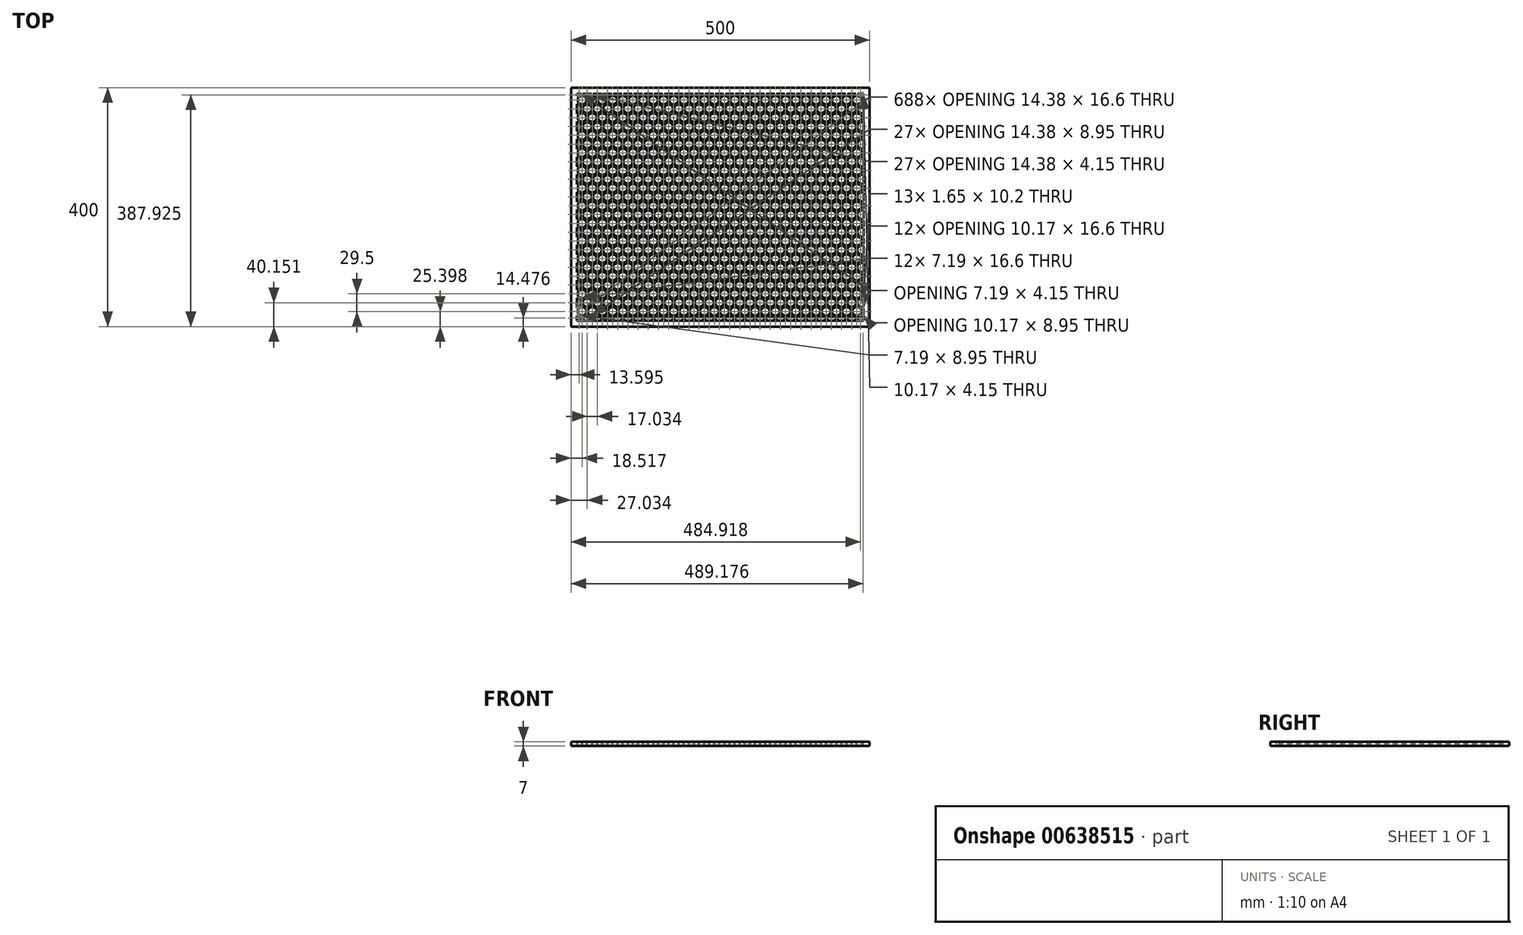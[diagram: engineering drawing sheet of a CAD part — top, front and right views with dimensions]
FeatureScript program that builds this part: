
annotation { "Feature Type Name" : "Feature", "Feature Type Description" : "" }
export const myFeature = defineFeature(function(context is Context, id is Id, definition is map)
    precondition{}
    {
        {
            var Q0;
            Q0=qCreatedBy(makeId("Top.planeOp"),FACE);
            var sketch = newSketch(context, id + "F0", { "sketchPlane" : qUnion([Q0])});
            skLineSegment(sketch, "E0.bottom", {"start": v(0, 0) * mm, "end": v(500, 0) * mm});
            skLineSegment(sketch, "E0.top", {"start": v(0, 400) * mm, "end": v(500, 400) * mm});
            skLineSegment(sketch, "E0.left", {"start": v(0, 0) * mm, "end": v(0, 400) * mm});
            skLineSegment(sketch, "E0.right", {"start": v(500, 0) * mm, "end": v(500, 400) * mm});
            skSolve(sketch);
        }
        {
            var Q0;
            Q0=makeQuery(id+"F0.imprint","IMPRINT",FACE,{"disambiguationData":[TD([[makeQuery(id+"F0.imprint","IMPRINT",EDGE,{"derivedFrom":sQuery(id+"F0.wireOp",EDGE,"E0.bottom")}),1.0]])]});
            extrude(context, id + "F1", {"entities" : qUnion([Q0]), "depth" : 7 * mm, "offsetDistance" : 25 * mm});
        }
        {
            var Q0;
            Q0=makeQuery(id+"F1.opExtrude","CAP_FACE",FACE,{"disambiguationData":[OSD([sQuery(id+"F0.wireOp",EDGE,"E0.bottom"),sQuery(id+"F0.wireOp",EDGE,"E0.top"),sQuery(id+"F0.wireOp",EDGE,"E0.left"),sQuery(id+"F0.wireOp",EDGE,"E0.right")])],"isStart":false});
            var sketch = newSketch(context, id + "F2", { "sketchPlane" : qUnion([Q0])});
            skLineSegment(sketch, "E1.0.5.0", {"start": v(28.36, 375.25) * mm, "end": v(28.36, 383.55) * mm});
            skLineSegment(sketch, "E1.0.5.1", {"start": v(52.58, 387.7) * mm, "end": v(59.77, 383.55) * mm});
            skLineSegment(sketch, "E1.0.5.3", {"start": v(25.7, 383.55) * mm, "end": v(25.7, 375.25) * mm});
            skLineSegment(sketch, "E1.0.5.4", {"start": v(52.58, 371.1) * mm, "end": v(45.4, 375.25) * mm});
            skLineSegment(sketch, "E1.0.5.5", {"start": v(18.52, 371.1) * mm, "end": v(11.33, 375.25) * mm});
            skLineSegment(sketch, "E1.0.5.6", {"start": v(35.55, 387.7) * mm, "end": v(42.74, 383.55) * mm});
            skLineSegment(sketch, "E1.0.5.7", {"start": v(11.33, 375.25) * mm, "end": v(11.33, 383.55) * mm});
            skLineSegment(sketch, "E1.0.5.8", {"start": v(59.77, 383.55) * mm, "end": v(59.77, 375.25) * mm});
            skLineSegment(sketch, "E1.0.5.9", {"start": v(42.74, 375.25) * mm, "end": v(35.55, 371.1) * mm});
            skLineSegment(sketch, "E1.0.5.10", {"start": v(45.4, 375.25) * mm, "end": v(45.4, 383.55) * mm});
            skLineSegment(sketch, "E1.0.5.12", {"start": v(28.36, 383.55) * mm, "end": v(35.55, 387.7) * mm});
            skLineSegment(sketch, "E1.0.5.19", {"start": v(11.33, 383.55) * mm, "end": v(18.52, 387.7) * mm});
            skLineSegment(sketch, "E1.0.5.24", {"start": v(25.7, 375.25) * mm, "end": v(18.52, 371.1) * mm});
            skLineSegment(sketch, "E1.0.5.25", {"start": v(45.4, 383.55) * mm, "end": v(52.58, 387.7) * mm});
            skLineSegment(sketch, "E1.0.5.26", {"start": v(18.52, 387.7) * mm, "end": v(25.7, 383.55) * mm});
            skLineSegment(sketch, "E1.0.5.27", {"start": v(59.77, 375.25) * mm, "end": v(52.58, 371.1) * mm});
            skLineSegment(sketch, "E1.0.5.28", {"start": v(35.55, 371.1) * mm, "end": v(28.36, 375.25) * mm});
            skLineSegment(sketch, "E1.0.5.29", {"start": v(42.74, 383.55) * mm, "end": v(42.74, 375.25) * mm});
            skLineSegment(sketch, "E2", {"start": v(10, 390) * mm, "end": v(10, 10) * mm});
            skLineSegment(sketch, "E3", {"start": v(490, 10) * mm, "end": v(10, 10) * mm});
            skLineSegment(sketch, "E4", {"start": v(490, 390) * mm, "end": v(490, 10) * mm});
            skLineSegment(sketch, "E5.MirrorCS", {"start": v(19.84, 390) * mm, "end": v(27.03, 385.85) * mm});
            skLineSegment(sketch, "E6.MirrorCS", {"start": v(27.03, 385.85) * mm, "end": v(34.22, 390) * mm});
            skLineSegment(sketch, "E7.MirrorCS", {"start": v(19.84, 398.3) * mm, "end": v(19.84, 390) * mm});
            skLineSegment(sketch, "E8.MirrorCS", {"start": v(27.03, 402.45) * mm, "end": v(19.84, 398.3) * mm});
            skLineSegment(sketch, "E9.MirrorCS", {"start": v(34.22, 398.3) * mm, "end": v(27.03, 402.45) * mm});
            skLineSegment(sketch, "E10.MirrorCS", {"start": v(34.22, 390) * mm, "end": v(34.22, 398.3) * mm});
            skLineSegment(sketch, "E11.MirrorCS", {"start": v(17.19, 390) * mm, "end": v(10, 385.85) * mm});
            skLineSegment(sketch, "E12.MirrorCS", {"start": v(17.19, 398.3) * mm, "end": v(17.19, 390) * mm});
            skLineSegment(sketch, "E13.MirrorCS", {"start": v(10, 402.45) * mm, "end": v(17.19, 398.3) * mm});
            skLineSegment(sketch, "E14.MirrorCS", {"start": v(2.81, 398.3) * mm, "end": v(10, 402.45) * mm});
            skLineSegment(sketch, "E15.MirrorCS", {"start": v(2.81, 390) * mm, "end": v(2.81, 398.3) * mm});
            skLineSegment(sketch, "E16.MirrorCS", {"start": v(10, 385.85) * mm, "end": v(2.81, 390) * mm});
            skLineSegment(sketch, "E17.MirrorCS", {"start": v(36.88, 390) * mm, "end": v(44.07, 385.85) * mm});
            skLineSegment(sketch, "E18.MirrorCS", {"start": v(44.07, 385.85) * mm, "end": v(51.26, 390) * mm});
            skLineSegment(sketch, "E19.MirrorCS", {"start": v(51.26, 390) * mm, "end": v(51.26, 398.3) * mm});
            skLineSegment(sketch, "E20.MirrorCS", {"start": v(51.26, 398.3) * mm, "end": v(44.07, 402.45) * mm});
            skLineSegment(sketch, "E21.MirrorCS", {"start": v(44.07, 402.45) * mm, "end": v(36.88, 398.3) * mm});
            skLineSegment(sketch, "E22.MirrorCS", {"start": v(36.88, 398.3) * mm, "end": v(36.88, 390) * mm});
            skLineSegment(sketch, "E23", {"start": v(10, 390) * mm, "end": v(490, 390) * mm});
            skLineSegment(sketch, "E24.1.0.0", {"start": v(61.1, 385.85) * mm, "end": v(53.92, 390) * mm});
            skLineSegment(sketch, "E24.1.0.2", {"start": v(95.18, 385.85) * mm, "end": v(102.37, 390) * mm});
            skLineSegment(sketch, "E24.1.0.3", {"start": v(95.18, 402.45) * mm, "end": v(87.99, 398.3) * mm});
            skLineSegment(sketch, "E24.1.0.4", {"start": v(79.47, 375.25) * mm, "end": v(79.47, 383.55) * mm});
            skLineSegment(sketch, "E24.1.0.5", {"start": v(103.7, 387.7) * mm, "end": v(110.88, 383.55) * mm});
            skLineSegment(sketch, "E24.1.0.8", {"start": v(78.14, 385.85) * mm, "end": v(85.33, 390) * mm});
            skLineSegment(sketch, "E24.1.0.9", {"start": v(61.1, 402.45) * mm, "end": v(68.3, 398.3) * mm});
            skLineSegment(sketch, "E24.1.0.10", {"start": v(79.47, 383.55) * mm, "end": v(86.66, 387.7) * mm});
            skLineSegment(sketch, "E24.1.0.11", {"start": v(110.88, 383.55) * mm, "end": v(110.88, 375.25) * mm});
            skLineSegment(sketch, "E24.1.0.13", {"start": v(87.99, 398.3) * mm, "end": v(87.99, 390) * mm});
            skLineSegment(sketch, "E24.1.0.14", {"start": v(76.82, 375.25) * mm, "end": v(69.63, 371.1) * mm});
            skLineSegment(sketch, "E24.1.0.16", {"start": v(85.33, 398.3) * mm, "end": v(78.14, 402.45) * mm});
            skLineSegment(sketch, "E24.1.0.18", {"start": v(93.85, 375.25) * mm, "end": v(86.66, 371.1) * mm});
            skLineSegment(sketch, "E24.1.0.19", {"start": v(96.5, 375.25) * mm, "end": v(96.5, 383.55) * mm});
            skLineSegment(sketch, "E24.1.0.21", {"start": v(93.85, 383.55) * mm, "end": v(93.85, 375.25) * mm});
            skLineSegment(sketch, "E24.1.0.22", {"start": v(68.3, 398.3) * mm, "end": v(68.3, 390) * mm});
            skLineSegment(sketch, "E24.1.0.25", {"start": v(102.37, 398.3) * mm, "end": v(95.18, 402.45) * mm});
            skLineSegment(sketch, "E24.1.0.26", {"start": v(76.82, 383.55) * mm, "end": v(76.82, 375.25) * mm});
            skLineSegment(sketch, "E24.1.0.27", {"start": v(103.7, 371.1) * mm, "end": v(96.5, 375.25) * mm});
            skLineSegment(sketch, "E24.1.0.28", {"start": v(102.37, 390) * mm, "end": v(102.37, 398.3) * mm});
            skLineSegment(sketch, "E24.1.0.31", {"start": v(86.66, 371.1) * mm, "end": v(79.47, 375.25) * mm});
            skLineSegment(sketch, "E24.1.0.32", {"start": v(62.44, 375.25) * mm, "end": v(62.44, 383.55) * mm});
            skLineSegment(sketch, "E24.1.0.33", {"start": v(69.63, 387.7) * mm, "end": v(76.82, 383.55) * mm});
            skLineSegment(sketch, "E24.1.0.34", {"start": v(78.14, 402.45) * mm, "end": v(70.95, 398.3) * mm});
            skLineSegment(sketch, "E24.1.0.35", {"start": v(85.33, 390) * mm, "end": v(85.33, 398.3) * mm});
            skLineSegment(sketch, "E24.1.0.36", {"start": v(110.88, 375.25) * mm, "end": v(103.7, 371.1) * mm});
            skLineSegment(sketch, "E24.1.0.37", {"start": v(87.99, 390) * mm, "end": v(95.18, 385.85) * mm});
            skLineSegment(sketch, "E24.1.0.41", {"start": v(68.3, 390) * mm, "end": v(61.1, 385.85) * mm});
            skLineSegment(sketch, "E24.1.0.42", {"start": v(53.92, 398.3) * mm, "end": v(61.1, 402.45) * mm});
            skLineSegment(sketch, "E24.1.0.43", {"start": v(70.95, 390) * mm, "end": v(78.14, 385.85) * mm});
            skLineSegment(sketch, "E24.1.0.44", {"start": v(53.92, 390) * mm, "end": v(53.92, 398.3) * mm});
            skLineSegment(sketch, "E24.1.0.46", {"start": v(70.95, 398.3) * mm, "end": v(70.95, 390) * mm});
            skLineSegment(sketch, "E24.1.0.47", {"start": v(96.5, 383.55) * mm, "end": v(103.7, 387.7) * mm});
            skLineSegment(sketch, "E24.1.0.49", {"start": v(69.63, 371.1) * mm, "end": v(62.44, 375.25) * mm});
            skLineSegment(sketch, "E24.1.0.51", {"start": v(86.66, 387.7) * mm, "end": v(93.85, 383.55) * mm});
            skLineSegment(sketch, "E24.1.0.52", {"start": v(62.44, 383.55) * mm, "end": v(69.63, 387.7) * mm});
            skLineSegment(sketch, "E24.2.0.0", {"start": v(112.22, 385.85) * mm, "end": v(105.03, 390) * mm});
            skLineSegment(sketch, "E24.2.0.2", {"start": v(146.29, 385.85) * mm, "end": v(153.48, 390) * mm});
            skLineSegment(sketch, "E24.2.0.3", {"start": v(146.29, 402.45) * mm, "end": v(139.1, 398.3) * mm});
            skLineSegment(sketch, "E24.2.0.4", {"start": v(130.58, 375.25) * mm, "end": v(130.58, 383.55) * mm});
            skLineSegment(sketch, "E24.2.0.5", {"start": v(154.8, 387.7) * mm, "end": v(162, 383.55) * mm});
            skLineSegment(sketch, "E24.2.0.8", {"start": v(129.25, 385.85) * mm, "end": v(136.44, 390) * mm});
            skLineSegment(sketch, "E24.2.0.9", {"start": v(112.22, 402.45) * mm, "end": v(119.4, 398.3) * mm});
            skLineSegment(sketch, "E24.2.0.10", {"start": v(130.58, 383.55) * mm, "end": v(137.77, 387.7) * mm});
            skLineSegment(sketch, "E24.2.0.11", {"start": v(162, 383.55) * mm, "end": v(162, 375.25) * mm});
            skLineSegment(sketch, "E24.2.0.13", {"start": v(139.1, 398.3) * mm, "end": v(139.1, 390) * mm});
            skLineSegment(sketch, "E24.2.0.14", {"start": v(127.93, 375.25) * mm, "end": v(120.74, 371.1) * mm});
            skLineSegment(sketch, "E24.2.0.16", {"start": v(136.44, 398.3) * mm, "end": v(129.25, 402.45) * mm});
            skLineSegment(sketch, "E24.2.0.18", {"start": v(144.96, 375.25) * mm, "end": v(137.77, 371.1) * mm});
            skLineSegment(sketch, "E24.2.0.19", {"start": v(147.62, 375.25) * mm, "end": v(147.62, 383.55) * mm});
            skLineSegment(sketch, "E24.2.0.21", {"start": v(144.96, 383.55) * mm, "end": v(144.96, 375.25) * mm});
            skLineSegment(sketch, "E24.2.0.22", {"start": v(119.4, 398.3) * mm, "end": v(119.4, 390) * mm});
            skLineSegment(sketch, "E24.2.0.25", {"start": v(153.48, 398.3) * mm, "end": v(146.29, 402.45) * mm});
            skLineSegment(sketch, "E24.2.0.26", {"start": v(127.93, 383.55) * mm, "end": v(127.93, 375.25) * mm});
            skLineSegment(sketch, "E24.2.0.27", {"start": v(154.8, 371.1) * mm, "end": v(147.62, 375.25) * mm});
            skLineSegment(sketch, "E24.2.0.28", {"start": v(153.48, 390) * mm, "end": v(153.48, 398.3) * mm});
            skLineSegment(sketch, "E24.2.0.31", {"start": v(137.77, 371.1) * mm, "end": v(130.58, 375.25) * mm});
            skLineSegment(sketch, "E24.2.0.32", {"start": v(113.55, 375.25) * mm, "end": v(113.55, 383.55) * mm});
            skLineSegment(sketch, "E24.2.0.33", {"start": v(120.74, 387.7) * mm, "end": v(127.93, 383.55) * mm});
            skLineSegment(sketch, "E24.2.0.34", {"start": v(129.25, 402.45) * mm, "end": v(122.06, 398.3) * mm});
            skLineSegment(sketch, "E24.2.0.35", {"start": v(136.44, 390) * mm, "end": v(136.44, 398.3) * mm});
            skLineSegment(sketch, "E24.2.0.36", {"start": v(162, 375.25) * mm, "end": v(154.8, 371.1) * mm});
            skLineSegment(sketch, "E24.2.0.37", {"start": v(139.1, 390) * mm, "end": v(146.29, 385.85) * mm});
            skLineSegment(sketch, "E24.2.0.41", {"start": v(119.4, 390) * mm, "end": v(112.22, 385.85) * mm});
            skLineSegment(sketch, "E24.2.0.42", {"start": v(105.03, 398.3) * mm, "end": v(112.22, 402.45) * mm});
            skLineSegment(sketch, "E24.2.0.43", {"start": v(122.06, 390) * mm, "end": v(129.25, 385.85) * mm});
            skLineSegment(sketch, "E24.2.0.44", {"start": v(105.03, 390) * mm, "end": v(105.03, 398.3) * mm});
            skLineSegment(sketch, "E24.2.0.46", {"start": v(122.06, 398.3) * mm, "end": v(122.06, 390) * mm});
            skLineSegment(sketch, "E24.2.0.47", {"start": v(147.62, 383.55) * mm, "end": v(154.8, 387.7) * mm});
            skLineSegment(sketch, "E24.2.0.49", {"start": v(120.74, 371.1) * mm, "end": v(113.55, 375.25) * mm});
            skLineSegment(sketch, "E24.2.0.51", {"start": v(137.77, 387.7) * mm, "end": v(144.96, 383.55) * mm});
            skLineSegment(sketch, "E24.2.0.52", {"start": v(113.55, 383.55) * mm, "end": v(120.74, 387.7) * mm});
            skLineSegment(sketch, "E24.3.0.0", {"start": v(163.33, 385.85) * mm, "end": v(156.14, 390) * mm});
            skLineSegment(sketch, "E24.3.0.2", {"start": v(197.4, 385.85) * mm, "end": v(204.59, 390) * mm});
            skLineSegment(sketch, "E24.3.0.3", {"start": v(197.4, 402.45) * mm, "end": v(190.2, 398.3) * mm});
            skLineSegment(sketch, "E24.3.0.4", {"start": v(181.7, 375.25) * mm, "end": v(181.7, 383.55) * mm});
            skLineSegment(sketch, "E24.3.0.5", {"start": v(205.91, 387.7) * mm, "end": v(213.1, 383.55) * mm});
            skLineSegment(sketch, "E24.3.0.8", {"start": v(180.36, 385.85) * mm, "end": v(187.55, 390) * mm});
            skLineSegment(sketch, "E24.3.0.9", {"start": v(163.33, 402.45) * mm, "end": v(170.52, 398.3) * mm});
            skLineSegment(sketch, "E24.3.0.10", {"start": v(181.7, 383.55) * mm, "end": v(188.88, 387.7) * mm});
            skLineSegment(sketch, "E24.3.0.11", {"start": v(213.1, 383.55) * mm, "end": v(213.1, 375.25) * mm});
            skLineSegment(sketch, "E24.3.0.13", {"start": v(190.2, 398.3) * mm, "end": v(190.2, 390) * mm});
            skLineSegment(sketch, "E24.3.0.14", {"start": v(179.04, 375.25) * mm, "end": v(171.85, 371.1) * mm});
            skLineSegment(sketch, "E24.3.0.16", {"start": v(187.55, 398.3) * mm, "end": v(180.36, 402.45) * mm});
            skLineSegment(sketch, "E24.3.0.18", {"start": v(196.07, 375.25) * mm, "end": v(188.88, 371.1) * mm});
            skLineSegment(sketch, "E24.3.0.19", {"start": v(198.73, 375.25) * mm, "end": v(198.73, 383.55) * mm});
            skLineSegment(sketch, "E24.3.0.21", {"start": v(196.07, 383.55) * mm, "end": v(196.07, 375.25) * mm});
            skLineSegment(sketch, "E24.3.0.22", {"start": v(170.52, 398.3) * mm, "end": v(170.52, 390) * mm});
            skLineSegment(sketch, "E24.3.0.25", {"start": v(204.59, 398.3) * mm, "end": v(197.4, 402.45) * mm});
            skLineSegment(sketch, "E24.3.0.26", {"start": v(179.04, 383.55) * mm, "end": v(179.04, 375.25) * mm});
            skLineSegment(sketch, "E24.3.0.27", {"start": v(205.91, 371.1) * mm, "end": v(198.73, 375.25) * mm});
            skLineSegment(sketch, "E24.3.0.28", {"start": v(204.59, 390) * mm, "end": v(204.59, 398.3) * mm});
            skLineSegment(sketch, "E24.3.0.31", {"start": v(188.88, 371.1) * mm, "end": v(181.7, 375.25) * mm});
            skLineSegment(sketch, "E24.3.0.32", {"start": v(164.66, 375.25) * mm, "end": v(164.66, 383.55) * mm});
            skLineSegment(sketch, "E24.3.0.33", {"start": v(171.85, 387.7) * mm, "end": v(179.04, 383.55) * mm});
            skLineSegment(sketch, "E24.3.0.34", {"start": v(180.36, 402.45) * mm, "end": v(173.17, 398.3) * mm});
            skLineSegment(sketch, "E24.3.0.35", {"start": v(187.55, 390) * mm, "end": v(187.55, 398.3) * mm});
            skLineSegment(sketch, "E24.3.0.36", {"start": v(213.1, 375.25) * mm, "end": v(205.91, 371.1) * mm});
            skLineSegment(sketch, "E24.3.0.37", {"start": v(190.2, 390) * mm, "end": v(197.4, 385.85) * mm});
            skLineSegment(sketch, "E24.3.0.41", {"start": v(170.52, 390) * mm, "end": v(163.33, 385.85) * mm});
            skLineSegment(sketch, "E24.3.0.42", {"start": v(156.14, 398.3) * mm, "end": v(163.33, 402.45) * mm});
            skLineSegment(sketch, "E24.3.0.43", {"start": v(173.17, 390) * mm, "end": v(180.36, 385.85) * mm});
            skLineSegment(sketch, "E24.3.0.44", {"start": v(156.14, 390) * mm, "end": v(156.14, 398.3) * mm});
            skLineSegment(sketch, "E24.3.0.46", {"start": v(173.17, 398.3) * mm, "end": v(173.17, 390) * mm});
            skLineSegment(sketch, "E24.3.0.47", {"start": v(198.73, 383.55) * mm, "end": v(205.91, 387.7) * mm});
            skLineSegment(sketch, "E24.3.0.49", {"start": v(171.85, 371.1) * mm, "end": v(164.66, 375.25) * mm});
            skLineSegment(sketch, "E24.3.0.51", {"start": v(188.88, 387.7) * mm, "end": v(196.07, 383.55) * mm});
            skLineSegment(sketch, "E24.3.0.52", {"start": v(164.66, 383.55) * mm, "end": v(171.85, 387.7) * mm});
            skLineSegment(sketch, "E24.4.0.0", {"start": v(214.44, 385.85) * mm, "end": v(207.25, 390) * mm});
            skLineSegment(sketch, "E24.4.0.2", {"start": v(248.5, 385.85) * mm, "end": v(255.7, 390) * mm});
            skLineSegment(sketch, "E24.4.0.3", {"start": v(248.5, 402.45) * mm, "end": v(241.32, 398.3) * mm});
            skLineSegment(sketch, "E24.4.0.4", {"start": v(232.8, 375.25) * mm, "end": v(232.8, 383.55) * mm});
            skLineSegment(sketch, "E24.4.0.5", {"start": v(257.02, 387.7) * mm, "end": v(264.21, 383.55) * mm});
            skLineSegment(sketch, "E24.4.0.8", {"start": v(231.47, 385.85) * mm, "end": v(238.66, 390) * mm});
            skLineSegment(sketch, "E24.4.0.9", {"start": v(214.44, 402.45) * mm, "end": v(221.63, 398.3) * mm});
            skLineSegment(sketch, "E24.4.0.10", {"start": v(232.8, 383.55) * mm, "end": v(240, 387.7) * mm});
            skLineSegment(sketch, "E24.4.0.11", {"start": v(264.21, 383.55) * mm, "end": v(264.21, 375.25) * mm});
            skLineSegment(sketch, "E24.4.0.13", {"start": v(241.32, 398.3) * mm, "end": v(241.32, 390) * mm});
            skLineSegment(sketch, "E24.4.0.14", {"start": v(230.15, 375.25) * mm, "end": v(222.96, 371.1) * mm});
            skLineSegment(sketch, "E24.4.0.16", {"start": v(238.66, 398.3) * mm, "end": v(231.47, 402.45) * mm});
            skLineSegment(sketch, "E24.4.0.18", {"start": v(247.18, 375.25) * mm, "end": v(240, 371.1) * mm});
            skLineSegment(sketch, "E24.4.0.19", {"start": v(249.84, 375.25) * mm, "end": v(249.84, 383.55) * mm});
            skLineSegment(sketch, "E24.4.0.21", {"start": v(247.18, 383.55) * mm, "end": v(247.18, 375.25) * mm});
            skLineSegment(sketch, "E24.4.0.22", {"start": v(221.63, 398.3) * mm, "end": v(221.63, 390) * mm});
            skLineSegment(sketch, "E24.4.0.25", {"start": v(255.7, 398.3) * mm, "end": v(248.5, 402.45) * mm});
            skLineSegment(sketch, "E24.4.0.26", {"start": v(230.15, 383.55) * mm, "end": v(230.15, 375.25) * mm});
            skLineSegment(sketch, "E24.4.0.27", {"start": v(257.02, 371.1) * mm, "end": v(249.84, 375.25) * mm});
            skLineSegment(sketch, "E24.4.0.28", {"start": v(255.7, 390) * mm, "end": v(255.7, 398.3) * mm});
            skLineSegment(sketch, "E24.4.0.31", {"start": v(240, 371.1) * mm, "end": v(232.8, 375.25) * mm});
            skLineSegment(sketch, "E24.4.0.32", {"start": v(215.77, 375.25) * mm, "end": v(215.77, 383.55) * mm});
            skLineSegment(sketch, "E24.4.0.33", {"start": v(222.96, 387.7) * mm, "end": v(230.15, 383.55) * mm});
            skLineSegment(sketch, "E24.4.0.34", {"start": v(231.47, 402.45) * mm, "end": v(224.28, 398.3) * mm});
            skLineSegment(sketch, "E24.4.0.35", {"start": v(238.66, 390) * mm, "end": v(238.66, 398.3) * mm});
            skLineSegment(sketch, "E24.4.0.36", {"start": v(264.21, 375.25) * mm, "end": v(257.02, 371.1) * mm});
            skLineSegment(sketch, "E24.4.0.37", {"start": v(241.32, 390) * mm, "end": v(248.5, 385.85) * mm});
            skLineSegment(sketch, "E24.4.0.41", {"start": v(221.63, 390) * mm, "end": v(214.44, 385.85) * mm});
            skLineSegment(sketch, "E24.4.0.42", {"start": v(207.25, 398.3) * mm, "end": v(214.44, 402.45) * mm});
            skLineSegment(sketch, "E24.4.0.43", {"start": v(224.28, 390) * mm, "end": v(231.47, 385.85) * mm});
            skLineSegment(sketch, "E24.4.0.44", {"start": v(207.25, 390) * mm, "end": v(207.25, 398.3) * mm});
            skLineSegment(sketch, "E24.4.0.46", {"start": v(224.28, 398.3) * mm, "end": v(224.28, 390) * mm});
            skLineSegment(sketch, "E24.4.0.47", {"start": v(249.84, 383.55) * mm, "end": v(257.02, 387.7) * mm});
            skLineSegment(sketch, "E24.4.0.49", {"start": v(222.96, 371.1) * mm, "end": v(215.77, 375.25) * mm});
            skLineSegment(sketch, "E24.4.0.51", {"start": v(240, 387.7) * mm, "end": v(247.18, 383.55) * mm});
            skLineSegment(sketch, "E24.4.0.52", {"start": v(215.77, 383.55) * mm, "end": v(222.96, 387.7) * mm});
            skLineSegment(sketch, "E24.5.0.0", {"start": v(265.55, 385.85) * mm, "end": v(258.36, 390) * mm});
            skLineSegment(sketch, "E24.5.0.2", {"start": v(299.62, 385.85) * mm, "end": v(306.8, 390) * mm});
            skLineSegment(sketch, "E24.5.0.3", {"start": v(299.62, 402.45) * mm, "end": v(292.43, 398.3) * mm});
            skLineSegment(sketch, "E24.5.0.4", {"start": v(283.91, 375.25) * mm, "end": v(283.91, 383.55) * mm});
            skLineSegment(sketch, "E24.5.0.5", {"start": v(308.13, 387.7) * mm, "end": v(315.32, 383.55) * mm});
            skLineSegment(sketch, "E24.5.0.8", {"start": v(282.58, 385.85) * mm, "end": v(289.77, 390) * mm});
            skLineSegment(sketch, "E24.5.0.9", {"start": v(265.55, 402.45) * mm, "end": v(272.74, 398.3) * mm});
            skLineSegment(sketch, "E24.5.0.10", {"start": v(283.91, 383.55) * mm, "end": v(291.1, 387.7) * mm});
            skLineSegment(sketch, "E24.5.0.11", {"start": v(315.32, 383.55) * mm, "end": v(315.32, 375.25) * mm});
            skLineSegment(sketch, "E24.5.0.13", {"start": v(292.43, 398.3) * mm, "end": v(292.43, 390) * mm});
            skLineSegment(sketch, "E24.5.0.14", {"start": v(281.26, 375.25) * mm, "end": v(274.07, 371.1) * mm});
            skLineSegment(sketch, "E24.5.0.16", {"start": v(289.77, 398.3) * mm, "end": v(282.58, 402.45) * mm});
            skLineSegment(sketch, "E24.5.0.18", {"start": v(298.29, 375.25) * mm, "end": v(291.1, 371.1) * mm});
            skLineSegment(sketch, "E24.5.0.19", {"start": v(300.95, 375.25) * mm, "end": v(300.95, 383.55) * mm});
            skLineSegment(sketch, "E24.5.0.21", {"start": v(298.29, 383.55) * mm, "end": v(298.29, 375.25) * mm});
            skLineSegment(sketch, "E24.5.0.22", {"start": v(272.74, 398.3) * mm, "end": v(272.74, 390) * mm});
            skLineSegment(sketch, "E24.5.0.25", {"start": v(306.8, 398.3) * mm, "end": v(299.62, 402.45) * mm});
            skLineSegment(sketch, "E24.5.0.26", {"start": v(281.26, 383.55) * mm, "end": v(281.26, 375.25) * mm});
            skLineSegment(sketch, "E24.5.0.27", {"start": v(308.13, 371.1) * mm, "end": v(300.95, 375.25) * mm});
            skLineSegment(sketch, "E24.5.0.28", {"start": v(306.8, 390) * mm, "end": v(306.8, 398.3) * mm});
            skLineSegment(sketch, "E24.5.0.31", {"start": v(291.1, 371.1) * mm, "end": v(283.91, 375.25) * mm});
            skLineSegment(sketch, "E24.5.0.32", {"start": v(266.88, 375.25) * mm, "end": v(266.88, 383.55) * mm});
            skLineSegment(sketch, "E24.5.0.33", {"start": v(274.07, 387.7) * mm, "end": v(281.26, 383.55) * mm});
            skLineSegment(sketch, "E24.5.0.34", {"start": v(282.58, 402.45) * mm, "end": v(275.4, 398.3) * mm});
            skLineSegment(sketch, "E24.5.0.35", {"start": v(289.77, 390) * mm, "end": v(289.77, 398.3) * mm});
            skLineSegment(sketch, "E24.5.0.36", {"start": v(315.32, 375.25) * mm, "end": v(308.13, 371.1) * mm});
            skLineSegment(sketch, "E24.5.0.37", {"start": v(292.43, 390) * mm, "end": v(299.62, 385.85) * mm});
            skLineSegment(sketch, "E24.5.0.41", {"start": v(272.74, 390) * mm, "end": v(265.55, 385.85) * mm});
            skLineSegment(sketch, "E24.5.0.42", {"start": v(258.36, 398.3) * mm, "end": v(265.55, 402.45) * mm});
            skLineSegment(sketch, "E24.5.0.43", {"start": v(275.4, 390) * mm, "end": v(282.58, 385.85) * mm});
            skLineSegment(sketch, "E24.5.0.44", {"start": v(258.36, 390) * mm, "end": v(258.36, 398.3) * mm});
            skLineSegment(sketch, "E24.5.0.46", {"start": v(275.4, 398.3) * mm, "end": v(275.4, 390) * mm});
            skLineSegment(sketch, "E24.5.0.47", {"start": v(300.95, 383.55) * mm, "end": v(308.13, 387.7) * mm});
            skLineSegment(sketch, "E24.5.0.49", {"start": v(274.07, 371.1) * mm, "end": v(266.88, 375.25) * mm});
            skLineSegment(sketch, "E24.5.0.51", {"start": v(291.1, 387.7) * mm, "end": v(298.29, 383.55) * mm});
            skLineSegment(sketch, "E24.5.0.52", {"start": v(266.88, 383.55) * mm, "end": v(274.07, 387.7) * mm});
            skLineSegment(sketch, "E24.6.0.0", {"start": v(316.66, 385.85) * mm, "end": v(309.47, 390) * mm});
            skLineSegment(sketch, "E24.6.0.2", {"start": v(350.73, 385.85) * mm, "end": v(357.92, 390) * mm});
            skLineSegment(sketch, "E24.6.0.3", {"start": v(350.73, 402.45) * mm, "end": v(343.54, 398.3) * mm});
            skLineSegment(sketch, "E24.6.0.4", {"start": v(335.02, 375.25) * mm, "end": v(335.02, 383.55) * mm});
            skLineSegment(sketch, "E24.6.0.5", {"start": v(359.24, 387.7) * mm, "end": v(366.43, 383.55) * mm});
            skLineSegment(sketch, "E24.6.0.8", {"start": v(333.7, 385.85) * mm, "end": v(340.88, 390) * mm});
            skLineSegment(sketch, "E24.6.0.9", {"start": v(316.66, 402.45) * mm, "end": v(323.85, 398.3) * mm});
            skLineSegment(sketch, "E24.6.0.10", {"start": v(335.02, 383.55) * mm, "end": v(342.21, 387.7) * mm});
            skLineSegment(sketch, "E24.6.0.11", {"start": v(366.43, 383.55) * mm, "end": v(366.43, 375.25) * mm});
            skLineSegment(sketch, "E24.6.0.13", {"start": v(343.54, 398.3) * mm, "end": v(343.54, 390) * mm});
            skLineSegment(sketch, "E24.6.0.14", {"start": v(332.37, 375.25) * mm, "end": v(325.18, 371.1) * mm});
            skLineSegment(sketch, "E24.6.0.16", {"start": v(340.88, 398.3) * mm, "end": v(333.7, 402.45) * mm});
            skLineSegment(sketch, "E24.6.0.18", {"start": v(349.4, 375.25) * mm, "end": v(342.21, 371.1) * mm});
            skLineSegment(sketch, "E24.6.0.19", {"start": v(352.06, 375.25) * mm, "end": v(352.06, 383.55) * mm});
            skLineSegment(sketch, "E24.6.0.21", {"start": v(349.4, 383.55) * mm, "end": v(349.4, 375.25) * mm});
            skLineSegment(sketch, "E24.6.0.22", {"start": v(323.85, 398.3) * mm, "end": v(323.85, 390) * mm});
            skLineSegment(sketch, "E24.6.0.25", {"start": v(357.92, 398.3) * mm, "end": v(350.73, 402.45) * mm});
            skLineSegment(sketch, "E24.6.0.26", {"start": v(332.37, 383.55) * mm, "end": v(332.37, 375.25) * mm});
            skLineSegment(sketch, "E24.6.0.27", {"start": v(359.24, 371.1) * mm, "end": v(352.06, 375.25) * mm});
            skLineSegment(sketch, "E24.6.0.28", {"start": v(357.92, 390) * mm, "end": v(357.92, 398.3) * mm});
            skLineSegment(sketch, "E24.6.0.31", {"start": v(342.21, 371.1) * mm, "end": v(335.02, 375.25) * mm});
            skLineSegment(sketch, "E24.6.0.32", {"start": v(317.99, 375.25) * mm, "end": v(317.99, 383.55) * mm});
            skLineSegment(sketch, "E24.6.0.33", {"start": v(325.18, 387.7) * mm, "end": v(332.37, 383.55) * mm});
            skLineSegment(sketch, "E24.6.0.34", {"start": v(333.7, 402.45) * mm, "end": v(326.5, 398.3) * mm});
            skLineSegment(sketch, "E24.6.0.35", {"start": v(340.88, 390) * mm, "end": v(340.88, 398.3) * mm});
            skLineSegment(sketch, "E24.6.0.36", {"start": v(366.43, 375.25) * mm, "end": v(359.24, 371.1) * mm});
            skLineSegment(sketch, "E24.6.0.37", {"start": v(343.54, 390) * mm, "end": v(350.73, 385.85) * mm});
            skLineSegment(sketch, "E24.6.0.41", {"start": v(323.85, 390) * mm, "end": v(316.66, 385.85) * mm});
            skLineSegment(sketch, "E24.6.0.42", {"start": v(309.47, 398.3) * mm, "end": v(316.66, 402.45) * mm});
            skLineSegment(sketch, "E24.6.0.43", {"start": v(326.5, 390) * mm, "end": v(333.7, 385.85) * mm});
            skLineSegment(sketch, "E24.6.0.44", {"start": v(309.47, 390) * mm, "end": v(309.47, 398.3) * mm});
            skLineSegment(sketch, "E24.6.0.46", {"start": v(326.5, 398.3) * mm, "end": v(326.5, 390) * mm});
            skLineSegment(sketch, "E24.6.0.47", {"start": v(352.06, 383.55) * mm, "end": v(359.24, 387.7) * mm});
            skLineSegment(sketch, "E24.6.0.49", {"start": v(325.18, 371.1) * mm, "end": v(317.99, 375.25) * mm});
            skLineSegment(sketch, "E24.6.0.51", {"start": v(342.21, 387.7) * mm, "end": v(349.4, 383.55) * mm});
            skLineSegment(sketch, "E24.6.0.52", {"start": v(317.99, 383.55) * mm, "end": v(325.18, 387.7) * mm});
            skLineSegment(sketch, "E24.7.0.0", {"start": v(367.77, 385.85) * mm, "end": v(360.58, 390) * mm});
            skLineSegment(sketch, "E24.7.0.2", {"start": v(401.84, 385.85) * mm, "end": v(409.03, 390) * mm});
            skLineSegment(sketch, "E24.7.0.3", {"start": v(401.84, 402.45) * mm, "end": v(394.65, 398.3) * mm});
            skLineSegment(sketch, "E24.7.0.4", {"start": v(386.13, 375.25) * mm, "end": v(386.13, 383.55) * mm});
            skLineSegment(sketch, "E24.7.0.5", {"start": v(410.35, 387.7) * mm, "end": v(417.54, 383.55) * mm});
            skLineSegment(sketch, "E24.7.0.8", {"start": v(384.8, 385.85) * mm, "end": v(392, 390) * mm});
            skLineSegment(sketch, "E24.7.0.9", {"start": v(367.77, 402.45) * mm, "end": v(374.96, 398.3) * mm});
            skLineSegment(sketch, "E24.7.0.10", {"start": v(386.13, 383.55) * mm, "end": v(393.32, 387.7) * mm});
            skLineSegment(sketch, "E24.7.0.11", {"start": v(417.54, 383.55) * mm, "end": v(417.54, 375.25) * mm});
            skLineSegment(sketch, "E24.7.0.13", {"start": v(394.65, 398.3) * mm, "end": v(394.65, 390) * mm});
            skLineSegment(sketch, "E24.7.0.14", {"start": v(383.48, 375.25) * mm, "end": v(376.29, 371.1) * mm});
            skLineSegment(sketch, "E24.7.0.16", {"start": v(392, 398.3) * mm, "end": v(384.8, 402.45) * mm});
            skLineSegment(sketch, "E24.7.0.18", {"start": v(400.5, 375.25) * mm, "end": v(393.32, 371.1) * mm});
            skLineSegment(sketch, "E24.7.0.19", {"start": v(403.17, 375.25) * mm, "end": v(403.17, 383.55) * mm});
            skLineSegment(sketch, "E24.7.0.21", {"start": v(400.5, 383.55) * mm, "end": v(400.5, 375.25) * mm});
            skLineSegment(sketch, "E24.7.0.22", {"start": v(374.96, 398.3) * mm, "end": v(374.96, 390) * mm});
            skLineSegment(sketch, "E24.7.0.25", {"start": v(409.03, 398.3) * mm, "end": v(401.84, 402.45) * mm});
            skLineSegment(sketch, "E24.7.0.26", {"start": v(383.48, 383.55) * mm, "end": v(383.48, 375.25) * mm});
            skLineSegment(sketch, "E24.7.0.27", {"start": v(410.35, 371.1) * mm, "end": v(403.17, 375.25) * mm});
            skLineSegment(sketch, "E24.7.0.28", {"start": v(409.03, 390) * mm, "end": v(409.03, 398.3) * mm});
            skLineSegment(sketch, "E24.7.0.31", {"start": v(393.32, 371.1) * mm, "end": v(386.13, 375.25) * mm});
            skLineSegment(sketch, "E24.7.0.32", {"start": v(369.1, 375.25) * mm, "end": v(369.1, 383.55) * mm});
            skLineSegment(sketch, "E24.7.0.33", {"start": v(376.29, 387.7) * mm, "end": v(383.48, 383.55) * mm});
            skLineSegment(sketch, "E24.7.0.34", {"start": v(384.8, 402.45) * mm, "end": v(377.61, 398.3) * mm});
            skLineSegment(sketch, "E24.7.0.35", {"start": v(392, 390) * mm, "end": v(392, 398.3) * mm});
            skLineSegment(sketch, "E24.7.0.36", {"start": v(417.54, 375.25) * mm, "end": v(410.35, 371.1) * mm});
            skLineSegment(sketch, "E24.7.0.37", {"start": v(394.65, 390) * mm, "end": v(401.84, 385.85) * mm});
            skLineSegment(sketch, "E24.7.0.41", {"start": v(374.96, 390) * mm, "end": v(367.77, 385.85) * mm});
            skLineSegment(sketch, "E24.7.0.42", {"start": v(360.58, 398.3) * mm, "end": v(367.77, 402.45) * mm});
            skLineSegment(sketch, "E24.7.0.43", {"start": v(377.61, 390) * mm, "end": v(384.8, 385.85) * mm});
            skLineSegment(sketch, "E24.7.0.44", {"start": v(360.58, 390) * mm, "end": v(360.58, 398.3) * mm});
            skLineSegment(sketch, "E24.7.0.46", {"start": v(377.61, 398.3) * mm, "end": v(377.61, 390) * mm});
            skLineSegment(sketch, "E24.7.0.47", {"start": v(403.17, 383.55) * mm, "end": v(410.35, 387.7) * mm});
            skLineSegment(sketch, "E24.7.0.49", {"start": v(376.29, 371.1) * mm, "end": v(369.1, 375.25) * mm});
            skLineSegment(sketch, "E24.7.0.51", {"start": v(393.32, 387.7) * mm, "end": v(400.5, 383.55) * mm});
            skLineSegment(sketch, "E24.7.0.52", {"start": v(369.1, 383.55) * mm, "end": v(376.29, 387.7) * mm});
            skLineSegment(sketch, "E24.8.0.0", {"start": v(418.88, 385.85) * mm, "end": v(411.7, 390) * mm});
            skLineSegment(sketch, "E24.8.0.2", {"start": v(452.95, 385.85) * mm, "end": v(460.14, 390) * mm});
            skLineSegment(sketch, "E24.8.0.3", {"start": v(452.95, 402.45) * mm, "end": v(445.76, 398.3) * mm});
            skLineSegment(sketch, "E24.8.0.4", {"start": v(437.24, 375.25) * mm, "end": v(437.24, 383.55) * mm});
            skLineSegment(sketch, "E24.8.0.5", {"start": v(461.46, 387.7) * mm, "end": v(468.65, 383.55) * mm});
            skLineSegment(sketch, "E24.8.0.8", {"start": v(435.91, 385.85) * mm, "end": v(443.1, 390) * mm});
            skLineSegment(sketch, "E24.8.0.9", {"start": v(418.88, 402.45) * mm, "end": v(426.07, 398.3) * mm});
            skLineSegment(sketch, "E24.8.0.10", {"start": v(437.24, 383.55) * mm, "end": v(444.43, 387.7) * mm});
            skLineSegment(sketch, "E24.8.0.11", {"start": v(468.65, 383.55) * mm, "end": v(468.65, 375.25) * mm});
            skLineSegment(sketch, "E24.8.0.13", {"start": v(445.76, 398.3) * mm, "end": v(445.76, 390) * mm});
            skLineSegment(sketch, "E24.8.0.14", {"start": v(434.59, 375.25) * mm, "end": v(427.4, 371.1) * mm});
            skLineSegment(sketch, "E24.8.0.16", {"start": v(443.1, 398.3) * mm, "end": v(435.91, 402.45) * mm});
            skLineSegment(sketch, "E24.8.0.18", {"start": v(451.62, 375.25) * mm, "end": v(444.43, 371.1) * mm});
            skLineSegment(sketch, "E24.8.0.19", {"start": v(454.28, 375.25) * mm, "end": v(454.28, 383.55) * mm});
            skLineSegment(sketch, "E24.8.0.21", {"start": v(451.62, 383.55) * mm, "end": v(451.62, 375.25) * mm});
            skLineSegment(sketch, "E24.8.0.22", {"start": v(426.07, 398.3) * mm, "end": v(426.07, 390) * mm});
            skLineSegment(sketch, "E24.8.0.25", {"start": v(460.14, 398.3) * mm, "end": v(452.95, 402.45) * mm});
            skLineSegment(sketch, "E24.8.0.26", {"start": v(434.59, 383.55) * mm, "end": v(434.59, 375.25) * mm});
            skLineSegment(sketch, "E24.8.0.27", {"start": v(461.46, 371.1) * mm, "end": v(454.28, 375.25) * mm});
            skLineSegment(sketch, "E24.8.0.28", {"start": v(460.14, 390) * mm, "end": v(460.14, 398.3) * mm});
            skLineSegment(sketch, "E24.8.0.31", {"start": v(444.43, 371.1) * mm, "end": v(437.24, 375.25) * mm});
            skLineSegment(sketch, "E24.8.0.32", {"start": v(420.2, 375.25) * mm, "end": v(420.2, 383.55) * mm});
            skLineSegment(sketch, "E24.8.0.33", {"start": v(427.4, 387.7) * mm, "end": v(434.59, 383.55) * mm});
            skLineSegment(sketch, "E24.8.0.34", {"start": v(435.91, 402.45) * mm, "end": v(428.72, 398.3) * mm});
            skLineSegment(sketch, "E24.8.0.35", {"start": v(443.1, 390) * mm, "end": v(443.1, 398.3) * mm});
            skLineSegment(sketch, "E24.8.0.36", {"start": v(468.65, 375.25) * mm, "end": v(461.46, 371.1) * mm});
            skLineSegment(sketch, "E24.8.0.37", {"start": v(445.76, 390) * mm, "end": v(452.95, 385.85) * mm});
            skLineSegment(sketch, "E24.8.0.41", {"start": v(426.07, 390) * mm, "end": v(418.88, 385.85) * mm});
            skLineSegment(sketch, "E24.8.0.42", {"start": v(411.7, 398.3) * mm, "end": v(418.88, 402.45) * mm});
            skLineSegment(sketch, "E24.8.0.43", {"start": v(428.72, 390) * mm, "end": v(435.91, 385.85) * mm});
            skLineSegment(sketch, "E24.8.0.44", {"start": v(411.7, 390) * mm, "end": v(411.7, 398.3) * mm});
            skLineSegment(sketch, "E24.8.0.46", {"start": v(428.72, 398.3) * mm, "end": v(428.72, 390) * mm});
            skLineSegment(sketch, "E24.8.0.47", {"start": v(454.28, 383.55) * mm, "end": v(461.46, 387.7) * mm});
            skLineSegment(sketch, "E24.8.0.49", {"start": v(427.4, 371.1) * mm, "end": v(420.2, 375.25) * mm});
            skLineSegment(sketch, "E24.8.0.51", {"start": v(444.43, 387.7) * mm, "end": v(451.62, 383.55) * mm});
            skLineSegment(sketch, "E24.8.0.52", {"start": v(420.2, 383.55) * mm, "end": v(427.4, 387.7) * mm});
            skLineSegment(sketch, "E24.9.0.0", {"start": v(469.99, 385.85) * mm, "end": v(462.8, 390) * mm});
            skLineSegment(sketch, "E24.9.0.2", {"start": v(504.06, 385.85) * mm, "end": v(511.25, 390) * mm});
            skLineSegment(sketch, "E24.9.0.3", {"start": v(504.06, 402.45) * mm, "end": v(496.87, 398.3) * mm});
            skLineSegment(sketch, "E24.9.0.4", {"start": v(488.35, 375.25) * mm, "end": v(488.35, 383.55) * mm});
            skLineSegment(sketch, "E24.9.0.5", {"start": v(512.57, 387.7) * mm, "end": v(519.76, 383.55) * mm});
            skLineSegment(sketch, "E24.9.0.8", {"start": v(487.02, 385.85) * mm, "end": v(494.21, 390) * mm});
            skLineSegment(sketch, "E24.9.0.9", {"start": v(469.99, 402.45) * mm, "end": v(477.18, 398.3) * mm});
            skLineSegment(sketch, "E24.9.0.10", {"start": v(488.35, 383.55) * mm, "end": v(495.54, 387.7) * mm});
            skLineSegment(sketch, "E24.9.0.11", {"start": v(519.76, 383.55) * mm, "end": v(519.76, 375.25) * mm});
            skLineSegment(sketch, "E24.9.0.13", {"start": v(496.87, 398.3) * mm, "end": v(496.87, 390) * mm});
            skLineSegment(sketch, "E24.9.0.14", {"start": v(485.7, 375.25) * mm, "end": v(478.5, 371.1) * mm});
            skLineSegment(sketch, "E24.9.0.16", {"start": v(494.21, 398.3) * mm, "end": v(487.02, 402.45) * mm});
            skLineSegment(sketch, "E24.9.0.18", {"start": v(502.73, 375.25) * mm, "end": v(495.54, 371.1) * mm});
            skLineSegment(sketch, "E24.9.0.19", {"start": v(505.39, 375.25) * mm, "end": v(505.39, 383.55) * mm});
            skLineSegment(sketch, "E24.9.0.21", {"start": v(502.73, 383.55) * mm, "end": v(502.73, 375.25) * mm});
            skLineSegment(sketch, "E24.9.0.22", {"start": v(477.18, 398.3) * mm, "end": v(477.18, 390) * mm});
            skLineSegment(sketch, "E24.9.0.25", {"start": v(511.25, 398.3) * mm, "end": v(504.06, 402.45) * mm});
            skLineSegment(sketch, "E24.9.0.26", {"start": v(485.7, 383.55) * mm, "end": v(485.7, 375.25) * mm});
            skLineSegment(sketch, "E24.9.0.27", {"start": v(512.57, 371.1) * mm, "end": v(505.39, 375.25) * mm});
            skLineSegment(sketch, "E24.9.0.28", {"start": v(511.25, 390) * mm, "end": v(511.25, 398.3) * mm});
            skLineSegment(sketch, "E24.9.0.31", {"start": v(495.54, 371.1) * mm, "end": v(488.35, 375.25) * mm});
            skLineSegment(sketch, "E24.9.0.32", {"start": v(471.32, 375.25) * mm, "end": v(471.32, 383.55) * mm});
            skLineSegment(sketch, "E24.9.0.33", {"start": v(478.5, 387.7) * mm, "end": v(485.7, 383.55) * mm});
            skLineSegment(sketch, "E24.9.0.34", {"start": v(487.02, 402.45) * mm, "end": v(479.83, 398.3) * mm});
            skLineSegment(sketch, "E24.9.0.35", {"start": v(494.21, 390) * mm, "end": v(494.21, 398.3) * mm});
            skLineSegment(sketch, "E24.9.0.36", {"start": v(519.76, 375.25) * mm, "end": v(512.57, 371.1) * mm});
            skLineSegment(sketch, "E24.9.0.37", {"start": v(496.87, 390) * mm, "end": v(504.06, 385.85) * mm});
            skLineSegment(sketch, "E24.9.0.41", {"start": v(477.18, 390) * mm, "end": v(469.99, 385.85) * mm});
            skLineSegment(sketch, "E24.9.0.42", {"start": v(462.8, 398.3) * mm, "end": v(469.99, 402.45) * mm});
            skLineSegment(sketch, "E24.9.0.43", {"start": v(479.83, 390) * mm, "end": v(487.02, 385.85) * mm});
            skLineSegment(sketch, "E24.9.0.44", {"start": v(462.8, 390) * mm, "end": v(462.8, 398.3) * mm});
            skLineSegment(sketch, "E24.9.0.46", {"start": v(479.83, 398.3) * mm, "end": v(479.83, 390) * mm});
            skLineSegment(sketch, "E24.9.0.47", {"start": v(505.39, 383.55) * mm, "end": v(512.57, 387.7) * mm});
            skLineSegment(sketch, "E24.9.0.49", {"start": v(478.5, 371.1) * mm, "end": v(471.32, 375.25) * mm});
            skLineSegment(sketch, "E24.9.0.51", {"start": v(495.54, 387.7) * mm, "end": v(502.73, 383.55) * mm});
            skLineSegment(sketch, "E24.9.0.52", {"start": v(471.32, 383.55) * mm, "end": v(478.5, 387.7) * mm});
            skLineSegment(sketch, "E25.0.1.0", {"start": v(332.37, 345.75) * mm, "end": v(325.18, 341.6) * mm});
            skLineSegment(sketch, "E25.0.1.1", {"start": v(511.25, 368.8) * mm, "end": v(504.06, 372.95) * mm});
            skLineSegment(sketch, "E25.0.1.2", {"start": v(2.81, 368.8) * mm, "end": v(10, 372.95) * mm});
            skLineSegment(sketch, "E25.0.1.3", {"start": v(127.93, 345.75) * mm, "end": v(120.74, 341.6) * mm});
            skLineSegment(sketch, "E25.0.1.4", {"start": v(512.57, 341.6) * mm, "end": v(505.39, 345.75) * mm});
            skLineSegment(sketch, "E25.0.1.5", {"start": v(519.76, 345.75) * mm, "end": v(512.57, 341.6) * mm});
            skLineSegment(sketch, "E25.0.1.6", {"start": v(25.7, 345.75) * mm, "end": v(18.52, 341.6) * mm});
            skLineSegment(sketch, "E25.0.1.7", {"start": v(11.33, 345.75) * mm, "end": v(11.33, 354.05) * mm});
            skLineSegment(sketch, "E25.0.1.8", {"start": v(18.52, 341.6) * mm, "end": v(11.33, 345.75) * mm});
            skLineSegment(sketch, "E25.0.1.9", {"start": v(519.76, 354.05) * mm, "end": v(519.76, 345.75) * mm});
            skLineSegment(sketch, "E25.0.1.10", {"start": v(76.82, 345.75) * mm, "end": v(69.63, 341.6) * mm});
            skLineSegment(sketch, "E25.0.1.11", {"start": v(112.22, 372.95) * mm, "end": v(119.4, 368.8) * mm});
            skLineSegment(sketch, "E25.0.1.12", {"start": v(205.91, 341.6) * mm, "end": v(198.73, 345.75) * mm});
            skLineSegment(sketch, "E25.0.1.13", {"start": v(197.4, 372.95) * mm, "end": v(190.2, 368.8) * mm});
            skLineSegment(sketch, "E25.0.1.14", {"start": v(93.85, 345.75) * mm, "end": v(86.66, 341.6) * mm});
            skLineSegment(sketch, "E25.0.1.15", {"start": v(129.25, 372.95) * mm, "end": v(122.06, 368.8) * mm});
            skLineSegment(sketch, "E25.0.1.16", {"start": v(298.29, 345.75) * mm, "end": v(291.1, 341.6) * mm});
            skLineSegment(sketch, "E25.0.1.17", {"start": v(502.73, 345.75) * mm, "end": v(495.54, 341.6) * mm});
            skLineSegment(sketch, "E25.0.1.18", {"start": v(289.77, 368.8) * mm, "end": v(282.58, 372.95) * mm});
            skLineSegment(sketch, "E25.0.1.19", {"start": v(85.33, 368.8) * mm, "end": v(78.14, 372.95) * mm});
            skLineSegment(sketch, "E25.0.1.20", {"start": v(494.21, 368.8) * mm, "end": v(487.02, 372.95) * mm});
            skLineSegment(sketch, "E25.0.1.21", {"start": v(333.7, 372.95) * mm, "end": v(326.5, 368.8) * mm});
            skLineSegment(sketch, "E25.0.1.22", {"start": v(95.18, 372.95) * mm, "end": v(87.99, 368.8) * mm});
            skLineSegment(sketch, "E25.0.1.23", {"start": v(478.5, 341.6) * mm, "end": v(471.32, 345.75) * mm});
            skLineSegment(sketch, "E25.0.1.24", {"start": v(274.07, 341.6) * mm, "end": v(266.88, 345.75) * mm});
            skLineSegment(sketch, "E25.0.1.25", {"start": v(444.43, 341.6) * mm, "end": v(437.24, 345.75) * mm});
            skLineSegment(sketch, "E25.0.1.26", {"start": v(401.84, 372.95) * mm, "end": v(394.65, 368.8) * mm});
            skLineSegment(sketch, "E25.0.1.27", {"start": v(410.35, 341.6) * mm, "end": v(403.17, 345.75) * mm});
            skLineSegment(sketch, "E25.0.1.28", {"start": v(468.65, 345.75) * mm, "end": v(461.46, 341.6) * mm});
            skLineSegment(sketch, "E25.0.1.29", {"start": v(427.4, 341.6) * mm, "end": v(420.2, 345.75) * mm});
            skLineSegment(sketch, "E25.0.1.30", {"start": v(59.77, 345.75) * mm, "end": v(52.58, 341.6) * mm});
            skLineSegment(sketch, "E25.0.1.31", {"start": v(512.57, 358.2) * mm, "end": v(519.76, 354.05) * mm});
            skLineSegment(sketch, "E25.0.1.32", {"start": v(196.07, 345.75) * mm, "end": v(188.88, 341.6) * mm});
            skLineSegment(sketch, "E25.0.1.33", {"start": v(86.66, 341.6) * mm, "end": v(79.47, 345.75) * mm});
            skLineSegment(sketch, "E25.0.1.34", {"start": v(400.5, 345.75) * mm, "end": v(393.32, 341.6) * mm});
            skLineSegment(sketch, "E25.0.1.35", {"start": v(103.7, 341.6) * mm, "end": v(96.5, 345.75) * mm});
            skLineSegment(sketch, "E25.0.1.36", {"start": v(299.62, 372.95) * mm, "end": v(292.43, 368.8) * mm});
            skLineSegment(sketch, "E25.0.1.37", {"start": v(504.06, 372.95) * mm, "end": v(496.87, 368.8) * mm});
            skLineSegment(sketch, "E25.0.1.38", {"start": v(2.81, 360.5) * mm, "end": v(2.81, 368.8) * mm});
            skLineSegment(sketch, "E25.0.1.39", {"start": v(308.13, 341.6) * mm, "end": v(300.95, 345.75) * mm});
            skLineSegment(sketch, "E25.0.1.40", {"start": v(417.54, 345.75) * mm, "end": v(410.35, 341.6) * mm});
            skLineSegment(sketch, "E25.0.1.41", {"start": v(434.59, 345.75) * mm, "end": v(427.4, 341.6) * mm});
            skLineSegment(sketch, "E25.0.1.42", {"start": v(62.44, 345.75) * mm, "end": v(62.44, 354.05) * mm});
            skLineSegment(sketch, "E25.0.1.43", {"start": v(69.63, 341.6) * mm, "end": v(62.44, 345.75) * mm});
            skLineSegment(sketch, "E25.0.1.44", {"start": v(325.18, 341.6) * mm, "end": v(317.99, 345.75) * mm});
            skLineSegment(sketch, "E25.0.1.45", {"start": v(264.21, 345.75) * mm, "end": v(257.02, 341.6) * mm});
            skLineSegment(sketch, "E25.0.1.46", {"start": v(120.74, 341.6) * mm, "end": v(113.55, 345.75) * mm});
            skLineSegment(sketch, "E25.0.1.47", {"start": v(502.73, 354.05) * mm, "end": v(502.73, 345.75) * mm});
            skLineSegment(sketch, "E25.0.1.48", {"start": v(316.66, 372.95) * mm, "end": v(323.85, 368.8) * mm});
            skLineSegment(sketch, "E25.0.1.49", {"start": v(505.39, 345.75) * mm, "end": v(505.39, 354.05) * mm});
            skLineSegment(sketch, "E25.0.1.50", {"start": v(10, 356.35) * mm, "end": v(2.81, 360.5) * mm});
            skLineSegment(sketch, "E25.0.1.51", {"start": v(59.77, 354.05) * mm, "end": v(59.77, 345.75) * mm});
            skLineSegment(sketch, "E25.0.1.52", {"start": v(291.1, 341.6) * mm, "end": v(283.91, 345.75) * mm});
            skLineSegment(sketch, "E25.0.1.53", {"start": v(511.25, 360.5) * mm, "end": v(511.25, 368.8) * mm});
            skLineSegment(sketch, "E25.0.1.54", {"start": v(392, 368.8) * mm, "end": v(384.8, 372.95) * mm});
            skLineSegment(sketch, "E25.0.1.55", {"start": v(187.55, 368.8) * mm, "end": v(180.36, 372.95) * mm});
            skLineSegment(sketch, "E25.0.1.56", {"start": v(247.18, 354.05) * mm, "end": v(247.18, 345.75) * mm});
            skLineSegment(sketch, "E25.0.1.57", {"start": v(188.88, 358.2) * mm, "end": v(196.07, 354.05) * mm});
            skLineSegment(sketch, "E25.0.1.58", {"start": v(369.1, 354.05) * mm, "end": v(376.29, 358.2) * mm});
            skLineSegment(sketch, "E25.0.1.59", {"start": v(409.03, 360.5) * mm, "end": v(409.03, 368.8) * mm});
            skLineSegment(sketch, "E25.0.1.60", {"start": v(188.88, 341.6) * mm, "end": v(181.7, 345.75) * mm});
            skLineSegment(sketch, "E25.0.1.61", {"start": v(204.59, 360.5) * mm, "end": v(204.59, 368.8) * mm});
            skLineSegment(sketch, "E25.0.1.62", {"start": v(164.66, 354.05) * mm, "end": v(171.85, 358.2) * mm});
            skLineSegment(sketch, "E25.0.1.63", {"start": v(230.15, 354.05) * mm, "end": v(230.15, 345.75) * mm});
            skLineSegment(sketch, "E25.0.1.64", {"start": v(343.54, 368.8) * mm, "end": v(343.54, 360.5) * mm});
            skLineSegment(sketch, "E25.0.1.65", {"start": v(139.1, 368.8) * mm, "end": v(139.1, 360.5) * mm});
            skLineSegment(sketch, "E25.0.1.66", {"start": v(70.95, 360.5) * mm, "end": v(78.14, 356.35) * mm});
            skLineSegment(sketch, "E25.0.1.67", {"start": v(96.5, 345.75) * mm, "end": v(96.5, 354.05) * mm});
            skLineSegment(sketch, "E25.0.1.68", {"start": v(44.07, 372.95) * mm, "end": v(36.88, 368.8) * mm});
            skLineSegment(sketch, "E25.0.1.69", {"start": v(162, 345.75) * mm, "end": v(154.8, 341.6) * mm});
            skLineSegment(sketch, "E25.0.1.70", {"start": v(300.95, 345.75) * mm, "end": v(300.95, 354.05) * mm});
            skLineSegment(sketch, "E25.0.1.71", {"start": v(222.96, 341.6) * mm, "end": v(215.77, 345.75) * mm});
            skLineSegment(sketch, "E25.0.1.72", {"start": v(452.95, 356.35) * mm, "end": v(460.14, 360.5) * mm});
            skLineSegment(sketch, "E25.0.1.73", {"start": v(369.1, 345.75) * mm, "end": v(369.1, 354.05) * mm});
            skLineSegment(sketch, "E25.0.1.74", {"start": v(366.43, 345.75) * mm, "end": v(359.24, 341.6) * mm});
            skLineSegment(sketch, "E25.0.1.75", {"start": v(164.66, 345.75) * mm, "end": v(164.66, 354.05) * mm});
            skLineSegment(sketch, "E25.0.1.76", {"start": v(248.5, 356.35) * mm, "end": v(255.7, 360.5) * mm});
            skLineSegment(sketch, "E25.0.1.77", {"start": v(249.84, 354.05) * mm, "end": v(257.02, 358.2) * mm});
            skLineSegment(sketch, "E25.0.1.78", {"start": v(393.32, 341.6) * mm, "end": v(386.13, 345.75) * mm});
            skLineSegment(sketch, "E25.0.1.79", {"start": v(62.44, 354.05) * mm, "end": v(69.63, 358.2) * mm});
            skLineSegment(sketch, "E25.0.1.80", {"start": v(136.44, 360.5) * mm, "end": v(136.44, 368.8) * mm});
            skLineSegment(sketch, "E25.0.1.81", {"start": v(102.37, 360.5) * mm, "end": v(102.37, 368.8) * mm});
            skLineSegment(sketch, "E25.0.1.82", {"start": v(418.88, 372.95) * mm, "end": v(426.07, 368.8) * mm});
            skLineSegment(sketch, "E25.0.1.83", {"start": v(454.28, 354.05) * mm, "end": v(461.46, 358.2) * mm});
            skLineSegment(sketch, "E25.0.1.84", {"start": v(78.14, 372.95) * mm, "end": v(70.95, 368.8) * mm});
            skLineSegment(sketch, "E25.0.1.85", {"start": v(105.03, 360.5) * mm, "end": v(105.03, 368.8) * mm});
            skLineSegment(sketch, "E25.0.1.86", {"start": v(190.2, 360.5) * mm, "end": v(197.4, 356.35) * mm});
            skLineSegment(sketch, "E25.0.1.87", {"start": v(352.06, 345.75) * mm, "end": v(352.06, 354.05) * mm});
            skLineSegment(sketch, "E25.0.1.88", {"start": v(400.5, 354.05) * mm, "end": v(400.5, 345.75) * mm});
            skLineSegment(sketch, "E25.0.1.89", {"start": v(299.62, 356.35) * mm, "end": v(306.8, 360.5) * mm});
            skLineSegment(sketch, "E25.0.1.90", {"start": v(190.2, 368.8) * mm, "end": v(190.2, 360.5) * mm});
            skLineSegment(sketch, "E25.0.1.91", {"start": v(76.82, 354.05) * mm, "end": v(76.82, 345.75) * mm});
            skLineSegment(sketch, "E25.0.1.92", {"start": v(392, 360.5) * mm, "end": v(392, 368.8) * mm});
            skLineSegment(sketch, "E25.0.1.93", {"start": v(309.47, 368.8) * mm, "end": v(316.66, 372.95) * mm});
            skLineSegment(sketch, "E25.0.1.94", {"start": v(349.4, 345.75) * mm, "end": v(342.21, 341.6) * mm});
            skLineSegment(sketch, "E25.0.1.95", {"start": v(257.02, 358.2) * mm, "end": v(264.21, 354.05) * mm});
            skLineSegment(sketch, "E25.0.1.96", {"start": v(61.1, 372.95) * mm, "end": v(68.3, 368.8) * mm});
            skLineSegment(sketch, "E25.0.1.97", {"start": v(146.29, 372.95) * mm, "end": v(139.1, 368.8) * mm});
            skLineSegment(sketch, "E25.0.1.98", {"start": v(154.8, 341.6) * mm, "end": v(147.62, 345.75) * mm});
            skLineSegment(sketch, "E25.0.1.99", {"start": v(306.8, 368.8) * mm, "end": v(299.62, 372.95) * mm});
            skLineSegment(sketch, "E25.0.1.100", {"start": v(87.99, 360.5) * mm, "end": v(95.18, 356.35) * mm});
            skLineSegment(sketch, "E25.0.1.101", {"start": v(105.03, 368.8) * mm, "end": v(112.22, 372.95) * mm});
            skLineSegment(sketch, "E25.0.1.102", {"start": v(102.37, 368.8) * mm, "end": v(95.18, 372.95) * mm});
            skLineSegment(sketch, "E25.0.1.103", {"start": v(187.55, 360.5) * mm, "end": v(187.55, 368.8) * mm});
            skLineSegment(sketch, "E25.0.1.104", {"start": v(61.1, 356.35) * mm, "end": v(53.92, 360.5) * mm});
            skLineSegment(sketch, "E25.0.1.105", {"start": v(437.24, 345.75) * mm, "end": v(437.24, 354.05) * mm});
            skLineSegment(sketch, "E25.0.1.106", {"start": v(393.32, 358.2) * mm, "end": v(400.5, 354.05) * mm});
            skLineSegment(sketch, "E25.0.1.107", {"start": v(232.8, 345.75) * mm, "end": v(232.8, 354.05) * mm});
            skLineSegment(sketch, "E25.0.1.108", {"start": v(87.99, 368.8) * mm, "end": v(87.99, 360.5) * mm});
            skLineSegment(sketch, "E25.0.1.109", {"start": v(113.55, 345.75) * mm, "end": v(113.55, 354.05) * mm});
            skLineSegment(sketch, "E25.0.1.110", {"start": v(332.37, 354.05) * mm, "end": v(332.37, 345.75) * mm});
            skLineSegment(sketch, "E25.0.1.111", {"start": v(266.88, 345.75) * mm, "end": v(266.88, 354.05) * mm});
            skLineSegment(sketch, "E25.0.1.112", {"start": v(180.36, 372.95) * mm, "end": v(173.17, 368.8) * mm});
            skLineSegment(sketch, "E25.0.1.113", {"start": v(181.7, 354.05) * mm, "end": v(188.88, 358.2) * mm});
            skLineSegment(sketch, "E25.0.1.114", {"start": v(68.3, 368.8) * mm, "end": v(68.3, 360.5) * mm});
            skLineSegment(sketch, "E25.0.1.115", {"start": v(317.99, 345.75) * mm, "end": v(317.99, 354.05) * mm});
            skLineSegment(sketch, "E25.0.1.116", {"start": v(485.7, 345.75) * mm, "end": v(478.5, 341.6) * mm});
            skLineSegment(sketch, "E25.0.1.117", {"start": v(10, 372.95) * mm, "end": v(17.19, 368.8) * mm});
            skLineSegment(sketch, "E25.0.1.118", {"start": v(376.29, 341.6) * mm, "end": v(369.1, 345.75) * mm});
            skLineSegment(sketch, "E25.0.1.119", {"start": v(452.95, 372.95) * mm, "end": v(445.76, 368.8) * mm});
            skLineSegment(sketch, "E25.0.1.120", {"start": v(315.32, 345.75) * mm, "end": v(308.13, 341.6) * mm});
            skLineSegment(sketch, "E25.0.1.121", {"start": v(93.85, 354.05) * mm, "end": v(93.85, 345.75) * mm});
            skLineSegment(sketch, "E25.0.1.122", {"start": v(35.55, 341.6) * mm, "end": v(28.36, 345.75) * mm});
            skLineSegment(sketch, "E25.0.1.123", {"start": v(45.4, 345.75) * mm, "end": v(45.4, 354.05) * mm});
            skLineSegment(sketch, "E25.0.1.124", {"start": v(42.74, 345.75) * mm, "end": v(35.55, 341.6) * mm});
            skLineSegment(sketch, "E25.0.1.125", {"start": v(434.59, 354.05) * mm, "end": v(434.59, 345.75) * mm});
            skLineSegment(sketch, "E25.0.1.126", {"start": v(340.88, 360.5) * mm, "end": v(340.88, 368.8) * mm});
            skLineSegment(sketch, "E25.0.1.127", {"start": v(394.65, 360.5) * mm, "end": v(401.84, 356.35) * mm});
            skLineSegment(sketch, "E25.0.1.128", {"start": v(153.48, 368.8) * mm, "end": v(146.29, 372.95) * mm});
            skLineSegment(sketch, "E25.0.1.129", {"start": v(52.58, 341.6) * mm, "end": v(45.4, 345.75) * mm});
            skLineSegment(sketch, "E25.0.1.130", {"start": v(25.7, 354.05) * mm, "end": v(25.7, 345.75) * mm});
            skLineSegment(sketch, "E25.0.1.131", {"start": v(28.36, 345.75) * mm, "end": v(28.36, 354.05) * mm});
            skLineSegment(sketch, "E25.0.1.132", {"start": v(45.4, 354.05) * mm, "end": v(52.58, 358.2) * mm});
            skLineSegment(sketch, "E25.0.1.133", {"start": v(451.62, 345.75) * mm, "end": v(444.43, 341.6) * mm});
            skLineSegment(sketch, "E25.0.1.134", {"start": v(411.7, 360.5) * mm, "end": v(411.7, 368.8) * mm});
            skLineSegment(sketch, "E25.0.1.135", {"start": v(342.21, 341.6) * mm, "end": v(335.02, 345.75) * mm});
            skLineSegment(sketch, "E25.0.1.136", {"start": v(443.1, 360.5) * mm, "end": v(443.1, 368.8) * mm});
            skLineSegment(sketch, "E25.0.1.137", {"start": v(357.92, 368.8) * mm, "end": v(350.73, 372.95) * mm});
            skLineSegment(sketch, "E25.0.1.138", {"start": v(289.77, 360.5) * mm, "end": v(289.77, 368.8) * mm});
            skLineSegment(sketch, "E25.0.1.139", {"start": v(204.59, 368.8) * mm, "end": v(197.4, 372.95) * mm});
            skLineSegment(sketch, "E25.0.1.140", {"start": v(198.73, 354.05) * mm, "end": v(205.91, 358.2) * mm});
            skLineSegment(sketch, "E25.0.1.141", {"start": v(454.28, 345.75) * mm, "end": v(454.28, 354.05) * mm});
            skLineSegment(sketch, "E25.0.1.142", {"start": v(86.66, 358.2) * mm, "end": v(93.85, 354.05) * mm});
            skLineSegment(sketch, "E25.0.1.143", {"start": v(443.1, 368.8) * mm, "end": v(435.91, 372.95) * mm});
            skLineSegment(sketch, "E25.0.1.144", {"start": v(435.91, 372.95) * mm, "end": v(428.72, 368.8) * mm});
            skLineSegment(sketch, "E25.0.1.145", {"start": v(437.24, 354.05) * mm, "end": v(444.43, 358.2) * mm});
            skLineSegment(sketch, "E25.0.1.146", {"start": v(231.47, 372.95) * mm, "end": v(224.28, 368.8) * mm});
            skLineSegment(sketch, "E25.0.1.147", {"start": v(79.47, 345.75) * mm, "end": v(79.47, 354.05) * mm});
            skLineSegment(sketch, "E25.0.1.148", {"start": v(309.47, 360.5) * mm, "end": v(309.47, 368.8) * mm});
            skLineSegment(sketch, "E25.0.1.149", {"start": v(214.44, 372.95) * mm, "end": v(221.63, 368.8) * mm});
            skLineSegment(sketch, "E25.0.1.150", {"start": v(238.66, 368.8) * mm, "end": v(231.47, 372.95) * mm});
            skLineSegment(sketch, "E25.0.1.151", {"start": v(394.65, 368.8) * mm, "end": v(394.65, 360.5) * mm});
            skLineSegment(sketch, "E25.0.1.152", {"start": v(445.76, 360.5) * mm, "end": v(452.95, 356.35) * mm});
            skLineSegment(sketch, "E25.0.1.153", {"start": v(241.32, 360.5) * mm, "end": v(248.5, 356.35) * mm});
            skLineSegment(sketch, "E25.0.1.154", {"start": v(231.47, 356.35) * mm, "end": v(238.66, 360.5) * mm});
            skLineSegment(sketch, "E25.0.1.155", {"start": v(79.47, 354.05) * mm, "end": v(86.66, 358.2) * mm});
            skLineSegment(sketch, "E25.0.1.156", {"start": v(350.73, 372.95) * mm, "end": v(343.54, 368.8) * mm});
            skLineSegment(sketch, "E25.0.1.157", {"start": v(196.07, 354.05) * mm, "end": v(196.07, 345.75) * mm});
            skLineSegment(sketch, "E25.0.1.158", {"start": v(240, 341.6) * mm, "end": v(232.8, 345.75) * mm});
            skLineSegment(sketch, "E25.0.1.159", {"start": v(69.63, 358.2) * mm, "end": v(76.82, 354.05) * mm});
            skLineSegment(sketch, "E25.0.1.160", {"start": v(349.4, 354.05) * mm, "end": v(349.4, 345.75) * mm});
            skLineSegment(sketch, "E25.0.1.161", {"start": v(383.48, 345.75) * mm, "end": v(376.29, 341.6) * mm});
            skLineSegment(sketch, "E25.0.1.162", {"start": v(144.96, 354.05) * mm, "end": v(144.96, 345.75) * mm});
            skLineSegment(sketch, "E25.0.1.163", {"start": v(179.04, 345.75) * mm, "end": v(171.85, 341.6) * mm});
            skLineSegment(sketch, "E25.0.1.164", {"start": v(386.13, 354.05) * mm, "end": v(393.32, 358.2) * mm});
            skLineSegment(sketch, "E25.0.1.165", {"start": v(435.91, 356.35) * mm, "end": v(443.1, 360.5) * mm});
            skLineSegment(sketch, "E25.0.1.166", {"start": v(504.06, 356.35) * mm, "end": v(511.25, 360.5) * mm});
            skLineSegment(sketch, "E25.0.1.167", {"start": v(403.17, 345.75) * mm, "end": v(403.17, 354.05) * mm});
            skLineSegment(sketch, "E25.0.1.168", {"start": v(241.32, 368.8) * mm, "end": v(241.32, 360.5) * mm});
            skLineSegment(sketch, "E25.0.1.169", {"start": v(359.24, 341.6) * mm, "end": v(352.06, 345.75) * mm});
            skLineSegment(sketch, "E25.0.1.170", {"start": v(213.1, 345.75) * mm, "end": v(205.91, 341.6) * mm});
            skLineSegment(sketch, "E25.0.1.171", {"start": v(34.22, 368.8) * mm, "end": v(27.03, 372.95) * mm});
            skLineSegment(sketch, "E25.0.1.172", {"start": v(461.46, 358.2) * mm, "end": v(468.65, 354.05) * mm});
            skLineSegment(sketch, "E25.0.1.173", {"start": v(505.39, 354.05) * mm, "end": v(512.57, 358.2) * mm});
            skLineSegment(sketch, "E25.0.1.174", {"start": v(300.95, 354.05) * mm, "end": v(308.13, 358.2) * mm});
            skLineSegment(sketch, "E25.0.1.175", {"start": v(230.15, 345.75) * mm, "end": v(222.96, 341.6) * mm});
            skLineSegment(sketch, "E25.0.1.176", {"start": v(265.55, 356.35) * mm, "end": v(258.36, 360.5) * mm});
            skLineSegment(sketch, "E25.0.1.177", {"start": v(144.96, 345.75) * mm, "end": v(137.77, 341.6) * mm});
            skLineSegment(sketch, "E25.0.1.178", {"start": v(27.03, 372.95) * mm, "end": v(19.84, 368.8) * mm});
            skLineSegment(sketch, "E25.0.1.179", {"start": v(384.8, 372.95) * mm, "end": v(377.61, 368.8) * mm});
            skLineSegment(sketch, "E25.0.1.180", {"start": v(340.88, 368.8) * mm, "end": v(333.7, 372.95) * mm});
            skLineSegment(sketch, "E25.0.1.181", {"start": v(136.44, 368.8) * mm, "end": v(129.25, 372.95) * mm});
            skLineSegment(sketch, "E25.0.1.182", {"start": v(198.73, 345.75) * mm, "end": v(198.73, 354.05) * mm});
            skLineSegment(sketch, "E25.0.1.183", {"start": v(70.95, 368.8) * mm, "end": v(70.95, 360.5) * mm});
            skLineSegment(sketch, "E25.0.1.184", {"start": v(127.93, 354.05) * mm, "end": v(127.93, 345.75) * mm});
            skLineSegment(sketch, "E25.0.1.185", {"start": v(461.46, 341.6) * mm, "end": v(454.28, 345.75) * mm});
            skLineSegment(sketch, "E25.0.1.186", {"start": v(444.43, 358.2) * mm, "end": v(451.62, 354.05) * mm});
            skLineSegment(sketch, "E25.0.1.187", {"start": v(445.76, 368.8) * mm, "end": v(445.76, 360.5) * mm});
            skLineSegment(sketch, "E25.0.1.188", {"start": v(240, 358.2) * mm, "end": v(247.18, 354.05) * mm});
            skLineSegment(sketch, "E25.0.1.189", {"start": v(298.29, 354.05) * mm, "end": v(298.29, 345.75) * mm});
            skLineSegment(sketch, "E25.0.1.190", {"start": v(471.32, 345.75) * mm, "end": v(471.32, 354.05) * mm});
            skLineSegment(sketch, "E25.0.1.191", {"start": v(207.25, 360.5) * mm, "end": v(207.25, 368.8) * mm});
            skLineSegment(sketch, "E25.0.1.192", {"start": v(281.26, 345.75) * mm, "end": v(274.07, 341.6) * mm});
            skLineSegment(sketch, "E25.0.1.193", {"start": v(257.02, 341.6) * mm, "end": v(249.84, 345.75) * mm});
            skLineSegment(sketch, "E25.0.1.194", {"start": v(248.5, 372.95) * mm, "end": v(241.32, 368.8) * mm});
            skLineSegment(sketch, "E25.0.1.195", {"start": v(451.62, 354.05) * mm, "end": v(451.62, 345.75) * mm});
            skLineSegment(sketch, "E25.0.1.196", {"start": v(110.88, 345.75) * mm, "end": v(103.7, 341.6) * mm});
            skLineSegment(sketch, "E25.0.1.197", {"start": v(401.84, 356.35) * mm, "end": v(409.03, 360.5) * mm});
            skLineSegment(sketch, "E25.0.1.198", {"start": v(292.43, 368.8) * mm, "end": v(292.43, 360.5) * mm});
            skLineSegment(sketch, "E25.0.1.199", {"start": v(171.85, 341.6) * mm, "end": v(164.66, 345.75) * mm});
            skLineSegment(sketch, "E25.0.1.200", {"start": v(197.4, 356.35) * mm, "end": v(204.59, 360.5) * mm});
            skLineSegment(sketch, "E25.0.1.201", {"start": v(52.58, 358.2) * mm, "end": v(59.77, 354.05) * mm});
            skLineSegment(sketch, "E25.0.1.202", {"start": v(411.7, 368.8) * mm, "end": v(418.88, 372.95) * mm});
            skLineSegment(sketch, "E25.0.1.203", {"start": v(409.03, 368.8) * mm, "end": v(401.84, 372.95) * mm});
            skLineSegment(sketch, "E25.0.1.204", {"start": v(207.25, 368.8) * mm, "end": v(214.44, 372.95) * mm});
            skLineSegment(sketch, "E25.0.1.205", {"start": v(403.17, 354.05) * mm, "end": v(410.35, 358.2) * mm});
            skLineSegment(sketch, "E25.0.1.206", {"start": v(495.54, 341.6) * mm, "end": v(488.35, 345.75) * mm});
            skLineSegment(sketch, "E25.0.1.207", {"start": v(468.65, 354.05) * mm, "end": v(468.65, 345.75) * mm});
            skLineSegment(sketch, "E25.0.1.208", {"start": v(264.21, 354.05) * mm, "end": v(264.21, 345.75) * mm});
            skLineSegment(sketch, "E25.0.1.209", {"start": v(238.66, 360.5) * mm, "end": v(238.66, 368.8) * mm});
            skLineSegment(sketch, "E25.0.1.210", {"start": v(247.18, 345.75) * mm, "end": v(240, 341.6) * mm});
            skLineSegment(sketch, "E25.0.1.211", {"start": v(85.33, 360.5) * mm, "end": v(85.33, 368.8) * mm});
            skLineSegment(sketch, "E25.0.1.212", {"start": v(137.77, 341.6) * mm, "end": v(130.58, 345.75) * mm});
            skLineSegment(sketch, "E25.0.1.213", {"start": v(374.96, 360.5) * mm, "end": v(367.77, 356.35) * mm});
            skLineSegment(sketch, "E25.0.1.214", {"start": v(323.85, 368.8) * mm, "end": v(323.85, 360.5) * mm});
            skLineSegment(sketch, "E25.0.1.215", {"start": v(266.88, 354.05) * mm, "end": v(274.07, 358.2) * mm});
            skLineSegment(sketch, "E25.0.1.216", {"start": v(326.5, 368.8) * mm, "end": v(326.5, 360.5) * mm});
            skLineSegment(sketch, "E25.0.1.217", {"start": v(232.8, 354.05) * mm, "end": v(240, 358.2) * mm});
            skLineSegment(sketch, "E25.0.1.218", {"start": v(306.8, 360.5) * mm, "end": v(306.8, 368.8) * mm});
            skLineSegment(sketch, "E25.0.1.219", {"start": v(119.4, 368.8) * mm, "end": v(119.4, 360.5) * mm});
            skLineSegment(sketch, "E25.0.1.220", {"start": v(122.06, 368.8) * mm, "end": v(122.06, 360.5) * mm});
            skLineSegment(sketch, "E25.0.1.221", {"start": v(170.52, 360.5) * mm, "end": v(163.33, 356.35) * mm});
            skLineSegment(sketch, "E25.0.1.222", {"start": v(428.72, 368.8) * mm, "end": v(428.72, 360.5) * mm});
            skLineSegment(sketch, "E25.0.1.223", {"start": v(51.26, 360.5) * mm, "end": v(51.26, 368.8) * mm});
            skLineSegment(sketch, "E25.0.1.224", {"start": v(386.13, 345.75) * mm, "end": v(386.13, 354.05) * mm});
            skLineSegment(sketch, "E25.0.1.225", {"start": v(44.07, 356.35) * mm, "end": v(51.26, 360.5) * mm});
            skLineSegment(sketch, "E25.0.1.226", {"start": v(462.8, 368.8) * mm, "end": v(469.99, 372.95) * mm});
            skLineSegment(sketch, "E25.0.1.227", {"start": v(214.44, 356.35) * mm, "end": v(207.25, 360.5) * mm});
            skLineSegment(sketch, "E25.0.1.228", {"start": v(205.91, 358.2) * mm, "end": v(213.1, 354.05) * mm});
            skLineSegment(sketch, "E25.0.1.229", {"start": v(366.43, 354.05) * mm, "end": v(366.43, 345.75) * mm});
            skLineSegment(sketch, "E25.0.1.230", {"start": v(130.58, 354.05) * mm, "end": v(137.77, 358.2) * mm});
            skLineSegment(sketch, "E25.0.1.231", {"start": v(224.28, 368.8) * mm, "end": v(224.28, 360.5) * mm});
            skLineSegment(sketch, "E25.0.1.232", {"start": v(384.8, 356.35) * mm, "end": v(392, 360.5) * mm});
            skLineSegment(sketch, "E25.0.1.233", {"start": v(275.4, 360.5) * mm, "end": v(282.58, 356.35) * mm});
            skLineSegment(sketch, "E25.0.1.234", {"start": v(19.84, 360.5) * mm, "end": v(27.03, 356.35) * mm});
            skLineSegment(sketch, "E25.0.1.235", {"start": v(180.36, 356.35) * mm, "end": v(187.55, 360.5) * mm});
            skLineSegment(sketch, "E25.0.1.236", {"start": v(410.35, 358.2) * mm, "end": v(417.54, 354.05) * mm});
            skLineSegment(sketch, "E25.0.1.237", {"start": v(255.7, 368.8) * mm, "end": v(248.5, 372.95) * mm});
            skLineSegment(sketch, "E25.0.1.238", {"start": v(53.92, 368.8) * mm, "end": v(61.1, 372.95) * mm});
            skLineSegment(sketch, "E25.0.1.239", {"start": v(162, 354.05) * mm, "end": v(162, 345.75) * mm});
            skLineSegment(sketch, "E25.0.1.240", {"start": v(51.26, 368.8) * mm, "end": v(44.07, 372.95) * mm});
            skLineSegment(sketch, "E25.0.1.241", {"start": v(427.4, 358.2) * mm, "end": v(434.59, 354.05) * mm});
            skLineSegment(sketch, "E25.0.1.242", {"start": v(460.14, 368.8) * mm, "end": v(452.95, 372.95) * mm});
            skLineSegment(sketch, "E25.0.1.243", {"start": v(272.74, 360.5) * mm, "end": v(265.55, 356.35) * mm});
            skLineSegment(sketch, "E25.0.1.244", {"start": v(181.7, 345.75) * mm, "end": v(181.7, 354.05) * mm});
            skLineSegment(sketch, "E25.0.1.245", {"start": v(335.02, 354.05) * mm, "end": v(342.21, 358.2) * mm});
            skLineSegment(sketch, "E25.0.1.246", {"start": v(221.63, 368.8) * mm, "end": v(221.63, 360.5) * mm});
            skLineSegment(sketch, "E25.0.1.247", {"start": v(68.3, 360.5) * mm, "end": v(61.1, 356.35) * mm});
            skLineSegment(sketch, "E25.0.1.248", {"start": v(130.58, 345.75) * mm, "end": v(130.58, 354.05) * mm});
            skLineSegment(sketch, "E25.0.1.249", {"start": v(477.18, 360.5) * mm, "end": v(469.99, 356.35) * mm});
            skLineSegment(sketch, "E25.0.1.250", {"start": v(469.99, 372.95) * mm, "end": v(477.18, 368.8) * mm});
            skLineSegment(sketch, "E25.0.1.251", {"start": v(360.58, 360.5) * mm, "end": v(360.58, 368.8) * mm});
            skLineSegment(sketch, "E25.0.1.252", {"start": v(122.06, 360.5) * mm, "end": v(129.25, 356.35) * mm});
            skLineSegment(sketch, "E25.0.1.253", {"start": v(95.18, 356.35) * mm, "end": v(102.37, 360.5) * mm});
            skLineSegment(sketch, "E25.0.1.254", {"start": v(137.77, 358.2) * mm, "end": v(144.96, 354.05) * mm});
            skLineSegment(sketch, "E25.0.1.255", {"start": v(469.99, 356.35) * mm, "end": v(462.8, 360.5) * mm});
            skLineSegment(sketch, "E25.0.1.256", {"start": v(417.54, 354.05) * mm, "end": v(417.54, 345.75) * mm});
            skLineSegment(sketch, "E25.0.1.257", {"start": v(120.74, 358.2) * mm, "end": v(127.93, 354.05) * mm});
            skLineSegment(sketch, "E25.0.1.258", {"start": v(477.18, 368.8) * mm, "end": v(477.18, 360.5) * mm});
            skLineSegment(sketch, "E25.0.1.259", {"start": v(420.2, 354.05) * mm, "end": v(427.4, 358.2) * mm});
            skLineSegment(sketch, "E25.0.1.260", {"start": v(275.4, 368.8) * mm, "end": v(275.4, 360.5) * mm});
            skLineSegment(sketch, "E25.0.1.261", {"start": v(255.7, 360.5) * mm, "end": v(255.7, 368.8) * mm});
            skLineSegment(sketch, "E25.0.1.262", {"start": v(215.77, 354.05) * mm, "end": v(222.96, 358.2) * mm});
            skLineSegment(sketch, "E25.0.1.263", {"start": v(42.74, 354.05) * mm, "end": v(42.74, 345.75) * mm});
            skLineSegment(sketch, "E25.0.1.264", {"start": v(350.73, 356.35) * mm, "end": v(357.92, 360.5) * mm});
            skLineSegment(sketch, "E25.0.1.265", {"start": v(78.14, 356.35) * mm, "end": v(85.33, 360.5) * mm});
            skLineSegment(sketch, "E25.0.1.266", {"start": v(119.4, 360.5) * mm, "end": v(112.22, 356.35) * mm});
            skLineSegment(sketch, "E25.0.1.267", {"start": v(19.84, 368.8) * mm, "end": v(19.84, 360.5) * mm});
            skLineSegment(sketch, "E25.0.1.268", {"start": v(496.87, 360.5) * mm, "end": v(504.06, 356.35) * mm});
            skLineSegment(sketch, "E25.0.1.269", {"start": v(325.18, 358.2) * mm, "end": v(332.37, 354.05) * mm});
            skLineSegment(sketch, "E25.0.1.270", {"start": v(367.77, 372.95) * mm, "end": v(374.96, 368.8) * mm});
            skLineSegment(sketch, "E25.0.1.271", {"start": v(258.36, 360.5) * mm, "end": v(258.36, 368.8) * mm});
            skLineSegment(sketch, "E25.0.1.272", {"start": v(163.33, 372.95) * mm, "end": v(170.52, 368.8) * mm});
            skLineSegment(sketch, "E25.0.1.273", {"start": v(179.04, 354.05) * mm, "end": v(179.04, 345.75) * mm});
            skLineSegment(sketch, "E25.0.1.274", {"start": v(249.84, 345.75) * mm, "end": v(249.84, 354.05) * mm});
            skLineSegment(sketch, "E25.0.1.275", {"start": v(139.1, 360.5) * mm, "end": v(146.29, 356.35) * mm});
            skLineSegment(sketch, "E25.0.1.276", {"start": v(418.88, 356.35) * mm, "end": v(411.7, 360.5) * mm});
            skLineSegment(sketch, "E25.0.1.277", {"start": v(426.07, 368.8) * mm, "end": v(426.07, 360.5) * mm});
            skLineSegment(sketch, "E25.0.1.278", {"start": v(367.77, 356.35) * mm, "end": v(360.58, 360.5) * mm});
            skLineSegment(sketch, "E25.0.1.279", {"start": v(352.06, 354.05) * mm, "end": v(359.24, 358.2) * mm});
            skLineSegment(sketch, "E25.0.1.280", {"start": v(163.33, 356.35) * mm, "end": v(156.14, 360.5) * mm});
            skLineSegment(sketch, "E25.0.1.281", {"start": v(112.22, 356.35) * mm, "end": v(105.03, 360.5) * mm});
            skLineSegment(sketch, "E25.0.1.282", {"start": v(487.02, 372.95) * mm, "end": v(479.83, 368.8) * mm});
            skLineSegment(sketch, "E25.0.1.283", {"start": v(374.96, 368.8) * mm, "end": v(374.96, 360.5) * mm});
            skLineSegment(sketch, "E25.0.1.284", {"start": v(17.19, 360.5) * mm, "end": v(10, 356.35) * mm});
            skLineSegment(sketch, "E25.0.1.285", {"start": v(221.63, 360.5) * mm, "end": v(214.44, 356.35) * mm});
            skLineSegment(sketch, "E25.0.1.286", {"start": v(282.58, 372.95) * mm, "end": v(275.4, 368.8) * mm});
            skLineSegment(sketch, "E25.0.1.287", {"start": v(335.02, 345.75) * mm, "end": v(335.02, 354.05) * mm});
            skLineSegment(sketch, "E25.0.1.288", {"start": v(170.52, 368.8) * mm, "end": v(170.52, 360.5) * mm});
            skLineSegment(sketch, "E25.0.1.289", {"start": v(291.1, 358.2) * mm, "end": v(298.29, 354.05) * mm});
            skLineSegment(sketch, "E25.0.1.290", {"start": v(173.17, 368.8) * mm, "end": v(173.17, 360.5) * mm});
            skLineSegment(sketch, "E25.0.1.291", {"start": v(495.54, 358.2) * mm, "end": v(502.73, 354.05) * mm});
            skLineSegment(sketch, "E25.0.1.292", {"start": v(147.62, 345.75) * mm, "end": v(147.62, 354.05) * mm});
            skLineSegment(sketch, "E25.0.1.293", {"start": v(153.48, 360.5) * mm, "end": v(153.48, 368.8) * mm});
            skLineSegment(sketch, "E25.0.1.294", {"start": v(222.96, 358.2) * mm, "end": v(230.15, 354.05) * mm});
            skLineSegment(sketch, "E25.0.1.295", {"start": v(479.83, 368.8) * mm, "end": v(479.83, 360.5) * mm});
            skLineSegment(sketch, "E25.0.1.296", {"start": v(420.2, 345.75) * mm, "end": v(420.2, 354.05) * mm});
            skLineSegment(sketch, "E25.0.1.297", {"start": v(326.5, 360.5) * mm, "end": v(333.7, 356.35) * mm});
            skLineSegment(sketch, "E25.0.1.298", {"start": v(173.17, 360.5) * mm, "end": v(180.36, 356.35) * mm});
            skLineSegment(sketch, "E25.0.1.299", {"start": v(342.21, 358.2) * mm, "end": v(349.4, 354.05) * mm});
            skLineSegment(sketch, "E25.0.1.300", {"start": v(265.55, 372.95) * mm, "end": v(272.74, 368.8) * mm});
            skLineSegment(sketch, "E25.0.1.301", {"start": v(274.07, 358.2) * mm, "end": v(281.26, 354.05) * mm});
            skLineSegment(sketch, "E25.0.1.302", {"start": v(215.77, 345.75) * mm, "end": v(215.77, 354.05) * mm});
            skLineSegment(sketch, "E25.0.1.303", {"start": v(462.8, 360.5) * mm, "end": v(462.8, 368.8) * mm});
            skLineSegment(sketch, "E25.0.1.304", {"start": v(281.26, 354.05) * mm, "end": v(281.26, 345.75) * mm});
            skLineSegment(sketch, "E25.0.1.305", {"start": v(156.14, 360.5) * mm, "end": v(156.14, 368.8) * mm});
            skLineSegment(sketch, "E25.0.1.306", {"start": v(213.1, 354.05) * mm, "end": v(213.1, 345.75) * mm});
            skLineSegment(sketch, "E25.0.1.307", {"start": v(96.5, 354.05) * mm, "end": v(103.7, 358.2) * mm});
            skLineSegment(sketch, "E25.0.1.308", {"start": v(460.14, 360.5) * mm, "end": v(460.14, 368.8) * mm});
            skLineSegment(sketch, "E25.0.1.309", {"start": v(323.85, 360.5) * mm, "end": v(316.66, 356.35) * mm});
            skLineSegment(sketch, "E25.0.1.310", {"start": v(272.74, 368.8) * mm, "end": v(272.74, 360.5) * mm});
            skLineSegment(sketch, "E25.0.1.311", {"start": v(377.61, 360.5) * mm, "end": v(384.8, 356.35) * mm});
            skLineSegment(sketch, "E25.0.1.312", {"start": v(282.58, 356.35) * mm, "end": v(289.77, 360.5) * mm});
            skLineSegment(sketch, "E25.0.1.313", {"start": v(146.29, 356.35) * mm, "end": v(153.48, 360.5) * mm});
            skLineSegment(sketch, "E25.0.1.314", {"start": v(343.54, 360.5) * mm, "end": v(350.73, 356.35) * mm});
            skLineSegment(sketch, "E25.0.1.315", {"start": v(376.29, 358.2) * mm, "end": v(383.48, 354.05) * mm});
            skLineSegment(sketch, "E25.0.1.316", {"start": v(171.85, 358.2) * mm, "end": v(179.04, 354.05) * mm});
            skLineSegment(sketch, "E25.0.1.317", {"start": v(53.92, 360.5) * mm, "end": v(53.92, 368.8) * mm});
            skLineSegment(sketch, "E25.0.1.318", {"start": v(292.43, 360.5) * mm, "end": v(299.62, 356.35) * mm});
            skLineSegment(sketch, "E25.0.1.319", {"start": v(377.61, 368.8) * mm, "end": v(377.61, 360.5) * mm});
            skLineSegment(sketch, "E25.0.1.320", {"start": v(383.48, 354.05) * mm, "end": v(383.48, 345.75) * mm});
            skLineSegment(sketch, "E25.0.1.321", {"start": v(129.25, 356.35) * mm, "end": v(136.44, 360.5) * mm});
            skLineSegment(sketch, "E25.0.1.322", {"start": v(428.72, 360.5) * mm, "end": v(435.91, 356.35) * mm});
            skLineSegment(sketch, "E25.0.1.323", {"start": v(496.87, 368.8) * mm, "end": v(496.87, 360.5) * mm});
            skLineSegment(sketch, "E25.0.1.324", {"start": v(224.28, 360.5) * mm, "end": v(231.47, 356.35) * mm});
            skLineSegment(sketch, "E25.0.1.325", {"start": v(333.7, 356.35) * mm, "end": v(340.88, 360.5) * mm});
            skLineSegment(sketch, "E25.0.1.326", {"start": v(11.33, 354.05) * mm, "end": v(18.52, 358.2) * mm});
            skLineSegment(sketch, "E25.0.1.327", {"start": v(18.52, 358.2) * mm, "end": v(25.7, 354.05) * mm});
            skLineSegment(sketch, "E25.0.1.328", {"start": v(494.21, 360.5) * mm, "end": v(494.21, 368.8) * mm});
            skLineSegment(sketch, "E25.0.1.329", {"start": v(315.32, 354.05) * mm, "end": v(315.32, 345.75) * mm});
            skLineSegment(sketch, "E25.0.1.330", {"start": v(360.58, 368.8) * mm, "end": v(367.77, 372.95) * mm});
            skLineSegment(sketch, "E25.0.1.331", {"start": v(316.66, 356.35) * mm, "end": v(309.47, 360.5) * mm});
            skLineSegment(sketch, "E25.0.1.332", {"start": v(308.13, 358.2) * mm, "end": v(315.32, 354.05) * mm});
            skLineSegment(sketch, "E25.0.1.333", {"start": v(147.62, 354.05) * mm, "end": v(154.8, 358.2) * mm});
            skLineSegment(sketch, "E25.0.1.334", {"start": v(359.24, 358.2) * mm, "end": v(366.43, 354.05) * mm});
            skLineSegment(sketch, "E25.0.1.335", {"start": v(110.88, 354.05) * mm, "end": v(110.88, 345.75) * mm});
            skLineSegment(sketch, "E25.0.1.336", {"start": v(154.8, 358.2) * mm, "end": v(162, 354.05) * mm});
            skLineSegment(sketch, "E25.0.1.337", {"start": v(17.19, 368.8) * mm, "end": v(17.19, 360.5) * mm});
            skLineSegment(sketch, "E25.0.1.338", {"start": v(156.14, 368.8) * mm, "end": v(163.33, 372.95) * mm});
            skLineSegment(sketch, "E25.0.1.339", {"start": v(103.7, 358.2) * mm, "end": v(110.88, 354.05) * mm});
            skLineSegment(sketch, "E25.0.1.340", {"start": v(471.32, 354.05) * mm, "end": v(478.5, 358.2) * mm});
            skLineSegment(sketch, "E25.0.1.341", {"start": v(426.07, 360.5) * mm, "end": v(418.88, 356.35) * mm});
            skLineSegment(sketch, "E25.0.1.342", {"start": v(357.92, 360.5) * mm, "end": v(357.92, 368.8) * mm});
            skLineSegment(sketch, "E25.0.1.343", {"start": v(317.99, 354.05) * mm, "end": v(325.18, 358.2) * mm});
            skLineSegment(sketch, "E25.0.1.344", {"start": v(258.36, 368.8) * mm, "end": v(265.55, 372.95) * mm});
            skLineSegment(sketch, "E25.0.1.345", {"start": v(283.91, 345.75) * mm, "end": v(283.91, 354.05) * mm});
            skLineSegment(sketch, "E25.0.1.346", {"start": v(283.91, 354.05) * mm, "end": v(291.1, 358.2) * mm});
            skLineSegment(sketch, "E25.0.1.347", {"start": v(113.55, 354.05) * mm, "end": v(120.74, 358.2) * mm});
            skLineSegment(sketch, "E25.0.1.348", {"start": v(36.88, 360.5) * mm, "end": v(44.07, 356.35) * mm});
            skLineSegment(sketch, "E25.0.1.349", {"start": v(36.88, 368.8) * mm, "end": v(36.88, 360.5) * mm});
            skLineSegment(sketch, "E25.0.1.350", {"start": v(34.22, 360.5) * mm, "end": v(34.22, 368.8) * mm});
            skLineSegment(sketch, "E25.0.1.351", {"start": v(485.7, 354.05) * mm, "end": v(485.7, 345.75) * mm});
            skLineSegment(sketch, "E25.0.1.352", {"start": v(478.5, 358.2) * mm, "end": v(485.7, 354.05) * mm});
            skLineSegment(sketch, "E25.0.1.353", {"start": v(487.02, 356.35) * mm, "end": v(494.21, 360.5) * mm});
            skLineSegment(sketch, "E25.0.1.354", {"start": v(27.03, 356.35) * mm, "end": v(34.22, 360.5) * mm});
            skLineSegment(sketch, "E25.0.1.355", {"start": v(479.83, 360.5) * mm, "end": v(487.02, 356.35) * mm});
            skLineSegment(sketch, "E25.0.1.356", {"start": v(28.36, 354.05) * mm, "end": v(35.55, 358.2) * mm});
            skLineSegment(sketch, "E25.0.1.357", {"start": v(35.55, 358.2) * mm, "end": v(42.74, 354.05) * mm});
            skLineSegment(sketch, "E25.0.1.358", {"start": v(488.35, 354.05) * mm, "end": v(495.54, 358.2) * mm});
            skLineSegment(sketch, "E25.0.1.359", {"start": v(488.35, 345.75) * mm, "end": v(488.35, 354.05) * mm});
            skLineSegment(sketch, "E25.0.2.0", {"start": v(332.37, 316.25) * mm, "end": v(325.18, 312.1) * mm});
            skLineSegment(sketch, "E25.0.2.1", {"start": v(511.25, 339.3) * mm, "end": v(504.06, 343.45) * mm});
            skLineSegment(sketch, "E25.0.2.2", {"start": v(2.81, 339.3) * mm, "end": v(10, 343.45) * mm});
            skLineSegment(sketch, "E25.0.2.3", {"start": v(127.93, 316.25) * mm, "end": v(120.74, 312.1) * mm});
            skLineSegment(sketch, "E25.0.2.4", {"start": v(512.57, 312.1) * mm, "end": v(505.39, 316.25) * mm});
            skLineSegment(sketch, "E25.0.2.5", {"start": v(519.76, 316.25) * mm, "end": v(512.57, 312.1) * mm});
            skLineSegment(sketch, "E25.0.2.6", {"start": v(25.7, 316.25) * mm, "end": v(18.52, 312.1) * mm});
            skLineSegment(sketch, "E25.0.2.7", {"start": v(11.33, 316.25) * mm, "end": v(11.33, 324.55) * mm});
            skLineSegment(sketch, "E25.0.2.8", {"start": v(18.52, 312.1) * mm, "end": v(11.33, 316.25) * mm});
            skLineSegment(sketch, "E25.0.2.9", {"start": v(519.76, 324.55) * mm, "end": v(519.76, 316.25) * mm});
            skLineSegment(sketch, "E25.0.2.10", {"start": v(76.82, 316.25) * mm, "end": v(69.63, 312.1) * mm});
            skLineSegment(sketch, "E25.0.2.11", {"start": v(112.22, 343.45) * mm, "end": v(119.4, 339.3) * mm});
            skLineSegment(sketch, "E25.0.2.12", {"start": v(205.91, 312.1) * mm, "end": v(198.73, 316.25) * mm});
            skLineSegment(sketch, "E25.0.2.13", {"start": v(197.4, 343.45) * mm, "end": v(190.2, 339.3) * mm});
            skLineSegment(sketch, "E25.0.2.14", {"start": v(93.85, 316.25) * mm, "end": v(86.66, 312.1) * mm});
            skLineSegment(sketch, "E25.0.2.15", {"start": v(129.25, 343.45) * mm, "end": v(122.06, 339.3) * mm});
            skLineSegment(sketch, "E25.0.2.16", {"start": v(298.29, 316.25) * mm, "end": v(291.1, 312.1) * mm});
            skLineSegment(sketch, "E25.0.2.17", {"start": v(502.73, 316.25) * mm, "end": v(495.54, 312.1) * mm});
            skLineSegment(sketch, "E25.0.2.18", {"start": v(289.77, 339.3) * mm, "end": v(282.58, 343.45) * mm});
            skLineSegment(sketch, "E25.0.2.19", {"start": v(85.33, 339.3) * mm, "end": v(78.14, 343.45) * mm});
            skLineSegment(sketch, "E25.0.2.20", {"start": v(494.21, 339.3) * mm, "end": v(487.02, 343.45) * mm});
            skLineSegment(sketch, "E25.0.2.21", {"start": v(333.7, 343.45) * mm, "end": v(326.5, 339.3) * mm});
            skLineSegment(sketch, "E25.0.2.22", {"start": v(95.18, 343.45) * mm, "end": v(87.99, 339.3) * mm});
            skLineSegment(sketch, "E25.0.2.23", {"start": v(478.5, 312.1) * mm, "end": v(471.32, 316.25) * mm});
            skLineSegment(sketch, "E25.0.2.24", {"start": v(274.07, 312.1) * mm, "end": v(266.88, 316.25) * mm});
            skLineSegment(sketch, "E25.0.2.25", {"start": v(444.43, 312.1) * mm, "end": v(437.24, 316.25) * mm});
            skLineSegment(sketch, "E25.0.2.26", {"start": v(401.84, 343.45) * mm, "end": v(394.65, 339.3) * mm});
            skLineSegment(sketch, "E25.0.2.27", {"start": v(410.35, 312.1) * mm, "end": v(403.17, 316.25) * mm});
            skLineSegment(sketch, "E25.0.2.28", {"start": v(468.65, 316.25) * mm, "end": v(461.46, 312.1) * mm});
            skLineSegment(sketch, "E25.0.2.29", {"start": v(427.4, 312.1) * mm, "end": v(420.2, 316.25) * mm});
            skLineSegment(sketch, "E25.0.2.30", {"start": v(59.77, 316.25) * mm, "end": v(52.58, 312.1) * mm});
            skLineSegment(sketch, "E25.0.2.31", {"start": v(512.57, 328.7) * mm, "end": v(519.76, 324.55) * mm});
            skLineSegment(sketch, "E25.0.2.32", {"start": v(196.07, 316.25) * mm, "end": v(188.88, 312.1) * mm});
            skLineSegment(sketch, "E25.0.2.33", {"start": v(86.66, 312.1) * mm, "end": v(79.47, 316.25) * mm});
            skLineSegment(sketch, "E25.0.2.34", {"start": v(400.5, 316.25) * mm, "end": v(393.32, 312.1) * mm});
            skLineSegment(sketch, "E25.0.2.35", {"start": v(103.7, 312.1) * mm, "end": v(96.5, 316.25) * mm});
            skLineSegment(sketch, "E25.0.2.36", {"start": v(299.62, 343.45) * mm, "end": v(292.43, 339.3) * mm});
            skLineSegment(sketch, "E25.0.2.37", {"start": v(504.06, 343.45) * mm, "end": v(496.87, 339.3) * mm});
            skLineSegment(sketch, "E25.0.2.38", {"start": v(2.81, 331) * mm, "end": v(2.81, 339.3) * mm});
            skLineSegment(sketch, "E25.0.2.39", {"start": v(308.13, 312.1) * mm, "end": v(300.95, 316.25) * mm});
            skLineSegment(sketch, "E25.0.2.40", {"start": v(417.54, 316.25) * mm, "end": v(410.35, 312.1) * mm});
            skLineSegment(sketch, "E25.0.2.41", {"start": v(434.59, 316.25) * mm, "end": v(427.4, 312.1) * mm});
            skLineSegment(sketch, "E25.0.2.42", {"start": v(62.44, 316.25) * mm, "end": v(62.44, 324.55) * mm});
            skLineSegment(sketch, "E25.0.2.43", {"start": v(69.63, 312.1) * mm, "end": v(62.44, 316.25) * mm});
            skLineSegment(sketch, "E25.0.2.44", {"start": v(325.18, 312.1) * mm, "end": v(317.99, 316.25) * mm});
            skLineSegment(sketch, "E25.0.2.45", {"start": v(264.21, 316.25) * mm, "end": v(257.02, 312.1) * mm});
            skLineSegment(sketch, "E25.0.2.46", {"start": v(120.74, 312.1) * mm, "end": v(113.55, 316.25) * mm});
            skLineSegment(sketch, "E25.0.2.47", {"start": v(502.73, 324.55) * mm, "end": v(502.73, 316.25) * mm});
            skLineSegment(sketch, "E25.0.2.48", {"start": v(316.66, 343.45) * mm, "end": v(323.85, 339.3) * mm});
            skLineSegment(sketch, "E25.0.2.49", {"start": v(505.39, 316.25) * mm, "end": v(505.39, 324.55) * mm});
            skLineSegment(sketch, "E25.0.2.50", {"start": v(10, 326.85) * mm, "end": v(2.81, 331) * mm});
            skLineSegment(sketch, "E25.0.2.51", {"start": v(59.77, 324.55) * mm, "end": v(59.77, 316.25) * mm});
            skLineSegment(sketch, "E25.0.2.52", {"start": v(291.1, 312.1) * mm, "end": v(283.91, 316.25) * mm});
            skLineSegment(sketch, "E25.0.2.53", {"start": v(511.25, 331) * mm, "end": v(511.25, 339.3) * mm});
            skLineSegment(sketch, "E25.0.2.54", {"start": v(392, 339.3) * mm, "end": v(384.8, 343.45) * mm});
            skLineSegment(sketch, "E25.0.2.55", {"start": v(187.55, 339.3) * mm, "end": v(180.36, 343.45) * mm});
            skLineSegment(sketch, "E25.0.2.56", {"start": v(247.18, 324.55) * mm, "end": v(247.18, 316.25) * mm});
            skLineSegment(sketch, "E25.0.2.57", {"start": v(188.88, 328.7) * mm, "end": v(196.07, 324.55) * mm});
            skLineSegment(sketch, "E25.0.2.58", {"start": v(369.1, 324.55) * mm, "end": v(376.29, 328.7) * mm});
            skLineSegment(sketch, "E25.0.2.59", {"start": v(409.03, 331) * mm, "end": v(409.03, 339.3) * mm});
            skLineSegment(sketch, "E25.0.2.60", {"start": v(188.88, 312.1) * mm, "end": v(181.7, 316.25) * mm});
            skLineSegment(sketch, "E25.0.2.61", {"start": v(204.59, 331) * mm, "end": v(204.59, 339.3) * mm});
            skLineSegment(sketch, "E25.0.2.62", {"start": v(164.66, 324.55) * mm, "end": v(171.85, 328.7) * mm});
            skLineSegment(sketch, "E25.0.2.63", {"start": v(230.15, 324.55) * mm, "end": v(230.15, 316.25) * mm});
            skLineSegment(sketch, "E25.0.2.64", {"start": v(343.54, 339.3) * mm, "end": v(343.54, 331) * mm});
            skLineSegment(sketch, "E25.0.2.65", {"start": v(139.1, 339.3) * mm, "end": v(139.1, 331) * mm});
            skLineSegment(sketch, "E25.0.2.66", {"start": v(70.95, 331) * mm, "end": v(78.14, 326.85) * mm});
            skLineSegment(sketch, "E25.0.2.67", {"start": v(96.5, 316.25) * mm, "end": v(96.5, 324.55) * mm});
            skLineSegment(sketch, "E25.0.2.68", {"start": v(44.07, 343.45) * mm, "end": v(36.88, 339.3) * mm});
            skLineSegment(sketch, "E25.0.2.69", {"start": v(162, 316.25) * mm, "end": v(154.8, 312.1) * mm});
            skLineSegment(sketch, "E25.0.2.70", {"start": v(300.95, 316.25) * mm, "end": v(300.95, 324.55) * mm});
            skLineSegment(sketch, "E25.0.2.71", {"start": v(222.96, 312.1) * mm, "end": v(215.77, 316.25) * mm});
            skLineSegment(sketch, "E25.0.2.72", {"start": v(452.95, 326.85) * mm, "end": v(460.14, 331) * mm});
            skLineSegment(sketch, "E25.0.2.73", {"start": v(369.1, 316.25) * mm, "end": v(369.1, 324.55) * mm});
            skLineSegment(sketch, "E25.0.2.74", {"start": v(366.43, 316.25) * mm, "end": v(359.24, 312.1) * mm});
            skLineSegment(sketch, "E25.0.2.75", {"start": v(164.66, 316.25) * mm, "end": v(164.66, 324.55) * mm});
            skLineSegment(sketch, "E25.0.2.76", {"start": v(248.5, 326.85) * mm, "end": v(255.7, 331) * mm});
            skLineSegment(sketch, "E25.0.2.77", {"start": v(249.84, 324.55) * mm, "end": v(257.02, 328.7) * mm});
            skLineSegment(sketch, "E25.0.2.78", {"start": v(393.32, 312.1) * mm, "end": v(386.13, 316.25) * mm});
            skLineSegment(sketch, "E25.0.2.79", {"start": v(62.44, 324.55) * mm, "end": v(69.63, 328.7) * mm});
            skLineSegment(sketch, "E25.0.2.80", {"start": v(136.44, 331) * mm, "end": v(136.44, 339.3) * mm});
            skLineSegment(sketch, "E25.0.2.81", {"start": v(102.37, 331) * mm, "end": v(102.37, 339.3) * mm});
            skLineSegment(sketch, "E25.0.2.82", {"start": v(418.88, 343.45) * mm, "end": v(426.07, 339.3) * mm});
            skLineSegment(sketch, "E25.0.2.83", {"start": v(454.28, 324.55) * mm, "end": v(461.46, 328.7) * mm});
            skLineSegment(sketch, "E25.0.2.84", {"start": v(78.14, 343.45) * mm, "end": v(70.95, 339.3) * mm});
            skLineSegment(sketch, "E25.0.2.85", {"start": v(105.03, 331) * mm, "end": v(105.03, 339.3) * mm});
            skLineSegment(sketch, "E25.0.2.86", {"start": v(190.2, 331) * mm, "end": v(197.4, 326.85) * mm});
            skLineSegment(sketch, "E25.0.2.87", {"start": v(352.06, 316.25) * mm, "end": v(352.06, 324.55) * mm});
            skLineSegment(sketch, "E25.0.2.88", {"start": v(400.5, 324.55) * mm, "end": v(400.5, 316.25) * mm});
            skLineSegment(sketch, "E25.0.2.89", {"start": v(299.62, 326.85) * mm, "end": v(306.8, 331) * mm});
            skLineSegment(sketch, "E25.0.2.90", {"start": v(190.2, 339.3) * mm, "end": v(190.2, 331) * mm});
            skLineSegment(sketch, "E25.0.2.91", {"start": v(76.82, 324.55) * mm, "end": v(76.82, 316.25) * mm});
            skLineSegment(sketch, "E25.0.2.92", {"start": v(392, 331) * mm, "end": v(392, 339.3) * mm});
            skLineSegment(sketch, "E25.0.2.93", {"start": v(309.47, 339.3) * mm, "end": v(316.66, 343.45) * mm});
            skLineSegment(sketch, "E25.0.2.94", {"start": v(349.4, 316.25) * mm, "end": v(342.21, 312.1) * mm});
            skLineSegment(sketch, "E25.0.2.95", {"start": v(257.02, 328.7) * mm, "end": v(264.21, 324.55) * mm});
            skLineSegment(sketch, "E25.0.2.96", {"start": v(61.1, 343.45) * mm, "end": v(68.3, 339.3) * mm});
            skLineSegment(sketch, "E25.0.2.97", {"start": v(146.29, 343.45) * mm, "end": v(139.1, 339.3) * mm});
            skLineSegment(sketch, "E25.0.2.98", {"start": v(154.8, 312.1) * mm, "end": v(147.62, 316.25) * mm});
            skLineSegment(sketch, "E25.0.2.99", {"start": v(306.8, 339.3) * mm, "end": v(299.62, 343.45) * mm});
            skLineSegment(sketch, "E25.0.2.100", {"start": v(87.99, 331) * mm, "end": v(95.18, 326.85) * mm});
            skLineSegment(sketch, "E25.0.2.101", {"start": v(105.03, 339.3) * mm, "end": v(112.22, 343.45) * mm});
            skLineSegment(sketch, "E25.0.2.102", {"start": v(102.37, 339.3) * mm, "end": v(95.18, 343.45) * mm});
            skLineSegment(sketch, "E25.0.2.103", {"start": v(187.55, 331) * mm, "end": v(187.55, 339.3) * mm});
            skLineSegment(sketch, "E25.0.2.104", {"start": v(61.1, 326.85) * mm, "end": v(53.92, 331) * mm});
            skLineSegment(sketch, "E25.0.2.105", {"start": v(437.24, 316.25) * mm, "end": v(437.24, 324.55) * mm});
            skLineSegment(sketch, "E25.0.2.106", {"start": v(393.32, 328.7) * mm, "end": v(400.5, 324.55) * mm});
            skLineSegment(sketch, "E25.0.2.107", {"start": v(232.8, 316.25) * mm, "end": v(232.8, 324.55) * mm});
            skLineSegment(sketch, "E25.0.2.108", {"start": v(87.99, 339.3) * mm, "end": v(87.99, 331) * mm});
            skLineSegment(sketch, "E25.0.2.109", {"start": v(113.55, 316.25) * mm, "end": v(113.55, 324.55) * mm});
            skLineSegment(sketch, "E25.0.2.110", {"start": v(332.37, 324.55) * mm, "end": v(332.37, 316.25) * mm});
            skLineSegment(sketch, "E25.0.2.111", {"start": v(266.88, 316.25) * mm, "end": v(266.88, 324.55) * mm});
            skLineSegment(sketch, "E25.0.2.112", {"start": v(180.36, 343.45) * mm, "end": v(173.17, 339.3) * mm});
            skLineSegment(sketch, "E25.0.2.113", {"start": v(181.7, 324.55) * mm, "end": v(188.88, 328.7) * mm});
            skLineSegment(sketch, "E25.0.2.114", {"start": v(68.3, 339.3) * mm, "end": v(68.3, 331) * mm});
            skLineSegment(sketch, "E25.0.2.115", {"start": v(317.99, 316.25) * mm, "end": v(317.99, 324.55) * mm});
            skLineSegment(sketch, "E25.0.2.116", {"start": v(485.7, 316.25) * mm, "end": v(478.5, 312.1) * mm});
            skLineSegment(sketch, "E25.0.2.117", {"start": v(10, 343.45) * mm, "end": v(17.19, 339.3) * mm});
            skLineSegment(sketch, "E25.0.2.118", {"start": v(376.29, 312.1) * mm, "end": v(369.1, 316.25) * mm});
            skLineSegment(sketch, "E25.0.2.119", {"start": v(452.95, 343.45) * mm, "end": v(445.76, 339.3) * mm});
            skLineSegment(sketch, "E25.0.2.120", {"start": v(315.32, 316.25) * mm, "end": v(308.13, 312.1) * mm});
            skLineSegment(sketch, "E25.0.2.121", {"start": v(93.85, 324.55) * mm, "end": v(93.85, 316.25) * mm});
            skLineSegment(sketch, "E25.0.2.122", {"start": v(35.55, 312.1) * mm, "end": v(28.36, 316.25) * mm});
            skLineSegment(sketch, "E25.0.2.123", {"start": v(45.4, 316.25) * mm, "end": v(45.4, 324.55) * mm});
            skLineSegment(sketch, "E25.0.2.124", {"start": v(42.74, 316.25) * mm, "end": v(35.55, 312.1) * mm});
            skLineSegment(sketch, "E25.0.2.125", {"start": v(434.59, 324.55) * mm, "end": v(434.59, 316.25) * mm});
            skLineSegment(sketch, "E25.0.2.126", {"start": v(340.88, 331) * mm, "end": v(340.88, 339.3) * mm});
            skLineSegment(sketch, "E25.0.2.127", {"start": v(394.65, 331) * mm, "end": v(401.84, 326.85) * mm});
            skLineSegment(sketch, "E25.0.2.128", {"start": v(153.48, 339.3) * mm, "end": v(146.29, 343.45) * mm});
            skLineSegment(sketch, "E25.0.2.129", {"start": v(52.58, 312.1) * mm, "end": v(45.4, 316.25) * mm});
            skLineSegment(sketch, "E25.0.2.130", {"start": v(25.7, 324.55) * mm, "end": v(25.7, 316.25) * mm});
            skLineSegment(sketch, "E25.0.2.131", {"start": v(28.36, 316.25) * mm, "end": v(28.36, 324.55) * mm});
            skLineSegment(sketch, "E25.0.2.132", {"start": v(45.4, 324.55) * mm, "end": v(52.58, 328.7) * mm});
            skLineSegment(sketch, "E25.0.2.133", {"start": v(451.62, 316.25) * mm, "end": v(444.43, 312.1) * mm});
            skLineSegment(sketch, "E25.0.2.134", {"start": v(411.7, 331) * mm, "end": v(411.7, 339.3) * mm});
            skLineSegment(sketch, "E25.0.2.135", {"start": v(342.21, 312.1) * mm, "end": v(335.02, 316.25) * mm});
            skLineSegment(sketch, "E25.0.2.136", {"start": v(443.1, 331) * mm, "end": v(443.1, 339.3) * mm});
            skLineSegment(sketch, "E25.0.2.137", {"start": v(357.92, 339.3) * mm, "end": v(350.73, 343.45) * mm});
            skLineSegment(sketch, "E25.0.2.138", {"start": v(289.77, 331) * mm, "end": v(289.77, 339.3) * mm});
            skLineSegment(sketch, "E25.0.2.139", {"start": v(204.59, 339.3) * mm, "end": v(197.4, 343.45) * mm});
            skLineSegment(sketch, "E25.0.2.140", {"start": v(198.73, 324.55) * mm, "end": v(205.91, 328.7) * mm});
            skLineSegment(sketch, "E25.0.2.141", {"start": v(454.28, 316.25) * mm, "end": v(454.28, 324.55) * mm});
            skLineSegment(sketch, "E25.0.2.142", {"start": v(86.66, 328.7) * mm, "end": v(93.85, 324.55) * mm});
            skLineSegment(sketch, "E25.0.2.143", {"start": v(443.1, 339.3) * mm, "end": v(435.91, 343.45) * mm});
            skLineSegment(sketch, "E25.0.2.144", {"start": v(435.91, 343.45) * mm, "end": v(428.72, 339.3) * mm});
            skLineSegment(sketch, "E25.0.2.145", {"start": v(437.24, 324.55) * mm, "end": v(444.43, 328.7) * mm});
            skLineSegment(sketch, "E25.0.2.146", {"start": v(231.47, 343.45) * mm, "end": v(224.28, 339.3) * mm});
            skLineSegment(sketch, "E25.0.2.147", {"start": v(79.47, 316.25) * mm, "end": v(79.47, 324.55) * mm});
            skLineSegment(sketch, "E25.0.2.148", {"start": v(309.47, 331) * mm, "end": v(309.47, 339.3) * mm});
            skLineSegment(sketch, "E25.0.2.149", {"start": v(214.44, 343.45) * mm, "end": v(221.63, 339.3) * mm});
            skLineSegment(sketch, "E25.0.2.150", {"start": v(238.66, 339.3) * mm, "end": v(231.47, 343.45) * mm});
            skLineSegment(sketch, "E25.0.2.151", {"start": v(394.65, 339.3) * mm, "end": v(394.65, 331) * mm});
            skLineSegment(sketch, "E25.0.2.152", {"start": v(445.76, 331) * mm, "end": v(452.95, 326.85) * mm});
            skLineSegment(sketch, "E25.0.2.153", {"start": v(241.32, 331) * mm, "end": v(248.5, 326.85) * mm});
            skLineSegment(sketch, "E25.0.2.154", {"start": v(231.47, 326.85) * mm, "end": v(238.66, 331) * mm});
            skLineSegment(sketch, "E25.0.2.155", {"start": v(79.47, 324.55) * mm, "end": v(86.66, 328.7) * mm});
            skLineSegment(sketch, "E25.0.2.156", {"start": v(350.73, 343.45) * mm, "end": v(343.54, 339.3) * mm});
            skLineSegment(sketch, "E25.0.2.157", {"start": v(196.07, 324.55) * mm, "end": v(196.07, 316.25) * mm});
            skLineSegment(sketch, "E25.0.2.158", {"start": v(240, 312.1) * mm, "end": v(232.8, 316.25) * mm});
            skLineSegment(sketch, "E25.0.2.159", {"start": v(69.63, 328.7) * mm, "end": v(76.82, 324.55) * mm});
            skLineSegment(sketch, "E25.0.2.160", {"start": v(349.4, 324.55) * mm, "end": v(349.4, 316.25) * mm});
            skLineSegment(sketch, "E25.0.2.161", {"start": v(383.48, 316.25) * mm, "end": v(376.29, 312.1) * mm});
            skLineSegment(sketch, "E25.0.2.162", {"start": v(144.96, 324.55) * mm, "end": v(144.96, 316.25) * mm});
            skLineSegment(sketch, "E25.0.2.163", {"start": v(179.04, 316.25) * mm, "end": v(171.85, 312.1) * mm});
            skLineSegment(sketch, "E25.0.2.164", {"start": v(386.13, 324.55) * mm, "end": v(393.32, 328.7) * mm});
            skLineSegment(sketch, "E25.0.2.165", {"start": v(435.91, 326.85) * mm, "end": v(443.1, 331) * mm});
            skLineSegment(sketch, "E25.0.2.166", {"start": v(504.06, 326.85) * mm, "end": v(511.25, 331) * mm});
            skLineSegment(sketch, "E25.0.2.167", {"start": v(403.17, 316.25) * mm, "end": v(403.17, 324.55) * mm});
            skLineSegment(sketch, "E25.0.2.168", {"start": v(241.32, 339.3) * mm, "end": v(241.32, 331) * mm});
            skLineSegment(sketch, "E25.0.2.169", {"start": v(359.24, 312.1) * mm, "end": v(352.06, 316.25) * mm});
            skLineSegment(sketch, "E25.0.2.170", {"start": v(213.1, 316.25) * mm, "end": v(205.91, 312.1) * mm});
            skLineSegment(sketch, "E25.0.2.171", {"start": v(34.22, 339.3) * mm, "end": v(27.03, 343.45) * mm});
            skLineSegment(sketch, "E25.0.2.172", {"start": v(461.46, 328.7) * mm, "end": v(468.65, 324.55) * mm});
            skLineSegment(sketch, "E25.0.2.173", {"start": v(505.39, 324.55) * mm, "end": v(512.57, 328.7) * mm});
            skLineSegment(sketch, "E25.0.2.174", {"start": v(300.95, 324.55) * mm, "end": v(308.13, 328.7) * mm});
            skLineSegment(sketch, "E25.0.2.175", {"start": v(230.15, 316.25) * mm, "end": v(222.96, 312.1) * mm});
            skLineSegment(sketch, "E25.0.2.176", {"start": v(265.55, 326.85) * mm, "end": v(258.36, 331) * mm});
            skLineSegment(sketch, "E25.0.2.177", {"start": v(144.96, 316.25) * mm, "end": v(137.77, 312.1) * mm});
            skLineSegment(sketch, "E25.0.2.178", {"start": v(27.03, 343.45) * mm, "end": v(19.84, 339.3) * mm});
            skLineSegment(sketch, "E25.0.2.179", {"start": v(384.8, 343.45) * mm, "end": v(377.61, 339.3) * mm});
            skLineSegment(sketch, "E25.0.2.180", {"start": v(340.88, 339.3) * mm, "end": v(333.7, 343.45) * mm});
            skLineSegment(sketch, "E25.0.2.181", {"start": v(136.44, 339.3) * mm, "end": v(129.25, 343.45) * mm});
            skLineSegment(sketch, "E25.0.2.182", {"start": v(198.73, 316.25) * mm, "end": v(198.73, 324.55) * mm});
            skLineSegment(sketch, "E25.0.2.183", {"start": v(70.95, 339.3) * mm, "end": v(70.95, 331) * mm});
            skLineSegment(sketch, "E25.0.2.184", {"start": v(127.93, 324.55) * mm, "end": v(127.93, 316.25) * mm});
            skLineSegment(sketch, "E25.0.2.185", {"start": v(461.46, 312.1) * mm, "end": v(454.28, 316.25) * mm});
            skLineSegment(sketch, "E25.0.2.186", {"start": v(444.43, 328.7) * mm, "end": v(451.62, 324.55) * mm});
            skLineSegment(sketch, "E25.0.2.187", {"start": v(445.76, 339.3) * mm, "end": v(445.76, 331) * mm});
            skLineSegment(sketch, "E25.0.2.188", {"start": v(240, 328.7) * mm, "end": v(247.18, 324.55) * mm});
            skLineSegment(sketch, "E25.0.2.189", {"start": v(298.29, 324.55) * mm, "end": v(298.29, 316.25) * mm});
            skLineSegment(sketch, "E25.0.2.190", {"start": v(471.32, 316.25) * mm, "end": v(471.32, 324.55) * mm});
            skLineSegment(sketch, "E25.0.2.191", {"start": v(207.25, 331) * mm, "end": v(207.25, 339.3) * mm});
            skLineSegment(sketch, "E25.0.2.192", {"start": v(281.26, 316.25) * mm, "end": v(274.07, 312.1) * mm});
            skLineSegment(sketch, "E25.0.2.193", {"start": v(257.02, 312.1) * mm, "end": v(249.84, 316.25) * mm});
            skLineSegment(sketch, "E25.0.2.194", {"start": v(248.5, 343.45) * mm, "end": v(241.32, 339.3) * mm});
            skLineSegment(sketch, "E25.0.2.195", {"start": v(451.62, 324.55) * mm, "end": v(451.62, 316.25) * mm});
            skLineSegment(sketch, "E25.0.2.196", {"start": v(110.88, 316.25) * mm, "end": v(103.7, 312.1) * mm});
            skLineSegment(sketch, "E25.0.2.197", {"start": v(401.84, 326.85) * mm, "end": v(409.03, 331) * mm});
            skLineSegment(sketch, "E25.0.2.198", {"start": v(292.43, 339.3) * mm, "end": v(292.43, 331) * mm});
            skLineSegment(sketch, "E25.0.2.199", {"start": v(171.85, 312.1) * mm, "end": v(164.66, 316.25) * mm});
            skLineSegment(sketch, "E25.0.2.200", {"start": v(197.4, 326.85) * mm, "end": v(204.59, 331) * mm});
            skLineSegment(sketch, "E25.0.2.201", {"start": v(52.58, 328.7) * mm, "end": v(59.77, 324.55) * mm});
            skLineSegment(sketch, "E25.0.2.202", {"start": v(411.7, 339.3) * mm, "end": v(418.88, 343.45) * mm});
            skLineSegment(sketch, "E25.0.2.203", {"start": v(409.03, 339.3) * mm, "end": v(401.84, 343.45) * mm});
            skLineSegment(sketch, "E25.0.2.204", {"start": v(207.25, 339.3) * mm, "end": v(214.44, 343.45) * mm});
            skLineSegment(sketch, "E25.0.2.205", {"start": v(403.17, 324.55) * mm, "end": v(410.35, 328.7) * mm});
            skLineSegment(sketch, "E25.0.2.206", {"start": v(495.54, 312.1) * mm, "end": v(488.35, 316.25) * mm});
            skLineSegment(sketch, "E25.0.2.207", {"start": v(468.65, 324.55) * mm, "end": v(468.65, 316.25) * mm});
            skLineSegment(sketch, "E25.0.2.208", {"start": v(264.21, 324.55) * mm, "end": v(264.21, 316.25) * mm});
            skLineSegment(sketch, "E25.0.2.209", {"start": v(238.66, 331) * mm, "end": v(238.66, 339.3) * mm});
            skLineSegment(sketch, "E25.0.2.210", {"start": v(247.18, 316.25) * mm, "end": v(240, 312.1) * mm});
            skLineSegment(sketch, "E25.0.2.211", {"start": v(85.33, 331) * mm, "end": v(85.33, 339.3) * mm});
            skLineSegment(sketch, "E25.0.2.212", {"start": v(137.77, 312.1) * mm, "end": v(130.58, 316.25) * mm});
            skLineSegment(sketch, "E25.0.2.213", {"start": v(374.96, 331) * mm, "end": v(367.77, 326.85) * mm});
            skLineSegment(sketch, "E25.0.2.214", {"start": v(323.85, 339.3) * mm, "end": v(323.85, 331) * mm});
            skLineSegment(sketch, "E25.0.2.215", {"start": v(266.88, 324.55) * mm, "end": v(274.07, 328.7) * mm});
            skLineSegment(sketch, "E25.0.2.216", {"start": v(326.5, 339.3) * mm, "end": v(326.5, 331) * mm});
            skLineSegment(sketch, "E25.0.2.217", {"start": v(232.8, 324.55) * mm, "end": v(240, 328.7) * mm});
            skLineSegment(sketch, "E25.0.2.218", {"start": v(306.8, 331) * mm, "end": v(306.8, 339.3) * mm});
            skLineSegment(sketch, "E25.0.2.219", {"start": v(119.4, 339.3) * mm, "end": v(119.4, 331) * mm});
            skLineSegment(sketch, "E25.0.2.220", {"start": v(122.06, 339.3) * mm, "end": v(122.06, 331) * mm});
            skLineSegment(sketch, "E25.0.2.221", {"start": v(170.52, 331) * mm, "end": v(163.33, 326.85) * mm});
            skLineSegment(sketch, "E25.0.2.222", {"start": v(428.72, 339.3) * mm, "end": v(428.72, 331) * mm});
            skLineSegment(sketch, "E25.0.2.223", {"start": v(51.26, 331) * mm, "end": v(51.26, 339.3) * mm});
            skLineSegment(sketch, "E25.0.2.224", {"start": v(386.13, 316.25) * mm, "end": v(386.13, 324.55) * mm});
            skLineSegment(sketch, "E25.0.2.225", {"start": v(44.07, 326.85) * mm, "end": v(51.26, 331) * mm});
            skLineSegment(sketch, "E25.0.2.226", {"start": v(462.8, 339.3) * mm, "end": v(469.99, 343.45) * mm});
            skLineSegment(sketch, "E25.0.2.227", {"start": v(214.44, 326.85) * mm, "end": v(207.25, 331) * mm});
            skLineSegment(sketch, "E25.0.2.228", {"start": v(205.91, 328.7) * mm, "end": v(213.1, 324.55) * mm});
            skLineSegment(sketch, "E25.0.2.229", {"start": v(366.43, 324.55) * mm, "end": v(366.43, 316.25) * mm});
            skLineSegment(sketch, "E25.0.2.230", {"start": v(130.58, 324.55) * mm, "end": v(137.77, 328.7) * mm});
            skLineSegment(sketch, "E25.0.2.231", {"start": v(224.28, 339.3) * mm, "end": v(224.28, 331) * mm});
            skLineSegment(sketch, "E25.0.2.232", {"start": v(384.8, 326.85) * mm, "end": v(392, 331) * mm});
            skLineSegment(sketch, "E25.0.2.233", {"start": v(275.4, 331) * mm, "end": v(282.58, 326.85) * mm});
            skLineSegment(sketch, "E25.0.2.234", {"start": v(19.84, 331) * mm, "end": v(27.03, 326.85) * mm});
            skLineSegment(sketch, "E25.0.2.235", {"start": v(180.36, 326.85) * mm, "end": v(187.55, 331) * mm});
            skLineSegment(sketch, "E25.0.2.236", {"start": v(410.35, 328.7) * mm, "end": v(417.54, 324.55) * mm});
            skLineSegment(sketch, "E25.0.2.237", {"start": v(255.7, 339.3) * mm, "end": v(248.5, 343.45) * mm});
            skLineSegment(sketch, "E25.0.2.238", {"start": v(53.92, 339.3) * mm, "end": v(61.1, 343.45) * mm});
            skLineSegment(sketch, "E25.0.2.239", {"start": v(162, 324.55) * mm, "end": v(162, 316.25) * mm});
            skLineSegment(sketch, "E25.0.2.240", {"start": v(51.26, 339.3) * mm, "end": v(44.07, 343.45) * mm});
            skLineSegment(sketch, "E25.0.2.241", {"start": v(427.4, 328.7) * mm, "end": v(434.59, 324.55) * mm});
            skLineSegment(sketch, "E25.0.2.242", {"start": v(460.14, 339.3) * mm, "end": v(452.95, 343.45) * mm});
            skLineSegment(sketch, "E25.0.2.243", {"start": v(272.74, 331) * mm, "end": v(265.55, 326.85) * mm});
            skLineSegment(sketch, "E25.0.2.244", {"start": v(181.7, 316.25) * mm, "end": v(181.7, 324.55) * mm});
            skLineSegment(sketch, "E25.0.2.245", {"start": v(335.02, 324.55) * mm, "end": v(342.21, 328.7) * mm});
            skLineSegment(sketch, "E25.0.2.246", {"start": v(221.63, 339.3) * mm, "end": v(221.63, 331) * mm});
            skLineSegment(sketch, "E25.0.2.247", {"start": v(68.3, 331) * mm, "end": v(61.1, 326.85) * mm});
            skLineSegment(sketch, "E25.0.2.248", {"start": v(130.58, 316.25) * mm, "end": v(130.58, 324.55) * mm});
            skLineSegment(sketch, "E25.0.2.249", {"start": v(477.18, 331) * mm, "end": v(469.99, 326.85) * mm});
            skLineSegment(sketch, "E25.0.2.250", {"start": v(469.99, 343.45) * mm, "end": v(477.18, 339.3) * mm});
            skLineSegment(sketch, "E25.0.2.251", {"start": v(360.58, 331) * mm, "end": v(360.58, 339.3) * mm});
            skLineSegment(sketch, "E25.0.2.252", {"start": v(122.06, 331) * mm, "end": v(129.25, 326.85) * mm});
            skLineSegment(sketch, "E25.0.2.253", {"start": v(95.18, 326.85) * mm, "end": v(102.37, 331) * mm});
            skLineSegment(sketch, "E25.0.2.254", {"start": v(137.77, 328.7) * mm, "end": v(144.96, 324.55) * mm});
            skLineSegment(sketch, "E25.0.2.255", {"start": v(469.99, 326.85) * mm, "end": v(462.8, 331) * mm});
            skLineSegment(sketch, "E25.0.2.256", {"start": v(417.54, 324.55) * mm, "end": v(417.54, 316.25) * mm});
            skLineSegment(sketch, "E25.0.2.257", {"start": v(120.74, 328.7) * mm, "end": v(127.93, 324.55) * mm});
            skLineSegment(sketch, "E25.0.2.258", {"start": v(477.18, 339.3) * mm, "end": v(477.18, 331) * mm});
            skLineSegment(sketch, "E25.0.2.259", {"start": v(420.2, 324.55) * mm, "end": v(427.4, 328.7) * mm});
            skLineSegment(sketch, "E25.0.2.260", {"start": v(275.4, 339.3) * mm, "end": v(275.4, 331) * mm});
            skLineSegment(sketch, "E25.0.2.261", {"start": v(255.7, 331) * mm, "end": v(255.7, 339.3) * mm});
            skLineSegment(sketch, "E25.0.2.262", {"start": v(215.77, 324.55) * mm, "end": v(222.96, 328.7) * mm});
            skLineSegment(sketch, "E25.0.2.263", {"start": v(42.74, 324.55) * mm, "end": v(42.74, 316.25) * mm});
            skLineSegment(sketch, "E25.0.2.264", {"start": v(350.73, 326.85) * mm, "end": v(357.92, 331) * mm});
            skLineSegment(sketch, "E25.0.2.265", {"start": v(78.14, 326.85) * mm, "end": v(85.33, 331) * mm});
            skLineSegment(sketch, "E25.0.2.266", {"start": v(119.4, 331) * mm, "end": v(112.22, 326.85) * mm});
            skLineSegment(sketch, "E25.0.2.267", {"start": v(19.84, 339.3) * mm, "end": v(19.84, 331) * mm});
            skLineSegment(sketch, "E25.0.2.268", {"start": v(496.87, 331) * mm, "end": v(504.06, 326.85) * mm});
            skLineSegment(sketch, "E25.0.2.269", {"start": v(325.18, 328.7) * mm, "end": v(332.37, 324.55) * mm});
            skLineSegment(sketch, "E25.0.2.270", {"start": v(367.77, 343.45) * mm, "end": v(374.96, 339.3) * mm});
            skLineSegment(sketch, "E25.0.2.271", {"start": v(258.36, 331) * mm, "end": v(258.36, 339.3) * mm});
            skLineSegment(sketch, "E25.0.2.272", {"start": v(163.33, 343.45) * mm, "end": v(170.52, 339.3) * mm});
            skLineSegment(sketch, "E25.0.2.273", {"start": v(179.04, 324.55) * mm, "end": v(179.04, 316.25) * mm});
            skLineSegment(sketch, "E25.0.2.274", {"start": v(249.84, 316.25) * mm, "end": v(249.84, 324.55) * mm});
            skLineSegment(sketch, "E25.0.2.275", {"start": v(139.1, 331) * mm, "end": v(146.29, 326.85) * mm});
            skLineSegment(sketch, "E25.0.2.276", {"start": v(418.88, 326.85) * mm, "end": v(411.7, 331) * mm});
            skLineSegment(sketch, "E25.0.2.277", {"start": v(426.07, 339.3) * mm, "end": v(426.07, 331) * mm});
            skLineSegment(sketch, "E25.0.2.278", {"start": v(367.77, 326.85) * mm, "end": v(360.58, 331) * mm});
            skLineSegment(sketch, "E25.0.2.279", {"start": v(352.06, 324.55) * mm, "end": v(359.24, 328.7) * mm});
            skLineSegment(sketch, "E25.0.2.280", {"start": v(163.33, 326.85) * mm, "end": v(156.14, 331) * mm});
            skLineSegment(sketch, "E25.0.2.281", {"start": v(112.22, 326.85) * mm, "end": v(105.03, 331) * mm});
            skLineSegment(sketch, "E25.0.2.282", {"start": v(487.02, 343.45) * mm, "end": v(479.83, 339.3) * mm});
            skLineSegment(sketch, "E25.0.2.283", {"start": v(374.96, 339.3) * mm, "end": v(374.96, 331) * mm});
            skLineSegment(sketch, "E25.0.2.284", {"start": v(17.19, 331) * mm, "end": v(10, 326.85) * mm});
            skLineSegment(sketch, "E25.0.2.285", {"start": v(221.63, 331) * mm, "end": v(214.44, 326.85) * mm});
            skLineSegment(sketch, "E25.0.2.286", {"start": v(282.58, 343.45) * mm, "end": v(275.4, 339.3) * mm});
            skLineSegment(sketch, "E25.0.2.287", {"start": v(335.02, 316.25) * mm, "end": v(335.02, 324.55) * mm});
            skLineSegment(sketch, "E25.0.2.288", {"start": v(170.52, 339.3) * mm, "end": v(170.52, 331) * mm});
            skLineSegment(sketch, "E25.0.2.289", {"start": v(291.1, 328.7) * mm, "end": v(298.29, 324.55) * mm});
            skLineSegment(sketch, "E25.0.2.290", {"start": v(173.17, 339.3) * mm, "end": v(173.17, 331) * mm});
            skLineSegment(sketch, "E25.0.2.291", {"start": v(495.54, 328.7) * mm, "end": v(502.73, 324.55) * mm});
            skLineSegment(sketch, "E25.0.2.292", {"start": v(147.62, 316.25) * mm, "end": v(147.62, 324.55) * mm});
            skLineSegment(sketch, "E25.0.2.293", {"start": v(153.48, 331) * mm, "end": v(153.48, 339.3) * mm});
            skLineSegment(sketch, "E25.0.2.294", {"start": v(222.96, 328.7) * mm, "end": v(230.15, 324.55) * mm});
            skLineSegment(sketch, "E25.0.2.295", {"start": v(479.83, 339.3) * mm, "end": v(479.83, 331) * mm});
            skLineSegment(sketch, "E25.0.2.296", {"start": v(420.2, 316.25) * mm, "end": v(420.2, 324.55) * mm});
            skLineSegment(sketch, "E25.0.2.297", {"start": v(326.5, 331) * mm, "end": v(333.7, 326.85) * mm});
            skLineSegment(sketch, "E25.0.2.298", {"start": v(173.17, 331) * mm, "end": v(180.36, 326.85) * mm});
            skLineSegment(sketch, "E25.0.2.299", {"start": v(342.21, 328.7) * mm, "end": v(349.4, 324.55) * mm});
            skLineSegment(sketch, "E25.0.2.300", {"start": v(265.55, 343.45) * mm, "end": v(272.74, 339.3) * mm});
            skLineSegment(sketch, "E25.0.2.301", {"start": v(274.07, 328.7) * mm, "end": v(281.26, 324.55) * mm});
            skLineSegment(sketch, "E25.0.2.302", {"start": v(215.77, 316.25) * mm, "end": v(215.77, 324.55) * mm});
            skLineSegment(sketch, "E25.0.2.303", {"start": v(462.8, 331) * mm, "end": v(462.8, 339.3) * mm});
            skLineSegment(sketch, "E25.0.2.304", {"start": v(281.26, 324.55) * mm, "end": v(281.26, 316.25) * mm});
            skLineSegment(sketch, "E25.0.2.305", {"start": v(156.14, 331) * mm, "end": v(156.14, 339.3) * mm});
            skLineSegment(sketch, "E25.0.2.306", {"start": v(213.1, 324.55) * mm, "end": v(213.1, 316.25) * mm});
            skLineSegment(sketch, "E25.0.2.307", {"start": v(96.5, 324.55) * mm, "end": v(103.7, 328.7) * mm});
            skLineSegment(sketch, "E25.0.2.308", {"start": v(460.14, 331) * mm, "end": v(460.14, 339.3) * mm});
            skLineSegment(sketch, "E25.0.2.309", {"start": v(323.85, 331) * mm, "end": v(316.66, 326.85) * mm});
            skLineSegment(sketch, "E25.0.2.310", {"start": v(272.74, 339.3) * mm, "end": v(272.74, 331) * mm});
            skLineSegment(sketch, "E25.0.2.311", {"start": v(377.61, 331) * mm, "end": v(384.8, 326.85) * mm});
            skLineSegment(sketch, "E25.0.2.312", {"start": v(282.58, 326.85) * mm, "end": v(289.77, 331) * mm});
            skLineSegment(sketch, "E25.0.2.313", {"start": v(146.29, 326.85) * mm, "end": v(153.48, 331) * mm});
            skLineSegment(sketch, "E25.0.2.314", {"start": v(343.54, 331) * mm, "end": v(350.73, 326.85) * mm});
            skLineSegment(sketch, "E25.0.2.315", {"start": v(376.29, 328.7) * mm, "end": v(383.48, 324.55) * mm});
            skLineSegment(sketch, "E25.0.2.316", {"start": v(171.85, 328.7) * mm, "end": v(179.04, 324.55) * mm});
            skLineSegment(sketch, "E25.0.2.317", {"start": v(53.92, 331) * mm, "end": v(53.92, 339.3) * mm});
            skLineSegment(sketch, "E25.0.2.318", {"start": v(292.43, 331) * mm, "end": v(299.62, 326.85) * mm});
            skLineSegment(sketch, "E25.0.2.319", {"start": v(377.61, 339.3) * mm, "end": v(377.61, 331) * mm});
            skLineSegment(sketch, "E25.0.2.320", {"start": v(383.48, 324.55) * mm, "end": v(383.48, 316.25) * mm});
            skLineSegment(sketch, "E25.0.2.321", {"start": v(129.25, 326.85) * mm, "end": v(136.44, 331) * mm});
            skLineSegment(sketch, "E25.0.2.322", {"start": v(428.72, 331) * mm, "end": v(435.91, 326.85) * mm});
            skLineSegment(sketch, "E25.0.2.323", {"start": v(496.87, 339.3) * mm, "end": v(496.87, 331) * mm});
            skLineSegment(sketch, "E25.0.2.324", {"start": v(224.28, 331) * mm, "end": v(231.47, 326.85) * mm});
            skLineSegment(sketch, "E25.0.2.325", {"start": v(333.7, 326.85) * mm, "end": v(340.88, 331) * mm});
            skLineSegment(sketch, "E25.0.2.326", {"start": v(11.33, 324.55) * mm, "end": v(18.52, 328.7) * mm});
            skLineSegment(sketch, "E25.0.2.327", {"start": v(18.52, 328.7) * mm, "end": v(25.7, 324.55) * mm});
            skLineSegment(sketch, "E25.0.2.328", {"start": v(494.21, 331) * mm, "end": v(494.21, 339.3) * mm});
            skLineSegment(sketch, "E25.0.2.329", {"start": v(315.32, 324.55) * mm, "end": v(315.32, 316.25) * mm});
            skLineSegment(sketch, "E25.0.2.330", {"start": v(360.58, 339.3) * mm, "end": v(367.77, 343.45) * mm});
            skLineSegment(sketch, "E25.0.2.331", {"start": v(316.66, 326.85) * mm, "end": v(309.47, 331) * mm});
            skLineSegment(sketch, "E25.0.2.332", {"start": v(308.13, 328.7) * mm, "end": v(315.32, 324.55) * mm});
            skLineSegment(sketch, "E25.0.2.333", {"start": v(147.62, 324.55) * mm, "end": v(154.8, 328.7) * mm});
            skLineSegment(sketch, "E25.0.2.334", {"start": v(359.24, 328.7) * mm, "end": v(366.43, 324.55) * mm});
            skLineSegment(sketch, "E25.0.2.335", {"start": v(110.88, 324.55) * mm, "end": v(110.88, 316.25) * mm});
            skLineSegment(sketch, "E25.0.2.336", {"start": v(154.8, 328.7) * mm, "end": v(162, 324.55) * mm});
            skLineSegment(sketch, "E25.0.2.337", {"start": v(17.19, 339.3) * mm, "end": v(17.19, 331) * mm});
            skLineSegment(sketch, "E25.0.2.338", {"start": v(156.14, 339.3) * mm, "end": v(163.33, 343.45) * mm});
            skLineSegment(sketch, "E25.0.2.339", {"start": v(103.7, 328.7) * mm, "end": v(110.88, 324.55) * mm});
            skLineSegment(sketch, "E25.0.2.340", {"start": v(471.32, 324.55) * mm, "end": v(478.5, 328.7) * mm});
            skLineSegment(sketch, "E25.0.2.341", {"start": v(426.07, 331) * mm, "end": v(418.88, 326.85) * mm});
            skLineSegment(sketch, "E25.0.2.342", {"start": v(357.92, 331) * mm, "end": v(357.92, 339.3) * mm});
            skLineSegment(sketch, "E25.0.2.343", {"start": v(317.99, 324.55) * mm, "end": v(325.18, 328.7) * mm});
            skLineSegment(sketch, "E25.0.2.344", {"start": v(258.36, 339.3) * mm, "end": v(265.55, 343.45) * mm});
            skLineSegment(sketch, "E25.0.2.345", {"start": v(283.91, 316.25) * mm, "end": v(283.91, 324.55) * mm});
            skLineSegment(sketch, "E25.0.2.346", {"start": v(283.91, 324.55) * mm, "end": v(291.1, 328.7) * mm});
            skLineSegment(sketch, "E25.0.2.347", {"start": v(113.55, 324.55) * mm, "end": v(120.74, 328.7) * mm});
            skLineSegment(sketch, "E25.0.2.348", {"start": v(36.88, 331) * mm, "end": v(44.07, 326.85) * mm});
            skLineSegment(sketch, "E25.0.2.349", {"start": v(36.88, 339.3) * mm, "end": v(36.88, 331) * mm});
            skLineSegment(sketch, "E25.0.2.350", {"start": v(34.22, 331) * mm, "end": v(34.22, 339.3) * mm});
            skLineSegment(sketch, "E25.0.2.351", {"start": v(485.7, 324.55) * mm, "end": v(485.7, 316.25) * mm});
            skLineSegment(sketch, "E25.0.2.352", {"start": v(478.5, 328.7) * mm, "end": v(485.7, 324.55) * mm});
            skLineSegment(sketch, "E25.0.2.353", {"start": v(487.02, 326.85) * mm, "end": v(494.21, 331) * mm});
            skLineSegment(sketch, "E25.0.2.354", {"start": v(27.03, 326.85) * mm, "end": v(34.22, 331) * mm});
            skLineSegment(sketch, "E25.0.2.355", {"start": v(479.83, 331) * mm, "end": v(487.02, 326.85) * mm});
            skLineSegment(sketch, "E25.0.2.356", {"start": v(28.36, 324.55) * mm, "end": v(35.55, 328.7) * mm});
            skLineSegment(sketch, "E25.0.2.357", {"start": v(35.55, 328.7) * mm, "end": v(42.74, 324.55) * mm});
            skLineSegment(sketch, "E25.0.2.358", {"start": v(488.35, 324.55) * mm, "end": v(495.54, 328.7) * mm});
            skLineSegment(sketch, "E25.0.2.359", {"start": v(488.35, 316.25) * mm, "end": v(488.35, 324.55) * mm});
            skLineSegment(sketch, "E25.0.3.0", {"start": v(332.37, 286.75) * mm, "end": v(325.18, 282.6) * mm});
            skLineSegment(sketch, "E25.0.3.1", {"start": v(511.25, 309.8) * mm, "end": v(504.06, 313.95) * mm});
            skLineSegment(sketch, "E25.0.3.2", {"start": v(2.81, 309.8) * mm, "end": v(10, 313.95) * mm});
            skLineSegment(sketch, "E25.0.3.3", {"start": v(127.93, 286.75) * mm, "end": v(120.74, 282.6) * mm});
            skLineSegment(sketch, "E25.0.3.4", {"start": v(512.57, 282.6) * mm, "end": v(505.39, 286.75) * mm});
            skLineSegment(sketch, "E25.0.3.5", {"start": v(519.76, 286.75) * mm, "end": v(512.57, 282.6) * mm});
            skLineSegment(sketch, "E25.0.3.6", {"start": v(25.7, 286.75) * mm, "end": v(18.52, 282.6) * mm});
            skLineSegment(sketch, "E25.0.3.7", {"start": v(11.33, 286.75) * mm, "end": v(11.33, 295.05) * mm});
            skLineSegment(sketch, "E25.0.3.8", {"start": v(18.52, 282.6) * mm, "end": v(11.33, 286.75) * mm});
            skLineSegment(sketch, "E25.0.3.9", {"start": v(519.76, 295.05) * mm, "end": v(519.76, 286.75) * mm});
            skLineSegment(sketch, "E25.0.3.10", {"start": v(76.82, 286.75) * mm, "end": v(69.63, 282.6) * mm});
            skLineSegment(sketch, "E25.0.3.11", {"start": v(112.22, 313.95) * mm, "end": v(119.4, 309.8) * mm});
            skLineSegment(sketch, "E25.0.3.12", {"start": v(205.91, 282.6) * mm, "end": v(198.73, 286.75) * mm});
            skLineSegment(sketch, "E25.0.3.13", {"start": v(197.4, 313.95) * mm, "end": v(190.2, 309.8) * mm});
            skLineSegment(sketch, "E25.0.3.14", {"start": v(93.85, 286.75) * mm, "end": v(86.66, 282.6) * mm});
            skLineSegment(sketch, "E25.0.3.15", {"start": v(129.25, 313.95) * mm, "end": v(122.06, 309.8) * mm});
            skLineSegment(sketch, "E25.0.3.16", {"start": v(298.29, 286.75) * mm, "end": v(291.1, 282.6) * mm});
            skLineSegment(sketch, "E25.0.3.17", {"start": v(502.73, 286.75) * mm, "end": v(495.54, 282.6) * mm});
            skLineSegment(sketch, "E25.0.3.18", {"start": v(289.77, 309.8) * mm, "end": v(282.58, 313.95) * mm});
            skLineSegment(sketch, "E25.0.3.19", {"start": v(85.33, 309.8) * mm, "end": v(78.14, 313.95) * mm});
            skLineSegment(sketch, "E25.0.3.20", {"start": v(494.21, 309.8) * mm, "end": v(487.02, 313.95) * mm});
            skLineSegment(sketch, "E25.0.3.21", {"start": v(333.7, 313.95) * mm, "end": v(326.5, 309.8) * mm});
            skLineSegment(sketch, "E25.0.3.22", {"start": v(95.18, 313.95) * mm, "end": v(87.99, 309.8) * mm});
            skLineSegment(sketch, "E25.0.3.23", {"start": v(478.5, 282.6) * mm, "end": v(471.32, 286.75) * mm});
            skLineSegment(sketch, "E25.0.3.24", {"start": v(274.07, 282.6) * mm, "end": v(266.88, 286.75) * mm});
            skLineSegment(sketch, "E25.0.3.25", {"start": v(444.43, 282.6) * mm, "end": v(437.24, 286.75) * mm});
            skLineSegment(sketch, "E25.0.3.26", {"start": v(401.84, 313.95) * mm, "end": v(394.65, 309.8) * mm});
            skLineSegment(sketch, "E25.0.3.27", {"start": v(410.35, 282.6) * mm, "end": v(403.17, 286.75) * mm});
            skLineSegment(sketch, "E25.0.3.28", {"start": v(468.65, 286.75) * mm, "end": v(461.46, 282.6) * mm});
            skLineSegment(sketch, "E25.0.3.29", {"start": v(427.4, 282.6) * mm, "end": v(420.2, 286.75) * mm});
            skLineSegment(sketch, "E25.0.3.30", {"start": v(59.77, 286.75) * mm, "end": v(52.58, 282.6) * mm});
            skLineSegment(sketch, "E25.0.3.31", {"start": v(512.57, 299.2) * mm, "end": v(519.76, 295.05) * mm});
            skLineSegment(sketch, "E25.0.3.32", {"start": v(196.07, 286.75) * mm, "end": v(188.88, 282.6) * mm});
            skLineSegment(sketch, "E25.0.3.33", {"start": v(86.66, 282.6) * mm, "end": v(79.47, 286.75) * mm});
            skLineSegment(sketch, "E25.0.3.34", {"start": v(400.5, 286.75) * mm, "end": v(393.32, 282.6) * mm});
            skLineSegment(sketch, "E25.0.3.35", {"start": v(103.7, 282.6) * mm, "end": v(96.5, 286.75) * mm});
            skLineSegment(sketch, "E25.0.3.36", {"start": v(299.62, 313.95) * mm, "end": v(292.43, 309.8) * mm});
            skLineSegment(sketch, "E25.0.3.37", {"start": v(504.06, 313.95) * mm, "end": v(496.87, 309.8) * mm});
            skLineSegment(sketch, "E25.0.3.38", {"start": v(2.81, 301.5) * mm, "end": v(2.81, 309.8) * mm});
            skLineSegment(sketch, "E25.0.3.39", {"start": v(308.13, 282.6) * mm, "end": v(300.95, 286.75) * mm});
            skLineSegment(sketch, "E25.0.3.40", {"start": v(417.54, 286.75) * mm, "end": v(410.35, 282.6) * mm});
            skLineSegment(sketch, "E25.0.3.41", {"start": v(434.59, 286.75) * mm, "end": v(427.4, 282.6) * mm});
            skLineSegment(sketch, "E25.0.3.42", {"start": v(62.44, 286.75) * mm, "end": v(62.44, 295.05) * mm});
            skLineSegment(sketch, "E25.0.3.43", {"start": v(69.63, 282.6) * mm, "end": v(62.44, 286.75) * mm});
            skLineSegment(sketch, "E25.0.3.44", {"start": v(325.18, 282.6) * mm, "end": v(317.99, 286.75) * mm});
            skLineSegment(sketch, "E25.0.3.45", {"start": v(264.21, 286.75) * mm, "end": v(257.02, 282.6) * mm});
            skLineSegment(sketch, "E25.0.3.46", {"start": v(120.74, 282.6) * mm, "end": v(113.55, 286.75) * mm});
            skLineSegment(sketch, "E25.0.3.47", {"start": v(502.73, 295.05) * mm, "end": v(502.73, 286.75) * mm});
            skLineSegment(sketch, "E25.0.3.48", {"start": v(316.66, 313.95) * mm, "end": v(323.85, 309.8) * mm});
            skLineSegment(sketch, "E25.0.3.49", {"start": v(505.39, 286.75) * mm, "end": v(505.39, 295.05) * mm});
            skLineSegment(sketch, "E25.0.3.50", {"start": v(10, 297.35) * mm, "end": v(2.81, 301.5) * mm});
            skLineSegment(sketch, "E25.0.3.51", {"start": v(59.77, 295.05) * mm, "end": v(59.77, 286.75) * mm});
            skLineSegment(sketch, "E25.0.3.52", {"start": v(291.1, 282.6) * mm, "end": v(283.91, 286.75) * mm});
            skLineSegment(sketch, "E25.0.3.53", {"start": v(511.25, 301.5) * mm, "end": v(511.25, 309.8) * mm});
            skLineSegment(sketch, "E25.0.3.54", {"start": v(392, 309.8) * mm, "end": v(384.8, 313.95) * mm});
            skLineSegment(sketch, "E25.0.3.55", {"start": v(187.55, 309.8) * mm, "end": v(180.36, 313.95) * mm});
            skLineSegment(sketch, "E25.0.3.56", {"start": v(247.18, 295.05) * mm, "end": v(247.18, 286.75) * mm});
            skLineSegment(sketch, "E25.0.3.57", {"start": v(188.88, 299.2) * mm, "end": v(196.07, 295.05) * mm});
            skLineSegment(sketch, "E25.0.3.58", {"start": v(369.1, 295.05) * mm, "end": v(376.29, 299.2) * mm});
            skLineSegment(sketch, "E25.0.3.59", {"start": v(409.03, 301.5) * mm, "end": v(409.03, 309.8) * mm});
            skLineSegment(sketch, "E25.0.3.60", {"start": v(188.88, 282.6) * mm, "end": v(181.7, 286.75) * mm});
            skLineSegment(sketch, "E25.0.3.61", {"start": v(204.59, 301.5) * mm, "end": v(204.59, 309.8) * mm});
            skLineSegment(sketch, "E25.0.3.62", {"start": v(164.66, 295.05) * mm, "end": v(171.85, 299.2) * mm});
            skLineSegment(sketch, "E25.0.3.63", {"start": v(230.15, 295.05) * mm, "end": v(230.15, 286.75) * mm});
            skLineSegment(sketch, "E25.0.3.64", {"start": v(343.54, 309.8) * mm, "end": v(343.54, 301.5) * mm});
            skLineSegment(sketch, "E25.0.3.65", {"start": v(139.1, 309.8) * mm, "end": v(139.1, 301.5) * mm});
            skLineSegment(sketch, "E25.0.3.66", {"start": v(70.95, 301.5) * mm, "end": v(78.14, 297.35) * mm});
            skLineSegment(sketch, "E25.0.3.67", {"start": v(96.5, 286.75) * mm, "end": v(96.5, 295.05) * mm});
            skLineSegment(sketch, "E25.0.3.68", {"start": v(44.07, 313.95) * mm, "end": v(36.88, 309.8) * mm});
            skLineSegment(sketch, "E25.0.3.69", {"start": v(162, 286.75) * mm, "end": v(154.8, 282.6) * mm});
            skLineSegment(sketch, "E25.0.3.70", {"start": v(300.95, 286.75) * mm, "end": v(300.95, 295.05) * mm});
            skLineSegment(sketch, "E25.0.3.71", {"start": v(222.96, 282.6) * mm, "end": v(215.77, 286.75) * mm});
            skLineSegment(sketch, "E25.0.3.72", {"start": v(452.95, 297.35) * mm, "end": v(460.14, 301.5) * mm});
            skLineSegment(sketch, "E25.0.3.73", {"start": v(369.1, 286.75) * mm, "end": v(369.1, 295.05) * mm});
            skLineSegment(sketch, "E25.0.3.74", {"start": v(366.43, 286.75) * mm, "end": v(359.24, 282.6) * mm});
            skLineSegment(sketch, "E25.0.3.75", {"start": v(164.66, 286.75) * mm, "end": v(164.66, 295.05) * mm});
            skLineSegment(sketch, "E25.0.3.76", {"start": v(248.5, 297.35) * mm, "end": v(255.7, 301.5) * mm});
            skLineSegment(sketch, "E25.0.3.77", {"start": v(249.84, 295.05) * mm, "end": v(257.02, 299.2) * mm});
            skLineSegment(sketch, "E25.0.3.78", {"start": v(393.32, 282.6) * mm, "end": v(386.13, 286.75) * mm});
            skLineSegment(sketch, "E25.0.3.79", {"start": v(62.44, 295.05) * mm, "end": v(69.63, 299.2) * mm});
            skLineSegment(sketch, "E25.0.3.80", {"start": v(136.44, 301.5) * mm, "end": v(136.44, 309.8) * mm});
            skLineSegment(sketch, "E25.0.3.81", {"start": v(102.37, 301.5) * mm, "end": v(102.37, 309.8) * mm});
            skLineSegment(sketch, "E25.0.3.82", {"start": v(418.88, 313.95) * mm, "end": v(426.07, 309.8) * mm});
            skLineSegment(sketch, "E25.0.3.83", {"start": v(454.28, 295.05) * mm, "end": v(461.46, 299.2) * mm});
            skLineSegment(sketch, "E25.0.3.84", {"start": v(78.14, 313.95) * mm, "end": v(70.95, 309.8) * mm});
            skLineSegment(sketch, "E25.0.3.85", {"start": v(105.03, 301.5) * mm, "end": v(105.03, 309.8) * mm});
            skLineSegment(sketch, "E25.0.3.86", {"start": v(190.2, 301.5) * mm, "end": v(197.4, 297.35) * mm});
            skLineSegment(sketch, "E25.0.3.87", {"start": v(352.06, 286.75) * mm, "end": v(352.06, 295.05) * mm});
            skLineSegment(sketch, "E25.0.3.88", {"start": v(400.5, 295.05) * mm, "end": v(400.5, 286.75) * mm});
            skLineSegment(sketch, "E25.0.3.89", {"start": v(299.62, 297.35) * mm, "end": v(306.8, 301.5) * mm});
            skLineSegment(sketch, "E25.0.3.90", {"start": v(190.2, 309.8) * mm, "end": v(190.2, 301.5) * mm});
            skLineSegment(sketch, "E25.0.3.91", {"start": v(76.82, 295.05) * mm, "end": v(76.82, 286.75) * mm});
            skLineSegment(sketch, "E25.0.3.92", {"start": v(392, 301.5) * mm, "end": v(392, 309.8) * mm});
            skLineSegment(sketch, "E25.0.3.93", {"start": v(309.47, 309.8) * mm, "end": v(316.66, 313.95) * mm});
            skLineSegment(sketch, "E25.0.3.94", {"start": v(349.4, 286.75) * mm, "end": v(342.21, 282.6) * mm});
            skLineSegment(sketch, "E25.0.3.95", {"start": v(257.02, 299.2) * mm, "end": v(264.21, 295.05) * mm});
            skLineSegment(sketch, "E25.0.3.96", {"start": v(61.1, 313.95) * mm, "end": v(68.3, 309.8) * mm});
            skLineSegment(sketch, "E25.0.3.97", {"start": v(146.29, 313.95) * mm, "end": v(139.1, 309.8) * mm});
            skLineSegment(sketch, "E25.0.3.98", {"start": v(154.8, 282.6) * mm, "end": v(147.62, 286.75) * mm});
            skLineSegment(sketch, "E25.0.3.99", {"start": v(306.8, 309.8) * mm, "end": v(299.62, 313.95) * mm});
            skLineSegment(sketch, "E25.0.3.100", {"start": v(87.99, 301.5) * mm, "end": v(95.18, 297.35) * mm});
            skLineSegment(sketch, "E25.0.3.101", {"start": v(105.03, 309.8) * mm, "end": v(112.22, 313.95) * mm});
            skLineSegment(sketch, "E25.0.3.102", {"start": v(102.37, 309.8) * mm, "end": v(95.18, 313.95) * mm});
            skLineSegment(sketch, "E25.0.3.103", {"start": v(187.55, 301.5) * mm, "end": v(187.55, 309.8) * mm});
            skLineSegment(sketch, "E25.0.3.104", {"start": v(61.1, 297.35) * mm, "end": v(53.92, 301.5) * mm});
            skLineSegment(sketch, "E25.0.3.105", {"start": v(437.24, 286.75) * mm, "end": v(437.24, 295.05) * mm});
            skLineSegment(sketch, "E25.0.3.106", {"start": v(393.32, 299.2) * mm, "end": v(400.5, 295.05) * mm});
            skLineSegment(sketch, "E25.0.3.107", {"start": v(232.8, 286.75) * mm, "end": v(232.8, 295.05) * mm});
            skLineSegment(sketch, "E25.0.3.108", {"start": v(87.99, 309.8) * mm, "end": v(87.99, 301.5) * mm});
            skLineSegment(sketch, "E25.0.3.109", {"start": v(113.55, 286.75) * mm, "end": v(113.55, 295.05) * mm});
            skLineSegment(sketch, "E25.0.3.110", {"start": v(332.37, 295.05) * mm, "end": v(332.37, 286.75) * mm});
            skLineSegment(sketch, "E25.0.3.111", {"start": v(266.88, 286.75) * mm, "end": v(266.88, 295.05) * mm});
            skLineSegment(sketch, "E25.0.3.112", {"start": v(180.36, 313.95) * mm, "end": v(173.17, 309.8) * mm});
            skLineSegment(sketch, "E25.0.3.113", {"start": v(181.7, 295.05) * mm, "end": v(188.88, 299.2) * mm});
            skLineSegment(sketch, "E25.0.3.114", {"start": v(68.3, 309.8) * mm, "end": v(68.3, 301.5) * mm});
            skLineSegment(sketch, "E25.0.3.115", {"start": v(317.99, 286.75) * mm, "end": v(317.99, 295.05) * mm});
            skLineSegment(sketch, "E25.0.3.116", {"start": v(485.7, 286.75) * mm, "end": v(478.5, 282.6) * mm});
            skLineSegment(sketch, "E25.0.3.117", {"start": v(10, 313.95) * mm, "end": v(17.19, 309.8) * mm});
            skLineSegment(sketch, "E25.0.3.118", {"start": v(376.29, 282.6) * mm, "end": v(369.1, 286.75) * mm});
            skLineSegment(sketch, "E25.0.3.119", {"start": v(452.95, 313.95) * mm, "end": v(445.76, 309.8) * mm});
            skLineSegment(sketch, "E25.0.3.120", {"start": v(315.32, 286.75) * mm, "end": v(308.13, 282.6) * mm});
            skLineSegment(sketch, "E25.0.3.121", {"start": v(93.85, 295.05) * mm, "end": v(93.85, 286.75) * mm});
            skLineSegment(sketch, "E25.0.3.122", {"start": v(35.55, 282.6) * mm, "end": v(28.36, 286.75) * mm});
            skLineSegment(sketch, "E25.0.3.123", {"start": v(45.4, 286.75) * mm, "end": v(45.4, 295.05) * mm});
            skLineSegment(sketch, "E25.0.3.124", {"start": v(42.74, 286.75) * mm, "end": v(35.55, 282.6) * mm});
            skLineSegment(sketch, "E25.0.3.125", {"start": v(434.59, 295.05) * mm, "end": v(434.59, 286.75) * mm});
            skLineSegment(sketch, "E25.0.3.126", {"start": v(340.88, 301.5) * mm, "end": v(340.88, 309.8) * mm});
            skLineSegment(sketch, "E25.0.3.127", {"start": v(394.65, 301.5) * mm, "end": v(401.84, 297.35) * mm});
            skLineSegment(sketch, "E25.0.3.128", {"start": v(153.48, 309.8) * mm, "end": v(146.29, 313.95) * mm});
            skLineSegment(sketch, "E25.0.3.129", {"start": v(52.58, 282.6) * mm, "end": v(45.4, 286.75) * mm});
            skLineSegment(sketch, "E25.0.3.130", {"start": v(25.7, 295.05) * mm, "end": v(25.7, 286.75) * mm});
            skLineSegment(sketch, "E25.0.3.131", {"start": v(28.36, 286.75) * mm, "end": v(28.36, 295.05) * mm});
            skLineSegment(sketch, "E25.0.3.132", {"start": v(45.4, 295.05) * mm, "end": v(52.58, 299.2) * mm});
            skLineSegment(sketch, "E25.0.3.133", {"start": v(451.62, 286.75) * mm, "end": v(444.43, 282.6) * mm});
            skLineSegment(sketch, "E25.0.3.134", {"start": v(411.7, 301.5) * mm, "end": v(411.7, 309.8) * mm});
            skLineSegment(sketch, "E25.0.3.135", {"start": v(342.21, 282.6) * mm, "end": v(335.02, 286.75) * mm});
            skLineSegment(sketch, "E25.0.3.136", {"start": v(443.1, 301.5) * mm, "end": v(443.1, 309.8) * mm});
            skLineSegment(sketch, "E25.0.3.137", {"start": v(357.92, 309.8) * mm, "end": v(350.73, 313.95) * mm});
            skLineSegment(sketch, "E25.0.3.138", {"start": v(289.77, 301.5) * mm, "end": v(289.77, 309.8) * mm});
            skLineSegment(sketch, "E25.0.3.139", {"start": v(204.59, 309.8) * mm, "end": v(197.4, 313.95) * mm});
            skLineSegment(sketch, "E25.0.3.140", {"start": v(198.73, 295.05) * mm, "end": v(205.91, 299.2) * mm});
            skLineSegment(sketch, "E25.0.3.141", {"start": v(454.28, 286.75) * mm, "end": v(454.28, 295.05) * mm});
            skLineSegment(sketch, "E25.0.3.142", {"start": v(86.66, 299.2) * mm, "end": v(93.85, 295.05) * mm});
            skLineSegment(sketch, "E25.0.3.143", {"start": v(443.1, 309.8) * mm, "end": v(435.91, 313.95) * mm});
            skLineSegment(sketch, "E25.0.3.144", {"start": v(435.91, 313.95) * mm, "end": v(428.72, 309.8) * mm});
            skLineSegment(sketch, "E25.0.3.145", {"start": v(437.24, 295.05) * mm, "end": v(444.43, 299.2) * mm});
            skLineSegment(sketch, "E25.0.3.146", {"start": v(231.47, 313.95) * mm, "end": v(224.28, 309.8) * mm});
            skLineSegment(sketch, "E25.0.3.147", {"start": v(79.47, 286.75) * mm, "end": v(79.47, 295.05) * mm});
            skLineSegment(sketch, "E25.0.3.148", {"start": v(309.47, 301.5) * mm, "end": v(309.47, 309.8) * mm});
            skLineSegment(sketch, "E25.0.3.149", {"start": v(214.44, 313.95) * mm, "end": v(221.63, 309.8) * mm});
            skLineSegment(sketch, "E25.0.3.150", {"start": v(238.66, 309.8) * mm, "end": v(231.47, 313.95) * mm});
            skLineSegment(sketch, "E25.0.3.151", {"start": v(394.65, 309.8) * mm, "end": v(394.65, 301.5) * mm});
            skLineSegment(sketch, "E25.0.3.152", {"start": v(445.76, 301.5) * mm, "end": v(452.95, 297.35) * mm});
            skLineSegment(sketch, "E25.0.3.153", {"start": v(241.32, 301.5) * mm, "end": v(248.5, 297.35) * mm});
            skLineSegment(sketch, "E25.0.3.154", {"start": v(231.47, 297.35) * mm, "end": v(238.66, 301.5) * mm});
            skLineSegment(sketch, "E25.0.3.155", {"start": v(79.47, 295.05) * mm, "end": v(86.66, 299.2) * mm});
            skLineSegment(sketch, "E25.0.3.156", {"start": v(350.73, 313.95) * mm, "end": v(343.54, 309.8) * mm});
            skLineSegment(sketch, "E25.0.3.157", {"start": v(196.07, 295.05) * mm, "end": v(196.07, 286.75) * mm});
            skLineSegment(sketch, "E25.0.3.158", {"start": v(240, 282.6) * mm, "end": v(232.8, 286.75) * mm});
            skLineSegment(sketch, "E25.0.3.159", {"start": v(69.63, 299.2) * mm, "end": v(76.82, 295.05) * mm});
            skLineSegment(sketch, "E25.0.3.160", {"start": v(349.4, 295.05) * mm, "end": v(349.4, 286.75) * mm});
            skLineSegment(sketch, "E25.0.3.161", {"start": v(383.48, 286.75) * mm, "end": v(376.29, 282.6) * mm});
            skLineSegment(sketch, "E25.0.3.162", {"start": v(144.96, 295.05) * mm, "end": v(144.96, 286.75) * mm});
            skLineSegment(sketch, "E25.0.3.163", {"start": v(179.04, 286.75) * mm, "end": v(171.85, 282.6) * mm});
            skLineSegment(sketch, "E25.0.3.164", {"start": v(386.13, 295.05) * mm, "end": v(393.32, 299.2) * mm});
            skLineSegment(sketch, "E25.0.3.165", {"start": v(435.91, 297.35) * mm, "end": v(443.1, 301.5) * mm});
            skLineSegment(sketch, "E25.0.3.166", {"start": v(504.06, 297.35) * mm, "end": v(511.25, 301.5) * mm});
            skLineSegment(sketch, "E25.0.3.167", {"start": v(403.17, 286.75) * mm, "end": v(403.17, 295.05) * mm});
            skLineSegment(sketch, "E25.0.3.168", {"start": v(241.32, 309.8) * mm, "end": v(241.32, 301.5) * mm});
            skLineSegment(sketch, "E25.0.3.169", {"start": v(359.24, 282.6) * mm, "end": v(352.06, 286.75) * mm});
            skLineSegment(sketch, "E25.0.3.170", {"start": v(213.1, 286.75) * mm, "end": v(205.91, 282.6) * mm});
            skLineSegment(sketch, "E25.0.3.171", {"start": v(34.22, 309.8) * mm, "end": v(27.03, 313.95) * mm});
            skLineSegment(sketch, "E25.0.3.172", {"start": v(461.46, 299.2) * mm, "end": v(468.65, 295.05) * mm});
            skLineSegment(sketch, "E25.0.3.173", {"start": v(505.39, 295.05) * mm, "end": v(512.57, 299.2) * mm});
            skLineSegment(sketch, "E25.0.3.174", {"start": v(300.95, 295.05) * mm, "end": v(308.13, 299.2) * mm});
            skLineSegment(sketch, "E25.0.3.175", {"start": v(230.15, 286.75) * mm, "end": v(222.96, 282.6) * mm});
            skLineSegment(sketch, "E25.0.3.176", {"start": v(265.55, 297.35) * mm, "end": v(258.36, 301.5) * mm});
            skLineSegment(sketch, "E25.0.3.177", {"start": v(144.96, 286.75) * mm, "end": v(137.77, 282.6) * mm});
            skLineSegment(sketch, "E25.0.3.178", {"start": v(27.03, 313.95) * mm, "end": v(19.84, 309.8) * mm});
            skLineSegment(sketch, "E25.0.3.179", {"start": v(384.8, 313.95) * mm, "end": v(377.61, 309.8) * mm});
            skLineSegment(sketch, "E25.0.3.180", {"start": v(340.88, 309.8) * mm, "end": v(333.7, 313.95) * mm});
            skLineSegment(sketch, "E25.0.3.181", {"start": v(136.44, 309.8) * mm, "end": v(129.25, 313.95) * mm});
            skLineSegment(sketch, "E25.0.3.182", {"start": v(198.73, 286.75) * mm, "end": v(198.73, 295.05) * mm});
            skLineSegment(sketch, "E25.0.3.183", {"start": v(70.95, 309.8) * mm, "end": v(70.95, 301.5) * mm});
            skLineSegment(sketch, "E25.0.3.184", {"start": v(127.93, 295.05) * mm, "end": v(127.93, 286.75) * mm});
            skLineSegment(sketch, "E25.0.3.185", {"start": v(461.46, 282.6) * mm, "end": v(454.28, 286.75) * mm});
            skLineSegment(sketch, "E25.0.3.186", {"start": v(444.43, 299.2) * mm, "end": v(451.62, 295.05) * mm});
            skLineSegment(sketch, "E25.0.3.187", {"start": v(445.76, 309.8) * mm, "end": v(445.76, 301.5) * mm});
            skLineSegment(sketch, "E25.0.3.188", {"start": v(240, 299.2) * mm, "end": v(247.18, 295.05) * mm});
            skLineSegment(sketch, "E25.0.3.189", {"start": v(298.29, 295.05) * mm, "end": v(298.29, 286.75) * mm});
            skLineSegment(sketch, "E25.0.3.190", {"start": v(471.32, 286.75) * mm, "end": v(471.32, 295.05) * mm});
            skLineSegment(sketch, "E25.0.3.191", {"start": v(207.25, 301.5) * mm, "end": v(207.25, 309.8) * mm});
            skLineSegment(sketch, "E25.0.3.192", {"start": v(281.26, 286.75) * mm, "end": v(274.07, 282.6) * mm});
            skLineSegment(sketch, "E25.0.3.193", {"start": v(257.02, 282.6) * mm, "end": v(249.84, 286.75) * mm});
            skLineSegment(sketch, "E25.0.3.194", {"start": v(248.5, 313.95) * mm, "end": v(241.32, 309.8) * mm});
            skLineSegment(sketch, "E25.0.3.195", {"start": v(451.62, 295.05) * mm, "end": v(451.62, 286.75) * mm});
            skLineSegment(sketch, "E25.0.3.196", {"start": v(110.88, 286.75) * mm, "end": v(103.7, 282.6) * mm});
            skLineSegment(sketch, "E25.0.3.197", {"start": v(401.84, 297.35) * mm, "end": v(409.03, 301.5) * mm});
            skLineSegment(sketch, "E25.0.3.198", {"start": v(292.43, 309.8) * mm, "end": v(292.43, 301.5) * mm});
            skLineSegment(sketch, "E25.0.3.199", {"start": v(171.85, 282.6) * mm, "end": v(164.66, 286.75) * mm});
            skLineSegment(sketch, "E25.0.3.200", {"start": v(197.4, 297.35) * mm, "end": v(204.59, 301.5) * mm});
            skLineSegment(sketch, "E25.0.3.201", {"start": v(52.58, 299.2) * mm, "end": v(59.77, 295.05) * mm});
            skLineSegment(sketch, "E25.0.3.202", {"start": v(411.7, 309.8) * mm, "end": v(418.88, 313.95) * mm});
            skLineSegment(sketch, "E25.0.3.203", {"start": v(409.03, 309.8) * mm, "end": v(401.84, 313.95) * mm});
            skLineSegment(sketch, "E25.0.3.204", {"start": v(207.25, 309.8) * mm, "end": v(214.44, 313.95) * mm});
            skLineSegment(sketch, "E25.0.3.205", {"start": v(403.17, 295.05) * mm, "end": v(410.35, 299.2) * mm});
            skLineSegment(sketch, "E25.0.3.206", {"start": v(495.54, 282.6) * mm, "end": v(488.35, 286.75) * mm});
            skLineSegment(sketch, "E25.0.3.207", {"start": v(468.65, 295.05) * mm, "end": v(468.65, 286.75) * mm});
            skLineSegment(sketch, "E25.0.3.208", {"start": v(264.21, 295.05) * mm, "end": v(264.21, 286.75) * mm});
            skLineSegment(sketch, "E25.0.3.209", {"start": v(238.66, 301.5) * mm, "end": v(238.66, 309.8) * mm});
            skLineSegment(sketch, "E25.0.3.210", {"start": v(247.18, 286.75) * mm, "end": v(240, 282.6) * mm});
            skLineSegment(sketch, "E25.0.3.211", {"start": v(85.33, 301.5) * mm, "end": v(85.33, 309.8) * mm});
            skLineSegment(sketch, "E25.0.3.212", {"start": v(137.77, 282.6) * mm, "end": v(130.58, 286.75) * mm});
            skLineSegment(sketch, "E25.0.3.213", {"start": v(374.96, 301.5) * mm, "end": v(367.77, 297.35) * mm});
            skLineSegment(sketch, "E25.0.3.214", {"start": v(323.85, 309.8) * mm, "end": v(323.85, 301.5) * mm});
            skLineSegment(sketch, "E25.0.3.215", {"start": v(266.88, 295.05) * mm, "end": v(274.07, 299.2) * mm});
            skLineSegment(sketch, "E25.0.3.216", {"start": v(326.5, 309.8) * mm, "end": v(326.5, 301.5) * mm});
            skLineSegment(sketch, "E25.0.3.217", {"start": v(232.8, 295.05) * mm, "end": v(240, 299.2) * mm});
            skLineSegment(sketch, "E25.0.3.218", {"start": v(306.8, 301.5) * mm, "end": v(306.8, 309.8) * mm});
            skLineSegment(sketch, "E25.0.3.219", {"start": v(119.4, 309.8) * mm, "end": v(119.4, 301.5) * mm});
            skLineSegment(sketch, "E25.0.3.220", {"start": v(122.06, 309.8) * mm, "end": v(122.06, 301.5) * mm});
            skLineSegment(sketch, "E25.0.3.221", {"start": v(170.52, 301.5) * mm, "end": v(163.33, 297.35) * mm});
            skLineSegment(sketch, "E25.0.3.222", {"start": v(428.72, 309.8) * mm, "end": v(428.72, 301.5) * mm});
            skLineSegment(sketch, "E25.0.3.223", {"start": v(51.26, 301.5) * mm, "end": v(51.26, 309.8) * mm});
            skLineSegment(sketch, "E25.0.3.224", {"start": v(386.13, 286.75) * mm, "end": v(386.13, 295.05) * mm});
            skLineSegment(sketch, "E25.0.3.225", {"start": v(44.07, 297.35) * mm, "end": v(51.26, 301.5) * mm});
            skLineSegment(sketch, "E25.0.3.226", {"start": v(462.8, 309.8) * mm, "end": v(469.99, 313.95) * mm});
            skLineSegment(sketch, "E25.0.3.227", {"start": v(214.44, 297.35) * mm, "end": v(207.25, 301.5) * mm});
            skLineSegment(sketch, "E25.0.3.228", {"start": v(205.91, 299.2) * mm, "end": v(213.1, 295.05) * mm});
            skLineSegment(sketch, "E25.0.3.229", {"start": v(366.43, 295.05) * mm, "end": v(366.43, 286.75) * mm});
            skLineSegment(sketch, "E25.0.3.230", {"start": v(130.58, 295.05) * mm, "end": v(137.77, 299.2) * mm});
            skLineSegment(sketch, "E25.0.3.231", {"start": v(224.28, 309.8) * mm, "end": v(224.28, 301.5) * mm});
            skLineSegment(sketch, "E25.0.3.232", {"start": v(384.8, 297.35) * mm, "end": v(392, 301.5) * mm});
            skLineSegment(sketch, "E25.0.3.233", {"start": v(275.4, 301.5) * mm, "end": v(282.58, 297.35) * mm});
            skLineSegment(sketch, "E25.0.3.234", {"start": v(19.84, 301.5) * mm, "end": v(27.03, 297.35) * mm});
            skLineSegment(sketch, "E25.0.3.235", {"start": v(180.36, 297.35) * mm, "end": v(187.55, 301.5) * mm});
            skLineSegment(sketch, "E25.0.3.236", {"start": v(410.35, 299.2) * mm, "end": v(417.54, 295.05) * mm});
            skLineSegment(sketch, "E25.0.3.237", {"start": v(255.7, 309.8) * mm, "end": v(248.5, 313.95) * mm});
            skLineSegment(sketch, "E25.0.3.238", {"start": v(53.92, 309.8) * mm, "end": v(61.1, 313.95) * mm});
            skLineSegment(sketch, "E25.0.3.239", {"start": v(162, 295.05) * mm, "end": v(162, 286.75) * mm});
            skLineSegment(sketch, "E25.0.3.240", {"start": v(51.26, 309.8) * mm, "end": v(44.07, 313.95) * mm});
            skLineSegment(sketch, "E25.0.3.241", {"start": v(427.4, 299.2) * mm, "end": v(434.59, 295.05) * mm});
            skLineSegment(sketch, "E25.0.3.242", {"start": v(460.14, 309.8) * mm, "end": v(452.95, 313.95) * mm});
            skLineSegment(sketch, "E25.0.3.243", {"start": v(272.74, 301.5) * mm, "end": v(265.55, 297.35) * mm});
            skLineSegment(sketch, "E25.0.3.244", {"start": v(181.7, 286.75) * mm, "end": v(181.7, 295.05) * mm});
            skLineSegment(sketch, "E25.0.3.245", {"start": v(335.02, 295.05) * mm, "end": v(342.21, 299.2) * mm});
            skLineSegment(sketch, "E25.0.3.246", {"start": v(221.63, 309.8) * mm, "end": v(221.63, 301.5) * mm});
            skLineSegment(sketch, "E25.0.3.247", {"start": v(68.3, 301.5) * mm, "end": v(61.1, 297.35) * mm});
            skLineSegment(sketch, "E25.0.3.248", {"start": v(130.58, 286.75) * mm, "end": v(130.58, 295.05) * mm});
            skLineSegment(sketch, "E25.0.3.249", {"start": v(477.18, 301.5) * mm, "end": v(469.99, 297.35) * mm});
            skLineSegment(sketch, "E25.0.3.250", {"start": v(469.99, 313.95) * mm, "end": v(477.18, 309.8) * mm});
            skLineSegment(sketch, "E25.0.3.251", {"start": v(360.58, 301.5) * mm, "end": v(360.58, 309.8) * mm});
            skLineSegment(sketch, "E25.0.3.252", {"start": v(122.06, 301.5) * mm, "end": v(129.25, 297.35) * mm});
            skLineSegment(sketch, "E25.0.3.253", {"start": v(95.18, 297.35) * mm, "end": v(102.37, 301.5) * mm});
            skLineSegment(sketch, "E25.0.3.254", {"start": v(137.77, 299.2) * mm, "end": v(144.96, 295.05) * mm});
            skLineSegment(sketch, "E25.0.3.255", {"start": v(469.99, 297.35) * mm, "end": v(462.8, 301.5) * mm});
            skLineSegment(sketch, "E25.0.3.256", {"start": v(417.54, 295.05) * mm, "end": v(417.54, 286.75) * mm});
            skLineSegment(sketch, "E25.0.3.257", {"start": v(120.74, 299.2) * mm, "end": v(127.93, 295.05) * mm});
            skLineSegment(sketch, "E25.0.3.258", {"start": v(477.18, 309.8) * mm, "end": v(477.18, 301.5) * mm});
            skLineSegment(sketch, "E25.0.3.259", {"start": v(420.2, 295.05) * mm, "end": v(427.4, 299.2) * mm});
            skLineSegment(sketch, "E25.0.3.260", {"start": v(275.4, 309.8) * mm, "end": v(275.4, 301.5) * mm});
            skLineSegment(sketch, "E25.0.3.261", {"start": v(255.7, 301.5) * mm, "end": v(255.7, 309.8) * mm});
            skLineSegment(sketch, "E25.0.3.262", {"start": v(215.77, 295.05) * mm, "end": v(222.96, 299.2) * mm});
            skLineSegment(sketch, "E25.0.3.263", {"start": v(42.74, 295.05) * mm, "end": v(42.74, 286.75) * mm});
            skLineSegment(sketch, "E25.0.3.264", {"start": v(350.73, 297.35) * mm, "end": v(357.92, 301.5) * mm});
            skLineSegment(sketch, "E25.0.3.265", {"start": v(78.14, 297.35) * mm, "end": v(85.33, 301.5) * mm});
            skLineSegment(sketch, "E25.0.3.266", {"start": v(119.4, 301.5) * mm, "end": v(112.22, 297.35) * mm});
            skLineSegment(sketch, "E25.0.3.267", {"start": v(19.84, 309.8) * mm, "end": v(19.84, 301.5) * mm});
            skLineSegment(sketch, "E25.0.3.268", {"start": v(496.87, 301.5) * mm, "end": v(504.06, 297.35) * mm});
            skLineSegment(sketch, "E25.0.3.269", {"start": v(325.18, 299.2) * mm, "end": v(332.37, 295.05) * mm});
            skLineSegment(sketch, "E25.0.3.270", {"start": v(367.77, 313.95) * mm, "end": v(374.96, 309.8) * mm});
            skLineSegment(sketch, "E25.0.3.271", {"start": v(258.36, 301.5) * mm, "end": v(258.36, 309.8) * mm});
            skLineSegment(sketch, "E25.0.3.272", {"start": v(163.33, 313.95) * mm, "end": v(170.52, 309.8) * mm});
            skLineSegment(sketch, "E25.0.3.273", {"start": v(179.04, 295.05) * mm, "end": v(179.04, 286.75) * mm});
            skLineSegment(sketch, "E25.0.3.274", {"start": v(249.84, 286.75) * mm, "end": v(249.84, 295.05) * mm});
            skLineSegment(sketch, "E25.0.3.275", {"start": v(139.1, 301.5) * mm, "end": v(146.29, 297.35) * mm});
            skLineSegment(sketch, "E25.0.3.276", {"start": v(418.88, 297.35) * mm, "end": v(411.7, 301.5) * mm});
            skLineSegment(sketch, "E25.0.3.277", {"start": v(426.07, 309.8) * mm, "end": v(426.07, 301.5) * mm});
            skLineSegment(sketch, "E25.0.3.278", {"start": v(367.77, 297.35) * mm, "end": v(360.58, 301.5) * mm});
            skLineSegment(sketch, "E25.0.3.279", {"start": v(352.06, 295.05) * mm, "end": v(359.24, 299.2) * mm});
            skLineSegment(sketch, "E25.0.3.280", {"start": v(163.33, 297.35) * mm, "end": v(156.14, 301.5) * mm});
            skLineSegment(sketch, "E25.0.3.281", {"start": v(112.22, 297.35) * mm, "end": v(105.03, 301.5) * mm});
            skLineSegment(sketch, "E25.0.3.282", {"start": v(487.02, 313.95) * mm, "end": v(479.83, 309.8) * mm});
            skLineSegment(sketch, "E25.0.3.283", {"start": v(374.96, 309.8) * mm, "end": v(374.96, 301.5) * mm});
            skLineSegment(sketch, "E25.0.3.284", {"start": v(17.19, 301.5) * mm, "end": v(10, 297.35) * mm});
            skLineSegment(sketch, "E25.0.3.285", {"start": v(221.63, 301.5) * mm, "end": v(214.44, 297.35) * mm});
            skLineSegment(sketch, "E25.0.3.286", {"start": v(282.58, 313.95) * mm, "end": v(275.4, 309.8) * mm});
            skLineSegment(sketch, "E25.0.3.287", {"start": v(335.02, 286.75) * mm, "end": v(335.02, 295.05) * mm});
            skLineSegment(sketch, "E25.0.3.288", {"start": v(170.52, 309.8) * mm, "end": v(170.52, 301.5) * mm});
            skLineSegment(sketch, "E25.0.3.289", {"start": v(291.1, 299.2) * mm, "end": v(298.29, 295.05) * mm});
            skLineSegment(sketch, "E25.0.3.290", {"start": v(173.17, 309.8) * mm, "end": v(173.17, 301.5) * mm});
            skLineSegment(sketch, "E25.0.3.291", {"start": v(495.54, 299.2) * mm, "end": v(502.73, 295.05) * mm});
            skLineSegment(sketch, "E25.0.3.292", {"start": v(147.62, 286.75) * mm, "end": v(147.62, 295.05) * mm});
            skLineSegment(sketch, "E25.0.3.293", {"start": v(153.48, 301.5) * mm, "end": v(153.48, 309.8) * mm});
            skLineSegment(sketch, "E25.0.3.294", {"start": v(222.96, 299.2) * mm, "end": v(230.15, 295.05) * mm});
            skLineSegment(sketch, "E25.0.3.295", {"start": v(479.83, 309.8) * mm, "end": v(479.83, 301.5) * mm});
            skLineSegment(sketch, "E25.0.3.296", {"start": v(420.2, 286.75) * mm, "end": v(420.2, 295.05) * mm});
            skLineSegment(sketch, "E25.0.3.297", {"start": v(326.5, 301.5) * mm, "end": v(333.7, 297.35) * mm});
            skLineSegment(sketch, "E25.0.3.298", {"start": v(173.17, 301.5) * mm, "end": v(180.36, 297.35) * mm});
            skLineSegment(sketch, "E25.0.3.299", {"start": v(342.21, 299.2) * mm, "end": v(349.4, 295.05) * mm});
            skLineSegment(sketch, "E25.0.3.300", {"start": v(265.55, 313.95) * mm, "end": v(272.74, 309.8) * mm});
            skLineSegment(sketch, "E25.0.3.301", {"start": v(274.07, 299.2) * mm, "end": v(281.26, 295.05) * mm});
            skLineSegment(sketch, "E25.0.3.302", {"start": v(215.77, 286.75) * mm, "end": v(215.77, 295.05) * mm});
            skLineSegment(sketch, "E25.0.3.303", {"start": v(462.8, 301.5) * mm, "end": v(462.8, 309.8) * mm});
            skLineSegment(sketch, "E25.0.3.304", {"start": v(281.26, 295.05) * mm, "end": v(281.26, 286.75) * mm});
            skLineSegment(sketch, "E25.0.3.305", {"start": v(156.14, 301.5) * mm, "end": v(156.14, 309.8) * mm});
            skLineSegment(sketch, "E25.0.3.306", {"start": v(213.1, 295.05) * mm, "end": v(213.1, 286.75) * mm});
            skLineSegment(sketch, "E25.0.3.307", {"start": v(96.5, 295.05) * mm, "end": v(103.7, 299.2) * mm});
            skLineSegment(sketch, "E25.0.3.308", {"start": v(460.14, 301.5) * mm, "end": v(460.14, 309.8) * mm});
            skLineSegment(sketch, "E25.0.3.309", {"start": v(323.85, 301.5) * mm, "end": v(316.66, 297.35) * mm});
            skLineSegment(sketch, "E25.0.3.310", {"start": v(272.74, 309.8) * mm, "end": v(272.74, 301.5) * mm});
            skLineSegment(sketch, "E25.0.3.311", {"start": v(377.61, 301.5) * mm, "end": v(384.8, 297.35) * mm});
            skLineSegment(sketch, "E25.0.3.312", {"start": v(282.58, 297.35) * mm, "end": v(289.77, 301.5) * mm});
            skLineSegment(sketch, "E25.0.3.313", {"start": v(146.29, 297.35) * mm, "end": v(153.48, 301.5) * mm});
            skLineSegment(sketch, "E25.0.3.314", {"start": v(343.54, 301.5) * mm, "end": v(350.73, 297.35) * mm});
            skLineSegment(sketch, "E25.0.3.315", {"start": v(376.29, 299.2) * mm, "end": v(383.48, 295.05) * mm});
            skLineSegment(sketch, "E25.0.3.316", {"start": v(171.85, 299.2) * mm, "end": v(179.04, 295.05) * mm});
            skLineSegment(sketch, "E25.0.3.317", {"start": v(53.92, 301.5) * mm, "end": v(53.92, 309.8) * mm});
            skLineSegment(sketch, "E25.0.3.318", {"start": v(292.43, 301.5) * mm, "end": v(299.62, 297.35) * mm});
            skLineSegment(sketch, "E25.0.3.319", {"start": v(377.61, 309.8) * mm, "end": v(377.61, 301.5) * mm});
            skLineSegment(sketch, "E25.0.3.320", {"start": v(383.48, 295.05) * mm, "end": v(383.48, 286.75) * mm});
            skLineSegment(sketch, "E25.0.3.321", {"start": v(129.25, 297.35) * mm, "end": v(136.44, 301.5) * mm});
            skLineSegment(sketch, "E25.0.3.322", {"start": v(428.72, 301.5) * mm, "end": v(435.91, 297.35) * mm});
            skLineSegment(sketch, "E25.0.3.323", {"start": v(496.87, 309.8) * mm, "end": v(496.87, 301.5) * mm});
            skLineSegment(sketch, "E25.0.3.324", {"start": v(224.28, 301.5) * mm, "end": v(231.47, 297.35) * mm});
            skLineSegment(sketch, "E25.0.3.325", {"start": v(333.7, 297.35) * mm, "end": v(340.88, 301.5) * mm});
            skLineSegment(sketch, "E25.0.3.326", {"start": v(11.33, 295.05) * mm, "end": v(18.52, 299.2) * mm});
            skLineSegment(sketch, "E25.0.3.327", {"start": v(18.52, 299.2) * mm, "end": v(25.7, 295.05) * mm});
            skLineSegment(sketch, "E25.0.3.328", {"start": v(494.21, 301.5) * mm, "end": v(494.21, 309.8) * mm});
            skLineSegment(sketch, "E25.0.3.329", {"start": v(315.32, 295.05) * mm, "end": v(315.32, 286.75) * mm});
            skLineSegment(sketch, "E25.0.3.330", {"start": v(360.58, 309.8) * mm, "end": v(367.77, 313.95) * mm});
            skLineSegment(sketch, "E25.0.3.331", {"start": v(316.66, 297.35) * mm, "end": v(309.47, 301.5) * mm});
            skLineSegment(sketch, "E25.0.3.332", {"start": v(308.13, 299.2) * mm, "end": v(315.32, 295.05) * mm});
            skLineSegment(sketch, "E25.0.3.333", {"start": v(147.62, 295.05) * mm, "end": v(154.8, 299.2) * mm});
            skLineSegment(sketch, "E25.0.3.334", {"start": v(359.24, 299.2) * mm, "end": v(366.43, 295.05) * mm});
            skLineSegment(sketch, "E25.0.3.335", {"start": v(110.88, 295.05) * mm, "end": v(110.88, 286.75) * mm});
            skLineSegment(sketch, "E25.0.3.336", {"start": v(154.8, 299.2) * mm, "end": v(162, 295.05) * mm});
            skLineSegment(sketch, "E25.0.3.337", {"start": v(17.19, 309.8) * mm, "end": v(17.19, 301.5) * mm});
            skLineSegment(sketch, "E25.0.3.338", {"start": v(156.14, 309.8) * mm, "end": v(163.33, 313.95) * mm});
            skLineSegment(sketch, "E25.0.3.339", {"start": v(103.7, 299.2) * mm, "end": v(110.88, 295.05) * mm});
            skLineSegment(sketch, "E25.0.3.340", {"start": v(471.32, 295.05) * mm, "end": v(478.5, 299.2) * mm});
            skLineSegment(sketch, "E25.0.3.341", {"start": v(426.07, 301.5) * mm, "end": v(418.88, 297.35) * mm});
            skLineSegment(sketch, "E25.0.3.342", {"start": v(357.92, 301.5) * mm, "end": v(357.92, 309.8) * mm});
            skLineSegment(sketch, "E25.0.3.343", {"start": v(317.99, 295.05) * mm, "end": v(325.18, 299.2) * mm});
            skLineSegment(sketch, "E25.0.3.344", {"start": v(258.36, 309.8) * mm, "end": v(265.55, 313.95) * mm});
            skLineSegment(sketch, "E25.0.3.345", {"start": v(283.91, 286.75) * mm, "end": v(283.91, 295.05) * mm});
            skLineSegment(sketch, "E25.0.3.346", {"start": v(283.91, 295.05) * mm, "end": v(291.1, 299.2) * mm});
            skLineSegment(sketch, "E25.0.3.347", {"start": v(113.55, 295.05) * mm, "end": v(120.74, 299.2) * mm});
            skLineSegment(sketch, "E25.0.3.348", {"start": v(36.88, 301.5) * mm, "end": v(44.07, 297.35) * mm});
            skLineSegment(sketch, "E25.0.3.349", {"start": v(36.88, 309.8) * mm, "end": v(36.88, 301.5) * mm});
            skLineSegment(sketch, "E25.0.3.350", {"start": v(34.22, 301.5) * mm, "end": v(34.22, 309.8) * mm});
            skLineSegment(sketch, "E25.0.3.351", {"start": v(485.7, 295.05) * mm, "end": v(485.7, 286.75) * mm});
            skLineSegment(sketch, "E25.0.3.352", {"start": v(478.5, 299.2) * mm, "end": v(485.7, 295.05) * mm});
            skLineSegment(sketch, "E25.0.3.353", {"start": v(487.02, 297.35) * mm, "end": v(494.21, 301.5) * mm});
            skLineSegment(sketch, "E25.0.3.354", {"start": v(27.03, 297.35) * mm, "end": v(34.22, 301.5) * mm});
            skLineSegment(sketch, "E25.0.3.355", {"start": v(479.83, 301.5) * mm, "end": v(487.02, 297.35) * mm});
            skLineSegment(sketch, "E25.0.3.356", {"start": v(28.36, 295.05) * mm, "end": v(35.55, 299.2) * mm});
            skLineSegment(sketch, "E25.0.3.357", {"start": v(35.55, 299.2) * mm, "end": v(42.74, 295.05) * mm});
            skLineSegment(sketch, "E25.0.3.358", {"start": v(488.35, 295.05) * mm, "end": v(495.54, 299.2) * mm});
            skLineSegment(sketch, "E25.0.3.359", {"start": v(488.35, 286.75) * mm, "end": v(488.35, 295.05) * mm});
            skLineSegment(sketch, "E25.0.4.0", {"start": v(332.37, 257.25) * mm, "end": v(325.18, 253.1) * mm});
            skLineSegment(sketch, "E25.0.4.1", {"start": v(511.25, 280.3) * mm, "end": v(504.06, 284.45) * mm});
            skLineSegment(sketch, "E25.0.4.2", {"start": v(2.81, 280.3) * mm, "end": v(10, 284.45) * mm});
            skLineSegment(sketch, "E25.0.4.3", {"start": v(127.93, 257.25) * mm, "end": v(120.74, 253.1) * mm});
            skLineSegment(sketch, "E25.0.4.4", {"start": v(512.57, 253.1) * mm, "end": v(505.39, 257.25) * mm});
            skLineSegment(sketch, "E25.0.4.5", {"start": v(519.76, 257.25) * mm, "end": v(512.57, 253.1) * mm});
            skLineSegment(sketch, "E25.0.4.6", {"start": v(25.7, 257.25) * mm, "end": v(18.52, 253.1) * mm});
            skLineSegment(sketch, "E25.0.4.7", {"start": v(11.33, 257.25) * mm, "end": v(11.33, 265.55) * mm});
            skLineSegment(sketch, "E25.0.4.8", {"start": v(18.52, 253.1) * mm, "end": v(11.33, 257.25) * mm});
            skLineSegment(sketch, "E25.0.4.9", {"start": v(519.76, 265.55) * mm, "end": v(519.76, 257.25) * mm});
            skLineSegment(sketch, "E25.0.4.10", {"start": v(76.82, 257.25) * mm, "end": v(69.63, 253.1) * mm});
            skLineSegment(sketch, "E25.0.4.11", {"start": v(112.22, 284.45) * mm, "end": v(119.4, 280.3) * mm});
            skLineSegment(sketch, "E25.0.4.12", {"start": v(205.91, 253.1) * mm, "end": v(198.73, 257.25) * mm});
            skLineSegment(sketch, "E25.0.4.13", {"start": v(197.4, 284.45) * mm, "end": v(190.2, 280.3) * mm});
            skLineSegment(sketch, "E25.0.4.14", {"start": v(93.85, 257.25) * mm, "end": v(86.66, 253.1) * mm});
            skLineSegment(sketch, "E25.0.4.15", {"start": v(129.25, 284.45) * mm, "end": v(122.06, 280.3) * mm});
            skLineSegment(sketch, "E25.0.4.16", {"start": v(298.29, 257.25) * mm, "end": v(291.1, 253.1) * mm});
            skLineSegment(sketch, "E25.0.4.17", {"start": v(502.73, 257.25) * mm, "end": v(495.54, 253.1) * mm});
            skLineSegment(sketch, "E25.0.4.18", {"start": v(289.77, 280.3) * mm, "end": v(282.58, 284.45) * mm});
            skLineSegment(sketch, "E25.0.4.19", {"start": v(85.33, 280.3) * mm, "end": v(78.14, 284.45) * mm});
            skLineSegment(sketch, "E25.0.4.20", {"start": v(494.21, 280.3) * mm, "end": v(487.02, 284.45) * mm});
            skLineSegment(sketch, "E25.0.4.21", {"start": v(333.7, 284.45) * mm, "end": v(326.5, 280.3) * mm});
            skLineSegment(sketch, "E25.0.4.22", {"start": v(95.18, 284.45) * mm, "end": v(87.99, 280.3) * mm});
            skLineSegment(sketch, "E25.0.4.23", {"start": v(478.5, 253.1) * mm, "end": v(471.32, 257.25) * mm});
            skLineSegment(sketch, "E25.0.4.24", {"start": v(274.07, 253.1) * mm, "end": v(266.88, 257.25) * mm});
            skLineSegment(sketch, "E25.0.4.25", {"start": v(444.43, 253.1) * mm, "end": v(437.24, 257.25) * mm});
            skLineSegment(sketch, "E25.0.4.26", {"start": v(401.84, 284.45) * mm, "end": v(394.65, 280.3) * mm});
            skLineSegment(sketch, "E25.0.4.27", {"start": v(410.35, 253.1) * mm, "end": v(403.17, 257.25) * mm});
            skLineSegment(sketch, "E25.0.4.28", {"start": v(468.65, 257.25) * mm, "end": v(461.46, 253.1) * mm});
            skLineSegment(sketch, "E25.0.4.29", {"start": v(427.4, 253.1) * mm, "end": v(420.2, 257.25) * mm});
            skLineSegment(sketch, "E25.0.4.30", {"start": v(59.77, 257.25) * mm, "end": v(52.58, 253.1) * mm});
            skLineSegment(sketch, "E25.0.4.31", {"start": v(512.57, 269.7) * mm, "end": v(519.76, 265.55) * mm});
            skLineSegment(sketch, "E25.0.4.32", {"start": v(196.07, 257.25) * mm, "end": v(188.88, 253.1) * mm});
            skLineSegment(sketch, "E25.0.4.33", {"start": v(86.66, 253.1) * mm, "end": v(79.47, 257.25) * mm});
            skLineSegment(sketch, "E25.0.4.34", {"start": v(400.5, 257.25) * mm, "end": v(393.32, 253.1) * mm});
            skLineSegment(sketch, "E25.0.4.35", {"start": v(103.7, 253.1) * mm, "end": v(96.5, 257.25) * mm});
            skLineSegment(sketch, "E25.0.4.36", {"start": v(299.62, 284.45) * mm, "end": v(292.43, 280.3) * mm});
            skLineSegment(sketch, "E25.0.4.37", {"start": v(504.06, 284.45) * mm, "end": v(496.87, 280.3) * mm});
            skLineSegment(sketch, "E25.0.4.38", {"start": v(2.81, 272) * mm, "end": v(2.81, 280.3) * mm});
            skLineSegment(sketch, "E25.0.4.39", {"start": v(308.13, 253.1) * mm, "end": v(300.95, 257.25) * mm});
            skLineSegment(sketch, "E25.0.4.40", {"start": v(417.54, 257.25) * mm, "end": v(410.35, 253.1) * mm});
            skLineSegment(sketch, "E25.0.4.41", {"start": v(434.59, 257.25) * mm, "end": v(427.4, 253.1) * mm});
            skLineSegment(sketch, "E25.0.4.42", {"start": v(62.44, 257.25) * mm, "end": v(62.44, 265.55) * mm});
            skLineSegment(sketch, "E25.0.4.43", {"start": v(69.63, 253.1) * mm, "end": v(62.44, 257.25) * mm});
            skLineSegment(sketch, "E25.0.4.44", {"start": v(325.18, 253.1) * mm, "end": v(317.99, 257.25) * mm});
            skLineSegment(sketch, "E25.0.4.45", {"start": v(264.21, 257.25) * mm, "end": v(257.02, 253.1) * mm});
            skLineSegment(sketch, "E25.0.4.46", {"start": v(120.74, 253.1) * mm, "end": v(113.55, 257.25) * mm});
            skLineSegment(sketch, "E25.0.4.47", {"start": v(502.73, 265.55) * mm, "end": v(502.73, 257.25) * mm});
            skLineSegment(sketch, "E25.0.4.48", {"start": v(316.66, 284.45) * mm, "end": v(323.85, 280.3) * mm});
            skLineSegment(sketch, "E25.0.4.49", {"start": v(505.39, 257.25) * mm, "end": v(505.39, 265.55) * mm});
            skLineSegment(sketch, "E25.0.4.50", {"start": v(10, 267.85) * mm, "end": v(2.81, 272) * mm});
            skLineSegment(sketch, "E25.0.4.51", {"start": v(59.77, 265.55) * mm, "end": v(59.77, 257.25) * mm});
            skLineSegment(sketch, "E25.0.4.52", {"start": v(291.1, 253.1) * mm, "end": v(283.91, 257.25) * mm});
            skLineSegment(sketch, "E25.0.4.53", {"start": v(511.25, 272) * mm, "end": v(511.25, 280.3) * mm});
            skLineSegment(sketch, "E25.0.4.54", {"start": v(392, 280.3) * mm, "end": v(384.8, 284.45) * mm});
            skLineSegment(sketch, "E25.0.4.55", {"start": v(187.55, 280.3) * mm, "end": v(180.36, 284.45) * mm});
            skLineSegment(sketch, "E25.0.4.56", {"start": v(247.18, 265.55) * mm, "end": v(247.18, 257.25) * mm});
            skLineSegment(sketch, "E25.0.4.57", {"start": v(188.88, 269.7) * mm, "end": v(196.07, 265.55) * mm});
            skLineSegment(sketch, "E25.0.4.58", {"start": v(369.1, 265.55) * mm, "end": v(376.29, 269.7) * mm});
            skLineSegment(sketch, "E25.0.4.59", {"start": v(409.03, 272) * mm, "end": v(409.03, 280.3) * mm});
            skLineSegment(sketch, "E25.0.4.60", {"start": v(188.88, 253.1) * mm, "end": v(181.7, 257.25) * mm});
            skLineSegment(sketch, "E25.0.4.61", {"start": v(204.59, 272) * mm, "end": v(204.59, 280.3) * mm});
            skLineSegment(sketch, "E25.0.4.62", {"start": v(164.66, 265.55) * mm, "end": v(171.85, 269.7) * mm});
            skLineSegment(sketch, "E25.0.4.63", {"start": v(230.15, 265.55) * mm, "end": v(230.15, 257.25) * mm});
            skLineSegment(sketch, "E25.0.4.64", {"start": v(343.54, 280.3) * mm, "end": v(343.54, 272) * mm});
            skLineSegment(sketch, "E25.0.4.65", {"start": v(139.1, 280.3) * mm, "end": v(139.1, 272) * mm});
            skLineSegment(sketch, "E25.0.4.66", {"start": v(70.95, 272) * mm, "end": v(78.14, 267.85) * mm});
            skLineSegment(sketch, "E25.0.4.67", {"start": v(96.5, 257.25) * mm, "end": v(96.5, 265.55) * mm});
            skLineSegment(sketch, "E25.0.4.68", {"start": v(44.07, 284.45) * mm, "end": v(36.88, 280.3) * mm});
            skLineSegment(sketch, "E25.0.4.69", {"start": v(162, 257.25) * mm, "end": v(154.8, 253.1) * mm});
            skLineSegment(sketch, "E25.0.4.70", {"start": v(300.95, 257.25) * mm, "end": v(300.95, 265.55) * mm});
            skLineSegment(sketch, "E25.0.4.71", {"start": v(222.96, 253.1) * mm, "end": v(215.77, 257.25) * mm});
            skLineSegment(sketch, "E25.0.4.72", {"start": v(452.95, 267.85) * mm, "end": v(460.14, 272) * mm});
            skLineSegment(sketch, "E25.0.4.73", {"start": v(369.1, 257.25) * mm, "end": v(369.1, 265.55) * mm});
            skLineSegment(sketch, "E25.0.4.74", {"start": v(366.43, 257.25) * mm, "end": v(359.24, 253.1) * mm});
            skLineSegment(sketch, "E25.0.4.75", {"start": v(164.66, 257.25) * mm, "end": v(164.66, 265.55) * mm});
            skLineSegment(sketch, "E25.0.4.76", {"start": v(248.5, 267.85) * mm, "end": v(255.7, 272) * mm});
            skLineSegment(sketch, "E25.0.4.77", {"start": v(249.84, 265.55) * mm, "end": v(257.02, 269.7) * mm});
            skLineSegment(sketch, "E25.0.4.78", {"start": v(393.32, 253.1) * mm, "end": v(386.13, 257.25) * mm});
            skLineSegment(sketch, "E25.0.4.79", {"start": v(62.44, 265.55) * mm, "end": v(69.63, 269.7) * mm});
            skLineSegment(sketch, "E25.0.4.80", {"start": v(136.44, 272) * mm, "end": v(136.44, 280.3) * mm});
            skLineSegment(sketch, "E25.0.4.81", {"start": v(102.37, 272) * mm, "end": v(102.37, 280.3) * mm});
            skLineSegment(sketch, "E25.0.4.82", {"start": v(418.88, 284.45) * mm, "end": v(426.07, 280.3) * mm});
            skLineSegment(sketch, "E25.0.4.83", {"start": v(454.28, 265.55) * mm, "end": v(461.46, 269.7) * mm});
            skLineSegment(sketch, "E25.0.4.84", {"start": v(78.14, 284.45) * mm, "end": v(70.95, 280.3) * mm});
            skLineSegment(sketch, "E25.0.4.85", {"start": v(105.03, 272) * mm, "end": v(105.03, 280.3) * mm});
            skLineSegment(sketch, "E25.0.4.86", {"start": v(190.2, 272) * mm, "end": v(197.4, 267.85) * mm});
            skLineSegment(sketch, "E25.0.4.87", {"start": v(352.06, 257.25) * mm, "end": v(352.06, 265.55) * mm});
            skLineSegment(sketch, "E25.0.4.88", {"start": v(400.5, 265.55) * mm, "end": v(400.5, 257.25) * mm});
            skLineSegment(sketch, "E25.0.4.89", {"start": v(299.62, 267.85) * mm, "end": v(306.8, 272) * mm});
            skLineSegment(sketch, "E25.0.4.90", {"start": v(190.2, 280.3) * mm, "end": v(190.2, 272) * mm});
            skLineSegment(sketch, "E25.0.4.91", {"start": v(76.82, 265.55) * mm, "end": v(76.82, 257.25) * mm});
            skLineSegment(sketch, "E25.0.4.92", {"start": v(392, 272) * mm, "end": v(392, 280.3) * mm});
            skLineSegment(sketch, "E25.0.4.93", {"start": v(309.47, 280.3) * mm, "end": v(316.66, 284.45) * mm});
            skLineSegment(sketch, "E25.0.4.94", {"start": v(349.4, 257.25) * mm, "end": v(342.21, 253.1) * mm});
            skLineSegment(sketch, "E25.0.4.95", {"start": v(257.02, 269.7) * mm, "end": v(264.21, 265.55) * mm});
            skLineSegment(sketch, "E25.0.4.96", {"start": v(61.1, 284.45) * mm, "end": v(68.3, 280.3) * mm});
            skLineSegment(sketch, "E25.0.4.97", {"start": v(146.29, 284.45) * mm, "end": v(139.1, 280.3) * mm});
            skLineSegment(sketch, "E25.0.4.98", {"start": v(154.8, 253.1) * mm, "end": v(147.62, 257.25) * mm});
            skLineSegment(sketch, "E25.0.4.99", {"start": v(306.8, 280.3) * mm, "end": v(299.62, 284.45) * mm});
            skLineSegment(sketch, "E25.0.4.100", {"start": v(87.99, 272) * mm, "end": v(95.18, 267.85) * mm});
            skLineSegment(sketch, "E25.0.4.101", {"start": v(105.03, 280.3) * mm, "end": v(112.22, 284.45) * mm});
            skLineSegment(sketch, "E25.0.4.102", {"start": v(102.37, 280.3) * mm, "end": v(95.18, 284.45) * mm});
            skLineSegment(sketch, "E25.0.4.103", {"start": v(187.55, 272) * mm, "end": v(187.55, 280.3) * mm});
            skLineSegment(sketch, "E25.0.4.104", {"start": v(61.1, 267.85) * mm, "end": v(53.92, 272) * mm});
            skLineSegment(sketch, "E25.0.4.105", {"start": v(437.24, 257.25) * mm, "end": v(437.24, 265.55) * mm});
            skLineSegment(sketch, "E25.0.4.106", {"start": v(393.32, 269.7) * mm, "end": v(400.5, 265.55) * mm});
            skLineSegment(sketch, "E25.0.4.107", {"start": v(232.8, 257.25) * mm, "end": v(232.8, 265.55) * mm});
            skLineSegment(sketch, "E25.0.4.108", {"start": v(87.99, 280.3) * mm, "end": v(87.99, 272) * mm});
            skLineSegment(sketch, "E25.0.4.109", {"start": v(113.55, 257.25) * mm, "end": v(113.55, 265.55) * mm});
            skLineSegment(sketch, "E25.0.4.110", {"start": v(332.37, 265.55) * mm, "end": v(332.37, 257.25) * mm});
            skLineSegment(sketch, "E25.0.4.111", {"start": v(266.88, 257.25) * mm, "end": v(266.88, 265.55) * mm});
            skLineSegment(sketch, "E25.0.4.112", {"start": v(180.36, 284.45) * mm, "end": v(173.17, 280.3) * mm});
            skLineSegment(sketch, "E25.0.4.113", {"start": v(181.7, 265.55) * mm, "end": v(188.88, 269.7) * mm});
            skLineSegment(sketch, "E25.0.4.114", {"start": v(68.3, 280.3) * mm, "end": v(68.3, 272) * mm});
            skLineSegment(sketch, "E25.0.4.115", {"start": v(317.99, 257.25) * mm, "end": v(317.99, 265.55) * mm});
            skLineSegment(sketch, "E25.0.4.116", {"start": v(485.7, 257.25) * mm, "end": v(478.5, 253.1) * mm});
            skLineSegment(sketch, "E25.0.4.117", {"start": v(10, 284.45) * mm, "end": v(17.19, 280.3) * mm});
            skLineSegment(sketch, "E25.0.4.118", {"start": v(376.29, 253.1) * mm, "end": v(369.1, 257.25) * mm});
            skLineSegment(sketch, "E25.0.4.119", {"start": v(452.95, 284.45) * mm, "end": v(445.76, 280.3) * mm});
            skLineSegment(sketch, "E25.0.4.120", {"start": v(315.32, 257.25) * mm, "end": v(308.13, 253.1) * mm});
            skLineSegment(sketch, "E25.0.4.121", {"start": v(93.85, 265.55) * mm, "end": v(93.85, 257.25) * mm});
            skLineSegment(sketch, "E25.0.4.122", {"start": v(35.55, 253.1) * mm, "end": v(28.36, 257.25) * mm});
            skLineSegment(sketch, "E25.0.4.123", {"start": v(45.4, 257.25) * mm, "end": v(45.4, 265.55) * mm});
            skLineSegment(sketch, "E25.0.4.124", {"start": v(42.74, 257.25) * mm, "end": v(35.55, 253.1) * mm});
            skLineSegment(sketch, "E25.0.4.125", {"start": v(434.59, 265.55) * mm, "end": v(434.59, 257.25) * mm});
            skLineSegment(sketch, "E25.0.4.126", {"start": v(340.88, 272) * mm, "end": v(340.88, 280.3) * mm});
            skLineSegment(sketch, "E25.0.4.127", {"start": v(394.65, 272) * mm, "end": v(401.84, 267.85) * mm});
            skLineSegment(sketch, "E25.0.4.128", {"start": v(153.48, 280.3) * mm, "end": v(146.29, 284.45) * mm});
            skLineSegment(sketch, "E25.0.4.129", {"start": v(52.58, 253.1) * mm, "end": v(45.4, 257.25) * mm});
            skLineSegment(sketch, "E25.0.4.130", {"start": v(25.7, 265.55) * mm, "end": v(25.7, 257.25) * mm});
            skLineSegment(sketch, "E25.0.4.131", {"start": v(28.36, 257.25) * mm, "end": v(28.36, 265.55) * mm});
            skLineSegment(sketch, "E25.0.4.132", {"start": v(45.4, 265.55) * mm, "end": v(52.58, 269.7) * mm});
            skLineSegment(sketch, "E25.0.4.133", {"start": v(451.62, 257.25) * mm, "end": v(444.43, 253.1) * mm});
            skLineSegment(sketch, "E25.0.4.134", {"start": v(411.7, 272) * mm, "end": v(411.7, 280.3) * mm});
            skLineSegment(sketch, "E25.0.4.135", {"start": v(342.21, 253.1) * mm, "end": v(335.02, 257.25) * mm});
            skLineSegment(sketch, "E25.0.4.136", {"start": v(443.1, 272) * mm, "end": v(443.1, 280.3) * mm});
            skLineSegment(sketch, "E25.0.4.137", {"start": v(357.92, 280.3) * mm, "end": v(350.73, 284.45) * mm});
            skLineSegment(sketch, "E25.0.4.138", {"start": v(289.77, 272) * mm, "end": v(289.77, 280.3) * mm});
            skLineSegment(sketch, "E25.0.4.139", {"start": v(204.59, 280.3) * mm, "end": v(197.4, 284.45) * mm});
            skLineSegment(sketch, "E25.0.4.140", {"start": v(198.73, 265.55) * mm, "end": v(205.91, 269.7) * mm});
            skLineSegment(sketch, "E25.0.4.141", {"start": v(454.28, 257.25) * mm, "end": v(454.28, 265.55) * mm});
            skLineSegment(sketch, "E25.0.4.142", {"start": v(86.66, 269.7) * mm, "end": v(93.85, 265.55) * mm});
            skLineSegment(sketch, "E25.0.4.143", {"start": v(443.1, 280.3) * mm, "end": v(435.91, 284.45) * mm});
            skLineSegment(sketch, "E25.0.4.144", {"start": v(435.91, 284.45) * mm, "end": v(428.72, 280.3) * mm});
            skLineSegment(sketch, "E25.0.4.145", {"start": v(437.24, 265.55) * mm, "end": v(444.43, 269.7) * mm});
            skLineSegment(sketch, "E25.0.4.146", {"start": v(231.47, 284.45) * mm, "end": v(224.28, 280.3) * mm});
            skLineSegment(sketch, "E25.0.4.147", {"start": v(79.47, 257.25) * mm, "end": v(79.47, 265.55) * mm});
            skLineSegment(sketch, "E25.0.4.148", {"start": v(309.47, 272) * mm, "end": v(309.47, 280.3) * mm});
            skLineSegment(sketch, "E25.0.4.149", {"start": v(214.44, 284.45) * mm, "end": v(221.63, 280.3) * mm});
            skLineSegment(sketch, "E25.0.4.150", {"start": v(238.66, 280.3) * mm, "end": v(231.47, 284.45) * mm});
            skLineSegment(sketch, "E25.0.4.151", {"start": v(394.65, 280.3) * mm, "end": v(394.65, 272) * mm});
            skLineSegment(sketch, "E25.0.4.152", {"start": v(445.76, 272) * mm, "end": v(452.95, 267.85) * mm});
            skLineSegment(sketch, "E25.0.4.153", {"start": v(241.32, 272) * mm, "end": v(248.5, 267.85) * mm});
            skLineSegment(sketch, "E25.0.4.154", {"start": v(231.47, 267.85) * mm, "end": v(238.66, 272) * mm});
            skLineSegment(sketch, "E25.0.4.155", {"start": v(79.47, 265.55) * mm, "end": v(86.66, 269.7) * mm});
            skLineSegment(sketch, "E25.0.4.156", {"start": v(350.73, 284.45) * mm, "end": v(343.54, 280.3) * mm});
            skLineSegment(sketch, "E25.0.4.157", {"start": v(196.07, 265.55) * mm, "end": v(196.07, 257.25) * mm});
            skLineSegment(sketch, "E25.0.4.158", {"start": v(240, 253.1) * mm, "end": v(232.8, 257.25) * mm});
            skLineSegment(sketch, "E25.0.4.159", {"start": v(69.63, 269.7) * mm, "end": v(76.82, 265.55) * mm});
            skLineSegment(sketch, "E25.0.4.160", {"start": v(349.4, 265.55) * mm, "end": v(349.4, 257.25) * mm});
            skLineSegment(sketch, "E25.0.4.161", {"start": v(383.48, 257.25) * mm, "end": v(376.29, 253.1) * mm});
            skLineSegment(sketch, "E25.0.4.162", {"start": v(144.96, 265.55) * mm, "end": v(144.96, 257.25) * mm});
            skLineSegment(sketch, "E25.0.4.163", {"start": v(179.04, 257.25) * mm, "end": v(171.85, 253.1) * mm});
            skLineSegment(sketch, "E25.0.4.164", {"start": v(386.13, 265.55) * mm, "end": v(393.32, 269.7) * mm});
            skLineSegment(sketch, "E25.0.4.165", {"start": v(435.91, 267.85) * mm, "end": v(443.1, 272) * mm});
            skLineSegment(sketch, "E25.0.4.166", {"start": v(504.06, 267.85) * mm, "end": v(511.25, 272) * mm});
            skLineSegment(sketch, "E25.0.4.167", {"start": v(403.17, 257.25) * mm, "end": v(403.17, 265.55) * mm});
            skLineSegment(sketch, "E25.0.4.168", {"start": v(241.32, 280.3) * mm, "end": v(241.32, 272) * mm});
            skLineSegment(sketch, "E25.0.4.169", {"start": v(359.24, 253.1) * mm, "end": v(352.06, 257.25) * mm});
            skLineSegment(sketch, "E25.0.4.170", {"start": v(213.1, 257.25) * mm, "end": v(205.91, 253.1) * mm});
            skLineSegment(sketch, "E25.0.4.171", {"start": v(34.22, 280.3) * mm, "end": v(27.03, 284.45) * mm});
            skLineSegment(sketch, "E25.0.4.172", {"start": v(461.46, 269.7) * mm, "end": v(468.65, 265.55) * mm});
            skLineSegment(sketch, "E25.0.4.173", {"start": v(505.39, 265.55) * mm, "end": v(512.57, 269.7) * mm});
            skLineSegment(sketch, "E25.0.4.174", {"start": v(300.95, 265.55) * mm, "end": v(308.13, 269.7) * mm});
            skLineSegment(sketch, "E25.0.4.175", {"start": v(230.15, 257.25) * mm, "end": v(222.96, 253.1) * mm});
            skLineSegment(sketch, "E25.0.4.176", {"start": v(265.55, 267.85) * mm, "end": v(258.36, 272) * mm});
            skLineSegment(sketch, "E25.0.4.177", {"start": v(144.96, 257.25) * mm, "end": v(137.77, 253.1) * mm});
            skLineSegment(sketch, "E25.0.4.178", {"start": v(27.03, 284.45) * mm, "end": v(19.84, 280.3) * mm});
            skLineSegment(sketch, "E25.0.4.179", {"start": v(384.8, 284.45) * mm, "end": v(377.61, 280.3) * mm});
            skLineSegment(sketch, "E25.0.4.180", {"start": v(340.88, 280.3) * mm, "end": v(333.7, 284.45) * mm});
            skLineSegment(sketch, "E25.0.4.181", {"start": v(136.44, 280.3) * mm, "end": v(129.25, 284.45) * mm});
            skLineSegment(sketch, "E25.0.4.182", {"start": v(198.73, 257.25) * mm, "end": v(198.73, 265.55) * mm});
            skLineSegment(sketch, "E25.0.4.183", {"start": v(70.95, 280.3) * mm, "end": v(70.95, 272) * mm});
            skLineSegment(sketch, "E25.0.4.184", {"start": v(127.93, 265.55) * mm, "end": v(127.93, 257.25) * mm});
            skLineSegment(sketch, "E25.0.4.185", {"start": v(461.46, 253.1) * mm, "end": v(454.28, 257.25) * mm});
            skLineSegment(sketch, "E25.0.4.186", {"start": v(444.43, 269.7) * mm, "end": v(451.62, 265.55) * mm});
            skLineSegment(sketch, "E25.0.4.187", {"start": v(445.76, 280.3) * mm, "end": v(445.76, 272) * mm});
            skLineSegment(sketch, "E25.0.4.188", {"start": v(240, 269.7) * mm, "end": v(247.18, 265.55) * mm});
            skLineSegment(sketch, "E25.0.4.189", {"start": v(298.29, 265.55) * mm, "end": v(298.29, 257.25) * mm});
            skLineSegment(sketch, "E25.0.4.190", {"start": v(471.32, 257.25) * mm, "end": v(471.32, 265.55) * mm});
            skLineSegment(sketch, "E25.0.4.191", {"start": v(207.25, 272) * mm, "end": v(207.25, 280.3) * mm});
            skLineSegment(sketch, "E25.0.4.192", {"start": v(281.26, 257.25) * mm, "end": v(274.07, 253.1) * mm});
            skLineSegment(sketch, "E25.0.4.193", {"start": v(257.02, 253.1) * mm, "end": v(249.84, 257.25) * mm});
            skLineSegment(sketch, "E25.0.4.194", {"start": v(248.5, 284.45) * mm, "end": v(241.32, 280.3) * mm});
            skLineSegment(sketch, "E25.0.4.195", {"start": v(451.62, 265.55) * mm, "end": v(451.62, 257.25) * mm});
            skLineSegment(sketch, "E25.0.4.196", {"start": v(110.88, 257.25) * mm, "end": v(103.7, 253.1) * mm});
            skLineSegment(sketch, "E25.0.4.197", {"start": v(401.84, 267.85) * mm, "end": v(409.03, 272) * mm});
            skLineSegment(sketch, "E25.0.4.198", {"start": v(292.43, 280.3) * mm, "end": v(292.43, 272) * mm});
            skLineSegment(sketch, "E25.0.4.199", {"start": v(171.85, 253.1) * mm, "end": v(164.66, 257.25) * mm});
            skLineSegment(sketch, "E25.0.4.200", {"start": v(197.4, 267.85) * mm, "end": v(204.59, 272) * mm});
            skLineSegment(sketch, "E25.0.4.201", {"start": v(52.58, 269.7) * mm, "end": v(59.77, 265.55) * mm});
            skLineSegment(sketch, "E25.0.4.202", {"start": v(411.7, 280.3) * mm, "end": v(418.88, 284.45) * mm});
            skLineSegment(sketch, "E25.0.4.203", {"start": v(409.03, 280.3) * mm, "end": v(401.84, 284.45) * mm});
            skLineSegment(sketch, "E25.0.4.204", {"start": v(207.25, 280.3) * mm, "end": v(214.44, 284.45) * mm});
            skLineSegment(sketch, "E25.0.4.205", {"start": v(403.17, 265.55) * mm, "end": v(410.35, 269.7) * mm});
            skLineSegment(sketch, "E25.0.4.206", {"start": v(495.54, 253.1) * mm, "end": v(488.35, 257.25) * mm});
            skLineSegment(sketch, "E25.0.4.207", {"start": v(468.65, 265.55) * mm, "end": v(468.65, 257.25) * mm});
            skLineSegment(sketch, "E25.0.4.208", {"start": v(264.21, 265.55) * mm, "end": v(264.21, 257.25) * mm});
            skLineSegment(sketch, "E25.0.4.209", {"start": v(238.66, 272) * mm, "end": v(238.66, 280.3) * mm});
            skLineSegment(sketch, "E25.0.4.210", {"start": v(247.18, 257.25) * mm, "end": v(240, 253.1) * mm});
            skLineSegment(sketch, "E25.0.4.211", {"start": v(85.33, 272) * mm, "end": v(85.33, 280.3) * mm});
            skLineSegment(sketch, "E25.0.4.212", {"start": v(137.77, 253.1) * mm, "end": v(130.58, 257.25) * mm});
            skLineSegment(sketch, "E25.0.4.213", {"start": v(374.96, 272) * mm, "end": v(367.77, 267.85) * mm});
            skLineSegment(sketch, "E25.0.4.214", {"start": v(323.85, 280.3) * mm, "end": v(323.85, 272) * mm});
            skLineSegment(sketch, "E25.0.4.215", {"start": v(266.88, 265.55) * mm, "end": v(274.07, 269.7) * mm});
            skLineSegment(sketch, "E25.0.4.216", {"start": v(326.5, 280.3) * mm, "end": v(326.5, 272) * mm});
            skLineSegment(sketch, "E25.0.4.217", {"start": v(232.8, 265.55) * mm, "end": v(240, 269.7) * mm});
            skLineSegment(sketch, "E25.0.4.218", {"start": v(306.8, 272) * mm, "end": v(306.8, 280.3) * mm});
            skLineSegment(sketch, "E25.0.4.219", {"start": v(119.4, 280.3) * mm, "end": v(119.4, 272) * mm});
            skLineSegment(sketch, "E25.0.4.220", {"start": v(122.06, 280.3) * mm, "end": v(122.06, 272) * mm});
            skLineSegment(sketch, "E25.0.4.221", {"start": v(170.52, 272) * mm, "end": v(163.33, 267.85) * mm});
            skLineSegment(sketch, "E25.0.4.222", {"start": v(428.72, 280.3) * mm, "end": v(428.72, 272) * mm});
            skLineSegment(sketch, "E25.0.4.223", {"start": v(51.26, 272) * mm, "end": v(51.26, 280.3) * mm});
            skLineSegment(sketch, "E25.0.4.224", {"start": v(386.13, 257.25) * mm, "end": v(386.13, 265.55) * mm});
            skLineSegment(sketch, "E25.0.4.225", {"start": v(44.07, 267.85) * mm, "end": v(51.26, 272) * mm});
            skLineSegment(sketch, "E25.0.4.226", {"start": v(462.8, 280.3) * mm, "end": v(469.99, 284.45) * mm});
            skLineSegment(sketch, "E25.0.4.227", {"start": v(214.44, 267.85) * mm, "end": v(207.25, 272) * mm});
            skLineSegment(sketch, "E25.0.4.228", {"start": v(205.91, 269.7) * mm, "end": v(213.1, 265.55) * mm});
            skLineSegment(sketch, "E25.0.4.229", {"start": v(366.43, 265.55) * mm, "end": v(366.43, 257.25) * mm});
            skLineSegment(sketch, "E25.0.4.230", {"start": v(130.58, 265.55) * mm, "end": v(137.77, 269.7) * mm});
            skLineSegment(sketch, "E25.0.4.231", {"start": v(224.28, 280.3) * mm, "end": v(224.28, 272) * mm});
            skLineSegment(sketch, "E25.0.4.232", {"start": v(384.8, 267.85) * mm, "end": v(392, 272) * mm});
            skLineSegment(sketch, "E25.0.4.233", {"start": v(275.4, 272) * mm, "end": v(282.58, 267.85) * mm});
            skLineSegment(sketch, "E25.0.4.234", {"start": v(19.84, 272) * mm, "end": v(27.03, 267.85) * mm});
            skLineSegment(sketch, "E25.0.4.235", {"start": v(180.36, 267.85) * mm, "end": v(187.55, 272) * mm});
            skLineSegment(sketch, "E25.0.4.236", {"start": v(410.35, 269.7) * mm, "end": v(417.54, 265.55) * mm});
            skLineSegment(sketch, "E25.0.4.237", {"start": v(255.7, 280.3) * mm, "end": v(248.5, 284.45) * mm});
            skLineSegment(sketch, "E25.0.4.238", {"start": v(53.92, 280.3) * mm, "end": v(61.1, 284.45) * mm});
            skLineSegment(sketch, "E25.0.4.239", {"start": v(162, 265.55) * mm, "end": v(162, 257.25) * mm});
            skLineSegment(sketch, "E25.0.4.240", {"start": v(51.26, 280.3) * mm, "end": v(44.07, 284.45) * mm});
            skLineSegment(sketch, "E25.0.4.241", {"start": v(427.4, 269.7) * mm, "end": v(434.59, 265.55) * mm});
            skLineSegment(sketch, "E25.0.4.242", {"start": v(460.14, 280.3) * mm, "end": v(452.95, 284.45) * mm});
            skLineSegment(sketch, "E25.0.4.243", {"start": v(272.74, 272) * mm, "end": v(265.55, 267.85) * mm});
            skLineSegment(sketch, "E25.0.4.244", {"start": v(181.7, 257.25) * mm, "end": v(181.7, 265.55) * mm});
            skLineSegment(sketch, "E25.0.4.245", {"start": v(335.02, 265.55) * mm, "end": v(342.21, 269.7) * mm});
            skLineSegment(sketch, "E25.0.4.246", {"start": v(221.63, 280.3) * mm, "end": v(221.63, 272) * mm});
            skLineSegment(sketch, "E25.0.4.247", {"start": v(68.3, 272) * mm, "end": v(61.1, 267.85) * mm});
            skLineSegment(sketch, "E25.0.4.248", {"start": v(130.58, 257.25) * mm, "end": v(130.58, 265.55) * mm});
            skLineSegment(sketch, "E25.0.4.249", {"start": v(477.18, 272) * mm, "end": v(469.99, 267.85) * mm});
            skLineSegment(sketch, "E25.0.4.250", {"start": v(469.99, 284.45) * mm, "end": v(477.18, 280.3) * mm});
            skLineSegment(sketch, "E25.0.4.251", {"start": v(360.58, 272) * mm, "end": v(360.58, 280.3) * mm});
            skLineSegment(sketch, "E25.0.4.252", {"start": v(122.06, 272) * mm, "end": v(129.25, 267.85) * mm});
            skLineSegment(sketch, "E25.0.4.253", {"start": v(95.18, 267.85) * mm, "end": v(102.37, 272) * mm});
            skLineSegment(sketch, "E25.0.4.254", {"start": v(137.77, 269.7) * mm, "end": v(144.96, 265.55) * mm});
            skLineSegment(sketch, "E25.0.4.255", {"start": v(469.99, 267.85) * mm, "end": v(462.8, 272) * mm});
            skLineSegment(sketch, "E25.0.4.256", {"start": v(417.54, 265.55) * mm, "end": v(417.54, 257.25) * mm});
            skLineSegment(sketch, "E25.0.4.257", {"start": v(120.74, 269.7) * mm, "end": v(127.93, 265.55) * mm});
            skLineSegment(sketch, "E25.0.4.258", {"start": v(477.18, 280.3) * mm, "end": v(477.18, 272) * mm});
            skLineSegment(sketch, "E25.0.4.259", {"start": v(420.2, 265.55) * mm, "end": v(427.4, 269.7) * mm});
            skLineSegment(sketch, "E25.0.4.260", {"start": v(275.4, 280.3) * mm, "end": v(275.4, 272) * mm});
            skLineSegment(sketch, "E25.0.4.261", {"start": v(255.7, 272) * mm, "end": v(255.7, 280.3) * mm});
            skLineSegment(sketch, "E25.0.4.262", {"start": v(215.77, 265.55) * mm, "end": v(222.96, 269.7) * mm});
            skLineSegment(sketch, "E25.0.4.263", {"start": v(42.74, 265.55) * mm, "end": v(42.74, 257.25) * mm});
            skLineSegment(sketch, "E25.0.4.264", {"start": v(350.73, 267.85) * mm, "end": v(357.92, 272) * mm});
            skLineSegment(sketch, "E25.0.4.265", {"start": v(78.14, 267.85) * mm, "end": v(85.33, 272) * mm});
            skLineSegment(sketch, "E25.0.4.266", {"start": v(119.4, 272) * mm, "end": v(112.22, 267.85) * mm});
            skLineSegment(sketch, "E25.0.4.267", {"start": v(19.84, 280.3) * mm, "end": v(19.84, 272) * mm});
            skLineSegment(sketch, "E25.0.4.268", {"start": v(496.87, 272) * mm, "end": v(504.06, 267.85) * mm});
            skLineSegment(sketch, "E25.0.4.269", {"start": v(325.18, 269.7) * mm, "end": v(332.37, 265.55) * mm});
            skLineSegment(sketch, "E25.0.4.270", {"start": v(367.77, 284.45) * mm, "end": v(374.96, 280.3) * mm});
            skLineSegment(sketch, "E25.0.4.271", {"start": v(258.36, 272) * mm, "end": v(258.36, 280.3) * mm});
            skLineSegment(sketch, "E25.0.4.272", {"start": v(163.33, 284.45) * mm, "end": v(170.52, 280.3) * mm});
            skLineSegment(sketch, "E25.0.4.273", {"start": v(179.04, 265.55) * mm, "end": v(179.04, 257.25) * mm});
            skLineSegment(sketch, "E25.0.4.274", {"start": v(249.84, 257.25) * mm, "end": v(249.84, 265.55) * mm});
            skLineSegment(sketch, "E25.0.4.275", {"start": v(139.1, 272) * mm, "end": v(146.29, 267.85) * mm});
            skLineSegment(sketch, "E25.0.4.276", {"start": v(418.88, 267.85) * mm, "end": v(411.7, 272) * mm});
            skLineSegment(sketch, "E25.0.4.277", {"start": v(426.07, 280.3) * mm, "end": v(426.07, 272) * mm});
            skLineSegment(sketch, "E25.0.4.278", {"start": v(367.77, 267.85) * mm, "end": v(360.58, 272) * mm});
            skLineSegment(sketch, "E25.0.4.279", {"start": v(352.06, 265.55) * mm, "end": v(359.24, 269.7) * mm});
            skLineSegment(sketch, "E25.0.4.280", {"start": v(163.33, 267.85) * mm, "end": v(156.14, 272) * mm});
            skLineSegment(sketch, "E25.0.4.281", {"start": v(112.22, 267.85) * mm, "end": v(105.03, 272) * mm});
            skLineSegment(sketch, "E25.0.4.282", {"start": v(487.02, 284.45) * mm, "end": v(479.83, 280.3) * mm});
            skLineSegment(sketch, "E25.0.4.283", {"start": v(374.96, 280.3) * mm, "end": v(374.96, 272) * mm});
            skLineSegment(sketch, "E25.0.4.284", {"start": v(17.19, 272) * mm, "end": v(10, 267.85) * mm});
            skLineSegment(sketch, "E25.0.4.285", {"start": v(221.63, 272) * mm, "end": v(214.44, 267.85) * mm});
            skLineSegment(sketch, "E25.0.4.286", {"start": v(282.58, 284.45) * mm, "end": v(275.4, 280.3) * mm});
            skLineSegment(sketch, "E25.0.4.287", {"start": v(335.02, 257.25) * mm, "end": v(335.02, 265.55) * mm});
            skLineSegment(sketch, "E25.0.4.288", {"start": v(170.52, 280.3) * mm, "end": v(170.52, 272) * mm});
            skLineSegment(sketch, "E25.0.4.289", {"start": v(291.1, 269.7) * mm, "end": v(298.29, 265.55) * mm});
            skLineSegment(sketch, "E25.0.4.290", {"start": v(173.17, 280.3) * mm, "end": v(173.17, 272) * mm});
            skLineSegment(sketch, "E25.0.4.291", {"start": v(495.54, 269.7) * mm, "end": v(502.73, 265.55) * mm});
            skLineSegment(sketch, "E25.0.4.292", {"start": v(147.62, 257.25) * mm, "end": v(147.62, 265.55) * mm});
            skLineSegment(sketch, "E25.0.4.293", {"start": v(153.48, 272) * mm, "end": v(153.48, 280.3) * mm});
            skLineSegment(sketch, "E25.0.4.294", {"start": v(222.96, 269.7) * mm, "end": v(230.15, 265.55) * mm});
            skLineSegment(sketch, "E25.0.4.295", {"start": v(479.83, 280.3) * mm, "end": v(479.83, 272) * mm});
            skLineSegment(sketch, "E25.0.4.296", {"start": v(420.2, 257.25) * mm, "end": v(420.2, 265.55) * mm});
            skLineSegment(sketch, "E25.0.4.297", {"start": v(326.5, 272) * mm, "end": v(333.7, 267.85) * mm});
            skLineSegment(sketch, "E25.0.4.298", {"start": v(173.17, 272) * mm, "end": v(180.36, 267.85) * mm});
            skLineSegment(sketch, "E25.0.4.299", {"start": v(342.21, 269.7) * mm, "end": v(349.4, 265.55) * mm});
            skLineSegment(sketch, "E25.0.4.300", {"start": v(265.55, 284.45) * mm, "end": v(272.74, 280.3) * mm});
            skLineSegment(sketch, "E25.0.4.301", {"start": v(274.07, 269.7) * mm, "end": v(281.26, 265.55) * mm});
            skLineSegment(sketch, "E25.0.4.302", {"start": v(215.77, 257.25) * mm, "end": v(215.77, 265.55) * mm});
            skLineSegment(sketch, "E25.0.4.303", {"start": v(462.8, 272) * mm, "end": v(462.8, 280.3) * mm});
            skLineSegment(sketch, "E25.0.4.304", {"start": v(281.26, 265.55) * mm, "end": v(281.26, 257.25) * mm});
            skLineSegment(sketch, "E25.0.4.305", {"start": v(156.14, 272) * mm, "end": v(156.14, 280.3) * mm});
            skLineSegment(sketch, "E25.0.4.306", {"start": v(213.1, 265.55) * mm, "end": v(213.1, 257.25) * mm});
            skLineSegment(sketch, "E25.0.4.307", {"start": v(96.5, 265.55) * mm, "end": v(103.7, 269.7) * mm});
            skLineSegment(sketch, "E25.0.4.308", {"start": v(460.14, 272) * mm, "end": v(460.14, 280.3) * mm});
            skLineSegment(sketch, "E25.0.4.309", {"start": v(323.85, 272) * mm, "end": v(316.66, 267.85) * mm});
            skLineSegment(sketch, "E25.0.4.310", {"start": v(272.74, 280.3) * mm, "end": v(272.74, 272) * mm});
            skLineSegment(sketch, "E25.0.4.311", {"start": v(377.61, 272) * mm, "end": v(384.8, 267.85) * mm});
            skLineSegment(sketch, "E25.0.4.312", {"start": v(282.58, 267.85) * mm, "end": v(289.77, 272) * mm});
            skLineSegment(sketch, "E25.0.4.313", {"start": v(146.29, 267.85) * mm, "end": v(153.48, 272) * mm});
            skLineSegment(sketch, "E25.0.4.314", {"start": v(343.54, 272) * mm, "end": v(350.73, 267.85) * mm});
            skLineSegment(sketch, "E25.0.4.315", {"start": v(376.29, 269.7) * mm, "end": v(383.48, 265.55) * mm});
            skLineSegment(sketch, "E25.0.4.316", {"start": v(171.85, 269.7) * mm, "end": v(179.04, 265.55) * mm});
            skLineSegment(sketch, "E25.0.4.317", {"start": v(53.92, 272) * mm, "end": v(53.92, 280.3) * mm});
            skLineSegment(sketch, "E25.0.4.318", {"start": v(292.43, 272) * mm, "end": v(299.62, 267.85) * mm});
            skLineSegment(sketch, "E25.0.4.319", {"start": v(377.61, 280.3) * mm, "end": v(377.61, 272) * mm});
            skLineSegment(sketch, "E25.0.4.320", {"start": v(383.48, 265.55) * mm, "end": v(383.48, 257.25) * mm});
            skLineSegment(sketch, "E25.0.4.321", {"start": v(129.25, 267.85) * mm, "end": v(136.44, 272) * mm});
            skLineSegment(sketch, "E25.0.4.322", {"start": v(428.72, 272) * mm, "end": v(435.91, 267.85) * mm});
            skLineSegment(sketch, "E25.0.4.323", {"start": v(496.87, 280.3) * mm, "end": v(496.87, 272) * mm});
            skLineSegment(sketch, "E25.0.4.324", {"start": v(224.28, 272) * mm, "end": v(231.47, 267.85) * mm});
            skLineSegment(sketch, "E25.0.4.325", {"start": v(333.7, 267.85) * mm, "end": v(340.88, 272) * mm});
            skLineSegment(sketch, "E25.0.4.326", {"start": v(11.33, 265.55) * mm, "end": v(18.52, 269.7) * mm});
            skLineSegment(sketch, "E25.0.4.327", {"start": v(18.52, 269.7) * mm, "end": v(25.7, 265.55) * mm});
            skLineSegment(sketch, "E25.0.4.328", {"start": v(494.21, 272) * mm, "end": v(494.21, 280.3) * mm});
            skLineSegment(sketch, "E25.0.4.329", {"start": v(315.32, 265.55) * mm, "end": v(315.32, 257.25) * mm});
            skLineSegment(sketch, "E25.0.4.330", {"start": v(360.58, 280.3) * mm, "end": v(367.77, 284.45) * mm});
            skLineSegment(sketch, "E25.0.4.331", {"start": v(316.66, 267.85) * mm, "end": v(309.47, 272) * mm});
            skLineSegment(sketch, "E25.0.4.332", {"start": v(308.13, 269.7) * mm, "end": v(315.32, 265.55) * mm});
            skLineSegment(sketch, "E25.0.4.333", {"start": v(147.62, 265.55) * mm, "end": v(154.8, 269.7) * mm});
            skLineSegment(sketch, "E25.0.4.334", {"start": v(359.24, 269.7) * mm, "end": v(366.43, 265.55) * mm});
            skLineSegment(sketch, "E25.0.4.335", {"start": v(110.88, 265.55) * mm, "end": v(110.88, 257.25) * mm});
            skLineSegment(sketch, "E25.0.4.336", {"start": v(154.8, 269.7) * mm, "end": v(162, 265.55) * mm});
            skLineSegment(sketch, "E25.0.4.337", {"start": v(17.19, 280.3) * mm, "end": v(17.19, 272) * mm});
            skLineSegment(sketch, "E25.0.4.338", {"start": v(156.14, 280.3) * mm, "end": v(163.33, 284.45) * mm});
            skLineSegment(sketch, "E25.0.4.339", {"start": v(103.7, 269.7) * mm, "end": v(110.88, 265.55) * mm});
            skLineSegment(sketch, "E25.0.4.340", {"start": v(471.32, 265.55) * mm, "end": v(478.5, 269.7) * mm});
            skLineSegment(sketch, "E25.0.4.341", {"start": v(426.07, 272) * mm, "end": v(418.88, 267.85) * mm});
            skLineSegment(sketch, "E25.0.4.342", {"start": v(357.92, 272) * mm, "end": v(357.92, 280.3) * mm});
            skLineSegment(sketch, "E25.0.4.343", {"start": v(317.99, 265.55) * mm, "end": v(325.18, 269.7) * mm});
            skLineSegment(sketch, "E25.0.4.344", {"start": v(258.36, 280.3) * mm, "end": v(265.55, 284.45) * mm});
            skLineSegment(sketch, "E25.0.4.345", {"start": v(283.91, 257.25) * mm, "end": v(283.91, 265.55) * mm});
            skLineSegment(sketch, "E25.0.4.346", {"start": v(283.91, 265.55) * mm, "end": v(291.1, 269.7) * mm});
            skLineSegment(sketch, "E25.0.4.347", {"start": v(113.55, 265.55) * mm, "end": v(120.74, 269.7) * mm});
            skLineSegment(sketch, "E25.0.4.348", {"start": v(36.88, 272) * mm, "end": v(44.07, 267.85) * mm});
            skLineSegment(sketch, "E25.0.4.349", {"start": v(36.88, 280.3) * mm, "end": v(36.88, 272) * mm});
            skLineSegment(sketch, "E25.0.4.350", {"start": v(34.22, 272) * mm, "end": v(34.22, 280.3) * mm});
            skLineSegment(sketch, "E25.0.4.351", {"start": v(485.7, 265.55) * mm, "end": v(485.7, 257.25) * mm});
            skLineSegment(sketch, "E25.0.4.352", {"start": v(478.5, 269.7) * mm, "end": v(485.7, 265.55) * mm});
            skLineSegment(sketch, "E25.0.4.353", {"start": v(487.02, 267.85) * mm, "end": v(494.21, 272) * mm});
            skLineSegment(sketch, "E25.0.4.354", {"start": v(27.03, 267.85) * mm, "end": v(34.22, 272) * mm});
            skLineSegment(sketch, "E25.0.4.355", {"start": v(479.83, 272) * mm, "end": v(487.02, 267.85) * mm});
            skLineSegment(sketch, "E25.0.4.356", {"start": v(28.36, 265.55) * mm, "end": v(35.55, 269.7) * mm});
            skLineSegment(sketch, "E25.0.4.357", {"start": v(35.55, 269.7) * mm, "end": v(42.74, 265.55) * mm});
            skLineSegment(sketch, "E25.0.4.358", {"start": v(488.35, 265.55) * mm, "end": v(495.54, 269.7) * mm});
            skLineSegment(sketch, "E25.0.4.359", {"start": v(488.35, 257.25) * mm, "end": v(488.35, 265.55) * mm});
            skLineSegment(sketch, "E25.0.5.0", {"start": v(332.37, 227.75) * mm, "end": v(325.18, 223.6) * mm});
            skLineSegment(sketch, "E25.0.5.1", {"start": v(511.25, 250.8) * mm, "end": v(504.06, 254.95) * mm});
            skLineSegment(sketch, "E25.0.5.2", {"start": v(2.81, 250.8) * mm, "end": v(10, 254.95) * mm});
            skLineSegment(sketch, "E25.0.5.3", {"start": v(127.93, 227.75) * mm, "end": v(120.74, 223.6) * mm});
            skLineSegment(sketch, "E25.0.5.4", {"start": v(512.57, 223.6) * mm, "end": v(505.39, 227.75) * mm});
            skLineSegment(sketch, "E25.0.5.5", {"start": v(519.76, 227.75) * mm, "end": v(512.57, 223.6) * mm});
            skLineSegment(sketch, "E25.0.5.6", {"start": v(25.7, 227.75) * mm, "end": v(18.52, 223.6) * mm});
            skLineSegment(sketch, "E25.0.5.7", {"start": v(11.33, 227.75) * mm, "end": v(11.33, 236.05) * mm});
            skLineSegment(sketch, "E25.0.5.8", {"start": v(18.52, 223.6) * mm, "end": v(11.33, 227.75) * mm});
            skLineSegment(sketch, "E25.0.5.9", {"start": v(519.76, 236.05) * mm, "end": v(519.76, 227.75) * mm});
            skLineSegment(sketch, "E25.0.5.10", {"start": v(76.82, 227.75) * mm, "end": v(69.63, 223.6) * mm});
            skLineSegment(sketch, "E25.0.5.11", {"start": v(112.22, 254.95) * mm, "end": v(119.4, 250.8) * mm});
            skLineSegment(sketch, "E25.0.5.12", {"start": v(205.91, 223.6) * mm, "end": v(198.73, 227.75) * mm});
            skLineSegment(sketch, "E25.0.5.13", {"start": v(197.4, 254.95) * mm, "end": v(190.2, 250.8) * mm});
            skLineSegment(sketch, "E25.0.5.14", {"start": v(93.85, 227.75) * mm, "end": v(86.66, 223.6) * mm});
            skLineSegment(sketch, "E25.0.5.15", {"start": v(129.25, 254.95) * mm, "end": v(122.06, 250.8) * mm});
            skLineSegment(sketch, "E25.0.5.16", {"start": v(298.29, 227.75) * mm, "end": v(291.1, 223.6) * mm});
            skLineSegment(sketch, "E25.0.5.17", {"start": v(502.73, 227.75) * mm, "end": v(495.54, 223.6) * mm});
            skLineSegment(sketch, "E25.0.5.18", {"start": v(289.77, 250.8) * mm, "end": v(282.58, 254.95) * mm});
            skLineSegment(sketch, "E25.0.5.19", {"start": v(85.33, 250.8) * mm, "end": v(78.14, 254.95) * mm});
            skLineSegment(sketch, "E25.0.5.20", {"start": v(494.21, 250.8) * mm, "end": v(487.02, 254.95) * mm});
            skLineSegment(sketch, "E25.0.5.21", {"start": v(333.7, 254.95) * mm, "end": v(326.5, 250.8) * mm});
            skLineSegment(sketch, "E25.0.5.22", {"start": v(95.18, 254.95) * mm, "end": v(87.99, 250.8) * mm});
            skLineSegment(sketch, "E25.0.5.23", {"start": v(478.5, 223.6) * mm, "end": v(471.32, 227.75) * mm});
            skLineSegment(sketch, "E25.0.5.24", {"start": v(274.07, 223.6) * mm, "end": v(266.88, 227.75) * mm});
            skLineSegment(sketch, "E25.0.5.25", {"start": v(444.43, 223.6) * mm, "end": v(437.24, 227.75) * mm});
            skLineSegment(sketch, "E25.0.5.26", {"start": v(401.84, 254.95) * mm, "end": v(394.65, 250.8) * mm});
            skLineSegment(sketch, "E25.0.5.27", {"start": v(410.35, 223.6) * mm, "end": v(403.17, 227.75) * mm});
            skLineSegment(sketch, "E25.0.5.28", {"start": v(468.65, 227.75) * mm, "end": v(461.46, 223.6) * mm});
            skLineSegment(sketch, "E25.0.5.29", {"start": v(427.4, 223.6) * mm, "end": v(420.2, 227.75) * mm});
            skLineSegment(sketch, "E25.0.5.30", {"start": v(59.77, 227.75) * mm, "end": v(52.58, 223.6) * mm});
            skLineSegment(sketch, "E25.0.5.31", {"start": v(512.57, 240.2) * mm, "end": v(519.76, 236.05) * mm});
            skLineSegment(sketch, "E25.0.5.32", {"start": v(196.07, 227.75) * mm, "end": v(188.88, 223.6) * mm});
            skLineSegment(sketch, "E25.0.5.33", {"start": v(86.66, 223.6) * mm, "end": v(79.47, 227.75) * mm});
            skLineSegment(sketch, "E25.0.5.34", {"start": v(400.5, 227.75) * mm, "end": v(393.32, 223.6) * mm});
            skLineSegment(sketch, "E25.0.5.35", {"start": v(103.7, 223.6) * mm, "end": v(96.5, 227.75) * mm});
            skLineSegment(sketch, "E25.0.5.36", {"start": v(299.62, 254.95) * mm, "end": v(292.43, 250.8) * mm});
            skLineSegment(sketch, "E25.0.5.37", {"start": v(504.06, 254.95) * mm, "end": v(496.87, 250.8) * mm});
            skLineSegment(sketch, "E25.0.5.38", {"start": v(2.81, 242.5) * mm, "end": v(2.81, 250.8) * mm});
            skLineSegment(sketch, "E25.0.5.39", {"start": v(308.13, 223.6) * mm, "end": v(300.95, 227.75) * mm});
            skLineSegment(sketch, "E25.0.5.40", {"start": v(417.54, 227.75) * mm, "end": v(410.35, 223.6) * mm});
            skLineSegment(sketch, "E25.0.5.41", {"start": v(434.59, 227.75) * mm, "end": v(427.4, 223.6) * mm});
            skLineSegment(sketch, "E25.0.5.42", {"start": v(62.44, 227.75) * mm, "end": v(62.44, 236.05) * mm});
            skLineSegment(sketch, "E25.0.5.43", {"start": v(69.63, 223.6) * mm, "end": v(62.44, 227.75) * mm});
            skLineSegment(sketch, "E25.0.5.44", {"start": v(325.18, 223.6) * mm, "end": v(317.99, 227.75) * mm});
            skLineSegment(sketch, "E25.0.5.45", {"start": v(264.21, 227.75) * mm, "end": v(257.02, 223.6) * mm});
            skLineSegment(sketch, "E25.0.5.46", {"start": v(120.74, 223.6) * mm, "end": v(113.55, 227.75) * mm});
            skLineSegment(sketch, "E25.0.5.47", {"start": v(502.73, 236.05) * mm, "end": v(502.73, 227.75) * mm});
            skLineSegment(sketch, "E25.0.5.48", {"start": v(316.66, 254.95) * mm, "end": v(323.85, 250.8) * mm});
            skLineSegment(sketch, "E25.0.5.49", {"start": v(505.39, 227.75) * mm, "end": v(505.39, 236.05) * mm});
            skLineSegment(sketch, "E25.0.5.50", {"start": v(10, 238.35) * mm, "end": v(2.81, 242.5) * mm});
            skLineSegment(sketch, "E25.0.5.51", {"start": v(59.77, 236.05) * mm, "end": v(59.77, 227.75) * mm});
            skLineSegment(sketch, "E25.0.5.52", {"start": v(291.1, 223.6) * mm, "end": v(283.91, 227.75) * mm});
            skLineSegment(sketch, "E25.0.5.53", {"start": v(511.25, 242.5) * mm, "end": v(511.25, 250.8) * mm});
            skLineSegment(sketch, "E25.0.5.54", {"start": v(392, 250.8) * mm, "end": v(384.8, 254.95) * mm});
            skLineSegment(sketch, "E25.0.5.55", {"start": v(187.55, 250.8) * mm, "end": v(180.36, 254.95) * mm});
            skLineSegment(sketch, "E25.0.5.56", {"start": v(247.18, 236.05) * mm, "end": v(247.18, 227.75) * mm});
            skLineSegment(sketch, "E25.0.5.57", {"start": v(188.88, 240.2) * mm, "end": v(196.07, 236.05) * mm});
            skLineSegment(sketch, "E25.0.5.58", {"start": v(369.1, 236.05) * mm, "end": v(376.29, 240.2) * mm});
            skLineSegment(sketch, "E25.0.5.59", {"start": v(409.03, 242.5) * mm, "end": v(409.03, 250.8) * mm});
            skLineSegment(sketch, "E25.0.5.60", {"start": v(188.88, 223.6) * mm, "end": v(181.7, 227.75) * mm});
            skLineSegment(sketch, "E25.0.5.61", {"start": v(204.59, 242.5) * mm, "end": v(204.59, 250.8) * mm});
            skLineSegment(sketch, "E25.0.5.62", {"start": v(164.66, 236.05) * mm, "end": v(171.85, 240.2) * mm});
            skLineSegment(sketch, "E25.0.5.63", {"start": v(230.15, 236.05) * mm, "end": v(230.15, 227.75) * mm});
            skLineSegment(sketch, "E25.0.5.64", {"start": v(343.54, 250.8) * mm, "end": v(343.54, 242.5) * mm});
            skLineSegment(sketch, "E25.0.5.65", {"start": v(139.1, 250.8) * mm, "end": v(139.1, 242.5) * mm});
            skLineSegment(sketch, "E25.0.5.66", {"start": v(70.95, 242.5) * mm, "end": v(78.14, 238.35) * mm});
            skLineSegment(sketch, "E25.0.5.67", {"start": v(96.5, 227.75) * mm, "end": v(96.5, 236.05) * mm});
            skLineSegment(sketch, "E25.0.5.68", {"start": v(44.07, 254.95) * mm, "end": v(36.88, 250.8) * mm});
            skLineSegment(sketch, "E25.0.5.69", {"start": v(162, 227.75) * mm, "end": v(154.8, 223.6) * mm});
            skLineSegment(sketch, "E25.0.5.70", {"start": v(300.95, 227.75) * mm, "end": v(300.95, 236.05) * mm});
            skLineSegment(sketch, "E25.0.5.71", {"start": v(222.96, 223.6) * mm, "end": v(215.77, 227.75) * mm});
            skLineSegment(sketch, "E25.0.5.72", {"start": v(452.95, 238.35) * mm, "end": v(460.14, 242.5) * mm});
            skLineSegment(sketch, "E25.0.5.73", {"start": v(369.1, 227.75) * mm, "end": v(369.1, 236.05) * mm});
            skLineSegment(sketch, "E25.0.5.74", {"start": v(366.43, 227.75) * mm, "end": v(359.24, 223.6) * mm});
            skLineSegment(sketch, "E25.0.5.75", {"start": v(164.66, 227.75) * mm, "end": v(164.66, 236.05) * mm});
            skLineSegment(sketch, "E25.0.5.76", {"start": v(248.5, 238.35) * mm, "end": v(255.7, 242.5) * mm});
            skLineSegment(sketch, "E25.0.5.77", {"start": v(249.84, 236.05) * mm, "end": v(257.02, 240.2) * mm});
            skLineSegment(sketch, "E25.0.5.78", {"start": v(393.32, 223.6) * mm, "end": v(386.13, 227.75) * mm});
            skLineSegment(sketch, "E25.0.5.79", {"start": v(62.44, 236.05) * mm, "end": v(69.63, 240.2) * mm});
            skLineSegment(sketch, "E25.0.5.80", {"start": v(136.44, 242.5) * mm, "end": v(136.44, 250.8) * mm});
            skLineSegment(sketch, "E25.0.5.81", {"start": v(102.37, 242.5) * mm, "end": v(102.37, 250.8) * mm});
            skLineSegment(sketch, "E25.0.5.82", {"start": v(418.88, 254.95) * mm, "end": v(426.07, 250.8) * mm});
            skLineSegment(sketch, "E25.0.5.83", {"start": v(454.28, 236.05) * mm, "end": v(461.46, 240.2) * mm});
            skLineSegment(sketch, "E25.0.5.84", {"start": v(78.14, 254.95) * mm, "end": v(70.95, 250.8) * mm});
            skLineSegment(sketch, "E25.0.5.85", {"start": v(105.03, 242.5) * mm, "end": v(105.03, 250.8) * mm});
            skLineSegment(sketch, "E25.0.5.86", {"start": v(190.2, 242.5) * mm, "end": v(197.4, 238.35) * mm});
            skLineSegment(sketch, "E25.0.5.87", {"start": v(352.06, 227.75) * mm, "end": v(352.06, 236.05) * mm});
            skLineSegment(sketch, "E25.0.5.88", {"start": v(400.5, 236.05) * mm, "end": v(400.5, 227.75) * mm});
            skLineSegment(sketch, "E25.0.5.89", {"start": v(299.62, 238.35) * mm, "end": v(306.8, 242.5) * mm});
            skLineSegment(sketch, "E25.0.5.90", {"start": v(190.2, 250.8) * mm, "end": v(190.2, 242.5) * mm});
            skLineSegment(sketch, "E25.0.5.91", {"start": v(76.82, 236.05) * mm, "end": v(76.82, 227.75) * mm});
            skLineSegment(sketch, "E25.0.5.92", {"start": v(392, 242.5) * mm, "end": v(392, 250.8) * mm});
            skLineSegment(sketch, "E25.0.5.93", {"start": v(309.47, 250.8) * mm, "end": v(316.66, 254.95) * mm});
            skLineSegment(sketch, "E25.0.5.94", {"start": v(349.4, 227.75) * mm, "end": v(342.21, 223.6) * mm});
            skLineSegment(sketch, "E25.0.5.95", {"start": v(257.02, 240.2) * mm, "end": v(264.21, 236.05) * mm});
            skLineSegment(sketch, "E25.0.5.96", {"start": v(61.1, 254.95) * mm, "end": v(68.3, 250.8) * mm});
            skLineSegment(sketch, "E25.0.5.97", {"start": v(146.29, 254.95) * mm, "end": v(139.1, 250.8) * mm});
            skLineSegment(sketch, "E25.0.5.98", {"start": v(154.8, 223.6) * mm, "end": v(147.62, 227.75) * mm});
            skLineSegment(sketch, "E25.0.5.99", {"start": v(306.8, 250.8) * mm, "end": v(299.62, 254.95) * mm});
            skLineSegment(sketch, "E25.0.5.100", {"start": v(87.99, 242.5) * mm, "end": v(95.18, 238.35) * mm});
            skLineSegment(sketch, "E25.0.5.101", {"start": v(105.03, 250.8) * mm, "end": v(112.22, 254.95) * mm});
            skLineSegment(sketch, "E25.0.5.102", {"start": v(102.37, 250.8) * mm, "end": v(95.18, 254.95) * mm});
            skLineSegment(sketch, "E25.0.5.103", {"start": v(187.55, 242.5) * mm, "end": v(187.55, 250.8) * mm});
            skLineSegment(sketch, "E25.0.5.104", {"start": v(61.1, 238.35) * mm, "end": v(53.92, 242.5) * mm});
            skLineSegment(sketch, "E25.0.5.105", {"start": v(437.24, 227.75) * mm, "end": v(437.24, 236.05) * mm});
            skLineSegment(sketch, "E25.0.5.106", {"start": v(393.32, 240.2) * mm, "end": v(400.5, 236.05) * mm});
            skLineSegment(sketch, "E25.0.5.107", {"start": v(232.8, 227.75) * mm, "end": v(232.8, 236.05) * mm});
            skLineSegment(sketch, "E25.0.5.108", {"start": v(87.99, 250.8) * mm, "end": v(87.99, 242.5) * mm});
            skLineSegment(sketch, "E25.0.5.109", {"start": v(113.55, 227.75) * mm, "end": v(113.55, 236.05) * mm});
            skLineSegment(sketch, "E25.0.5.110", {"start": v(332.37, 236.05) * mm, "end": v(332.37, 227.75) * mm});
            skLineSegment(sketch, "E25.0.5.111", {"start": v(266.88, 227.75) * mm, "end": v(266.88, 236.05) * mm});
            skLineSegment(sketch, "E25.0.5.112", {"start": v(180.36, 254.95) * mm, "end": v(173.17, 250.8) * mm});
            skLineSegment(sketch, "E25.0.5.113", {"start": v(181.7, 236.05) * mm, "end": v(188.88, 240.2) * mm});
            skLineSegment(sketch, "E25.0.5.114", {"start": v(68.3, 250.8) * mm, "end": v(68.3, 242.5) * mm});
            skLineSegment(sketch, "E25.0.5.115", {"start": v(317.99, 227.75) * mm, "end": v(317.99, 236.05) * mm});
            skLineSegment(sketch, "E25.0.5.116", {"start": v(485.7, 227.75) * mm, "end": v(478.5, 223.6) * mm});
            skLineSegment(sketch, "E25.0.5.117", {"start": v(10, 254.95) * mm, "end": v(17.19, 250.8) * mm});
            skLineSegment(sketch, "E25.0.5.118", {"start": v(376.29, 223.6) * mm, "end": v(369.1, 227.75) * mm});
            skLineSegment(sketch, "E25.0.5.119", {"start": v(452.95, 254.95) * mm, "end": v(445.76, 250.8) * mm});
            skLineSegment(sketch, "E25.0.5.120", {"start": v(315.32, 227.75) * mm, "end": v(308.13, 223.6) * mm});
            skLineSegment(sketch, "E25.0.5.121", {"start": v(93.85, 236.05) * mm, "end": v(93.85, 227.75) * mm});
            skLineSegment(sketch, "E25.0.5.122", {"start": v(35.55, 223.6) * mm, "end": v(28.36, 227.75) * mm});
            skLineSegment(sketch, "E25.0.5.123", {"start": v(45.4, 227.75) * mm, "end": v(45.4, 236.05) * mm});
            skLineSegment(sketch, "E25.0.5.124", {"start": v(42.74, 227.75) * mm, "end": v(35.55, 223.6) * mm});
            skLineSegment(sketch, "E25.0.5.125", {"start": v(434.59, 236.05) * mm, "end": v(434.59, 227.75) * mm});
            skLineSegment(sketch, "E25.0.5.126", {"start": v(340.88, 242.5) * mm, "end": v(340.88, 250.8) * mm});
            skLineSegment(sketch, "E25.0.5.127", {"start": v(394.65, 242.5) * mm, "end": v(401.84, 238.35) * mm});
            skLineSegment(sketch, "E25.0.5.128", {"start": v(153.48, 250.8) * mm, "end": v(146.29, 254.95) * mm});
            skLineSegment(sketch, "E25.0.5.129", {"start": v(52.58, 223.6) * mm, "end": v(45.4, 227.75) * mm});
            skLineSegment(sketch, "E25.0.5.130", {"start": v(25.7, 236.05) * mm, "end": v(25.7, 227.75) * mm});
            skLineSegment(sketch, "E25.0.5.131", {"start": v(28.36, 227.75) * mm, "end": v(28.36, 236.05) * mm});
            skLineSegment(sketch, "E25.0.5.132", {"start": v(45.4, 236.05) * mm, "end": v(52.58, 240.2) * mm});
            skLineSegment(sketch, "E25.0.5.133", {"start": v(451.62, 227.75) * mm, "end": v(444.43, 223.6) * mm});
            skLineSegment(sketch, "E25.0.5.134", {"start": v(411.7, 242.5) * mm, "end": v(411.7, 250.8) * mm});
            skLineSegment(sketch, "E25.0.5.135", {"start": v(342.21, 223.6) * mm, "end": v(335.02, 227.75) * mm});
            skLineSegment(sketch, "E25.0.5.136", {"start": v(443.1, 242.5) * mm, "end": v(443.1, 250.8) * mm});
            skLineSegment(sketch, "E25.0.5.137", {"start": v(357.92, 250.8) * mm, "end": v(350.73, 254.95) * mm});
            skLineSegment(sketch, "E25.0.5.138", {"start": v(289.77, 242.5) * mm, "end": v(289.77, 250.8) * mm});
            skLineSegment(sketch, "E25.0.5.139", {"start": v(204.59, 250.8) * mm, "end": v(197.4, 254.95) * mm});
            skLineSegment(sketch, "E25.0.5.140", {"start": v(198.73, 236.05) * mm, "end": v(205.91, 240.2) * mm});
            skLineSegment(sketch, "E25.0.5.141", {"start": v(454.28, 227.75) * mm, "end": v(454.28, 236.05) * mm});
            skLineSegment(sketch, "E25.0.5.142", {"start": v(86.66, 240.2) * mm, "end": v(93.85, 236.05) * mm});
            skLineSegment(sketch, "E25.0.5.143", {"start": v(443.1, 250.8) * mm, "end": v(435.91, 254.95) * mm});
            skLineSegment(sketch, "E25.0.5.144", {"start": v(435.91, 254.95) * mm, "end": v(428.72, 250.8) * mm});
            skLineSegment(sketch, "E25.0.5.145", {"start": v(437.24, 236.05) * mm, "end": v(444.43, 240.2) * mm});
            skLineSegment(sketch, "E25.0.5.146", {"start": v(231.47, 254.95) * mm, "end": v(224.28, 250.8) * mm});
            skLineSegment(sketch, "E25.0.5.147", {"start": v(79.47, 227.75) * mm, "end": v(79.47, 236.05) * mm});
            skLineSegment(sketch, "E25.0.5.148", {"start": v(309.47, 242.5) * mm, "end": v(309.47, 250.8) * mm});
            skLineSegment(sketch, "E25.0.5.149", {"start": v(214.44, 254.95) * mm, "end": v(221.63, 250.8) * mm});
            skLineSegment(sketch, "E25.0.5.150", {"start": v(238.66, 250.8) * mm, "end": v(231.47, 254.95) * mm});
            skLineSegment(sketch, "E25.0.5.151", {"start": v(394.65, 250.8) * mm, "end": v(394.65, 242.5) * mm});
            skLineSegment(sketch, "E25.0.5.152", {"start": v(445.76, 242.5) * mm, "end": v(452.95, 238.35) * mm});
            skLineSegment(sketch, "E25.0.5.153", {"start": v(241.32, 242.5) * mm, "end": v(248.5, 238.35) * mm});
            skLineSegment(sketch, "E25.0.5.154", {"start": v(231.47, 238.35) * mm, "end": v(238.66, 242.5) * mm});
            skLineSegment(sketch, "E25.0.5.155", {"start": v(79.47, 236.05) * mm, "end": v(86.66, 240.2) * mm});
            skLineSegment(sketch, "E25.0.5.156", {"start": v(350.73, 254.95) * mm, "end": v(343.54, 250.8) * mm});
            skLineSegment(sketch, "E25.0.5.157", {"start": v(196.07, 236.05) * mm, "end": v(196.07, 227.75) * mm});
            skLineSegment(sketch, "E25.0.5.158", {"start": v(240, 223.6) * mm, "end": v(232.8, 227.75) * mm});
            skLineSegment(sketch, "E25.0.5.159", {"start": v(69.63, 240.2) * mm, "end": v(76.82, 236.05) * mm});
            skLineSegment(sketch, "E25.0.5.160", {"start": v(349.4, 236.05) * mm, "end": v(349.4, 227.75) * mm});
            skLineSegment(sketch, "E25.0.5.161", {"start": v(383.48, 227.75) * mm, "end": v(376.29, 223.6) * mm});
            skLineSegment(sketch, "E25.0.5.162", {"start": v(144.96, 236.05) * mm, "end": v(144.96, 227.75) * mm});
            skLineSegment(sketch, "E25.0.5.163", {"start": v(179.04, 227.75) * mm, "end": v(171.85, 223.6) * mm});
            skLineSegment(sketch, "E25.0.5.164", {"start": v(386.13, 236.05) * mm, "end": v(393.32, 240.2) * mm});
            skLineSegment(sketch, "E25.0.5.165", {"start": v(435.91, 238.35) * mm, "end": v(443.1, 242.5) * mm});
            skLineSegment(sketch, "E25.0.5.166", {"start": v(504.06, 238.35) * mm, "end": v(511.25, 242.5) * mm});
            skLineSegment(sketch, "E25.0.5.167", {"start": v(403.17, 227.75) * mm, "end": v(403.17, 236.05) * mm});
            skLineSegment(sketch, "E25.0.5.168", {"start": v(241.32, 250.8) * mm, "end": v(241.32, 242.5) * mm});
            skLineSegment(sketch, "E25.0.5.169", {"start": v(359.24, 223.6) * mm, "end": v(352.06, 227.75) * mm});
            skLineSegment(sketch, "E25.0.5.170", {"start": v(213.1, 227.75) * mm, "end": v(205.91, 223.6) * mm});
            skLineSegment(sketch, "E25.0.5.171", {"start": v(34.22, 250.8) * mm, "end": v(27.03, 254.95) * mm});
            skLineSegment(sketch, "E25.0.5.172", {"start": v(461.46, 240.2) * mm, "end": v(468.65, 236.05) * mm});
            skLineSegment(sketch, "E25.0.5.173", {"start": v(505.39, 236.05) * mm, "end": v(512.57, 240.2) * mm});
            skLineSegment(sketch, "E25.0.5.174", {"start": v(300.95, 236.05) * mm, "end": v(308.13, 240.2) * mm});
            skLineSegment(sketch, "E25.0.5.175", {"start": v(230.15, 227.75) * mm, "end": v(222.96, 223.6) * mm});
            skLineSegment(sketch, "E25.0.5.176", {"start": v(265.55, 238.35) * mm, "end": v(258.36, 242.5) * mm});
            skLineSegment(sketch, "E25.0.5.177", {"start": v(144.96, 227.75) * mm, "end": v(137.77, 223.6) * mm});
            skLineSegment(sketch, "E25.0.5.178", {"start": v(27.03, 254.95) * mm, "end": v(19.84, 250.8) * mm});
            skLineSegment(sketch, "E25.0.5.179", {"start": v(384.8, 254.95) * mm, "end": v(377.61, 250.8) * mm});
            skLineSegment(sketch, "E25.0.5.180", {"start": v(340.88, 250.8) * mm, "end": v(333.7, 254.95) * mm});
            skLineSegment(sketch, "E25.0.5.181", {"start": v(136.44, 250.8) * mm, "end": v(129.25, 254.95) * mm});
            skLineSegment(sketch, "E25.0.5.182", {"start": v(198.73, 227.75) * mm, "end": v(198.73, 236.05) * mm});
            skLineSegment(sketch, "E25.0.5.183", {"start": v(70.95, 250.8) * mm, "end": v(70.95, 242.5) * mm});
            skLineSegment(sketch, "E25.0.5.184", {"start": v(127.93, 236.05) * mm, "end": v(127.93, 227.75) * mm});
            skLineSegment(sketch, "E25.0.5.185", {"start": v(461.46, 223.6) * mm, "end": v(454.28, 227.75) * mm});
            skLineSegment(sketch, "E25.0.5.186", {"start": v(444.43, 240.2) * mm, "end": v(451.62, 236.05) * mm});
            skLineSegment(sketch, "E25.0.5.187", {"start": v(445.76, 250.8) * mm, "end": v(445.76, 242.5) * mm});
            skLineSegment(sketch, "E25.0.5.188", {"start": v(240, 240.2) * mm, "end": v(247.18, 236.05) * mm});
            skLineSegment(sketch, "E25.0.5.189", {"start": v(298.29, 236.05) * mm, "end": v(298.29, 227.75) * mm});
            skLineSegment(sketch, "E25.0.5.190", {"start": v(471.32, 227.75) * mm, "end": v(471.32, 236.05) * mm});
            skLineSegment(sketch, "E25.0.5.191", {"start": v(207.25, 242.5) * mm, "end": v(207.25, 250.8) * mm});
            skLineSegment(sketch, "E25.0.5.192", {"start": v(281.26, 227.75) * mm, "end": v(274.07, 223.6) * mm});
            skLineSegment(sketch, "E25.0.5.193", {"start": v(257.02, 223.6) * mm, "end": v(249.84, 227.75) * mm});
            skLineSegment(sketch, "E25.0.5.194", {"start": v(248.5, 254.95) * mm, "end": v(241.32, 250.8) * mm});
            skLineSegment(sketch, "E25.0.5.195", {"start": v(451.62, 236.05) * mm, "end": v(451.62, 227.75) * mm});
            skLineSegment(sketch, "E25.0.5.196", {"start": v(110.88, 227.75) * mm, "end": v(103.7, 223.6) * mm});
            skLineSegment(sketch, "E25.0.5.197", {"start": v(401.84, 238.35) * mm, "end": v(409.03, 242.5) * mm});
            skLineSegment(sketch, "E25.0.5.198", {"start": v(292.43, 250.8) * mm, "end": v(292.43, 242.5) * mm});
            skLineSegment(sketch, "E25.0.5.199", {"start": v(171.85, 223.6) * mm, "end": v(164.66, 227.75) * mm});
            skLineSegment(sketch, "E25.0.5.200", {"start": v(197.4, 238.35) * mm, "end": v(204.59, 242.5) * mm});
            skLineSegment(sketch, "E25.0.5.201", {"start": v(52.58, 240.2) * mm, "end": v(59.77, 236.05) * mm});
            skLineSegment(sketch, "E25.0.5.202", {"start": v(411.7, 250.8) * mm, "end": v(418.88, 254.95) * mm});
            skLineSegment(sketch, "E25.0.5.203", {"start": v(409.03, 250.8) * mm, "end": v(401.84, 254.95) * mm});
            skLineSegment(sketch, "E25.0.5.204", {"start": v(207.25, 250.8) * mm, "end": v(214.44, 254.95) * mm});
            skLineSegment(sketch, "E25.0.5.205", {"start": v(403.17, 236.05) * mm, "end": v(410.35, 240.2) * mm});
            skLineSegment(sketch, "E25.0.5.206", {"start": v(495.54, 223.6) * mm, "end": v(488.35, 227.75) * mm});
            skLineSegment(sketch, "E25.0.5.207", {"start": v(468.65, 236.05) * mm, "end": v(468.65, 227.75) * mm});
            skLineSegment(sketch, "E25.0.5.208", {"start": v(264.21, 236.05) * mm, "end": v(264.21, 227.75) * mm});
            skLineSegment(sketch, "E25.0.5.209", {"start": v(238.66, 242.5) * mm, "end": v(238.66, 250.8) * mm});
            skLineSegment(sketch, "E25.0.5.210", {"start": v(247.18, 227.75) * mm, "end": v(240, 223.6) * mm});
            skLineSegment(sketch, "E25.0.5.211", {"start": v(85.33, 242.5) * mm, "end": v(85.33, 250.8) * mm});
            skLineSegment(sketch, "E25.0.5.212", {"start": v(137.77, 223.6) * mm, "end": v(130.58, 227.75) * mm});
            skLineSegment(sketch, "E25.0.5.213", {"start": v(374.96, 242.5) * mm, "end": v(367.77, 238.35) * mm});
            skLineSegment(sketch, "E25.0.5.214", {"start": v(323.85, 250.8) * mm, "end": v(323.85, 242.5) * mm});
            skLineSegment(sketch, "E25.0.5.215", {"start": v(266.88, 236.05) * mm, "end": v(274.07, 240.2) * mm});
            skLineSegment(sketch, "E25.0.5.216", {"start": v(326.5, 250.8) * mm, "end": v(326.5, 242.5) * mm});
            skLineSegment(sketch, "E25.0.5.217", {"start": v(232.8, 236.05) * mm, "end": v(240, 240.2) * mm});
            skLineSegment(sketch, "E25.0.5.218", {"start": v(306.8, 242.5) * mm, "end": v(306.8, 250.8) * mm});
            skLineSegment(sketch, "E25.0.5.219", {"start": v(119.4, 250.8) * mm, "end": v(119.4, 242.5) * mm});
            skLineSegment(sketch, "E25.0.5.220", {"start": v(122.06, 250.8) * mm, "end": v(122.06, 242.5) * mm});
            skLineSegment(sketch, "E25.0.5.221", {"start": v(170.52, 242.5) * mm, "end": v(163.33, 238.35) * mm});
            skLineSegment(sketch, "E25.0.5.222", {"start": v(428.72, 250.8) * mm, "end": v(428.72, 242.5) * mm});
            skLineSegment(sketch, "E25.0.5.223", {"start": v(51.26, 242.5) * mm, "end": v(51.26, 250.8) * mm});
            skLineSegment(sketch, "E25.0.5.224", {"start": v(386.13, 227.75) * mm, "end": v(386.13, 236.05) * mm});
            skLineSegment(sketch, "E25.0.5.225", {"start": v(44.07, 238.35) * mm, "end": v(51.26, 242.5) * mm});
            skLineSegment(sketch, "E25.0.5.226", {"start": v(462.8, 250.8) * mm, "end": v(469.99, 254.95) * mm});
            skLineSegment(sketch, "E25.0.5.227", {"start": v(214.44, 238.35) * mm, "end": v(207.25, 242.5) * mm});
            skLineSegment(sketch, "E25.0.5.228", {"start": v(205.91, 240.2) * mm, "end": v(213.1, 236.05) * mm});
            skLineSegment(sketch, "E25.0.5.229", {"start": v(366.43, 236.05) * mm, "end": v(366.43, 227.75) * mm});
            skLineSegment(sketch, "E25.0.5.230", {"start": v(130.58, 236.05) * mm, "end": v(137.77, 240.2) * mm});
            skLineSegment(sketch, "E25.0.5.231", {"start": v(224.28, 250.8) * mm, "end": v(224.28, 242.5) * mm});
            skLineSegment(sketch, "E25.0.5.232", {"start": v(384.8, 238.35) * mm, "end": v(392, 242.5) * mm});
            skLineSegment(sketch, "E25.0.5.233", {"start": v(275.4, 242.5) * mm, "end": v(282.58, 238.35) * mm});
            skLineSegment(sketch, "E25.0.5.234", {"start": v(19.84, 242.5) * mm, "end": v(27.03, 238.35) * mm});
            skLineSegment(sketch, "E25.0.5.235", {"start": v(180.36, 238.35) * mm, "end": v(187.55, 242.5) * mm});
            skLineSegment(sketch, "E25.0.5.236", {"start": v(410.35, 240.2) * mm, "end": v(417.54, 236.05) * mm});
            skLineSegment(sketch, "E25.0.5.237", {"start": v(255.7, 250.8) * mm, "end": v(248.5, 254.95) * mm});
            skLineSegment(sketch, "E25.0.5.238", {"start": v(53.92, 250.8) * mm, "end": v(61.1, 254.95) * mm});
            skLineSegment(sketch, "E25.0.5.239", {"start": v(162, 236.05) * mm, "end": v(162, 227.75) * mm});
            skLineSegment(sketch, "E25.0.5.240", {"start": v(51.26, 250.8) * mm, "end": v(44.07, 254.95) * mm});
            skLineSegment(sketch, "E25.0.5.241", {"start": v(427.4, 240.2) * mm, "end": v(434.59, 236.05) * mm});
            skLineSegment(sketch, "E25.0.5.242", {"start": v(460.14, 250.8) * mm, "end": v(452.95, 254.95) * mm});
            skLineSegment(sketch, "E25.0.5.243", {"start": v(272.74, 242.5) * mm, "end": v(265.55, 238.35) * mm});
            skLineSegment(sketch, "E25.0.5.244", {"start": v(181.7, 227.75) * mm, "end": v(181.7, 236.05) * mm});
            skLineSegment(sketch, "E25.0.5.245", {"start": v(335.02, 236.05) * mm, "end": v(342.21, 240.2) * mm});
            skLineSegment(sketch, "E25.0.5.246", {"start": v(221.63, 250.8) * mm, "end": v(221.63, 242.5) * mm});
            skLineSegment(sketch, "E25.0.5.247", {"start": v(68.3, 242.5) * mm, "end": v(61.1, 238.35) * mm});
            skLineSegment(sketch, "E25.0.5.248", {"start": v(130.58, 227.75) * mm, "end": v(130.58, 236.05) * mm});
            skLineSegment(sketch, "E25.0.5.249", {"start": v(477.18, 242.5) * mm, "end": v(469.99, 238.35) * mm});
            skLineSegment(sketch, "E25.0.5.250", {"start": v(469.99, 254.95) * mm, "end": v(477.18, 250.8) * mm});
            skLineSegment(sketch, "E25.0.5.251", {"start": v(360.58, 242.5) * mm, "end": v(360.58, 250.8) * mm});
            skLineSegment(sketch, "E25.0.5.252", {"start": v(122.06, 242.5) * mm, "end": v(129.25, 238.35) * mm});
            skLineSegment(sketch, "E25.0.5.253", {"start": v(95.18, 238.35) * mm, "end": v(102.37, 242.5) * mm});
            skLineSegment(sketch, "E25.0.5.254", {"start": v(137.77, 240.2) * mm, "end": v(144.96, 236.05) * mm});
            skLineSegment(sketch, "E25.0.5.255", {"start": v(469.99, 238.35) * mm, "end": v(462.8, 242.5) * mm});
            skLineSegment(sketch, "E25.0.5.256", {"start": v(417.54, 236.05) * mm, "end": v(417.54, 227.75) * mm});
            skLineSegment(sketch, "E25.0.5.257", {"start": v(120.74, 240.2) * mm, "end": v(127.93, 236.05) * mm});
            skLineSegment(sketch, "E25.0.5.258", {"start": v(477.18, 250.8) * mm, "end": v(477.18, 242.5) * mm});
            skLineSegment(sketch, "E25.0.5.259", {"start": v(420.2, 236.05) * mm, "end": v(427.4, 240.2) * mm});
            skLineSegment(sketch, "E25.0.5.260", {"start": v(275.4, 250.8) * mm, "end": v(275.4, 242.5) * mm});
            skLineSegment(sketch, "E25.0.5.261", {"start": v(255.7, 242.5) * mm, "end": v(255.7, 250.8) * mm});
            skLineSegment(sketch, "E25.0.5.262", {"start": v(215.77, 236.05) * mm, "end": v(222.96, 240.2) * mm});
            skLineSegment(sketch, "E25.0.5.263", {"start": v(42.74, 236.05) * mm, "end": v(42.74, 227.75) * mm});
            skLineSegment(sketch, "E25.0.5.264", {"start": v(350.73, 238.35) * mm, "end": v(357.92, 242.5) * mm});
            skLineSegment(sketch, "E25.0.5.265", {"start": v(78.14, 238.35) * mm, "end": v(85.33, 242.5) * mm});
            skLineSegment(sketch, "E25.0.5.266", {"start": v(119.4, 242.5) * mm, "end": v(112.22, 238.35) * mm});
            skLineSegment(sketch, "E25.0.5.267", {"start": v(19.84, 250.8) * mm, "end": v(19.84, 242.5) * mm});
            skLineSegment(sketch, "E25.0.5.268", {"start": v(496.87, 242.5) * mm, "end": v(504.06, 238.35) * mm});
            skLineSegment(sketch, "E25.0.5.269", {"start": v(325.18, 240.2) * mm, "end": v(332.37, 236.05) * mm});
            skLineSegment(sketch, "E25.0.5.270", {"start": v(367.77, 254.95) * mm, "end": v(374.96, 250.8) * mm});
            skLineSegment(sketch, "E25.0.5.271", {"start": v(258.36, 242.5) * mm, "end": v(258.36, 250.8) * mm});
            skLineSegment(sketch, "E25.0.5.272", {"start": v(163.33, 254.95) * mm, "end": v(170.52, 250.8) * mm});
            skLineSegment(sketch, "E25.0.5.273", {"start": v(179.04, 236.05) * mm, "end": v(179.04, 227.75) * mm});
            skLineSegment(sketch, "E25.0.5.274", {"start": v(249.84, 227.75) * mm, "end": v(249.84, 236.05) * mm});
            skLineSegment(sketch, "E25.0.5.275", {"start": v(139.1, 242.5) * mm, "end": v(146.29, 238.35) * mm});
            skLineSegment(sketch, "E25.0.5.276", {"start": v(418.88, 238.35) * mm, "end": v(411.7, 242.5) * mm});
            skLineSegment(sketch, "E25.0.5.277", {"start": v(426.07, 250.8) * mm, "end": v(426.07, 242.5) * mm});
            skLineSegment(sketch, "E25.0.5.278", {"start": v(367.77, 238.35) * mm, "end": v(360.58, 242.5) * mm});
            skLineSegment(sketch, "E25.0.5.279", {"start": v(352.06, 236.05) * mm, "end": v(359.24, 240.2) * mm});
            skLineSegment(sketch, "E25.0.5.280", {"start": v(163.33, 238.35) * mm, "end": v(156.14, 242.5) * mm});
            skLineSegment(sketch, "E25.0.5.281", {"start": v(112.22, 238.35) * mm, "end": v(105.03, 242.5) * mm});
            skLineSegment(sketch, "E25.0.5.282", {"start": v(487.02, 254.95) * mm, "end": v(479.83, 250.8) * mm});
            skLineSegment(sketch, "E25.0.5.283", {"start": v(374.96, 250.8) * mm, "end": v(374.96, 242.5) * mm});
            skLineSegment(sketch, "E25.0.5.284", {"start": v(17.19, 242.5) * mm, "end": v(10, 238.35) * mm});
            skLineSegment(sketch, "E25.0.5.285", {"start": v(221.63, 242.5) * mm, "end": v(214.44, 238.35) * mm});
            skLineSegment(sketch, "E25.0.5.286", {"start": v(282.58, 254.95) * mm, "end": v(275.4, 250.8) * mm});
            skLineSegment(sketch, "E25.0.5.287", {"start": v(335.02, 227.75) * mm, "end": v(335.02, 236.05) * mm});
            skLineSegment(sketch, "E25.0.5.288", {"start": v(170.52, 250.8) * mm, "end": v(170.52, 242.5) * mm});
            skLineSegment(sketch, "E25.0.5.289", {"start": v(291.1, 240.2) * mm, "end": v(298.29, 236.05) * mm});
            skLineSegment(sketch, "E25.0.5.290", {"start": v(173.17, 250.8) * mm, "end": v(173.17, 242.5) * mm});
            skLineSegment(sketch, "E25.0.5.291", {"start": v(495.54, 240.2) * mm, "end": v(502.73, 236.05) * mm});
            skLineSegment(sketch, "E25.0.5.292", {"start": v(147.62, 227.75) * mm, "end": v(147.62, 236.05) * mm});
            skLineSegment(sketch, "E25.0.5.293", {"start": v(153.48, 242.5) * mm, "end": v(153.48, 250.8) * mm});
            skLineSegment(sketch, "E25.0.5.294", {"start": v(222.96, 240.2) * mm, "end": v(230.15, 236.05) * mm});
            skLineSegment(sketch, "E25.0.5.295", {"start": v(479.83, 250.8) * mm, "end": v(479.83, 242.5) * mm});
            skLineSegment(sketch, "E25.0.5.296", {"start": v(420.2, 227.75) * mm, "end": v(420.2, 236.05) * mm});
            skLineSegment(sketch, "E25.0.5.297", {"start": v(326.5, 242.5) * mm, "end": v(333.7, 238.35) * mm});
            skLineSegment(sketch, "E25.0.5.298", {"start": v(173.17, 242.5) * mm, "end": v(180.36, 238.35) * mm});
            skLineSegment(sketch, "E25.0.5.299", {"start": v(342.21, 240.2) * mm, "end": v(349.4, 236.05) * mm});
            skLineSegment(sketch, "E25.0.5.300", {"start": v(265.55, 254.95) * mm, "end": v(272.74, 250.8) * mm});
            skLineSegment(sketch, "E25.0.5.301", {"start": v(274.07, 240.2) * mm, "end": v(281.26, 236.05) * mm});
            skLineSegment(sketch, "E25.0.5.302", {"start": v(215.77, 227.75) * mm, "end": v(215.77, 236.05) * mm});
            skLineSegment(sketch, "E25.0.5.303", {"start": v(462.8, 242.5) * mm, "end": v(462.8, 250.8) * mm});
            skLineSegment(sketch, "E25.0.5.304", {"start": v(281.26, 236.05) * mm, "end": v(281.26, 227.75) * mm});
            skLineSegment(sketch, "E25.0.5.305", {"start": v(156.14, 242.5) * mm, "end": v(156.14, 250.8) * mm});
            skLineSegment(sketch, "E25.0.5.306", {"start": v(213.1, 236.05) * mm, "end": v(213.1, 227.75) * mm});
            skLineSegment(sketch, "E25.0.5.307", {"start": v(96.5, 236.05) * mm, "end": v(103.7, 240.2) * mm});
            skLineSegment(sketch, "E25.0.5.308", {"start": v(460.14, 242.5) * mm, "end": v(460.14, 250.8) * mm});
            skLineSegment(sketch, "E25.0.5.309", {"start": v(323.85, 242.5) * mm, "end": v(316.66, 238.35) * mm});
            skLineSegment(sketch, "E25.0.5.310", {"start": v(272.74, 250.8) * mm, "end": v(272.74, 242.5) * mm});
            skLineSegment(sketch, "E25.0.5.311", {"start": v(377.61, 242.5) * mm, "end": v(384.8, 238.35) * mm});
            skLineSegment(sketch, "E25.0.5.312", {"start": v(282.58, 238.35) * mm, "end": v(289.77, 242.5) * mm});
            skLineSegment(sketch, "E25.0.5.313", {"start": v(146.29, 238.35) * mm, "end": v(153.48, 242.5) * mm});
            skLineSegment(sketch, "E25.0.5.314", {"start": v(343.54, 242.5) * mm, "end": v(350.73, 238.35) * mm});
            skLineSegment(sketch, "E25.0.5.315", {"start": v(376.29, 240.2) * mm, "end": v(383.48, 236.05) * mm});
            skLineSegment(sketch, "E25.0.5.316", {"start": v(171.85, 240.2) * mm, "end": v(179.04, 236.05) * mm});
            skLineSegment(sketch, "E25.0.5.317", {"start": v(53.92, 242.5) * mm, "end": v(53.92, 250.8) * mm});
            skLineSegment(sketch, "E25.0.5.318", {"start": v(292.43, 242.5) * mm, "end": v(299.62, 238.35) * mm});
            skLineSegment(sketch, "E25.0.5.319", {"start": v(377.61, 250.8) * mm, "end": v(377.61, 242.5) * mm});
            skLineSegment(sketch, "E25.0.5.320", {"start": v(383.48, 236.05) * mm, "end": v(383.48, 227.75) * mm});
            skLineSegment(sketch, "E25.0.5.321", {"start": v(129.25, 238.35) * mm, "end": v(136.44, 242.5) * mm});
            skLineSegment(sketch, "E25.0.5.322", {"start": v(428.72, 242.5) * mm, "end": v(435.91, 238.35) * mm});
            skLineSegment(sketch, "E25.0.5.323", {"start": v(496.87, 250.8) * mm, "end": v(496.87, 242.5) * mm});
            skLineSegment(sketch, "E25.0.5.324", {"start": v(224.28, 242.5) * mm, "end": v(231.47, 238.35) * mm});
            skLineSegment(sketch, "E25.0.5.325", {"start": v(333.7, 238.35) * mm, "end": v(340.88, 242.5) * mm});
            skLineSegment(sketch, "E25.0.5.326", {"start": v(11.33, 236.05) * mm, "end": v(18.52, 240.2) * mm});
            skLineSegment(sketch, "E25.0.5.327", {"start": v(18.52, 240.2) * mm, "end": v(25.7, 236.05) * mm});
            skLineSegment(sketch, "E25.0.5.328", {"start": v(494.21, 242.5) * mm, "end": v(494.21, 250.8) * mm});
            skLineSegment(sketch, "E25.0.5.329", {"start": v(315.32, 236.05) * mm, "end": v(315.32, 227.75) * mm});
            skLineSegment(sketch, "E25.0.5.330", {"start": v(360.58, 250.8) * mm, "end": v(367.77, 254.95) * mm});
            skLineSegment(sketch, "E25.0.5.331", {"start": v(316.66, 238.35) * mm, "end": v(309.47, 242.5) * mm});
            skLineSegment(sketch, "E25.0.5.332", {"start": v(308.13, 240.2) * mm, "end": v(315.32, 236.05) * mm});
            skLineSegment(sketch, "E25.0.5.333", {"start": v(147.62, 236.05) * mm, "end": v(154.8, 240.2) * mm});
            skLineSegment(sketch, "E25.0.5.334", {"start": v(359.24, 240.2) * mm, "end": v(366.43, 236.05) * mm});
            skLineSegment(sketch, "E25.0.5.335", {"start": v(110.88, 236.05) * mm, "end": v(110.88, 227.75) * mm});
            skLineSegment(sketch, "E25.0.5.336", {"start": v(154.8, 240.2) * mm, "end": v(162, 236.05) * mm});
            skLineSegment(sketch, "E25.0.5.337", {"start": v(17.19, 250.8) * mm, "end": v(17.19, 242.5) * mm});
            skLineSegment(sketch, "E25.0.5.338", {"start": v(156.14, 250.8) * mm, "end": v(163.33, 254.95) * mm});
            skLineSegment(sketch, "E25.0.5.339", {"start": v(103.7, 240.2) * mm, "end": v(110.88, 236.05) * mm});
            skLineSegment(sketch, "E25.0.5.340", {"start": v(471.32, 236.05) * mm, "end": v(478.5, 240.2) * mm});
            skLineSegment(sketch, "E25.0.5.341", {"start": v(426.07, 242.5) * mm, "end": v(418.88, 238.35) * mm});
            skLineSegment(sketch, "E25.0.5.342", {"start": v(357.92, 242.5) * mm, "end": v(357.92, 250.8) * mm});
            skLineSegment(sketch, "E25.0.5.343", {"start": v(317.99, 236.05) * mm, "end": v(325.18, 240.2) * mm});
            skLineSegment(sketch, "E25.0.5.344", {"start": v(258.36, 250.8) * mm, "end": v(265.55, 254.95) * mm});
            skLineSegment(sketch, "E25.0.5.345", {"start": v(283.91, 227.75) * mm, "end": v(283.91, 236.05) * mm});
            skLineSegment(sketch, "E25.0.5.346", {"start": v(283.91, 236.05) * mm, "end": v(291.1, 240.2) * mm});
            skLineSegment(sketch, "E25.0.5.347", {"start": v(113.55, 236.05) * mm, "end": v(120.74, 240.2) * mm});
            skLineSegment(sketch, "E25.0.5.348", {"start": v(36.88, 242.5) * mm, "end": v(44.07, 238.35) * mm});
            skLineSegment(sketch, "E25.0.5.349", {"start": v(36.88, 250.8) * mm, "end": v(36.88, 242.5) * mm});
            skLineSegment(sketch, "E25.0.5.350", {"start": v(34.22, 242.5) * mm, "end": v(34.22, 250.8) * mm});
            skLineSegment(sketch, "E25.0.5.351", {"start": v(485.7, 236.05) * mm, "end": v(485.7, 227.75) * mm});
            skLineSegment(sketch, "E25.0.5.352", {"start": v(478.5, 240.2) * mm, "end": v(485.7, 236.05) * mm});
            skLineSegment(sketch, "E25.0.5.353", {"start": v(487.02, 238.35) * mm, "end": v(494.21, 242.5) * mm});
            skLineSegment(sketch, "E25.0.5.354", {"start": v(27.03, 238.35) * mm, "end": v(34.22, 242.5) * mm});
            skLineSegment(sketch, "E25.0.5.355", {"start": v(479.83, 242.5) * mm, "end": v(487.02, 238.35) * mm});
            skLineSegment(sketch, "E25.0.5.356", {"start": v(28.36, 236.05) * mm, "end": v(35.55, 240.2) * mm});
            skLineSegment(sketch, "E25.0.5.357", {"start": v(35.55, 240.2) * mm, "end": v(42.74, 236.05) * mm});
            skLineSegment(sketch, "E25.0.5.358", {"start": v(488.35, 236.05) * mm, "end": v(495.54, 240.2) * mm});
            skLineSegment(sketch, "E25.0.5.359", {"start": v(488.35, 227.75) * mm, "end": v(488.35, 236.05) * mm});
            skLineSegment(sketch, "E25.0.6.0", {"start": v(332.37, 198.25) * mm, "end": v(325.18, 194.1) * mm});
            skLineSegment(sketch, "E25.0.6.1", {"start": v(511.25, 221.3) * mm, "end": v(504.06, 225.45) * mm});
            skLineSegment(sketch, "E25.0.6.2", {"start": v(2.81, 221.3) * mm, "end": v(10, 225.45) * mm});
            skLineSegment(sketch, "E25.0.6.3", {"start": v(127.93, 198.25) * mm, "end": v(120.74, 194.1) * mm});
            skLineSegment(sketch, "E25.0.6.4", {"start": v(512.57, 194.1) * mm, "end": v(505.39, 198.25) * mm});
            skLineSegment(sketch, "E25.0.6.5", {"start": v(519.76, 198.25) * mm, "end": v(512.57, 194.1) * mm});
            skLineSegment(sketch, "E25.0.6.6", {"start": v(25.7, 198.25) * mm, "end": v(18.52, 194.1) * mm});
            skLineSegment(sketch, "E25.0.6.7", {"start": v(11.33, 198.25) * mm, "end": v(11.33, 206.55) * mm});
            skLineSegment(sketch, "E25.0.6.8", {"start": v(18.52, 194.1) * mm, "end": v(11.33, 198.25) * mm});
            skLineSegment(sketch, "E25.0.6.9", {"start": v(519.76, 206.55) * mm, "end": v(519.76, 198.25) * mm});
            skLineSegment(sketch, "E25.0.6.10", {"start": v(76.82, 198.25) * mm, "end": v(69.63, 194.1) * mm});
            skLineSegment(sketch, "E25.0.6.11", {"start": v(112.22, 225.45) * mm, "end": v(119.4, 221.3) * mm});
            skLineSegment(sketch, "E25.0.6.12", {"start": v(205.91, 194.1) * mm, "end": v(198.73, 198.25) * mm});
            skLineSegment(sketch, "E25.0.6.13", {"start": v(197.4, 225.45) * mm, "end": v(190.2, 221.3) * mm});
            skLineSegment(sketch, "E25.0.6.14", {"start": v(93.85, 198.25) * mm, "end": v(86.66, 194.1) * mm});
            skLineSegment(sketch, "E25.0.6.15", {"start": v(129.25, 225.45) * mm, "end": v(122.06, 221.3) * mm});
            skLineSegment(sketch, "E25.0.6.16", {"start": v(298.29, 198.25) * mm, "end": v(291.1, 194.1) * mm});
            skLineSegment(sketch, "E25.0.6.17", {"start": v(502.73, 198.25) * mm, "end": v(495.54, 194.1) * mm});
            skLineSegment(sketch, "E25.0.6.18", {"start": v(289.77, 221.3) * mm, "end": v(282.58, 225.45) * mm});
            skLineSegment(sketch, "E25.0.6.19", {"start": v(85.33, 221.3) * mm, "end": v(78.14, 225.45) * mm});
            skLineSegment(sketch, "E25.0.6.20", {"start": v(494.21, 221.3) * mm, "end": v(487.02, 225.45) * mm});
            skLineSegment(sketch, "E25.0.6.21", {"start": v(333.7, 225.45) * mm, "end": v(326.5, 221.3) * mm});
            skLineSegment(sketch, "E25.0.6.22", {"start": v(95.18, 225.45) * mm, "end": v(87.99, 221.3) * mm});
            skLineSegment(sketch, "E25.0.6.23", {"start": v(478.5, 194.1) * mm, "end": v(471.32, 198.25) * mm});
            skLineSegment(sketch, "E25.0.6.24", {"start": v(274.07, 194.1) * mm, "end": v(266.88, 198.25) * mm});
            skLineSegment(sketch, "E25.0.6.25", {"start": v(444.43, 194.1) * mm, "end": v(437.24, 198.25) * mm});
            skLineSegment(sketch, "E25.0.6.26", {"start": v(401.84, 225.45) * mm, "end": v(394.65, 221.3) * mm});
            skLineSegment(sketch, "E25.0.6.27", {"start": v(410.35, 194.1) * mm, "end": v(403.17, 198.25) * mm});
            skLineSegment(sketch, "E25.0.6.28", {"start": v(468.65, 198.25) * mm, "end": v(461.46, 194.1) * mm});
            skLineSegment(sketch, "E25.0.6.29", {"start": v(427.4, 194.1) * mm, "end": v(420.2, 198.25) * mm});
            skLineSegment(sketch, "E25.0.6.30", {"start": v(59.77, 198.25) * mm, "end": v(52.58, 194.1) * mm});
            skLineSegment(sketch, "E25.0.6.31", {"start": v(512.57, 210.7) * mm, "end": v(519.76, 206.55) * mm});
            skLineSegment(sketch, "E25.0.6.32", {"start": v(196.07, 198.25) * mm, "end": v(188.88, 194.1) * mm});
            skLineSegment(sketch, "E25.0.6.33", {"start": v(86.66, 194.1) * mm, "end": v(79.47, 198.25) * mm});
            skLineSegment(sketch, "E25.0.6.34", {"start": v(400.5, 198.25) * mm, "end": v(393.32, 194.1) * mm});
            skLineSegment(sketch, "E25.0.6.35", {"start": v(103.7, 194.1) * mm, "end": v(96.5, 198.25) * mm});
            skLineSegment(sketch, "E25.0.6.36", {"start": v(299.62, 225.45) * mm, "end": v(292.43, 221.3) * mm});
            skLineSegment(sketch, "E25.0.6.37", {"start": v(504.06, 225.45) * mm, "end": v(496.87, 221.3) * mm});
            skLineSegment(sketch, "E25.0.6.38", {"start": v(2.81, 213) * mm, "end": v(2.81, 221.3) * mm});
            skLineSegment(sketch, "E25.0.6.39", {"start": v(308.13, 194.1) * mm, "end": v(300.95, 198.25) * mm});
            skLineSegment(sketch, "E25.0.6.40", {"start": v(417.54, 198.25) * mm, "end": v(410.35, 194.1) * mm});
            skLineSegment(sketch, "E25.0.6.41", {"start": v(434.59, 198.25) * mm, "end": v(427.4, 194.1) * mm});
            skLineSegment(sketch, "E25.0.6.42", {"start": v(62.44, 198.25) * mm, "end": v(62.44, 206.55) * mm});
            skLineSegment(sketch, "E25.0.6.43", {"start": v(69.63, 194.1) * mm, "end": v(62.44, 198.25) * mm});
            skLineSegment(sketch, "E25.0.6.44", {"start": v(325.18, 194.1) * mm, "end": v(317.99, 198.25) * mm});
            skLineSegment(sketch, "E25.0.6.45", {"start": v(264.21, 198.25) * mm, "end": v(257.02, 194.1) * mm});
            skLineSegment(sketch, "E25.0.6.46", {"start": v(120.74, 194.1) * mm, "end": v(113.55, 198.25) * mm});
            skLineSegment(sketch, "E25.0.6.47", {"start": v(502.73, 206.55) * mm, "end": v(502.73, 198.25) * mm});
            skLineSegment(sketch, "E25.0.6.48", {"start": v(316.66, 225.45) * mm, "end": v(323.85, 221.3) * mm});
            skLineSegment(sketch, "E25.0.6.49", {"start": v(505.39, 198.25) * mm, "end": v(505.39, 206.55) * mm});
            skLineSegment(sketch, "E25.0.6.50", {"start": v(10, 208.85) * mm, "end": v(2.81, 213) * mm});
            skLineSegment(sketch, "E25.0.6.51", {"start": v(59.77, 206.55) * mm, "end": v(59.77, 198.25) * mm});
            skLineSegment(sketch, "E25.0.6.52", {"start": v(291.1, 194.1) * mm, "end": v(283.91, 198.25) * mm});
            skLineSegment(sketch, "E25.0.6.53", {"start": v(511.25, 213) * mm, "end": v(511.25, 221.3) * mm});
            skLineSegment(sketch, "E25.0.6.54", {"start": v(392, 221.3) * mm, "end": v(384.8, 225.45) * mm});
            skLineSegment(sketch, "E25.0.6.55", {"start": v(187.55, 221.3) * mm, "end": v(180.36, 225.45) * mm});
            skLineSegment(sketch, "E25.0.6.56", {"start": v(247.18, 206.55) * mm, "end": v(247.18, 198.25) * mm});
            skLineSegment(sketch, "E25.0.6.57", {"start": v(188.88, 210.7) * mm, "end": v(196.07, 206.55) * mm});
            skLineSegment(sketch, "E25.0.6.58", {"start": v(369.1, 206.55) * mm, "end": v(376.29, 210.7) * mm});
            skLineSegment(sketch, "E25.0.6.59", {"start": v(409.03, 213) * mm, "end": v(409.03, 221.3) * mm});
            skLineSegment(sketch, "E25.0.6.60", {"start": v(188.88, 194.1) * mm, "end": v(181.7, 198.25) * mm});
            skLineSegment(sketch, "E25.0.6.61", {"start": v(204.59, 213) * mm, "end": v(204.59, 221.3) * mm});
            skLineSegment(sketch, "E25.0.6.62", {"start": v(164.66, 206.55) * mm, "end": v(171.85, 210.7) * mm});
            skLineSegment(sketch, "E25.0.6.63", {"start": v(230.15, 206.55) * mm, "end": v(230.15, 198.25) * mm});
            skLineSegment(sketch, "E25.0.6.64", {"start": v(343.54, 221.3) * mm, "end": v(343.54, 213) * mm});
            skLineSegment(sketch, "E25.0.6.65", {"start": v(139.1, 221.3) * mm, "end": v(139.1, 213) * mm});
            skLineSegment(sketch, "E25.0.6.66", {"start": v(70.95, 213) * mm, "end": v(78.14, 208.85) * mm});
            skLineSegment(sketch, "E25.0.6.67", {"start": v(96.5, 198.25) * mm, "end": v(96.5, 206.55) * mm});
            skLineSegment(sketch, "E25.0.6.68", {"start": v(44.07, 225.45) * mm, "end": v(36.88, 221.3) * mm});
            skLineSegment(sketch, "E25.0.6.69", {"start": v(162, 198.25) * mm, "end": v(154.8, 194.1) * mm});
            skLineSegment(sketch, "E25.0.6.70", {"start": v(300.95, 198.25) * mm, "end": v(300.95, 206.55) * mm});
            skLineSegment(sketch, "E25.0.6.71", {"start": v(222.96, 194.1) * mm, "end": v(215.77, 198.25) * mm});
            skLineSegment(sketch, "E25.0.6.72", {"start": v(452.95, 208.85) * mm, "end": v(460.14, 213) * mm});
            skLineSegment(sketch, "E25.0.6.73", {"start": v(369.1, 198.25) * mm, "end": v(369.1, 206.55) * mm});
            skLineSegment(sketch, "E25.0.6.74", {"start": v(366.43, 198.25) * mm, "end": v(359.24, 194.1) * mm});
            skLineSegment(sketch, "E25.0.6.75", {"start": v(164.66, 198.25) * mm, "end": v(164.66, 206.55) * mm});
            skLineSegment(sketch, "E25.0.6.76", {"start": v(248.5, 208.85) * mm, "end": v(255.7, 213) * mm});
            skLineSegment(sketch, "E25.0.6.77", {"start": v(249.84, 206.55) * mm, "end": v(257.02, 210.7) * mm});
            skLineSegment(sketch, "E25.0.6.78", {"start": v(393.32, 194.1) * mm, "end": v(386.13, 198.25) * mm});
            skLineSegment(sketch, "E25.0.6.79", {"start": v(62.44, 206.55) * mm, "end": v(69.63, 210.7) * mm});
            skLineSegment(sketch, "E25.0.6.80", {"start": v(136.44, 213) * mm, "end": v(136.44, 221.3) * mm});
            skLineSegment(sketch, "E25.0.6.81", {"start": v(102.37, 213) * mm, "end": v(102.37, 221.3) * mm});
            skLineSegment(sketch, "E25.0.6.82", {"start": v(418.88, 225.45) * mm, "end": v(426.07, 221.3) * mm});
            skLineSegment(sketch, "E25.0.6.83", {"start": v(454.28, 206.55) * mm, "end": v(461.46, 210.7) * mm});
            skLineSegment(sketch, "E25.0.6.84", {"start": v(78.14, 225.45) * mm, "end": v(70.95, 221.3) * mm});
            skLineSegment(sketch, "E25.0.6.85", {"start": v(105.03, 213) * mm, "end": v(105.03, 221.3) * mm});
            skLineSegment(sketch, "E25.0.6.86", {"start": v(190.2, 213) * mm, "end": v(197.4, 208.85) * mm});
            skLineSegment(sketch, "E25.0.6.87", {"start": v(352.06, 198.25) * mm, "end": v(352.06, 206.55) * mm});
            skLineSegment(sketch, "E25.0.6.88", {"start": v(400.5, 206.55) * mm, "end": v(400.5, 198.25) * mm});
            skLineSegment(sketch, "E25.0.6.89", {"start": v(299.62, 208.85) * mm, "end": v(306.8, 213) * mm});
            skLineSegment(sketch, "E25.0.6.90", {"start": v(190.2, 221.3) * mm, "end": v(190.2, 213) * mm});
            skLineSegment(sketch, "E25.0.6.91", {"start": v(76.82, 206.55) * mm, "end": v(76.82, 198.25) * mm});
            skLineSegment(sketch, "E25.0.6.92", {"start": v(392, 213) * mm, "end": v(392, 221.3) * mm});
            skLineSegment(sketch, "E25.0.6.93", {"start": v(309.47, 221.3) * mm, "end": v(316.66, 225.45) * mm});
            skLineSegment(sketch, "E25.0.6.94", {"start": v(349.4, 198.25) * mm, "end": v(342.21, 194.1) * mm});
            skLineSegment(sketch, "E25.0.6.95", {"start": v(257.02, 210.7) * mm, "end": v(264.21, 206.55) * mm});
            skLineSegment(sketch, "E25.0.6.96", {"start": v(61.1, 225.45) * mm, "end": v(68.3, 221.3) * mm});
            skLineSegment(sketch, "E25.0.6.97", {"start": v(146.29, 225.45) * mm, "end": v(139.1, 221.3) * mm});
            skLineSegment(sketch, "E25.0.6.98", {"start": v(154.8, 194.1) * mm, "end": v(147.62, 198.25) * mm});
            skLineSegment(sketch, "E25.0.6.99", {"start": v(306.8, 221.3) * mm, "end": v(299.62, 225.45) * mm});
            skLineSegment(sketch, "E25.0.6.100", {"start": v(87.99, 213) * mm, "end": v(95.18, 208.85) * mm});
            skLineSegment(sketch, "E25.0.6.101", {"start": v(105.03, 221.3) * mm, "end": v(112.22, 225.45) * mm});
            skLineSegment(sketch, "E25.0.6.102", {"start": v(102.37, 221.3) * mm, "end": v(95.18, 225.45) * mm});
            skLineSegment(sketch, "E25.0.6.103", {"start": v(187.55, 213) * mm, "end": v(187.55, 221.3) * mm});
            skLineSegment(sketch, "E25.0.6.104", {"start": v(61.1, 208.85) * mm, "end": v(53.92, 213) * mm});
            skLineSegment(sketch, "E25.0.6.105", {"start": v(437.24, 198.25) * mm, "end": v(437.24, 206.55) * mm});
            skLineSegment(sketch, "E25.0.6.106", {"start": v(393.32, 210.7) * mm, "end": v(400.5, 206.55) * mm});
            skLineSegment(sketch, "E25.0.6.107", {"start": v(232.8, 198.25) * mm, "end": v(232.8, 206.55) * mm});
            skLineSegment(sketch, "E25.0.6.108", {"start": v(87.99, 221.3) * mm, "end": v(87.99, 213) * mm});
            skLineSegment(sketch, "E25.0.6.109", {"start": v(113.55, 198.25) * mm, "end": v(113.55, 206.55) * mm});
            skLineSegment(sketch, "E25.0.6.110", {"start": v(332.37, 206.55) * mm, "end": v(332.37, 198.25) * mm});
            skLineSegment(sketch, "E25.0.6.111", {"start": v(266.88, 198.25) * mm, "end": v(266.88, 206.55) * mm});
            skLineSegment(sketch, "E25.0.6.112", {"start": v(180.36, 225.45) * mm, "end": v(173.17, 221.3) * mm});
            skLineSegment(sketch, "E25.0.6.113", {"start": v(181.7, 206.55) * mm, "end": v(188.88, 210.7) * mm});
            skLineSegment(sketch, "E25.0.6.114", {"start": v(68.3, 221.3) * mm, "end": v(68.3, 213) * mm});
            skLineSegment(sketch, "E25.0.6.115", {"start": v(317.99, 198.25) * mm, "end": v(317.99, 206.55) * mm});
            skLineSegment(sketch, "E25.0.6.116", {"start": v(485.7, 198.25) * mm, "end": v(478.5, 194.1) * mm});
            skLineSegment(sketch, "E25.0.6.117", {"start": v(10, 225.45) * mm, "end": v(17.19, 221.3) * mm});
            skLineSegment(sketch, "E25.0.6.118", {"start": v(376.29, 194.1) * mm, "end": v(369.1, 198.25) * mm});
            skLineSegment(sketch, "E25.0.6.119", {"start": v(452.95, 225.45) * mm, "end": v(445.76, 221.3) * mm});
            skLineSegment(sketch, "E25.0.6.120", {"start": v(315.32, 198.25) * mm, "end": v(308.13, 194.1) * mm});
            skLineSegment(sketch, "E25.0.6.121", {"start": v(93.85, 206.55) * mm, "end": v(93.85, 198.25) * mm});
            skLineSegment(sketch, "E25.0.6.122", {"start": v(35.55, 194.1) * mm, "end": v(28.36, 198.25) * mm});
            skLineSegment(sketch, "E25.0.6.123", {"start": v(45.4, 198.25) * mm, "end": v(45.4, 206.55) * mm});
            skLineSegment(sketch, "E25.0.6.124", {"start": v(42.74, 198.25) * mm, "end": v(35.55, 194.1) * mm});
            skLineSegment(sketch, "E25.0.6.125", {"start": v(434.59, 206.55) * mm, "end": v(434.59, 198.25) * mm});
            skLineSegment(sketch, "E25.0.6.126", {"start": v(340.88, 213) * mm, "end": v(340.88, 221.3) * mm});
            skLineSegment(sketch, "E25.0.6.127", {"start": v(394.65, 213) * mm, "end": v(401.84, 208.85) * mm});
            skLineSegment(sketch, "E25.0.6.128", {"start": v(153.48, 221.3) * mm, "end": v(146.29, 225.45) * mm});
            skLineSegment(sketch, "E25.0.6.129", {"start": v(52.58, 194.1) * mm, "end": v(45.4, 198.25) * mm});
            skLineSegment(sketch, "E25.0.6.130", {"start": v(25.7, 206.55) * mm, "end": v(25.7, 198.25) * mm});
            skLineSegment(sketch, "E25.0.6.131", {"start": v(28.36, 198.25) * mm, "end": v(28.36, 206.55) * mm});
            skLineSegment(sketch, "E25.0.6.132", {"start": v(45.4, 206.55) * mm, "end": v(52.58, 210.7) * mm});
            skLineSegment(sketch, "E25.0.6.133", {"start": v(451.62, 198.25) * mm, "end": v(444.43, 194.1) * mm});
            skLineSegment(sketch, "E25.0.6.134", {"start": v(411.7, 213) * mm, "end": v(411.7, 221.3) * mm});
            skLineSegment(sketch, "E25.0.6.135", {"start": v(342.21, 194.1) * mm, "end": v(335.02, 198.25) * mm});
            skLineSegment(sketch, "E25.0.6.136", {"start": v(443.1, 213) * mm, "end": v(443.1, 221.3) * mm});
            skLineSegment(sketch, "E25.0.6.137", {"start": v(357.92, 221.3) * mm, "end": v(350.73, 225.45) * mm});
            skLineSegment(sketch, "E25.0.6.138", {"start": v(289.77, 213) * mm, "end": v(289.77, 221.3) * mm});
            skLineSegment(sketch, "E25.0.6.139", {"start": v(204.59, 221.3) * mm, "end": v(197.4, 225.45) * mm});
            skLineSegment(sketch, "E25.0.6.140", {"start": v(198.73, 206.55) * mm, "end": v(205.91, 210.7) * mm});
            skLineSegment(sketch, "E25.0.6.141", {"start": v(454.28, 198.25) * mm, "end": v(454.28, 206.55) * mm});
            skLineSegment(sketch, "E25.0.6.142", {"start": v(86.66, 210.7) * mm, "end": v(93.85, 206.55) * mm});
            skLineSegment(sketch, "E25.0.6.143", {"start": v(443.1, 221.3) * mm, "end": v(435.91, 225.45) * mm});
            skLineSegment(sketch, "E25.0.6.144", {"start": v(435.91, 225.45) * mm, "end": v(428.72, 221.3) * mm});
            skLineSegment(sketch, "E25.0.6.145", {"start": v(437.24, 206.55) * mm, "end": v(444.43, 210.7) * mm});
            skLineSegment(sketch, "E25.0.6.146", {"start": v(231.47, 225.45) * mm, "end": v(224.28, 221.3) * mm});
            skLineSegment(sketch, "E25.0.6.147", {"start": v(79.47, 198.25) * mm, "end": v(79.47, 206.55) * mm});
            skLineSegment(sketch, "E25.0.6.148", {"start": v(309.47, 213) * mm, "end": v(309.47, 221.3) * mm});
            skLineSegment(sketch, "E25.0.6.149", {"start": v(214.44, 225.45) * mm, "end": v(221.63, 221.3) * mm});
            skLineSegment(sketch, "E25.0.6.150", {"start": v(238.66, 221.3) * mm, "end": v(231.47, 225.45) * mm});
            skLineSegment(sketch, "E25.0.6.151", {"start": v(394.65, 221.3) * mm, "end": v(394.65, 213) * mm});
            skLineSegment(sketch, "E25.0.6.152", {"start": v(445.76, 213) * mm, "end": v(452.95, 208.85) * mm});
            skLineSegment(sketch, "E25.0.6.153", {"start": v(241.32, 213) * mm, "end": v(248.5, 208.85) * mm});
            skLineSegment(sketch, "E25.0.6.154", {"start": v(231.47, 208.85) * mm, "end": v(238.66, 213) * mm});
            skLineSegment(sketch, "E25.0.6.155", {"start": v(79.47, 206.55) * mm, "end": v(86.66, 210.7) * mm});
            skLineSegment(sketch, "E25.0.6.156", {"start": v(350.73, 225.45) * mm, "end": v(343.54, 221.3) * mm});
            skLineSegment(sketch, "E25.0.6.157", {"start": v(196.07, 206.55) * mm, "end": v(196.07, 198.25) * mm});
            skLineSegment(sketch, "E25.0.6.158", {"start": v(240, 194.1) * mm, "end": v(232.8, 198.25) * mm});
            skLineSegment(sketch, "E25.0.6.159", {"start": v(69.63, 210.7) * mm, "end": v(76.82, 206.55) * mm});
            skLineSegment(sketch, "E25.0.6.160", {"start": v(349.4, 206.55) * mm, "end": v(349.4, 198.25) * mm});
            skLineSegment(sketch, "E25.0.6.161", {"start": v(383.48, 198.25) * mm, "end": v(376.29, 194.1) * mm});
            skLineSegment(sketch, "E25.0.6.162", {"start": v(144.96, 206.55) * mm, "end": v(144.96, 198.25) * mm});
            skLineSegment(sketch, "E25.0.6.163", {"start": v(179.04, 198.25) * mm, "end": v(171.85, 194.1) * mm});
            skLineSegment(sketch, "E25.0.6.164", {"start": v(386.13, 206.55) * mm, "end": v(393.32, 210.7) * mm});
            skLineSegment(sketch, "E25.0.6.165", {"start": v(435.91, 208.85) * mm, "end": v(443.1, 213) * mm});
            skLineSegment(sketch, "E25.0.6.166", {"start": v(504.06, 208.85) * mm, "end": v(511.25, 213) * mm});
            skLineSegment(sketch, "E25.0.6.167", {"start": v(403.17, 198.25) * mm, "end": v(403.17, 206.55) * mm});
            skLineSegment(sketch, "E25.0.6.168", {"start": v(241.32, 221.3) * mm, "end": v(241.32, 213) * mm});
            skLineSegment(sketch, "E25.0.6.169", {"start": v(359.24, 194.1) * mm, "end": v(352.06, 198.25) * mm});
            skLineSegment(sketch, "E25.0.6.170", {"start": v(213.1, 198.25) * mm, "end": v(205.91, 194.1) * mm});
            skLineSegment(sketch, "E25.0.6.171", {"start": v(34.22, 221.3) * mm, "end": v(27.03, 225.45) * mm});
            skLineSegment(sketch, "E25.0.6.172", {"start": v(461.46, 210.7) * mm, "end": v(468.65, 206.55) * mm});
            skLineSegment(sketch, "E25.0.6.173", {"start": v(505.39, 206.55) * mm, "end": v(512.57, 210.7) * mm});
            skLineSegment(sketch, "E25.0.6.174", {"start": v(300.95, 206.55) * mm, "end": v(308.13, 210.7) * mm});
            skLineSegment(sketch, "E25.0.6.175", {"start": v(230.15, 198.25) * mm, "end": v(222.96, 194.1) * mm});
            skLineSegment(sketch, "E25.0.6.176", {"start": v(265.55, 208.85) * mm, "end": v(258.36, 213) * mm});
            skLineSegment(sketch, "E25.0.6.177", {"start": v(144.96, 198.25) * mm, "end": v(137.77, 194.1) * mm});
            skLineSegment(sketch, "E25.0.6.178", {"start": v(27.03, 225.45) * mm, "end": v(19.84, 221.3) * mm});
            skLineSegment(sketch, "E25.0.6.179", {"start": v(384.8, 225.45) * mm, "end": v(377.61, 221.3) * mm});
            skLineSegment(sketch, "E25.0.6.180", {"start": v(340.88, 221.3) * mm, "end": v(333.7, 225.45) * mm});
            skLineSegment(sketch, "E25.0.6.181", {"start": v(136.44, 221.3) * mm, "end": v(129.25, 225.45) * mm});
            skLineSegment(sketch, "E25.0.6.182", {"start": v(198.73, 198.25) * mm, "end": v(198.73, 206.55) * mm});
            skLineSegment(sketch, "E25.0.6.183", {"start": v(70.95, 221.3) * mm, "end": v(70.95, 213) * mm});
            skLineSegment(sketch, "E25.0.6.184", {"start": v(127.93, 206.55) * mm, "end": v(127.93, 198.25) * mm});
            skLineSegment(sketch, "E25.0.6.185", {"start": v(461.46, 194.1) * mm, "end": v(454.28, 198.25) * mm});
            skLineSegment(sketch, "E25.0.6.186", {"start": v(444.43, 210.7) * mm, "end": v(451.62, 206.55) * mm});
            skLineSegment(sketch, "E25.0.6.187", {"start": v(445.76, 221.3) * mm, "end": v(445.76, 213) * mm});
            skLineSegment(sketch, "E25.0.6.188", {"start": v(240, 210.7) * mm, "end": v(247.18, 206.55) * mm});
            skLineSegment(sketch, "E25.0.6.189", {"start": v(298.29, 206.55) * mm, "end": v(298.29, 198.25) * mm});
            skLineSegment(sketch, "E25.0.6.190", {"start": v(471.32, 198.25) * mm, "end": v(471.32, 206.55) * mm});
            skLineSegment(sketch, "E25.0.6.191", {"start": v(207.25, 213) * mm, "end": v(207.25, 221.3) * mm});
            skLineSegment(sketch, "E25.0.6.192", {"start": v(281.26, 198.25) * mm, "end": v(274.07, 194.1) * mm});
            skLineSegment(sketch, "E25.0.6.193", {"start": v(257.02, 194.1) * mm, "end": v(249.84, 198.25) * mm});
            skLineSegment(sketch, "E25.0.6.194", {"start": v(248.5, 225.45) * mm, "end": v(241.32, 221.3) * mm});
            skLineSegment(sketch, "E25.0.6.195", {"start": v(451.62, 206.55) * mm, "end": v(451.62, 198.25) * mm});
            skLineSegment(sketch, "E25.0.6.196", {"start": v(110.88, 198.25) * mm, "end": v(103.7, 194.1) * mm});
            skLineSegment(sketch, "E25.0.6.197", {"start": v(401.84, 208.85) * mm, "end": v(409.03, 213) * mm});
            skLineSegment(sketch, "E25.0.6.198", {"start": v(292.43, 221.3) * mm, "end": v(292.43, 213) * mm});
            skLineSegment(sketch, "E25.0.6.199", {"start": v(171.85, 194.1) * mm, "end": v(164.66, 198.25) * mm});
            skLineSegment(sketch, "E25.0.6.200", {"start": v(197.4, 208.85) * mm, "end": v(204.59, 213) * mm});
            skLineSegment(sketch, "E25.0.6.201", {"start": v(52.58, 210.7) * mm, "end": v(59.77, 206.55) * mm});
            skLineSegment(sketch, "E25.0.6.202", {"start": v(411.7, 221.3) * mm, "end": v(418.88, 225.45) * mm});
            skLineSegment(sketch, "E25.0.6.203", {"start": v(409.03, 221.3) * mm, "end": v(401.84, 225.45) * mm});
            skLineSegment(sketch, "E25.0.6.204", {"start": v(207.25, 221.3) * mm, "end": v(214.44, 225.45) * mm});
            skLineSegment(sketch, "E25.0.6.205", {"start": v(403.17, 206.55) * mm, "end": v(410.35, 210.7) * mm});
            skLineSegment(sketch, "E25.0.6.206", {"start": v(495.54, 194.1) * mm, "end": v(488.35, 198.25) * mm});
            skLineSegment(sketch, "E25.0.6.207", {"start": v(468.65, 206.55) * mm, "end": v(468.65, 198.25) * mm});
            skLineSegment(sketch, "E25.0.6.208", {"start": v(264.21, 206.55) * mm, "end": v(264.21, 198.25) * mm});
            skLineSegment(sketch, "E25.0.6.209", {"start": v(238.66, 213) * mm, "end": v(238.66, 221.3) * mm});
            skLineSegment(sketch, "E25.0.6.210", {"start": v(247.18, 198.25) * mm, "end": v(240, 194.1) * mm});
            skLineSegment(sketch, "E25.0.6.211", {"start": v(85.33, 213) * mm, "end": v(85.33, 221.3) * mm});
            skLineSegment(sketch, "E25.0.6.212", {"start": v(137.77, 194.1) * mm, "end": v(130.58, 198.25) * mm});
            skLineSegment(sketch, "E25.0.6.213", {"start": v(374.96, 213) * mm, "end": v(367.77, 208.85) * mm});
            skLineSegment(sketch, "E25.0.6.214", {"start": v(323.85, 221.3) * mm, "end": v(323.85, 213) * mm});
            skLineSegment(sketch, "E25.0.6.215", {"start": v(266.88, 206.55) * mm, "end": v(274.07, 210.7) * mm});
            skLineSegment(sketch, "E25.0.6.216", {"start": v(326.5, 221.3) * mm, "end": v(326.5, 213) * mm});
            skLineSegment(sketch, "E25.0.6.217", {"start": v(232.8, 206.55) * mm, "end": v(240, 210.7) * mm});
            skLineSegment(sketch, "E25.0.6.218", {"start": v(306.8, 213) * mm, "end": v(306.8, 221.3) * mm});
            skLineSegment(sketch, "E25.0.6.219", {"start": v(119.4, 221.3) * mm, "end": v(119.4, 213) * mm});
            skLineSegment(sketch, "E25.0.6.220", {"start": v(122.06, 221.3) * mm, "end": v(122.06, 213) * mm});
            skLineSegment(sketch, "E25.0.6.221", {"start": v(170.52, 213) * mm, "end": v(163.33, 208.85) * mm});
            skLineSegment(sketch, "E25.0.6.222", {"start": v(428.72, 221.3) * mm, "end": v(428.72, 213) * mm});
            skLineSegment(sketch, "E25.0.6.223", {"start": v(51.26, 213) * mm, "end": v(51.26, 221.3) * mm});
            skLineSegment(sketch, "E25.0.6.224", {"start": v(386.13, 198.25) * mm, "end": v(386.13, 206.55) * mm});
            skLineSegment(sketch, "E25.0.6.225", {"start": v(44.07, 208.85) * mm, "end": v(51.26, 213) * mm});
            skLineSegment(sketch, "E25.0.6.226", {"start": v(462.8, 221.3) * mm, "end": v(469.99, 225.45) * mm});
            skLineSegment(sketch, "E25.0.6.227", {"start": v(214.44, 208.85) * mm, "end": v(207.25, 213) * mm});
            skLineSegment(sketch, "E25.0.6.228", {"start": v(205.91, 210.7) * mm, "end": v(213.1, 206.55) * mm});
            skLineSegment(sketch, "E25.0.6.229", {"start": v(366.43, 206.55) * mm, "end": v(366.43, 198.25) * mm});
            skLineSegment(sketch, "E25.0.6.230", {"start": v(130.58, 206.55) * mm, "end": v(137.77, 210.7) * mm});
            skLineSegment(sketch, "E25.0.6.231", {"start": v(224.28, 221.3) * mm, "end": v(224.28, 213) * mm});
            skLineSegment(sketch, "E25.0.6.232", {"start": v(384.8, 208.85) * mm, "end": v(392, 213) * mm});
            skLineSegment(sketch, "E25.0.6.233", {"start": v(275.4, 213) * mm, "end": v(282.58, 208.85) * mm});
            skLineSegment(sketch, "E25.0.6.234", {"start": v(19.84, 213) * mm, "end": v(27.03, 208.85) * mm});
            skLineSegment(sketch, "E25.0.6.235", {"start": v(180.36, 208.85) * mm, "end": v(187.55, 213) * mm});
            skLineSegment(sketch, "E25.0.6.236", {"start": v(410.35, 210.7) * mm, "end": v(417.54, 206.55) * mm});
            skLineSegment(sketch, "E25.0.6.237", {"start": v(255.7, 221.3) * mm, "end": v(248.5, 225.45) * mm});
            skLineSegment(sketch, "E25.0.6.238", {"start": v(53.92, 221.3) * mm, "end": v(61.1, 225.45) * mm});
            skLineSegment(sketch, "E25.0.6.239", {"start": v(162, 206.55) * mm, "end": v(162, 198.25) * mm});
            skLineSegment(sketch, "E25.0.6.240", {"start": v(51.26, 221.3) * mm, "end": v(44.07, 225.45) * mm});
            skLineSegment(sketch, "E25.0.6.241", {"start": v(427.4, 210.7) * mm, "end": v(434.59, 206.55) * mm});
            skLineSegment(sketch, "E25.0.6.242", {"start": v(460.14, 221.3) * mm, "end": v(452.95, 225.45) * mm});
            skLineSegment(sketch, "E25.0.6.243", {"start": v(272.74, 213) * mm, "end": v(265.55, 208.85) * mm});
            skLineSegment(sketch, "E25.0.6.244", {"start": v(181.7, 198.25) * mm, "end": v(181.7, 206.55) * mm});
            skLineSegment(sketch, "E25.0.6.245", {"start": v(335.02, 206.55) * mm, "end": v(342.21, 210.7) * mm});
            skLineSegment(sketch, "E25.0.6.246", {"start": v(221.63, 221.3) * mm, "end": v(221.63, 213) * mm});
            skLineSegment(sketch, "E25.0.6.247", {"start": v(68.3, 213) * mm, "end": v(61.1, 208.85) * mm});
            skLineSegment(sketch, "E25.0.6.248", {"start": v(130.58, 198.25) * mm, "end": v(130.58, 206.55) * mm});
            skLineSegment(sketch, "E25.0.6.249", {"start": v(477.18, 213) * mm, "end": v(469.99, 208.85) * mm});
            skLineSegment(sketch, "E25.0.6.250", {"start": v(469.99, 225.45) * mm, "end": v(477.18, 221.3) * mm});
            skLineSegment(sketch, "E25.0.6.251", {"start": v(360.58, 213) * mm, "end": v(360.58, 221.3) * mm});
            skLineSegment(sketch, "E25.0.6.252", {"start": v(122.06, 213) * mm, "end": v(129.25, 208.85) * mm});
            skLineSegment(sketch, "E25.0.6.253", {"start": v(95.18, 208.85) * mm, "end": v(102.37, 213) * mm});
            skLineSegment(sketch, "E25.0.6.254", {"start": v(137.77, 210.7) * mm, "end": v(144.96, 206.55) * mm});
            skLineSegment(sketch, "E25.0.6.255", {"start": v(469.99, 208.85) * mm, "end": v(462.8, 213) * mm});
            skLineSegment(sketch, "E25.0.6.256", {"start": v(417.54, 206.55) * mm, "end": v(417.54, 198.25) * mm});
            skLineSegment(sketch, "E25.0.6.257", {"start": v(120.74, 210.7) * mm, "end": v(127.93, 206.55) * mm});
            skLineSegment(sketch, "E25.0.6.258", {"start": v(477.18, 221.3) * mm, "end": v(477.18, 213) * mm});
            skLineSegment(sketch, "E25.0.6.259", {"start": v(420.2, 206.55) * mm, "end": v(427.4, 210.7) * mm});
            skLineSegment(sketch, "E25.0.6.260", {"start": v(275.4, 221.3) * mm, "end": v(275.4, 213) * mm});
            skLineSegment(sketch, "E25.0.6.261", {"start": v(255.7, 213) * mm, "end": v(255.7, 221.3) * mm});
            skLineSegment(sketch, "E25.0.6.262", {"start": v(215.77, 206.55) * mm, "end": v(222.96, 210.7) * mm});
            skLineSegment(sketch, "E25.0.6.263", {"start": v(42.74, 206.55) * mm, "end": v(42.74, 198.25) * mm});
            skLineSegment(sketch, "E25.0.6.264", {"start": v(350.73, 208.85) * mm, "end": v(357.92, 213) * mm});
            skLineSegment(sketch, "E25.0.6.265", {"start": v(78.14, 208.85) * mm, "end": v(85.33, 213) * mm});
            skLineSegment(sketch, "E25.0.6.266", {"start": v(119.4, 213) * mm, "end": v(112.22, 208.85) * mm});
            skLineSegment(sketch, "E25.0.6.267", {"start": v(19.84, 221.3) * mm, "end": v(19.84, 213) * mm});
            skLineSegment(sketch, "E25.0.6.268", {"start": v(496.87, 213) * mm, "end": v(504.06, 208.85) * mm});
            skLineSegment(sketch, "E25.0.6.269", {"start": v(325.18, 210.7) * mm, "end": v(332.37, 206.55) * mm});
            skLineSegment(sketch, "E25.0.6.270", {"start": v(367.77, 225.45) * mm, "end": v(374.96, 221.3) * mm});
            skLineSegment(sketch, "E25.0.6.271", {"start": v(258.36, 213) * mm, "end": v(258.36, 221.3) * mm});
            skLineSegment(sketch, "E25.0.6.272", {"start": v(163.33, 225.45) * mm, "end": v(170.52, 221.3) * mm});
            skLineSegment(sketch, "E25.0.6.273", {"start": v(179.04, 206.55) * mm, "end": v(179.04, 198.25) * mm});
            skLineSegment(sketch, "E25.0.6.274", {"start": v(249.84, 198.25) * mm, "end": v(249.84, 206.55) * mm});
            skLineSegment(sketch, "E25.0.6.275", {"start": v(139.1, 213) * mm, "end": v(146.29, 208.85) * mm});
            skLineSegment(sketch, "E25.0.6.276", {"start": v(418.88, 208.85) * mm, "end": v(411.7, 213) * mm});
            skLineSegment(sketch, "E25.0.6.277", {"start": v(426.07, 221.3) * mm, "end": v(426.07, 213) * mm});
            skLineSegment(sketch, "E25.0.6.278", {"start": v(367.77, 208.85) * mm, "end": v(360.58, 213) * mm});
            skLineSegment(sketch, "E25.0.6.279", {"start": v(352.06, 206.55) * mm, "end": v(359.24, 210.7) * mm});
            skLineSegment(sketch, "E25.0.6.280", {"start": v(163.33, 208.85) * mm, "end": v(156.14, 213) * mm});
            skLineSegment(sketch, "E25.0.6.281", {"start": v(112.22, 208.85) * mm, "end": v(105.03, 213) * mm});
            skLineSegment(sketch, "E25.0.6.282", {"start": v(487.02, 225.45) * mm, "end": v(479.83, 221.3) * mm});
            skLineSegment(sketch, "E25.0.6.283", {"start": v(374.96, 221.3) * mm, "end": v(374.96, 213) * mm});
            skLineSegment(sketch, "E25.0.6.284", {"start": v(17.19, 213) * mm, "end": v(10, 208.85) * mm});
            skLineSegment(sketch, "E25.0.6.285", {"start": v(221.63, 213) * mm, "end": v(214.44, 208.85) * mm});
            skLineSegment(sketch, "E25.0.6.286", {"start": v(282.58, 225.45) * mm, "end": v(275.4, 221.3) * mm});
            skLineSegment(sketch, "E25.0.6.287", {"start": v(335.02, 198.25) * mm, "end": v(335.02, 206.55) * mm});
            skLineSegment(sketch, "E25.0.6.288", {"start": v(170.52, 221.3) * mm, "end": v(170.52, 213) * mm});
            skLineSegment(sketch, "E25.0.6.289", {"start": v(291.1, 210.7) * mm, "end": v(298.29, 206.55) * mm});
            skLineSegment(sketch, "E25.0.6.290", {"start": v(173.17, 221.3) * mm, "end": v(173.17, 213) * mm});
            skLineSegment(sketch, "E25.0.6.291", {"start": v(495.54, 210.7) * mm, "end": v(502.73, 206.55) * mm});
            skLineSegment(sketch, "E25.0.6.292", {"start": v(147.62, 198.25) * mm, "end": v(147.62, 206.55) * mm});
            skLineSegment(sketch, "E25.0.6.293", {"start": v(153.48, 213) * mm, "end": v(153.48, 221.3) * mm});
            skLineSegment(sketch, "E25.0.6.294", {"start": v(222.96, 210.7) * mm, "end": v(230.15, 206.55) * mm});
            skLineSegment(sketch, "E25.0.6.295", {"start": v(479.83, 221.3) * mm, "end": v(479.83, 213) * mm});
            skLineSegment(sketch, "E25.0.6.296", {"start": v(420.2, 198.25) * mm, "end": v(420.2, 206.55) * mm});
            skLineSegment(sketch, "E25.0.6.297", {"start": v(326.5, 213) * mm, "end": v(333.7, 208.85) * mm});
            skLineSegment(sketch, "E25.0.6.298", {"start": v(173.17, 213) * mm, "end": v(180.36, 208.85) * mm});
            skLineSegment(sketch, "E25.0.6.299", {"start": v(342.21, 210.7) * mm, "end": v(349.4, 206.55) * mm});
            skLineSegment(sketch, "E25.0.6.300", {"start": v(265.55, 225.45) * mm, "end": v(272.74, 221.3) * mm});
            skLineSegment(sketch, "E25.0.6.301", {"start": v(274.07, 210.7) * mm, "end": v(281.26, 206.55) * mm});
            skLineSegment(sketch, "E25.0.6.302", {"start": v(215.77, 198.25) * mm, "end": v(215.77, 206.55) * mm});
            skLineSegment(sketch, "E25.0.6.303", {"start": v(462.8, 213) * mm, "end": v(462.8, 221.3) * mm});
            skLineSegment(sketch, "E25.0.6.304", {"start": v(281.26, 206.55) * mm, "end": v(281.26, 198.25) * mm});
            skLineSegment(sketch, "E25.0.6.305", {"start": v(156.14, 213) * mm, "end": v(156.14, 221.3) * mm});
            skLineSegment(sketch, "E25.0.6.306", {"start": v(213.1, 206.55) * mm, "end": v(213.1, 198.25) * mm});
            skLineSegment(sketch, "E25.0.6.307", {"start": v(96.5, 206.55) * mm, "end": v(103.7, 210.7) * mm});
            skLineSegment(sketch, "E25.0.6.308", {"start": v(460.14, 213) * mm, "end": v(460.14, 221.3) * mm});
            skLineSegment(sketch, "E25.0.6.309", {"start": v(323.85, 213) * mm, "end": v(316.66, 208.85) * mm});
            skLineSegment(sketch, "E25.0.6.310", {"start": v(272.74, 221.3) * mm, "end": v(272.74, 213) * mm});
            skLineSegment(sketch, "E25.0.6.311", {"start": v(377.61, 213) * mm, "end": v(384.8, 208.85) * mm});
            skLineSegment(sketch, "E25.0.6.312", {"start": v(282.58, 208.85) * mm, "end": v(289.77, 213) * mm});
            skLineSegment(sketch, "E25.0.6.313", {"start": v(146.29, 208.85) * mm, "end": v(153.48, 213) * mm});
            skLineSegment(sketch, "E25.0.6.314", {"start": v(343.54, 213) * mm, "end": v(350.73, 208.85) * mm});
            skLineSegment(sketch, "E25.0.6.315", {"start": v(376.29, 210.7) * mm, "end": v(383.48, 206.55) * mm});
            skLineSegment(sketch, "E25.0.6.316", {"start": v(171.85, 210.7) * mm, "end": v(179.04, 206.55) * mm});
            skLineSegment(sketch, "E25.0.6.317", {"start": v(53.92, 213) * mm, "end": v(53.92, 221.3) * mm});
            skLineSegment(sketch, "E25.0.6.318", {"start": v(292.43, 213) * mm, "end": v(299.62, 208.85) * mm});
            skLineSegment(sketch, "E25.0.6.319", {"start": v(377.61, 221.3) * mm, "end": v(377.61, 213) * mm});
            skLineSegment(sketch, "E25.0.6.320", {"start": v(383.48, 206.55) * mm, "end": v(383.48, 198.25) * mm});
            skLineSegment(sketch, "E25.0.6.321", {"start": v(129.25, 208.85) * mm, "end": v(136.44, 213) * mm});
            skLineSegment(sketch, "E25.0.6.322", {"start": v(428.72, 213) * mm, "end": v(435.91, 208.85) * mm});
            skLineSegment(sketch, "E25.0.6.323", {"start": v(496.87, 221.3) * mm, "end": v(496.87, 213) * mm});
            skLineSegment(sketch, "E25.0.6.324", {"start": v(224.28, 213) * mm, "end": v(231.47, 208.85) * mm});
            skLineSegment(sketch, "E25.0.6.325", {"start": v(333.7, 208.85) * mm, "end": v(340.88, 213) * mm});
            skLineSegment(sketch, "E25.0.6.326", {"start": v(11.33, 206.55) * mm, "end": v(18.52, 210.7) * mm});
            skLineSegment(sketch, "E25.0.6.327", {"start": v(18.52, 210.7) * mm, "end": v(25.7, 206.55) * mm});
            skLineSegment(sketch, "E25.0.6.328", {"start": v(494.21, 213) * mm, "end": v(494.21, 221.3) * mm});
            skLineSegment(sketch, "E25.0.6.329", {"start": v(315.32, 206.55) * mm, "end": v(315.32, 198.25) * mm});
            skLineSegment(sketch, "E25.0.6.330", {"start": v(360.58, 221.3) * mm, "end": v(367.77, 225.45) * mm});
            skLineSegment(sketch, "E25.0.6.331", {"start": v(316.66, 208.85) * mm, "end": v(309.47, 213) * mm});
            skLineSegment(sketch, "E25.0.6.332", {"start": v(308.13, 210.7) * mm, "end": v(315.32, 206.55) * mm});
            skLineSegment(sketch, "E25.0.6.333", {"start": v(147.62, 206.55) * mm, "end": v(154.8, 210.7) * mm});
            skLineSegment(sketch, "E25.0.6.334", {"start": v(359.24, 210.7) * mm, "end": v(366.43, 206.55) * mm});
            skLineSegment(sketch, "E25.0.6.335", {"start": v(110.88, 206.55) * mm, "end": v(110.88, 198.25) * mm});
            skLineSegment(sketch, "E25.0.6.336", {"start": v(154.8, 210.7) * mm, "end": v(162, 206.55) * mm});
            skLineSegment(sketch, "E25.0.6.337", {"start": v(17.19, 221.3) * mm, "end": v(17.19, 213) * mm});
            skLineSegment(sketch, "E25.0.6.338", {"start": v(156.14, 221.3) * mm, "end": v(163.33, 225.45) * mm});
            skLineSegment(sketch, "E25.0.6.339", {"start": v(103.7, 210.7) * mm, "end": v(110.88, 206.55) * mm});
            skLineSegment(sketch, "E25.0.6.340", {"start": v(471.32, 206.55) * mm, "end": v(478.5, 210.7) * mm});
            skLineSegment(sketch, "E25.0.6.341", {"start": v(426.07, 213) * mm, "end": v(418.88, 208.85) * mm});
            skLineSegment(sketch, "E25.0.6.342", {"start": v(357.92, 213) * mm, "end": v(357.92, 221.3) * mm});
            skLineSegment(sketch, "E25.0.6.343", {"start": v(317.99, 206.55) * mm, "end": v(325.18, 210.7) * mm});
            skLineSegment(sketch, "E25.0.6.344", {"start": v(258.36, 221.3) * mm, "end": v(265.55, 225.45) * mm});
            skLineSegment(sketch, "E25.0.6.345", {"start": v(283.91, 198.25) * mm, "end": v(283.91, 206.55) * mm});
            skLineSegment(sketch, "E25.0.6.346", {"start": v(283.91, 206.55) * mm, "end": v(291.1, 210.7) * mm});
            skLineSegment(sketch, "E25.0.6.347", {"start": v(113.55, 206.55) * mm, "end": v(120.74, 210.7) * mm});
            skLineSegment(sketch, "E25.0.6.348", {"start": v(36.88, 213) * mm, "end": v(44.07, 208.85) * mm});
            skLineSegment(sketch, "E25.0.6.349", {"start": v(36.88, 221.3) * mm, "end": v(36.88, 213) * mm});
            skLineSegment(sketch, "E25.0.6.350", {"start": v(34.22, 213) * mm, "end": v(34.22, 221.3) * mm});
            skLineSegment(sketch, "E25.0.6.351", {"start": v(485.7, 206.55) * mm, "end": v(485.7, 198.25) * mm});
            skLineSegment(sketch, "E25.0.6.352", {"start": v(478.5, 210.7) * mm, "end": v(485.7, 206.55) * mm});
            skLineSegment(sketch, "E25.0.6.353", {"start": v(487.02, 208.85) * mm, "end": v(494.21, 213) * mm});
            skLineSegment(sketch, "E25.0.6.354", {"start": v(27.03, 208.85) * mm, "end": v(34.22, 213) * mm});
            skLineSegment(sketch, "E25.0.6.355", {"start": v(479.83, 213) * mm, "end": v(487.02, 208.85) * mm});
            skLineSegment(sketch, "E25.0.6.356", {"start": v(28.36, 206.55) * mm, "end": v(35.55, 210.7) * mm});
            skLineSegment(sketch, "E25.0.6.357", {"start": v(35.55, 210.7) * mm, "end": v(42.74, 206.55) * mm});
            skLineSegment(sketch, "E25.0.6.358", {"start": v(488.35, 206.55) * mm, "end": v(495.54, 210.7) * mm});
            skLineSegment(sketch, "E25.0.6.359", {"start": v(488.35, 198.25) * mm, "end": v(488.35, 206.55) * mm});
            skLineSegment(sketch, "E25.0.7.0", {"start": v(332.37, 168.75) * mm, "end": v(325.18, 164.6) * mm});
            skLineSegment(sketch, "E25.0.7.1", {"start": v(511.25, 191.8) * mm, "end": v(504.06, 195.95) * mm});
            skLineSegment(sketch, "E25.0.7.2", {"start": v(2.81, 191.8) * mm, "end": v(10, 195.95) * mm});
            skLineSegment(sketch, "E25.0.7.3", {"start": v(127.93, 168.75) * mm, "end": v(120.74, 164.6) * mm});
            skLineSegment(sketch, "E25.0.7.4", {"start": v(512.57, 164.6) * mm, "end": v(505.39, 168.75) * mm});
            skLineSegment(sketch, "E25.0.7.5", {"start": v(519.76, 168.75) * mm, "end": v(512.57, 164.6) * mm});
            skLineSegment(sketch, "E25.0.7.6", {"start": v(25.7, 168.75) * mm, "end": v(18.52, 164.6) * mm});
            skLineSegment(sketch, "E25.0.7.7", {"start": v(11.33, 168.75) * mm, "end": v(11.33, 177.05) * mm});
            skLineSegment(sketch, "E25.0.7.8", {"start": v(18.52, 164.6) * mm, "end": v(11.33, 168.75) * mm});
            skLineSegment(sketch, "E25.0.7.9", {"start": v(519.76, 177.05) * mm, "end": v(519.76, 168.75) * mm});
            skLineSegment(sketch, "E25.0.7.10", {"start": v(76.82, 168.75) * mm, "end": v(69.63, 164.6) * mm});
            skLineSegment(sketch, "E25.0.7.11", {"start": v(112.22, 195.95) * mm, "end": v(119.4, 191.8) * mm});
            skLineSegment(sketch, "E25.0.7.12", {"start": v(205.91, 164.6) * mm, "end": v(198.73, 168.75) * mm});
            skLineSegment(sketch, "E25.0.7.13", {"start": v(197.4, 195.95) * mm, "end": v(190.2, 191.8) * mm});
            skLineSegment(sketch, "E25.0.7.14", {"start": v(93.85, 168.75) * mm, "end": v(86.66, 164.6) * mm});
            skLineSegment(sketch, "E25.0.7.15", {"start": v(129.25, 195.95) * mm, "end": v(122.06, 191.8) * mm});
            skLineSegment(sketch, "E25.0.7.16", {"start": v(298.29, 168.75) * mm, "end": v(291.1, 164.6) * mm});
            skLineSegment(sketch, "E25.0.7.17", {"start": v(502.73, 168.75) * mm, "end": v(495.54, 164.6) * mm});
            skLineSegment(sketch, "E25.0.7.18", {"start": v(289.77, 191.8) * mm, "end": v(282.58, 195.95) * mm});
            skLineSegment(sketch, "E25.0.7.19", {"start": v(85.33, 191.8) * mm, "end": v(78.14, 195.95) * mm});
            skLineSegment(sketch, "E25.0.7.20", {"start": v(494.21, 191.8) * mm, "end": v(487.02, 195.95) * mm});
            skLineSegment(sketch, "E25.0.7.21", {"start": v(333.7, 195.95) * mm, "end": v(326.5, 191.8) * mm});
            skLineSegment(sketch, "E25.0.7.22", {"start": v(95.18, 195.95) * mm, "end": v(87.99, 191.8) * mm});
            skLineSegment(sketch, "E25.0.7.23", {"start": v(478.5, 164.6) * mm, "end": v(471.32, 168.75) * mm});
            skLineSegment(sketch, "E25.0.7.24", {"start": v(274.07, 164.6) * mm, "end": v(266.88, 168.75) * mm});
            skLineSegment(sketch, "E25.0.7.25", {"start": v(444.43, 164.6) * mm, "end": v(437.24, 168.75) * mm});
            skLineSegment(sketch, "E25.0.7.26", {"start": v(401.84, 195.95) * mm, "end": v(394.65, 191.8) * mm});
            skLineSegment(sketch, "E25.0.7.27", {"start": v(410.35, 164.6) * mm, "end": v(403.17, 168.75) * mm});
            skLineSegment(sketch, "E25.0.7.28", {"start": v(468.65, 168.75) * mm, "end": v(461.46, 164.6) * mm});
            skLineSegment(sketch, "E25.0.7.29", {"start": v(427.4, 164.6) * mm, "end": v(420.2, 168.75) * mm});
            skLineSegment(sketch, "E25.0.7.30", {"start": v(59.77, 168.75) * mm, "end": v(52.58, 164.6) * mm});
            skLineSegment(sketch, "E25.0.7.31", {"start": v(512.57, 181.2) * mm, "end": v(519.76, 177.05) * mm});
            skLineSegment(sketch, "E25.0.7.32", {"start": v(196.07, 168.75) * mm, "end": v(188.88, 164.6) * mm});
            skLineSegment(sketch, "E25.0.7.33", {"start": v(86.66, 164.6) * mm, "end": v(79.47, 168.75) * mm});
            skLineSegment(sketch, "E25.0.7.34", {"start": v(400.5, 168.75) * mm, "end": v(393.32, 164.6) * mm});
            skLineSegment(sketch, "E25.0.7.35", {"start": v(103.7, 164.6) * mm, "end": v(96.5, 168.75) * mm});
            skLineSegment(sketch, "E25.0.7.36", {"start": v(299.62, 195.95) * mm, "end": v(292.43, 191.8) * mm});
            skLineSegment(sketch, "E25.0.7.37", {"start": v(504.06, 195.95) * mm, "end": v(496.87, 191.8) * mm});
            skLineSegment(sketch, "E25.0.7.38", {"start": v(2.81, 183.5) * mm, "end": v(2.81, 191.8) * mm});
            skLineSegment(sketch, "E25.0.7.39", {"start": v(308.13, 164.6) * mm, "end": v(300.95, 168.75) * mm});
            skLineSegment(sketch, "E25.0.7.40", {"start": v(417.54, 168.75) * mm, "end": v(410.35, 164.6) * mm});
            skLineSegment(sketch, "E25.0.7.41", {"start": v(434.59, 168.75) * mm, "end": v(427.4, 164.6) * mm});
            skLineSegment(sketch, "E25.0.7.42", {"start": v(62.44, 168.75) * mm, "end": v(62.44, 177.05) * mm});
            skLineSegment(sketch, "E25.0.7.43", {"start": v(69.63, 164.6) * mm, "end": v(62.44, 168.75) * mm});
            skLineSegment(sketch, "E25.0.7.44", {"start": v(325.18, 164.6) * mm, "end": v(317.99, 168.75) * mm});
            skLineSegment(sketch, "E25.0.7.45", {"start": v(264.21, 168.75) * mm, "end": v(257.02, 164.6) * mm});
            skLineSegment(sketch, "E25.0.7.46", {"start": v(120.74, 164.6) * mm, "end": v(113.55, 168.75) * mm});
            skLineSegment(sketch, "E25.0.7.47", {"start": v(502.73, 177.05) * mm, "end": v(502.73, 168.75) * mm});
            skLineSegment(sketch, "E25.0.7.48", {"start": v(316.66, 195.95) * mm, "end": v(323.85, 191.8) * mm});
            skLineSegment(sketch, "E25.0.7.49", {"start": v(505.39, 168.75) * mm, "end": v(505.39, 177.05) * mm});
            skLineSegment(sketch, "E25.0.7.50", {"start": v(10, 179.35) * mm, "end": v(2.81, 183.5) * mm});
            skLineSegment(sketch, "E25.0.7.51", {"start": v(59.77, 177.05) * mm, "end": v(59.77, 168.75) * mm});
            skLineSegment(sketch, "E25.0.7.52", {"start": v(291.1, 164.6) * mm, "end": v(283.91, 168.75) * mm});
            skLineSegment(sketch, "E25.0.7.53", {"start": v(511.25, 183.5) * mm, "end": v(511.25, 191.8) * mm});
            skLineSegment(sketch, "E25.0.7.54", {"start": v(392, 191.8) * mm, "end": v(384.8, 195.95) * mm});
            skLineSegment(sketch, "E25.0.7.55", {"start": v(187.55, 191.8) * mm, "end": v(180.36, 195.95) * mm});
            skLineSegment(sketch, "E25.0.7.56", {"start": v(247.18, 177.05) * mm, "end": v(247.18, 168.75) * mm});
            skLineSegment(sketch, "E25.0.7.57", {"start": v(188.88, 181.2) * mm, "end": v(196.07, 177.05) * mm});
            skLineSegment(sketch, "E25.0.7.58", {"start": v(369.1, 177.05) * mm, "end": v(376.29, 181.2) * mm});
            skLineSegment(sketch, "E25.0.7.59", {"start": v(409.03, 183.5) * mm, "end": v(409.03, 191.8) * mm});
            skLineSegment(sketch, "E25.0.7.60", {"start": v(188.88, 164.6) * mm, "end": v(181.7, 168.75) * mm});
            skLineSegment(sketch, "E25.0.7.61", {"start": v(204.59, 183.5) * mm, "end": v(204.59, 191.8) * mm});
            skLineSegment(sketch, "E25.0.7.62", {"start": v(164.66, 177.05) * mm, "end": v(171.85, 181.2) * mm});
            skLineSegment(sketch, "E25.0.7.63", {"start": v(230.15, 177.05) * mm, "end": v(230.15, 168.75) * mm});
            skLineSegment(sketch, "E25.0.7.64", {"start": v(343.54, 191.8) * mm, "end": v(343.54, 183.5) * mm});
            skLineSegment(sketch, "E25.0.7.65", {"start": v(139.1, 191.8) * mm, "end": v(139.1, 183.5) * mm});
            skLineSegment(sketch, "E25.0.7.66", {"start": v(70.95, 183.5) * mm, "end": v(78.14, 179.35) * mm});
            skLineSegment(sketch, "E25.0.7.67", {"start": v(96.5, 168.75) * mm, "end": v(96.5, 177.05) * mm});
            skLineSegment(sketch, "E25.0.7.68", {"start": v(44.07, 195.95) * mm, "end": v(36.88, 191.8) * mm});
            skLineSegment(sketch, "E25.0.7.69", {"start": v(162, 168.75) * mm, "end": v(154.8, 164.6) * mm});
            skLineSegment(sketch, "E25.0.7.70", {"start": v(300.95, 168.75) * mm, "end": v(300.95, 177.05) * mm});
            skLineSegment(sketch, "E25.0.7.71", {"start": v(222.96, 164.6) * mm, "end": v(215.77, 168.75) * mm});
            skLineSegment(sketch, "E25.0.7.72", {"start": v(452.95, 179.35) * mm, "end": v(460.14, 183.5) * mm});
            skLineSegment(sketch, "E25.0.7.73", {"start": v(369.1, 168.75) * mm, "end": v(369.1, 177.05) * mm});
            skLineSegment(sketch, "E25.0.7.74", {"start": v(366.43, 168.75) * mm, "end": v(359.24, 164.6) * mm});
            skLineSegment(sketch, "E25.0.7.75", {"start": v(164.66, 168.75) * mm, "end": v(164.66, 177.05) * mm});
            skLineSegment(sketch, "E25.0.7.76", {"start": v(248.5, 179.35) * mm, "end": v(255.7, 183.5) * mm});
            skLineSegment(sketch, "E25.0.7.77", {"start": v(249.84, 177.05) * mm, "end": v(257.02, 181.2) * mm});
            skLineSegment(sketch, "E25.0.7.78", {"start": v(393.32, 164.6) * mm, "end": v(386.13, 168.75) * mm});
            skLineSegment(sketch, "E25.0.7.79", {"start": v(62.44, 177.05) * mm, "end": v(69.63, 181.2) * mm});
            skLineSegment(sketch, "E25.0.7.80", {"start": v(136.44, 183.5) * mm, "end": v(136.44, 191.8) * mm});
            skLineSegment(sketch, "E25.0.7.81", {"start": v(102.37, 183.5) * mm, "end": v(102.37, 191.8) * mm});
            skLineSegment(sketch, "E25.0.7.82", {"start": v(418.88, 195.95) * mm, "end": v(426.07, 191.8) * mm});
            skLineSegment(sketch, "E25.0.7.83", {"start": v(454.28, 177.05) * mm, "end": v(461.46, 181.2) * mm});
            skLineSegment(sketch, "E25.0.7.84", {"start": v(78.14, 195.95) * mm, "end": v(70.95, 191.8) * mm});
            skLineSegment(sketch, "E25.0.7.85", {"start": v(105.03, 183.5) * mm, "end": v(105.03, 191.8) * mm});
            skLineSegment(sketch, "E25.0.7.86", {"start": v(190.2, 183.5) * mm, "end": v(197.4, 179.35) * mm});
            skLineSegment(sketch, "E25.0.7.87", {"start": v(352.06, 168.75) * mm, "end": v(352.06, 177.05) * mm});
            skLineSegment(sketch, "E25.0.7.88", {"start": v(400.5, 177.05) * mm, "end": v(400.5, 168.75) * mm});
            skLineSegment(sketch, "E25.0.7.89", {"start": v(299.62, 179.35) * mm, "end": v(306.8, 183.5) * mm});
            skLineSegment(sketch, "E25.0.7.90", {"start": v(190.2, 191.8) * mm, "end": v(190.2, 183.5) * mm});
            skLineSegment(sketch, "E25.0.7.91", {"start": v(76.82, 177.05) * mm, "end": v(76.82, 168.75) * mm});
            skLineSegment(sketch, "E25.0.7.92", {"start": v(392, 183.5) * mm, "end": v(392, 191.8) * mm});
            skLineSegment(sketch, "E25.0.7.93", {"start": v(309.47, 191.8) * mm, "end": v(316.66, 195.95) * mm});
            skLineSegment(sketch, "E25.0.7.94", {"start": v(349.4, 168.75) * mm, "end": v(342.21, 164.6) * mm});
            skLineSegment(sketch, "E25.0.7.95", {"start": v(257.02, 181.2) * mm, "end": v(264.21, 177.05) * mm});
            skLineSegment(sketch, "E25.0.7.96", {"start": v(61.1, 195.95) * mm, "end": v(68.3, 191.8) * mm});
            skLineSegment(sketch, "E25.0.7.97", {"start": v(146.29, 195.95) * mm, "end": v(139.1, 191.8) * mm});
            skLineSegment(sketch, "E25.0.7.98", {"start": v(154.8, 164.6) * mm, "end": v(147.62, 168.75) * mm});
            skLineSegment(sketch, "E25.0.7.99", {"start": v(306.8, 191.8) * mm, "end": v(299.62, 195.95) * mm});
            skLineSegment(sketch, "E25.0.7.100", {"start": v(87.99, 183.5) * mm, "end": v(95.18, 179.35) * mm});
            skLineSegment(sketch, "E25.0.7.101", {"start": v(105.03, 191.8) * mm, "end": v(112.22, 195.95) * mm});
            skLineSegment(sketch, "E25.0.7.102", {"start": v(102.37, 191.8) * mm, "end": v(95.18, 195.95) * mm});
            skLineSegment(sketch, "E25.0.7.103", {"start": v(187.55, 183.5) * mm, "end": v(187.55, 191.8) * mm});
            skLineSegment(sketch, "E25.0.7.104", {"start": v(61.1, 179.35) * mm, "end": v(53.92, 183.5) * mm});
            skLineSegment(sketch, "E25.0.7.105", {"start": v(437.24, 168.75) * mm, "end": v(437.24, 177.05) * mm});
            skLineSegment(sketch, "E25.0.7.106", {"start": v(393.32, 181.2) * mm, "end": v(400.5, 177.05) * mm});
            skLineSegment(sketch, "E25.0.7.107", {"start": v(232.8, 168.75) * mm, "end": v(232.8, 177.05) * mm});
            skLineSegment(sketch, "E25.0.7.108", {"start": v(87.99, 191.8) * mm, "end": v(87.99, 183.5) * mm});
            skLineSegment(sketch, "E25.0.7.109", {"start": v(113.55, 168.75) * mm, "end": v(113.55, 177.05) * mm});
            skLineSegment(sketch, "E25.0.7.110", {"start": v(332.37, 177.05) * mm, "end": v(332.37, 168.75) * mm});
            skLineSegment(sketch, "E25.0.7.111", {"start": v(266.88, 168.75) * mm, "end": v(266.88, 177.05) * mm});
            skLineSegment(sketch, "E25.0.7.112", {"start": v(180.36, 195.95) * mm, "end": v(173.17, 191.8) * mm});
            skLineSegment(sketch, "E25.0.7.113", {"start": v(181.7, 177.05) * mm, "end": v(188.88, 181.2) * mm});
            skLineSegment(sketch, "E25.0.7.114", {"start": v(68.3, 191.8) * mm, "end": v(68.3, 183.5) * mm});
            skLineSegment(sketch, "E25.0.7.115", {"start": v(317.99, 168.75) * mm, "end": v(317.99, 177.05) * mm});
            skLineSegment(sketch, "E25.0.7.116", {"start": v(485.7, 168.75) * mm, "end": v(478.5, 164.6) * mm});
            skLineSegment(sketch, "E25.0.7.117", {"start": v(10, 195.95) * mm, "end": v(17.19, 191.8) * mm});
            skLineSegment(sketch, "E25.0.7.118", {"start": v(376.29, 164.6) * mm, "end": v(369.1, 168.75) * mm});
            skLineSegment(sketch, "E25.0.7.119", {"start": v(452.95, 195.95) * mm, "end": v(445.76, 191.8) * mm});
            skLineSegment(sketch, "E25.0.7.120", {"start": v(315.32, 168.75) * mm, "end": v(308.13, 164.6) * mm});
            skLineSegment(sketch, "E25.0.7.121", {"start": v(93.85, 177.05) * mm, "end": v(93.85, 168.75) * mm});
            skLineSegment(sketch, "E25.0.7.122", {"start": v(35.55, 164.6) * mm, "end": v(28.36, 168.75) * mm});
            skLineSegment(sketch, "E25.0.7.123", {"start": v(45.4, 168.75) * mm, "end": v(45.4, 177.05) * mm});
            skLineSegment(sketch, "E25.0.7.124", {"start": v(42.74, 168.75) * mm, "end": v(35.55, 164.6) * mm});
            skLineSegment(sketch, "E25.0.7.125", {"start": v(434.59, 177.05) * mm, "end": v(434.59, 168.75) * mm});
            skLineSegment(sketch, "E25.0.7.126", {"start": v(340.88, 183.5) * mm, "end": v(340.88, 191.8) * mm});
            skLineSegment(sketch, "E25.0.7.127", {"start": v(394.65, 183.5) * mm, "end": v(401.84, 179.35) * mm});
            skLineSegment(sketch, "E25.0.7.128", {"start": v(153.48, 191.8) * mm, "end": v(146.29, 195.95) * mm});
            skLineSegment(sketch, "E25.0.7.129", {"start": v(52.58, 164.6) * mm, "end": v(45.4, 168.75) * mm});
            skLineSegment(sketch, "E25.0.7.130", {"start": v(25.7, 177.05) * mm, "end": v(25.7, 168.75) * mm});
            skLineSegment(sketch, "E25.0.7.131", {"start": v(28.36, 168.75) * mm, "end": v(28.36, 177.05) * mm});
            skLineSegment(sketch, "E25.0.7.132", {"start": v(45.4, 177.05) * mm, "end": v(52.58, 181.2) * mm});
            skLineSegment(sketch, "E25.0.7.133", {"start": v(451.62, 168.75) * mm, "end": v(444.43, 164.6) * mm});
            skLineSegment(sketch, "E25.0.7.134", {"start": v(411.7, 183.5) * mm, "end": v(411.7, 191.8) * mm});
            skLineSegment(sketch, "E25.0.7.135", {"start": v(342.21, 164.6) * mm, "end": v(335.02, 168.75) * mm});
            skLineSegment(sketch, "E25.0.7.136", {"start": v(443.1, 183.5) * mm, "end": v(443.1, 191.8) * mm});
            skLineSegment(sketch, "E25.0.7.137", {"start": v(357.92, 191.8) * mm, "end": v(350.73, 195.95) * mm});
            skLineSegment(sketch, "E25.0.7.138", {"start": v(289.77, 183.5) * mm, "end": v(289.77, 191.8) * mm});
            skLineSegment(sketch, "E25.0.7.139", {"start": v(204.59, 191.8) * mm, "end": v(197.4, 195.95) * mm});
            skLineSegment(sketch, "E25.0.7.140", {"start": v(198.73, 177.05) * mm, "end": v(205.91, 181.2) * mm});
            skLineSegment(sketch, "E25.0.7.141", {"start": v(454.28, 168.75) * mm, "end": v(454.28, 177.05) * mm});
            skLineSegment(sketch, "E25.0.7.142", {"start": v(86.66, 181.2) * mm, "end": v(93.85, 177.05) * mm});
            skLineSegment(sketch, "E25.0.7.143", {"start": v(443.1, 191.8) * mm, "end": v(435.91, 195.95) * mm});
            skLineSegment(sketch, "E25.0.7.144", {"start": v(435.91, 195.95) * mm, "end": v(428.72, 191.8) * mm});
            skLineSegment(sketch, "E25.0.7.145", {"start": v(437.24, 177.05) * mm, "end": v(444.43, 181.2) * mm});
            skLineSegment(sketch, "E25.0.7.146", {"start": v(231.47, 195.95) * mm, "end": v(224.28, 191.8) * mm});
            skLineSegment(sketch, "E25.0.7.147", {"start": v(79.47, 168.75) * mm, "end": v(79.47, 177.05) * mm});
            skLineSegment(sketch, "E25.0.7.148", {"start": v(309.47, 183.5) * mm, "end": v(309.47, 191.8) * mm});
            skLineSegment(sketch, "E25.0.7.149", {"start": v(214.44, 195.95) * mm, "end": v(221.63, 191.8) * mm});
            skLineSegment(sketch, "E25.0.7.150", {"start": v(238.66, 191.8) * mm, "end": v(231.47, 195.95) * mm});
            skLineSegment(sketch, "E25.0.7.151", {"start": v(394.65, 191.8) * mm, "end": v(394.65, 183.5) * mm});
            skLineSegment(sketch, "E25.0.7.152", {"start": v(445.76, 183.5) * mm, "end": v(452.95, 179.35) * mm});
            skLineSegment(sketch, "E25.0.7.153", {"start": v(241.32, 183.5) * mm, "end": v(248.5, 179.35) * mm});
            skLineSegment(sketch, "E25.0.7.154", {"start": v(231.47, 179.35) * mm, "end": v(238.66, 183.5) * mm});
            skLineSegment(sketch, "E25.0.7.155", {"start": v(79.47, 177.05) * mm, "end": v(86.66, 181.2) * mm});
            skLineSegment(sketch, "E25.0.7.156", {"start": v(350.73, 195.95) * mm, "end": v(343.54, 191.8) * mm});
            skLineSegment(sketch, "E25.0.7.157", {"start": v(196.07, 177.05) * mm, "end": v(196.07, 168.75) * mm});
            skLineSegment(sketch, "E25.0.7.158", {"start": v(240, 164.6) * mm, "end": v(232.8, 168.75) * mm});
            skLineSegment(sketch, "E25.0.7.159", {"start": v(69.63, 181.2) * mm, "end": v(76.82, 177.05) * mm});
            skLineSegment(sketch, "E25.0.7.160", {"start": v(349.4, 177.05) * mm, "end": v(349.4, 168.75) * mm});
            skLineSegment(sketch, "E25.0.7.161", {"start": v(383.48, 168.75) * mm, "end": v(376.29, 164.6) * mm});
            skLineSegment(sketch, "E25.0.7.162", {"start": v(144.96, 177.05) * mm, "end": v(144.96, 168.75) * mm});
            skLineSegment(sketch, "E25.0.7.163", {"start": v(179.04, 168.75) * mm, "end": v(171.85, 164.6) * mm});
            skLineSegment(sketch, "E25.0.7.164", {"start": v(386.13, 177.05) * mm, "end": v(393.32, 181.2) * mm});
            skLineSegment(sketch, "E25.0.7.165", {"start": v(435.91, 179.35) * mm, "end": v(443.1, 183.5) * mm});
            skLineSegment(sketch, "E25.0.7.166", {"start": v(504.06, 179.35) * mm, "end": v(511.25, 183.5) * mm});
            skLineSegment(sketch, "E25.0.7.167", {"start": v(403.17, 168.75) * mm, "end": v(403.17, 177.05) * mm});
            skLineSegment(sketch, "E25.0.7.168", {"start": v(241.32, 191.8) * mm, "end": v(241.32, 183.5) * mm});
            skLineSegment(sketch, "E25.0.7.169", {"start": v(359.24, 164.6) * mm, "end": v(352.06, 168.75) * mm});
            skLineSegment(sketch, "E25.0.7.170", {"start": v(213.1, 168.75) * mm, "end": v(205.91, 164.6) * mm});
            skLineSegment(sketch, "E25.0.7.171", {"start": v(34.22, 191.8) * mm, "end": v(27.03, 195.95) * mm});
            skLineSegment(sketch, "E25.0.7.172", {"start": v(461.46, 181.2) * mm, "end": v(468.65, 177.05) * mm});
            skLineSegment(sketch, "E25.0.7.173", {"start": v(505.39, 177.05) * mm, "end": v(512.57, 181.2) * mm});
            skLineSegment(sketch, "E25.0.7.174", {"start": v(300.95, 177.05) * mm, "end": v(308.13, 181.2) * mm});
            skLineSegment(sketch, "E25.0.7.175", {"start": v(230.15, 168.75) * mm, "end": v(222.96, 164.6) * mm});
            skLineSegment(sketch, "E25.0.7.176", {"start": v(265.55, 179.35) * mm, "end": v(258.36, 183.5) * mm});
            skLineSegment(sketch, "E25.0.7.177", {"start": v(144.96, 168.75) * mm, "end": v(137.77, 164.6) * mm});
            skLineSegment(sketch, "E25.0.7.178", {"start": v(27.03, 195.95) * mm, "end": v(19.84, 191.8) * mm});
            skLineSegment(sketch, "E25.0.7.179", {"start": v(384.8, 195.95) * mm, "end": v(377.61, 191.8) * mm});
            skLineSegment(sketch, "E25.0.7.180", {"start": v(340.88, 191.8) * mm, "end": v(333.7, 195.95) * mm});
            skLineSegment(sketch, "E25.0.7.181", {"start": v(136.44, 191.8) * mm, "end": v(129.25, 195.95) * mm});
            skLineSegment(sketch, "E25.0.7.182", {"start": v(198.73, 168.75) * mm, "end": v(198.73, 177.05) * mm});
            skLineSegment(sketch, "E25.0.7.183", {"start": v(70.95, 191.8) * mm, "end": v(70.95, 183.5) * mm});
            skLineSegment(sketch, "E25.0.7.184", {"start": v(127.93, 177.05) * mm, "end": v(127.93, 168.75) * mm});
            skLineSegment(sketch, "E25.0.7.185", {"start": v(461.46, 164.6) * mm, "end": v(454.28, 168.75) * mm});
            skLineSegment(sketch, "E25.0.7.186", {"start": v(444.43, 181.2) * mm, "end": v(451.62, 177.05) * mm});
            skLineSegment(sketch, "E25.0.7.187", {"start": v(445.76, 191.8) * mm, "end": v(445.76, 183.5) * mm});
            skLineSegment(sketch, "E25.0.7.188", {"start": v(240, 181.2) * mm, "end": v(247.18, 177.05) * mm});
            skLineSegment(sketch, "E25.0.7.189", {"start": v(298.29, 177.05) * mm, "end": v(298.29, 168.75) * mm});
            skLineSegment(sketch, "E25.0.7.190", {"start": v(471.32, 168.75) * mm, "end": v(471.32, 177.05) * mm});
            skLineSegment(sketch, "E25.0.7.191", {"start": v(207.25, 183.5) * mm, "end": v(207.25, 191.8) * mm});
            skLineSegment(sketch, "E25.0.7.192", {"start": v(281.26, 168.75) * mm, "end": v(274.07, 164.6) * mm});
            skLineSegment(sketch, "E25.0.7.193", {"start": v(257.02, 164.6) * mm, "end": v(249.84, 168.75) * mm});
            skLineSegment(sketch, "E25.0.7.194", {"start": v(248.5, 195.95) * mm, "end": v(241.32, 191.8) * mm});
            skLineSegment(sketch, "E25.0.7.195", {"start": v(451.62, 177.05) * mm, "end": v(451.62, 168.75) * mm});
            skLineSegment(sketch, "E25.0.7.196", {"start": v(110.88, 168.75) * mm, "end": v(103.7, 164.6) * mm});
            skLineSegment(sketch, "E25.0.7.197", {"start": v(401.84, 179.35) * mm, "end": v(409.03, 183.5) * mm});
            skLineSegment(sketch, "E25.0.7.198", {"start": v(292.43, 191.8) * mm, "end": v(292.43, 183.5) * mm});
            skLineSegment(sketch, "E25.0.7.199", {"start": v(171.85, 164.6) * mm, "end": v(164.66, 168.75) * mm});
            skLineSegment(sketch, "E25.0.7.200", {"start": v(197.4, 179.35) * mm, "end": v(204.59, 183.5) * mm});
            skLineSegment(sketch, "E25.0.7.201", {"start": v(52.58, 181.2) * mm, "end": v(59.77, 177.05) * mm});
            skLineSegment(sketch, "E25.0.7.202", {"start": v(411.7, 191.8) * mm, "end": v(418.88, 195.95) * mm});
            skLineSegment(sketch, "E25.0.7.203", {"start": v(409.03, 191.8) * mm, "end": v(401.84, 195.95) * mm});
            skLineSegment(sketch, "E25.0.7.204", {"start": v(207.25, 191.8) * mm, "end": v(214.44, 195.95) * mm});
            skLineSegment(sketch, "E25.0.7.205", {"start": v(403.17, 177.05) * mm, "end": v(410.35, 181.2) * mm});
            skLineSegment(sketch, "E25.0.7.206", {"start": v(495.54, 164.6) * mm, "end": v(488.35, 168.75) * mm});
            skLineSegment(sketch, "E25.0.7.207", {"start": v(468.65, 177.05) * mm, "end": v(468.65, 168.75) * mm});
            skLineSegment(sketch, "E25.0.7.208", {"start": v(264.21, 177.05) * mm, "end": v(264.21, 168.75) * mm});
            skLineSegment(sketch, "E25.0.7.209", {"start": v(238.66, 183.5) * mm, "end": v(238.66, 191.8) * mm});
            skLineSegment(sketch, "E25.0.7.210", {"start": v(247.18, 168.75) * mm, "end": v(240, 164.6) * mm});
            skLineSegment(sketch, "E25.0.7.211", {"start": v(85.33, 183.5) * mm, "end": v(85.33, 191.8) * mm});
            skLineSegment(sketch, "E25.0.7.212", {"start": v(137.77, 164.6) * mm, "end": v(130.58, 168.75) * mm});
            skLineSegment(sketch, "E25.0.7.213", {"start": v(374.96, 183.5) * mm, "end": v(367.77, 179.35) * mm});
            skLineSegment(sketch, "E25.0.7.214", {"start": v(323.85, 191.8) * mm, "end": v(323.85, 183.5) * mm});
            skLineSegment(sketch, "E25.0.7.215", {"start": v(266.88, 177.05) * mm, "end": v(274.07, 181.2) * mm});
            skLineSegment(sketch, "E25.0.7.216", {"start": v(326.5, 191.8) * mm, "end": v(326.5, 183.5) * mm});
            skLineSegment(sketch, "E25.0.7.217", {"start": v(232.8, 177.05) * mm, "end": v(240, 181.2) * mm});
            skLineSegment(sketch, "E25.0.7.218", {"start": v(306.8, 183.5) * mm, "end": v(306.8, 191.8) * mm});
            skLineSegment(sketch, "E25.0.7.219", {"start": v(119.4, 191.8) * mm, "end": v(119.4, 183.5) * mm});
            skLineSegment(sketch, "E25.0.7.220", {"start": v(122.06, 191.8) * mm, "end": v(122.06, 183.5) * mm});
            skLineSegment(sketch, "E25.0.7.221", {"start": v(170.52, 183.5) * mm, "end": v(163.33, 179.35) * mm});
            skLineSegment(sketch, "E25.0.7.222", {"start": v(428.72, 191.8) * mm, "end": v(428.72, 183.5) * mm});
            skLineSegment(sketch, "E25.0.7.223", {"start": v(51.26, 183.5) * mm, "end": v(51.26, 191.8) * mm});
            skLineSegment(sketch, "E25.0.7.224", {"start": v(386.13, 168.75) * mm, "end": v(386.13, 177.05) * mm});
            skLineSegment(sketch, "E25.0.7.225", {"start": v(44.07, 179.35) * mm, "end": v(51.26, 183.5) * mm});
            skLineSegment(sketch, "E25.0.7.226", {"start": v(462.8, 191.8) * mm, "end": v(469.99, 195.95) * mm});
            skLineSegment(sketch, "E25.0.7.227", {"start": v(214.44, 179.35) * mm, "end": v(207.25, 183.5) * mm});
            skLineSegment(sketch, "E25.0.7.228", {"start": v(205.91, 181.2) * mm, "end": v(213.1, 177.05) * mm});
            skLineSegment(sketch, "E25.0.7.229", {"start": v(366.43, 177.05) * mm, "end": v(366.43, 168.75) * mm});
            skLineSegment(sketch, "E25.0.7.230", {"start": v(130.58, 177.05) * mm, "end": v(137.77, 181.2) * mm});
            skLineSegment(sketch, "E25.0.7.231", {"start": v(224.28, 191.8) * mm, "end": v(224.28, 183.5) * mm});
            skLineSegment(sketch, "E25.0.7.232", {"start": v(384.8, 179.35) * mm, "end": v(392, 183.5) * mm});
            skLineSegment(sketch, "E25.0.7.233", {"start": v(275.4, 183.5) * mm, "end": v(282.58, 179.35) * mm});
            skLineSegment(sketch, "E25.0.7.234", {"start": v(19.84, 183.5) * mm, "end": v(27.03, 179.35) * mm});
            skLineSegment(sketch, "E25.0.7.235", {"start": v(180.36, 179.35) * mm, "end": v(187.55, 183.5) * mm});
            skLineSegment(sketch, "E25.0.7.236", {"start": v(410.35, 181.2) * mm, "end": v(417.54, 177.05) * mm});
            skLineSegment(sketch, "E25.0.7.237", {"start": v(255.7, 191.8) * mm, "end": v(248.5, 195.95) * mm});
            skLineSegment(sketch, "E25.0.7.238", {"start": v(53.92, 191.8) * mm, "end": v(61.1, 195.95) * mm});
            skLineSegment(sketch, "E25.0.7.239", {"start": v(162, 177.05) * mm, "end": v(162, 168.75) * mm});
            skLineSegment(sketch, "E25.0.7.240", {"start": v(51.26, 191.8) * mm, "end": v(44.07, 195.95) * mm});
            skLineSegment(sketch, "E25.0.7.241", {"start": v(427.4, 181.2) * mm, "end": v(434.59, 177.05) * mm});
            skLineSegment(sketch, "E25.0.7.242", {"start": v(460.14, 191.8) * mm, "end": v(452.95, 195.95) * mm});
            skLineSegment(sketch, "E25.0.7.243", {"start": v(272.74, 183.5) * mm, "end": v(265.55, 179.35) * mm});
            skLineSegment(sketch, "E25.0.7.244", {"start": v(181.7, 168.75) * mm, "end": v(181.7, 177.05) * mm});
            skLineSegment(sketch, "E25.0.7.245", {"start": v(335.02, 177.05) * mm, "end": v(342.21, 181.2) * mm});
            skLineSegment(sketch, "E25.0.7.246", {"start": v(221.63, 191.8) * mm, "end": v(221.63, 183.5) * mm});
            skLineSegment(sketch, "E25.0.7.247", {"start": v(68.3, 183.5) * mm, "end": v(61.1, 179.35) * mm});
            skLineSegment(sketch, "E25.0.7.248", {"start": v(130.58, 168.75) * mm, "end": v(130.58, 177.05) * mm});
            skLineSegment(sketch, "E25.0.7.249", {"start": v(477.18, 183.5) * mm, "end": v(469.99, 179.35) * mm});
            skLineSegment(sketch, "E25.0.7.250", {"start": v(469.99, 195.95) * mm, "end": v(477.18, 191.8) * mm});
            skLineSegment(sketch, "E25.0.7.251", {"start": v(360.58, 183.5) * mm, "end": v(360.58, 191.8) * mm});
            skLineSegment(sketch, "E25.0.7.252", {"start": v(122.06, 183.5) * mm, "end": v(129.25, 179.35) * mm});
            skLineSegment(sketch, "E25.0.7.253", {"start": v(95.18, 179.35) * mm, "end": v(102.37, 183.5) * mm});
            skLineSegment(sketch, "E25.0.7.254", {"start": v(137.77, 181.2) * mm, "end": v(144.96, 177.05) * mm});
            skLineSegment(sketch, "E25.0.7.255", {"start": v(469.99, 179.35) * mm, "end": v(462.8, 183.5) * mm});
            skLineSegment(sketch, "E25.0.7.256", {"start": v(417.54, 177.05) * mm, "end": v(417.54, 168.75) * mm});
            skLineSegment(sketch, "E25.0.7.257", {"start": v(120.74, 181.2) * mm, "end": v(127.93, 177.05) * mm});
            skLineSegment(sketch, "E25.0.7.258", {"start": v(477.18, 191.8) * mm, "end": v(477.18, 183.5) * mm});
            skLineSegment(sketch, "E25.0.7.259", {"start": v(420.2, 177.05) * mm, "end": v(427.4, 181.2) * mm});
            skLineSegment(sketch, "E25.0.7.260", {"start": v(275.4, 191.8) * mm, "end": v(275.4, 183.5) * mm});
            skLineSegment(sketch, "E25.0.7.261", {"start": v(255.7, 183.5) * mm, "end": v(255.7, 191.8) * mm});
            skLineSegment(sketch, "E25.0.7.262", {"start": v(215.77, 177.05) * mm, "end": v(222.96, 181.2) * mm});
            skLineSegment(sketch, "E25.0.7.263", {"start": v(42.74, 177.05) * mm, "end": v(42.74, 168.75) * mm});
            skLineSegment(sketch, "E25.0.7.264", {"start": v(350.73, 179.35) * mm, "end": v(357.92, 183.5) * mm});
            skLineSegment(sketch, "E25.0.7.265", {"start": v(78.14, 179.35) * mm, "end": v(85.33, 183.5) * mm});
            skLineSegment(sketch, "E25.0.7.266", {"start": v(119.4, 183.5) * mm, "end": v(112.22, 179.35) * mm});
            skLineSegment(sketch, "E25.0.7.267", {"start": v(19.84, 191.8) * mm, "end": v(19.84, 183.5) * mm});
            skLineSegment(sketch, "E25.0.7.268", {"start": v(496.87, 183.5) * mm, "end": v(504.06, 179.35) * mm});
            skLineSegment(sketch, "E25.0.7.269", {"start": v(325.18, 181.2) * mm, "end": v(332.37, 177.05) * mm});
            skLineSegment(sketch, "E25.0.7.270", {"start": v(367.77, 195.95) * mm, "end": v(374.96, 191.8) * mm});
            skLineSegment(sketch, "E25.0.7.271", {"start": v(258.36, 183.5) * mm, "end": v(258.36, 191.8) * mm});
            skLineSegment(sketch, "E25.0.7.272", {"start": v(163.33, 195.95) * mm, "end": v(170.52, 191.8) * mm});
            skLineSegment(sketch, "E25.0.7.273", {"start": v(179.04, 177.05) * mm, "end": v(179.04, 168.75) * mm});
            skLineSegment(sketch, "E25.0.7.274", {"start": v(249.84, 168.75) * mm, "end": v(249.84, 177.05) * mm});
            skLineSegment(sketch, "E25.0.7.275", {"start": v(139.1, 183.5) * mm, "end": v(146.29, 179.35) * mm});
            skLineSegment(sketch, "E25.0.7.276", {"start": v(418.88, 179.35) * mm, "end": v(411.7, 183.5) * mm});
            skLineSegment(sketch, "E25.0.7.277", {"start": v(426.07, 191.8) * mm, "end": v(426.07, 183.5) * mm});
            skLineSegment(sketch, "E25.0.7.278", {"start": v(367.77, 179.35) * mm, "end": v(360.58, 183.5) * mm});
            skLineSegment(sketch, "E25.0.7.279", {"start": v(352.06, 177.05) * mm, "end": v(359.24, 181.2) * mm});
            skLineSegment(sketch, "E25.0.7.280", {"start": v(163.33, 179.35) * mm, "end": v(156.14, 183.5) * mm});
            skLineSegment(sketch, "E25.0.7.281", {"start": v(112.22, 179.35) * mm, "end": v(105.03, 183.5) * mm});
            skLineSegment(sketch, "E25.0.7.282", {"start": v(487.02, 195.95) * mm, "end": v(479.83, 191.8) * mm});
            skLineSegment(sketch, "E25.0.7.283", {"start": v(374.96, 191.8) * mm, "end": v(374.96, 183.5) * mm});
            skLineSegment(sketch, "E25.0.7.284", {"start": v(17.19, 183.5) * mm, "end": v(10, 179.35) * mm});
            skLineSegment(sketch, "E25.0.7.285", {"start": v(221.63, 183.5) * mm, "end": v(214.44, 179.35) * mm});
            skLineSegment(sketch, "E25.0.7.286", {"start": v(282.58, 195.95) * mm, "end": v(275.4, 191.8) * mm});
            skLineSegment(sketch, "E25.0.7.287", {"start": v(335.02, 168.75) * mm, "end": v(335.02, 177.05) * mm});
            skLineSegment(sketch, "E25.0.7.288", {"start": v(170.52, 191.8) * mm, "end": v(170.52, 183.5) * mm});
            skLineSegment(sketch, "E25.0.7.289", {"start": v(291.1, 181.2) * mm, "end": v(298.29, 177.05) * mm});
            skLineSegment(sketch, "E25.0.7.290", {"start": v(173.17, 191.8) * mm, "end": v(173.17, 183.5) * mm});
            skLineSegment(sketch, "E25.0.7.291", {"start": v(495.54, 181.2) * mm, "end": v(502.73, 177.05) * mm});
            skLineSegment(sketch, "E25.0.7.292", {"start": v(147.62, 168.75) * mm, "end": v(147.62, 177.05) * mm});
            skLineSegment(sketch, "E25.0.7.293", {"start": v(153.48, 183.5) * mm, "end": v(153.48, 191.8) * mm});
            skLineSegment(sketch, "E25.0.7.294", {"start": v(222.96, 181.2) * mm, "end": v(230.15, 177.05) * mm});
            skLineSegment(sketch, "E25.0.7.295", {"start": v(479.83, 191.8) * mm, "end": v(479.83, 183.5) * mm});
            skLineSegment(sketch, "E25.0.7.296", {"start": v(420.2, 168.75) * mm, "end": v(420.2, 177.05) * mm});
            skLineSegment(sketch, "E25.0.7.297", {"start": v(326.5, 183.5) * mm, "end": v(333.7, 179.35) * mm});
            skLineSegment(sketch, "E25.0.7.298", {"start": v(173.17, 183.5) * mm, "end": v(180.36, 179.35) * mm});
            skLineSegment(sketch, "E25.0.7.299", {"start": v(342.21, 181.2) * mm, "end": v(349.4, 177.05) * mm});
            skLineSegment(sketch, "E25.0.7.300", {"start": v(265.55, 195.95) * mm, "end": v(272.74, 191.8) * mm});
            skLineSegment(sketch, "E25.0.7.301", {"start": v(274.07, 181.2) * mm, "end": v(281.26, 177.05) * mm});
            skLineSegment(sketch, "E25.0.7.302", {"start": v(215.77, 168.75) * mm, "end": v(215.77, 177.05) * mm});
            skLineSegment(sketch, "E25.0.7.303", {"start": v(462.8, 183.5) * mm, "end": v(462.8, 191.8) * mm});
            skLineSegment(sketch, "E25.0.7.304", {"start": v(281.26, 177.05) * mm, "end": v(281.26, 168.75) * mm});
            skLineSegment(sketch, "E25.0.7.305", {"start": v(156.14, 183.5) * mm, "end": v(156.14, 191.8) * mm});
            skLineSegment(sketch, "E25.0.7.306", {"start": v(213.1, 177.05) * mm, "end": v(213.1, 168.75) * mm});
            skLineSegment(sketch, "E25.0.7.307", {"start": v(96.5, 177.05) * mm, "end": v(103.7, 181.2) * mm});
            skLineSegment(sketch, "E25.0.7.308", {"start": v(460.14, 183.5) * mm, "end": v(460.14, 191.8) * mm});
            skLineSegment(sketch, "E25.0.7.309", {"start": v(323.85, 183.5) * mm, "end": v(316.66, 179.35) * mm});
            skLineSegment(sketch, "E25.0.7.310", {"start": v(272.74, 191.8) * mm, "end": v(272.74, 183.5) * mm});
            skLineSegment(sketch, "E25.0.7.311", {"start": v(377.61, 183.5) * mm, "end": v(384.8, 179.35) * mm});
            skLineSegment(sketch, "E25.0.7.312", {"start": v(282.58, 179.35) * mm, "end": v(289.77, 183.5) * mm});
            skLineSegment(sketch, "E25.0.7.313", {"start": v(146.29, 179.35) * mm, "end": v(153.48, 183.5) * mm});
            skLineSegment(sketch, "E25.0.7.314", {"start": v(343.54, 183.5) * mm, "end": v(350.73, 179.35) * mm});
            skLineSegment(sketch, "E25.0.7.315", {"start": v(376.29, 181.2) * mm, "end": v(383.48, 177.05) * mm});
            skLineSegment(sketch, "E25.0.7.316", {"start": v(171.85, 181.2) * mm, "end": v(179.04, 177.05) * mm});
            skLineSegment(sketch, "E25.0.7.317", {"start": v(53.92, 183.5) * mm, "end": v(53.92, 191.8) * mm});
            skLineSegment(sketch, "E25.0.7.318", {"start": v(292.43, 183.5) * mm, "end": v(299.62, 179.35) * mm});
            skLineSegment(sketch, "E25.0.7.319", {"start": v(377.61, 191.8) * mm, "end": v(377.61, 183.5) * mm});
            skLineSegment(sketch, "E25.0.7.320", {"start": v(383.48, 177.05) * mm, "end": v(383.48, 168.75) * mm});
            skLineSegment(sketch, "E25.0.7.321", {"start": v(129.25, 179.35) * mm, "end": v(136.44, 183.5) * mm});
            skLineSegment(sketch, "E25.0.7.322", {"start": v(428.72, 183.5) * mm, "end": v(435.91, 179.35) * mm});
            skLineSegment(sketch, "E25.0.7.323", {"start": v(496.87, 191.8) * mm, "end": v(496.87, 183.5) * mm});
            skLineSegment(sketch, "E25.0.7.324", {"start": v(224.28, 183.5) * mm, "end": v(231.47, 179.35) * mm});
            skLineSegment(sketch, "E25.0.7.325", {"start": v(333.7, 179.35) * mm, "end": v(340.88, 183.5) * mm});
            skLineSegment(sketch, "E25.0.7.326", {"start": v(11.33, 177.05) * mm, "end": v(18.52, 181.2) * mm});
            skLineSegment(sketch, "E25.0.7.327", {"start": v(18.52, 181.2) * mm, "end": v(25.7, 177.05) * mm});
            skLineSegment(sketch, "E25.0.7.328", {"start": v(494.21, 183.5) * mm, "end": v(494.21, 191.8) * mm});
            skLineSegment(sketch, "E25.0.7.329", {"start": v(315.32, 177.05) * mm, "end": v(315.32, 168.75) * mm});
            skLineSegment(sketch, "E25.0.7.330", {"start": v(360.58, 191.8) * mm, "end": v(367.77, 195.95) * mm});
            skLineSegment(sketch, "E25.0.7.331", {"start": v(316.66, 179.35) * mm, "end": v(309.47, 183.5) * mm});
            skLineSegment(sketch, "E25.0.7.332", {"start": v(308.13, 181.2) * mm, "end": v(315.32, 177.05) * mm});
            skLineSegment(sketch, "E25.0.7.333", {"start": v(147.62, 177.05) * mm, "end": v(154.8, 181.2) * mm});
            skLineSegment(sketch, "E25.0.7.334", {"start": v(359.24, 181.2) * mm, "end": v(366.43, 177.05) * mm});
            skLineSegment(sketch, "E25.0.7.335", {"start": v(110.88, 177.05) * mm, "end": v(110.88, 168.75) * mm});
            skLineSegment(sketch, "E25.0.7.336", {"start": v(154.8, 181.2) * mm, "end": v(162, 177.05) * mm});
            skLineSegment(sketch, "E25.0.7.337", {"start": v(17.19, 191.8) * mm, "end": v(17.19, 183.5) * mm});
            skLineSegment(sketch, "E25.0.7.338", {"start": v(156.14, 191.8) * mm, "end": v(163.33, 195.95) * mm});
            skLineSegment(sketch, "E25.0.7.339", {"start": v(103.7, 181.2) * mm, "end": v(110.88, 177.05) * mm});
            skLineSegment(sketch, "E25.0.7.340", {"start": v(471.32, 177.05) * mm, "end": v(478.5, 181.2) * mm});
            skLineSegment(sketch, "E25.0.7.341", {"start": v(426.07, 183.5) * mm, "end": v(418.88, 179.35) * mm});
            skLineSegment(sketch, "E25.0.7.342", {"start": v(357.92, 183.5) * mm, "end": v(357.92, 191.8) * mm});
            skLineSegment(sketch, "E25.0.7.343", {"start": v(317.99, 177.05) * mm, "end": v(325.18, 181.2) * mm});
            skLineSegment(sketch, "E25.0.7.344", {"start": v(258.36, 191.8) * mm, "end": v(265.55, 195.95) * mm});
            skLineSegment(sketch, "E25.0.7.345", {"start": v(283.91, 168.75) * mm, "end": v(283.91, 177.05) * mm});
            skLineSegment(sketch, "E25.0.7.346", {"start": v(283.91, 177.05) * mm, "end": v(291.1, 181.2) * mm});
            skLineSegment(sketch, "E25.0.7.347", {"start": v(113.55, 177.05) * mm, "end": v(120.74, 181.2) * mm});
            skLineSegment(sketch, "E25.0.7.348", {"start": v(36.88, 183.5) * mm, "end": v(44.07, 179.35) * mm});
            skLineSegment(sketch, "E25.0.7.349", {"start": v(36.88, 191.8) * mm, "end": v(36.88, 183.5) * mm});
            skLineSegment(sketch, "E25.0.7.350", {"start": v(34.22, 183.5) * mm, "end": v(34.22, 191.8) * mm});
            skLineSegment(sketch, "E25.0.7.351", {"start": v(485.7, 177.05) * mm, "end": v(485.7, 168.75) * mm});
            skLineSegment(sketch, "E25.0.7.352", {"start": v(478.5, 181.2) * mm, "end": v(485.7, 177.05) * mm});
            skLineSegment(sketch, "E25.0.7.353", {"start": v(487.02, 179.35) * mm, "end": v(494.21, 183.5) * mm});
            skLineSegment(sketch, "E25.0.7.354", {"start": v(27.03, 179.35) * mm, "end": v(34.22, 183.5) * mm});
            skLineSegment(sketch, "E25.0.7.355", {"start": v(479.83, 183.5) * mm, "end": v(487.02, 179.35) * mm});
            skLineSegment(sketch, "E25.0.7.356", {"start": v(28.36, 177.05) * mm, "end": v(35.55, 181.2) * mm});
            skLineSegment(sketch, "E25.0.7.357", {"start": v(35.55, 181.2) * mm, "end": v(42.74, 177.05) * mm});
            skLineSegment(sketch, "E25.0.7.358", {"start": v(488.35, 177.05) * mm, "end": v(495.54, 181.2) * mm});
            skLineSegment(sketch, "E25.0.7.359", {"start": v(488.35, 168.75) * mm, "end": v(488.35, 177.05) * mm});
            skLineSegment(sketch, "E25.0.8.0", {"start": v(332.37, 139.25) * mm, "end": v(325.18, 135.1) * mm});
            skLineSegment(sketch, "E25.0.8.1", {"start": v(511.25, 162.3) * mm, "end": v(504.06, 166.45) * mm});
            skLineSegment(sketch, "E25.0.8.2", {"start": v(2.81, 162.3) * mm, "end": v(10, 166.45) * mm});
            skLineSegment(sketch, "E25.0.8.3", {"start": v(127.93, 139.25) * mm, "end": v(120.74, 135.1) * mm});
            skLineSegment(sketch, "E25.0.8.4", {"start": v(512.57, 135.1) * mm, "end": v(505.39, 139.25) * mm});
            skLineSegment(sketch, "E25.0.8.5", {"start": v(519.76, 139.25) * mm, "end": v(512.57, 135.1) * mm});
            skLineSegment(sketch, "E25.0.8.6", {"start": v(25.7, 139.25) * mm, "end": v(18.52, 135.1) * mm});
            skLineSegment(sketch, "E25.0.8.7", {"start": v(11.33, 139.25) * mm, "end": v(11.33, 147.55) * mm});
            skLineSegment(sketch, "E25.0.8.8", {"start": v(18.52, 135.1) * mm, "end": v(11.33, 139.25) * mm});
            skLineSegment(sketch, "E25.0.8.9", {"start": v(519.76, 147.55) * mm, "end": v(519.76, 139.25) * mm});
            skLineSegment(sketch, "E25.0.8.10", {"start": v(76.82, 139.25) * mm, "end": v(69.63, 135.1) * mm});
            skLineSegment(sketch, "E25.0.8.11", {"start": v(112.22, 166.45) * mm, "end": v(119.4, 162.3) * mm});
            skLineSegment(sketch, "E25.0.8.12", {"start": v(205.91, 135.1) * mm, "end": v(198.73, 139.25) * mm});
            skLineSegment(sketch, "E25.0.8.13", {"start": v(197.4, 166.45) * mm, "end": v(190.2, 162.3) * mm});
            skLineSegment(sketch, "E25.0.8.14", {"start": v(93.85, 139.25) * mm, "end": v(86.66, 135.1) * mm});
            skLineSegment(sketch, "E25.0.8.15", {"start": v(129.25, 166.45) * mm, "end": v(122.06, 162.3) * mm});
            skLineSegment(sketch, "E25.0.8.16", {"start": v(298.29, 139.25) * mm, "end": v(291.1, 135.1) * mm});
            skLineSegment(sketch, "E25.0.8.17", {"start": v(502.73, 139.25) * mm, "end": v(495.54, 135.1) * mm});
            skLineSegment(sketch, "E25.0.8.18", {"start": v(289.77, 162.3) * mm, "end": v(282.58, 166.45) * mm});
            skLineSegment(sketch, "E25.0.8.19", {"start": v(85.33, 162.3) * mm, "end": v(78.14, 166.45) * mm});
            skLineSegment(sketch, "E25.0.8.20", {"start": v(494.21, 162.3) * mm, "end": v(487.02, 166.45) * mm});
            skLineSegment(sketch, "E25.0.8.21", {"start": v(333.7, 166.45) * mm, "end": v(326.5, 162.3) * mm});
            skLineSegment(sketch, "E25.0.8.22", {"start": v(95.18, 166.45) * mm, "end": v(87.99, 162.3) * mm});
            skLineSegment(sketch, "E25.0.8.23", {"start": v(478.5, 135.1) * mm, "end": v(471.32, 139.25) * mm});
            skLineSegment(sketch, "E25.0.8.24", {"start": v(274.07, 135.1) * mm, "end": v(266.88, 139.25) * mm});
            skLineSegment(sketch, "E25.0.8.25", {"start": v(444.43, 135.1) * mm, "end": v(437.24, 139.25) * mm});
            skLineSegment(sketch, "E25.0.8.26", {"start": v(401.84, 166.45) * mm, "end": v(394.65, 162.3) * mm});
            skLineSegment(sketch, "E25.0.8.27", {"start": v(410.35, 135.1) * mm, "end": v(403.17, 139.25) * mm});
            skLineSegment(sketch, "E25.0.8.28", {"start": v(468.65, 139.25) * mm, "end": v(461.46, 135.1) * mm});
            skLineSegment(sketch, "E25.0.8.29", {"start": v(427.4, 135.1) * mm, "end": v(420.2, 139.25) * mm});
            skLineSegment(sketch, "E25.0.8.30", {"start": v(59.77, 139.25) * mm, "end": v(52.58, 135.1) * mm});
            skLineSegment(sketch, "E25.0.8.31", {"start": v(512.57, 151.7) * mm, "end": v(519.76, 147.55) * mm});
            skLineSegment(sketch, "E25.0.8.32", {"start": v(196.07, 139.25) * mm, "end": v(188.88, 135.1) * mm});
            skLineSegment(sketch, "E25.0.8.33", {"start": v(86.66, 135.1) * mm, "end": v(79.47, 139.25) * mm});
            skLineSegment(sketch, "E25.0.8.34", {"start": v(400.5, 139.25) * mm, "end": v(393.32, 135.1) * mm});
            skLineSegment(sketch, "E25.0.8.35", {"start": v(103.7, 135.1) * mm, "end": v(96.5, 139.25) * mm});
            skLineSegment(sketch, "E25.0.8.36", {"start": v(299.62, 166.45) * mm, "end": v(292.43, 162.3) * mm});
            skLineSegment(sketch, "E25.0.8.37", {"start": v(504.06, 166.45) * mm, "end": v(496.87, 162.3) * mm});
            skLineSegment(sketch, "E25.0.8.38", {"start": v(2.81, 154) * mm, "end": v(2.81, 162.3) * mm});
            skLineSegment(sketch, "E25.0.8.39", {"start": v(308.13, 135.1) * mm, "end": v(300.95, 139.25) * mm});
            skLineSegment(sketch, "E25.0.8.40", {"start": v(417.54, 139.25) * mm, "end": v(410.35, 135.1) * mm});
            skLineSegment(sketch, "E25.0.8.41", {"start": v(434.59, 139.25) * mm, "end": v(427.4, 135.1) * mm});
            skLineSegment(sketch, "E25.0.8.42", {"start": v(62.44, 139.25) * mm, "end": v(62.44, 147.55) * mm});
            skLineSegment(sketch, "E25.0.8.43", {"start": v(69.63, 135.1) * mm, "end": v(62.44, 139.25) * mm});
            skLineSegment(sketch, "E25.0.8.44", {"start": v(325.18, 135.1) * mm, "end": v(317.99, 139.25) * mm});
            skLineSegment(sketch, "E25.0.8.45", {"start": v(264.21, 139.25) * mm, "end": v(257.02, 135.1) * mm});
            skLineSegment(sketch, "E25.0.8.46", {"start": v(120.74, 135.1) * mm, "end": v(113.55, 139.25) * mm});
            skLineSegment(sketch, "E25.0.8.47", {"start": v(502.73, 147.55) * mm, "end": v(502.73, 139.25) * mm});
            skLineSegment(sketch, "E25.0.8.48", {"start": v(316.66, 166.45) * mm, "end": v(323.85, 162.3) * mm});
            skLineSegment(sketch, "E25.0.8.49", {"start": v(505.39, 139.25) * mm, "end": v(505.39, 147.55) * mm});
            skLineSegment(sketch, "E25.0.8.50", {"start": v(10, 149.85) * mm, "end": v(2.81, 154) * mm});
            skLineSegment(sketch, "E25.0.8.51", {"start": v(59.77, 147.55) * mm, "end": v(59.77, 139.25) * mm});
            skLineSegment(sketch, "E25.0.8.52", {"start": v(291.1, 135.1) * mm, "end": v(283.91, 139.25) * mm});
            skLineSegment(sketch, "E25.0.8.53", {"start": v(511.25, 154) * mm, "end": v(511.25, 162.3) * mm});
            skLineSegment(sketch, "E25.0.8.54", {"start": v(392, 162.3) * mm, "end": v(384.8, 166.45) * mm});
            skLineSegment(sketch, "E25.0.8.55", {"start": v(187.55, 162.3) * mm, "end": v(180.36, 166.45) * mm});
            skLineSegment(sketch, "E25.0.8.56", {"start": v(247.18, 147.55) * mm, "end": v(247.18, 139.25) * mm});
            skLineSegment(sketch, "E25.0.8.57", {"start": v(188.88, 151.7) * mm, "end": v(196.07, 147.55) * mm});
            skLineSegment(sketch, "E25.0.8.58", {"start": v(369.1, 147.55) * mm, "end": v(376.29, 151.7) * mm});
            skLineSegment(sketch, "E25.0.8.59", {"start": v(409.03, 154) * mm, "end": v(409.03, 162.3) * mm});
            skLineSegment(sketch, "E25.0.8.60", {"start": v(188.88, 135.1) * mm, "end": v(181.7, 139.25) * mm});
            skLineSegment(sketch, "E25.0.8.61", {"start": v(204.59, 154) * mm, "end": v(204.59, 162.3) * mm});
            skLineSegment(sketch, "E25.0.8.62", {"start": v(164.66, 147.55) * mm, "end": v(171.85, 151.7) * mm});
            skLineSegment(sketch, "E25.0.8.63", {"start": v(230.15, 147.55) * mm, "end": v(230.15, 139.25) * mm});
            skLineSegment(sketch, "E25.0.8.64", {"start": v(343.54, 162.3) * mm, "end": v(343.54, 154) * mm});
            skLineSegment(sketch, "E25.0.8.65", {"start": v(139.1, 162.3) * mm, "end": v(139.1, 154) * mm});
            skLineSegment(sketch, "E25.0.8.66", {"start": v(70.95, 154) * mm, "end": v(78.14, 149.85) * mm});
            skLineSegment(sketch, "E25.0.8.67", {"start": v(96.5, 139.25) * mm, "end": v(96.5, 147.55) * mm});
            skLineSegment(sketch, "E25.0.8.68", {"start": v(44.07, 166.45) * mm, "end": v(36.88, 162.3) * mm});
            skLineSegment(sketch, "E25.0.8.69", {"start": v(162, 139.25) * mm, "end": v(154.8, 135.1) * mm});
            skLineSegment(sketch, "E25.0.8.70", {"start": v(300.95, 139.25) * mm, "end": v(300.95, 147.55) * mm});
            skLineSegment(sketch, "E25.0.8.71", {"start": v(222.96, 135.1) * mm, "end": v(215.77, 139.25) * mm});
            skLineSegment(sketch, "E25.0.8.72", {"start": v(452.95, 149.85) * mm, "end": v(460.14, 154) * mm});
            skLineSegment(sketch, "E25.0.8.73", {"start": v(369.1, 139.25) * mm, "end": v(369.1, 147.55) * mm});
            skLineSegment(sketch, "E25.0.8.74", {"start": v(366.43, 139.25) * mm, "end": v(359.24, 135.1) * mm});
            skLineSegment(sketch, "E25.0.8.75", {"start": v(164.66, 139.25) * mm, "end": v(164.66, 147.55) * mm});
            skLineSegment(sketch, "E25.0.8.76", {"start": v(248.5, 149.85) * mm, "end": v(255.7, 154) * mm});
            skLineSegment(sketch, "E25.0.8.77", {"start": v(249.84, 147.55) * mm, "end": v(257.02, 151.7) * mm});
            skLineSegment(sketch, "E25.0.8.78", {"start": v(393.32, 135.1) * mm, "end": v(386.13, 139.25) * mm});
            skLineSegment(sketch, "E25.0.8.79", {"start": v(62.44, 147.55) * mm, "end": v(69.63, 151.7) * mm});
            skLineSegment(sketch, "E25.0.8.80", {"start": v(136.44, 154) * mm, "end": v(136.44, 162.3) * mm});
            skLineSegment(sketch, "E25.0.8.81", {"start": v(102.37, 154) * mm, "end": v(102.37, 162.3) * mm});
            skLineSegment(sketch, "E25.0.8.82", {"start": v(418.88, 166.45) * mm, "end": v(426.07, 162.3) * mm});
            skLineSegment(sketch, "E25.0.8.83", {"start": v(454.28, 147.55) * mm, "end": v(461.46, 151.7) * mm});
            skLineSegment(sketch, "E25.0.8.84", {"start": v(78.14, 166.45) * mm, "end": v(70.95, 162.3) * mm});
            skLineSegment(sketch, "E25.0.8.85", {"start": v(105.03, 154) * mm, "end": v(105.03, 162.3) * mm});
            skLineSegment(sketch, "E25.0.8.86", {"start": v(190.2, 154) * mm, "end": v(197.4, 149.85) * mm});
            skLineSegment(sketch, "E25.0.8.87", {"start": v(352.06, 139.25) * mm, "end": v(352.06, 147.55) * mm});
            skLineSegment(sketch, "E25.0.8.88", {"start": v(400.5, 147.55) * mm, "end": v(400.5, 139.25) * mm});
            skLineSegment(sketch, "E25.0.8.89", {"start": v(299.62, 149.85) * mm, "end": v(306.8, 154) * mm});
            skLineSegment(sketch, "E25.0.8.90", {"start": v(190.2, 162.3) * mm, "end": v(190.2, 154) * mm});
            skLineSegment(sketch, "E25.0.8.91", {"start": v(76.82, 147.55) * mm, "end": v(76.82, 139.25) * mm});
            skLineSegment(sketch, "E25.0.8.92", {"start": v(392, 154) * mm, "end": v(392, 162.3) * mm});
            skLineSegment(sketch, "E25.0.8.93", {"start": v(309.47, 162.3) * mm, "end": v(316.66, 166.45) * mm});
            skLineSegment(sketch, "E25.0.8.94", {"start": v(349.4, 139.25) * mm, "end": v(342.21, 135.1) * mm});
            skLineSegment(sketch, "E25.0.8.95", {"start": v(257.02, 151.7) * mm, "end": v(264.21, 147.55) * mm});
            skLineSegment(sketch, "E25.0.8.96", {"start": v(61.1, 166.45) * mm, "end": v(68.3, 162.3) * mm});
            skLineSegment(sketch, "E25.0.8.97", {"start": v(146.29, 166.45) * mm, "end": v(139.1, 162.3) * mm});
            skLineSegment(sketch, "E25.0.8.98", {"start": v(154.8, 135.1) * mm, "end": v(147.62, 139.25) * mm});
            skLineSegment(sketch, "E25.0.8.99", {"start": v(306.8, 162.3) * mm, "end": v(299.62, 166.45) * mm});
            skLineSegment(sketch, "E25.0.8.100", {"start": v(87.99, 154) * mm, "end": v(95.18, 149.85) * mm});
            skLineSegment(sketch, "E25.0.8.101", {"start": v(105.03, 162.3) * mm, "end": v(112.22, 166.45) * mm});
            skLineSegment(sketch, "E25.0.8.102", {"start": v(102.37, 162.3) * mm, "end": v(95.18, 166.45) * mm});
            skLineSegment(sketch, "E25.0.8.103", {"start": v(187.55, 154) * mm, "end": v(187.55, 162.3) * mm});
            skLineSegment(sketch, "E25.0.8.104", {"start": v(61.1, 149.85) * mm, "end": v(53.92, 154) * mm});
            skLineSegment(sketch, "E25.0.8.105", {"start": v(437.24, 139.25) * mm, "end": v(437.24, 147.55) * mm});
            skLineSegment(sketch, "E25.0.8.106", {"start": v(393.32, 151.7) * mm, "end": v(400.5, 147.55) * mm});
            skLineSegment(sketch, "E25.0.8.107", {"start": v(232.8, 139.25) * mm, "end": v(232.8, 147.55) * mm});
            skLineSegment(sketch, "E25.0.8.108", {"start": v(87.99, 162.3) * mm, "end": v(87.99, 154) * mm});
            skLineSegment(sketch, "E25.0.8.109", {"start": v(113.55, 139.25) * mm, "end": v(113.55, 147.55) * mm});
            skLineSegment(sketch, "E25.0.8.110", {"start": v(332.37, 147.55) * mm, "end": v(332.37, 139.25) * mm});
            skLineSegment(sketch, "E25.0.8.111", {"start": v(266.88, 139.25) * mm, "end": v(266.88, 147.55) * mm});
            skLineSegment(sketch, "E25.0.8.112", {"start": v(180.36, 166.45) * mm, "end": v(173.17, 162.3) * mm});
            skLineSegment(sketch, "E25.0.8.113", {"start": v(181.7, 147.55) * mm, "end": v(188.88, 151.7) * mm});
            skLineSegment(sketch, "E25.0.8.114", {"start": v(68.3, 162.3) * mm, "end": v(68.3, 154) * mm});
            skLineSegment(sketch, "E25.0.8.115", {"start": v(317.99, 139.25) * mm, "end": v(317.99, 147.55) * mm});
            skLineSegment(sketch, "E25.0.8.116", {"start": v(485.7, 139.25) * mm, "end": v(478.5, 135.1) * mm});
            skLineSegment(sketch, "E25.0.8.117", {"start": v(10, 166.45) * mm, "end": v(17.19, 162.3) * mm});
            skLineSegment(sketch, "E25.0.8.118", {"start": v(376.29, 135.1) * mm, "end": v(369.1, 139.25) * mm});
            skLineSegment(sketch, "E25.0.8.119", {"start": v(452.95, 166.45) * mm, "end": v(445.76, 162.3) * mm});
            skLineSegment(sketch, "E25.0.8.120", {"start": v(315.32, 139.25) * mm, "end": v(308.13, 135.1) * mm});
            skLineSegment(sketch, "E25.0.8.121", {"start": v(93.85, 147.55) * mm, "end": v(93.85, 139.25) * mm});
            skLineSegment(sketch, "E25.0.8.122", {"start": v(35.55, 135.1) * mm, "end": v(28.36, 139.25) * mm});
            skLineSegment(sketch, "E25.0.8.123", {"start": v(45.4, 139.25) * mm, "end": v(45.4, 147.55) * mm});
            skLineSegment(sketch, "E25.0.8.124", {"start": v(42.74, 139.25) * mm, "end": v(35.55, 135.1) * mm});
            skLineSegment(sketch, "E25.0.8.125", {"start": v(434.59, 147.55) * mm, "end": v(434.59, 139.25) * mm});
            skLineSegment(sketch, "E25.0.8.126", {"start": v(340.88, 154) * mm, "end": v(340.88, 162.3) * mm});
            skLineSegment(sketch, "E25.0.8.127", {"start": v(394.65, 154) * mm, "end": v(401.84, 149.85) * mm});
            skLineSegment(sketch, "E25.0.8.128", {"start": v(153.48, 162.3) * mm, "end": v(146.29, 166.45) * mm});
            skLineSegment(sketch, "E25.0.8.129", {"start": v(52.58, 135.1) * mm, "end": v(45.4, 139.25) * mm});
            skLineSegment(sketch, "E25.0.8.130", {"start": v(25.7, 147.55) * mm, "end": v(25.7, 139.25) * mm});
            skLineSegment(sketch, "E25.0.8.131", {"start": v(28.36, 139.25) * mm, "end": v(28.36, 147.55) * mm});
            skLineSegment(sketch, "E25.0.8.132", {"start": v(45.4, 147.55) * mm, "end": v(52.58, 151.7) * mm});
            skLineSegment(sketch, "E25.0.8.133", {"start": v(451.62, 139.25) * mm, "end": v(444.43, 135.1) * mm});
            skLineSegment(sketch, "E25.0.8.134", {"start": v(411.7, 154) * mm, "end": v(411.7, 162.3) * mm});
            skLineSegment(sketch, "E25.0.8.135", {"start": v(342.21, 135.1) * mm, "end": v(335.02, 139.25) * mm});
            skLineSegment(sketch, "E25.0.8.136", {"start": v(443.1, 154) * mm, "end": v(443.1, 162.3) * mm});
            skLineSegment(sketch, "E25.0.8.137", {"start": v(357.92, 162.3) * mm, "end": v(350.73, 166.45) * mm});
            skLineSegment(sketch, "E25.0.8.138", {"start": v(289.77, 154) * mm, "end": v(289.77, 162.3) * mm});
            skLineSegment(sketch, "E25.0.8.139", {"start": v(204.59, 162.3) * mm, "end": v(197.4, 166.45) * mm});
            skLineSegment(sketch, "E25.0.8.140", {"start": v(198.73, 147.55) * mm, "end": v(205.91, 151.7) * mm});
            skLineSegment(sketch, "E25.0.8.141", {"start": v(454.28, 139.25) * mm, "end": v(454.28, 147.55) * mm});
            skLineSegment(sketch, "E25.0.8.142", {"start": v(86.66, 151.7) * mm, "end": v(93.85, 147.55) * mm});
            skLineSegment(sketch, "E25.0.8.143", {"start": v(443.1, 162.3) * mm, "end": v(435.91, 166.45) * mm});
            skLineSegment(sketch, "E25.0.8.144", {"start": v(435.91, 166.45) * mm, "end": v(428.72, 162.3) * mm});
            skLineSegment(sketch, "E25.0.8.145", {"start": v(437.24, 147.55) * mm, "end": v(444.43, 151.7) * mm});
            skLineSegment(sketch, "E25.0.8.146", {"start": v(231.47, 166.45) * mm, "end": v(224.28, 162.3) * mm});
            skLineSegment(sketch, "E25.0.8.147", {"start": v(79.47, 139.25) * mm, "end": v(79.47, 147.55) * mm});
            skLineSegment(sketch, "E25.0.8.148", {"start": v(309.47, 154) * mm, "end": v(309.47, 162.3) * mm});
            skLineSegment(sketch, "E25.0.8.149", {"start": v(214.44, 166.45) * mm, "end": v(221.63, 162.3) * mm});
            skLineSegment(sketch, "E25.0.8.150", {"start": v(238.66, 162.3) * mm, "end": v(231.47, 166.45) * mm});
            skLineSegment(sketch, "E25.0.8.151", {"start": v(394.65, 162.3) * mm, "end": v(394.65, 154) * mm});
            skLineSegment(sketch, "E25.0.8.152", {"start": v(445.76, 154) * mm, "end": v(452.95, 149.85) * mm});
            skLineSegment(sketch, "E25.0.8.153", {"start": v(241.32, 154) * mm, "end": v(248.5, 149.85) * mm});
            skLineSegment(sketch, "E25.0.8.154", {"start": v(231.47, 149.85) * mm, "end": v(238.66, 154) * mm});
            skLineSegment(sketch, "E25.0.8.155", {"start": v(79.47, 147.55) * mm, "end": v(86.66, 151.7) * mm});
            skLineSegment(sketch, "E25.0.8.156", {"start": v(350.73, 166.45) * mm, "end": v(343.54, 162.3) * mm});
            skLineSegment(sketch, "E25.0.8.157", {"start": v(196.07, 147.55) * mm, "end": v(196.07, 139.25) * mm});
            skLineSegment(sketch, "E25.0.8.158", {"start": v(240, 135.1) * mm, "end": v(232.8, 139.25) * mm});
            skLineSegment(sketch, "E25.0.8.159", {"start": v(69.63, 151.7) * mm, "end": v(76.82, 147.55) * mm});
            skLineSegment(sketch, "E25.0.8.160", {"start": v(349.4, 147.55) * mm, "end": v(349.4, 139.25) * mm});
            skLineSegment(sketch, "E25.0.8.161", {"start": v(383.48, 139.25) * mm, "end": v(376.29, 135.1) * mm});
            skLineSegment(sketch, "E25.0.8.162", {"start": v(144.96, 147.55) * mm, "end": v(144.96, 139.25) * mm});
            skLineSegment(sketch, "E25.0.8.163", {"start": v(179.04, 139.25) * mm, "end": v(171.85, 135.1) * mm});
            skLineSegment(sketch, "E25.0.8.164", {"start": v(386.13, 147.55) * mm, "end": v(393.32, 151.7) * mm});
            skLineSegment(sketch, "E25.0.8.165", {"start": v(435.91, 149.85) * mm, "end": v(443.1, 154) * mm});
            skLineSegment(sketch, "E25.0.8.166", {"start": v(504.06, 149.85) * mm, "end": v(511.25, 154) * mm});
            skLineSegment(sketch, "E25.0.8.167", {"start": v(403.17, 139.25) * mm, "end": v(403.17, 147.55) * mm});
            skLineSegment(sketch, "E25.0.8.168", {"start": v(241.32, 162.3) * mm, "end": v(241.32, 154) * mm});
            skLineSegment(sketch, "E25.0.8.169", {"start": v(359.24, 135.1) * mm, "end": v(352.06, 139.25) * mm});
            skLineSegment(sketch, "E25.0.8.170", {"start": v(213.1, 139.25) * mm, "end": v(205.91, 135.1) * mm});
            skLineSegment(sketch, "E25.0.8.171", {"start": v(34.22, 162.3) * mm, "end": v(27.03, 166.45) * mm});
            skLineSegment(sketch, "E25.0.8.172", {"start": v(461.46, 151.7) * mm, "end": v(468.65, 147.55) * mm});
            skLineSegment(sketch, "E25.0.8.173", {"start": v(505.39, 147.55) * mm, "end": v(512.57, 151.7) * mm});
            skLineSegment(sketch, "E25.0.8.174", {"start": v(300.95, 147.55) * mm, "end": v(308.13, 151.7) * mm});
            skLineSegment(sketch, "E25.0.8.175", {"start": v(230.15, 139.25) * mm, "end": v(222.96, 135.1) * mm});
            skLineSegment(sketch, "E25.0.8.176", {"start": v(265.55, 149.85) * mm, "end": v(258.36, 154) * mm});
            skLineSegment(sketch, "E25.0.8.177", {"start": v(144.96, 139.25) * mm, "end": v(137.77, 135.1) * mm});
            skLineSegment(sketch, "E25.0.8.178", {"start": v(27.03, 166.45) * mm, "end": v(19.84, 162.3) * mm});
            skLineSegment(sketch, "E25.0.8.179", {"start": v(384.8, 166.45) * mm, "end": v(377.61, 162.3) * mm});
            skLineSegment(sketch, "E25.0.8.180", {"start": v(340.88, 162.3) * mm, "end": v(333.7, 166.45) * mm});
            skLineSegment(sketch, "E25.0.8.181", {"start": v(136.44, 162.3) * mm, "end": v(129.25, 166.45) * mm});
            skLineSegment(sketch, "E25.0.8.182", {"start": v(198.73, 139.25) * mm, "end": v(198.73, 147.55) * mm});
            skLineSegment(sketch, "E25.0.8.183", {"start": v(70.95, 162.3) * mm, "end": v(70.95, 154) * mm});
            skLineSegment(sketch, "E25.0.8.184", {"start": v(127.93, 147.55) * mm, "end": v(127.93, 139.25) * mm});
            skLineSegment(sketch, "E25.0.8.185", {"start": v(461.46, 135.1) * mm, "end": v(454.28, 139.25) * mm});
            skLineSegment(sketch, "E25.0.8.186", {"start": v(444.43, 151.7) * mm, "end": v(451.62, 147.55) * mm});
            skLineSegment(sketch, "E25.0.8.187", {"start": v(445.76, 162.3) * mm, "end": v(445.76, 154) * mm});
            skLineSegment(sketch, "E25.0.8.188", {"start": v(240, 151.7) * mm, "end": v(247.18, 147.55) * mm});
            skLineSegment(sketch, "E25.0.8.189", {"start": v(298.29, 147.55) * mm, "end": v(298.29, 139.25) * mm});
            skLineSegment(sketch, "E25.0.8.190", {"start": v(471.32, 139.25) * mm, "end": v(471.32, 147.55) * mm});
            skLineSegment(sketch, "E25.0.8.191", {"start": v(207.25, 154) * mm, "end": v(207.25, 162.3) * mm});
            skLineSegment(sketch, "E25.0.8.192", {"start": v(281.26, 139.25) * mm, "end": v(274.07, 135.1) * mm});
            skLineSegment(sketch, "E25.0.8.193", {"start": v(257.02, 135.1) * mm, "end": v(249.84, 139.25) * mm});
            skLineSegment(sketch, "E25.0.8.194", {"start": v(248.5, 166.45) * mm, "end": v(241.32, 162.3) * mm});
            skLineSegment(sketch, "E25.0.8.195", {"start": v(451.62, 147.55) * mm, "end": v(451.62, 139.25) * mm});
            skLineSegment(sketch, "E25.0.8.196", {"start": v(110.88, 139.25) * mm, "end": v(103.7, 135.1) * mm});
            skLineSegment(sketch, "E25.0.8.197", {"start": v(401.84, 149.85) * mm, "end": v(409.03, 154) * mm});
            skLineSegment(sketch, "E25.0.8.198", {"start": v(292.43, 162.3) * mm, "end": v(292.43, 154) * mm});
            skLineSegment(sketch, "E25.0.8.199", {"start": v(171.85, 135.1) * mm, "end": v(164.66, 139.25) * mm});
            skLineSegment(sketch, "E25.0.8.200", {"start": v(197.4, 149.85) * mm, "end": v(204.59, 154) * mm});
            skLineSegment(sketch, "E25.0.8.201", {"start": v(52.58, 151.7) * mm, "end": v(59.77, 147.55) * mm});
            skLineSegment(sketch, "E25.0.8.202", {"start": v(411.7, 162.3) * mm, "end": v(418.88, 166.45) * mm});
            skLineSegment(sketch, "E25.0.8.203", {"start": v(409.03, 162.3) * mm, "end": v(401.84, 166.45) * mm});
            skLineSegment(sketch, "E25.0.8.204", {"start": v(207.25, 162.3) * mm, "end": v(214.44, 166.45) * mm});
            skLineSegment(sketch, "E25.0.8.205", {"start": v(403.17, 147.55) * mm, "end": v(410.35, 151.7) * mm});
            skLineSegment(sketch, "E25.0.8.206", {"start": v(495.54, 135.1) * mm, "end": v(488.35, 139.25) * mm});
            skLineSegment(sketch, "E25.0.8.207", {"start": v(468.65, 147.55) * mm, "end": v(468.65, 139.25) * mm});
            skLineSegment(sketch, "E25.0.8.208", {"start": v(264.21, 147.55) * mm, "end": v(264.21, 139.25) * mm});
            skLineSegment(sketch, "E25.0.8.209", {"start": v(238.66, 154) * mm, "end": v(238.66, 162.3) * mm});
            skLineSegment(sketch, "E25.0.8.210", {"start": v(247.18, 139.25) * mm, "end": v(240, 135.1) * mm});
            skLineSegment(sketch, "E25.0.8.211", {"start": v(85.33, 154) * mm, "end": v(85.33, 162.3) * mm});
            skLineSegment(sketch, "E25.0.8.212", {"start": v(137.77, 135.1) * mm, "end": v(130.58, 139.25) * mm});
            skLineSegment(sketch, "E25.0.8.213", {"start": v(374.96, 154) * mm, "end": v(367.77, 149.85) * mm});
            skLineSegment(sketch, "E25.0.8.214", {"start": v(323.85, 162.3) * mm, "end": v(323.85, 154) * mm});
            skLineSegment(sketch, "E25.0.8.215", {"start": v(266.88, 147.55) * mm, "end": v(274.07, 151.7) * mm});
            skLineSegment(sketch, "E25.0.8.216", {"start": v(326.5, 162.3) * mm, "end": v(326.5, 154) * mm});
            skLineSegment(sketch, "E25.0.8.217", {"start": v(232.8, 147.55) * mm, "end": v(240, 151.7) * mm});
            skLineSegment(sketch, "E25.0.8.218", {"start": v(306.8, 154) * mm, "end": v(306.8, 162.3) * mm});
            skLineSegment(sketch, "E25.0.8.219", {"start": v(119.4, 162.3) * mm, "end": v(119.4, 154) * mm});
            skLineSegment(sketch, "E25.0.8.220", {"start": v(122.06, 162.3) * mm, "end": v(122.06, 154) * mm});
            skLineSegment(sketch, "E25.0.8.221", {"start": v(170.52, 154) * mm, "end": v(163.33, 149.85) * mm});
            skLineSegment(sketch, "E25.0.8.222", {"start": v(428.72, 162.3) * mm, "end": v(428.72, 154) * mm});
            skLineSegment(sketch, "E25.0.8.223", {"start": v(51.26, 154) * mm, "end": v(51.26, 162.3) * mm});
            skLineSegment(sketch, "E25.0.8.224", {"start": v(386.13, 139.25) * mm, "end": v(386.13, 147.55) * mm});
            skLineSegment(sketch, "E25.0.8.225", {"start": v(44.07, 149.85) * mm, "end": v(51.26, 154) * mm});
            skLineSegment(sketch, "E25.0.8.226", {"start": v(462.8, 162.3) * mm, "end": v(469.99, 166.45) * mm});
            skLineSegment(sketch, "E25.0.8.227", {"start": v(214.44, 149.85) * mm, "end": v(207.25, 154) * mm});
            skLineSegment(sketch, "E25.0.8.228", {"start": v(205.91, 151.7) * mm, "end": v(213.1, 147.55) * mm});
            skLineSegment(sketch, "E25.0.8.229", {"start": v(366.43, 147.55) * mm, "end": v(366.43, 139.25) * mm});
            skLineSegment(sketch, "E25.0.8.230", {"start": v(130.58, 147.55) * mm, "end": v(137.77, 151.7) * mm});
            skLineSegment(sketch, "E25.0.8.231", {"start": v(224.28, 162.3) * mm, "end": v(224.28, 154) * mm});
            skLineSegment(sketch, "E25.0.8.232", {"start": v(384.8, 149.85) * mm, "end": v(392, 154) * mm});
            skLineSegment(sketch, "E25.0.8.233", {"start": v(275.4, 154) * mm, "end": v(282.58, 149.85) * mm});
            skLineSegment(sketch, "E25.0.8.234", {"start": v(19.84, 154) * mm, "end": v(27.03, 149.85) * mm});
            skLineSegment(sketch, "E25.0.8.235", {"start": v(180.36, 149.85) * mm, "end": v(187.55, 154) * mm});
            skLineSegment(sketch, "E25.0.8.236", {"start": v(410.35, 151.7) * mm, "end": v(417.54, 147.55) * mm});
            skLineSegment(sketch, "E25.0.8.237", {"start": v(255.7, 162.3) * mm, "end": v(248.5, 166.45) * mm});
            skLineSegment(sketch, "E25.0.8.238", {"start": v(53.92, 162.3) * mm, "end": v(61.1, 166.45) * mm});
            skLineSegment(sketch, "E25.0.8.239", {"start": v(162, 147.55) * mm, "end": v(162, 139.25) * mm});
            skLineSegment(sketch, "E25.0.8.240", {"start": v(51.26, 162.3) * mm, "end": v(44.07, 166.45) * mm});
            skLineSegment(sketch, "E25.0.8.241", {"start": v(427.4, 151.7) * mm, "end": v(434.59, 147.55) * mm});
            skLineSegment(sketch, "E25.0.8.242", {"start": v(460.14, 162.3) * mm, "end": v(452.95, 166.45) * mm});
            skLineSegment(sketch, "E25.0.8.243", {"start": v(272.74, 154) * mm, "end": v(265.55, 149.85) * mm});
            skLineSegment(sketch, "E25.0.8.244", {"start": v(181.7, 139.25) * mm, "end": v(181.7, 147.55) * mm});
            skLineSegment(sketch, "E25.0.8.245", {"start": v(335.02, 147.55) * mm, "end": v(342.21, 151.7) * mm});
            skLineSegment(sketch, "E25.0.8.246", {"start": v(221.63, 162.3) * mm, "end": v(221.63, 154) * mm});
            skLineSegment(sketch, "E25.0.8.247", {"start": v(68.3, 154) * mm, "end": v(61.1, 149.85) * mm});
            skLineSegment(sketch, "E25.0.8.248", {"start": v(130.58, 139.25) * mm, "end": v(130.58, 147.55) * mm});
            skLineSegment(sketch, "E25.0.8.249", {"start": v(477.18, 154) * mm, "end": v(469.99, 149.85) * mm});
            skLineSegment(sketch, "E25.0.8.250", {"start": v(469.99, 166.45) * mm, "end": v(477.18, 162.3) * mm});
            skLineSegment(sketch, "E25.0.8.251", {"start": v(360.58, 154) * mm, "end": v(360.58, 162.3) * mm});
            skLineSegment(sketch, "E25.0.8.252", {"start": v(122.06, 154) * mm, "end": v(129.25, 149.85) * mm});
            skLineSegment(sketch, "E25.0.8.253", {"start": v(95.18, 149.85) * mm, "end": v(102.37, 154) * mm});
            skLineSegment(sketch, "E25.0.8.254", {"start": v(137.77, 151.7) * mm, "end": v(144.96, 147.55) * mm});
            skLineSegment(sketch, "E25.0.8.255", {"start": v(469.99, 149.85) * mm, "end": v(462.8, 154) * mm});
            skLineSegment(sketch, "E25.0.8.256", {"start": v(417.54, 147.55) * mm, "end": v(417.54, 139.25) * mm});
            skLineSegment(sketch, "E25.0.8.257", {"start": v(120.74, 151.7) * mm, "end": v(127.93, 147.55) * mm});
            skLineSegment(sketch, "E25.0.8.258", {"start": v(477.18, 162.3) * mm, "end": v(477.18, 154) * mm});
            skLineSegment(sketch, "E25.0.8.259", {"start": v(420.2, 147.55) * mm, "end": v(427.4, 151.7) * mm});
            skLineSegment(sketch, "E25.0.8.260", {"start": v(275.4, 162.3) * mm, "end": v(275.4, 154) * mm});
            skLineSegment(sketch, "E25.0.8.261", {"start": v(255.7, 154) * mm, "end": v(255.7, 162.3) * mm});
            skLineSegment(sketch, "E25.0.8.262", {"start": v(215.77, 147.55) * mm, "end": v(222.96, 151.7) * mm});
            skLineSegment(sketch, "E25.0.8.263", {"start": v(42.74, 147.55) * mm, "end": v(42.74, 139.25) * mm});
            skLineSegment(sketch, "E25.0.8.264", {"start": v(350.73, 149.85) * mm, "end": v(357.92, 154) * mm});
            skLineSegment(sketch, "E25.0.8.265", {"start": v(78.14, 149.85) * mm, "end": v(85.33, 154) * mm});
            skLineSegment(sketch, "E25.0.8.266", {"start": v(119.4, 154) * mm, "end": v(112.22, 149.85) * mm});
            skLineSegment(sketch, "E25.0.8.267", {"start": v(19.84, 162.3) * mm, "end": v(19.84, 154) * mm});
            skLineSegment(sketch, "E25.0.8.268", {"start": v(496.87, 154) * mm, "end": v(504.06, 149.85) * mm});
            skLineSegment(sketch, "E25.0.8.269", {"start": v(325.18, 151.7) * mm, "end": v(332.37, 147.55) * mm});
            skLineSegment(sketch, "E25.0.8.270", {"start": v(367.77, 166.45) * mm, "end": v(374.96, 162.3) * mm});
            skLineSegment(sketch, "E25.0.8.271", {"start": v(258.36, 154) * mm, "end": v(258.36, 162.3) * mm});
            skLineSegment(sketch, "E25.0.8.272", {"start": v(163.33, 166.45) * mm, "end": v(170.52, 162.3) * mm});
            skLineSegment(sketch, "E25.0.8.273", {"start": v(179.04, 147.55) * mm, "end": v(179.04, 139.25) * mm});
            skLineSegment(sketch, "E25.0.8.274", {"start": v(249.84, 139.25) * mm, "end": v(249.84, 147.55) * mm});
            skLineSegment(sketch, "E25.0.8.275", {"start": v(139.1, 154) * mm, "end": v(146.29, 149.85) * mm});
            skLineSegment(sketch, "E25.0.8.276", {"start": v(418.88, 149.85) * mm, "end": v(411.7, 154) * mm});
            skLineSegment(sketch, "E25.0.8.277", {"start": v(426.07, 162.3) * mm, "end": v(426.07, 154) * mm});
            skLineSegment(sketch, "E25.0.8.278", {"start": v(367.77, 149.85) * mm, "end": v(360.58, 154) * mm});
            skLineSegment(sketch, "E25.0.8.279", {"start": v(352.06, 147.55) * mm, "end": v(359.24, 151.7) * mm});
            skLineSegment(sketch, "E25.0.8.280", {"start": v(163.33, 149.85) * mm, "end": v(156.14, 154) * mm});
            skLineSegment(sketch, "E25.0.8.281", {"start": v(112.22, 149.85) * mm, "end": v(105.03, 154) * mm});
            skLineSegment(sketch, "E25.0.8.282", {"start": v(487.02, 166.45) * mm, "end": v(479.83, 162.3) * mm});
            skLineSegment(sketch, "E25.0.8.283", {"start": v(374.96, 162.3) * mm, "end": v(374.96, 154) * mm});
            skLineSegment(sketch, "E25.0.8.284", {"start": v(17.19, 154) * mm, "end": v(10, 149.85) * mm});
            skLineSegment(sketch, "E25.0.8.285", {"start": v(221.63, 154) * mm, "end": v(214.44, 149.85) * mm});
            skLineSegment(sketch, "E25.0.8.286", {"start": v(282.58, 166.45) * mm, "end": v(275.4, 162.3) * mm});
            skLineSegment(sketch, "E25.0.8.287", {"start": v(335.02, 139.25) * mm, "end": v(335.02, 147.55) * mm});
            skLineSegment(sketch, "E25.0.8.288", {"start": v(170.52, 162.3) * mm, "end": v(170.52, 154) * mm});
            skLineSegment(sketch, "E25.0.8.289", {"start": v(291.1, 151.7) * mm, "end": v(298.29, 147.55) * mm});
            skLineSegment(sketch, "E25.0.8.290", {"start": v(173.17, 162.3) * mm, "end": v(173.17, 154) * mm});
            skLineSegment(sketch, "E25.0.8.291", {"start": v(495.54, 151.7) * mm, "end": v(502.73, 147.55) * mm});
            skLineSegment(sketch, "E25.0.8.292", {"start": v(147.62, 139.25) * mm, "end": v(147.62, 147.55) * mm});
            skLineSegment(sketch, "E25.0.8.293", {"start": v(153.48, 154) * mm, "end": v(153.48, 162.3) * mm});
            skLineSegment(sketch, "E25.0.8.294", {"start": v(222.96, 151.7) * mm, "end": v(230.15, 147.55) * mm});
            skLineSegment(sketch, "E25.0.8.295", {"start": v(479.83, 162.3) * mm, "end": v(479.83, 154) * mm});
            skLineSegment(sketch, "E25.0.8.296", {"start": v(420.2, 139.25) * mm, "end": v(420.2, 147.55) * mm});
            skLineSegment(sketch, "E25.0.8.297", {"start": v(326.5, 154) * mm, "end": v(333.7, 149.85) * mm});
            skLineSegment(sketch, "E25.0.8.298", {"start": v(173.17, 154) * mm, "end": v(180.36, 149.85) * mm});
            skLineSegment(sketch, "E25.0.8.299", {"start": v(342.21, 151.7) * mm, "end": v(349.4, 147.55) * mm});
            skLineSegment(sketch, "E25.0.8.300", {"start": v(265.55, 166.45) * mm, "end": v(272.74, 162.3) * mm});
            skLineSegment(sketch, "E25.0.8.301", {"start": v(274.07, 151.7) * mm, "end": v(281.26, 147.55) * mm});
            skLineSegment(sketch, "E25.0.8.302", {"start": v(215.77, 139.25) * mm, "end": v(215.77, 147.55) * mm});
            skLineSegment(sketch, "E25.0.8.303", {"start": v(462.8, 154) * mm, "end": v(462.8, 162.3) * mm});
            skLineSegment(sketch, "E25.0.8.304", {"start": v(281.26, 147.55) * mm, "end": v(281.26, 139.25) * mm});
            skLineSegment(sketch, "E25.0.8.305", {"start": v(156.14, 154) * mm, "end": v(156.14, 162.3) * mm});
            skLineSegment(sketch, "E25.0.8.306", {"start": v(213.1, 147.55) * mm, "end": v(213.1, 139.25) * mm});
            skLineSegment(sketch, "E25.0.8.307", {"start": v(96.5, 147.55) * mm, "end": v(103.7, 151.7) * mm});
            skLineSegment(sketch, "E25.0.8.308", {"start": v(460.14, 154) * mm, "end": v(460.14, 162.3) * mm});
            skLineSegment(sketch, "E25.0.8.309", {"start": v(323.85, 154) * mm, "end": v(316.66, 149.85) * mm});
            skLineSegment(sketch, "E25.0.8.310", {"start": v(272.74, 162.3) * mm, "end": v(272.74, 154) * mm});
            skLineSegment(sketch, "E25.0.8.311", {"start": v(377.61, 154) * mm, "end": v(384.8, 149.85) * mm});
            skLineSegment(sketch, "E25.0.8.312", {"start": v(282.58, 149.85) * mm, "end": v(289.77, 154) * mm});
            skLineSegment(sketch, "E25.0.8.313", {"start": v(146.29, 149.85) * mm, "end": v(153.48, 154) * mm});
            skLineSegment(sketch, "E25.0.8.314", {"start": v(343.54, 154) * mm, "end": v(350.73, 149.85) * mm});
            skLineSegment(sketch, "E25.0.8.315", {"start": v(376.29, 151.7) * mm, "end": v(383.48, 147.55) * mm});
            skLineSegment(sketch, "E25.0.8.316", {"start": v(171.85, 151.7) * mm, "end": v(179.04, 147.55) * mm});
            skLineSegment(sketch, "E25.0.8.317", {"start": v(53.92, 154) * mm, "end": v(53.92, 162.3) * mm});
            skLineSegment(sketch, "E25.0.8.318", {"start": v(292.43, 154) * mm, "end": v(299.62, 149.85) * mm});
            skLineSegment(sketch, "E25.0.8.319", {"start": v(377.61, 162.3) * mm, "end": v(377.61, 154) * mm});
            skLineSegment(sketch, "E25.0.8.320", {"start": v(383.48, 147.55) * mm, "end": v(383.48, 139.25) * mm});
            skLineSegment(sketch, "E25.0.8.321", {"start": v(129.25, 149.85) * mm, "end": v(136.44, 154) * mm});
            skLineSegment(sketch, "E25.0.8.322", {"start": v(428.72, 154) * mm, "end": v(435.91, 149.85) * mm});
            skLineSegment(sketch, "E25.0.8.323", {"start": v(496.87, 162.3) * mm, "end": v(496.87, 154) * mm});
            skLineSegment(sketch, "E25.0.8.324", {"start": v(224.28, 154) * mm, "end": v(231.47, 149.85) * mm});
            skLineSegment(sketch, "E25.0.8.325", {"start": v(333.7, 149.85) * mm, "end": v(340.88, 154) * mm});
            skLineSegment(sketch, "E25.0.8.326", {"start": v(11.33, 147.55) * mm, "end": v(18.52, 151.7) * mm});
            skLineSegment(sketch, "E25.0.8.327", {"start": v(18.52, 151.7) * mm, "end": v(25.7, 147.55) * mm});
            skLineSegment(sketch, "E25.0.8.328", {"start": v(494.21, 154) * mm, "end": v(494.21, 162.3) * mm});
            skLineSegment(sketch, "E25.0.8.329", {"start": v(315.32, 147.55) * mm, "end": v(315.32, 139.25) * mm});
            skLineSegment(sketch, "E25.0.8.330", {"start": v(360.58, 162.3) * mm, "end": v(367.77, 166.45) * mm});
            skLineSegment(sketch, "E25.0.8.331", {"start": v(316.66, 149.85) * mm, "end": v(309.47, 154) * mm});
            skLineSegment(sketch, "E25.0.8.332", {"start": v(308.13, 151.7) * mm, "end": v(315.32, 147.55) * mm});
            skLineSegment(sketch, "E25.0.8.333", {"start": v(147.62, 147.55) * mm, "end": v(154.8, 151.7) * mm});
            skLineSegment(sketch, "E25.0.8.334", {"start": v(359.24, 151.7) * mm, "end": v(366.43, 147.55) * mm});
            skLineSegment(sketch, "E25.0.8.335", {"start": v(110.88, 147.55) * mm, "end": v(110.88, 139.25) * mm});
            skLineSegment(sketch, "E25.0.8.336", {"start": v(154.8, 151.7) * mm, "end": v(162, 147.55) * mm});
            skLineSegment(sketch, "E25.0.8.337", {"start": v(17.19, 162.3) * mm, "end": v(17.19, 154) * mm});
            skLineSegment(sketch, "E25.0.8.338", {"start": v(156.14, 162.3) * mm, "end": v(163.33, 166.45) * mm});
            skLineSegment(sketch, "E25.0.8.339", {"start": v(103.7, 151.7) * mm, "end": v(110.88, 147.55) * mm});
            skLineSegment(sketch, "E25.0.8.340", {"start": v(471.32, 147.55) * mm, "end": v(478.5, 151.7) * mm});
            skLineSegment(sketch, "E25.0.8.341", {"start": v(426.07, 154) * mm, "end": v(418.88, 149.85) * mm});
            skLineSegment(sketch, "E25.0.8.342", {"start": v(357.92, 154) * mm, "end": v(357.92, 162.3) * mm});
            skLineSegment(sketch, "E25.0.8.343", {"start": v(317.99, 147.55) * mm, "end": v(325.18, 151.7) * mm});
            skLineSegment(sketch, "E25.0.8.344", {"start": v(258.36, 162.3) * mm, "end": v(265.55, 166.45) * mm});
            skLineSegment(sketch, "E25.0.8.345", {"start": v(283.91, 139.25) * mm, "end": v(283.91, 147.55) * mm});
            skLineSegment(sketch, "E25.0.8.346", {"start": v(283.91, 147.55) * mm, "end": v(291.1, 151.7) * mm});
            skLineSegment(sketch, "E25.0.8.347", {"start": v(113.55, 147.55) * mm, "end": v(120.74, 151.7) * mm});
            skLineSegment(sketch, "E25.0.8.348", {"start": v(36.88, 154) * mm, "end": v(44.07, 149.85) * mm});
            skLineSegment(sketch, "E25.0.8.349", {"start": v(36.88, 162.3) * mm, "end": v(36.88, 154) * mm});
            skLineSegment(sketch, "E25.0.8.350", {"start": v(34.22, 154) * mm, "end": v(34.22, 162.3) * mm});
            skLineSegment(sketch, "E25.0.8.351", {"start": v(485.7, 147.55) * mm, "end": v(485.7, 139.25) * mm});
            skLineSegment(sketch, "E25.0.8.352", {"start": v(478.5, 151.7) * mm, "end": v(485.7, 147.55) * mm});
            skLineSegment(sketch, "E25.0.8.353", {"start": v(487.02, 149.85) * mm, "end": v(494.21, 154) * mm});
            skLineSegment(sketch, "E25.0.8.354", {"start": v(27.03, 149.85) * mm, "end": v(34.22, 154) * mm});
            skLineSegment(sketch, "E25.0.8.355", {"start": v(479.83, 154) * mm, "end": v(487.02, 149.85) * mm});
            skLineSegment(sketch, "E25.0.8.356", {"start": v(28.36, 147.55) * mm, "end": v(35.55, 151.7) * mm});
            skLineSegment(sketch, "E25.0.8.357", {"start": v(35.55, 151.7) * mm, "end": v(42.74, 147.55) * mm});
            skLineSegment(sketch, "E25.0.8.358", {"start": v(488.35, 147.55) * mm, "end": v(495.54, 151.7) * mm});
            skLineSegment(sketch, "E25.0.8.359", {"start": v(488.35, 139.25) * mm, "end": v(488.35, 147.55) * mm});
            skLineSegment(sketch, "E25.direction1", {"start": v(11.33, 375.25) * mm, "end": v(36.33, 375.25) * mm, "construction": true});
            skLineSegment(sketch, "E25.direction2", {"start": v(11.33, 375.25) * mm, "end": v(11.33, 345.75) * mm, "construction": true});
            skLineSegment(sketch, "E26.0.1.0", {"start": v(2.81, 124.5) * mm, "end": v(2.81, 132.8) * mm});
            skLineSegment(sketch, "E26.0.1.1", {"start": v(511.25, 124.5) * mm, "end": v(511.25, 132.8) * mm});
            skLineSegment(sketch, "E26.0.1.2", {"start": v(120.74, 105.6) * mm, "end": v(113.55, 109.75) * mm});
            skLineSegment(sketch, "E26.0.1.3", {"start": v(240, 105.6) * mm, "end": v(232.8, 109.75) * mm});
            skLineSegment(sketch, "E26.0.1.4", {"start": v(519.76, 109.75) * mm, "end": v(512.57, 105.6) * mm});
            skLineSegment(sketch, "E26.0.1.5", {"start": v(18.52, 105.6) * mm, "end": v(11.33, 109.75) * mm});
            skLineSegment(sketch, "E26.0.1.6", {"start": v(383.48, 109.75) * mm, "end": v(376.29, 105.6) * mm});
            skLineSegment(sketch, "E26.0.1.7", {"start": v(274.07, 105.6) * mm, "end": v(266.88, 109.75) * mm});
            skLineSegment(sketch, "E26.0.1.8", {"start": v(315.32, 109.75) * mm, "end": v(308.13, 105.6) * mm});
            skLineSegment(sketch, "E26.0.1.9", {"start": v(86.66, 105.6) * mm, "end": v(79.47, 109.75) * mm});
            skLineSegment(sketch, "E26.0.1.10", {"start": v(10, 120.35) * mm, "end": v(2.81, 124.5) * mm});
            skLineSegment(sketch, "E26.0.1.11", {"start": v(247.18, 109.75) * mm, "end": v(240, 105.6) * mm});
            skLineSegment(sketch, "E26.0.1.12", {"start": v(325.18, 105.6) * mm, "end": v(317.99, 109.75) * mm});
            skLineSegment(sketch, "E26.0.1.13", {"start": v(257.02, 105.6) * mm, "end": v(249.84, 109.75) * mm});
            skLineSegment(sketch, "E26.0.1.14", {"start": v(35.55, 105.6) * mm, "end": v(28.36, 109.75) * mm});
            skLineSegment(sketch, "E26.0.1.15", {"start": v(127.93, 109.75) * mm, "end": v(120.74, 105.6) * mm});
            skLineSegment(sketch, "E26.0.1.16", {"start": v(196.07, 109.75) * mm, "end": v(188.88, 105.6) * mm});
            skLineSegment(sketch, "E26.0.1.17", {"start": v(308.13, 105.6) * mm, "end": v(300.95, 109.75) * mm});
            skLineSegment(sketch, "E26.0.1.18", {"start": v(298.29, 109.75) * mm, "end": v(291.1, 105.6) * mm});
            skLineSegment(sketch, "E26.0.1.19", {"start": v(332.37, 109.75) * mm, "end": v(325.18, 105.6) * mm});
            skLineSegment(sketch, "E26.0.1.20", {"start": v(11.33, 109.75) * mm, "end": v(11.33, 118.05) * mm});
            skLineSegment(sketch, "E26.0.1.21", {"start": v(519.76, 118.05) * mm, "end": v(519.76, 109.75) * mm});
            skLineSegment(sketch, "E26.0.1.22", {"start": v(461.46, 105.6) * mm, "end": v(454.28, 109.75) * mm});
            skLineSegment(sketch, "E26.0.1.23", {"start": v(230.15, 109.75) * mm, "end": v(222.96, 105.6) * mm});
            skLineSegment(sketch, "E26.0.1.24", {"start": v(300.95, 109.75) * mm, "end": v(300.95, 118.05) * mm});
            skLineSegment(sketch, "E26.0.1.25", {"start": v(42.74, 109.75) * mm, "end": v(35.55, 105.6) * mm});
            skLineSegment(sketch, "E26.0.1.26", {"start": v(17.19, 124.5) * mm, "end": v(10, 120.35) * mm});
            skLineSegment(sketch, "E26.0.1.27", {"start": v(34.22, 124.5) * mm, "end": v(34.22, 132.8) * mm});
            skLineSegment(sketch, "E26.0.1.28", {"start": v(512.57, 122.2) * mm, "end": v(519.76, 118.05) * mm});
            skLineSegment(sketch, "E26.0.1.29", {"start": v(376.29, 105.6) * mm, "end": v(369.1, 109.75) * mm});
            skLineSegment(sketch, "E26.0.1.30", {"start": v(292.43, 124.5) * mm, "end": v(299.62, 120.35) * mm});
            skLineSegment(sketch, "E26.0.1.31", {"start": v(468.65, 118.05) * mm, "end": v(468.65, 109.75) * mm});
            skLineSegment(sketch, "E26.0.1.32", {"start": v(11.33, 118.05) * mm, "end": v(18.52, 122.2) * mm});
            skLineSegment(sketch, "E26.0.1.33", {"start": v(377.61, 132.8) * mm, "end": v(377.61, 124.5) * mm});
            skLineSegment(sketch, "E26.0.1.34", {"start": v(366.43, 118.05) * mm, "end": v(366.43, 109.75) * mm});
            skLineSegment(sketch, "E26.0.1.35", {"start": v(255.7, 124.5) * mm, "end": v(255.7, 132.8) * mm});
            skLineSegment(sketch, "E26.0.1.36", {"start": v(495.54, 105.6) * mm, "end": v(488.35, 109.75) * mm});
            skLineSegment(sketch, "E26.0.1.37", {"start": v(105.03, 124.5) * mm, "end": v(105.03, 132.8) * mm});
            skLineSegment(sketch, "E26.0.1.38", {"start": v(162, 109.75) * mm, "end": v(154.8, 105.6) * mm});
            skLineSegment(sketch, "E26.0.1.39", {"start": v(93.85, 109.75) * mm, "end": v(86.66, 105.6) * mm});
            skLineSegment(sketch, "E26.0.1.40", {"start": v(25.7, 109.75) * mm, "end": v(18.52, 105.6) * mm});
            skLineSegment(sketch, "E26.0.1.41", {"start": v(110.88, 109.75) * mm, "end": v(103.7, 105.6) * mm});
            skLineSegment(sketch, "E26.0.1.42", {"start": v(281.26, 109.75) * mm, "end": v(274.07, 105.6) * mm});
            skLineSegment(sketch, "E26.0.1.43", {"start": v(171.85, 105.6) * mm, "end": v(164.66, 109.75) * mm});
            skLineSegment(sketch, "E26.0.1.44", {"start": v(298.29, 118.05) * mm, "end": v(298.29, 109.75) * mm});
            skLineSegment(sketch, "E26.0.1.45", {"start": v(281.26, 118.05) * mm, "end": v(281.26, 109.75) * mm});
            skLineSegment(sketch, "E26.0.1.46", {"start": v(374.96, 132.8) * mm, "end": v(374.96, 124.5) * mm});
            skLineSegment(sketch, "E26.0.1.47", {"start": v(502.73, 109.75) * mm, "end": v(495.54, 105.6) * mm});
            skLineSegment(sketch, "E26.0.1.48", {"start": v(144.96, 109.75) * mm, "end": v(137.77, 105.6) * mm});
            skLineSegment(sketch, "E26.0.1.49", {"start": v(76.82, 118.05) * mm, "end": v(76.82, 109.75) * mm});
            skLineSegment(sketch, "E26.0.1.50", {"start": v(102.37, 124.5) * mm, "end": v(102.37, 132.8) * mm});
            skLineSegment(sketch, "E26.0.1.51", {"start": v(179.04, 109.75) * mm, "end": v(171.85, 105.6) * mm});
            skLineSegment(sketch, "E26.0.1.52", {"start": v(52.58, 105.6) * mm, "end": v(45.4, 109.75) * mm});
            skLineSegment(sketch, "E26.0.1.53", {"start": v(17.19, 132.8) * mm, "end": v(17.19, 124.5) * mm});
            skLineSegment(sketch, "E26.0.1.54", {"start": v(205.91, 105.6) * mm, "end": v(198.73, 109.75) * mm});
            skLineSegment(sketch, "E26.0.1.55", {"start": v(154.8, 105.6) * mm, "end": v(147.62, 109.75) * mm});
            skLineSegment(sketch, "E26.0.1.56", {"start": v(299.62, 120.35) * mm, "end": v(306.8, 124.5) * mm});
            skLineSegment(sketch, "E26.0.1.57", {"start": v(306.8, 124.5) * mm, "end": v(306.8, 132.8) * mm});
            skLineSegment(sketch, "E26.0.1.58", {"start": v(291.1, 122.2) * mm, "end": v(298.29, 118.05) * mm});
            skLineSegment(sketch, "E26.0.1.59", {"start": v(213.1, 109.75) * mm, "end": v(205.91, 105.6) * mm});
            skLineSegment(sketch, "E26.0.1.60", {"start": v(238.66, 124.5) * mm, "end": v(238.66, 132.8) * mm});
            skLineSegment(sketch, "E26.0.1.61", {"start": v(76.82, 109.75) * mm, "end": v(69.63, 105.6) * mm});
            skLineSegment(sketch, "E26.0.1.62", {"start": v(434.59, 109.75) * mm, "end": v(427.4, 105.6) * mm});
            skLineSegment(sketch, "E26.0.1.63", {"start": v(309.47, 124.5) * mm, "end": v(309.47, 132.8) * mm});
            skLineSegment(sketch, "E26.0.1.64", {"start": v(366.43, 109.75) * mm, "end": v(359.24, 105.6) * mm});
            skLineSegment(sketch, "E26.0.1.65", {"start": v(468.65, 109.75) * mm, "end": v(461.46, 105.6) * mm});
            skLineSegment(sketch, "E26.0.1.66", {"start": v(478.5, 105.6) * mm, "end": v(471.32, 109.75) * mm});
            skLineSegment(sketch, "E26.0.1.67", {"start": v(222.96, 105.6) * mm, "end": v(215.77, 109.75) * mm});
            skLineSegment(sketch, "E26.0.1.68", {"start": v(512.57, 105.6) * mm, "end": v(505.39, 109.75) * mm});
            skLineSegment(sketch, "E26.0.1.69", {"start": v(427.4, 105.6) * mm, "end": v(420.2, 109.75) * mm});
            skLineSegment(sketch, "E26.0.1.70", {"start": v(291.1, 105.6) * mm, "end": v(283.91, 109.75) * mm});
            skLineSegment(sketch, "E26.0.1.71", {"start": v(444.43, 105.6) * mm, "end": v(437.24, 109.75) * mm});
            skLineSegment(sketch, "E26.0.1.72", {"start": v(369.1, 109.75) * mm, "end": v(369.1, 118.05) * mm});
            skLineSegment(sketch, "E26.0.1.73", {"start": v(188.88, 105.6) * mm, "end": v(181.7, 109.75) * mm});
            skLineSegment(sketch, "E26.0.1.74", {"start": v(79.47, 109.75) * mm, "end": v(79.47, 118.05) * mm});
            skLineSegment(sketch, "E26.0.1.75", {"start": v(264.21, 109.75) * mm, "end": v(257.02, 105.6) * mm});
            skLineSegment(sketch, "E26.0.1.76", {"start": v(485.7, 109.75) * mm, "end": v(478.5, 105.6) * mm});
            skLineSegment(sketch, "E26.0.1.77", {"start": v(241.32, 132.8) * mm, "end": v(241.32, 124.5) * mm});
            skLineSegment(sketch, "E26.0.1.78", {"start": v(283.91, 109.75) * mm, "end": v(283.91, 118.05) * mm});
            skLineSegment(sketch, "E26.0.1.79", {"start": v(496.87, 132.8) * mm, "end": v(496.87, 124.5) * mm});
            skLineSegment(sketch, "E26.0.1.80", {"start": v(122.06, 132.8) * mm, "end": v(122.06, 124.5) * mm});
            skLineSegment(sketch, "E26.0.1.81", {"start": v(96.5, 118.05) * mm, "end": v(103.7, 122.2) * mm});
            skLineSegment(sketch, "E26.0.1.82", {"start": v(308.13, 122.2) * mm, "end": v(315.32, 118.05) * mm});
            skLineSegment(sketch, "E26.0.1.83", {"start": v(113.55, 118.05) * mm, "end": v(120.74, 122.2) * mm});
            skLineSegment(sketch, "E26.0.1.84", {"start": v(190.2, 124.5) * mm, "end": v(197.4, 120.35) * mm});
            skLineSegment(sketch, "E26.0.1.85", {"start": v(249.84, 109.75) * mm, "end": v(249.84, 118.05) * mm});
            skLineSegment(sketch, "E26.0.1.86", {"start": v(230.15, 118.05) * mm, "end": v(230.15, 109.75) * mm});
            skLineSegment(sketch, "E26.0.1.87", {"start": v(411.7, 124.5) * mm, "end": v(411.7, 132.8) * mm});
            skLineSegment(sketch, "E26.0.1.88", {"start": v(221.63, 132.8) * mm, "end": v(221.63, 124.5) * mm});
            skLineSegment(sketch, "E26.0.1.89", {"start": v(130.58, 118.05) * mm, "end": v(137.77, 122.2) * mm});
            skLineSegment(sketch, "E26.0.1.90", {"start": v(323.85, 132.8) * mm, "end": v(323.85, 124.5) * mm});
            skLineSegment(sketch, "E26.0.1.91", {"start": v(258.36, 124.5) * mm, "end": v(258.36, 132.8) * mm});
            skLineSegment(sketch, "E26.0.1.92", {"start": v(215.77, 118.05) * mm, "end": v(222.96, 122.2) * mm});
            skLineSegment(sketch, "E26.0.1.93", {"start": v(272.74, 132.8) * mm, "end": v(272.74, 124.5) * mm});
            skLineSegment(sketch, "E26.0.1.94", {"start": v(35.55, 122.2) * mm, "end": v(42.74, 118.05) * mm});
            skLineSegment(sketch, "E26.0.1.95", {"start": v(215.77, 109.75) * mm, "end": v(215.77, 118.05) * mm});
            skLineSegment(sketch, "E26.0.1.96", {"start": v(292.43, 132.8) * mm, "end": v(292.43, 124.5) * mm});
            skLineSegment(sketch, "E26.0.1.97", {"start": v(359.24, 122.2) * mm, "end": v(366.43, 118.05) * mm});
            skLineSegment(sketch, "E26.0.1.98", {"start": v(367.77, 120.35) * mm, "end": v(360.58, 124.5) * mm});
            skLineSegment(sketch, "E26.0.1.99", {"start": v(335.02, 109.75) * mm, "end": v(335.02, 118.05) * mm});
            skLineSegment(sketch, "E26.0.1.100", {"start": v(462.8, 124.5) * mm, "end": v(462.8, 132.8) * mm});
            skLineSegment(sketch, "E26.0.1.101", {"start": v(485.7, 118.05) * mm, "end": v(485.7, 109.75) * mm});
            skLineSegment(sketch, "E26.0.1.102", {"start": v(153.48, 124.5) * mm, "end": v(153.48, 132.8) * mm});
            skLineSegment(sketch, "E26.0.1.103", {"start": v(51.26, 124.5) * mm, "end": v(51.26, 132.8) * mm});
            skLineSegment(sketch, "E26.0.1.104", {"start": v(162, 118.05) * mm, "end": v(162, 109.75) * mm});
            skLineSegment(sketch, "E26.0.1.105", {"start": v(222.96, 122.2) * mm, "end": v(230.15, 118.05) * mm});
            skLineSegment(sketch, "E26.0.1.106", {"start": v(357.92, 124.5) * mm, "end": v(357.92, 132.8) * mm});
            skLineSegment(sketch, "E26.0.1.107", {"start": v(488.35, 118.05) * mm, "end": v(495.54, 122.2) * mm});
            skLineSegment(sketch, "E26.0.1.108", {"start": v(374.96, 124.5) * mm, "end": v(367.77, 120.35) * mm});
            skLineSegment(sketch, "E26.0.1.109", {"start": v(471.32, 109.75) * mm, "end": v(471.32, 118.05) * mm});
            skLineSegment(sketch, "E26.0.1.110", {"start": v(335.02, 118.05) * mm, "end": v(342.21, 122.2) * mm});
            skLineSegment(sketch, "E26.0.1.111", {"start": v(340.88, 124.5) * mm, "end": v(340.88, 132.8) * mm});
            skLineSegment(sketch, "E26.0.1.112", {"start": v(401.84, 120.35) * mm, "end": v(409.03, 124.5) * mm});
            skLineSegment(sketch, "E26.0.1.113", {"start": v(428.72, 132.8) * mm, "end": v(428.72, 124.5) * mm});
            skLineSegment(sketch, "E26.0.1.114", {"start": v(426.07, 132.8) * mm, "end": v(426.07, 124.5) * mm});
            skLineSegment(sketch, "E26.0.1.115", {"start": v(333.7, 120.35) * mm, "end": v(340.88, 124.5) * mm});
            skLineSegment(sketch, "E26.0.1.116", {"start": v(451.62, 109.75) * mm, "end": v(444.43, 105.6) * mm});
            skLineSegment(sketch, "E26.0.1.117", {"start": v(393.32, 105.6) * mm, "end": v(386.13, 109.75) * mm});
            skLineSegment(sketch, "E26.0.1.118", {"start": v(300.95, 118.05) * mm, "end": v(308.13, 122.2) * mm});
            skLineSegment(sketch, "E26.0.1.119", {"start": v(59.77, 109.75) * mm, "end": v(52.58, 105.6) * mm});
            skLineSegment(sketch, "E26.0.1.120", {"start": v(86.66, 122.2) * mm, "end": v(93.85, 118.05) * mm});
            skLineSegment(sketch, "E26.0.1.121", {"start": v(198.73, 109.75) * mm, "end": v(198.73, 118.05) * mm});
            skLineSegment(sketch, "E26.0.1.122", {"start": v(164.66, 118.05) * mm, "end": v(171.85, 122.2) * mm});
            skLineSegment(sketch, "E26.0.1.123", {"start": v(349.4, 109.75) * mm, "end": v(342.21, 105.6) * mm});
            skLineSegment(sketch, "E26.0.1.124", {"start": v(435.91, 120.35) * mm, "end": v(443.1, 124.5) * mm});
            skLineSegment(sketch, "E26.0.1.125", {"start": v(332.37, 118.05) * mm, "end": v(332.37, 109.75) * mm});
            skLineSegment(sketch, "E26.0.1.126", {"start": v(69.63, 122.2) * mm, "end": v(76.82, 118.05) * mm});
            skLineSegment(sketch, "E26.0.1.127", {"start": v(394.65, 132.8) * mm, "end": v(394.65, 124.5) * mm});
            skLineSegment(sketch, "E26.0.1.128", {"start": v(36.88, 132.8) * mm, "end": v(36.88, 124.5) * mm});
            skLineSegment(sketch, "E26.0.1.129", {"start": v(147.62, 109.75) * mm, "end": v(147.62, 118.05) * mm});
            skLineSegment(sketch, "E26.0.1.130", {"start": v(170.52, 124.5) * mm, "end": v(163.33, 120.35) * mm});
            skLineSegment(sketch, "E26.0.1.131", {"start": v(224.28, 132.8) * mm, "end": v(224.28, 124.5) * mm});
            skLineSegment(sketch, "E26.0.1.132", {"start": v(266.88, 118.05) * mm, "end": v(274.07, 122.2) * mm});
            skLineSegment(sketch, "E26.0.1.133", {"start": v(221.63, 124.5) * mm, "end": v(214.44, 120.35) * mm});
            skLineSegment(sketch, "E26.0.1.134", {"start": v(471.32, 118.05) * mm, "end": v(478.5, 122.2) * mm});
            skLineSegment(sketch, "E26.0.1.135", {"start": v(53.92, 124.5) * mm, "end": v(53.92, 132.8) * mm});
            skLineSegment(sketch, "E26.0.1.136", {"start": v(460.14, 124.5) * mm, "end": v(460.14, 132.8) * mm});
            skLineSegment(sketch, "E26.0.1.137", {"start": v(154.8, 122.2) * mm, "end": v(162, 118.05) * mm});
            skLineSegment(sketch, "E26.0.1.138", {"start": v(181.7, 109.75) * mm, "end": v(181.7, 118.05) * mm});
            skLineSegment(sketch, "E26.0.1.139", {"start": v(274.07, 122.2) * mm, "end": v(281.26, 118.05) * mm});
            skLineSegment(sketch, "E26.0.1.140", {"start": v(28.36, 118.05) * mm, "end": v(35.55, 122.2) * mm});
            skLineSegment(sketch, "E26.0.1.141", {"start": v(137.77, 105.6) * mm, "end": v(130.58, 109.75) * mm});
            skLineSegment(sketch, "E26.0.1.142", {"start": v(479.83, 132.8) * mm, "end": v(479.83, 124.5) * mm});
            skLineSegment(sketch, "E26.0.1.143", {"start": v(275.4, 132.8) * mm, "end": v(275.4, 124.5) * mm});
            skLineSegment(sketch, "E26.0.1.144", {"start": v(170.52, 132.8) * mm, "end": v(170.52, 124.5) * mm});
            skLineSegment(sketch, "E26.0.1.145", {"start": v(377.61, 124.5) * mm, "end": v(384.8, 120.35) * mm});
            skLineSegment(sketch, "E26.0.1.146", {"start": v(434.59, 118.05) * mm, "end": v(434.59, 109.75) * mm});
            skLineSegment(sketch, "E26.0.1.147", {"start": v(18.52, 122.2) * mm, "end": v(25.7, 118.05) * mm});
            skLineSegment(sketch, "E26.0.1.148", {"start": v(224.28, 124.5) * mm, "end": v(231.47, 120.35) * mm});
            skLineSegment(sketch, "E26.0.1.149", {"start": v(325.18, 122.2) * mm, "end": v(332.37, 118.05) * mm});
            skLineSegment(sketch, "E26.0.1.150", {"start": v(95.18, 120.35) * mm, "end": v(102.37, 124.5) * mm});
            skLineSegment(sketch, "E26.0.1.151", {"start": v(488.35, 109.75) * mm, "end": v(488.35, 118.05) * mm});
            skLineSegment(sketch, "E26.0.1.152", {"start": v(376.29, 122.2) * mm, "end": v(383.48, 118.05) * mm});
            skLineSegment(sketch, "E26.0.1.153", {"start": v(316.66, 120.35) * mm, "end": v(309.47, 124.5) * mm});
            skLineSegment(sketch, "E26.0.1.154", {"start": v(127.93, 118.05) * mm, "end": v(127.93, 109.75) * mm});
            skLineSegment(sketch, "E26.0.1.155", {"start": v(479.83, 124.5) * mm, "end": v(487.02, 120.35) * mm});
            skLineSegment(sketch, "E26.0.1.156", {"start": v(326.5, 124.5) * mm, "end": v(333.7, 120.35) * mm});
            skLineSegment(sketch, "E26.0.1.157", {"start": v(171.85, 122.2) * mm, "end": v(179.04, 118.05) * mm});
            skLineSegment(sketch, "E26.0.1.158", {"start": v(247.18, 118.05) * mm, "end": v(247.18, 109.75) * mm});
            skLineSegment(sketch, "E26.0.1.159", {"start": v(69.63, 105.6) * mm, "end": v(62.44, 109.75) * mm});
            skLineSegment(sketch, "E26.0.1.160", {"start": v(452.95, 120.35) * mm, "end": v(460.14, 124.5) * mm});
            skLineSegment(sketch, "E26.0.1.161", {"start": v(275.4, 124.5) * mm, "end": v(282.58, 120.35) * mm});
            skLineSegment(sketch, "E26.0.1.162", {"start": v(232.8, 118.05) * mm, "end": v(240, 122.2) * mm});
            skLineSegment(sketch, "E26.0.1.163", {"start": v(122.06, 124.5) * mm, "end": v(129.25, 120.35) * mm});
            skLineSegment(sketch, "E26.0.1.164", {"start": v(417.54, 109.75) * mm, "end": v(410.35, 105.6) * mm});
            skLineSegment(sketch, "E26.0.1.165", {"start": v(139.1, 132.8) * mm, "end": v(139.1, 124.5) * mm});
            skLineSegment(sketch, "E26.0.1.166", {"start": v(443.1, 124.5) * mm, "end": v(443.1, 132.8) * mm});
            skLineSegment(sketch, "E26.0.1.167", {"start": v(232.8, 109.75) * mm, "end": v(232.8, 118.05) * mm});
            skLineSegment(sketch, "E26.0.1.168", {"start": v(61.1, 120.35) * mm, "end": v(53.92, 124.5) * mm});
            skLineSegment(sketch, "E26.0.1.169", {"start": v(437.24, 118.05) * mm, "end": v(444.43, 122.2) * mm});
            skLineSegment(sketch, "E26.0.1.170", {"start": v(78.14, 120.35) * mm, "end": v(85.33, 124.5) * mm});
            skLineSegment(sketch, "E26.0.1.171", {"start": v(85.33, 124.5) * mm, "end": v(85.33, 132.8) * mm});
            skLineSegment(sketch, "E26.0.1.172", {"start": v(445.76, 124.5) * mm, "end": v(452.95, 120.35) * mm});
            skLineSegment(sketch, "E26.0.1.173", {"start": v(240, 122.2) * mm, "end": v(247.18, 118.05) * mm});
            skLineSegment(sketch, "E26.0.1.174", {"start": v(477.18, 124.5) * mm, "end": v(469.99, 120.35) * mm});
            skLineSegment(sketch, "E26.0.1.175", {"start": v(451.62, 118.05) * mm, "end": v(451.62, 109.75) * mm});
            skLineSegment(sketch, "E26.0.1.176", {"start": v(129.25, 120.35) * mm, "end": v(136.44, 124.5) * mm});
            skLineSegment(sketch, "E26.0.1.177", {"start": v(87.99, 132.8) * mm, "end": v(87.99, 124.5) * mm});
            skLineSegment(sketch, "E26.0.1.178", {"start": v(52.58, 122.2) * mm, "end": v(59.77, 118.05) * mm});
            skLineSegment(sketch, "E26.0.1.179", {"start": v(70.95, 124.5) * mm, "end": v(78.14, 120.35) * mm});
            skLineSegment(sketch, "E26.0.1.180", {"start": v(181.7, 118.05) * mm, "end": v(188.88, 122.2) * mm});
            skLineSegment(sketch, "E26.0.1.181", {"start": v(437.24, 109.75) * mm, "end": v(437.24, 118.05) * mm});
            skLineSegment(sketch, "E26.0.1.182", {"start": v(25.7, 118.05) * mm, "end": v(25.7, 109.75) * mm});
            skLineSegment(sketch, "E26.0.1.183", {"start": v(103.7, 105.6) * mm, "end": v(96.5, 109.75) * mm});
            skLineSegment(sketch, "E26.0.1.184", {"start": v(248.5, 120.35) * mm, "end": v(255.7, 124.5) * mm});
            skLineSegment(sketch, "E26.0.1.185", {"start": v(28.36, 109.75) * mm, "end": v(28.36, 118.05) * mm});
            skLineSegment(sketch, "E26.0.1.186", {"start": v(241.32, 124.5) * mm, "end": v(248.5, 120.35) * mm});
            skLineSegment(sketch, "E26.0.1.187", {"start": v(392, 124.5) * mm, "end": v(392, 132.8) * mm});
            skLineSegment(sketch, "E26.0.1.188", {"start": v(119.4, 124.5) * mm, "end": v(112.22, 120.35) * mm});
            skLineSegment(sketch, "E26.0.1.189", {"start": v(19.84, 124.5) * mm, "end": v(27.03, 120.35) * mm});
            skLineSegment(sketch, "E26.0.1.190", {"start": v(93.85, 118.05) * mm, "end": v(93.85, 109.75) * mm});
            skLineSegment(sketch, "E26.0.1.191", {"start": v(173.17, 124.5) * mm, "end": v(180.36, 120.35) * mm});
            skLineSegment(sketch, "E26.0.1.192", {"start": v(283.91, 118.05) * mm, "end": v(291.1, 122.2) * mm});
            skLineSegment(sketch, "E26.0.1.193", {"start": v(156.14, 124.5) * mm, "end": v(156.14, 132.8) * mm});
            skLineSegment(sketch, "E26.0.1.194", {"start": v(27.03, 120.35) * mm, "end": v(34.22, 124.5) * mm});
            skLineSegment(sketch, "E26.0.1.195", {"start": v(494.21, 124.5) * mm, "end": v(494.21, 132.8) * mm});
            skLineSegment(sketch, "E26.0.1.196", {"start": v(487.02, 120.35) * mm, "end": v(494.21, 124.5) * mm});
            skLineSegment(sketch, "E26.0.1.197", {"start": v(120.74, 122.2) * mm, "end": v(127.93, 118.05) * mm});
            skLineSegment(sketch, "E26.0.1.198", {"start": v(282.58, 120.35) * mm, "end": v(289.77, 124.5) * mm});
            skLineSegment(sketch, "E26.0.1.199", {"start": v(326.5, 132.8) * mm, "end": v(326.5, 124.5) * mm});
            skLineSegment(sketch, "E26.0.1.200", {"start": v(130.58, 109.75) * mm, "end": v(130.58, 118.05) * mm});
            skLineSegment(sketch, "E26.0.1.201", {"start": v(444.43, 122.2) * mm, "end": v(451.62, 118.05) * mm});
            skLineSegment(sketch, "E26.0.1.202", {"start": v(188.88, 122.2) * mm, "end": v(196.07, 118.05) * mm});
            skLineSegment(sketch, "E26.0.1.203", {"start": v(369.1, 118.05) * mm, "end": v(376.29, 122.2) * mm});
            skLineSegment(sketch, "E26.0.1.204", {"start": v(87.99, 124.5) * mm, "end": v(95.18, 120.35) * mm});
            skLineSegment(sketch, "E26.0.1.205", {"start": v(454.28, 109.75) * mm, "end": v(454.28, 118.05) * mm});
            skLineSegment(sketch, "E26.0.1.206", {"start": v(359.24, 105.6) * mm, "end": v(352.06, 109.75) * mm});
            skLineSegment(sketch, "E26.0.1.207", {"start": v(164.66, 109.75) * mm, "end": v(164.66, 118.05) * mm});
            skLineSegment(sketch, "E26.0.1.208", {"start": v(19.84, 132.8) * mm, "end": v(19.84, 124.5) * mm});
            skLineSegment(sketch, "E26.0.1.209", {"start": v(410.35, 105.6) * mm, "end": v(403.17, 109.75) * mm});
            skLineSegment(sketch, "E26.0.1.210", {"start": v(79.47, 118.05) * mm, "end": v(86.66, 122.2) * mm});
            skLineSegment(sketch, "E26.0.1.211", {"start": v(400.5, 109.75) * mm, "end": v(393.32, 105.6) * mm});
            skLineSegment(sketch, "E26.0.1.212", {"start": v(289.77, 124.5) * mm, "end": v(289.77, 132.8) * mm});
            skLineSegment(sketch, "E26.0.1.213", {"start": v(360.58, 124.5) * mm, "end": v(360.58, 132.8) * mm});
            skLineSegment(sketch, "E26.0.1.214", {"start": v(180.36, 120.35) * mm, "end": v(187.55, 124.5) * mm});
            skLineSegment(sketch, "E26.0.1.215", {"start": v(190.2, 132.8) * mm, "end": v(190.2, 124.5) * mm});
            skLineSegment(sketch, "E26.0.1.216", {"start": v(144.96, 118.05) * mm, "end": v(144.96, 109.75) * mm});
            skLineSegment(sketch, "E26.0.1.217", {"start": v(96.5, 109.75) * mm, "end": v(96.5, 118.05) * mm});
            skLineSegment(sketch, "E26.0.1.218", {"start": v(68.3, 132.8) * mm, "end": v(68.3, 124.5) * mm});
            skLineSegment(sketch, "E26.0.1.219", {"start": v(187.55, 124.5) * mm, "end": v(187.55, 132.8) * mm});
            skLineSegment(sketch, "E26.0.1.220", {"start": v(342.21, 105.6) * mm, "end": v(335.02, 109.75) * mm});
            skLineSegment(sketch, "E26.0.1.221", {"start": v(136.44, 124.5) * mm, "end": v(136.44, 132.8) * mm});
            skLineSegment(sketch, "E26.0.1.222", {"start": v(343.54, 132.8) * mm, "end": v(343.54, 124.5) * mm});
            skLineSegment(sketch, "E26.0.1.223", {"start": v(231.47, 120.35) * mm, "end": v(238.66, 124.5) * mm});
            skLineSegment(sketch, "E26.0.1.224", {"start": v(163.33, 120.35) * mm, "end": v(156.14, 124.5) * mm});
            skLineSegment(sketch, "E26.0.1.225", {"start": v(70.95, 132.8) * mm, "end": v(70.95, 124.5) * mm});
            skLineSegment(sketch, "E26.0.1.226", {"start": v(179.04, 118.05) * mm, "end": v(179.04, 109.75) * mm});
            skLineSegment(sketch, "E26.0.1.227", {"start": v(196.07, 118.05) * mm, "end": v(196.07, 109.75) * mm});
            skLineSegment(sketch, "E26.0.1.228", {"start": v(505.39, 118.05) * mm, "end": v(512.57, 122.2) * mm});
            skLineSegment(sketch, "E26.0.1.229", {"start": v(249.84, 118.05) * mm, "end": v(257.02, 122.2) * mm});
            skLineSegment(sketch, "E26.0.1.230", {"start": v(173.17, 132.8) * mm, "end": v(173.17, 124.5) * mm});
            skLineSegment(sketch, "E26.0.1.231", {"start": v(213.1, 118.05) * mm, "end": v(213.1, 109.75) * mm});
            skLineSegment(sketch, "E26.0.1.232", {"start": v(445.76, 132.8) * mm, "end": v(445.76, 124.5) * mm});
            skLineSegment(sketch, "E26.0.1.233", {"start": v(478.5, 122.2) * mm, "end": v(485.7, 118.05) * mm});
            skLineSegment(sketch, "E26.0.1.234", {"start": v(409.03, 124.5) * mm, "end": v(409.03, 132.8) * mm});
            skLineSegment(sketch, "E26.0.1.235", {"start": v(496.87, 124.5) * mm, "end": v(504.06, 120.35) * mm});
            skLineSegment(sketch, "E26.0.1.236", {"start": v(139.1, 124.5) * mm, "end": v(146.29, 120.35) * mm});
            skLineSegment(sketch, "E26.0.1.237", {"start": v(272.74, 124.5) * mm, "end": v(265.55, 120.35) * mm});
            skLineSegment(sketch, "E26.0.1.238", {"start": v(214.44, 120.35) * mm, "end": v(207.25, 124.5) * mm});
            skLineSegment(sketch, "E26.0.1.239", {"start": v(342.21, 122.2) * mm, "end": v(349.4, 118.05) * mm});
            skLineSegment(sketch, "E26.0.1.240", {"start": v(495.54, 122.2) * mm, "end": v(502.73, 118.05) * mm});
            skLineSegment(sketch, "E26.0.1.241", {"start": v(36.88, 124.5) * mm, "end": v(44.07, 120.35) * mm});
            skLineSegment(sketch, "E26.0.1.242", {"start": v(62.44, 118.05) * mm, "end": v(69.63, 122.2) * mm});
            skLineSegment(sketch, "E26.0.1.243", {"start": v(502.73, 118.05) * mm, "end": v(502.73, 109.75) * mm});
            skLineSegment(sketch, "E26.0.1.244", {"start": v(266.88, 109.75) * mm, "end": v(266.88, 118.05) * mm});
            skLineSegment(sketch, "E26.0.1.245", {"start": v(477.18, 132.8) * mm, "end": v(477.18, 124.5) * mm});
            skLineSegment(sketch, "E26.0.1.246", {"start": v(257.02, 122.2) * mm, "end": v(264.21, 118.05) * mm});
            skLineSegment(sketch, "E26.0.1.247", {"start": v(207.25, 124.5) * mm, "end": v(207.25, 132.8) * mm});
            skLineSegment(sketch, "E26.0.1.248", {"start": v(469.99, 120.35) * mm, "end": v(462.8, 124.5) * mm});
            skLineSegment(sketch, "E26.0.1.249", {"start": v(394.65, 124.5) * mm, "end": v(401.84, 120.35) * mm});
            skLineSegment(sketch, "E26.0.1.250", {"start": v(426.07, 124.5) * mm, "end": v(418.88, 120.35) * mm});
            skLineSegment(sketch, "E26.0.1.251", {"start": v(110.88, 118.05) * mm, "end": v(110.88, 109.75) * mm});
            skLineSegment(sketch, "E26.0.1.252", {"start": v(137.77, 122.2) * mm, "end": v(144.96, 118.05) * mm});
            skLineSegment(sketch, "E26.0.1.253", {"start": v(323.85, 124.5) * mm, "end": v(316.66, 120.35) * mm});
            skLineSegment(sketch, "E26.0.1.254", {"start": v(504.06, 120.35) * mm, "end": v(511.25, 124.5) * mm});
            skLineSegment(sketch, "E26.0.1.255", {"start": v(68.3, 124.5) * mm, "end": v(61.1, 120.35) * mm});
            skLineSegment(sketch, "E26.0.1.256", {"start": v(264.21, 118.05) * mm, "end": v(264.21, 109.75) * mm});
            skLineSegment(sketch, "E26.0.1.257", {"start": v(42.74, 118.05) * mm, "end": v(42.74, 109.75) * mm});
            skLineSegment(sketch, "E26.0.1.258", {"start": v(418.88, 120.35) * mm, "end": v(411.7, 124.5) * mm});
            skLineSegment(sketch, "E26.0.1.259", {"start": v(147.62, 118.05) * mm, "end": v(154.8, 122.2) * mm});
            skLineSegment(sketch, "E26.0.1.260", {"start": v(205.91, 122.2) * mm, "end": v(213.1, 118.05) * mm});
            skLineSegment(sketch, "E26.0.1.261", {"start": v(403.17, 118.05) * mm, "end": v(410.35, 122.2) * mm});
            skLineSegment(sketch, "E26.0.1.262", {"start": v(113.55, 109.75) * mm, "end": v(113.55, 118.05) * mm});
            skLineSegment(sketch, "E26.0.1.263", {"start": v(383.48, 118.05) * mm, "end": v(383.48, 109.75) * mm});
            skLineSegment(sketch, "E26.0.1.264", {"start": v(317.99, 118.05) * mm, "end": v(325.18, 122.2) * mm});
            skLineSegment(sketch, "E26.0.1.265", {"start": v(417.54, 118.05) * mm, "end": v(417.54, 109.75) * mm});
            skLineSegment(sketch, "E26.0.1.266", {"start": v(352.06, 118.05) * mm, "end": v(359.24, 122.2) * mm});
            skLineSegment(sketch, "E26.0.1.267", {"start": v(386.13, 109.75) * mm, "end": v(386.13, 118.05) * mm});
            skLineSegment(sketch, "E26.0.1.268", {"start": v(103.7, 122.2) * mm, "end": v(110.88, 118.05) * mm});
            skLineSegment(sketch, "E26.0.1.269", {"start": v(112.22, 120.35) * mm, "end": v(105.03, 124.5) * mm});
            skLineSegment(sketch, "E26.0.1.270", {"start": v(315.32, 118.05) * mm, "end": v(315.32, 109.75) * mm});
            skLineSegment(sketch, "E26.0.1.271", {"start": v(410.35, 122.2) * mm, "end": v(417.54, 118.05) * mm});
            skLineSegment(sketch, "E26.0.1.272", {"start": v(146.29, 120.35) * mm, "end": v(153.48, 124.5) * mm});
            skLineSegment(sketch, "E26.0.1.273", {"start": v(400.5, 118.05) * mm, "end": v(400.5, 109.75) * mm});
            skLineSegment(sketch, "E26.0.1.274", {"start": v(505.39, 109.75) * mm, "end": v(505.39, 118.05) * mm});
            skLineSegment(sketch, "E26.0.1.275", {"start": v(119.4, 132.8) * mm, "end": v(119.4, 124.5) * mm});
            skLineSegment(sketch, "E26.0.1.276", {"start": v(420.2, 118.05) * mm, "end": v(427.4, 122.2) * mm});
            skLineSegment(sketch, "E26.0.1.277", {"start": v(198.73, 118.05) * mm, "end": v(205.91, 122.2) * mm});
            skLineSegment(sketch, "E26.0.1.278", {"start": v(197.4, 120.35) * mm, "end": v(204.59, 124.5) * mm});
            skLineSegment(sketch, "E26.0.1.279", {"start": v(317.99, 109.75) * mm, "end": v(317.99, 118.05) * mm});
            skLineSegment(sketch, "E26.0.1.280", {"start": v(428.72, 124.5) * mm, "end": v(435.91, 120.35) * mm});
            skLineSegment(sketch, "E26.0.1.281", {"start": v(343.54, 124.5) * mm, "end": v(350.73, 120.35) * mm});
            skLineSegment(sketch, "E26.0.1.282", {"start": v(427.4, 122.2) * mm, "end": v(434.59, 118.05) * mm});
            skLineSegment(sketch, "E26.0.1.283", {"start": v(350.73, 120.35) * mm, "end": v(357.92, 124.5) * mm});
            skLineSegment(sketch, "E26.0.1.284", {"start": v(204.59, 124.5) * mm, "end": v(204.59, 132.8) * mm});
            skLineSegment(sketch, "E26.0.1.285", {"start": v(62.44, 109.75) * mm, "end": v(62.44, 118.05) * mm});
            skLineSegment(sketch, "E26.0.1.286", {"start": v(45.4, 109.75) * mm, "end": v(45.4, 118.05) * mm});
            skLineSegment(sketch, "E26.0.1.287", {"start": v(454.28, 118.05) * mm, "end": v(461.46, 122.2) * mm});
            skLineSegment(sketch, "E26.0.1.288", {"start": v(461.46, 122.2) * mm, "end": v(468.65, 118.05) * mm});
            skLineSegment(sketch, "E26.0.1.289", {"start": v(393.32, 122.2) * mm, "end": v(400.5, 118.05) * mm});
            skLineSegment(sketch, "E26.0.1.290", {"start": v(59.77, 118.05) * mm, "end": v(59.77, 109.75) * mm});
            skLineSegment(sketch, "E26.0.1.291", {"start": v(352.06, 109.75) * mm, "end": v(352.06, 118.05) * mm});
            skLineSegment(sketch, "E26.0.1.292", {"start": v(265.55, 120.35) * mm, "end": v(258.36, 124.5) * mm});
            skLineSegment(sketch, "E26.0.1.293", {"start": v(349.4, 118.05) * mm, "end": v(349.4, 109.75) * mm});
            skLineSegment(sketch, "E26.0.1.294", {"start": v(420.2, 109.75) * mm, "end": v(420.2, 118.05) * mm});
            skLineSegment(sketch, "E26.0.1.295", {"start": v(386.13, 118.05) * mm, "end": v(393.32, 122.2) * mm});
            skLineSegment(sketch, "E26.0.1.296", {"start": v(44.07, 120.35) * mm, "end": v(51.26, 124.5) * mm});
            skLineSegment(sketch, "E26.0.1.297", {"start": v(403.17, 109.75) * mm, "end": v(403.17, 118.05) * mm});
            skLineSegment(sketch, "E26.0.1.298", {"start": v(384.8, 120.35) * mm, "end": v(392, 124.5) * mm});
            skLineSegment(sketch, "E26.0.1.299", {"start": v(45.4, 118.05) * mm, "end": v(52.58, 122.2) * mm});
            skLineSegment(sketch, "E26.0.1.300", {"start": v(511.25, 132.8) * mm, "end": v(504.06, 136.95) * mm});
            skLineSegment(sketch, "E26.0.1.301", {"start": v(504.06, 136.95) * mm, "end": v(496.87, 132.8) * mm});
            skLineSegment(sketch, "E26.0.1.302", {"start": v(494.21, 132.8) * mm, "end": v(487.02, 136.95) * mm});
            skLineSegment(sketch, "E26.0.1.303", {"start": v(487.02, 136.95) * mm, "end": v(479.83, 132.8) * mm});
            skLineSegment(sketch, "E26.0.1.304", {"start": v(443.1, 132.8) * mm, "end": v(435.91, 136.95) * mm});
            skLineSegment(sketch, "E26.0.1.305", {"start": v(367.77, 136.95) * mm, "end": v(374.96, 132.8) * mm});
            skLineSegment(sketch, "E26.0.1.306", {"start": v(333.7, 136.95) * mm, "end": v(326.5, 132.8) * mm});
            skLineSegment(sketch, "E26.0.1.307", {"start": v(435.91, 136.95) * mm, "end": v(428.72, 132.8) * mm});
            skLineSegment(sketch, "E26.0.1.308", {"start": v(418.88, 136.95) * mm, "end": v(426.07, 132.8) * mm});
            skLineSegment(sketch, "E26.0.1.309", {"start": v(411.7, 132.8) * mm, "end": v(418.88, 136.95) * mm});
            skLineSegment(sketch, "E26.0.1.310", {"start": v(357.92, 132.8) * mm, "end": v(350.73, 136.95) * mm});
            skLineSegment(sketch, "E26.0.1.311", {"start": v(401.84, 136.95) * mm, "end": v(394.65, 132.8) * mm});
            skLineSegment(sketch, "E26.0.1.312", {"start": v(350.73, 136.95) * mm, "end": v(343.54, 132.8) * mm});
            skLineSegment(sketch, "E26.0.1.313", {"start": v(340.88, 132.8) * mm, "end": v(333.7, 136.95) * mm});
            skLineSegment(sketch, "E26.0.1.314", {"start": v(460.14, 132.8) * mm, "end": v(452.95, 136.95) * mm});
            skLineSegment(sketch, "E26.0.1.315", {"start": v(392, 132.8) * mm, "end": v(384.8, 136.95) * mm});
            skLineSegment(sketch, "E26.0.1.316", {"start": v(462.8, 132.8) * mm, "end": v(469.99, 136.95) * mm});
            skLineSegment(sketch, "E26.0.1.317", {"start": v(306.8, 132.8) * mm, "end": v(299.62, 136.95) * mm});
            skLineSegment(sketch, "E26.0.1.318", {"start": v(469.99, 136.95) * mm, "end": v(477.18, 132.8) * mm});
            skLineSegment(sketch, "E26.0.1.319", {"start": v(360.58, 132.8) * mm, "end": v(367.77, 136.95) * mm});
            skLineSegment(sketch, "E26.0.1.320", {"start": v(309.47, 132.8) * mm, "end": v(316.66, 136.95) * mm});
            skLineSegment(sketch, "E26.0.1.321", {"start": v(409.03, 132.8) * mm, "end": v(401.84, 136.95) * mm});
            skLineSegment(sketch, "E26.0.1.322", {"start": v(384.8, 136.95) * mm, "end": v(377.61, 132.8) * mm});
            skLineSegment(sketch, "E26.0.1.323", {"start": v(316.66, 136.95) * mm, "end": v(323.85, 132.8) * mm});
            skLineSegment(sketch, "E26.0.1.324", {"start": v(452.95, 136.95) * mm, "end": v(445.76, 132.8) * mm});
            skLineSegment(sketch, "E26.0.1.325", {"start": v(299.62, 136.95) * mm, "end": v(292.43, 132.8) * mm});
            skLineSegment(sketch, "E26.0.1.326", {"start": v(95.18, 136.95) * mm, "end": v(87.99, 132.8) * mm});
            skLineSegment(sketch, "E26.0.1.327", {"start": v(129.25, 136.95) * mm, "end": v(122.06, 132.8) * mm});
            skLineSegment(sketch, "E26.0.1.328", {"start": v(102.37, 132.8) * mm, "end": v(95.18, 136.95) * mm});
            skLineSegment(sketch, "E26.0.1.329", {"start": v(238.66, 132.8) * mm, "end": v(231.47, 136.95) * mm});
            skLineSegment(sketch, "E26.0.1.330", {"start": v(282.58, 136.95) * mm, "end": v(275.4, 132.8) * mm});
            skLineSegment(sketch, "E26.0.1.331", {"start": v(53.92, 132.8) * mm, "end": v(61.1, 136.95) * mm});
            skLineSegment(sketch, "E26.0.1.332", {"start": v(105.03, 132.8) * mm, "end": v(112.22, 136.95) * mm});
            skLineSegment(sketch, "E26.0.1.333", {"start": v(214.44, 136.95) * mm, "end": v(221.63, 132.8) * mm});
            skLineSegment(sketch, "E26.0.1.334", {"start": v(136.44, 132.8) * mm, "end": v(129.25, 136.95) * mm});
            skLineSegment(sketch, "E26.0.1.335", {"start": v(153.48, 132.8) * mm, "end": v(146.29, 136.95) * mm});
            skLineSegment(sketch, "E26.0.1.336", {"start": v(255.7, 132.8) * mm, "end": v(248.5, 136.95) * mm});
            skLineSegment(sketch, "E26.0.1.337", {"start": v(61.1, 136.95) * mm, "end": v(68.3, 132.8) * mm});
            skLineSegment(sketch, "E26.0.1.338", {"start": v(180.36, 136.95) * mm, "end": v(173.17, 132.8) * mm});
            skLineSegment(sketch, "E26.0.1.339", {"start": v(51.26, 132.8) * mm, "end": v(44.07, 136.95) * mm});
            skLineSegment(sketch, "E26.0.1.340", {"start": v(163.33, 136.95) * mm, "end": v(170.52, 132.8) * mm});
            skLineSegment(sketch, "E26.0.1.341", {"start": v(265.55, 136.95) * mm, "end": v(272.74, 132.8) * mm});
            skLineSegment(sketch, "E26.0.1.342", {"start": v(207.25, 132.8) * mm, "end": v(214.44, 136.95) * mm});
            skLineSegment(sketch, "E26.0.1.343", {"start": v(146.29, 136.95) * mm, "end": v(139.1, 132.8) * mm});
            skLineSegment(sketch, "E26.0.1.344", {"start": v(258.36, 132.8) * mm, "end": v(265.55, 136.95) * mm});
            skLineSegment(sketch, "E26.0.1.345", {"start": v(231.47, 136.95) * mm, "end": v(224.28, 132.8) * mm});
            skLineSegment(sketch, "E26.0.1.346", {"start": v(248.5, 136.95) * mm, "end": v(241.32, 132.8) * mm});
            skLineSegment(sketch, "E26.0.1.347", {"start": v(156.14, 132.8) * mm, "end": v(163.33, 136.95) * mm});
            skLineSegment(sketch, "E26.0.1.348", {"start": v(34.22, 132.8) * mm, "end": v(27.03, 136.95) * mm});
            skLineSegment(sketch, "E26.0.1.349", {"start": v(112.22, 136.95) * mm, "end": v(119.4, 132.8) * mm});
            skLineSegment(sketch, "E26.0.1.350", {"start": v(204.59, 132.8) * mm, "end": v(197.4, 136.95) * mm});
            skLineSegment(sketch, "E26.0.1.351", {"start": v(85.33, 132.8) * mm, "end": v(78.14, 136.95) * mm});
            skLineSegment(sketch, "E26.0.1.352", {"start": v(187.55, 132.8) * mm, "end": v(180.36, 136.95) * mm});
            skLineSegment(sketch, "E26.0.1.353", {"start": v(197.4, 136.95) * mm, "end": v(190.2, 132.8) * mm});
            skLineSegment(sketch, "E26.0.1.354", {"start": v(44.07, 136.95) * mm, "end": v(36.88, 132.8) * mm});
            skLineSegment(sketch, "E26.0.1.355", {"start": v(78.14, 136.95) * mm, "end": v(70.95, 132.8) * mm});
            skLineSegment(sketch, "E26.0.1.356", {"start": v(27.03, 136.95) * mm, "end": v(19.84, 132.8) * mm});
            skLineSegment(sketch, "E26.0.1.357", {"start": v(10, 136.95) * mm, "end": v(17.19, 132.8) * mm});
            skLineSegment(sketch, "E26.0.1.358", {"start": v(2.81, 132.8) * mm, "end": v(10, 136.95) * mm});
            skLineSegment(sketch, "E26.0.2.0", {"start": v(2.81, 95) * mm, "end": v(2.81, 103.3) * mm});
            skLineSegment(sketch, "E26.0.2.1", {"start": v(511.25, 95) * mm, "end": v(511.25, 103.3) * mm});
            skLineSegment(sketch, "E26.0.2.2", {"start": v(120.74, 76.1) * mm, "end": v(113.55, 80.25) * mm});
            skLineSegment(sketch, "E26.0.2.3", {"start": v(240, 76.1) * mm, "end": v(232.8, 80.25) * mm});
            skLineSegment(sketch, "E26.0.2.4", {"start": v(519.76, 80.25) * mm, "end": v(512.57, 76.1) * mm});
            skLineSegment(sketch, "E26.0.2.5", {"start": v(18.52, 76.1) * mm, "end": v(11.33, 80.25) * mm});
            skLineSegment(sketch, "E26.0.2.6", {"start": v(383.48, 80.25) * mm, "end": v(376.29, 76.1) * mm});
            skLineSegment(sketch, "E26.0.2.7", {"start": v(274.07, 76.1) * mm, "end": v(266.88, 80.25) * mm});
            skLineSegment(sketch, "E26.0.2.8", {"start": v(315.32, 80.25) * mm, "end": v(308.13, 76.1) * mm});
            skLineSegment(sketch, "E26.0.2.9", {"start": v(86.66, 76.1) * mm, "end": v(79.47, 80.25) * mm});
            skLineSegment(sketch, "E26.0.2.10", {"start": v(10, 90.85) * mm, "end": v(2.81, 95) * mm});
            skLineSegment(sketch, "E26.0.2.11", {"start": v(247.18, 80.25) * mm, "end": v(240, 76.1) * mm});
            skLineSegment(sketch, "E26.0.2.12", {"start": v(325.18, 76.1) * mm, "end": v(317.99, 80.25) * mm});
            skLineSegment(sketch, "E26.0.2.13", {"start": v(257.02, 76.1) * mm, "end": v(249.84, 80.25) * mm});
            skLineSegment(sketch, "E26.0.2.14", {"start": v(35.55, 76.1) * mm, "end": v(28.36, 80.25) * mm});
            skLineSegment(sketch, "E26.0.2.15", {"start": v(127.93, 80.25) * mm, "end": v(120.74, 76.1) * mm});
            skLineSegment(sketch, "E26.0.2.16", {"start": v(196.07, 80.25) * mm, "end": v(188.88, 76.1) * mm});
            skLineSegment(sketch, "E26.0.2.17", {"start": v(308.13, 76.1) * mm, "end": v(300.95, 80.25) * mm});
            skLineSegment(sketch, "E26.0.2.18", {"start": v(298.29, 80.25) * mm, "end": v(291.1, 76.1) * mm});
            skLineSegment(sketch, "E26.0.2.19", {"start": v(332.37, 80.25) * mm, "end": v(325.18, 76.1) * mm});
            skLineSegment(sketch, "E26.0.2.20", {"start": v(11.33, 80.25) * mm, "end": v(11.33, 88.55) * mm});
            skLineSegment(sketch, "E26.0.2.21", {"start": v(519.76, 88.55) * mm, "end": v(519.76, 80.25) * mm});
            skLineSegment(sketch, "E26.0.2.22", {"start": v(461.46, 76.1) * mm, "end": v(454.28, 80.25) * mm});
            skLineSegment(sketch, "E26.0.2.23", {"start": v(230.15, 80.25) * mm, "end": v(222.96, 76.1) * mm});
            skLineSegment(sketch, "E26.0.2.24", {"start": v(300.95, 80.25) * mm, "end": v(300.95, 88.55) * mm});
            skLineSegment(sketch, "E26.0.2.25", {"start": v(42.74, 80.25) * mm, "end": v(35.55, 76.1) * mm});
            skLineSegment(sketch, "E26.0.2.26", {"start": v(17.19, 95) * mm, "end": v(10, 90.85) * mm});
            skLineSegment(sketch, "E26.0.2.27", {"start": v(34.22, 95) * mm, "end": v(34.22, 103.3) * mm});
            skLineSegment(sketch, "E26.0.2.28", {"start": v(512.57, 92.7) * mm, "end": v(519.76, 88.55) * mm});
            skLineSegment(sketch, "E26.0.2.29", {"start": v(376.29, 76.1) * mm, "end": v(369.1, 80.25) * mm});
            skLineSegment(sketch, "E26.0.2.30", {"start": v(292.43, 95) * mm, "end": v(299.62, 90.85) * mm});
            skLineSegment(sketch, "E26.0.2.31", {"start": v(468.65, 88.55) * mm, "end": v(468.65, 80.25) * mm});
            skLineSegment(sketch, "E26.0.2.32", {"start": v(11.33, 88.55) * mm, "end": v(18.52, 92.7) * mm});
            skLineSegment(sketch, "E26.0.2.33", {"start": v(377.61, 103.3) * mm, "end": v(377.61, 95) * mm});
            skLineSegment(sketch, "E26.0.2.34", {"start": v(366.43, 88.55) * mm, "end": v(366.43, 80.25) * mm});
            skLineSegment(sketch, "E26.0.2.35", {"start": v(255.7, 95) * mm, "end": v(255.7, 103.3) * mm});
            skLineSegment(sketch, "E26.0.2.36", {"start": v(495.54, 76.1) * mm, "end": v(488.35, 80.25) * mm});
            skLineSegment(sketch, "E26.0.2.37", {"start": v(105.03, 95) * mm, "end": v(105.03, 103.3) * mm});
            skLineSegment(sketch, "E26.0.2.38", {"start": v(162, 80.25) * mm, "end": v(154.8, 76.1) * mm});
            skLineSegment(sketch, "E26.0.2.39", {"start": v(93.85, 80.25) * mm, "end": v(86.66, 76.1) * mm});
            skLineSegment(sketch, "E26.0.2.40", {"start": v(25.7, 80.25) * mm, "end": v(18.52, 76.1) * mm});
            skLineSegment(sketch, "E26.0.2.41", {"start": v(110.88, 80.25) * mm, "end": v(103.7, 76.1) * mm});
            skLineSegment(sketch, "E26.0.2.42", {"start": v(281.26, 80.25) * mm, "end": v(274.07, 76.1) * mm});
            skLineSegment(sketch, "E26.0.2.43", {"start": v(171.85, 76.1) * mm, "end": v(164.66, 80.25) * mm});
            skLineSegment(sketch, "E26.0.2.44", {"start": v(298.29, 88.55) * mm, "end": v(298.29, 80.25) * mm});
            skLineSegment(sketch, "E26.0.2.45", {"start": v(281.26, 88.55) * mm, "end": v(281.26, 80.25) * mm});
            skLineSegment(sketch, "E26.0.2.46", {"start": v(374.96, 103.3) * mm, "end": v(374.96, 95) * mm});
            skLineSegment(sketch, "E26.0.2.47", {"start": v(502.73, 80.25) * mm, "end": v(495.54, 76.1) * mm});
            skLineSegment(sketch, "E26.0.2.48", {"start": v(144.96, 80.25) * mm, "end": v(137.77, 76.1) * mm});
            skLineSegment(sketch, "E26.0.2.49", {"start": v(76.82, 88.55) * mm, "end": v(76.82, 80.25) * mm});
            skLineSegment(sketch, "E26.0.2.50", {"start": v(102.37, 95) * mm, "end": v(102.37, 103.3) * mm});
            skLineSegment(sketch, "E26.0.2.51", {"start": v(179.04, 80.25) * mm, "end": v(171.85, 76.1) * mm});
            skLineSegment(sketch, "E26.0.2.52", {"start": v(52.58, 76.1) * mm, "end": v(45.4, 80.25) * mm});
            skLineSegment(sketch, "E26.0.2.53", {"start": v(17.19, 103.3) * mm, "end": v(17.19, 95) * mm});
            skLineSegment(sketch, "E26.0.2.54", {"start": v(205.91, 76.1) * mm, "end": v(198.73, 80.25) * mm});
            skLineSegment(sketch, "E26.0.2.55", {"start": v(154.8, 76.1) * mm, "end": v(147.62, 80.25) * mm});
            skLineSegment(sketch, "E26.0.2.56", {"start": v(299.62, 90.85) * mm, "end": v(306.8, 95) * mm});
            skLineSegment(sketch, "E26.0.2.57", {"start": v(306.8, 95) * mm, "end": v(306.8, 103.3) * mm});
            skLineSegment(sketch, "E26.0.2.58", {"start": v(291.1, 92.7) * mm, "end": v(298.29, 88.55) * mm});
            skLineSegment(sketch, "E26.0.2.59", {"start": v(213.1, 80.25) * mm, "end": v(205.91, 76.1) * mm});
            skLineSegment(sketch, "E26.0.2.60", {"start": v(238.66, 95) * mm, "end": v(238.66, 103.3) * mm});
            skLineSegment(sketch, "E26.0.2.61", {"start": v(76.82, 80.25) * mm, "end": v(69.63, 76.1) * mm});
            skLineSegment(sketch, "E26.0.2.62", {"start": v(434.59, 80.25) * mm, "end": v(427.4, 76.1) * mm});
            skLineSegment(sketch, "E26.0.2.63", {"start": v(309.47, 95) * mm, "end": v(309.47, 103.3) * mm});
            skLineSegment(sketch, "E26.0.2.64", {"start": v(366.43, 80.25) * mm, "end": v(359.24, 76.1) * mm});
            skLineSegment(sketch, "E26.0.2.65", {"start": v(468.65, 80.25) * mm, "end": v(461.46, 76.1) * mm});
            skLineSegment(sketch, "E26.0.2.66", {"start": v(478.5, 76.1) * mm, "end": v(471.32, 80.25) * mm});
            skLineSegment(sketch, "E26.0.2.67", {"start": v(222.96, 76.1) * mm, "end": v(215.77, 80.25) * mm});
            skLineSegment(sketch, "E26.0.2.68", {"start": v(512.57, 76.1) * mm, "end": v(505.39, 80.25) * mm});
            skLineSegment(sketch, "E26.0.2.69", {"start": v(427.4, 76.1) * mm, "end": v(420.2, 80.25) * mm});
            skLineSegment(sketch, "E26.0.2.70", {"start": v(291.1, 76.1) * mm, "end": v(283.91, 80.25) * mm});
            skLineSegment(sketch, "E26.0.2.71", {"start": v(444.43, 76.1) * mm, "end": v(437.24, 80.25) * mm});
            skLineSegment(sketch, "E26.0.2.72", {"start": v(369.1, 80.25) * mm, "end": v(369.1, 88.55) * mm});
            skLineSegment(sketch, "E26.0.2.73", {"start": v(188.88, 76.1) * mm, "end": v(181.7, 80.25) * mm});
            skLineSegment(sketch, "E26.0.2.74", {"start": v(79.47, 80.25) * mm, "end": v(79.47, 88.55) * mm});
            skLineSegment(sketch, "E26.0.2.75", {"start": v(264.21, 80.25) * mm, "end": v(257.02, 76.1) * mm});
            skLineSegment(sketch, "E26.0.2.76", {"start": v(485.7, 80.25) * mm, "end": v(478.5, 76.1) * mm});
            skLineSegment(sketch, "E26.0.2.77", {"start": v(241.32, 103.3) * mm, "end": v(241.32, 95) * mm});
            skLineSegment(sketch, "E26.0.2.78", {"start": v(283.91, 80.25) * mm, "end": v(283.91, 88.55) * mm});
            skLineSegment(sketch, "E26.0.2.79", {"start": v(496.87, 103.3) * mm, "end": v(496.87, 95) * mm});
            skLineSegment(sketch, "E26.0.2.80", {"start": v(122.06, 103.3) * mm, "end": v(122.06, 95) * mm});
            skLineSegment(sketch, "E26.0.2.81", {"start": v(96.5, 88.55) * mm, "end": v(103.7, 92.7) * mm});
            skLineSegment(sketch, "E26.0.2.82", {"start": v(308.13, 92.7) * mm, "end": v(315.32, 88.55) * mm});
            skLineSegment(sketch, "E26.0.2.83", {"start": v(113.55, 88.55) * mm, "end": v(120.74, 92.7) * mm});
            skLineSegment(sketch, "E26.0.2.84", {"start": v(190.2, 95) * mm, "end": v(197.4, 90.85) * mm});
            skLineSegment(sketch, "E26.0.2.85", {"start": v(249.84, 80.25) * mm, "end": v(249.84, 88.55) * mm});
            skLineSegment(sketch, "E26.0.2.86", {"start": v(230.15, 88.55) * mm, "end": v(230.15, 80.25) * mm});
            skLineSegment(sketch, "E26.0.2.87", {"start": v(411.7, 95) * mm, "end": v(411.7, 103.3) * mm});
            skLineSegment(sketch, "E26.0.2.88", {"start": v(221.63, 103.3) * mm, "end": v(221.63, 95) * mm});
            skLineSegment(sketch, "E26.0.2.89", {"start": v(130.58, 88.55) * mm, "end": v(137.77, 92.7) * mm});
            skLineSegment(sketch, "E26.0.2.90", {"start": v(323.85, 103.3) * mm, "end": v(323.85, 95) * mm});
            skLineSegment(sketch, "E26.0.2.91", {"start": v(258.36, 95) * mm, "end": v(258.36, 103.3) * mm});
            skLineSegment(sketch, "E26.0.2.92", {"start": v(215.77, 88.55) * mm, "end": v(222.96, 92.7) * mm});
            skLineSegment(sketch, "E26.0.2.93", {"start": v(272.74, 103.3) * mm, "end": v(272.74, 95) * mm});
            skLineSegment(sketch, "E26.0.2.94", {"start": v(35.55, 92.7) * mm, "end": v(42.74, 88.55) * mm});
            skLineSegment(sketch, "E26.0.2.95", {"start": v(215.77, 80.25) * mm, "end": v(215.77, 88.55) * mm});
            skLineSegment(sketch, "E26.0.2.96", {"start": v(292.43, 103.3) * mm, "end": v(292.43, 95) * mm});
            skLineSegment(sketch, "E26.0.2.97", {"start": v(359.24, 92.7) * mm, "end": v(366.43, 88.55) * mm});
            skLineSegment(sketch, "E26.0.2.98", {"start": v(367.77, 90.85) * mm, "end": v(360.58, 95) * mm});
            skLineSegment(sketch, "E26.0.2.99", {"start": v(335.02, 80.25) * mm, "end": v(335.02, 88.55) * mm});
            skLineSegment(sketch, "E26.0.2.100", {"start": v(462.8, 95) * mm, "end": v(462.8, 103.3) * mm});
            skLineSegment(sketch, "E26.0.2.101", {"start": v(485.7, 88.55) * mm, "end": v(485.7, 80.25) * mm});
            skLineSegment(sketch, "E26.0.2.102", {"start": v(153.48, 95) * mm, "end": v(153.48, 103.3) * mm});
            skLineSegment(sketch, "E26.0.2.103", {"start": v(51.26, 95) * mm, "end": v(51.26, 103.3) * mm});
            skLineSegment(sketch, "E26.0.2.104", {"start": v(162, 88.55) * mm, "end": v(162, 80.25) * mm});
            skLineSegment(sketch, "E26.0.2.105", {"start": v(222.96, 92.7) * mm, "end": v(230.15, 88.55) * mm});
            skLineSegment(sketch, "E26.0.2.106", {"start": v(357.92, 95) * mm, "end": v(357.92, 103.3) * mm});
            skLineSegment(sketch, "E26.0.2.107", {"start": v(488.35, 88.55) * mm, "end": v(495.54, 92.7) * mm});
            skLineSegment(sketch, "E26.0.2.108", {"start": v(374.96, 95) * mm, "end": v(367.77, 90.85) * mm});
            skLineSegment(sketch, "E26.0.2.109", {"start": v(471.32, 80.25) * mm, "end": v(471.32, 88.55) * mm});
            skLineSegment(sketch, "E26.0.2.110", {"start": v(335.02, 88.55) * mm, "end": v(342.21, 92.7) * mm});
            skLineSegment(sketch, "E26.0.2.111", {"start": v(340.88, 95) * mm, "end": v(340.88, 103.3) * mm});
            skLineSegment(sketch, "E26.0.2.112", {"start": v(401.84, 90.85) * mm, "end": v(409.03, 95) * mm});
            skLineSegment(sketch, "E26.0.2.113", {"start": v(428.72, 103.3) * mm, "end": v(428.72, 95) * mm});
            skLineSegment(sketch, "E26.0.2.114", {"start": v(426.07, 103.3) * mm, "end": v(426.07, 95) * mm});
            skLineSegment(sketch, "E26.0.2.115", {"start": v(333.7, 90.85) * mm, "end": v(340.88, 95) * mm});
            skLineSegment(sketch, "E26.0.2.116", {"start": v(451.62, 80.25) * mm, "end": v(444.43, 76.1) * mm});
            skLineSegment(sketch, "E26.0.2.117", {"start": v(393.32, 76.1) * mm, "end": v(386.13, 80.25) * mm});
            skLineSegment(sketch, "E26.0.2.118", {"start": v(300.95, 88.55) * mm, "end": v(308.13, 92.7) * mm});
            skLineSegment(sketch, "E26.0.2.119", {"start": v(59.77, 80.25) * mm, "end": v(52.58, 76.1) * mm});
            skLineSegment(sketch, "E26.0.2.120", {"start": v(86.66, 92.7) * mm, "end": v(93.85, 88.55) * mm});
            skLineSegment(sketch, "E26.0.2.121", {"start": v(198.73, 80.25) * mm, "end": v(198.73, 88.55) * mm});
            skLineSegment(sketch, "E26.0.2.122", {"start": v(164.66, 88.55) * mm, "end": v(171.85, 92.7) * mm});
            skLineSegment(sketch, "E26.0.2.123", {"start": v(349.4, 80.25) * mm, "end": v(342.21, 76.1) * mm});
            skLineSegment(sketch, "E26.0.2.124", {"start": v(435.91, 90.85) * mm, "end": v(443.1, 95) * mm});
            skLineSegment(sketch, "E26.0.2.125", {"start": v(332.37, 88.55) * mm, "end": v(332.37, 80.25) * mm});
            skLineSegment(sketch, "E26.0.2.126", {"start": v(69.63, 92.7) * mm, "end": v(76.82, 88.55) * mm});
            skLineSegment(sketch, "E26.0.2.127", {"start": v(394.65, 103.3) * mm, "end": v(394.65, 95) * mm});
            skLineSegment(sketch, "E26.0.2.128", {"start": v(36.88, 103.3) * mm, "end": v(36.88, 95) * mm});
            skLineSegment(sketch, "E26.0.2.129", {"start": v(147.62, 80.25) * mm, "end": v(147.62, 88.55) * mm});
            skLineSegment(sketch, "E26.0.2.130", {"start": v(170.52, 95) * mm, "end": v(163.33, 90.85) * mm});
            skLineSegment(sketch, "E26.0.2.131", {"start": v(224.28, 103.3) * mm, "end": v(224.28, 95) * mm});
            skLineSegment(sketch, "E26.0.2.132", {"start": v(266.88, 88.55) * mm, "end": v(274.07, 92.7) * mm});
            skLineSegment(sketch, "E26.0.2.133", {"start": v(221.63, 95) * mm, "end": v(214.44, 90.85) * mm});
            skLineSegment(sketch, "E26.0.2.134", {"start": v(471.32, 88.55) * mm, "end": v(478.5, 92.7) * mm});
            skLineSegment(sketch, "E26.0.2.135", {"start": v(53.92, 95) * mm, "end": v(53.92, 103.3) * mm});
            skLineSegment(sketch, "E26.0.2.136", {"start": v(460.14, 95) * mm, "end": v(460.14, 103.3) * mm});
            skLineSegment(sketch, "E26.0.2.137", {"start": v(154.8, 92.7) * mm, "end": v(162, 88.55) * mm});
            skLineSegment(sketch, "E26.0.2.138", {"start": v(181.7, 80.25) * mm, "end": v(181.7, 88.55) * mm});
            skLineSegment(sketch, "E26.0.2.139", {"start": v(274.07, 92.7) * mm, "end": v(281.26, 88.55) * mm});
            skLineSegment(sketch, "E26.0.2.140", {"start": v(28.36, 88.55) * mm, "end": v(35.55, 92.7) * mm});
            skLineSegment(sketch, "E26.0.2.141", {"start": v(137.77, 76.1) * mm, "end": v(130.58, 80.25) * mm});
            skLineSegment(sketch, "E26.0.2.142", {"start": v(479.83, 103.3) * mm, "end": v(479.83, 95) * mm});
            skLineSegment(sketch, "E26.0.2.143", {"start": v(275.4, 103.3) * mm, "end": v(275.4, 95) * mm});
            skLineSegment(sketch, "E26.0.2.144", {"start": v(170.52, 103.3) * mm, "end": v(170.52, 95) * mm});
            skLineSegment(sketch, "E26.0.2.145", {"start": v(377.61, 95) * mm, "end": v(384.8, 90.85) * mm});
            skLineSegment(sketch, "E26.0.2.146", {"start": v(434.59, 88.55) * mm, "end": v(434.59, 80.25) * mm});
            skLineSegment(sketch, "E26.0.2.147", {"start": v(18.52, 92.7) * mm, "end": v(25.7, 88.55) * mm});
            skLineSegment(sketch, "E26.0.2.148", {"start": v(224.28, 95) * mm, "end": v(231.47, 90.85) * mm});
            skLineSegment(sketch, "E26.0.2.149", {"start": v(325.18, 92.7) * mm, "end": v(332.37, 88.55) * mm});
            skLineSegment(sketch, "E26.0.2.150", {"start": v(95.18, 90.85) * mm, "end": v(102.37, 95) * mm});
            skLineSegment(sketch, "E26.0.2.151", {"start": v(488.35, 80.25) * mm, "end": v(488.35, 88.55) * mm});
            skLineSegment(sketch, "E26.0.2.152", {"start": v(376.29, 92.7) * mm, "end": v(383.48, 88.55) * mm});
            skLineSegment(sketch, "E26.0.2.153", {"start": v(316.66, 90.85) * mm, "end": v(309.47, 95) * mm});
            skLineSegment(sketch, "E26.0.2.154", {"start": v(127.93, 88.55) * mm, "end": v(127.93, 80.25) * mm});
            skLineSegment(sketch, "E26.0.2.155", {"start": v(479.83, 95) * mm, "end": v(487.02, 90.85) * mm});
            skLineSegment(sketch, "E26.0.2.156", {"start": v(326.5, 95) * mm, "end": v(333.7, 90.85) * mm});
            skLineSegment(sketch, "E26.0.2.157", {"start": v(171.85, 92.7) * mm, "end": v(179.04, 88.55) * mm});
            skLineSegment(sketch, "E26.0.2.158", {"start": v(247.18, 88.55) * mm, "end": v(247.18, 80.25) * mm});
            skLineSegment(sketch, "E26.0.2.159", {"start": v(69.63, 76.1) * mm, "end": v(62.44, 80.25) * mm});
            skLineSegment(sketch, "E26.0.2.160", {"start": v(452.95, 90.85) * mm, "end": v(460.14, 95) * mm});
            skLineSegment(sketch, "E26.0.2.161", {"start": v(275.4, 95) * mm, "end": v(282.58, 90.85) * mm});
            skLineSegment(sketch, "E26.0.2.162", {"start": v(232.8, 88.55) * mm, "end": v(240, 92.7) * mm});
            skLineSegment(sketch, "E26.0.2.163", {"start": v(122.06, 95) * mm, "end": v(129.25, 90.85) * mm});
            skLineSegment(sketch, "E26.0.2.164", {"start": v(417.54, 80.25) * mm, "end": v(410.35, 76.1) * mm});
            skLineSegment(sketch, "E26.0.2.165", {"start": v(139.1, 103.3) * mm, "end": v(139.1, 95) * mm});
            skLineSegment(sketch, "E26.0.2.166", {"start": v(443.1, 95) * mm, "end": v(443.1, 103.3) * mm});
            skLineSegment(sketch, "E26.0.2.167", {"start": v(232.8, 80.25) * mm, "end": v(232.8, 88.55) * mm});
            skLineSegment(sketch, "E26.0.2.168", {"start": v(61.1, 90.85) * mm, "end": v(53.92, 95) * mm});
            skLineSegment(sketch, "E26.0.2.169", {"start": v(437.24, 88.55) * mm, "end": v(444.43, 92.7) * mm});
            skLineSegment(sketch, "E26.0.2.170", {"start": v(78.14, 90.85) * mm, "end": v(85.33, 95) * mm});
            skLineSegment(sketch, "E26.0.2.171", {"start": v(85.33, 95) * mm, "end": v(85.33, 103.3) * mm});
            skLineSegment(sketch, "E26.0.2.172", {"start": v(445.76, 95) * mm, "end": v(452.95, 90.85) * mm});
            skLineSegment(sketch, "E26.0.2.173", {"start": v(240, 92.7) * mm, "end": v(247.18, 88.55) * mm});
            skLineSegment(sketch, "E26.0.2.174", {"start": v(477.18, 95) * mm, "end": v(469.99, 90.85) * mm});
            skLineSegment(sketch, "E26.0.2.175", {"start": v(451.62, 88.55) * mm, "end": v(451.62, 80.25) * mm});
            skLineSegment(sketch, "E26.0.2.176", {"start": v(129.25, 90.85) * mm, "end": v(136.44, 95) * mm});
            skLineSegment(sketch, "E26.0.2.177", {"start": v(87.99, 103.3) * mm, "end": v(87.99, 95) * mm});
            skLineSegment(sketch, "E26.0.2.178", {"start": v(52.58, 92.7) * mm, "end": v(59.77, 88.55) * mm});
            skLineSegment(sketch, "E26.0.2.179", {"start": v(70.95, 95) * mm, "end": v(78.14, 90.85) * mm});
            skLineSegment(sketch, "E26.0.2.180", {"start": v(181.7, 88.55) * mm, "end": v(188.88, 92.7) * mm});
            skLineSegment(sketch, "E26.0.2.181", {"start": v(437.24, 80.25) * mm, "end": v(437.24, 88.55) * mm});
            skLineSegment(sketch, "E26.0.2.182", {"start": v(25.7, 88.55) * mm, "end": v(25.7, 80.25) * mm});
            skLineSegment(sketch, "E26.0.2.183", {"start": v(103.7, 76.1) * mm, "end": v(96.5, 80.25) * mm});
            skLineSegment(sketch, "E26.0.2.184", {"start": v(248.5, 90.85) * mm, "end": v(255.7, 95) * mm});
            skLineSegment(sketch, "E26.0.2.185", {"start": v(28.36, 80.25) * mm, "end": v(28.36, 88.55) * mm});
            skLineSegment(sketch, "E26.0.2.186", {"start": v(241.32, 95) * mm, "end": v(248.5, 90.85) * mm});
            skLineSegment(sketch, "E26.0.2.187", {"start": v(392, 95) * mm, "end": v(392, 103.3) * mm});
            skLineSegment(sketch, "E26.0.2.188", {"start": v(119.4, 95) * mm, "end": v(112.22, 90.85) * mm});
            skLineSegment(sketch, "E26.0.2.189", {"start": v(19.84, 95) * mm, "end": v(27.03, 90.85) * mm});
            skLineSegment(sketch, "E26.0.2.190", {"start": v(93.85, 88.55) * mm, "end": v(93.85, 80.25) * mm});
            skLineSegment(sketch, "E26.0.2.191", {"start": v(173.17, 95) * mm, "end": v(180.36, 90.85) * mm});
            skLineSegment(sketch, "E26.0.2.192", {"start": v(283.91, 88.55) * mm, "end": v(291.1, 92.7) * mm});
            skLineSegment(sketch, "E26.0.2.193", {"start": v(156.14, 95) * mm, "end": v(156.14, 103.3) * mm});
            skLineSegment(sketch, "E26.0.2.194", {"start": v(27.03, 90.85) * mm, "end": v(34.22, 95) * mm});
            skLineSegment(sketch, "E26.0.2.195", {"start": v(494.21, 95) * mm, "end": v(494.21, 103.3) * mm});
            skLineSegment(sketch, "E26.0.2.196", {"start": v(487.02, 90.85) * mm, "end": v(494.21, 95) * mm});
            skLineSegment(sketch, "E26.0.2.197", {"start": v(120.74, 92.7) * mm, "end": v(127.93, 88.55) * mm});
            skLineSegment(sketch, "E26.0.2.198", {"start": v(282.58, 90.85) * mm, "end": v(289.77, 95) * mm});
            skLineSegment(sketch, "E26.0.2.199", {"start": v(326.5, 103.3) * mm, "end": v(326.5, 95) * mm});
            skLineSegment(sketch, "E26.0.2.200", {"start": v(130.58, 80.25) * mm, "end": v(130.58, 88.55) * mm});
            skLineSegment(sketch, "E26.0.2.201", {"start": v(444.43, 92.7) * mm, "end": v(451.62, 88.55) * mm});
            skLineSegment(sketch, "E26.0.2.202", {"start": v(188.88, 92.7) * mm, "end": v(196.07, 88.55) * mm});
            skLineSegment(sketch, "E26.0.2.203", {"start": v(369.1, 88.55) * mm, "end": v(376.29, 92.7) * mm});
            skLineSegment(sketch, "E26.0.2.204", {"start": v(87.99, 95) * mm, "end": v(95.18, 90.85) * mm});
            skLineSegment(sketch, "E26.0.2.205", {"start": v(454.28, 80.25) * mm, "end": v(454.28, 88.55) * mm});
            skLineSegment(sketch, "E26.0.2.206", {"start": v(359.24, 76.1) * mm, "end": v(352.06, 80.25) * mm});
            skLineSegment(sketch, "E26.0.2.207", {"start": v(164.66, 80.25) * mm, "end": v(164.66, 88.55) * mm});
            skLineSegment(sketch, "E26.0.2.208", {"start": v(19.84, 103.3) * mm, "end": v(19.84, 95) * mm});
            skLineSegment(sketch, "E26.0.2.209", {"start": v(410.35, 76.1) * mm, "end": v(403.17, 80.25) * mm});
            skLineSegment(sketch, "E26.0.2.210", {"start": v(79.47, 88.55) * mm, "end": v(86.66, 92.7) * mm});
            skLineSegment(sketch, "E26.0.2.211", {"start": v(400.5, 80.25) * mm, "end": v(393.32, 76.1) * mm});
            skLineSegment(sketch, "E26.0.2.212", {"start": v(289.77, 95) * mm, "end": v(289.77, 103.3) * mm});
            skLineSegment(sketch, "E26.0.2.213", {"start": v(360.58, 95) * mm, "end": v(360.58, 103.3) * mm});
            skLineSegment(sketch, "E26.0.2.214", {"start": v(180.36, 90.85) * mm, "end": v(187.55, 95) * mm});
            skLineSegment(sketch, "E26.0.2.215", {"start": v(190.2, 103.3) * mm, "end": v(190.2, 95) * mm});
            skLineSegment(sketch, "E26.0.2.216", {"start": v(144.96, 88.55) * mm, "end": v(144.96, 80.25) * mm});
            skLineSegment(sketch, "E26.0.2.217", {"start": v(96.5, 80.25) * mm, "end": v(96.5, 88.55) * mm});
            skLineSegment(sketch, "E26.0.2.218", {"start": v(68.3, 103.3) * mm, "end": v(68.3, 95) * mm});
            skLineSegment(sketch, "E26.0.2.219", {"start": v(187.55, 95) * mm, "end": v(187.55, 103.3) * mm});
            skLineSegment(sketch, "E26.0.2.220", {"start": v(342.21, 76.1) * mm, "end": v(335.02, 80.25) * mm});
            skLineSegment(sketch, "E26.0.2.221", {"start": v(136.44, 95) * mm, "end": v(136.44, 103.3) * mm});
            skLineSegment(sketch, "E26.0.2.222", {"start": v(343.54, 103.3) * mm, "end": v(343.54, 95) * mm});
            skLineSegment(sketch, "E26.0.2.223", {"start": v(231.47, 90.85) * mm, "end": v(238.66, 95) * mm});
            skLineSegment(sketch, "E26.0.2.224", {"start": v(163.33, 90.85) * mm, "end": v(156.14, 95) * mm});
            skLineSegment(sketch, "E26.0.2.225", {"start": v(70.95, 103.3) * mm, "end": v(70.95, 95) * mm});
            skLineSegment(sketch, "E26.0.2.226", {"start": v(179.04, 88.55) * mm, "end": v(179.04, 80.25) * mm});
            skLineSegment(sketch, "E26.0.2.227", {"start": v(196.07, 88.55) * mm, "end": v(196.07, 80.25) * mm});
            skLineSegment(sketch, "E26.0.2.228", {"start": v(505.39, 88.55) * mm, "end": v(512.57, 92.7) * mm});
            skLineSegment(sketch, "E26.0.2.229", {"start": v(249.84, 88.55) * mm, "end": v(257.02, 92.7) * mm});
            skLineSegment(sketch, "E26.0.2.230", {"start": v(173.17, 103.3) * mm, "end": v(173.17, 95) * mm});
            skLineSegment(sketch, "E26.0.2.231", {"start": v(213.1, 88.55) * mm, "end": v(213.1, 80.25) * mm});
            skLineSegment(sketch, "E26.0.2.232", {"start": v(445.76, 103.3) * mm, "end": v(445.76, 95) * mm});
            skLineSegment(sketch, "E26.0.2.233", {"start": v(478.5, 92.7) * mm, "end": v(485.7, 88.55) * mm});
            skLineSegment(sketch, "E26.0.2.234", {"start": v(409.03, 95) * mm, "end": v(409.03, 103.3) * mm});
            skLineSegment(sketch, "E26.0.2.235", {"start": v(496.87, 95) * mm, "end": v(504.06, 90.85) * mm});
            skLineSegment(sketch, "E26.0.2.236", {"start": v(139.1, 95) * mm, "end": v(146.29, 90.85) * mm});
            skLineSegment(sketch, "E26.0.2.237", {"start": v(272.74, 95) * mm, "end": v(265.55, 90.85) * mm});
            skLineSegment(sketch, "E26.0.2.238", {"start": v(214.44, 90.85) * mm, "end": v(207.25, 95) * mm});
            skLineSegment(sketch, "E26.0.2.239", {"start": v(342.21, 92.7) * mm, "end": v(349.4, 88.55) * mm});
            skLineSegment(sketch, "E26.0.2.240", {"start": v(495.54, 92.7) * mm, "end": v(502.73, 88.55) * mm});
            skLineSegment(sketch, "E26.0.2.241", {"start": v(36.88, 95) * mm, "end": v(44.07, 90.85) * mm});
            skLineSegment(sketch, "E26.0.2.242", {"start": v(62.44, 88.55) * mm, "end": v(69.63, 92.7) * mm});
            skLineSegment(sketch, "E26.0.2.243", {"start": v(502.73, 88.55) * mm, "end": v(502.73, 80.25) * mm});
            skLineSegment(sketch, "E26.0.2.244", {"start": v(266.88, 80.25) * mm, "end": v(266.88, 88.55) * mm});
            skLineSegment(sketch, "E26.0.2.245", {"start": v(477.18, 103.3) * mm, "end": v(477.18, 95) * mm});
            skLineSegment(sketch, "E26.0.2.246", {"start": v(257.02, 92.7) * mm, "end": v(264.21, 88.55) * mm});
            skLineSegment(sketch, "E26.0.2.247", {"start": v(207.25, 95) * mm, "end": v(207.25, 103.3) * mm});
            skLineSegment(sketch, "E26.0.2.248", {"start": v(469.99, 90.85) * mm, "end": v(462.8, 95) * mm});
            skLineSegment(sketch, "E26.0.2.249", {"start": v(394.65, 95) * mm, "end": v(401.84, 90.85) * mm});
            skLineSegment(sketch, "E26.0.2.250", {"start": v(426.07, 95) * mm, "end": v(418.88, 90.85) * mm});
            skLineSegment(sketch, "E26.0.2.251", {"start": v(110.88, 88.55) * mm, "end": v(110.88, 80.25) * mm});
            skLineSegment(sketch, "E26.0.2.252", {"start": v(137.77, 92.7) * mm, "end": v(144.96, 88.55) * mm});
            skLineSegment(sketch, "E26.0.2.253", {"start": v(323.85, 95) * mm, "end": v(316.66, 90.85) * mm});
            skLineSegment(sketch, "E26.0.2.254", {"start": v(504.06, 90.85) * mm, "end": v(511.25, 95) * mm});
            skLineSegment(sketch, "E26.0.2.255", {"start": v(68.3, 95) * mm, "end": v(61.1, 90.85) * mm});
            skLineSegment(sketch, "E26.0.2.256", {"start": v(264.21, 88.55) * mm, "end": v(264.21, 80.25) * mm});
            skLineSegment(sketch, "E26.0.2.257", {"start": v(42.74, 88.55) * mm, "end": v(42.74, 80.25) * mm});
            skLineSegment(sketch, "E26.0.2.258", {"start": v(418.88, 90.85) * mm, "end": v(411.7, 95) * mm});
            skLineSegment(sketch, "E26.0.2.259", {"start": v(147.62, 88.55) * mm, "end": v(154.8, 92.7) * mm});
            skLineSegment(sketch, "E26.0.2.260", {"start": v(205.91, 92.7) * mm, "end": v(213.1, 88.55) * mm});
            skLineSegment(sketch, "E26.0.2.261", {"start": v(403.17, 88.55) * mm, "end": v(410.35, 92.7) * mm});
            skLineSegment(sketch, "E26.0.2.262", {"start": v(113.55, 80.25) * mm, "end": v(113.55, 88.55) * mm});
            skLineSegment(sketch, "E26.0.2.263", {"start": v(383.48, 88.55) * mm, "end": v(383.48, 80.25) * mm});
            skLineSegment(sketch, "E26.0.2.264", {"start": v(317.99, 88.55) * mm, "end": v(325.18, 92.7) * mm});
            skLineSegment(sketch, "E26.0.2.265", {"start": v(417.54, 88.55) * mm, "end": v(417.54, 80.25) * mm});
            skLineSegment(sketch, "E26.0.2.266", {"start": v(352.06, 88.55) * mm, "end": v(359.24, 92.7) * mm});
            skLineSegment(sketch, "E26.0.2.267", {"start": v(386.13, 80.25) * mm, "end": v(386.13, 88.55) * mm});
            skLineSegment(sketch, "E26.0.2.268", {"start": v(103.7, 92.7) * mm, "end": v(110.88, 88.55) * mm});
            skLineSegment(sketch, "E26.0.2.269", {"start": v(112.22, 90.85) * mm, "end": v(105.03, 95) * mm});
            skLineSegment(sketch, "E26.0.2.270", {"start": v(315.32, 88.55) * mm, "end": v(315.32, 80.25) * mm});
            skLineSegment(sketch, "E26.0.2.271", {"start": v(410.35, 92.7) * mm, "end": v(417.54, 88.55) * mm});
            skLineSegment(sketch, "E26.0.2.272", {"start": v(146.29, 90.85) * mm, "end": v(153.48, 95) * mm});
            skLineSegment(sketch, "E26.0.2.273", {"start": v(400.5, 88.55) * mm, "end": v(400.5, 80.25) * mm});
            skLineSegment(sketch, "E26.0.2.274", {"start": v(505.39, 80.25) * mm, "end": v(505.39, 88.55) * mm});
            skLineSegment(sketch, "E26.0.2.275", {"start": v(119.4, 103.3) * mm, "end": v(119.4, 95) * mm});
            skLineSegment(sketch, "E26.0.2.276", {"start": v(420.2, 88.55) * mm, "end": v(427.4, 92.7) * mm});
            skLineSegment(sketch, "E26.0.2.277", {"start": v(198.73, 88.55) * mm, "end": v(205.91, 92.7) * mm});
            skLineSegment(sketch, "E26.0.2.278", {"start": v(197.4, 90.85) * mm, "end": v(204.59, 95) * mm});
            skLineSegment(sketch, "E26.0.2.279", {"start": v(317.99, 80.25) * mm, "end": v(317.99, 88.55) * mm});
            skLineSegment(sketch, "E26.0.2.280", {"start": v(428.72, 95) * mm, "end": v(435.91, 90.85) * mm});
            skLineSegment(sketch, "E26.0.2.281", {"start": v(343.54, 95) * mm, "end": v(350.73, 90.85) * mm});
            skLineSegment(sketch, "E26.0.2.282", {"start": v(427.4, 92.7) * mm, "end": v(434.59, 88.55) * mm});
            skLineSegment(sketch, "E26.0.2.283", {"start": v(350.73, 90.85) * mm, "end": v(357.92, 95) * mm});
            skLineSegment(sketch, "E26.0.2.284", {"start": v(204.59, 95) * mm, "end": v(204.59, 103.3) * mm});
            skLineSegment(sketch, "E26.0.2.285", {"start": v(62.44, 80.25) * mm, "end": v(62.44, 88.55) * mm});
            skLineSegment(sketch, "E26.0.2.286", {"start": v(45.4, 80.25) * mm, "end": v(45.4, 88.55) * mm});
            skLineSegment(sketch, "E26.0.2.287", {"start": v(454.28, 88.55) * mm, "end": v(461.46, 92.7) * mm});
            skLineSegment(sketch, "E26.0.2.288", {"start": v(461.46, 92.7) * mm, "end": v(468.65, 88.55) * mm});
            skLineSegment(sketch, "E26.0.2.289", {"start": v(393.32, 92.7) * mm, "end": v(400.5, 88.55) * mm});
            skLineSegment(sketch, "E26.0.2.290", {"start": v(59.77, 88.55) * mm, "end": v(59.77, 80.25) * mm});
            skLineSegment(sketch, "E26.0.2.291", {"start": v(352.06, 80.25) * mm, "end": v(352.06, 88.55) * mm});
            skLineSegment(sketch, "E26.0.2.292", {"start": v(265.55, 90.85) * mm, "end": v(258.36, 95) * mm});
            skLineSegment(sketch, "E26.0.2.293", {"start": v(349.4, 88.55) * mm, "end": v(349.4, 80.25) * mm});
            skLineSegment(sketch, "E26.0.2.294", {"start": v(420.2, 80.25) * mm, "end": v(420.2, 88.55) * mm});
            skLineSegment(sketch, "E26.0.2.295", {"start": v(386.13, 88.55) * mm, "end": v(393.32, 92.7) * mm});
            skLineSegment(sketch, "E26.0.2.296", {"start": v(44.07, 90.85) * mm, "end": v(51.26, 95) * mm});
            skLineSegment(sketch, "E26.0.2.297", {"start": v(403.17, 80.25) * mm, "end": v(403.17, 88.55) * mm});
            skLineSegment(sketch, "E26.0.2.298", {"start": v(384.8, 90.85) * mm, "end": v(392, 95) * mm});
            skLineSegment(sketch, "E26.0.2.299", {"start": v(45.4, 88.55) * mm, "end": v(52.58, 92.7) * mm});
            skLineSegment(sketch, "E26.0.2.300", {"start": v(511.25, 103.3) * mm, "end": v(504.06, 107.45) * mm});
            skLineSegment(sketch, "E26.0.2.301", {"start": v(504.06, 107.45) * mm, "end": v(496.87, 103.3) * mm});
            skLineSegment(sketch, "E26.0.2.302", {"start": v(494.21, 103.3) * mm, "end": v(487.02, 107.45) * mm});
            skLineSegment(sketch, "E26.0.2.303", {"start": v(487.02, 107.45) * mm, "end": v(479.83, 103.3) * mm});
            skLineSegment(sketch, "E26.0.2.304", {"start": v(443.1, 103.3) * mm, "end": v(435.91, 107.45) * mm});
            skLineSegment(sketch, "E26.0.2.305", {"start": v(367.77, 107.45) * mm, "end": v(374.96, 103.3) * mm});
            skLineSegment(sketch, "E26.0.2.306", {"start": v(333.7, 107.45) * mm, "end": v(326.5, 103.3) * mm});
            skLineSegment(sketch, "E26.0.2.307", {"start": v(435.91, 107.45) * mm, "end": v(428.72, 103.3) * mm});
            skLineSegment(sketch, "E26.0.2.308", {"start": v(418.88, 107.45) * mm, "end": v(426.07, 103.3) * mm});
            skLineSegment(sketch, "E26.0.2.309", {"start": v(411.7, 103.3) * mm, "end": v(418.88, 107.45) * mm});
            skLineSegment(sketch, "E26.0.2.310", {"start": v(357.92, 103.3) * mm, "end": v(350.73, 107.45) * mm});
            skLineSegment(sketch, "E26.0.2.311", {"start": v(401.84, 107.45) * mm, "end": v(394.65, 103.3) * mm});
            skLineSegment(sketch, "E26.0.2.312", {"start": v(350.73, 107.45) * mm, "end": v(343.54, 103.3) * mm});
            skLineSegment(sketch, "E26.0.2.313", {"start": v(340.88, 103.3) * mm, "end": v(333.7, 107.45) * mm});
            skLineSegment(sketch, "E26.0.2.314", {"start": v(460.14, 103.3) * mm, "end": v(452.95, 107.45) * mm});
            skLineSegment(sketch, "E26.0.2.315", {"start": v(392, 103.3) * mm, "end": v(384.8, 107.45) * mm});
            skLineSegment(sketch, "E26.0.2.316", {"start": v(462.8, 103.3) * mm, "end": v(469.99, 107.45) * mm});
            skLineSegment(sketch, "E26.0.2.317", {"start": v(306.8, 103.3) * mm, "end": v(299.62, 107.45) * mm});
            skLineSegment(sketch, "E26.0.2.318", {"start": v(469.99, 107.45) * mm, "end": v(477.18, 103.3) * mm});
            skLineSegment(sketch, "E26.0.2.319", {"start": v(360.58, 103.3) * mm, "end": v(367.77, 107.45) * mm});
            skLineSegment(sketch, "E26.0.2.320", {"start": v(309.47, 103.3) * mm, "end": v(316.66, 107.45) * mm});
            skLineSegment(sketch, "E26.0.2.321", {"start": v(409.03, 103.3) * mm, "end": v(401.84, 107.45) * mm});
            skLineSegment(sketch, "E26.0.2.322", {"start": v(384.8, 107.45) * mm, "end": v(377.61, 103.3) * mm});
            skLineSegment(sketch, "E26.0.2.323", {"start": v(316.66, 107.45) * mm, "end": v(323.85, 103.3) * mm});
            skLineSegment(sketch, "E26.0.2.324", {"start": v(452.95, 107.45) * mm, "end": v(445.76, 103.3) * mm});
            skLineSegment(sketch, "E26.0.2.325", {"start": v(299.62, 107.45) * mm, "end": v(292.43, 103.3) * mm});
            skLineSegment(sketch, "E26.0.2.326", {"start": v(95.18, 107.45) * mm, "end": v(87.99, 103.3) * mm});
            skLineSegment(sketch, "E26.0.2.327", {"start": v(129.25, 107.45) * mm, "end": v(122.06, 103.3) * mm});
            skLineSegment(sketch, "E26.0.2.328", {"start": v(102.37, 103.3) * mm, "end": v(95.18, 107.45) * mm});
            skLineSegment(sketch, "E26.0.2.329", {"start": v(238.66, 103.3) * mm, "end": v(231.47, 107.45) * mm});
            skLineSegment(sketch, "E26.0.2.330", {"start": v(282.58, 107.45) * mm, "end": v(275.4, 103.3) * mm});
            skLineSegment(sketch, "E26.0.2.331", {"start": v(53.92, 103.3) * mm, "end": v(61.1, 107.45) * mm});
            skLineSegment(sketch, "E26.0.2.332", {"start": v(105.03, 103.3) * mm, "end": v(112.22, 107.45) * mm});
            skLineSegment(sketch, "E26.0.2.333", {"start": v(214.44, 107.45) * mm, "end": v(221.63, 103.3) * mm});
            skLineSegment(sketch, "E26.0.2.334", {"start": v(136.44, 103.3) * mm, "end": v(129.25, 107.45) * mm});
            skLineSegment(sketch, "E26.0.2.335", {"start": v(153.48, 103.3) * mm, "end": v(146.29, 107.45) * mm});
            skLineSegment(sketch, "E26.0.2.336", {"start": v(255.7, 103.3) * mm, "end": v(248.5, 107.45) * mm});
            skLineSegment(sketch, "E26.0.2.337", {"start": v(61.1, 107.45) * mm, "end": v(68.3, 103.3) * mm});
            skLineSegment(sketch, "E26.0.2.338", {"start": v(180.36, 107.45) * mm, "end": v(173.17, 103.3) * mm});
            skLineSegment(sketch, "E26.0.2.339", {"start": v(51.26, 103.3) * mm, "end": v(44.07, 107.45) * mm});
            skLineSegment(sketch, "E26.0.2.340", {"start": v(163.33, 107.45) * mm, "end": v(170.52, 103.3) * mm});
            skLineSegment(sketch, "E26.0.2.341", {"start": v(265.55, 107.45) * mm, "end": v(272.74, 103.3) * mm});
            skLineSegment(sketch, "E26.0.2.342", {"start": v(207.25, 103.3) * mm, "end": v(214.44, 107.45) * mm});
            skLineSegment(sketch, "E26.0.2.343", {"start": v(146.29, 107.45) * mm, "end": v(139.1, 103.3) * mm});
            skLineSegment(sketch, "E26.0.2.344", {"start": v(258.36, 103.3) * mm, "end": v(265.55, 107.45) * mm});
            skLineSegment(sketch, "E26.0.2.345", {"start": v(231.47, 107.45) * mm, "end": v(224.28, 103.3) * mm});
            skLineSegment(sketch, "E26.0.2.346", {"start": v(248.5, 107.45) * mm, "end": v(241.32, 103.3) * mm});
            skLineSegment(sketch, "E26.0.2.347", {"start": v(156.14, 103.3) * mm, "end": v(163.33, 107.45) * mm});
            skLineSegment(sketch, "E26.0.2.348", {"start": v(34.22, 103.3) * mm, "end": v(27.03, 107.45) * mm});
            skLineSegment(sketch, "E26.0.2.349", {"start": v(112.22, 107.45) * mm, "end": v(119.4, 103.3) * mm});
            skLineSegment(sketch, "E26.0.2.350", {"start": v(204.59, 103.3) * mm, "end": v(197.4, 107.45) * mm});
            skLineSegment(sketch, "E26.0.2.351", {"start": v(85.33, 103.3) * mm, "end": v(78.14, 107.45) * mm});
            skLineSegment(sketch, "E26.0.2.352", {"start": v(187.55, 103.3) * mm, "end": v(180.36, 107.45) * mm});
            skLineSegment(sketch, "E26.0.2.353", {"start": v(197.4, 107.45) * mm, "end": v(190.2, 103.3) * mm});
            skLineSegment(sketch, "E26.0.2.354", {"start": v(44.07, 107.45) * mm, "end": v(36.88, 103.3) * mm});
            skLineSegment(sketch, "E26.0.2.355", {"start": v(78.14, 107.45) * mm, "end": v(70.95, 103.3) * mm});
            skLineSegment(sketch, "E26.0.2.356", {"start": v(27.03, 107.45) * mm, "end": v(19.84, 103.3) * mm});
            skLineSegment(sketch, "E26.0.2.357", {"start": v(10, 107.45) * mm, "end": v(17.19, 103.3) * mm});
            skLineSegment(sketch, "E26.0.2.358", {"start": v(2.81, 103.3) * mm, "end": v(10, 107.45) * mm});
            skLineSegment(sketch, "E26.0.3.0", {"start": v(2.81, 65.5) * mm, "end": v(2.81, 73.8) * mm});
            skLineSegment(sketch, "E26.0.3.1", {"start": v(511.25, 65.5) * mm, "end": v(511.25, 73.8) * mm});
            skLineSegment(sketch, "E26.0.3.2", {"start": v(120.74, 46.6) * mm, "end": v(113.55, 50.75) * mm});
            skLineSegment(sketch, "E26.0.3.3", {"start": v(240, 46.6) * mm, "end": v(232.8, 50.75) * mm});
            skLineSegment(sketch, "E26.0.3.4", {"start": v(519.76, 50.75) * mm, "end": v(512.57, 46.6) * mm});
            skLineSegment(sketch, "E26.0.3.5", {"start": v(18.52, 46.6) * mm, "end": v(11.33, 50.75) * mm});
            skLineSegment(sketch, "E26.0.3.6", {"start": v(383.48, 50.75) * mm, "end": v(376.29, 46.6) * mm});
            skLineSegment(sketch, "E26.0.3.7", {"start": v(274.07, 46.6) * mm, "end": v(266.88, 50.75) * mm});
            skLineSegment(sketch, "E26.0.3.8", {"start": v(315.32, 50.75) * mm, "end": v(308.13, 46.6) * mm});
            skLineSegment(sketch, "E26.0.3.9", {"start": v(86.66, 46.6) * mm, "end": v(79.47, 50.75) * mm});
            skLineSegment(sketch, "E26.0.3.10", {"start": v(10, 61.35) * mm, "end": v(2.81, 65.5) * mm});
            skLineSegment(sketch, "E26.0.3.11", {"start": v(247.18, 50.75) * mm, "end": v(240, 46.6) * mm});
            skLineSegment(sketch, "E26.0.3.12", {"start": v(325.18, 46.6) * mm, "end": v(317.99, 50.75) * mm});
            skLineSegment(sketch, "E26.0.3.13", {"start": v(257.02, 46.6) * mm, "end": v(249.84, 50.75) * mm});
            skLineSegment(sketch, "E26.0.3.14", {"start": v(35.55, 46.6) * mm, "end": v(28.36, 50.75) * mm});
            skLineSegment(sketch, "E26.0.3.15", {"start": v(127.93, 50.75) * mm, "end": v(120.74, 46.6) * mm});
            skLineSegment(sketch, "E26.0.3.16", {"start": v(196.07, 50.75) * mm, "end": v(188.88, 46.6) * mm});
            skLineSegment(sketch, "E26.0.3.17", {"start": v(308.13, 46.6) * mm, "end": v(300.95, 50.75) * mm});
            skLineSegment(sketch, "E26.0.3.18", {"start": v(298.29, 50.75) * mm, "end": v(291.1, 46.6) * mm});
            skLineSegment(sketch, "E26.0.3.19", {"start": v(332.37, 50.75) * mm, "end": v(325.18, 46.6) * mm});
            skLineSegment(sketch, "E26.0.3.20", {"start": v(11.33, 50.75) * mm, "end": v(11.33, 59.05) * mm});
            skLineSegment(sketch, "E26.0.3.21", {"start": v(519.76, 59.05) * mm, "end": v(519.76, 50.75) * mm});
            skLineSegment(sketch, "E26.0.3.22", {"start": v(461.46, 46.6) * mm, "end": v(454.28, 50.75) * mm});
            skLineSegment(sketch, "E26.0.3.23", {"start": v(230.15, 50.75) * mm, "end": v(222.96, 46.6) * mm});
            skLineSegment(sketch, "E26.0.3.24", {"start": v(300.95, 50.75) * mm, "end": v(300.95, 59.05) * mm});
            skLineSegment(sketch, "E26.0.3.25", {"start": v(42.74, 50.75) * mm, "end": v(35.55, 46.6) * mm});
            skLineSegment(sketch, "E26.0.3.26", {"start": v(17.19, 65.5) * mm, "end": v(10, 61.35) * mm});
            skLineSegment(sketch, "E26.0.3.27", {"start": v(34.22, 65.5) * mm, "end": v(34.22, 73.8) * mm});
            skLineSegment(sketch, "E26.0.3.28", {"start": v(512.57, 63.2) * mm, "end": v(519.76, 59.05) * mm});
            skLineSegment(sketch, "E26.0.3.29", {"start": v(376.29, 46.6) * mm, "end": v(369.1, 50.75) * mm});
            skLineSegment(sketch, "E26.0.3.30", {"start": v(292.43, 65.5) * mm, "end": v(299.62, 61.35) * mm});
            skLineSegment(sketch, "E26.0.3.31", {"start": v(468.65, 59.05) * mm, "end": v(468.65, 50.75) * mm});
            skLineSegment(sketch, "E26.0.3.32", {"start": v(11.33, 59.05) * mm, "end": v(18.52, 63.2) * mm});
            skLineSegment(sketch, "E26.0.3.33", {"start": v(377.61, 73.8) * mm, "end": v(377.61, 65.5) * mm});
            skLineSegment(sketch, "E26.0.3.34", {"start": v(366.43, 59.05) * mm, "end": v(366.43, 50.75) * mm});
            skLineSegment(sketch, "E26.0.3.35", {"start": v(255.7, 65.5) * mm, "end": v(255.7, 73.8) * mm});
            skLineSegment(sketch, "E26.0.3.36", {"start": v(495.54, 46.6) * mm, "end": v(488.35, 50.75) * mm});
            skLineSegment(sketch, "E26.0.3.37", {"start": v(105.03, 65.5) * mm, "end": v(105.03, 73.8) * mm});
            skLineSegment(sketch, "E26.0.3.38", {"start": v(162, 50.75) * mm, "end": v(154.8, 46.6) * mm});
            skLineSegment(sketch, "E26.0.3.39", {"start": v(93.85, 50.75) * mm, "end": v(86.66, 46.6) * mm});
            skLineSegment(sketch, "E26.0.3.40", {"start": v(25.7, 50.75) * mm, "end": v(18.52, 46.6) * mm});
            skLineSegment(sketch, "E26.0.3.41", {"start": v(110.88, 50.75) * mm, "end": v(103.7, 46.6) * mm});
            skLineSegment(sketch, "E26.0.3.42", {"start": v(281.26, 50.75) * mm, "end": v(274.07, 46.6) * mm});
            skLineSegment(sketch, "E26.0.3.43", {"start": v(171.85, 46.6) * mm, "end": v(164.66, 50.75) * mm});
            skLineSegment(sketch, "E26.0.3.44", {"start": v(298.29, 59.05) * mm, "end": v(298.29, 50.75) * mm});
            skLineSegment(sketch, "E26.0.3.45", {"start": v(281.26, 59.05) * mm, "end": v(281.26, 50.75) * mm});
            skLineSegment(sketch, "E26.0.3.46", {"start": v(374.96, 73.8) * mm, "end": v(374.96, 65.5) * mm});
            skLineSegment(sketch, "E26.0.3.47", {"start": v(502.73, 50.75) * mm, "end": v(495.54, 46.6) * mm});
            skLineSegment(sketch, "E26.0.3.48", {"start": v(144.96, 50.75) * mm, "end": v(137.77, 46.6) * mm});
            skLineSegment(sketch, "E26.0.3.49", {"start": v(76.82, 59.05) * mm, "end": v(76.82, 50.75) * mm});
            skLineSegment(sketch, "E26.0.3.50", {"start": v(102.37, 65.5) * mm, "end": v(102.37, 73.8) * mm});
            skLineSegment(sketch, "E26.0.3.51", {"start": v(179.04, 50.75) * mm, "end": v(171.85, 46.6) * mm});
            skLineSegment(sketch, "E26.0.3.52", {"start": v(52.58, 46.6) * mm, "end": v(45.4, 50.75) * mm});
            skLineSegment(sketch, "E26.0.3.53", {"start": v(17.19, 73.8) * mm, "end": v(17.19, 65.5) * mm});
            skLineSegment(sketch, "E26.0.3.54", {"start": v(205.91, 46.6) * mm, "end": v(198.73, 50.75) * mm});
            skLineSegment(sketch, "E26.0.3.55", {"start": v(154.8, 46.6) * mm, "end": v(147.62, 50.75) * mm});
            skLineSegment(sketch, "E26.0.3.56", {"start": v(299.62, 61.35) * mm, "end": v(306.8, 65.5) * mm});
            skLineSegment(sketch, "E26.0.3.57", {"start": v(306.8, 65.5) * mm, "end": v(306.8, 73.8) * mm});
            skLineSegment(sketch, "E26.0.3.58", {"start": v(291.1, 63.2) * mm, "end": v(298.29, 59.05) * mm});
            skLineSegment(sketch, "E26.0.3.59", {"start": v(213.1, 50.75) * mm, "end": v(205.91, 46.6) * mm});
            skLineSegment(sketch, "E26.0.3.60", {"start": v(238.66, 65.5) * mm, "end": v(238.66, 73.8) * mm});
            skLineSegment(sketch, "E26.0.3.61", {"start": v(76.82, 50.75) * mm, "end": v(69.63, 46.6) * mm});
            skLineSegment(sketch, "E26.0.3.62", {"start": v(434.59, 50.75) * mm, "end": v(427.4, 46.6) * mm});
            skLineSegment(sketch, "E26.0.3.63", {"start": v(309.47, 65.5) * mm, "end": v(309.47, 73.8) * mm});
            skLineSegment(sketch, "E26.0.3.64", {"start": v(366.43, 50.75) * mm, "end": v(359.24, 46.6) * mm});
            skLineSegment(sketch, "E26.0.3.65", {"start": v(468.65, 50.75) * mm, "end": v(461.46, 46.6) * mm});
            skLineSegment(sketch, "E26.0.3.66", {"start": v(478.5, 46.6) * mm, "end": v(471.32, 50.75) * mm});
            skLineSegment(sketch, "E26.0.3.67", {"start": v(222.96, 46.6) * mm, "end": v(215.77, 50.75) * mm});
            skLineSegment(sketch, "E26.0.3.68", {"start": v(512.57, 46.6) * mm, "end": v(505.39, 50.75) * mm});
            skLineSegment(sketch, "E26.0.3.69", {"start": v(427.4, 46.6) * mm, "end": v(420.2, 50.75) * mm});
            skLineSegment(sketch, "E26.0.3.70", {"start": v(291.1, 46.6) * mm, "end": v(283.91, 50.75) * mm});
            skLineSegment(sketch, "E26.0.3.71", {"start": v(444.43, 46.6) * mm, "end": v(437.24, 50.75) * mm});
            skLineSegment(sketch, "E26.0.3.72", {"start": v(369.1, 50.75) * mm, "end": v(369.1, 59.05) * mm});
            skLineSegment(sketch, "E26.0.3.73", {"start": v(188.88, 46.6) * mm, "end": v(181.7, 50.75) * mm});
            skLineSegment(sketch, "E26.0.3.74", {"start": v(79.47, 50.75) * mm, "end": v(79.47, 59.05) * mm});
            skLineSegment(sketch, "E26.0.3.75", {"start": v(264.21, 50.75) * mm, "end": v(257.02, 46.6) * mm});
            skLineSegment(sketch, "E26.0.3.76", {"start": v(485.7, 50.75) * mm, "end": v(478.5, 46.6) * mm});
            skLineSegment(sketch, "E26.0.3.77", {"start": v(241.32, 73.8) * mm, "end": v(241.32, 65.5) * mm});
            skLineSegment(sketch, "E26.0.3.78", {"start": v(283.91, 50.75) * mm, "end": v(283.91, 59.05) * mm});
            skLineSegment(sketch, "E26.0.3.79", {"start": v(496.87, 73.8) * mm, "end": v(496.87, 65.5) * mm});
            skLineSegment(sketch, "E26.0.3.80", {"start": v(122.06, 73.8) * mm, "end": v(122.06, 65.5) * mm});
            skLineSegment(sketch, "E26.0.3.81", {"start": v(96.5, 59.05) * mm, "end": v(103.7, 63.2) * mm});
            skLineSegment(sketch, "E26.0.3.82", {"start": v(308.13, 63.2) * mm, "end": v(315.32, 59.05) * mm});
            skLineSegment(sketch, "E26.0.3.83", {"start": v(113.55, 59.05) * mm, "end": v(120.74, 63.2) * mm});
            skLineSegment(sketch, "E26.0.3.84", {"start": v(190.2, 65.5) * mm, "end": v(197.4, 61.35) * mm});
            skLineSegment(sketch, "E26.0.3.85", {"start": v(249.84, 50.75) * mm, "end": v(249.84, 59.05) * mm});
            skLineSegment(sketch, "E26.0.3.86", {"start": v(230.15, 59.05) * mm, "end": v(230.15, 50.75) * mm});
            skLineSegment(sketch, "E26.0.3.87", {"start": v(411.7, 65.5) * mm, "end": v(411.7, 73.8) * mm});
            skLineSegment(sketch, "E26.0.3.88", {"start": v(221.63, 73.8) * mm, "end": v(221.63, 65.5) * mm});
            skLineSegment(sketch, "E26.0.3.89", {"start": v(130.58, 59.05) * mm, "end": v(137.77, 63.2) * mm});
            skLineSegment(sketch, "E26.0.3.90", {"start": v(323.85, 73.8) * mm, "end": v(323.85, 65.5) * mm});
            skLineSegment(sketch, "E26.0.3.91", {"start": v(258.36, 65.5) * mm, "end": v(258.36, 73.8) * mm});
            skLineSegment(sketch, "E26.0.3.92", {"start": v(215.77, 59.05) * mm, "end": v(222.96, 63.2) * mm});
            skLineSegment(sketch, "E26.0.3.93", {"start": v(272.74, 73.8) * mm, "end": v(272.74, 65.5) * mm});
            skLineSegment(sketch, "E26.0.3.94", {"start": v(35.55, 63.2) * mm, "end": v(42.74, 59.05) * mm});
            skLineSegment(sketch, "E26.0.3.95", {"start": v(215.77, 50.75) * mm, "end": v(215.77, 59.05) * mm});
            skLineSegment(sketch, "E26.0.3.96", {"start": v(292.43, 73.8) * mm, "end": v(292.43, 65.5) * mm});
            skLineSegment(sketch, "E26.0.3.97", {"start": v(359.24, 63.2) * mm, "end": v(366.43, 59.05) * mm});
            skLineSegment(sketch, "E26.0.3.98", {"start": v(367.77, 61.35) * mm, "end": v(360.58, 65.5) * mm});
            skLineSegment(sketch, "E26.0.3.99", {"start": v(335.02, 50.75) * mm, "end": v(335.02, 59.05) * mm});
            skLineSegment(sketch, "E26.0.3.100", {"start": v(462.8, 65.5) * mm, "end": v(462.8, 73.8) * mm});
            skLineSegment(sketch, "E26.0.3.101", {"start": v(485.7, 59.05) * mm, "end": v(485.7, 50.75) * mm});
            skLineSegment(sketch, "E26.0.3.102", {"start": v(153.48, 65.5) * mm, "end": v(153.48, 73.8) * mm});
            skLineSegment(sketch, "E26.0.3.103", {"start": v(51.26, 65.5) * mm, "end": v(51.26, 73.8) * mm});
            skLineSegment(sketch, "E26.0.3.104", {"start": v(162, 59.05) * mm, "end": v(162, 50.75) * mm});
            skLineSegment(sketch, "E26.0.3.105", {"start": v(222.96, 63.2) * mm, "end": v(230.15, 59.05) * mm});
            skLineSegment(sketch, "E26.0.3.106", {"start": v(357.92, 65.5) * mm, "end": v(357.92, 73.8) * mm});
            skLineSegment(sketch, "E26.0.3.107", {"start": v(488.35, 59.05) * mm, "end": v(495.54, 63.2) * mm});
            skLineSegment(sketch, "E26.0.3.108", {"start": v(374.96, 65.5) * mm, "end": v(367.77, 61.35) * mm});
            skLineSegment(sketch, "E26.0.3.109", {"start": v(471.32, 50.75) * mm, "end": v(471.32, 59.05) * mm});
            skLineSegment(sketch, "E26.0.3.110", {"start": v(335.02, 59.05) * mm, "end": v(342.21, 63.2) * mm});
            skLineSegment(sketch, "E26.0.3.111", {"start": v(340.88, 65.5) * mm, "end": v(340.88, 73.8) * mm});
            skLineSegment(sketch, "E26.0.3.112", {"start": v(401.84, 61.35) * mm, "end": v(409.03, 65.5) * mm});
            skLineSegment(sketch, "E26.0.3.113", {"start": v(428.72, 73.8) * mm, "end": v(428.72, 65.5) * mm});
            skLineSegment(sketch, "E26.0.3.114", {"start": v(426.07, 73.8) * mm, "end": v(426.07, 65.5) * mm});
            skLineSegment(sketch, "E26.0.3.115", {"start": v(333.7, 61.35) * mm, "end": v(340.88, 65.5) * mm});
            skLineSegment(sketch, "E26.0.3.116", {"start": v(451.62, 50.75) * mm, "end": v(444.43, 46.6) * mm});
            skLineSegment(sketch, "E26.0.3.117", {"start": v(393.32, 46.6) * mm, "end": v(386.13, 50.75) * mm});
            skLineSegment(sketch, "E26.0.3.118", {"start": v(300.95, 59.05) * mm, "end": v(308.13, 63.2) * mm});
            skLineSegment(sketch, "E26.0.3.119", {"start": v(59.77, 50.75) * mm, "end": v(52.58, 46.6) * mm});
            skLineSegment(sketch, "E26.0.3.120", {"start": v(86.66, 63.2) * mm, "end": v(93.85, 59.05) * mm});
            skLineSegment(sketch, "E26.0.3.121", {"start": v(198.73, 50.75) * mm, "end": v(198.73, 59.05) * mm});
            skLineSegment(sketch, "E26.0.3.122", {"start": v(164.66, 59.05) * mm, "end": v(171.85, 63.2) * mm});
            skLineSegment(sketch, "E26.0.3.123", {"start": v(349.4, 50.75) * mm, "end": v(342.21, 46.6) * mm});
            skLineSegment(sketch, "E26.0.3.124", {"start": v(435.91, 61.35) * mm, "end": v(443.1, 65.5) * mm});
            skLineSegment(sketch, "E26.0.3.125", {"start": v(332.37, 59.05) * mm, "end": v(332.37, 50.75) * mm});
            skLineSegment(sketch, "E26.0.3.126", {"start": v(69.63, 63.2) * mm, "end": v(76.82, 59.05) * mm});
            skLineSegment(sketch, "E26.0.3.127", {"start": v(394.65, 73.8) * mm, "end": v(394.65, 65.5) * mm});
            skLineSegment(sketch, "E26.0.3.128", {"start": v(36.88, 73.8) * mm, "end": v(36.88, 65.5) * mm});
            skLineSegment(sketch, "E26.0.3.129", {"start": v(147.62, 50.75) * mm, "end": v(147.62, 59.05) * mm});
            skLineSegment(sketch, "E26.0.3.130", {"start": v(170.52, 65.5) * mm, "end": v(163.33, 61.35) * mm});
            skLineSegment(sketch, "E26.0.3.131", {"start": v(224.28, 73.8) * mm, "end": v(224.28, 65.5) * mm});
            skLineSegment(sketch, "E26.0.3.132", {"start": v(266.88, 59.05) * mm, "end": v(274.07, 63.2) * mm});
            skLineSegment(sketch, "E26.0.3.133", {"start": v(221.63, 65.5) * mm, "end": v(214.44, 61.35) * mm});
            skLineSegment(sketch, "E26.0.3.134", {"start": v(471.32, 59.05) * mm, "end": v(478.5, 63.2) * mm});
            skLineSegment(sketch, "E26.0.3.135", {"start": v(53.92, 65.5) * mm, "end": v(53.92, 73.8) * mm});
            skLineSegment(sketch, "E26.0.3.136", {"start": v(460.14, 65.5) * mm, "end": v(460.14, 73.8) * mm});
            skLineSegment(sketch, "E26.0.3.137", {"start": v(154.8, 63.2) * mm, "end": v(162, 59.05) * mm});
            skLineSegment(sketch, "E26.0.3.138", {"start": v(181.7, 50.75) * mm, "end": v(181.7, 59.05) * mm});
            skLineSegment(sketch, "E26.0.3.139", {"start": v(274.07, 63.2) * mm, "end": v(281.26, 59.05) * mm});
            skLineSegment(sketch, "E26.0.3.140", {"start": v(28.36, 59.05) * mm, "end": v(35.55, 63.2) * mm});
            skLineSegment(sketch, "E26.0.3.141", {"start": v(137.77, 46.6) * mm, "end": v(130.58, 50.75) * mm});
            skLineSegment(sketch, "E26.0.3.142", {"start": v(479.83, 73.8) * mm, "end": v(479.83, 65.5) * mm});
            skLineSegment(sketch, "E26.0.3.143", {"start": v(275.4, 73.8) * mm, "end": v(275.4, 65.5) * mm});
            skLineSegment(sketch, "E26.0.3.144", {"start": v(170.52, 73.8) * mm, "end": v(170.52, 65.5) * mm});
            skLineSegment(sketch, "E26.0.3.145", {"start": v(377.61, 65.5) * mm, "end": v(384.8, 61.35) * mm});
            skLineSegment(sketch, "E26.0.3.146", {"start": v(434.59, 59.05) * mm, "end": v(434.59, 50.75) * mm});
            skLineSegment(sketch, "E26.0.3.147", {"start": v(18.52, 63.2) * mm, "end": v(25.7, 59.05) * mm});
            skLineSegment(sketch, "E26.0.3.148", {"start": v(224.28, 65.5) * mm, "end": v(231.47, 61.35) * mm});
            skLineSegment(sketch, "E26.0.3.149", {"start": v(325.18, 63.2) * mm, "end": v(332.37, 59.05) * mm});
            skLineSegment(sketch, "E26.0.3.150", {"start": v(95.18, 61.35) * mm, "end": v(102.37, 65.5) * mm});
            skLineSegment(sketch, "E26.0.3.151", {"start": v(488.35, 50.75) * mm, "end": v(488.35, 59.05) * mm});
            skLineSegment(sketch, "E26.0.3.152", {"start": v(376.29, 63.2) * mm, "end": v(383.48, 59.05) * mm});
            skLineSegment(sketch, "E26.0.3.153", {"start": v(316.66, 61.35) * mm, "end": v(309.47, 65.5) * mm});
            skLineSegment(sketch, "E26.0.3.154", {"start": v(127.93, 59.05) * mm, "end": v(127.93, 50.75) * mm});
            skLineSegment(sketch, "E26.0.3.155", {"start": v(479.83, 65.5) * mm, "end": v(487.02, 61.35) * mm});
            skLineSegment(sketch, "E26.0.3.156", {"start": v(326.5, 65.5) * mm, "end": v(333.7, 61.35) * mm});
            skLineSegment(sketch, "E26.0.3.157", {"start": v(171.85, 63.2) * mm, "end": v(179.04, 59.05) * mm});
            skLineSegment(sketch, "E26.0.3.158", {"start": v(247.18, 59.05) * mm, "end": v(247.18, 50.75) * mm});
            skLineSegment(sketch, "E26.0.3.159", {"start": v(69.63, 46.6) * mm, "end": v(62.44, 50.75) * mm});
            skLineSegment(sketch, "E26.0.3.160", {"start": v(452.95, 61.35) * mm, "end": v(460.14, 65.5) * mm});
            skLineSegment(sketch, "E26.0.3.161", {"start": v(275.4, 65.5) * mm, "end": v(282.58, 61.35) * mm});
            skLineSegment(sketch, "E26.0.3.162", {"start": v(232.8, 59.05) * mm, "end": v(240, 63.2) * mm});
            skLineSegment(sketch, "E26.0.3.163", {"start": v(122.06, 65.5) * mm, "end": v(129.25, 61.35) * mm});
            skLineSegment(sketch, "E26.0.3.164", {"start": v(417.54, 50.75) * mm, "end": v(410.35, 46.6) * mm});
            skLineSegment(sketch, "E26.0.3.165", {"start": v(139.1, 73.8) * mm, "end": v(139.1, 65.5) * mm});
            skLineSegment(sketch, "E26.0.3.166", {"start": v(443.1, 65.5) * mm, "end": v(443.1, 73.8) * mm});
            skLineSegment(sketch, "E26.0.3.167", {"start": v(232.8, 50.75) * mm, "end": v(232.8, 59.05) * mm});
            skLineSegment(sketch, "E26.0.3.168", {"start": v(61.1, 61.35) * mm, "end": v(53.92, 65.5) * mm});
            skLineSegment(sketch, "E26.0.3.169", {"start": v(437.24, 59.05) * mm, "end": v(444.43, 63.2) * mm});
            skLineSegment(sketch, "E26.0.3.170", {"start": v(78.14, 61.35) * mm, "end": v(85.33, 65.5) * mm});
            skLineSegment(sketch, "E26.0.3.171", {"start": v(85.33, 65.5) * mm, "end": v(85.33, 73.8) * mm});
            skLineSegment(sketch, "E26.0.3.172", {"start": v(445.76, 65.5) * mm, "end": v(452.95, 61.35) * mm});
            skLineSegment(sketch, "E26.0.3.173", {"start": v(240, 63.2) * mm, "end": v(247.18, 59.05) * mm});
            skLineSegment(sketch, "E26.0.3.174", {"start": v(477.18, 65.5) * mm, "end": v(469.99, 61.35) * mm});
            skLineSegment(sketch, "E26.0.3.175", {"start": v(451.62, 59.05) * mm, "end": v(451.62, 50.75) * mm});
            skLineSegment(sketch, "E26.0.3.176", {"start": v(129.25, 61.35) * mm, "end": v(136.44, 65.5) * mm});
            skLineSegment(sketch, "E26.0.3.177", {"start": v(87.99, 73.8) * mm, "end": v(87.99, 65.5) * mm});
            skLineSegment(sketch, "E26.0.3.178", {"start": v(52.58, 63.2) * mm, "end": v(59.77, 59.05) * mm});
            skLineSegment(sketch, "E26.0.3.179", {"start": v(70.95, 65.5) * mm, "end": v(78.14, 61.35) * mm});
            skLineSegment(sketch, "E26.0.3.180", {"start": v(181.7, 59.05) * mm, "end": v(188.88, 63.2) * mm});
            skLineSegment(sketch, "E26.0.3.181", {"start": v(437.24, 50.75) * mm, "end": v(437.24, 59.05) * mm});
            skLineSegment(sketch, "E26.0.3.182", {"start": v(25.7, 59.05) * mm, "end": v(25.7, 50.75) * mm});
            skLineSegment(sketch, "E26.0.3.183", {"start": v(103.7, 46.6) * mm, "end": v(96.5, 50.75) * mm});
            skLineSegment(sketch, "E26.0.3.184", {"start": v(248.5, 61.35) * mm, "end": v(255.7, 65.5) * mm});
            skLineSegment(sketch, "E26.0.3.185", {"start": v(28.36, 50.75) * mm, "end": v(28.36, 59.05) * mm});
            skLineSegment(sketch, "E26.0.3.186", {"start": v(241.32, 65.5) * mm, "end": v(248.5, 61.35) * mm});
            skLineSegment(sketch, "E26.0.3.187", {"start": v(392, 65.5) * mm, "end": v(392, 73.8) * mm});
            skLineSegment(sketch, "E26.0.3.188", {"start": v(119.4, 65.5) * mm, "end": v(112.22, 61.35) * mm});
            skLineSegment(sketch, "E26.0.3.189", {"start": v(19.84, 65.5) * mm, "end": v(27.03, 61.35) * mm});
            skLineSegment(sketch, "E26.0.3.190", {"start": v(93.85, 59.05) * mm, "end": v(93.85, 50.75) * mm});
            skLineSegment(sketch, "E26.0.3.191", {"start": v(173.17, 65.5) * mm, "end": v(180.36, 61.35) * mm});
            skLineSegment(sketch, "E26.0.3.192", {"start": v(283.91, 59.05) * mm, "end": v(291.1, 63.2) * mm});
            skLineSegment(sketch, "E26.0.3.193", {"start": v(156.14, 65.5) * mm, "end": v(156.14, 73.8) * mm});
            skLineSegment(sketch, "E26.0.3.194", {"start": v(27.03, 61.35) * mm, "end": v(34.22, 65.5) * mm});
            skLineSegment(sketch, "E26.0.3.195", {"start": v(494.21, 65.5) * mm, "end": v(494.21, 73.8) * mm});
            skLineSegment(sketch, "E26.0.3.196", {"start": v(487.02, 61.35) * mm, "end": v(494.21, 65.5) * mm});
            skLineSegment(sketch, "E26.0.3.197", {"start": v(120.74, 63.2) * mm, "end": v(127.93, 59.05) * mm});
            skLineSegment(sketch, "E26.0.3.198", {"start": v(282.58, 61.35) * mm, "end": v(289.77, 65.5) * mm});
            skLineSegment(sketch, "E26.0.3.199", {"start": v(326.5, 73.8) * mm, "end": v(326.5, 65.5) * mm});
            skLineSegment(sketch, "E26.0.3.200", {"start": v(130.58, 50.75) * mm, "end": v(130.58, 59.05) * mm});
            skLineSegment(sketch, "E26.0.3.201", {"start": v(444.43, 63.2) * mm, "end": v(451.62, 59.05) * mm});
            skLineSegment(sketch, "E26.0.3.202", {"start": v(188.88, 63.2) * mm, "end": v(196.07, 59.05) * mm});
            skLineSegment(sketch, "E26.0.3.203", {"start": v(369.1, 59.05) * mm, "end": v(376.29, 63.2) * mm});
            skLineSegment(sketch, "E26.0.3.204", {"start": v(87.99, 65.5) * mm, "end": v(95.18, 61.35) * mm});
            skLineSegment(sketch, "E26.0.3.205", {"start": v(454.28, 50.75) * mm, "end": v(454.28, 59.05) * mm});
            skLineSegment(sketch, "E26.0.3.206", {"start": v(359.24, 46.6) * mm, "end": v(352.06, 50.75) * mm});
            skLineSegment(sketch, "E26.0.3.207", {"start": v(164.66, 50.75) * mm, "end": v(164.66, 59.05) * mm});
            skLineSegment(sketch, "E26.0.3.208", {"start": v(19.84, 73.8) * mm, "end": v(19.84, 65.5) * mm});
            skLineSegment(sketch, "E26.0.3.209", {"start": v(410.35, 46.6) * mm, "end": v(403.17, 50.75) * mm});
            skLineSegment(sketch, "E26.0.3.210", {"start": v(79.47, 59.05) * mm, "end": v(86.66, 63.2) * mm});
            skLineSegment(sketch, "E26.0.3.211", {"start": v(400.5, 50.75) * mm, "end": v(393.32, 46.6) * mm});
            skLineSegment(sketch, "E26.0.3.212", {"start": v(289.77, 65.5) * mm, "end": v(289.77, 73.8) * mm});
            skLineSegment(sketch, "E26.0.3.213", {"start": v(360.58, 65.5) * mm, "end": v(360.58, 73.8) * mm});
            skLineSegment(sketch, "E26.0.3.214", {"start": v(180.36, 61.35) * mm, "end": v(187.55, 65.5) * mm});
            skLineSegment(sketch, "E26.0.3.215", {"start": v(190.2, 73.8) * mm, "end": v(190.2, 65.5) * mm});
            skLineSegment(sketch, "E26.0.3.216", {"start": v(144.96, 59.05) * mm, "end": v(144.96, 50.75) * mm});
            skLineSegment(sketch, "E26.0.3.217", {"start": v(96.5, 50.75) * mm, "end": v(96.5, 59.05) * mm});
            skLineSegment(sketch, "E26.0.3.218", {"start": v(68.3, 73.8) * mm, "end": v(68.3, 65.5) * mm});
            skLineSegment(sketch, "E26.0.3.219", {"start": v(187.55, 65.5) * mm, "end": v(187.55, 73.8) * mm});
            skLineSegment(sketch, "E26.0.3.220", {"start": v(342.21, 46.6) * mm, "end": v(335.02, 50.75) * mm});
            skLineSegment(sketch, "E26.0.3.221", {"start": v(136.44, 65.5) * mm, "end": v(136.44, 73.8) * mm});
            skLineSegment(sketch, "E26.0.3.222", {"start": v(343.54, 73.8) * mm, "end": v(343.54, 65.5) * mm});
            skLineSegment(sketch, "E26.0.3.223", {"start": v(231.47, 61.35) * mm, "end": v(238.66, 65.5) * mm});
            skLineSegment(sketch, "E26.0.3.224", {"start": v(163.33, 61.35) * mm, "end": v(156.14, 65.5) * mm});
            skLineSegment(sketch, "E26.0.3.225", {"start": v(70.95, 73.8) * mm, "end": v(70.95, 65.5) * mm});
            skLineSegment(sketch, "E26.0.3.226", {"start": v(179.04, 59.05) * mm, "end": v(179.04, 50.75) * mm});
            skLineSegment(sketch, "E26.0.3.227", {"start": v(196.07, 59.05) * mm, "end": v(196.07, 50.75) * mm});
            skLineSegment(sketch, "E26.0.3.228", {"start": v(505.39, 59.05) * mm, "end": v(512.57, 63.2) * mm});
            skLineSegment(sketch, "E26.0.3.229", {"start": v(249.84, 59.05) * mm, "end": v(257.02, 63.2) * mm});
            skLineSegment(sketch, "E26.0.3.230", {"start": v(173.17, 73.8) * mm, "end": v(173.17, 65.5) * mm});
            skLineSegment(sketch, "E26.0.3.231", {"start": v(213.1, 59.05) * mm, "end": v(213.1, 50.75) * mm});
            skLineSegment(sketch, "E26.0.3.232", {"start": v(445.76, 73.8) * mm, "end": v(445.76, 65.5) * mm});
            skLineSegment(sketch, "E26.0.3.233", {"start": v(478.5, 63.2) * mm, "end": v(485.7, 59.05) * mm});
            skLineSegment(sketch, "E26.0.3.234", {"start": v(409.03, 65.5) * mm, "end": v(409.03, 73.8) * mm});
            skLineSegment(sketch, "E26.0.3.235", {"start": v(496.87, 65.5) * mm, "end": v(504.06, 61.35) * mm});
            skLineSegment(sketch, "E26.0.3.236", {"start": v(139.1, 65.5) * mm, "end": v(146.29, 61.35) * mm});
            skLineSegment(sketch, "E26.0.3.237", {"start": v(272.74, 65.5) * mm, "end": v(265.55, 61.35) * mm});
            skLineSegment(sketch, "E26.0.3.238", {"start": v(214.44, 61.35) * mm, "end": v(207.25, 65.5) * mm});
            skLineSegment(sketch, "E26.0.3.239", {"start": v(342.21, 63.2) * mm, "end": v(349.4, 59.05) * mm});
            skLineSegment(sketch, "E26.0.3.240", {"start": v(495.54, 63.2) * mm, "end": v(502.73, 59.05) * mm});
            skLineSegment(sketch, "E26.0.3.241", {"start": v(36.88, 65.5) * mm, "end": v(44.07, 61.35) * mm});
            skLineSegment(sketch, "E26.0.3.242", {"start": v(62.44, 59.05) * mm, "end": v(69.63, 63.2) * mm});
            skLineSegment(sketch, "E26.0.3.243", {"start": v(502.73, 59.05) * mm, "end": v(502.73, 50.75) * mm});
            skLineSegment(sketch, "E26.0.3.244", {"start": v(266.88, 50.75) * mm, "end": v(266.88, 59.05) * mm});
            skLineSegment(sketch, "E26.0.3.245", {"start": v(477.18, 73.8) * mm, "end": v(477.18, 65.5) * mm});
            skLineSegment(sketch, "E26.0.3.246", {"start": v(257.02, 63.2) * mm, "end": v(264.21, 59.05) * mm});
            skLineSegment(sketch, "E26.0.3.247", {"start": v(207.25, 65.5) * mm, "end": v(207.25, 73.8) * mm});
            skLineSegment(sketch, "E26.0.3.248", {"start": v(469.99, 61.35) * mm, "end": v(462.8, 65.5) * mm});
            skLineSegment(sketch, "E26.0.3.249", {"start": v(394.65, 65.5) * mm, "end": v(401.84, 61.35) * mm});
            skLineSegment(sketch, "E26.0.3.250", {"start": v(426.07, 65.5) * mm, "end": v(418.88, 61.35) * mm});
            skLineSegment(sketch, "E26.0.3.251", {"start": v(110.88, 59.05) * mm, "end": v(110.88, 50.75) * mm});
            skLineSegment(sketch, "E26.0.3.252", {"start": v(137.77, 63.2) * mm, "end": v(144.96, 59.05) * mm});
            skLineSegment(sketch, "E26.0.3.253", {"start": v(323.85, 65.5) * mm, "end": v(316.66, 61.35) * mm});
            skLineSegment(sketch, "E26.0.3.254", {"start": v(504.06, 61.35) * mm, "end": v(511.25, 65.5) * mm});
            skLineSegment(sketch, "E26.0.3.255", {"start": v(68.3, 65.5) * mm, "end": v(61.1, 61.35) * mm});
            skLineSegment(sketch, "E26.0.3.256", {"start": v(264.21, 59.05) * mm, "end": v(264.21, 50.75) * mm});
            skLineSegment(sketch, "E26.0.3.257", {"start": v(42.74, 59.05) * mm, "end": v(42.74, 50.75) * mm});
            skLineSegment(sketch, "E26.0.3.258", {"start": v(418.88, 61.35) * mm, "end": v(411.7, 65.5) * mm});
            skLineSegment(sketch, "E26.0.3.259", {"start": v(147.62, 59.05) * mm, "end": v(154.8, 63.2) * mm});
            skLineSegment(sketch, "E26.0.3.260", {"start": v(205.91, 63.2) * mm, "end": v(213.1, 59.05) * mm});
            skLineSegment(sketch, "E26.0.3.261", {"start": v(403.17, 59.05) * mm, "end": v(410.35, 63.2) * mm});
            skLineSegment(sketch, "E26.0.3.262", {"start": v(113.55, 50.75) * mm, "end": v(113.55, 59.05) * mm});
            skLineSegment(sketch, "E26.0.3.263", {"start": v(383.48, 59.05) * mm, "end": v(383.48, 50.75) * mm});
            skLineSegment(sketch, "E26.0.3.264", {"start": v(317.99, 59.05) * mm, "end": v(325.18, 63.2) * mm});
            skLineSegment(sketch, "E26.0.3.265", {"start": v(417.54, 59.05) * mm, "end": v(417.54, 50.75) * mm});
            skLineSegment(sketch, "E26.0.3.266", {"start": v(352.06, 59.05) * mm, "end": v(359.24, 63.2) * mm});
            skLineSegment(sketch, "E26.0.3.267", {"start": v(386.13, 50.75) * mm, "end": v(386.13, 59.05) * mm});
            skLineSegment(sketch, "E26.0.3.268", {"start": v(103.7, 63.2) * mm, "end": v(110.88, 59.05) * mm});
            skLineSegment(sketch, "E26.0.3.269", {"start": v(112.22, 61.35) * mm, "end": v(105.03, 65.5) * mm});
            skLineSegment(sketch, "E26.0.3.270", {"start": v(315.32, 59.05) * mm, "end": v(315.32, 50.75) * mm});
            skLineSegment(sketch, "E26.0.3.271", {"start": v(410.35, 63.2) * mm, "end": v(417.54, 59.05) * mm});
            skLineSegment(sketch, "E26.0.3.272", {"start": v(146.29, 61.35) * mm, "end": v(153.48, 65.5) * mm});
            skLineSegment(sketch, "E26.0.3.273", {"start": v(400.5, 59.05) * mm, "end": v(400.5, 50.75) * mm});
            skLineSegment(sketch, "E26.0.3.274", {"start": v(505.39, 50.75) * mm, "end": v(505.39, 59.05) * mm});
            skLineSegment(sketch, "E26.0.3.275", {"start": v(119.4, 73.8) * mm, "end": v(119.4, 65.5) * mm});
            skLineSegment(sketch, "E26.0.3.276", {"start": v(420.2, 59.05) * mm, "end": v(427.4, 63.2) * mm});
            skLineSegment(sketch, "E26.0.3.277", {"start": v(198.73, 59.05) * mm, "end": v(205.91, 63.2) * mm});
            skLineSegment(sketch, "E26.0.3.278", {"start": v(197.4, 61.35) * mm, "end": v(204.59, 65.5) * mm});
            skLineSegment(sketch, "E26.0.3.279", {"start": v(317.99, 50.75) * mm, "end": v(317.99, 59.05) * mm});
            skLineSegment(sketch, "E26.0.3.280", {"start": v(428.72, 65.5) * mm, "end": v(435.91, 61.35) * mm});
            skLineSegment(sketch, "E26.0.3.281", {"start": v(343.54, 65.5) * mm, "end": v(350.73, 61.35) * mm});
            skLineSegment(sketch, "E26.0.3.282", {"start": v(427.4, 63.2) * mm, "end": v(434.59, 59.05) * mm});
            skLineSegment(sketch, "E26.0.3.283", {"start": v(350.73, 61.35) * mm, "end": v(357.92, 65.5) * mm});
            skLineSegment(sketch, "E26.0.3.284", {"start": v(204.59, 65.5) * mm, "end": v(204.59, 73.8) * mm});
            skLineSegment(sketch, "E26.0.3.285", {"start": v(62.44, 50.75) * mm, "end": v(62.44, 59.05) * mm});
            skLineSegment(sketch, "E26.0.3.286", {"start": v(45.4, 50.75) * mm, "end": v(45.4, 59.05) * mm});
            skLineSegment(sketch, "E26.0.3.287", {"start": v(454.28, 59.05) * mm, "end": v(461.46, 63.2) * mm});
            skLineSegment(sketch, "E26.0.3.288", {"start": v(461.46, 63.2) * mm, "end": v(468.65, 59.05) * mm});
            skLineSegment(sketch, "E26.0.3.289", {"start": v(393.32, 63.2) * mm, "end": v(400.5, 59.05) * mm});
            skLineSegment(sketch, "E26.0.3.290", {"start": v(59.77, 59.05) * mm, "end": v(59.77, 50.75) * mm});
            skLineSegment(sketch, "E26.0.3.291", {"start": v(352.06, 50.75) * mm, "end": v(352.06, 59.05) * mm});
            skLineSegment(sketch, "E26.0.3.292", {"start": v(265.55, 61.35) * mm, "end": v(258.36, 65.5) * mm});
            skLineSegment(sketch, "E26.0.3.293", {"start": v(349.4, 59.05) * mm, "end": v(349.4, 50.75) * mm});
            skLineSegment(sketch, "E26.0.3.294", {"start": v(420.2, 50.75) * mm, "end": v(420.2, 59.05) * mm});
            skLineSegment(sketch, "E26.0.3.295", {"start": v(386.13, 59.05) * mm, "end": v(393.32, 63.2) * mm});
            skLineSegment(sketch, "E26.0.3.296", {"start": v(44.07, 61.35) * mm, "end": v(51.26, 65.5) * mm});
            skLineSegment(sketch, "E26.0.3.297", {"start": v(403.17, 50.75) * mm, "end": v(403.17, 59.05) * mm});
            skLineSegment(sketch, "E26.0.3.298", {"start": v(384.8, 61.35) * mm, "end": v(392, 65.5) * mm});
            skLineSegment(sketch, "E26.0.3.299", {"start": v(45.4, 59.05) * mm, "end": v(52.58, 63.2) * mm});
            skLineSegment(sketch, "E26.0.3.300", {"start": v(511.25, 73.8) * mm, "end": v(504.06, 77.95) * mm});
            skLineSegment(sketch, "E26.0.3.301", {"start": v(504.06, 77.95) * mm, "end": v(496.87, 73.8) * mm});
            skLineSegment(sketch, "E26.0.3.302", {"start": v(494.21, 73.8) * mm, "end": v(487.02, 77.95) * mm});
            skLineSegment(sketch, "E26.0.3.303", {"start": v(487.02, 77.95) * mm, "end": v(479.83, 73.8) * mm});
            skLineSegment(sketch, "E26.0.3.304", {"start": v(443.1, 73.8) * mm, "end": v(435.91, 77.95) * mm});
            skLineSegment(sketch, "E26.0.3.305", {"start": v(367.77, 77.95) * mm, "end": v(374.96, 73.8) * mm});
            skLineSegment(sketch, "E26.0.3.306", {"start": v(333.7, 77.95) * mm, "end": v(326.5, 73.8) * mm});
            skLineSegment(sketch, "E26.0.3.307", {"start": v(435.91, 77.95) * mm, "end": v(428.72, 73.8) * mm});
            skLineSegment(sketch, "E26.0.3.308", {"start": v(418.88, 77.95) * mm, "end": v(426.07, 73.8) * mm});
            skLineSegment(sketch, "E26.0.3.309", {"start": v(411.7, 73.8) * mm, "end": v(418.88, 77.95) * mm});
            skLineSegment(sketch, "E26.0.3.310", {"start": v(357.92, 73.8) * mm, "end": v(350.73, 77.95) * mm});
            skLineSegment(sketch, "E26.0.3.311", {"start": v(401.84, 77.95) * mm, "end": v(394.65, 73.8) * mm});
            skLineSegment(sketch, "E26.0.3.312", {"start": v(350.73, 77.95) * mm, "end": v(343.54, 73.8) * mm});
            skLineSegment(sketch, "E26.0.3.313", {"start": v(340.88, 73.8) * mm, "end": v(333.7, 77.95) * mm});
            skLineSegment(sketch, "E26.0.3.314", {"start": v(460.14, 73.8) * mm, "end": v(452.95, 77.95) * mm});
            skLineSegment(sketch, "E26.0.3.315", {"start": v(392, 73.8) * mm, "end": v(384.8, 77.95) * mm});
            skLineSegment(sketch, "E26.0.3.316", {"start": v(462.8, 73.8) * mm, "end": v(469.99, 77.95) * mm});
            skLineSegment(sketch, "E26.0.3.317", {"start": v(306.8, 73.8) * mm, "end": v(299.62, 77.95) * mm});
            skLineSegment(sketch, "E26.0.3.318", {"start": v(469.99, 77.95) * mm, "end": v(477.18, 73.8) * mm});
            skLineSegment(sketch, "E26.0.3.319", {"start": v(360.58, 73.8) * mm, "end": v(367.77, 77.95) * mm});
            skLineSegment(sketch, "E26.0.3.320", {"start": v(309.47, 73.8) * mm, "end": v(316.66, 77.95) * mm});
            skLineSegment(sketch, "E26.0.3.321", {"start": v(409.03, 73.8) * mm, "end": v(401.84, 77.95) * mm});
            skLineSegment(sketch, "E26.0.3.322", {"start": v(384.8, 77.95) * mm, "end": v(377.61, 73.8) * mm});
            skLineSegment(sketch, "E26.0.3.323", {"start": v(316.66, 77.95) * mm, "end": v(323.85, 73.8) * mm});
            skLineSegment(sketch, "E26.0.3.324", {"start": v(452.95, 77.95) * mm, "end": v(445.76, 73.8) * mm});
            skLineSegment(sketch, "E26.0.3.325", {"start": v(299.62, 77.95) * mm, "end": v(292.43, 73.8) * mm});
            skLineSegment(sketch, "E26.0.3.326", {"start": v(95.18, 77.95) * mm, "end": v(87.99, 73.8) * mm});
            skLineSegment(sketch, "E26.0.3.327", {"start": v(129.25, 77.95) * mm, "end": v(122.06, 73.8) * mm});
            skLineSegment(sketch, "E26.0.3.328", {"start": v(102.37, 73.8) * mm, "end": v(95.18, 77.95) * mm});
            skLineSegment(sketch, "E26.0.3.329", {"start": v(238.66, 73.8) * mm, "end": v(231.47, 77.95) * mm});
            skLineSegment(sketch, "E26.0.3.330", {"start": v(282.58, 77.95) * mm, "end": v(275.4, 73.8) * mm});
            skLineSegment(sketch, "E26.0.3.331", {"start": v(53.92, 73.8) * mm, "end": v(61.1, 77.95) * mm});
            skLineSegment(sketch, "E26.0.3.332", {"start": v(105.03, 73.8) * mm, "end": v(112.22, 77.95) * mm});
            skLineSegment(sketch, "E26.0.3.333", {"start": v(214.44, 77.95) * mm, "end": v(221.63, 73.8) * mm});
            skLineSegment(sketch, "E26.0.3.334", {"start": v(136.44, 73.8) * mm, "end": v(129.25, 77.95) * mm});
            skLineSegment(sketch, "E26.0.3.335", {"start": v(153.48, 73.8) * mm, "end": v(146.29, 77.95) * mm});
            skLineSegment(sketch, "E26.0.3.336", {"start": v(255.7, 73.8) * mm, "end": v(248.5, 77.95) * mm});
            skLineSegment(sketch, "E26.0.3.337", {"start": v(61.1, 77.95) * mm, "end": v(68.3, 73.8) * mm});
            skLineSegment(sketch, "E26.0.3.338", {"start": v(180.36, 77.95) * mm, "end": v(173.17, 73.8) * mm});
            skLineSegment(sketch, "E26.0.3.339", {"start": v(51.26, 73.8) * mm, "end": v(44.07, 77.95) * mm});
            skLineSegment(sketch, "E26.0.3.340", {"start": v(163.33, 77.95) * mm, "end": v(170.52, 73.8) * mm});
            skLineSegment(sketch, "E26.0.3.341", {"start": v(265.55, 77.95) * mm, "end": v(272.74, 73.8) * mm});
            skLineSegment(sketch, "E26.0.3.342", {"start": v(207.25, 73.8) * mm, "end": v(214.44, 77.95) * mm});
            skLineSegment(sketch, "E26.0.3.343", {"start": v(146.29, 77.95) * mm, "end": v(139.1, 73.8) * mm});
            skLineSegment(sketch, "E26.0.3.344", {"start": v(258.36, 73.8) * mm, "end": v(265.55, 77.95) * mm});
            skLineSegment(sketch, "E26.0.3.345", {"start": v(231.47, 77.95) * mm, "end": v(224.28, 73.8) * mm});
            skLineSegment(sketch, "E26.0.3.346", {"start": v(248.5, 77.95) * mm, "end": v(241.32, 73.8) * mm});
            skLineSegment(sketch, "E26.0.3.347", {"start": v(156.14, 73.8) * mm, "end": v(163.33, 77.95) * mm});
            skLineSegment(sketch, "E26.0.3.348", {"start": v(34.22, 73.8) * mm, "end": v(27.03, 77.95) * mm});
            skLineSegment(sketch, "E26.0.3.349", {"start": v(112.22, 77.95) * mm, "end": v(119.4, 73.8) * mm});
            skLineSegment(sketch, "E26.0.3.350", {"start": v(204.59, 73.8) * mm, "end": v(197.4, 77.95) * mm});
            skLineSegment(sketch, "E26.0.3.351", {"start": v(85.33, 73.8) * mm, "end": v(78.14, 77.95) * mm});
            skLineSegment(sketch, "E26.0.3.352", {"start": v(187.55, 73.8) * mm, "end": v(180.36, 77.95) * mm});
            skLineSegment(sketch, "E26.0.3.353", {"start": v(197.4, 77.95) * mm, "end": v(190.2, 73.8) * mm});
            skLineSegment(sketch, "E26.0.3.354", {"start": v(44.07, 77.95) * mm, "end": v(36.88, 73.8) * mm});
            skLineSegment(sketch, "E26.0.3.355", {"start": v(78.14, 77.95) * mm, "end": v(70.95, 73.8) * mm});
            skLineSegment(sketch, "E26.0.3.356", {"start": v(27.03, 77.95) * mm, "end": v(19.84, 73.8) * mm});
            skLineSegment(sketch, "E26.0.3.357", {"start": v(10, 77.95) * mm, "end": v(17.19, 73.8) * mm});
            skLineSegment(sketch, "E26.0.3.358", {"start": v(2.81, 73.8) * mm, "end": v(10, 77.95) * mm});
            skLineSegment(sketch, "E26.0.4.0", {"start": v(2.81, 36) * mm, "end": v(2.81, 44.3) * mm});
            skLineSegment(sketch, "E26.0.4.1", {"start": v(511.25, 36) * mm, "end": v(511.25, 44.3) * mm});
            skLineSegment(sketch, "E26.0.4.2", {"start": v(120.74, 17.1) * mm, "end": v(113.55, 21.25) * mm});
            skLineSegment(sketch, "E26.0.4.3", {"start": v(240, 17.1) * mm, "end": v(232.8, 21.25) * mm});
            skLineSegment(sketch, "E26.0.4.4", {"start": v(519.76, 21.25) * mm, "end": v(512.57, 17.1) * mm});
            skLineSegment(sketch, "E26.0.4.5", {"start": v(18.52, 17.1) * mm, "end": v(11.33, 21.25) * mm});
            skLineSegment(sketch, "E26.0.4.6", {"start": v(383.48, 21.25) * mm, "end": v(376.29, 17.1) * mm});
            skLineSegment(sketch, "E26.0.4.7", {"start": v(274.07, 17.1) * mm, "end": v(266.88, 21.25) * mm});
            skLineSegment(sketch, "E26.0.4.8", {"start": v(315.32, 21.25) * mm, "end": v(308.13, 17.1) * mm});
            skLineSegment(sketch, "E26.0.4.9", {"start": v(86.66, 17.1) * mm, "end": v(79.47, 21.25) * mm});
            skLineSegment(sketch, "E26.0.4.10", {"start": v(10, 31.85) * mm, "end": v(2.81, 36) * mm});
            skLineSegment(sketch, "E26.0.4.11", {"start": v(247.18, 21.25) * mm, "end": v(240, 17.1) * mm});
            skLineSegment(sketch, "E26.0.4.12", {"start": v(325.18, 17.1) * mm, "end": v(317.99, 21.25) * mm});
            skLineSegment(sketch, "E26.0.4.13", {"start": v(257.02, 17.1) * mm, "end": v(249.84, 21.25) * mm});
            skLineSegment(sketch, "E26.0.4.14", {"start": v(35.55, 17.1) * mm, "end": v(28.36, 21.25) * mm});
            skLineSegment(sketch, "E26.0.4.15", {"start": v(127.93, 21.25) * mm, "end": v(120.74, 17.1) * mm});
            skLineSegment(sketch, "E26.0.4.16", {"start": v(196.07, 21.25) * mm, "end": v(188.88, 17.1) * mm});
            skLineSegment(sketch, "E26.0.4.17", {"start": v(308.13, 17.1) * mm, "end": v(300.95, 21.25) * mm});
            skLineSegment(sketch, "E26.0.4.18", {"start": v(298.29, 21.25) * mm, "end": v(291.1, 17.1) * mm});
            skLineSegment(sketch, "E26.0.4.19", {"start": v(332.37, 21.25) * mm, "end": v(325.18, 17.1) * mm});
            skLineSegment(sketch, "E26.0.4.20", {"start": v(11.33, 21.25) * mm, "end": v(11.33, 29.55) * mm});
            skLineSegment(sketch, "E26.0.4.21", {"start": v(519.76, 29.55) * mm, "end": v(519.76, 21.25) * mm});
            skLineSegment(sketch, "E26.0.4.22", {"start": v(461.46, 17.1) * mm, "end": v(454.28, 21.25) * mm});
            skLineSegment(sketch, "E26.0.4.23", {"start": v(230.15, 21.25) * mm, "end": v(222.96, 17.1) * mm});
            skLineSegment(sketch, "E26.0.4.24", {"start": v(300.95, 21.25) * mm, "end": v(300.95, 29.55) * mm});
            skLineSegment(sketch, "E26.0.4.25", {"start": v(42.74, 21.25) * mm, "end": v(35.55, 17.1) * mm});
            skLineSegment(sketch, "E26.0.4.26", {"start": v(17.19, 36) * mm, "end": v(10, 31.85) * mm});
            skLineSegment(sketch, "E26.0.4.27", {"start": v(34.22, 36) * mm, "end": v(34.22, 44.3) * mm});
            skLineSegment(sketch, "E26.0.4.28", {"start": v(512.57, 33.7) * mm, "end": v(519.76, 29.55) * mm});
            skLineSegment(sketch, "E26.0.4.29", {"start": v(376.29, 17.1) * mm, "end": v(369.1, 21.25) * mm});
            skLineSegment(sketch, "E26.0.4.30", {"start": v(292.43, 36) * mm, "end": v(299.62, 31.85) * mm});
            skLineSegment(sketch, "E26.0.4.31", {"start": v(468.65, 29.55) * mm, "end": v(468.65, 21.25) * mm});
            skLineSegment(sketch, "E26.0.4.32", {"start": v(11.33, 29.55) * mm, "end": v(18.52, 33.7) * mm});
            skLineSegment(sketch, "E26.0.4.33", {"start": v(377.61, 44.3) * mm, "end": v(377.61, 36) * mm});
            skLineSegment(sketch, "E26.0.4.34", {"start": v(366.43, 29.55) * mm, "end": v(366.43, 21.25) * mm});
            skLineSegment(sketch, "E26.0.4.35", {"start": v(255.7, 36) * mm, "end": v(255.7, 44.3) * mm});
            skLineSegment(sketch, "E26.0.4.36", {"start": v(495.54, 17.1) * mm, "end": v(488.35, 21.25) * mm});
            skLineSegment(sketch, "E26.0.4.37", {"start": v(105.03, 36) * mm, "end": v(105.03, 44.3) * mm});
            skLineSegment(sketch, "E26.0.4.38", {"start": v(162, 21.25) * mm, "end": v(154.8, 17.1) * mm});
            skLineSegment(sketch, "E26.0.4.39", {"start": v(93.85, 21.25) * mm, "end": v(86.66, 17.1) * mm});
            skLineSegment(sketch, "E26.0.4.40", {"start": v(25.7, 21.25) * mm, "end": v(18.52, 17.1) * mm});
            skLineSegment(sketch, "E26.0.4.41", {"start": v(110.88, 21.25) * mm, "end": v(103.7, 17.1) * mm});
            skLineSegment(sketch, "E26.0.4.42", {"start": v(281.26, 21.25) * mm, "end": v(274.07, 17.1) * mm});
            skLineSegment(sketch, "E26.0.4.43", {"start": v(171.85, 17.1) * mm, "end": v(164.66, 21.25) * mm});
            skLineSegment(sketch, "E26.0.4.44", {"start": v(298.29, 29.55) * mm, "end": v(298.29, 21.25) * mm});
            skLineSegment(sketch, "E26.0.4.45", {"start": v(281.26, 29.55) * mm, "end": v(281.26, 21.25) * mm});
            skLineSegment(sketch, "E26.0.4.46", {"start": v(374.96, 44.3) * mm, "end": v(374.96, 36) * mm});
            skLineSegment(sketch, "E26.0.4.47", {"start": v(502.73, 21.25) * mm, "end": v(495.54, 17.1) * mm});
            skLineSegment(sketch, "E26.0.4.48", {"start": v(144.96, 21.25) * mm, "end": v(137.77, 17.1) * mm});
            skLineSegment(sketch, "E26.0.4.49", {"start": v(76.82, 29.55) * mm, "end": v(76.82, 21.25) * mm});
            skLineSegment(sketch, "E26.0.4.50", {"start": v(102.37, 36) * mm, "end": v(102.37, 44.3) * mm});
            skLineSegment(sketch, "E26.0.4.51", {"start": v(179.04, 21.25) * mm, "end": v(171.85, 17.1) * mm});
            skLineSegment(sketch, "E26.0.4.52", {"start": v(52.58, 17.1) * mm, "end": v(45.4, 21.25) * mm});
            skLineSegment(sketch, "E26.0.4.53", {"start": v(17.19, 44.3) * mm, "end": v(17.19, 36) * mm});
            skLineSegment(sketch, "E26.0.4.54", {"start": v(205.91, 17.1) * mm, "end": v(198.73, 21.25) * mm});
            skLineSegment(sketch, "E26.0.4.55", {"start": v(154.8, 17.1) * mm, "end": v(147.62, 21.25) * mm});
            skLineSegment(sketch, "E26.0.4.56", {"start": v(299.62, 31.85) * mm, "end": v(306.8, 36) * mm});
            skLineSegment(sketch, "E26.0.4.57", {"start": v(306.8, 36) * mm, "end": v(306.8, 44.3) * mm});
            skLineSegment(sketch, "E26.0.4.58", {"start": v(291.1, 33.7) * mm, "end": v(298.29, 29.55) * mm});
            skLineSegment(sketch, "E26.0.4.59", {"start": v(213.1, 21.25) * mm, "end": v(205.91, 17.1) * mm});
            skLineSegment(sketch, "E26.0.4.60", {"start": v(238.66, 36) * mm, "end": v(238.66, 44.3) * mm});
            skLineSegment(sketch, "E26.0.4.61", {"start": v(76.82, 21.25) * mm, "end": v(69.63, 17.1) * mm});
            skLineSegment(sketch, "E26.0.4.62", {"start": v(434.59, 21.25) * mm, "end": v(427.4, 17.1) * mm});
            skLineSegment(sketch, "E26.0.4.63", {"start": v(309.47, 36) * mm, "end": v(309.47, 44.3) * mm});
            skLineSegment(sketch, "E26.0.4.64", {"start": v(366.43, 21.25) * mm, "end": v(359.24, 17.1) * mm});
            skLineSegment(sketch, "E26.0.4.65", {"start": v(468.65, 21.25) * mm, "end": v(461.46, 17.1) * mm});
            skLineSegment(sketch, "E26.0.4.66", {"start": v(478.5, 17.1) * mm, "end": v(471.32, 21.25) * mm});
            skLineSegment(sketch, "E26.0.4.67", {"start": v(222.96, 17.1) * mm, "end": v(215.77, 21.25) * mm});
            skLineSegment(sketch, "E26.0.4.68", {"start": v(512.57, 17.1) * mm, "end": v(505.39, 21.25) * mm});
            skLineSegment(sketch, "E26.0.4.69", {"start": v(427.4, 17.1) * mm, "end": v(420.2, 21.25) * mm});
            skLineSegment(sketch, "E26.0.4.70", {"start": v(291.1, 17.1) * mm, "end": v(283.91, 21.25) * mm});
            skLineSegment(sketch, "E26.0.4.71", {"start": v(444.43, 17.1) * mm, "end": v(437.24, 21.25) * mm});
            skLineSegment(sketch, "E26.0.4.72", {"start": v(369.1, 21.25) * mm, "end": v(369.1, 29.55) * mm});
            skLineSegment(sketch, "E26.0.4.73", {"start": v(188.88, 17.1) * mm, "end": v(181.7, 21.25) * mm});
            skLineSegment(sketch, "E26.0.4.74", {"start": v(79.47, 21.25) * mm, "end": v(79.47, 29.55) * mm});
            skLineSegment(sketch, "E26.0.4.75", {"start": v(264.21, 21.25) * mm, "end": v(257.02, 17.1) * mm});
            skLineSegment(sketch, "E26.0.4.76", {"start": v(485.7, 21.25) * mm, "end": v(478.5, 17.1) * mm});
            skLineSegment(sketch, "E26.0.4.77", {"start": v(241.32, 44.3) * mm, "end": v(241.32, 36) * mm});
            skLineSegment(sketch, "E26.0.4.78", {"start": v(283.91, 21.25) * mm, "end": v(283.91, 29.55) * mm});
            skLineSegment(sketch, "E26.0.4.79", {"start": v(496.87, 44.3) * mm, "end": v(496.87, 36) * mm});
            skLineSegment(sketch, "E26.0.4.80", {"start": v(122.06, 44.3) * mm, "end": v(122.06, 36) * mm});
            skLineSegment(sketch, "E26.0.4.81", {"start": v(96.5, 29.55) * mm, "end": v(103.7, 33.7) * mm});
            skLineSegment(sketch, "E26.0.4.82", {"start": v(308.13, 33.7) * mm, "end": v(315.32, 29.55) * mm});
            skLineSegment(sketch, "E26.0.4.83", {"start": v(113.55, 29.55) * mm, "end": v(120.74, 33.7) * mm});
            skLineSegment(sketch, "E26.0.4.84", {"start": v(190.2, 36) * mm, "end": v(197.4, 31.85) * mm});
            skLineSegment(sketch, "E26.0.4.85", {"start": v(249.84, 21.25) * mm, "end": v(249.84, 29.55) * mm});
            skLineSegment(sketch, "E26.0.4.86", {"start": v(230.15, 29.55) * mm, "end": v(230.15, 21.25) * mm});
            skLineSegment(sketch, "E26.0.4.87", {"start": v(411.7, 36) * mm, "end": v(411.7, 44.3) * mm});
            skLineSegment(sketch, "E26.0.4.88", {"start": v(221.63, 44.3) * mm, "end": v(221.63, 36) * mm});
            skLineSegment(sketch, "E26.0.4.89", {"start": v(130.58, 29.55) * mm, "end": v(137.77, 33.7) * mm});
            skLineSegment(sketch, "E26.0.4.90", {"start": v(323.85, 44.3) * mm, "end": v(323.85, 36) * mm});
            skLineSegment(sketch, "E26.0.4.91", {"start": v(258.36, 36) * mm, "end": v(258.36, 44.3) * mm});
            skLineSegment(sketch, "E26.0.4.92", {"start": v(215.77, 29.55) * mm, "end": v(222.96, 33.7) * mm});
            skLineSegment(sketch, "E26.0.4.93", {"start": v(272.74, 44.3) * mm, "end": v(272.74, 36) * mm});
            skLineSegment(sketch, "E26.0.4.94", {"start": v(35.55, 33.7) * mm, "end": v(42.74, 29.55) * mm});
            skLineSegment(sketch, "E26.0.4.95", {"start": v(215.77, 21.25) * mm, "end": v(215.77, 29.55) * mm});
            skLineSegment(sketch, "E26.0.4.96", {"start": v(292.43, 44.3) * mm, "end": v(292.43, 36) * mm});
            skLineSegment(sketch, "E26.0.4.97", {"start": v(359.24, 33.7) * mm, "end": v(366.43, 29.55) * mm});
            skLineSegment(sketch, "E26.0.4.98", {"start": v(367.77, 31.85) * mm, "end": v(360.58, 36) * mm});
            skLineSegment(sketch, "E26.0.4.99", {"start": v(335.02, 21.25) * mm, "end": v(335.02, 29.55) * mm});
            skLineSegment(sketch, "E26.0.4.100", {"start": v(462.8, 36) * mm, "end": v(462.8, 44.3) * mm});
            skLineSegment(sketch, "E26.0.4.101", {"start": v(485.7, 29.55) * mm, "end": v(485.7, 21.25) * mm});
            skLineSegment(sketch, "E26.0.4.102", {"start": v(153.48, 36) * mm, "end": v(153.48, 44.3) * mm});
            skLineSegment(sketch, "E26.0.4.103", {"start": v(51.26, 36) * mm, "end": v(51.26, 44.3) * mm});
            skLineSegment(sketch, "E26.0.4.104", {"start": v(162, 29.55) * mm, "end": v(162, 21.25) * mm});
            skLineSegment(sketch, "E26.0.4.105", {"start": v(222.96, 33.7) * mm, "end": v(230.15, 29.55) * mm});
            skLineSegment(sketch, "E26.0.4.106", {"start": v(357.92, 36) * mm, "end": v(357.92, 44.3) * mm});
            skLineSegment(sketch, "E26.0.4.107", {"start": v(488.35, 29.55) * mm, "end": v(495.54, 33.7) * mm});
            skLineSegment(sketch, "E26.0.4.108", {"start": v(374.96, 36) * mm, "end": v(367.77, 31.85) * mm});
            skLineSegment(sketch, "E26.0.4.109", {"start": v(471.32, 21.25) * mm, "end": v(471.32, 29.55) * mm});
            skLineSegment(sketch, "E26.0.4.110", {"start": v(335.02, 29.55) * mm, "end": v(342.21, 33.7) * mm});
            skLineSegment(sketch, "E26.0.4.111", {"start": v(340.88, 36) * mm, "end": v(340.88, 44.3) * mm});
            skLineSegment(sketch, "E26.0.4.112", {"start": v(401.84, 31.85) * mm, "end": v(409.03, 36) * mm});
            skLineSegment(sketch, "E26.0.4.113", {"start": v(428.72, 44.3) * mm, "end": v(428.72, 36) * mm});
            skLineSegment(sketch, "E26.0.4.114", {"start": v(426.07, 44.3) * mm, "end": v(426.07, 36) * mm});
            skLineSegment(sketch, "E26.0.4.115", {"start": v(333.7, 31.85) * mm, "end": v(340.88, 36) * mm});
            skLineSegment(sketch, "E26.0.4.116", {"start": v(451.62, 21.25) * mm, "end": v(444.43, 17.1) * mm});
            skLineSegment(sketch, "E26.0.4.117", {"start": v(393.32, 17.1) * mm, "end": v(386.13, 21.25) * mm});
            skLineSegment(sketch, "E26.0.4.118", {"start": v(300.95, 29.55) * mm, "end": v(308.13, 33.7) * mm});
            skLineSegment(sketch, "E26.0.4.119", {"start": v(59.77, 21.25) * mm, "end": v(52.58, 17.1) * mm});
            skLineSegment(sketch, "E26.0.4.120", {"start": v(86.66, 33.7) * mm, "end": v(93.85, 29.55) * mm});
            skLineSegment(sketch, "E26.0.4.121", {"start": v(198.73, 21.25) * mm, "end": v(198.73, 29.55) * mm});
            skLineSegment(sketch, "E26.0.4.122", {"start": v(164.66, 29.55) * mm, "end": v(171.85, 33.7) * mm});
            skLineSegment(sketch, "E26.0.4.123", {"start": v(349.4, 21.25) * mm, "end": v(342.21, 17.1) * mm});
            skLineSegment(sketch, "E26.0.4.124", {"start": v(435.91, 31.85) * mm, "end": v(443.1, 36) * mm});
            skLineSegment(sketch, "E26.0.4.125", {"start": v(332.37, 29.55) * mm, "end": v(332.37, 21.25) * mm});
            skLineSegment(sketch, "E26.0.4.126", {"start": v(69.63, 33.7) * mm, "end": v(76.82, 29.55) * mm});
            skLineSegment(sketch, "E26.0.4.127", {"start": v(394.65, 44.3) * mm, "end": v(394.65, 36) * mm});
            skLineSegment(sketch, "E26.0.4.128", {"start": v(36.88, 44.3) * mm, "end": v(36.88, 36) * mm});
            skLineSegment(sketch, "E26.0.4.129", {"start": v(147.62, 21.25) * mm, "end": v(147.62, 29.55) * mm});
            skLineSegment(sketch, "E26.0.4.130", {"start": v(170.52, 36) * mm, "end": v(163.33, 31.85) * mm});
            skLineSegment(sketch, "E26.0.4.131", {"start": v(224.28, 44.3) * mm, "end": v(224.28, 36) * mm});
            skLineSegment(sketch, "E26.0.4.132", {"start": v(266.88, 29.55) * mm, "end": v(274.07, 33.7) * mm});
            skLineSegment(sketch, "E26.0.4.133", {"start": v(221.63, 36) * mm, "end": v(214.44, 31.85) * mm});
            skLineSegment(sketch, "E26.0.4.134", {"start": v(471.32, 29.55) * mm, "end": v(478.5, 33.7) * mm});
            skLineSegment(sketch, "E26.0.4.135", {"start": v(53.92, 36) * mm, "end": v(53.92, 44.3) * mm});
            skLineSegment(sketch, "E26.0.4.136", {"start": v(460.14, 36) * mm, "end": v(460.14, 44.3) * mm});
            skLineSegment(sketch, "E26.0.4.137", {"start": v(154.8, 33.7) * mm, "end": v(162, 29.55) * mm});
            skLineSegment(sketch, "E26.0.4.138", {"start": v(181.7, 21.25) * mm, "end": v(181.7, 29.55) * mm});
            skLineSegment(sketch, "E26.0.4.139", {"start": v(274.07, 33.7) * mm, "end": v(281.26, 29.55) * mm});
            skLineSegment(sketch, "E26.0.4.140", {"start": v(28.36, 29.55) * mm, "end": v(35.55, 33.7) * mm});
            skLineSegment(sketch, "E26.0.4.141", {"start": v(137.77, 17.1) * mm, "end": v(130.58, 21.25) * mm});
            skLineSegment(sketch, "E26.0.4.142", {"start": v(479.83, 44.3) * mm, "end": v(479.83, 36) * mm});
            skLineSegment(sketch, "E26.0.4.143", {"start": v(275.4, 44.3) * mm, "end": v(275.4, 36) * mm});
            skLineSegment(sketch, "E26.0.4.144", {"start": v(170.52, 44.3) * mm, "end": v(170.52, 36) * mm});
            skLineSegment(sketch, "E26.0.4.145", {"start": v(377.61, 36) * mm, "end": v(384.8, 31.85) * mm});
            skLineSegment(sketch, "E26.0.4.146", {"start": v(434.59, 29.55) * mm, "end": v(434.59, 21.25) * mm});
            skLineSegment(sketch, "E26.0.4.147", {"start": v(18.52, 33.7) * mm, "end": v(25.7, 29.55) * mm});
            skLineSegment(sketch, "E26.0.4.148", {"start": v(224.28, 36) * mm, "end": v(231.47, 31.85) * mm});
            skLineSegment(sketch, "E26.0.4.149", {"start": v(325.18, 33.7) * mm, "end": v(332.37, 29.55) * mm});
            skLineSegment(sketch, "E26.0.4.150", {"start": v(95.18, 31.85) * mm, "end": v(102.37, 36) * mm});
            skLineSegment(sketch, "E26.0.4.151", {"start": v(488.35, 21.25) * mm, "end": v(488.35, 29.55) * mm});
            skLineSegment(sketch, "E26.0.4.152", {"start": v(376.29, 33.7) * mm, "end": v(383.48, 29.55) * mm});
            skLineSegment(sketch, "E26.0.4.153", {"start": v(316.66, 31.85) * mm, "end": v(309.47, 36) * mm});
            skLineSegment(sketch, "E26.0.4.154", {"start": v(127.93, 29.55) * mm, "end": v(127.93, 21.25) * mm});
            skLineSegment(sketch, "E26.0.4.155", {"start": v(479.83, 36) * mm, "end": v(487.02, 31.85) * mm});
            skLineSegment(sketch, "E26.0.4.156", {"start": v(326.5, 36) * mm, "end": v(333.7, 31.85) * mm});
            skLineSegment(sketch, "E26.0.4.157", {"start": v(171.85, 33.7) * mm, "end": v(179.04, 29.55) * mm});
            skLineSegment(sketch, "E26.0.4.158", {"start": v(247.18, 29.55) * mm, "end": v(247.18, 21.25) * mm});
            skLineSegment(sketch, "E26.0.4.159", {"start": v(69.63, 17.1) * mm, "end": v(62.44, 21.25) * mm});
            skLineSegment(sketch, "E26.0.4.160", {"start": v(452.95, 31.85) * mm, "end": v(460.14, 36) * mm});
            skLineSegment(sketch, "E26.0.4.161", {"start": v(275.4, 36) * mm, "end": v(282.58, 31.85) * mm});
            skLineSegment(sketch, "E26.0.4.162", {"start": v(232.8, 29.55) * mm, "end": v(240, 33.7) * mm});
            skLineSegment(sketch, "E26.0.4.163", {"start": v(122.06, 36) * mm, "end": v(129.25, 31.85) * mm});
            skLineSegment(sketch, "E26.0.4.164", {"start": v(417.54, 21.25) * mm, "end": v(410.35, 17.1) * mm});
            skLineSegment(sketch, "E26.0.4.165", {"start": v(139.1, 44.3) * mm, "end": v(139.1, 36) * mm});
            skLineSegment(sketch, "E26.0.4.166", {"start": v(443.1, 36) * mm, "end": v(443.1, 44.3) * mm});
            skLineSegment(sketch, "E26.0.4.167", {"start": v(232.8, 21.25) * mm, "end": v(232.8, 29.55) * mm});
            skLineSegment(sketch, "E26.0.4.168", {"start": v(61.1, 31.85) * mm, "end": v(53.92, 36) * mm});
            skLineSegment(sketch, "E26.0.4.169", {"start": v(437.24, 29.55) * mm, "end": v(444.43, 33.7) * mm});
            skLineSegment(sketch, "E26.0.4.170", {"start": v(78.14, 31.85) * mm, "end": v(85.33, 36) * mm});
            skLineSegment(sketch, "E26.0.4.171", {"start": v(85.33, 36) * mm, "end": v(85.33, 44.3) * mm});
            skLineSegment(sketch, "E26.0.4.172", {"start": v(445.76, 36) * mm, "end": v(452.95, 31.85) * mm});
            skLineSegment(sketch, "E26.0.4.173", {"start": v(240, 33.7) * mm, "end": v(247.18, 29.55) * mm});
            skLineSegment(sketch, "E26.0.4.174", {"start": v(477.18, 36) * mm, "end": v(469.99, 31.85) * mm});
            skLineSegment(sketch, "E26.0.4.175", {"start": v(451.62, 29.55) * mm, "end": v(451.62, 21.25) * mm});
            skLineSegment(sketch, "E26.0.4.176", {"start": v(129.25, 31.85) * mm, "end": v(136.44, 36) * mm});
            skLineSegment(sketch, "E26.0.4.177", {"start": v(87.99, 44.3) * mm, "end": v(87.99, 36) * mm});
            skLineSegment(sketch, "E26.0.4.178", {"start": v(52.58, 33.7) * mm, "end": v(59.77, 29.55) * mm});
            skLineSegment(sketch, "E26.0.4.179", {"start": v(70.95, 36) * mm, "end": v(78.14, 31.85) * mm});
            skLineSegment(sketch, "E26.0.4.180", {"start": v(181.7, 29.55) * mm, "end": v(188.88, 33.7) * mm});
            skLineSegment(sketch, "E26.0.4.181", {"start": v(437.24, 21.25) * mm, "end": v(437.24, 29.55) * mm});
            skLineSegment(sketch, "E26.0.4.182", {"start": v(25.7, 29.55) * mm, "end": v(25.7, 21.25) * mm});
            skLineSegment(sketch, "E26.0.4.183", {"start": v(103.7, 17.1) * mm, "end": v(96.5, 21.25) * mm});
            skLineSegment(sketch, "E26.0.4.184", {"start": v(248.5, 31.85) * mm, "end": v(255.7, 36) * mm});
            skLineSegment(sketch, "E26.0.4.185", {"start": v(28.36, 21.25) * mm, "end": v(28.36, 29.55) * mm});
            skLineSegment(sketch, "E26.0.4.186", {"start": v(241.32, 36) * mm, "end": v(248.5, 31.85) * mm});
            skLineSegment(sketch, "E26.0.4.187", {"start": v(392, 36) * mm, "end": v(392, 44.3) * mm});
            skLineSegment(sketch, "E26.0.4.188", {"start": v(119.4, 36) * mm, "end": v(112.22, 31.85) * mm});
            skLineSegment(sketch, "E26.0.4.189", {"start": v(19.84, 36) * mm, "end": v(27.03, 31.85) * mm});
            skLineSegment(sketch, "E26.0.4.190", {"start": v(93.85, 29.55) * mm, "end": v(93.85, 21.25) * mm});
            skLineSegment(sketch, "E26.0.4.191", {"start": v(173.17, 36) * mm, "end": v(180.36, 31.85) * mm});
            skLineSegment(sketch, "E26.0.4.192", {"start": v(283.91, 29.55) * mm, "end": v(291.1, 33.7) * mm});
            skLineSegment(sketch, "E26.0.4.193", {"start": v(156.14, 36) * mm, "end": v(156.14, 44.3) * mm});
            skLineSegment(sketch, "E26.0.4.194", {"start": v(27.03, 31.85) * mm, "end": v(34.22, 36) * mm});
            skLineSegment(sketch, "E26.0.4.195", {"start": v(494.21, 36) * mm, "end": v(494.21, 44.3) * mm});
            skLineSegment(sketch, "E26.0.4.196", {"start": v(487.02, 31.85) * mm, "end": v(494.21, 36) * mm});
            skLineSegment(sketch, "E26.0.4.197", {"start": v(120.74, 33.7) * mm, "end": v(127.93, 29.55) * mm});
            skLineSegment(sketch, "E26.0.4.198", {"start": v(282.58, 31.85) * mm, "end": v(289.77, 36) * mm});
            skLineSegment(sketch, "E26.0.4.199", {"start": v(326.5, 44.3) * mm, "end": v(326.5, 36) * mm});
            skLineSegment(sketch, "E26.0.4.200", {"start": v(130.58, 21.25) * mm, "end": v(130.58, 29.55) * mm});
            skLineSegment(sketch, "E26.0.4.201", {"start": v(444.43, 33.7) * mm, "end": v(451.62, 29.55) * mm});
            skLineSegment(sketch, "E26.0.4.202", {"start": v(188.88, 33.7) * mm, "end": v(196.07, 29.55) * mm});
            skLineSegment(sketch, "E26.0.4.203", {"start": v(369.1, 29.55) * mm, "end": v(376.29, 33.7) * mm});
            skLineSegment(sketch, "E26.0.4.204", {"start": v(87.99, 36) * mm, "end": v(95.18, 31.85) * mm});
            skLineSegment(sketch, "E26.0.4.205", {"start": v(454.28, 21.25) * mm, "end": v(454.28, 29.55) * mm});
            skLineSegment(sketch, "E26.0.4.206", {"start": v(359.24, 17.1) * mm, "end": v(352.06, 21.25) * mm});
            skLineSegment(sketch, "E26.0.4.207", {"start": v(164.66, 21.25) * mm, "end": v(164.66, 29.55) * mm});
            skLineSegment(sketch, "E26.0.4.208", {"start": v(19.84, 44.3) * mm, "end": v(19.84, 36) * mm});
            skLineSegment(sketch, "E26.0.4.209", {"start": v(410.35, 17.1) * mm, "end": v(403.17, 21.25) * mm});
            skLineSegment(sketch, "E26.0.4.210", {"start": v(79.47, 29.55) * mm, "end": v(86.66, 33.7) * mm});
            skLineSegment(sketch, "E26.0.4.211", {"start": v(400.5, 21.25) * mm, "end": v(393.32, 17.1) * mm});
            skLineSegment(sketch, "E26.0.4.212", {"start": v(289.77, 36) * mm, "end": v(289.77, 44.3) * mm});
            skLineSegment(sketch, "E26.0.4.213", {"start": v(360.58, 36) * mm, "end": v(360.58, 44.3) * mm});
            skLineSegment(sketch, "E26.0.4.214", {"start": v(180.36, 31.85) * mm, "end": v(187.55, 36) * mm});
            skLineSegment(sketch, "E26.0.4.215", {"start": v(190.2, 44.3) * mm, "end": v(190.2, 36) * mm});
            skLineSegment(sketch, "E26.0.4.216", {"start": v(144.96, 29.55) * mm, "end": v(144.96, 21.25) * mm});
            skLineSegment(sketch, "E26.0.4.217", {"start": v(96.5, 21.25) * mm, "end": v(96.5, 29.55) * mm});
            skLineSegment(sketch, "E26.0.4.218", {"start": v(68.3, 44.3) * mm, "end": v(68.3, 36) * mm});
            skLineSegment(sketch, "E26.0.4.219", {"start": v(187.55, 36) * mm, "end": v(187.55, 44.3) * mm});
            skLineSegment(sketch, "E26.0.4.220", {"start": v(342.21, 17.1) * mm, "end": v(335.02, 21.25) * mm});
            skLineSegment(sketch, "E26.0.4.221", {"start": v(136.44, 36) * mm, "end": v(136.44, 44.3) * mm});
            skLineSegment(sketch, "E26.0.4.222", {"start": v(343.54, 44.3) * mm, "end": v(343.54, 36) * mm});
            skLineSegment(sketch, "E26.0.4.223", {"start": v(231.47, 31.85) * mm, "end": v(238.66, 36) * mm});
            skLineSegment(sketch, "E26.0.4.224", {"start": v(163.33, 31.85) * mm, "end": v(156.14, 36) * mm});
            skLineSegment(sketch, "E26.0.4.225", {"start": v(70.95, 44.3) * mm, "end": v(70.95, 36) * mm});
            skLineSegment(sketch, "E26.0.4.226", {"start": v(179.04, 29.55) * mm, "end": v(179.04, 21.25) * mm});
            skLineSegment(sketch, "E26.0.4.227", {"start": v(196.07, 29.55) * mm, "end": v(196.07, 21.25) * mm});
            skLineSegment(sketch, "E26.0.4.228", {"start": v(505.39, 29.55) * mm, "end": v(512.57, 33.7) * mm});
            skLineSegment(sketch, "E26.0.4.229", {"start": v(249.84, 29.55) * mm, "end": v(257.02, 33.7) * mm});
            skLineSegment(sketch, "E26.0.4.230", {"start": v(173.17, 44.3) * mm, "end": v(173.17, 36) * mm});
            skLineSegment(sketch, "E26.0.4.231", {"start": v(213.1, 29.55) * mm, "end": v(213.1, 21.25) * mm});
            skLineSegment(sketch, "E26.0.4.232", {"start": v(445.76, 44.3) * mm, "end": v(445.76, 36) * mm});
            skLineSegment(sketch, "E26.0.4.233", {"start": v(478.5, 33.7) * mm, "end": v(485.7, 29.55) * mm});
            skLineSegment(sketch, "E26.0.4.234", {"start": v(409.03, 36) * mm, "end": v(409.03, 44.3) * mm});
            skLineSegment(sketch, "E26.0.4.235", {"start": v(496.87, 36) * mm, "end": v(504.06, 31.85) * mm});
            skLineSegment(sketch, "E26.0.4.236", {"start": v(139.1, 36) * mm, "end": v(146.29, 31.85) * mm});
            skLineSegment(sketch, "E26.0.4.237", {"start": v(272.74, 36) * mm, "end": v(265.55, 31.85) * mm});
            skLineSegment(sketch, "E26.0.4.238", {"start": v(214.44, 31.85) * mm, "end": v(207.25, 36) * mm});
            skLineSegment(sketch, "E26.0.4.239", {"start": v(342.21, 33.7) * mm, "end": v(349.4, 29.55) * mm});
            skLineSegment(sketch, "E26.0.4.240", {"start": v(495.54, 33.7) * mm, "end": v(502.73, 29.55) * mm});
            skLineSegment(sketch, "E26.0.4.241", {"start": v(36.88, 36) * mm, "end": v(44.07, 31.85) * mm});
            skLineSegment(sketch, "E26.0.4.242", {"start": v(62.44, 29.55) * mm, "end": v(69.63, 33.7) * mm});
            skLineSegment(sketch, "E26.0.4.243", {"start": v(502.73, 29.55) * mm, "end": v(502.73, 21.25) * mm});
            skLineSegment(sketch, "E26.0.4.244", {"start": v(266.88, 21.25) * mm, "end": v(266.88, 29.55) * mm});
            skLineSegment(sketch, "E26.0.4.245", {"start": v(477.18, 44.3) * mm, "end": v(477.18, 36) * mm});
            skLineSegment(sketch, "E26.0.4.246", {"start": v(257.02, 33.7) * mm, "end": v(264.21, 29.55) * mm});
            skLineSegment(sketch, "E26.0.4.247", {"start": v(207.25, 36) * mm, "end": v(207.25, 44.3) * mm});
            skLineSegment(sketch, "E26.0.4.248", {"start": v(469.99, 31.85) * mm, "end": v(462.8, 36) * mm});
            skLineSegment(sketch, "E26.0.4.249", {"start": v(394.65, 36) * mm, "end": v(401.84, 31.85) * mm});
            skLineSegment(sketch, "E26.0.4.250", {"start": v(426.07, 36) * mm, "end": v(418.88, 31.85) * mm});
            skLineSegment(sketch, "E26.0.4.251", {"start": v(110.88, 29.55) * mm, "end": v(110.88, 21.25) * mm});
            skLineSegment(sketch, "E26.0.4.252", {"start": v(137.77, 33.7) * mm, "end": v(144.96, 29.55) * mm});
            skLineSegment(sketch, "E26.0.4.253", {"start": v(323.85, 36) * mm, "end": v(316.66, 31.85) * mm});
            skLineSegment(sketch, "E26.0.4.254", {"start": v(504.06, 31.85) * mm, "end": v(511.25, 36) * mm});
            skLineSegment(sketch, "E26.0.4.255", {"start": v(68.3, 36) * mm, "end": v(61.1, 31.85) * mm});
            skLineSegment(sketch, "E26.0.4.256", {"start": v(264.21, 29.55) * mm, "end": v(264.21, 21.25) * mm});
            skLineSegment(sketch, "E26.0.4.257", {"start": v(42.74, 29.55) * mm, "end": v(42.74, 21.25) * mm});
            skLineSegment(sketch, "E26.0.4.258", {"start": v(418.88, 31.85) * mm, "end": v(411.7, 36) * mm});
            skLineSegment(sketch, "E26.0.4.259", {"start": v(147.62, 29.55) * mm, "end": v(154.8, 33.7) * mm});
            skLineSegment(sketch, "E26.0.4.260", {"start": v(205.91, 33.7) * mm, "end": v(213.1, 29.55) * mm});
            skLineSegment(sketch, "E26.0.4.261", {"start": v(403.17, 29.55) * mm, "end": v(410.35, 33.7) * mm});
            skLineSegment(sketch, "E26.0.4.262", {"start": v(113.55, 21.25) * mm, "end": v(113.55, 29.55) * mm});
            skLineSegment(sketch, "E26.0.4.263", {"start": v(383.48, 29.55) * mm, "end": v(383.48, 21.25) * mm});
            skLineSegment(sketch, "E26.0.4.264", {"start": v(317.99, 29.55) * mm, "end": v(325.18, 33.7) * mm});
            skLineSegment(sketch, "E26.0.4.265", {"start": v(417.54, 29.55) * mm, "end": v(417.54, 21.25) * mm});
            skLineSegment(sketch, "E26.0.4.266", {"start": v(352.06, 29.55) * mm, "end": v(359.24, 33.7) * mm});
            skLineSegment(sketch, "E26.0.4.267", {"start": v(386.13, 21.25) * mm, "end": v(386.13, 29.55) * mm});
            skLineSegment(sketch, "E26.0.4.268", {"start": v(103.7, 33.7) * mm, "end": v(110.88, 29.55) * mm});
            skLineSegment(sketch, "E26.0.4.269", {"start": v(112.22, 31.85) * mm, "end": v(105.03, 36) * mm});
            skLineSegment(sketch, "E26.0.4.270", {"start": v(315.32, 29.55) * mm, "end": v(315.32, 21.25) * mm});
            skLineSegment(sketch, "E26.0.4.271", {"start": v(410.35, 33.7) * mm, "end": v(417.54, 29.55) * mm});
            skLineSegment(sketch, "E26.0.4.272", {"start": v(146.29, 31.85) * mm, "end": v(153.48, 36) * mm});
            skLineSegment(sketch, "E26.0.4.273", {"start": v(400.5, 29.55) * mm, "end": v(400.5, 21.25) * mm});
            skLineSegment(sketch, "E26.0.4.274", {"start": v(505.39, 21.25) * mm, "end": v(505.39, 29.55) * mm});
            skLineSegment(sketch, "E26.0.4.275", {"start": v(119.4, 44.3) * mm, "end": v(119.4, 36) * mm});
            skLineSegment(sketch, "E26.0.4.276", {"start": v(420.2, 29.55) * mm, "end": v(427.4, 33.7) * mm});
            skLineSegment(sketch, "E26.0.4.277", {"start": v(198.73, 29.55) * mm, "end": v(205.91, 33.7) * mm});
            skLineSegment(sketch, "E26.0.4.278", {"start": v(197.4, 31.85) * mm, "end": v(204.59, 36) * mm});
            skLineSegment(sketch, "E26.0.4.279", {"start": v(317.99, 21.25) * mm, "end": v(317.99, 29.55) * mm});
            skLineSegment(sketch, "E26.0.4.280", {"start": v(428.72, 36) * mm, "end": v(435.91, 31.85) * mm});
            skLineSegment(sketch, "E26.0.4.281", {"start": v(343.54, 36) * mm, "end": v(350.73, 31.85) * mm});
            skLineSegment(sketch, "E26.0.4.282", {"start": v(427.4, 33.7) * mm, "end": v(434.59, 29.55) * mm});
            skLineSegment(sketch, "E26.0.4.283", {"start": v(350.73, 31.85) * mm, "end": v(357.92, 36) * mm});
            skLineSegment(sketch, "E26.0.4.284", {"start": v(204.59, 36) * mm, "end": v(204.59, 44.3) * mm});
            skLineSegment(sketch, "E26.0.4.285", {"start": v(62.44, 21.25) * mm, "end": v(62.44, 29.55) * mm});
            skLineSegment(sketch, "E26.0.4.286", {"start": v(45.4, 21.25) * mm, "end": v(45.4, 29.55) * mm});
            skLineSegment(sketch, "E26.0.4.287", {"start": v(454.28, 29.55) * mm, "end": v(461.46, 33.7) * mm});
            skLineSegment(sketch, "E26.0.4.288", {"start": v(461.46, 33.7) * mm, "end": v(468.65, 29.55) * mm});
            skLineSegment(sketch, "E26.0.4.289", {"start": v(393.32, 33.7) * mm, "end": v(400.5, 29.55) * mm});
            skLineSegment(sketch, "E26.0.4.290", {"start": v(59.77, 29.55) * mm, "end": v(59.77, 21.25) * mm});
            skLineSegment(sketch, "E26.0.4.291", {"start": v(352.06, 21.25) * mm, "end": v(352.06, 29.55) * mm});
            skLineSegment(sketch, "E26.0.4.292", {"start": v(265.55, 31.85) * mm, "end": v(258.36, 36) * mm});
            skLineSegment(sketch, "E26.0.4.293", {"start": v(349.4, 29.55) * mm, "end": v(349.4, 21.25) * mm});
            skLineSegment(sketch, "E26.0.4.294", {"start": v(420.2, 21.25) * mm, "end": v(420.2, 29.55) * mm});
            skLineSegment(sketch, "E26.0.4.295", {"start": v(386.13, 29.55) * mm, "end": v(393.32, 33.7) * mm});
            skLineSegment(sketch, "E26.0.4.296", {"start": v(44.07, 31.85) * mm, "end": v(51.26, 36) * mm});
            skLineSegment(sketch, "E26.0.4.297", {"start": v(403.17, 21.25) * mm, "end": v(403.17, 29.55) * mm});
            skLineSegment(sketch, "E26.0.4.298", {"start": v(384.8, 31.85) * mm, "end": v(392, 36) * mm});
            skLineSegment(sketch, "E26.0.4.299", {"start": v(45.4, 29.55) * mm, "end": v(52.58, 33.7) * mm});
            skLineSegment(sketch, "E26.0.4.300", {"start": v(511.25, 44.3) * mm, "end": v(504.06, 48.45) * mm});
            skLineSegment(sketch, "E26.0.4.301", {"start": v(504.06, 48.45) * mm, "end": v(496.87, 44.3) * mm});
            skLineSegment(sketch, "E26.0.4.302", {"start": v(494.21, 44.3) * mm, "end": v(487.02, 48.45) * mm});
            skLineSegment(sketch, "E26.0.4.303", {"start": v(487.02, 48.45) * mm, "end": v(479.83, 44.3) * mm});
            skLineSegment(sketch, "E26.0.4.304", {"start": v(443.1, 44.3) * mm, "end": v(435.91, 48.45) * mm});
            skLineSegment(sketch, "E26.0.4.305", {"start": v(367.77, 48.45) * mm, "end": v(374.96, 44.3) * mm});
            skLineSegment(sketch, "E26.0.4.306", {"start": v(333.7, 48.45) * mm, "end": v(326.5, 44.3) * mm});
            skLineSegment(sketch, "E26.0.4.307", {"start": v(435.91, 48.45) * mm, "end": v(428.72, 44.3) * mm});
            skLineSegment(sketch, "E26.0.4.308", {"start": v(418.88, 48.45) * mm, "end": v(426.07, 44.3) * mm});
            skLineSegment(sketch, "E26.0.4.309", {"start": v(411.7, 44.3) * mm, "end": v(418.88, 48.45) * mm});
            skLineSegment(sketch, "E26.0.4.310", {"start": v(357.92, 44.3) * mm, "end": v(350.73, 48.45) * mm});
            skLineSegment(sketch, "E26.0.4.311", {"start": v(401.84, 48.45) * mm, "end": v(394.65, 44.3) * mm});
            skLineSegment(sketch, "E26.0.4.312", {"start": v(350.73, 48.45) * mm, "end": v(343.54, 44.3) * mm});
            skLineSegment(sketch, "E26.0.4.313", {"start": v(340.88, 44.3) * mm, "end": v(333.7, 48.45) * mm});
            skLineSegment(sketch, "E26.0.4.314", {"start": v(460.14, 44.3) * mm, "end": v(452.95, 48.45) * mm});
            skLineSegment(sketch, "E26.0.4.315", {"start": v(392, 44.3) * mm, "end": v(384.8, 48.45) * mm});
            skLineSegment(sketch, "E26.0.4.316", {"start": v(462.8, 44.3) * mm, "end": v(469.99, 48.45) * mm});
            skLineSegment(sketch, "E26.0.4.317", {"start": v(306.8, 44.3) * mm, "end": v(299.62, 48.45) * mm});
            skLineSegment(sketch, "E26.0.4.318", {"start": v(469.99, 48.45) * mm, "end": v(477.18, 44.3) * mm});
            skLineSegment(sketch, "E26.0.4.319", {"start": v(360.58, 44.3) * mm, "end": v(367.77, 48.45) * mm});
            skLineSegment(sketch, "E26.0.4.320", {"start": v(309.47, 44.3) * mm, "end": v(316.66, 48.45) * mm});
            skLineSegment(sketch, "E26.0.4.321", {"start": v(409.03, 44.3) * mm, "end": v(401.84, 48.45) * mm});
            skLineSegment(sketch, "E26.0.4.322", {"start": v(384.8, 48.45) * mm, "end": v(377.61, 44.3) * mm});
            skLineSegment(sketch, "E26.0.4.323", {"start": v(316.66, 48.45) * mm, "end": v(323.85, 44.3) * mm});
            skLineSegment(sketch, "E26.0.4.324", {"start": v(452.95, 48.45) * mm, "end": v(445.76, 44.3) * mm});
            skLineSegment(sketch, "E26.0.4.325", {"start": v(299.62, 48.45) * mm, "end": v(292.43, 44.3) * mm});
            skLineSegment(sketch, "E26.0.4.326", {"start": v(95.18, 48.45) * mm, "end": v(87.99, 44.3) * mm});
            skLineSegment(sketch, "E26.0.4.327", {"start": v(129.25, 48.45) * mm, "end": v(122.06, 44.3) * mm});
            skLineSegment(sketch, "E26.0.4.328", {"start": v(102.37, 44.3) * mm, "end": v(95.18, 48.45) * mm});
            skLineSegment(sketch, "E26.0.4.329", {"start": v(238.66, 44.3) * mm, "end": v(231.47, 48.45) * mm});
            skLineSegment(sketch, "E26.0.4.330", {"start": v(282.58, 48.45) * mm, "end": v(275.4, 44.3) * mm});
            skLineSegment(sketch, "E26.0.4.331", {"start": v(53.92, 44.3) * mm, "end": v(61.1, 48.45) * mm});
            skLineSegment(sketch, "E26.0.4.332", {"start": v(105.03, 44.3) * mm, "end": v(112.22, 48.45) * mm});
            skLineSegment(sketch, "E26.0.4.333", {"start": v(214.44, 48.45) * mm, "end": v(221.63, 44.3) * mm});
            skLineSegment(sketch, "E26.0.4.334", {"start": v(136.44, 44.3) * mm, "end": v(129.25, 48.45) * mm});
            skLineSegment(sketch, "E26.0.4.335", {"start": v(153.48, 44.3) * mm, "end": v(146.29, 48.45) * mm});
            skLineSegment(sketch, "E26.0.4.336", {"start": v(255.7, 44.3) * mm, "end": v(248.5, 48.45) * mm});
            skLineSegment(sketch, "E26.0.4.337", {"start": v(61.1, 48.45) * mm, "end": v(68.3, 44.3) * mm});
            skLineSegment(sketch, "E26.0.4.338", {"start": v(180.36, 48.45) * mm, "end": v(173.17, 44.3) * mm});
            skLineSegment(sketch, "E26.0.4.339", {"start": v(51.26, 44.3) * mm, "end": v(44.07, 48.45) * mm});
            skLineSegment(sketch, "E26.0.4.340", {"start": v(163.33, 48.45) * mm, "end": v(170.52, 44.3) * mm});
            skLineSegment(sketch, "E26.0.4.341", {"start": v(265.55, 48.45) * mm, "end": v(272.74, 44.3) * mm});
            skLineSegment(sketch, "E26.0.4.342", {"start": v(207.25, 44.3) * mm, "end": v(214.44, 48.45) * mm});
            skLineSegment(sketch, "E26.0.4.343", {"start": v(146.29, 48.45) * mm, "end": v(139.1, 44.3) * mm});
            skLineSegment(sketch, "E26.0.4.344", {"start": v(258.36, 44.3) * mm, "end": v(265.55, 48.45) * mm});
            skLineSegment(sketch, "E26.0.4.345", {"start": v(231.47, 48.45) * mm, "end": v(224.28, 44.3) * mm});
            skLineSegment(sketch, "E26.0.4.346", {"start": v(248.5, 48.45) * mm, "end": v(241.32, 44.3) * mm});
            skLineSegment(sketch, "E26.0.4.347", {"start": v(156.14, 44.3) * mm, "end": v(163.33, 48.45) * mm});
            skLineSegment(sketch, "E26.0.4.348", {"start": v(34.22, 44.3) * mm, "end": v(27.03, 48.45) * mm});
            skLineSegment(sketch, "E26.0.4.349", {"start": v(112.22, 48.45) * mm, "end": v(119.4, 44.3) * mm});
            skLineSegment(sketch, "E26.0.4.350", {"start": v(204.59, 44.3) * mm, "end": v(197.4, 48.45) * mm});
            skLineSegment(sketch, "E26.0.4.351", {"start": v(85.33, 44.3) * mm, "end": v(78.14, 48.45) * mm});
            skLineSegment(sketch, "E26.0.4.352", {"start": v(187.55, 44.3) * mm, "end": v(180.36, 48.45) * mm});
            skLineSegment(sketch, "E26.0.4.353", {"start": v(197.4, 48.45) * mm, "end": v(190.2, 44.3) * mm});
            skLineSegment(sketch, "E26.0.4.354", {"start": v(44.07, 48.45) * mm, "end": v(36.88, 44.3) * mm});
            skLineSegment(sketch, "E26.0.4.355", {"start": v(78.14, 48.45) * mm, "end": v(70.95, 44.3) * mm});
            skLineSegment(sketch, "E26.0.4.356", {"start": v(27.03, 48.45) * mm, "end": v(19.84, 44.3) * mm});
            skLineSegment(sketch, "E26.0.4.357", {"start": v(10, 48.45) * mm, "end": v(17.19, 44.3) * mm});
            skLineSegment(sketch, "E26.0.4.358", {"start": v(2.81, 44.3) * mm, "end": v(10, 48.45) * mm});
            skLineSegment(sketch, "E26.0.5.0", {"start": v(2.81, 6.5) * mm, "end": v(2.81, 14.8) * mm});
            skLineSegment(sketch, "E26.0.5.1", {"start": v(511.25, 6.5) * mm, "end": v(511.25, 14.8) * mm});
            skLineSegment(sketch, "E26.0.5.2", {"start": v(120.74, -12.4) * mm, "end": v(113.55, -8.25) * mm});
            skLineSegment(sketch, "E26.0.5.3", {"start": v(240, -12.4) * mm, "end": v(232.8, -8.25) * mm});
            skLineSegment(sketch, "E26.0.5.4", {"start": v(519.76, -8.25) * mm, "end": v(512.57, -12.4) * mm});
            skLineSegment(sketch, "E26.0.5.5", {"start": v(18.52, -12.4) * mm, "end": v(11.33, -8.25) * mm});
            skLineSegment(sketch, "E26.0.5.6", {"start": v(383.48, -8.25) * mm, "end": v(376.29, -12.4) * mm});
            skLineSegment(sketch, "E26.0.5.7", {"start": v(274.07, -12.4) * mm, "end": v(266.88, -8.25) * mm});
            skLineSegment(sketch, "E26.0.5.8", {"start": v(315.32, -8.25) * mm, "end": v(308.13, -12.4) * mm});
            skLineSegment(sketch, "E26.0.5.9", {"start": v(86.66, -12.4) * mm, "end": v(79.47, -8.25) * mm});
            skLineSegment(sketch, "E26.0.5.10", {"start": v(10, 2.35) * mm, "end": v(2.81, 6.5) * mm});
            skLineSegment(sketch, "E26.0.5.11", {"start": v(247.18, -8.25) * mm, "end": v(240, -12.4) * mm});
            skLineSegment(sketch, "E26.0.5.12", {"start": v(325.18, -12.4) * mm, "end": v(317.99, -8.25) * mm});
            skLineSegment(sketch, "E26.0.5.13", {"start": v(257.02, -12.4) * mm, "end": v(249.84, -8.25) * mm});
            skLineSegment(sketch, "E26.0.5.14", {"start": v(35.55, -12.4) * mm, "end": v(28.36, -8.25) * mm});
            skLineSegment(sketch, "E26.0.5.15", {"start": v(127.93, -8.25) * mm, "end": v(120.74, -12.4) * mm});
            skLineSegment(sketch, "E26.0.5.16", {"start": v(196.07, -8.25) * mm, "end": v(188.88, -12.4) * mm});
            skLineSegment(sketch, "E26.0.5.17", {"start": v(308.13, -12.4) * mm, "end": v(300.95, -8.25) * mm});
            skLineSegment(sketch, "E26.0.5.18", {"start": v(298.29, -8.25) * mm, "end": v(291.1, -12.4) * mm});
            skLineSegment(sketch, "E26.0.5.19", {"start": v(332.37, -8.25) * mm, "end": v(325.18, -12.4) * mm});
            skLineSegment(sketch, "E26.0.5.20", {"start": v(11.33, -8.25) * mm, "end": v(11.33, 0.05) * mm});
            skLineSegment(sketch, "E26.0.5.21", {"start": v(519.76, 0.05) * mm, "end": v(519.76, -8.25) * mm});
            skLineSegment(sketch, "E26.0.5.22", {"start": v(461.46, -12.4) * mm, "end": v(454.28, -8.25) * mm});
            skLineSegment(sketch, "E26.0.5.23", {"start": v(230.15, -8.25) * mm, "end": v(222.96, -12.4) * mm});
            skLineSegment(sketch, "E26.0.5.24", {"start": v(300.95, -8.25) * mm, "end": v(300.95, 0.05) * mm});
            skLineSegment(sketch, "E26.0.5.25", {"start": v(42.74, -8.25) * mm, "end": v(35.55, -12.4) * mm});
            skLineSegment(sketch, "E26.0.5.26", {"start": v(17.19, 6.5) * mm, "end": v(10, 2.35) * mm});
            skLineSegment(sketch, "E26.0.5.27", {"start": v(34.22, 6.5) * mm, "end": v(34.22, 14.8) * mm});
            skLineSegment(sketch, "E26.0.5.28", {"start": v(512.57, 4.2) * mm, "end": v(519.76, 0.05) * mm});
            skLineSegment(sketch, "E26.0.5.29", {"start": v(376.29, -12.4) * mm, "end": v(369.1, -8.25) * mm});
            skLineSegment(sketch, "E26.0.5.30", {"start": v(292.43, 6.5) * mm, "end": v(299.62, 2.35) * mm});
            skLineSegment(sketch, "E26.0.5.31", {"start": v(468.65, 0.05) * mm, "end": v(468.65, -8.25) * mm});
            skLineSegment(sketch, "E26.0.5.32", {"start": v(11.33, 0.05) * mm, "end": v(18.52, 4.2) * mm});
            skLineSegment(sketch, "E26.0.5.33", {"start": v(377.61, 14.8) * mm, "end": v(377.61, 6.5) * mm});
            skLineSegment(sketch, "E26.0.5.34", {"start": v(366.43, 0.05) * mm, "end": v(366.43, -8.25) * mm});
            skLineSegment(sketch, "E26.0.5.35", {"start": v(255.7, 6.5) * mm, "end": v(255.7, 14.8) * mm});
            skLineSegment(sketch, "E26.0.5.36", {"start": v(495.54, -12.4) * mm, "end": v(488.35, -8.25) * mm});
            skLineSegment(sketch, "E26.0.5.37", {"start": v(105.03, 6.5) * mm, "end": v(105.03, 14.8) * mm});
            skLineSegment(sketch, "E26.0.5.38", {"start": v(162, -8.25) * mm, "end": v(154.8, -12.4) * mm});
            skLineSegment(sketch, "E26.0.5.39", {"start": v(93.85, -8.25) * mm, "end": v(86.66, -12.4) * mm});
            skLineSegment(sketch, "E26.0.5.40", {"start": v(25.7, -8.25) * mm, "end": v(18.52, -12.4) * mm});
            skLineSegment(sketch, "E26.0.5.41", {"start": v(110.88, -8.25) * mm, "end": v(103.7, -12.4) * mm});
            skLineSegment(sketch, "E26.0.5.42", {"start": v(281.26, -8.25) * mm, "end": v(274.07, -12.4) * mm});
            skLineSegment(sketch, "E26.0.5.43", {"start": v(171.85, -12.4) * mm, "end": v(164.66, -8.25) * mm});
            skLineSegment(sketch, "E26.0.5.44", {"start": v(298.29, 0.05) * mm, "end": v(298.29, -8.25) * mm});
            skLineSegment(sketch, "E26.0.5.45", {"start": v(281.26, 0.05) * mm, "end": v(281.26, -8.25) * mm});
            skLineSegment(sketch, "E26.0.5.46", {"start": v(374.96, 14.8) * mm, "end": v(374.96, 6.5) * mm});
            skLineSegment(sketch, "E26.0.5.47", {"start": v(502.73, -8.25) * mm, "end": v(495.54, -12.4) * mm});
            skLineSegment(sketch, "E26.0.5.48", {"start": v(144.96, -8.25) * mm, "end": v(137.77, -12.4) * mm});
            skLineSegment(sketch, "E26.0.5.49", {"start": v(76.82, 0.05) * mm, "end": v(76.82, -8.25) * mm});
            skLineSegment(sketch, "E26.0.5.50", {"start": v(102.37, 6.5) * mm, "end": v(102.37, 14.8) * mm});
            skLineSegment(sketch, "E26.0.5.51", {"start": v(179.04, -8.25) * mm, "end": v(171.85, -12.4) * mm});
            skLineSegment(sketch, "E26.0.5.52", {"start": v(52.58, -12.4) * mm, "end": v(45.4, -8.25) * mm});
            skLineSegment(sketch, "E26.0.5.53", {"start": v(17.19, 14.8) * mm, "end": v(17.19, 6.5) * mm});
            skLineSegment(sketch, "E26.0.5.54", {"start": v(205.91, -12.4) * mm, "end": v(198.73, -8.25) * mm});
            skLineSegment(sketch, "E26.0.5.55", {"start": v(154.8, -12.4) * mm, "end": v(147.62, -8.25) * mm});
            skLineSegment(sketch, "E26.0.5.56", {"start": v(299.62, 2.35) * mm, "end": v(306.8, 6.5) * mm});
            skLineSegment(sketch, "E26.0.5.57", {"start": v(306.8, 6.5) * mm, "end": v(306.8, 14.8) * mm});
            skLineSegment(sketch, "E26.0.5.58", {"start": v(291.1, 4.2) * mm, "end": v(298.29, 0.05) * mm});
            skLineSegment(sketch, "E26.0.5.59", {"start": v(213.1, -8.25) * mm, "end": v(205.91, -12.4) * mm});
            skLineSegment(sketch, "E26.0.5.60", {"start": v(238.66, 6.5) * mm, "end": v(238.66, 14.8) * mm});
            skLineSegment(sketch, "E26.0.5.61", {"start": v(76.82, -8.25) * mm, "end": v(69.63, -12.4) * mm});
            skLineSegment(sketch, "E26.0.5.62", {"start": v(434.59, -8.25) * mm, "end": v(427.4, -12.4) * mm});
            skLineSegment(sketch, "E26.0.5.63", {"start": v(309.47, 6.5) * mm, "end": v(309.47, 14.8) * mm});
            skLineSegment(sketch, "E26.0.5.64", {"start": v(366.43, -8.25) * mm, "end": v(359.24, -12.4) * mm});
            skLineSegment(sketch, "E26.0.5.65", {"start": v(468.65, -8.25) * mm, "end": v(461.46, -12.4) * mm});
            skLineSegment(sketch, "E26.0.5.66", {"start": v(478.5, -12.4) * mm, "end": v(471.32, -8.25) * mm});
            skLineSegment(sketch, "E26.0.5.67", {"start": v(222.96, -12.4) * mm, "end": v(215.77, -8.25) * mm});
            skLineSegment(sketch, "E26.0.5.68", {"start": v(512.57, -12.4) * mm, "end": v(505.39, -8.25) * mm});
            skLineSegment(sketch, "E26.0.5.69", {"start": v(427.4, -12.4) * mm, "end": v(420.2, -8.25) * mm});
            skLineSegment(sketch, "E26.0.5.70", {"start": v(291.1, -12.4) * mm, "end": v(283.91, -8.25) * mm});
            skLineSegment(sketch, "E26.0.5.71", {"start": v(444.43, -12.4) * mm, "end": v(437.24, -8.25) * mm});
            skLineSegment(sketch, "E26.0.5.72", {"start": v(369.1, -8.25) * mm, "end": v(369.1, 0.05) * mm});
            skLineSegment(sketch, "E26.0.5.73", {"start": v(188.88, -12.4) * mm, "end": v(181.7, -8.25) * mm});
            skLineSegment(sketch, "E26.0.5.74", {"start": v(79.47, -8.25) * mm, "end": v(79.47, 0.05) * mm});
            skLineSegment(sketch, "E26.0.5.75", {"start": v(264.21, -8.25) * mm, "end": v(257.02, -12.4) * mm});
            skLineSegment(sketch, "E26.0.5.76", {"start": v(485.7, -8.25) * mm, "end": v(478.5, -12.4) * mm});
            skLineSegment(sketch, "E26.0.5.77", {"start": v(241.32, 14.8) * mm, "end": v(241.32, 6.5) * mm});
            skLineSegment(sketch, "E26.0.5.78", {"start": v(283.91, -8.25) * mm, "end": v(283.91, 0.05) * mm});
            skLineSegment(sketch, "E26.0.5.79", {"start": v(496.87, 14.8) * mm, "end": v(496.87, 6.5) * mm});
            skLineSegment(sketch, "E26.0.5.80", {"start": v(122.06, 14.8) * mm, "end": v(122.06, 6.5) * mm});
            skLineSegment(sketch, "E26.0.5.81", {"start": v(96.5, 0.05) * mm, "end": v(103.7, 4.2) * mm});
            skLineSegment(sketch, "E26.0.5.82", {"start": v(308.13, 4.2) * mm, "end": v(315.32, 0.05) * mm});
            skLineSegment(sketch, "E26.0.5.83", {"start": v(113.55, 0.05) * mm, "end": v(120.74, 4.2) * mm});
            skLineSegment(sketch, "E26.0.5.84", {"start": v(190.2, 6.5) * mm, "end": v(197.4, 2.35) * mm});
            skLineSegment(sketch, "E26.0.5.85", {"start": v(249.84, -8.25) * mm, "end": v(249.84, 0.05) * mm});
            skLineSegment(sketch, "E26.0.5.86", {"start": v(230.15, 0.05) * mm, "end": v(230.15, -8.25) * mm});
            skLineSegment(sketch, "E26.0.5.87", {"start": v(411.7, 6.5) * mm, "end": v(411.7, 14.8) * mm});
            skLineSegment(sketch, "E26.0.5.88", {"start": v(221.63, 14.8) * mm, "end": v(221.63, 6.5) * mm});
            skLineSegment(sketch, "E26.0.5.89", {"start": v(130.58, 0.05) * mm, "end": v(137.77, 4.2) * mm});
            skLineSegment(sketch, "E26.0.5.90", {"start": v(323.85, 14.8) * mm, "end": v(323.85, 6.5) * mm});
            skLineSegment(sketch, "E26.0.5.91", {"start": v(258.36, 6.5) * mm, "end": v(258.36, 14.8) * mm});
            skLineSegment(sketch, "E26.0.5.92", {"start": v(215.77, 0.05) * mm, "end": v(222.96, 4.2) * mm});
            skLineSegment(sketch, "E26.0.5.93", {"start": v(272.74, 14.8) * mm, "end": v(272.74, 6.5) * mm});
            skLineSegment(sketch, "E26.0.5.94", {"start": v(35.55, 4.2) * mm, "end": v(42.74, 0.05) * mm});
            skLineSegment(sketch, "E26.0.5.95", {"start": v(215.77, -8.25) * mm, "end": v(215.77, 0.05) * mm});
            skLineSegment(sketch, "E26.0.5.96", {"start": v(292.43, 14.8) * mm, "end": v(292.43, 6.5) * mm});
            skLineSegment(sketch, "E26.0.5.97", {"start": v(359.24, 4.2) * mm, "end": v(366.43, 0.05) * mm});
            skLineSegment(sketch, "E26.0.5.98", {"start": v(367.77, 2.35) * mm, "end": v(360.58, 6.5) * mm});
            skLineSegment(sketch, "E26.0.5.99", {"start": v(335.02, -8.25) * mm, "end": v(335.02, 0.05) * mm});
            skLineSegment(sketch, "E26.0.5.100", {"start": v(462.8, 6.5) * mm, "end": v(462.8, 14.8) * mm});
            skLineSegment(sketch, "E26.0.5.101", {"start": v(485.7, 0.05) * mm, "end": v(485.7, -8.25) * mm});
            skLineSegment(sketch, "E26.0.5.102", {"start": v(153.48, 6.5) * mm, "end": v(153.48, 14.8) * mm});
            skLineSegment(sketch, "E26.0.5.103", {"start": v(51.26, 6.5) * mm, "end": v(51.26, 14.8) * mm});
            skLineSegment(sketch, "E26.0.5.104", {"start": v(162, 0.05) * mm, "end": v(162, -8.25) * mm});
            skLineSegment(sketch, "E26.0.5.105", {"start": v(222.96, 4.2) * mm, "end": v(230.15, 0.05) * mm});
            skLineSegment(sketch, "E26.0.5.106", {"start": v(357.92, 6.5) * mm, "end": v(357.92, 14.8) * mm});
            skLineSegment(sketch, "E26.0.5.107", {"start": v(488.35, 0.05) * mm, "end": v(495.54, 4.2) * mm});
            skLineSegment(sketch, "E26.0.5.108", {"start": v(374.96, 6.5) * mm, "end": v(367.77, 2.35) * mm});
            skLineSegment(sketch, "E26.0.5.109", {"start": v(471.32, -8.25) * mm, "end": v(471.32, 0.05) * mm});
            skLineSegment(sketch, "E26.0.5.110", {"start": v(335.02, 0.05) * mm, "end": v(342.21, 4.2) * mm});
            skLineSegment(sketch, "E26.0.5.111", {"start": v(340.88, 6.5) * mm, "end": v(340.88, 14.8) * mm});
            skLineSegment(sketch, "E26.0.5.112", {"start": v(401.84, 2.35) * mm, "end": v(409.03, 6.5) * mm});
            skLineSegment(sketch, "E26.0.5.113", {"start": v(428.72, 14.8) * mm, "end": v(428.72, 6.5) * mm});
            skLineSegment(sketch, "E26.0.5.114", {"start": v(426.07, 14.8) * mm, "end": v(426.07, 6.5) * mm});
            skLineSegment(sketch, "E26.0.5.115", {"start": v(333.7, 2.35) * mm, "end": v(340.88, 6.5) * mm});
            skLineSegment(sketch, "E26.0.5.116", {"start": v(451.62, -8.25) * mm, "end": v(444.43, -12.4) * mm});
            skLineSegment(sketch, "E26.0.5.117", {"start": v(393.32, -12.4) * mm, "end": v(386.13, -8.25) * mm});
            skLineSegment(sketch, "E26.0.5.118", {"start": v(300.95, 0.05) * mm, "end": v(308.13, 4.2) * mm});
            skLineSegment(sketch, "E26.0.5.119", {"start": v(59.77, -8.25) * mm, "end": v(52.58, -12.4) * mm});
            skLineSegment(sketch, "E26.0.5.120", {"start": v(86.66, 4.2) * mm, "end": v(93.85, 0.05) * mm});
            skLineSegment(sketch, "E26.0.5.121", {"start": v(198.73, -8.25) * mm, "end": v(198.73, 0.05) * mm});
            skLineSegment(sketch, "E26.0.5.122", {"start": v(164.66, 0.05) * mm, "end": v(171.85, 4.2) * mm});
            skLineSegment(sketch, "E26.0.5.123", {"start": v(349.4, -8.25) * mm, "end": v(342.21, -12.4) * mm});
            skLineSegment(sketch, "E26.0.5.124", {"start": v(435.91, 2.35) * mm, "end": v(443.1, 6.5) * mm});
            skLineSegment(sketch, "E26.0.5.125", {"start": v(332.37, 0.05) * mm, "end": v(332.37, -8.25) * mm});
            skLineSegment(sketch, "E26.0.5.126", {"start": v(69.63, 4.2) * mm, "end": v(76.82, 0.05) * mm});
            skLineSegment(sketch, "E26.0.5.127", {"start": v(394.65, 14.8) * mm, "end": v(394.65, 6.5) * mm});
            skLineSegment(sketch, "E26.0.5.128", {"start": v(36.88, 14.8) * mm, "end": v(36.88, 6.5) * mm});
            skLineSegment(sketch, "E26.0.5.129", {"start": v(147.62, -8.25) * mm, "end": v(147.62, 0.05) * mm});
            skLineSegment(sketch, "E26.0.5.130", {"start": v(170.52, 6.5) * mm, "end": v(163.33, 2.35) * mm});
            skLineSegment(sketch, "E26.0.5.131", {"start": v(224.28, 14.8) * mm, "end": v(224.28, 6.5) * mm});
            skLineSegment(sketch, "E26.0.5.132", {"start": v(266.88, 0.05) * mm, "end": v(274.07, 4.2) * mm});
            skLineSegment(sketch, "E26.0.5.133", {"start": v(221.63, 6.5) * mm, "end": v(214.44, 2.35) * mm});
            skLineSegment(sketch, "E26.0.5.134", {"start": v(471.32, 0.05) * mm, "end": v(478.5, 4.2) * mm});
            skLineSegment(sketch, "E26.0.5.135", {"start": v(53.92, 6.5) * mm, "end": v(53.92, 14.8) * mm});
            skLineSegment(sketch, "E26.0.5.136", {"start": v(460.14, 6.5) * mm, "end": v(460.14, 14.8) * mm});
            skLineSegment(sketch, "E26.0.5.137", {"start": v(154.8, 4.2) * mm, "end": v(162, 0.05) * mm});
            skLineSegment(sketch, "E26.0.5.138", {"start": v(181.7, -8.25) * mm, "end": v(181.7, 0.05) * mm});
            skLineSegment(sketch, "E26.0.5.139", {"start": v(274.07, 4.2) * mm, "end": v(281.26, 0.05) * mm});
            skLineSegment(sketch, "E26.0.5.140", {"start": v(28.36, 0.05) * mm, "end": v(35.55, 4.2) * mm});
            skLineSegment(sketch, "E26.0.5.141", {"start": v(137.77, -12.4) * mm, "end": v(130.58, -8.25) * mm});
            skLineSegment(sketch, "E26.0.5.142", {"start": v(479.83, 14.8) * mm, "end": v(479.83, 6.5) * mm});
            skLineSegment(sketch, "E26.0.5.143", {"start": v(275.4, 14.8) * mm, "end": v(275.4, 6.5) * mm});
            skLineSegment(sketch, "E26.0.5.144", {"start": v(170.52, 14.8) * mm, "end": v(170.52, 6.5) * mm});
            skLineSegment(sketch, "E26.0.5.145", {"start": v(377.61, 6.5) * mm, "end": v(384.8, 2.35) * mm});
            skLineSegment(sketch, "E26.0.5.146", {"start": v(434.59, 0.05) * mm, "end": v(434.59, -8.25) * mm});
            skLineSegment(sketch, "E26.0.5.147", {"start": v(18.52, 4.2) * mm, "end": v(25.7, 0.05) * mm});
            skLineSegment(sketch, "E26.0.5.148", {"start": v(224.28, 6.5) * mm, "end": v(231.47, 2.35) * mm});
            skLineSegment(sketch, "E26.0.5.149", {"start": v(325.18, 4.2) * mm, "end": v(332.37, 0.05) * mm});
            skLineSegment(sketch, "E26.0.5.150", {"start": v(95.18, 2.35) * mm, "end": v(102.37, 6.5) * mm});
            skLineSegment(sketch, "E26.0.5.151", {"start": v(488.35, -8.25) * mm, "end": v(488.35, 0.05) * mm});
            skLineSegment(sketch, "E26.0.5.152", {"start": v(376.29, 4.2) * mm, "end": v(383.48, 0.05) * mm});
            skLineSegment(sketch, "E26.0.5.153", {"start": v(316.66, 2.35) * mm, "end": v(309.47, 6.5) * mm});
            skLineSegment(sketch, "E26.0.5.154", {"start": v(127.93, 0.05) * mm, "end": v(127.93, -8.25) * mm});
            skLineSegment(sketch, "E26.0.5.155", {"start": v(479.83, 6.5) * mm, "end": v(487.02, 2.35) * mm});
            skLineSegment(sketch, "E26.0.5.156", {"start": v(326.5, 6.5) * mm, "end": v(333.7, 2.35) * mm});
            skLineSegment(sketch, "E26.0.5.157", {"start": v(171.85, 4.2) * mm, "end": v(179.04, 0.05) * mm});
            skLineSegment(sketch, "E26.0.5.158", {"start": v(247.18, 0.05) * mm, "end": v(247.18, -8.25) * mm});
            skLineSegment(sketch, "E26.0.5.159", {"start": v(69.63, -12.4) * mm, "end": v(62.44, -8.25) * mm});
            skLineSegment(sketch, "E26.0.5.160", {"start": v(452.95, 2.35) * mm, "end": v(460.14, 6.5) * mm});
            skLineSegment(sketch, "E26.0.5.161", {"start": v(275.4, 6.5) * mm, "end": v(282.58, 2.35) * mm});
            skLineSegment(sketch, "E26.0.5.162", {"start": v(232.8, 0.05) * mm, "end": v(240, 4.2) * mm});
            skLineSegment(sketch, "E26.0.5.163", {"start": v(122.06, 6.5) * mm, "end": v(129.25, 2.35) * mm});
            skLineSegment(sketch, "E26.0.5.164", {"start": v(417.54, -8.25) * mm, "end": v(410.35, -12.4) * mm});
            skLineSegment(sketch, "E26.0.5.165", {"start": v(139.1, 14.8) * mm, "end": v(139.1, 6.5) * mm});
            skLineSegment(sketch, "E26.0.5.166", {"start": v(443.1, 6.5) * mm, "end": v(443.1, 14.8) * mm});
            skLineSegment(sketch, "E26.0.5.167", {"start": v(232.8, -8.25) * mm, "end": v(232.8, 0.05) * mm});
            skLineSegment(sketch, "E26.0.5.168", {"start": v(61.1, 2.35) * mm, "end": v(53.92, 6.5) * mm});
            skLineSegment(sketch, "E26.0.5.169", {"start": v(437.24, 0.05) * mm, "end": v(444.43, 4.2) * mm});
            skLineSegment(sketch, "E26.0.5.170", {"start": v(78.14, 2.35) * mm, "end": v(85.33, 6.5) * mm});
            skLineSegment(sketch, "E26.0.5.171", {"start": v(85.33, 6.5) * mm, "end": v(85.33, 14.8) * mm});
            skLineSegment(sketch, "E26.0.5.172", {"start": v(445.76, 6.5) * mm, "end": v(452.95, 2.35) * mm});
            skLineSegment(sketch, "E26.0.5.173", {"start": v(240, 4.2) * mm, "end": v(247.18, 0.05) * mm});
            skLineSegment(sketch, "E26.0.5.174", {"start": v(477.18, 6.5) * mm, "end": v(469.99, 2.35) * mm});
            skLineSegment(sketch, "E26.0.5.175", {"start": v(451.62, 0.05) * mm, "end": v(451.62, -8.25) * mm});
            skLineSegment(sketch, "E26.0.5.176", {"start": v(129.25, 2.35) * mm, "end": v(136.44, 6.5) * mm});
            skLineSegment(sketch, "E26.0.5.177", {"start": v(87.99, 14.8) * mm, "end": v(87.99, 6.5) * mm});
            skLineSegment(sketch, "E26.0.5.178", {"start": v(52.58, 4.2) * mm, "end": v(59.77, 0.05) * mm});
            skLineSegment(sketch, "E26.0.5.179", {"start": v(70.95, 6.5) * mm, "end": v(78.14, 2.35) * mm});
            skLineSegment(sketch, "E26.0.5.180", {"start": v(181.7, 0.05) * mm, "end": v(188.88, 4.2) * mm});
            skLineSegment(sketch, "E26.0.5.181", {"start": v(437.24, -8.25) * mm, "end": v(437.24, 0.05) * mm});
            skLineSegment(sketch, "E26.0.5.182", {"start": v(25.7, 0.05) * mm, "end": v(25.7, -8.25) * mm});
            skLineSegment(sketch, "E26.0.5.183", {"start": v(103.7, -12.4) * mm, "end": v(96.5, -8.25) * mm});
            skLineSegment(sketch, "E26.0.5.184", {"start": v(248.5, 2.35) * mm, "end": v(255.7, 6.5) * mm});
            skLineSegment(sketch, "E26.0.5.185", {"start": v(28.36, -8.25) * mm, "end": v(28.36, 0.05) * mm});
            skLineSegment(sketch, "E26.0.5.186", {"start": v(241.32, 6.5) * mm, "end": v(248.5, 2.35) * mm});
            skLineSegment(sketch, "E26.0.5.187", {"start": v(392, 6.5) * mm, "end": v(392, 14.8) * mm});
            skLineSegment(sketch, "E26.0.5.188", {"start": v(119.4, 6.5) * mm, "end": v(112.22, 2.35) * mm});
            skLineSegment(sketch, "E26.0.5.189", {"start": v(19.84, 6.5) * mm, "end": v(27.03, 2.35) * mm});
            skLineSegment(sketch, "E26.0.5.190", {"start": v(93.85, 0.05) * mm, "end": v(93.85, -8.25) * mm});
            skLineSegment(sketch, "E26.0.5.191", {"start": v(173.17, 6.5) * mm, "end": v(180.36, 2.35) * mm});
            skLineSegment(sketch, "E26.0.5.192", {"start": v(283.91, 0.05) * mm, "end": v(291.1, 4.2) * mm});
            skLineSegment(sketch, "E26.0.5.193", {"start": v(156.14, 6.5) * mm, "end": v(156.14, 14.8) * mm});
            skLineSegment(sketch, "E26.0.5.194", {"start": v(27.03, 2.35) * mm, "end": v(34.22, 6.5) * mm});
            skLineSegment(sketch, "E26.0.5.195", {"start": v(494.21, 6.5) * mm, "end": v(494.21, 14.8) * mm});
            skLineSegment(sketch, "E26.0.5.196", {"start": v(487.02, 2.35) * mm, "end": v(494.21, 6.5) * mm});
            skLineSegment(sketch, "E26.0.5.197", {"start": v(120.74, 4.2) * mm, "end": v(127.93, 0.05) * mm});
            skLineSegment(sketch, "E26.0.5.198", {"start": v(282.58, 2.35) * mm, "end": v(289.77, 6.5) * mm});
            skLineSegment(sketch, "E26.0.5.199", {"start": v(326.5, 14.8) * mm, "end": v(326.5, 6.5) * mm});
            skLineSegment(sketch, "E26.0.5.200", {"start": v(130.58, -8.25) * mm, "end": v(130.58, 0.05) * mm});
            skLineSegment(sketch, "E26.0.5.201", {"start": v(444.43, 4.2) * mm, "end": v(451.62, 0.05) * mm});
            skLineSegment(sketch, "E26.0.5.202", {"start": v(188.88, 4.2) * mm, "end": v(196.07, 0.05) * mm});
            skLineSegment(sketch, "E26.0.5.203", {"start": v(369.1, 0.05) * mm, "end": v(376.29, 4.2) * mm});
            skLineSegment(sketch, "E26.0.5.204", {"start": v(87.99, 6.5) * mm, "end": v(95.18, 2.35) * mm});
            skLineSegment(sketch, "E26.0.5.205", {"start": v(454.28, -8.25) * mm, "end": v(454.28, 0.05) * mm});
            skLineSegment(sketch, "E26.0.5.206", {"start": v(359.24, -12.4) * mm, "end": v(352.06, -8.25) * mm});
            skLineSegment(sketch, "E26.0.5.207", {"start": v(164.66, -8.25) * mm, "end": v(164.66, 0.05) * mm});
            skLineSegment(sketch, "E26.0.5.208", {"start": v(19.84, 14.8) * mm, "end": v(19.84, 6.5) * mm});
            skLineSegment(sketch, "E26.0.5.209", {"start": v(410.35, -12.4) * mm, "end": v(403.17, -8.25) * mm});
            skLineSegment(sketch, "E26.0.5.210", {"start": v(79.47, 0.05) * mm, "end": v(86.66, 4.2) * mm});
            skLineSegment(sketch, "E26.0.5.211", {"start": v(400.5, -8.25) * mm, "end": v(393.32, -12.4) * mm});
            skLineSegment(sketch, "E26.0.5.212", {"start": v(289.77, 6.5) * mm, "end": v(289.77, 14.8) * mm});
            skLineSegment(sketch, "E26.0.5.213", {"start": v(360.58, 6.5) * mm, "end": v(360.58, 14.8) * mm});
            skLineSegment(sketch, "E26.0.5.214", {"start": v(180.36, 2.35) * mm, "end": v(187.55, 6.5) * mm});
            skLineSegment(sketch, "E26.0.5.215", {"start": v(190.2, 14.8) * mm, "end": v(190.2, 6.5) * mm});
            skLineSegment(sketch, "E26.0.5.216", {"start": v(144.96, 0.05) * mm, "end": v(144.96, -8.25) * mm});
            skLineSegment(sketch, "E26.0.5.217", {"start": v(96.5, -8.25) * mm, "end": v(96.5, 0.05) * mm});
            skLineSegment(sketch, "E26.0.5.218", {"start": v(68.3, 14.8) * mm, "end": v(68.3, 6.5) * mm});
            skLineSegment(sketch, "E26.0.5.219", {"start": v(187.55, 6.5) * mm, "end": v(187.55, 14.8) * mm});
            skLineSegment(sketch, "E26.0.5.220", {"start": v(342.21, -12.4) * mm, "end": v(335.02, -8.25) * mm});
            skLineSegment(sketch, "E26.0.5.221", {"start": v(136.44, 6.5) * mm, "end": v(136.44, 14.8) * mm});
            skLineSegment(sketch, "E26.0.5.222", {"start": v(343.54, 14.8) * mm, "end": v(343.54, 6.5) * mm});
            skLineSegment(sketch, "E26.0.5.223", {"start": v(231.47, 2.35) * mm, "end": v(238.66, 6.5) * mm});
            skLineSegment(sketch, "E26.0.5.224", {"start": v(163.33, 2.35) * mm, "end": v(156.14, 6.5) * mm});
            skLineSegment(sketch, "E26.0.5.225", {"start": v(70.95, 14.8) * mm, "end": v(70.95, 6.5) * mm});
            skLineSegment(sketch, "E26.0.5.226", {"start": v(179.04, 0.05) * mm, "end": v(179.04, -8.25) * mm});
            skLineSegment(sketch, "E26.0.5.227", {"start": v(196.07, 0.05) * mm, "end": v(196.07, -8.25) * mm});
            skLineSegment(sketch, "E26.0.5.228", {"start": v(505.39, 0.05) * mm, "end": v(512.57, 4.2) * mm});
            skLineSegment(sketch, "E26.0.5.229", {"start": v(249.84, 0.05) * mm, "end": v(257.02, 4.2) * mm});
            skLineSegment(sketch, "E26.0.5.230", {"start": v(173.17, 14.8) * mm, "end": v(173.17, 6.5) * mm});
            skLineSegment(sketch, "E26.0.5.231", {"start": v(213.1, 0.05) * mm, "end": v(213.1, -8.25) * mm});
            skLineSegment(sketch, "E26.0.5.232", {"start": v(445.76, 14.8) * mm, "end": v(445.76, 6.5) * mm});
            skLineSegment(sketch, "E26.0.5.233", {"start": v(478.5, 4.2) * mm, "end": v(485.7, 0.05) * mm});
            skLineSegment(sketch, "E26.0.5.234", {"start": v(409.03, 6.5) * mm, "end": v(409.03, 14.8) * mm});
            skLineSegment(sketch, "E26.0.5.235", {"start": v(496.87, 6.5) * mm, "end": v(504.06, 2.35) * mm});
            skLineSegment(sketch, "E26.0.5.236", {"start": v(139.1, 6.5) * mm, "end": v(146.29, 2.35) * mm});
            skLineSegment(sketch, "E26.0.5.237", {"start": v(272.74, 6.5) * mm, "end": v(265.55, 2.35) * mm});
            skLineSegment(sketch, "E26.0.5.238", {"start": v(214.44, 2.35) * mm, "end": v(207.25, 6.5) * mm});
            skLineSegment(sketch, "E26.0.5.239", {"start": v(342.21, 4.2) * mm, "end": v(349.4, 0.05) * mm});
            skLineSegment(sketch, "E26.0.5.240", {"start": v(495.54, 4.2) * mm, "end": v(502.73, 0.05) * mm});
            skLineSegment(sketch, "E26.0.5.241", {"start": v(36.88, 6.5) * mm, "end": v(44.07, 2.35) * mm});
            skLineSegment(sketch, "E26.0.5.242", {"start": v(62.44, 0.05) * mm, "end": v(69.63, 4.2) * mm});
            skLineSegment(sketch, "E26.0.5.243", {"start": v(502.73, 0.05) * mm, "end": v(502.73, -8.25) * mm});
            skLineSegment(sketch, "E26.0.5.244", {"start": v(266.88, -8.25) * mm, "end": v(266.88, 0.05) * mm});
            skLineSegment(sketch, "E26.0.5.245", {"start": v(477.18, 14.8) * mm, "end": v(477.18, 6.5) * mm});
            skLineSegment(sketch, "E26.0.5.246", {"start": v(257.02, 4.2) * mm, "end": v(264.21, 0.05) * mm});
            skLineSegment(sketch, "E26.0.5.247", {"start": v(207.25, 6.5) * mm, "end": v(207.25, 14.8) * mm});
            skLineSegment(sketch, "E26.0.5.248", {"start": v(469.99, 2.35) * mm, "end": v(462.8, 6.5) * mm});
            skLineSegment(sketch, "E26.0.5.249", {"start": v(394.65, 6.5) * mm, "end": v(401.84, 2.35) * mm});
            skLineSegment(sketch, "E26.0.5.250", {"start": v(426.07, 6.5) * mm, "end": v(418.88, 2.35) * mm});
            skLineSegment(sketch, "E26.0.5.251", {"start": v(110.88, 0.05) * mm, "end": v(110.88, -8.25) * mm});
            skLineSegment(sketch, "E26.0.5.252", {"start": v(137.77, 4.2) * mm, "end": v(144.96, 0.05) * mm});
            skLineSegment(sketch, "E26.0.5.253", {"start": v(323.85, 6.5) * mm, "end": v(316.66, 2.35) * mm});
            skLineSegment(sketch, "E26.0.5.254", {"start": v(504.06, 2.35) * mm, "end": v(511.25, 6.5) * mm});
            skLineSegment(sketch, "E26.0.5.255", {"start": v(68.3, 6.5) * mm, "end": v(61.1, 2.35) * mm});
            skLineSegment(sketch, "E26.0.5.256", {"start": v(264.21, 0.05) * mm, "end": v(264.21, -8.25) * mm});
            skLineSegment(sketch, "E26.0.5.257", {"start": v(42.74, 0.05) * mm, "end": v(42.74, -8.25) * mm});
            skLineSegment(sketch, "E26.0.5.258", {"start": v(418.88, 2.35) * mm, "end": v(411.7, 6.5) * mm});
            skLineSegment(sketch, "E26.0.5.259", {"start": v(147.62, 0.05) * mm, "end": v(154.8, 4.2) * mm});
            skLineSegment(sketch, "E26.0.5.260", {"start": v(205.91, 4.2) * mm, "end": v(213.1, 0.05) * mm});
            skLineSegment(sketch, "E26.0.5.261", {"start": v(403.17, 0.05) * mm, "end": v(410.35, 4.2) * mm});
            skLineSegment(sketch, "E26.0.5.262", {"start": v(113.55, -8.25) * mm, "end": v(113.55, 0.05) * mm});
            skLineSegment(sketch, "E26.0.5.263", {"start": v(383.48, 0.05) * mm, "end": v(383.48, -8.25) * mm});
            skLineSegment(sketch, "E26.0.5.264", {"start": v(317.99, 0.05) * mm, "end": v(325.18, 4.2) * mm});
            skLineSegment(sketch, "E26.0.5.265", {"start": v(417.54, 0.05) * mm, "end": v(417.54, -8.25) * mm});
            skLineSegment(sketch, "E26.0.5.266", {"start": v(352.06, 0.05) * mm, "end": v(359.24, 4.2) * mm});
            skLineSegment(sketch, "E26.0.5.267", {"start": v(386.13, -8.25) * mm, "end": v(386.13, 0.05) * mm});
            skLineSegment(sketch, "E26.0.5.268", {"start": v(103.7, 4.2) * mm, "end": v(110.88, 0.05) * mm});
            skLineSegment(sketch, "E26.0.5.269", {"start": v(112.22, 2.35) * mm, "end": v(105.03, 6.5) * mm});
            skLineSegment(sketch, "E26.0.5.270", {"start": v(315.32, 0.05) * mm, "end": v(315.32, -8.25) * mm});
            skLineSegment(sketch, "E26.0.5.271", {"start": v(410.35, 4.2) * mm, "end": v(417.54, 0.05) * mm});
            skLineSegment(sketch, "E26.0.5.272", {"start": v(146.29, 2.35) * mm, "end": v(153.48, 6.5) * mm});
            skLineSegment(sketch, "E26.0.5.273", {"start": v(400.5, 0.05) * mm, "end": v(400.5, -8.25) * mm});
            skLineSegment(sketch, "E26.0.5.274", {"start": v(505.39, -8.25) * mm, "end": v(505.39, 0.05) * mm});
            skLineSegment(sketch, "E26.0.5.275", {"start": v(119.4, 14.8) * mm, "end": v(119.4, 6.5) * mm});
            skLineSegment(sketch, "E26.0.5.276", {"start": v(420.2, 0.05) * mm, "end": v(427.4, 4.2) * mm});
            skLineSegment(sketch, "E26.0.5.277", {"start": v(198.73, 0.05) * mm, "end": v(205.91, 4.2) * mm});
            skLineSegment(sketch, "E26.0.5.278", {"start": v(197.4, 2.35) * mm, "end": v(204.59, 6.5) * mm});
            skLineSegment(sketch, "E26.0.5.279", {"start": v(317.99, -8.25) * mm, "end": v(317.99, 0.05) * mm});
            skLineSegment(sketch, "E26.0.5.280", {"start": v(428.72, 6.5) * mm, "end": v(435.91, 2.35) * mm});
            skLineSegment(sketch, "E26.0.5.281", {"start": v(343.54, 6.5) * mm, "end": v(350.73, 2.35) * mm});
            skLineSegment(sketch, "E26.0.5.282", {"start": v(427.4, 4.2) * mm, "end": v(434.59, 0.05) * mm});
            skLineSegment(sketch, "E26.0.5.283", {"start": v(350.73, 2.35) * mm, "end": v(357.92, 6.5) * mm});
            skLineSegment(sketch, "E26.0.5.284", {"start": v(204.59, 6.5) * mm, "end": v(204.59, 14.8) * mm});
            skLineSegment(sketch, "E26.0.5.285", {"start": v(62.44, -8.25) * mm, "end": v(62.44, 0.05) * mm});
            skLineSegment(sketch, "E26.0.5.286", {"start": v(45.4, -8.25) * mm, "end": v(45.4, 0.05) * mm});
            skLineSegment(sketch, "E26.0.5.287", {"start": v(454.28, 0.05) * mm, "end": v(461.46, 4.2) * mm});
            skLineSegment(sketch, "E26.0.5.288", {"start": v(461.46, 4.2) * mm, "end": v(468.65, 0.05) * mm});
            skLineSegment(sketch, "E26.0.5.289", {"start": v(393.32, 4.2) * mm, "end": v(400.5, 0.05) * mm});
            skLineSegment(sketch, "E26.0.5.290", {"start": v(59.77, 0.05) * mm, "end": v(59.77, -8.25) * mm});
            skLineSegment(sketch, "E26.0.5.291", {"start": v(352.06, -8.25) * mm, "end": v(352.06, 0.05) * mm});
            skLineSegment(sketch, "E26.0.5.292", {"start": v(265.55, 2.35) * mm, "end": v(258.36, 6.5) * mm});
            skLineSegment(sketch, "E26.0.5.293", {"start": v(349.4, 0.05) * mm, "end": v(349.4, -8.25) * mm});
            skLineSegment(sketch, "E26.0.5.294", {"start": v(420.2, -8.25) * mm, "end": v(420.2, 0.05) * mm});
            skLineSegment(sketch, "E26.0.5.295", {"start": v(386.13, 0.05) * mm, "end": v(393.32, 4.2) * mm});
            skLineSegment(sketch, "E26.0.5.296", {"start": v(44.07, 2.35) * mm, "end": v(51.26, 6.5) * mm});
            skLineSegment(sketch, "E26.0.5.297", {"start": v(403.17, -8.25) * mm, "end": v(403.17, 0.05) * mm});
            skLineSegment(sketch, "E26.0.5.298", {"start": v(384.8, 2.35) * mm, "end": v(392, 6.5) * mm});
            skLineSegment(sketch, "E26.0.5.299", {"start": v(45.4, 0.05) * mm, "end": v(52.58, 4.2) * mm});
            skLineSegment(sketch, "E26.0.5.300", {"start": v(511.25, 14.8) * mm, "end": v(504.06, 18.95) * mm});
            skLineSegment(sketch, "E26.0.5.301", {"start": v(504.06, 18.95) * mm, "end": v(496.87, 14.8) * mm});
            skLineSegment(sketch, "E26.0.5.302", {"start": v(494.21, 14.8) * mm, "end": v(487.02, 18.95) * mm});
            skLineSegment(sketch, "E26.0.5.303", {"start": v(487.02, 18.95) * mm, "end": v(479.83, 14.8) * mm});
            skLineSegment(sketch, "E26.0.5.304", {"start": v(443.1, 14.8) * mm, "end": v(435.91, 18.95) * mm});
            skLineSegment(sketch, "E26.0.5.305", {"start": v(367.77, 18.95) * mm, "end": v(374.96, 14.8) * mm});
            skLineSegment(sketch, "E26.0.5.306", {"start": v(333.7, 18.95) * mm, "end": v(326.5, 14.8) * mm});
            skLineSegment(sketch, "E26.0.5.307", {"start": v(435.91, 18.95) * mm, "end": v(428.72, 14.8) * mm});
            skLineSegment(sketch, "E26.0.5.308", {"start": v(418.88, 18.95) * mm, "end": v(426.07, 14.8) * mm});
            skLineSegment(sketch, "E26.0.5.309", {"start": v(411.7, 14.8) * mm, "end": v(418.88, 18.95) * mm});
            skLineSegment(sketch, "E26.0.5.310", {"start": v(357.92, 14.8) * mm, "end": v(350.73, 18.95) * mm});
            skLineSegment(sketch, "E26.0.5.311", {"start": v(401.84, 18.95) * mm, "end": v(394.65, 14.8) * mm});
            skLineSegment(sketch, "E26.0.5.312", {"start": v(350.73, 18.95) * mm, "end": v(343.54, 14.8) * mm});
            skLineSegment(sketch, "E26.0.5.313", {"start": v(340.88, 14.8) * mm, "end": v(333.7, 18.95) * mm});
            skLineSegment(sketch, "E26.0.5.314", {"start": v(460.14, 14.8) * mm, "end": v(452.95, 18.95) * mm});
            skLineSegment(sketch, "E26.0.5.315", {"start": v(392, 14.8) * mm, "end": v(384.8, 18.95) * mm});
            skLineSegment(sketch, "E26.0.5.316", {"start": v(462.8, 14.8) * mm, "end": v(469.99, 18.95) * mm});
            skLineSegment(sketch, "E26.0.5.317", {"start": v(306.8, 14.8) * mm, "end": v(299.62, 18.95) * mm});
            skLineSegment(sketch, "E26.0.5.318", {"start": v(469.99, 18.95) * mm, "end": v(477.18, 14.8) * mm});
            skLineSegment(sketch, "E26.0.5.319", {"start": v(360.58, 14.8) * mm, "end": v(367.77, 18.95) * mm});
            skLineSegment(sketch, "E26.0.5.320", {"start": v(309.47, 14.8) * mm, "end": v(316.66, 18.95) * mm});
            skLineSegment(sketch, "E26.0.5.321", {"start": v(409.03, 14.8) * mm, "end": v(401.84, 18.95) * mm});
            skLineSegment(sketch, "E26.0.5.322", {"start": v(384.8, 18.95) * mm, "end": v(377.61, 14.8) * mm});
            skLineSegment(sketch, "E26.0.5.323", {"start": v(316.66, 18.95) * mm, "end": v(323.85, 14.8) * mm});
            skLineSegment(sketch, "E26.0.5.324", {"start": v(452.95, 18.95) * mm, "end": v(445.76, 14.8) * mm});
            skLineSegment(sketch, "E26.0.5.325", {"start": v(299.62, 18.95) * mm, "end": v(292.43, 14.8) * mm});
            skLineSegment(sketch, "E26.0.5.326", {"start": v(95.18, 18.95) * mm, "end": v(87.99, 14.8) * mm});
            skLineSegment(sketch, "E26.0.5.327", {"start": v(129.25, 18.95) * mm, "end": v(122.06, 14.8) * mm});
            skLineSegment(sketch, "E26.0.5.328", {"start": v(102.37, 14.8) * mm, "end": v(95.18, 18.95) * mm});
            skLineSegment(sketch, "E26.0.5.329", {"start": v(238.66, 14.8) * mm, "end": v(231.47, 18.95) * mm});
            skLineSegment(sketch, "E26.0.5.330", {"start": v(282.58, 18.95) * mm, "end": v(275.4, 14.8) * mm});
            skLineSegment(sketch, "E26.0.5.331", {"start": v(53.92, 14.8) * mm, "end": v(61.1, 18.95) * mm});
            skLineSegment(sketch, "E26.0.5.332", {"start": v(105.03, 14.8) * mm, "end": v(112.22, 18.95) * mm});
            skLineSegment(sketch, "E26.0.5.333", {"start": v(214.44, 18.95) * mm, "end": v(221.63, 14.8) * mm});
            skLineSegment(sketch, "E26.0.5.334", {"start": v(136.44, 14.8) * mm, "end": v(129.25, 18.95) * mm});
            skLineSegment(sketch, "E26.0.5.335", {"start": v(153.48, 14.8) * mm, "end": v(146.29, 18.95) * mm});
            skLineSegment(sketch, "E26.0.5.336", {"start": v(255.7, 14.8) * mm, "end": v(248.5, 18.95) * mm});
            skLineSegment(sketch, "E26.0.5.337", {"start": v(61.1, 18.95) * mm, "end": v(68.3, 14.8) * mm});
            skLineSegment(sketch, "E26.0.5.338", {"start": v(180.36, 18.95) * mm, "end": v(173.17, 14.8) * mm});
            skLineSegment(sketch, "E26.0.5.339", {"start": v(51.26, 14.8) * mm, "end": v(44.07, 18.95) * mm});
            skLineSegment(sketch, "E26.0.5.340", {"start": v(163.33, 18.95) * mm, "end": v(170.52, 14.8) * mm});
            skLineSegment(sketch, "E26.0.5.341", {"start": v(265.55, 18.95) * mm, "end": v(272.74, 14.8) * mm});
            skLineSegment(sketch, "E26.0.5.342", {"start": v(207.25, 14.8) * mm, "end": v(214.44, 18.95) * mm});
            skLineSegment(sketch, "E26.0.5.343", {"start": v(146.29, 18.95) * mm, "end": v(139.1, 14.8) * mm});
            skLineSegment(sketch, "E26.0.5.344", {"start": v(258.36, 14.8) * mm, "end": v(265.55, 18.95) * mm});
            skLineSegment(sketch, "E26.0.5.345", {"start": v(231.47, 18.95) * mm, "end": v(224.28, 14.8) * mm});
            skLineSegment(sketch, "E26.0.5.346", {"start": v(248.5, 18.95) * mm, "end": v(241.32, 14.8) * mm});
            skLineSegment(sketch, "E26.0.5.347", {"start": v(156.14, 14.8) * mm, "end": v(163.33, 18.95) * mm});
            skLineSegment(sketch, "E26.0.5.348", {"start": v(34.22, 14.8) * mm, "end": v(27.03, 18.95) * mm});
            skLineSegment(sketch, "E26.0.5.349", {"start": v(112.22, 18.95) * mm, "end": v(119.4, 14.8) * mm});
            skLineSegment(sketch, "E26.0.5.350", {"start": v(204.59, 14.8) * mm, "end": v(197.4, 18.95) * mm});
            skLineSegment(sketch, "E26.0.5.351", {"start": v(85.33, 14.8) * mm, "end": v(78.14, 18.95) * mm});
            skLineSegment(sketch, "E26.0.5.352", {"start": v(187.55, 14.8) * mm, "end": v(180.36, 18.95) * mm});
            skLineSegment(sketch, "E26.0.5.353", {"start": v(197.4, 18.95) * mm, "end": v(190.2, 14.8) * mm});
            skLineSegment(sketch, "E26.0.5.354", {"start": v(44.07, 18.95) * mm, "end": v(36.88, 14.8) * mm});
            skLineSegment(sketch, "E26.0.5.355", {"start": v(78.14, 18.95) * mm, "end": v(70.95, 14.8) * mm});
            skLineSegment(sketch, "E26.0.5.356", {"start": v(27.03, 18.95) * mm, "end": v(19.84, 14.8) * mm});
            skLineSegment(sketch, "E26.0.5.357", {"start": v(10, 18.95) * mm, "end": v(17.19, 14.8) * mm});
            skLineSegment(sketch, "E26.0.5.358", {"start": v(2.81, 14.8) * mm, "end": v(10, 18.95) * mm});
            skLineSegment(sketch, "E26.direction1", {"start": v(11.33, 139.25) * mm, "end": v(36.33, 139.25) * mm, "construction": true});
            skLineSegment(sketch, "E26.direction2", {"start": v(11.33, 139.25) * mm, "end": v(11.33, 109.75) * mm, "construction": true});
            skLineSegment(sketch, "E27", {"start": v(282.58, 136.95) * mm, "end": v(289.77, 132.8) * mm});
            skLineSegment(sketch, "E28", {"start": v(282.58, 107.45) * mm, "end": v(289.77, 103.3) * mm});
            skLineSegment(sketch, "E29", {"start": v(282.58, 77.95) * mm, "end": v(289.77, 73.8) * mm});
            skLineSegment(sketch, "E30", {"start": v(282.58, 48.45) * mm, "end": v(289.77, 44.3) * mm});
            skLineSegment(sketch, "E31", {"start": v(282.58, 18.95) * mm, "end": v(289.77, 14.8) * mm});
            skSolve(sketch);
        }
        {
            var Q0;
            {var subQ3=sQuery(id+"F2.wireOp",EDGE,"E11.MirrorCS");Q0=makeQuery(id+"F2.imprint","IMPRINT",FACE,{"disambiguationData":[TD([[makeQuery(id+"F2.imprint","IMPRINT",EDGE,{"derivedFrom":subQ3}),-1.0]])]});}
            var Q1;
            {var subQ0=sQuery(id+"F2.wireOp",EDGE,"E5.MirrorCS");Q1=makeQuery(id+"F2.imprint","IMPRINT",FACE,{"disambiguationData":[TD([[makeQuery(id+"F2.imprint","IMPRINT",EDGE,{"derivedFrom":subQ0}),1.0]])]});}
            var Q2;
            Q2=makeQuery(id+"F2.imprint","IMPRINT",FACE,{"disambiguationData":[TD([[makeQuery(id+"F2.imprint","IMPRINT",EDGE,{"derivedFrom":sQuery(id+"F2.wireOp",EDGE,"E1.0.5.3")}),-1.0]])]});
            var Q3;
            Q3=makeQuery(id+"F2.imprint","IMPRINT",FACE,{"disambiguationData":[TD([[makeQuery(id+"F2.imprint","IMPRINT",EDGE,{"derivedFrom":sQuery(id+"F2.wireOp",EDGE,"E1.0.5.0")}),-1.0]])]});
            var Q4;
            {var subQ0=sQuery(id+"F2.wireOp",EDGE,"E25.0.1.117");Q4=makeQuery(id+"F2.imprint","IMPRINT",FACE,{"disambiguationData":[TD([[makeQuery(id+"F2.imprint","IMPRINT",EDGE,{"derivedFrom":subQ0}),-1.0]])]});}
            var Q5;
            Q5=makeQuery(id+"F2.imprint","IMPRINT",FACE,{"disambiguationData":[TD([[makeQuery(id+"F2.imprint","IMPRINT",EDGE,{"derivedFrom":sQuery(id+"F2.wireOp",EDGE,"E25.0.1.171")}),1.0]])]});
            var Q6;
            Q6=makeQuery(id+"F2.imprint","IMPRINT",FACE,{"disambiguationData":[TD([[makeQuery(id+"F2.imprint","IMPRINT",EDGE,{"derivedFrom":sQuery(id+"F2.wireOp",EDGE,"E25.0.1.68")}),1.0]])]});
            var Q7;
            {var subQ0=sQuery(id+"F2.wireOp",EDGE,"E17.MirrorCS");Q7=makeQuery(id+"F2.imprint","IMPRINT",FACE,{"disambiguationData":[TD([[makeQuery(id+"F2.imprint","IMPRINT",EDGE,{"derivedFrom":subQ0}),1.0]])]});}
            var Q8;
            {var subQ0=sQuery(id+"F2.wireOp",EDGE,"E24.1.0.0");Q8=makeQuery(id+"F2.imprint","IMPRINT",FACE,{"disambiguationData":[TD([[makeQuery(id+"F2.imprint","IMPRINT",EDGE,{"derivedFrom":subQ0}),-1.0]])]});}
            var Q9;
            {var subQ0=sQuery(id+"F2.wireOp",EDGE,"E24.1.0.8");Q9=makeQuery(id+"F2.imprint","IMPRINT",FACE,{"disambiguationData":[TD([[makeQuery(id+"F2.imprint","IMPRINT",EDGE,{"derivedFrom":subQ0}),1.0]])]});}
            var Q10;
            {var subQ0=sQuery(id+"F2.wireOp",EDGE,"E24.1.0.2");Q10=makeQuery(id+"F2.imprint","IMPRINT",FACE,{"disambiguationData":[TD([[makeQuery(id+"F2.imprint","IMPRINT",EDGE,{"derivedFrom":subQ0}),1.0]])]});}
            var Q11;
            Q11=makeQuery(id+"F2.imprint","IMPRINT",FACE,{"disambiguationData":[TD([[makeQuery(id+"F2.imprint","IMPRINT",EDGE,{"derivedFrom":sQuery(id+"F2.wireOp",EDGE,"E24.1.0.4")}),-1.0]])]});
            var Q12;
            Q12=makeQuery(id+"F2.imprint","IMPRINT",FACE,{"disambiguationData":[TD([[makeQuery(id+"F2.imprint","IMPRINT",EDGE,{"derivedFrom":sQuery(id+"F2.wireOp",EDGE,"E24.1.0.14")}),-1.0]])]});
            var Q13;
            Q13=makeQuery(id+"F2.imprint","IMPRINT",FACE,{"disambiguationData":[TD([[makeQuery(id+"F2.imprint","IMPRINT",EDGE,{"derivedFrom":sQuery(id+"F2.wireOp",EDGE,"E1.0.5.1")}),-1.0]])]});
            var Q14;
            Q14=makeQuery(id+"F2.imprint","IMPRINT",FACE,{"disambiguationData":[TD([[makeQuery(id+"F2.imprint","IMPRINT",EDGE,{"derivedFrom":sQuery(id+"F2.wireOp",EDGE,"E25.0.1.96")}),-1.0]])]});
            var Q15;
            Q15=makeQuery(id+"F2.imprint","IMPRINT",FACE,{"disambiguationData":[TD([[makeQuery(id+"F2.imprint","IMPRINT",EDGE,{"derivedFrom":sQuery(id+"F2.wireOp",EDGE,"E25.0.1.30")}),-1.0]])]});
            var Q16;
            Q16=makeQuery(id+"F2.imprint","IMPRINT",FACE,{"disambiguationData":[TD([[makeQuery(id+"F2.imprint","IMPRINT",EDGE,{"derivedFrom":sQuery(id+"F2.wireOp",EDGE,"E25.0.1.122")}),-1.0]])]});
            var Q17;
            Q17=makeQuery(id+"F2.imprint","IMPRINT",FACE,{"disambiguationData":[TD([[makeQuery(id+"F2.imprint","IMPRINT",EDGE,{"derivedFrom":sQuery(id+"F2.wireOp",EDGE,"E25.0.1.6")}),-1.0]])]});
            var Q18;
            {var subQ0=sQuery(id+"F2.wireOp",EDGE,"E25.0.2.117");Q18=makeQuery(id+"F2.imprint","IMPRINT",FACE,{"disambiguationData":[TD([[makeQuery(id+"F2.imprint","IMPRINT",EDGE,{"derivedFrom":subQ0}),-1.0]])]});}
            var Q19;
            Q19=makeQuery(id+"F2.imprint","IMPRINT",FACE,{"disambiguationData":[TD([[makeQuery(id+"F2.imprint","IMPRINT",EDGE,{"derivedFrom":sQuery(id+"F2.wireOp",EDGE,"E25.0.2.171")}),1.0]])]});
            var Q20;
            Q20=makeQuery(id+"F2.imprint","IMPRINT",FACE,{"disambiguationData":[TD([[makeQuery(id+"F2.imprint","IMPRINT",EDGE,{"derivedFrom":sQuery(id+"F2.wireOp",EDGE,"E25.0.2.68")}),1.0]])]});
            var Q21;
            Q21=makeQuery(id+"F2.imprint","IMPRINT",FACE,{"disambiguationData":[TD([[makeQuery(id+"F2.imprint","IMPRINT",EDGE,{"derivedFrom":sQuery(id+"F2.wireOp",EDGE,"E25.0.2.96")}),-1.0]])]});
            var Q22;
            Q22=makeQuery(id+"F2.imprint","IMPRINT",FACE,{"disambiguationData":[TD([[makeQuery(id+"F2.imprint","IMPRINT",EDGE,{"derivedFrom":sQuery(id+"F2.wireOp",EDGE,"E25.0.1.10")}),-1.0]])]});
            var Q23;
            Q23=makeQuery(id+"F2.imprint","IMPRINT",FACE,{"disambiguationData":[TD([[makeQuery(id+"F2.imprint","IMPRINT",EDGE,{"derivedFrom":sQuery(id+"F2.wireOp",EDGE,"E25.0.2.19")}),1.0]])]});
            var Q24;
            Q24=makeQuery(id+"F2.imprint","IMPRINT",FACE,{"disambiguationData":[TD([[makeQuery(id+"F2.imprint","IMPRINT",EDGE,{"derivedFrom":sQuery(id+"F2.wireOp",EDGE,"E25.0.2.10")}),-1.0]])]});
            var Q25;
            Q25=makeQuery(id+"F2.imprint","IMPRINT",FACE,{"disambiguationData":[TD([[makeQuery(id+"F2.imprint","IMPRINT",EDGE,{"derivedFrom":sQuery(id+"F2.wireOp",EDGE,"E25.0.2.30")}),-1.0]])]});
            var Q26;
            Q26=makeQuery(id+"F2.imprint","IMPRINT",FACE,{"disambiguationData":[TD([[makeQuery(id+"F2.imprint","IMPRINT",EDGE,{"derivedFrom":sQuery(id+"F2.wireOp",EDGE,"E25.0.2.122")}),-1.0]])]});
            var Q27;
            Q27=makeQuery(id+"F2.imprint","IMPRINT",FACE,{"disambiguationData":[TD([[makeQuery(id+"F2.imprint","IMPRINT",EDGE,{"derivedFrom":sQuery(id+"F2.wireOp",EDGE,"E25.0.2.6")}),-1.0]])]});
            var Q28;
            Q28=makeQuery(id+"F2.imprint","IMPRINT",FACE,{"disambiguationData":[TD([[makeQuery(id+"F2.imprint","IMPRINT",EDGE,{"derivedFrom":sQuery(id+"F2.wireOp",EDGE,"E25.0.1.19")}),1.0]])]});
            var Q29;
            Q29=makeQuery(id+"F2.imprint","IMPRINT",FACE,{"disambiguationData":[TD([[makeQuery(id+"F2.imprint","IMPRINT",EDGE,{"derivedFrom":sQuery(id+"F2.wireOp",EDGE,"E25.0.3.19")}),1.0]])]});
            var Q30;
            Q30=makeQuery(id+"F2.imprint","IMPRINT",FACE,{"disambiguationData":[TD([[makeQuery(id+"F2.imprint","IMPRINT",EDGE,{"derivedFrom":sQuery(id+"F2.wireOp",EDGE,"E25.0.3.10")}),-1.0]])]});
            var Q31;
            Q31=makeQuery(id+"F2.imprint","IMPRINT",FACE,{"disambiguationData":[TD([[makeQuery(id+"F2.imprint","IMPRINT",EDGE,{"derivedFrom":sQuery(id+"F2.wireOp",EDGE,"E25.0.4.19")}),1.0]])]});
            var Q32;
            Q32=makeQuery(id+"F2.imprint","IMPRINT",FACE,{"disambiguationData":[TD([[makeQuery(id+"F2.imprint","IMPRINT",EDGE,{"derivedFrom":sQuery(id+"F2.wireOp",EDGE,"E25.0.4.10")}),-1.0]])]});
            var Q33;
            Q33=makeQuery(id+"F2.imprint","IMPRINT",FACE,{"disambiguationData":[TD([[makeQuery(id+"F2.imprint","IMPRINT",EDGE,{"derivedFrom":sQuery(id+"F2.wireOp",EDGE,"E25.0.5.19")}),1.0]])]});
            var Q34;
            Q34=makeQuery(id+"F2.imprint","IMPRINT",FACE,{"disambiguationData":[TD([[makeQuery(id+"F2.imprint","IMPRINT",EDGE,{"derivedFrom":sQuery(id+"F2.wireOp",EDGE,"E25.0.5.10")}),-1.0]])]});
            var Q35;
            Q35=makeQuery(id+"F2.imprint","IMPRINT",FACE,{"disambiguationData":[TD([[makeQuery(id+"F2.imprint","IMPRINT",EDGE,{"derivedFrom":sQuery(id+"F2.wireOp",EDGE,"E25.0.5.96")}),-1.0]])]});
            var Q36;
            Q36=makeQuery(id+"F2.imprint","IMPRINT",FACE,{"disambiguationData":[TD([[makeQuery(id+"F2.imprint","IMPRINT",EDGE,{"derivedFrom":sQuery(id+"F2.wireOp",EDGE,"E25.0.4.30")}),-1.0]])]});
            var Q37;
            Q37=makeQuery(id+"F2.imprint","IMPRINT",FACE,{"disambiguationData":[TD([[makeQuery(id+"F2.imprint","IMPRINT",EDGE,{"derivedFrom":sQuery(id+"F2.wireOp",EDGE,"E25.0.4.96")}),-1.0]])]});
            var Q38;
            Q38=makeQuery(id+"F2.imprint","IMPRINT",FACE,{"disambiguationData":[TD([[makeQuery(id+"F2.imprint","IMPRINT",EDGE,{"derivedFrom":sQuery(id+"F2.wireOp",EDGE,"E25.0.3.30")}),-1.0]])]});
            var Q39;
            Q39=makeQuery(id+"F2.imprint","IMPRINT",FACE,{"disambiguationData":[TD([[makeQuery(id+"F2.imprint","IMPRINT",EDGE,{"derivedFrom":sQuery(id+"F2.wireOp",EDGE,"E25.0.3.96")}),-1.0]])]});
            var Q40;
            {var subQ0=sQuery(id+"F2.wireOp",EDGE,"E25.0.3.117");Q40=makeQuery(id+"F2.imprint","IMPRINT",FACE,{"disambiguationData":[TD([[makeQuery(id+"F2.imprint","IMPRINT",EDGE,{"derivedFrom":subQ0}),-1.0]])]});}
            var Q41;
            Q41=makeQuery(id+"F2.imprint","IMPRINT",FACE,{"disambiguationData":[TD([[makeQuery(id+"F2.imprint","IMPRINT",EDGE,{"derivedFrom":sQuery(id+"F2.wireOp",EDGE,"E25.0.3.6")}),-1.0]])]});
            var Q42;
            {var subQ0=sQuery(id+"F2.wireOp",EDGE,"E25.0.4.117");Q42=makeQuery(id+"F2.imprint","IMPRINT",FACE,{"disambiguationData":[TD([[makeQuery(id+"F2.imprint","IMPRINT",EDGE,{"derivedFrom":subQ0}),-1.0]])]});}
            var Q43;
            {var subQ0=sQuery(id+"F2.wireOp",EDGE,"E25.0.5.117");Q43=makeQuery(id+"F2.imprint","IMPRINT",FACE,{"disambiguationData":[TD([[makeQuery(id+"F2.imprint","IMPRINT",EDGE,{"derivedFrom":subQ0}),-1.0]])]});}
            var Q44;
            Q44=makeQuery(id+"F2.imprint","IMPRINT",FACE,{"disambiguationData":[TD([[makeQuery(id+"F2.imprint","IMPRINT",EDGE,{"derivedFrom":sQuery(id+"F2.wireOp",EDGE,"E25.0.5.6")}),-1.0]])]});
            var Q45;
            Q45=makeQuery(id+"F2.imprint","IMPRINT",FACE,{"disambiguationData":[TD([[makeQuery(id+"F2.imprint","IMPRINT",EDGE,{"derivedFrom":sQuery(id+"F2.wireOp",EDGE,"E25.0.4.6")}),-1.0]])]});
            var Q46;
            Q46=makeQuery(id+"F2.imprint","IMPRINT",FACE,{"disambiguationData":[TD([[makeQuery(id+"F2.imprint","IMPRINT",EDGE,{"derivedFrom":sQuery(id+"F2.wireOp",EDGE,"E25.0.3.171")}),1.0]])]});
            var Q47;
            Q47=makeQuery(id+"F2.imprint","IMPRINT",FACE,{"disambiguationData":[TD([[makeQuery(id+"F2.imprint","IMPRINT",EDGE,{"derivedFrom":sQuery(id+"F2.wireOp",EDGE,"E25.0.3.122")}),-1.0]])]});
            var Q48;
            Q48=makeQuery(id+"F2.imprint","IMPRINT",FACE,{"disambiguationData":[TD([[makeQuery(id+"F2.imprint","IMPRINT",EDGE,{"derivedFrom":sQuery(id+"F2.wireOp",EDGE,"E25.0.4.171")}),1.0]])]});
            var Q49;
            Q49=makeQuery(id+"F2.imprint","IMPRINT",FACE,{"disambiguationData":[TD([[makeQuery(id+"F2.imprint","IMPRINT",EDGE,{"derivedFrom":sQuery(id+"F2.wireOp",EDGE,"E25.0.4.122")}),-1.0]])]});
            var Q50;
            Q50=makeQuery(id+"F2.imprint","IMPRINT",FACE,{"disambiguationData":[TD([[makeQuery(id+"F2.imprint","IMPRINT",EDGE,{"derivedFrom":sQuery(id+"F2.wireOp",EDGE,"E25.0.5.171")}),1.0]])]});
            var Q51;
            Q51=makeQuery(id+"F2.imprint","IMPRINT",FACE,{"disambiguationData":[TD([[makeQuery(id+"F2.imprint","IMPRINT",EDGE,{"derivedFrom":sQuery(id+"F2.wireOp",EDGE,"E25.0.5.68")}),1.0]])]});
            var Q52;
            Q52=makeQuery(id+"F2.imprint","IMPRINT",FACE,{"disambiguationData":[TD([[makeQuery(id+"F2.imprint","IMPRINT",EDGE,{"derivedFrom":sQuery(id+"F2.wireOp",EDGE,"E25.0.5.122")}),-1.0]])]});
            var Q53;
            Q53=makeQuery(id+"F2.imprint","IMPRINT",FACE,{"disambiguationData":[TD([[makeQuery(id+"F2.imprint","IMPRINT",EDGE,{"derivedFrom":sQuery(id+"F2.wireOp",EDGE,"E25.0.5.30")}),-1.0]])]});
            var Q54;
            Q54=makeQuery(id+"F2.imprint","IMPRINT",FACE,{"disambiguationData":[TD([[makeQuery(id+"F2.imprint","IMPRINT",EDGE,{"derivedFrom":sQuery(id+"F2.wireOp",EDGE,"E25.0.4.68")}),1.0]])]});
            var Q55;
            Q55=makeQuery(id+"F2.imprint","IMPRINT",FACE,{"disambiguationData":[TD([[makeQuery(id+"F2.imprint","IMPRINT",EDGE,{"derivedFrom":sQuery(id+"F2.wireOp",EDGE,"E25.0.3.68")}),1.0]])]});
            var Q56;
            {var subQ0=sQuery(id+"F2.wireOp",EDGE,"E25.0.6.117");Q56=makeQuery(id+"F2.imprint","IMPRINT",FACE,{"disambiguationData":[TD([[makeQuery(id+"F2.imprint","IMPRINT",EDGE,{"derivedFrom":subQ0}),-1.0]])]});}
            var Q57;
            Q57=makeQuery(id+"F2.imprint","IMPRINT",FACE,{"disambiguationData":[TD([[makeQuery(id+"F2.imprint","IMPRINT",EDGE,{"derivedFrom":sQuery(id+"F2.wireOp",EDGE,"E25.0.6.6")}),-1.0]])]});
            var Q58;
            {var subQ0=sQuery(id+"F2.wireOp",EDGE,"E25.0.7.117");Q58=makeQuery(id+"F2.imprint","IMPRINT",FACE,{"disambiguationData":[TD([[makeQuery(id+"F2.imprint","IMPRINT",EDGE,{"derivedFrom":subQ0}),-1.0]])]});}
            var Q59;
            {var subQ0=sQuery(id+"F2.wireOp",EDGE,"E25.0.8.117");Q59=makeQuery(id+"F2.imprint","IMPRINT",FACE,{"disambiguationData":[TD([[makeQuery(id+"F2.imprint","IMPRINT",EDGE,{"derivedFrom":subQ0}),-1.0]])]});}
            var Q60;
            Q60=makeQuery(id+"F2.imprint","IMPRINT",FACE,{"disambiguationData":[TD([[makeQuery(id+"F2.imprint","IMPRINT",EDGE,{"derivedFrom":sQuery(id+"F2.wireOp",EDGE,"E25.0.8.6")}),-1.0]])]});
            var Q61;
            Q61=makeQuery(id+"F2.imprint","IMPRINT",FACE,{"disambiguationData":[TD([[makeQuery(id+"F2.imprint","IMPRINT",EDGE,{"derivedFrom":sQuery(id+"F2.wireOp",EDGE,"E25.0.8.171")}),1.0]])]});
            var Q62;
            Q62=makeQuery(id+"F2.imprint","IMPRINT",FACE,{"disambiguationData":[TD([[makeQuery(id+"F2.imprint","IMPRINT",EDGE,{"derivedFrom":sQuery(id+"F2.wireOp",EDGE,"E25.0.7.6")}),-1.0]])]});
            var Q63;
            Q63=makeQuery(id+"F2.imprint","IMPRINT",FACE,{"disambiguationData":[TD([[makeQuery(id+"F2.imprint","IMPRINT",EDGE,{"derivedFrom":sQuery(id+"F2.wireOp",EDGE,"E25.0.7.171")}),1.0]])]});
            var Q64;
            Q64=makeQuery(id+"F2.imprint","IMPRINT",FACE,{"disambiguationData":[TD([[makeQuery(id+"F2.imprint","IMPRINT",EDGE,{"derivedFrom":sQuery(id+"F2.wireOp",EDGE,"E25.0.6.171")}),1.0]])]});
            var Q65;
            Q65=makeQuery(id+"F2.imprint","IMPRINT",FACE,{"disambiguationData":[TD([[makeQuery(id+"F2.imprint","IMPRINT",EDGE,{"derivedFrom":sQuery(id+"F2.wireOp",EDGE,"E25.0.6.122")}),-1.0]])]});
            var Q66;
            Q66=makeQuery(id+"F2.imprint","IMPRINT",FACE,{"disambiguationData":[TD([[makeQuery(id+"F2.imprint","IMPRINT",EDGE,{"derivedFrom":sQuery(id+"F2.wireOp",EDGE,"E25.0.7.68")}),1.0]])]});
            var Q67;
            Q67=makeQuery(id+"F2.imprint","IMPRINT",FACE,{"disambiguationData":[TD([[makeQuery(id+"F2.imprint","IMPRINT",EDGE,{"derivedFrom":sQuery(id+"F2.wireOp",EDGE,"E25.0.7.122")}),-1.0]])]});
            var Q68;
            Q68=makeQuery(id+"F2.imprint","IMPRINT",FACE,{"disambiguationData":[TD([[makeQuery(id+"F2.imprint","IMPRINT",EDGE,{"derivedFrom":sQuery(id+"F2.wireOp",EDGE,"E25.0.8.68")}),1.0]])]});
            var Q69;
            Q69=makeQuery(id+"F2.imprint","IMPRINT",FACE,{"disambiguationData":[TD([[makeQuery(id+"F2.imprint","IMPRINT",EDGE,{"derivedFrom":sQuery(id+"F2.wireOp",EDGE,"E25.0.8.122")}),-1.0]])]});
            var Q70;
            Q70=makeQuery(id+"F2.imprint","IMPRINT",FACE,{"disambiguationData":[TD([[makeQuery(id+"F2.imprint","IMPRINT",EDGE,{"derivedFrom":sQuery(id+"F2.wireOp",EDGE,"E25.0.6.68")}),1.0]])]});
            var Q71;
            Q71=makeQuery(id+"F2.imprint","IMPRINT",FACE,{"disambiguationData":[TD([[makeQuery(id+"F2.imprint","IMPRINT",EDGE,{"derivedFrom":sQuery(id+"F2.wireOp",EDGE,"E25.0.6.30")}),-1.0]])]});
            var Q72;
            Q72=makeQuery(id+"F2.imprint","IMPRINT",FACE,{"disambiguationData":[TD([[makeQuery(id+"F2.imprint","IMPRINT",EDGE,{"derivedFrom":sQuery(id+"F2.wireOp",EDGE,"E25.0.7.96")}),-1.0]])]});
            var Q73;
            Q73=makeQuery(id+"F2.imprint","IMPRINT",FACE,{"disambiguationData":[TD([[makeQuery(id+"F2.imprint","IMPRINT",EDGE,{"derivedFrom":sQuery(id+"F2.wireOp",EDGE,"E25.0.7.30")}),-1.0]])]});
            var Q74;
            Q74=makeQuery(id+"F2.imprint","IMPRINT",FACE,{"disambiguationData":[TD([[makeQuery(id+"F2.imprint","IMPRINT",EDGE,{"derivedFrom":sQuery(id+"F2.wireOp",EDGE,"E25.0.8.96")}),-1.0]])]});
            var Q75;
            Q75=makeQuery(id+"F2.imprint","IMPRINT",FACE,{"disambiguationData":[TD([[makeQuery(id+"F2.imprint","IMPRINT",EDGE,{"derivedFrom":sQuery(id+"F2.wireOp",EDGE,"E25.0.8.30")}),-1.0]])]});
            var Q76;
            Q76=makeQuery(id+"F2.imprint","IMPRINT",FACE,{"disambiguationData":[TD([[makeQuery(id+"F2.imprint","IMPRINT",EDGE,{"derivedFrom":sQuery(id+"F2.wireOp",EDGE,"E25.0.6.96")}),-1.0]])]});
            var Q77;
            Q77=makeQuery(id+"F2.imprint","IMPRINT",FACE,{"disambiguationData":[TD([[makeQuery(id+"F2.imprint","IMPRINT",EDGE,{"derivedFrom":sQuery(id+"F2.wireOp",EDGE,"E25.0.6.19")}),1.0]])]});
            var Q78;
            Q78=makeQuery(id+"F2.imprint","IMPRINT",FACE,{"disambiguationData":[TD([[makeQuery(id+"F2.imprint","IMPRINT",EDGE,{"derivedFrom":sQuery(id+"F2.wireOp",EDGE,"E25.0.6.10")}),-1.0]])]});
            var Q79;
            Q79=makeQuery(id+"F2.imprint","IMPRINT",FACE,{"disambiguationData":[TD([[makeQuery(id+"F2.imprint","IMPRINT",EDGE,{"derivedFrom":sQuery(id+"F2.wireOp",EDGE,"E25.0.7.19")}),1.0]])]});
            var Q80;
            Q80=makeQuery(id+"F2.imprint","IMPRINT",FACE,{"disambiguationData":[TD([[makeQuery(id+"F2.imprint","IMPRINT",EDGE,{"derivedFrom":sQuery(id+"F2.wireOp",EDGE,"E25.0.7.10")}),-1.0]])]});
            var Q81;
            Q81=makeQuery(id+"F2.imprint","IMPRINT",FACE,{"disambiguationData":[TD([[makeQuery(id+"F2.imprint","IMPRINT",EDGE,{"derivedFrom":sQuery(id+"F2.wireOp",EDGE,"E25.0.8.19")}),1.0]])]});
            var Q82;
            Q82=makeQuery(id+"F2.imprint","IMPRINT",FACE,{"disambiguationData":[TD([[makeQuery(id+"F2.imprint","IMPRINT",EDGE,{"derivedFrom":sQuery(id+"F2.wireOp",EDGE,"E25.0.8.10")}),-1.0]])]});
            var Q83;
            Q83=makeQuery(id+"F2.imprint","IMPRINT",FACE,{"disambiguationData":[TD([[makeQuery(id+"F2.imprint","IMPRINT",EDGE,{"derivedFrom":sQuery(id+"F2.wireOp",EDGE,"E26.0.1.170")}),1.0]])]});
            var Q84;
            {var subQ0=sQuery(id+"F2.wireOp",EDGE,"E26.0.1.26");Q84=makeQuery(id+"F2.imprint","IMPRINT",FACE,{"disambiguationData":[TD([[makeQuery(id+"F2.imprint","IMPRINT",EDGE,{"derivedFrom":subQ0}),-1.0]])]});}
            var Q85;
            Q85=makeQuery(id+"F2.imprint","IMPRINT",FACE,{"disambiguationData":[TD([[makeQuery(id+"F2.imprint","IMPRINT",EDGE,{"derivedFrom":sQuery(id+"F2.wireOp",EDGE,"E26.0.1.5")}),-1.0]])]});
            var Q86;
            {var subQ0=sQuery(id+"F2.wireOp",EDGE,"E26.0.2.26");Q86=makeQuery(id+"F2.imprint","IMPRINT",FACE,{"disambiguationData":[TD([[makeQuery(id+"F2.imprint","IMPRINT",EDGE,{"derivedFrom":subQ0}),-1.0]])]});}
            var Q87;
            Q87=makeQuery(id+"F2.imprint","IMPRINT",FACE,{"disambiguationData":[TD([[makeQuery(id+"F2.imprint","IMPRINT",EDGE,{"derivedFrom":sQuery(id+"F2.wireOp",EDGE,"E26.0.2.5")}),-1.0]])]});
            var Q88;
            {var subQ0=sQuery(id+"F2.wireOp",EDGE,"E26.0.3.26");Q88=makeQuery(id+"F2.imprint","IMPRINT",FACE,{"disambiguationData":[TD([[makeQuery(id+"F2.imprint","IMPRINT",EDGE,{"derivedFrom":subQ0}),-1.0]])]});}
            var Q89;
            Q89=makeQuery(id+"F2.imprint","IMPRINT",FACE,{"disambiguationData":[TD([[makeQuery(id+"F2.imprint","IMPRINT",EDGE,{"derivedFrom":sQuery(id+"F2.wireOp",EDGE,"E26.0.3.5")}),-1.0]])]});
            var Q90;
            Q90=makeQuery(id+"F2.imprint","IMPRINT",FACE,{"disambiguationData":[TD([[makeQuery(id+"F2.imprint","IMPRINT",EDGE,{"derivedFrom":sQuery(id+"F2.wireOp",EDGE,"E26.0.1.27")}),1.0]])]});
            var Q91;
            Q91=makeQuery(id+"F2.imprint","IMPRINT",FACE,{"disambiguationData":[TD([[makeQuery(id+"F2.imprint","IMPRINT",EDGE,{"derivedFrom":sQuery(id+"F2.wireOp",EDGE,"E26.0.1.14")}),-1.0]])]});
            var Q92;
            Q92=makeQuery(id+"F2.imprint","IMPRINT",FACE,{"disambiguationData":[TD([[makeQuery(id+"F2.imprint","IMPRINT",EDGE,{"derivedFrom":sQuery(id+"F2.wireOp",EDGE,"E26.0.2.27")}),1.0]])]});
            var Q93;
            Q93=makeQuery(id+"F2.imprint","IMPRINT",FACE,{"disambiguationData":[TD([[makeQuery(id+"F2.imprint","IMPRINT",EDGE,{"derivedFrom":sQuery(id+"F2.wireOp",EDGE,"E26.0.2.14")}),-1.0]])]});
            var Q94;
            Q94=makeQuery(id+"F2.imprint","IMPRINT",FACE,{"disambiguationData":[TD([[makeQuery(id+"F2.imprint","IMPRINT",EDGE,{"derivedFrom":sQuery(id+"F2.wireOp",EDGE,"E26.0.3.27")}),1.0]])]});
            var Q95;
            Q95=makeQuery(id+"F2.imprint","IMPRINT",FACE,{"disambiguationData":[TD([[makeQuery(id+"F2.imprint","IMPRINT",EDGE,{"derivedFrom":sQuery(id+"F2.wireOp",EDGE,"E26.0.3.103")}),1.0]])]});
            var Q96;
            Q96=makeQuery(id+"F2.imprint","IMPRINT",FACE,{"disambiguationData":[TD([[makeQuery(id+"F2.imprint","IMPRINT",EDGE,{"derivedFrom":sQuery(id+"F2.wireOp",EDGE,"E26.0.3.14")}),-1.0]])]});
            var Q97;
            Q97=makeQuery(id+"F2.imprint","IMPRINT",FACE,{"disambiguationData":[TD([[makeQuery(id+"F2.imprint","IMPRINT",EDGE,{"derivedFrom":sQuery(id+"F2.wireOp",EDGE,"E26.0.1.103")}),1.0]])]});
            var Q98;
            Q98=makeQuery(id+"F2.imprint","IMPRINT",FACE,{"disambiguationData":[TD([[makeQuery(id+"F2.imprint","IMPRINT",EDGE,{"derivedFrom":sQuery(id+"F2.wireOp",EDGE,"E26.0.1.52")}),-1.0]])]});
            var Q99;
            Q99=makeQuery(id+"F2.imprint","IMPRINT",FACE,{"disambiguationData":[TD([[makeQuery(id+"F2.imprint","IMPRINT",EDGE,{"derivedFrom":sQuery(id+"F2.wireOp",EDGE,"E26.0.1.135")}),-1.0]])]});
            var Q100;
            Q100=makeQuery(id+"F2.imprint","IMPRINT",FACE,{"disambiguationData":[TD([[makeQuery(id+"F2.imprint","IMPRINT",EDGE,{"derivedFrom":sQuery(id+"F2.wireOp",EDGE,"E26.0.1.49")}),-1.0]])]});
            var Q101;
            Q101=makeQuery(id+"F2.imprint","IMPRINT",FACE,{"disambiguationData":[TD([[makeQuery(id+"F2.imprint","IMPRINT",EDGE,{"derivedFrom":sQuery(id+"F2.wireOp",EDGE,"E26.0.2.135")}),-1.0]])]});
            var Q102;
            Q102=makeQuery(id+"F2.imprint","IMPRINT",FACE,{"disambiguationData":[TD([[makeQuery(id+"F2.imprint","IMPRINT",EDGE,{"derivedFrom":sQuery(id+"F2.wireOp",EDGE,"E26.0.2.103")}),1.0]])]});
            var Q103;
            Q103=makeQuery(id+"F2.imprint","IMPRINT",FACE,{"disambiguationData":[TD([[makeQuery(id+"F2.imprint","IMPRINT",EDGE,{"derivedFrom":sQuery(id+"F2.wireOp",EDGE,"E26.0.2.52")}),-1.0]])]});
            var Q104;
            Q104=makeQuery(id+"F2.imprint","IMPRINT",FACE,{"disambiguationData":[TD([[makeQuery(id+"F2.imprint","IMPRINT",EDGE,{"derivedFrom":sQuery(id+"F2.wireOp",EDGE,"E26.0.2.49")}),-1.0]])]});
            var Q105;
            Q105=makeQuery(id+"F2.imprint","IMPRINT",FACE,{"disambiguationData":[TD([[makeQuery(id+"F2.imprint","IMPRINT",EDGE,{"derivedFrom":sQuery(id+"F2.wireOp",EDGE,"E26.0.2.170")}),1.0]])]});
            var Q106;
            Q106=makeQuery(id+"F2.imprint","IMPRINT",FACE,{"disambiguationData":[TD([[makeQuery(id+"F2.imprint","IMPRINT",EDGE,{"derivedFrom":sQuery(id+"F2.wireOp",EDGE,"E26.0.3.170")}),1.0]])]});
            var Q107;
            Q107=makeQuery(id+"F2.imprint","IMPRINT",FACE,{"disambiguationData":[TD([[makeQuery(id+"F2.imprint","IMPRINT",EDGE,{"derivedFrom":sQuery(id+"F2.wireOp",EDGE,"E26.0.3.135")}),-1.0]])]});
            var Q108;
            Q108=makeQuery(id+"F2.imprint","IMPRINT",FACE,{"disambiguationData":[TD([[makeQuery(id+"F2.imprint","IMPRINT",EDGE,{"derivedFrom":sQuery(id+"F2.wireOp",EDGE,"E26.0.3.52")}),-1.0]])]});
            var Q109;
            Q109=makeQuery(id+"F2.imprint","IMPRINT",FACE,{"disambiguationData":[TD([[makeQuery(id+"F2.imprint","IMPRINT",EDGE,{"derivedFrom":sQuery(id+"F2.wireOp",EDGE,"E26.0.3.49")}),-1.0]])]});
            var Q110;
            Q110=makeQuery(id+"F2.imprint","IMPRINT",FACE,{"disambiguationData":[TD([[makeQuery(id+"F2.imprint","IMPRINT",EDGE,{"derivedFrom":sQuery(id+"F2.wireOp",EDGE,"E26.0.3.9")}),-1.0]])]});
            var Q111;
            Q111=makeQuery(id+"F2.imprint","IMPRINT",FACE,{"disambiguationData":[TD([[makeQuery(id+"F2.imprint","IMPRINT",EDGE,{"derivedFrom":sQuery(id+"F2.wireOp",EDGE,"E26.0.4.170")}),1.0]])]});
            var Q112;
            Q112=makeQuery(id+"F2.imprint","IMPRINT",FACE,{"disambiguationData":[TD([[makeQuery(id+"F2.imprint","IMPRINT",EDGE,{"derivedFrom":sQuery(id+"F2.wireOp",EDGE,"E26.0.4.49")}),-1.0]])]});
            var Q113;
            Q113=makeQuery(id+"F2.imprint","IMPRINT",FACE,{"disambiguationData":[TD([[makeQuery(id+"F2.imprint","IMPRINT",EDGE,{"derivedFrom":sQuery(id+"F2.wireOp",EDGE,"E26.0.4.135")}),-1.0]])]});
            var Q114;
            Q114=makeQuery(id+"F2.imprint","IMPRINT",FACE,{"disambiguationData":[TD([[makeQuery(id+"F2.imprint","IMPRINT",EDGE,{"derivedFrom":sQuery(id+"F2.wireOp",EDGE,"E26.0.4.103")}),1.0]])]});
            var Q115;
            Q115=makeQuery(id+"F2.imprint","IMPRINT",FACE,{"disambiguationData":[TD([[makeQuery(id+"F2.imprint","IMPRINT",EDGE,{"derivedFrom":sQuery(id+"F2.wireOp",EDGE,"E26.0.4.27")}),1.0]])]});
            var Q116;
            {var subQ0=sQuery(id+"F2.wireOp",EDGE,"E26.0.4.26");Q116=makeQuery(id+"F2.imprint","IMPRINT",FACE,{"disambiguationData":[TD([[makeQuery(id+"F2.imprint","IMPRINT",EDGE,{"derivedFrom":subQ0}),-1.0]])]});}
            var Q117;
            Q117=makeQuery(id+"F2.imprint","IMPRINT",FACE,{"disambiguationData":[TD([[makeQuery(id+"F2.imprint","IMPRINT",EDGE,{"derivedFrom":sQuery(id+"F2.wireOp",EDGE,"E26.0.4.5")}),-1.0]])]});
            var Q118;
            {var subQ3=sQuery(id+"F2.wireOp",EDGE,"E26.0.5.357");Q118=makeQuery(id+"F2.imprint","IMPRINT",FACE,{"disambiguationData":[TD([[makeQuery(id+"F2.imprint","IMPRINT",EDGE,{"derivedFrom":subQ3}),-1.0]])]});}
            var Q119;
            {var subQ6=sQuery(id+"F2.wireOp",EDGE,"E26.0.5.348");Q119=makeQuery(id+"F2.imprint","IMPRINT",FACE,{"disambiguationData":[TD([[makeQuery(id+"F2.imprint","IMPRINT",EDGE,{"derivedFrom":subQ6}),1.0]])]});}
            var Q120;
            {var subQ4=sQuery(id+"F2.wireOp",EDGE,"E26.0.5.339");Q120=makeQuery(id+"F2.imprint","IMPRINT",FACE,{"disambiguationData":[TD([[makeQuery(id+"F2.imprint","IMPRINT",EDGE,{"derivedFrom":subQ4}),1.0]])]});}
            var Q121;
            {var subQ0=sQuery(id+"F2.wireOp",EDGE,"E26.0.5.331");Q121=makeQuery(id+"F2.imprint","IMPRINT",FACE,{"disambiguationData":[TD([[makeQuery(id+"F2.imprint","IMPRINT",EDGE,{"derivedFrom":subQ0}),-1.0]])]});}
            var Q122;
            Q122=makeQuery(id+"F2.imprint","IMPRINT",FACE,{"disambiguationData":[TD([[makeQuery(id+"F2.imprint","IMPRINT",EDGE,{"derivedFrom":sQuery(id+"F2.wireOp",EDGE,"E26.0.4.52")}),-1.0]])]});
            var Q123;
            Q123=makeQuery(id+"F2.imprint","IMPRINT",FACE,{"disambiguationData":[TD([[makeQuery(id+"F2.imprint","IMPRINT",EDGE,{"derivedFrom":sQuery(id+"F2.wireOp",EDGE,"E26.0.4.14")}),-1.0]])]});
            var Q124;
            {var subQ6=sQuery(id+"F2.wireOp",EDGE,"E26.0.5.351");Q124=makeQuery(id+"F2.imprint","IMPRINT",FACE,{"disambiguationData":[TD([[makeQuery(id+"F2.imprint","IMPRINT",EDGE,{"derivedFrom":subQ6}),1.0]])]});}
            var Q125;
            Q125=makeQuery(id+"F2.imprint","IMPRINT",FACE,{"disambiguationData":[TD([[makeQuery(id+"F2.imprint","IMPRINT",EDGE,{"derivedFrom":sQuery(id+"F2.wireOp",EDGE,"E26.0.4.9")}),-1.0]])]});
            var Q126;
            {var subQ0=sQuery(id+"F2.wireOp",EDGE,"E26.0.5.326");Q126=makeQuery(id+"F2.imprint","IMPRINT",FACE,{"disambiguationData":[TD([[makeQuery(id+"F2.imprint","IMPRINT",EDGE,{"derivedFrom":subQ0}),1.0]])]});}
            var Q127;
            Q127=makeQuery(id+"F2.imprint","IMPRINT",FACE,{"disambiguationData":[TD([[makeQuery(id+"F2.imprint","IMPRINT",EDGE,{"derivedFrom":sQuery(id+"F2.wireOp",EDGE,"E26.0.4.41")}),-1.0]])]});
            var Q128;
            {var subQ0=sQuery(id+"F2.wireOp",EDGE,"E26.0.5.332");Q128=makeQuery(id+"F2.imprint","IMPRINT",FACE,{"disambiguationData":[TD([[makeQuery(id+"F2.imprint","IMPRINT",EDGE,{"derivedFrom":subQ0}),-1.0]])]});}
            var Q129;
            {var subQ0=sQuery(id+"F2.wireOp",EDGE,"E26.0.5.327");Q129=makeQuery(id+"F2.imprint","IMPRINT",FACE,{"disambiguationData":[TD([[makeQuery(id+"F2.imprint","IMPRINT",EDGE,{"derivedFrom":subQ0}),1.0]])]});}
            var Q130;
            {var subQ4=sQuery(id+"F2.wireOp",EDGE,"E26.0.5.335");Q130=makeQuery(id+"F2.imprint","IMPRINT",FACE,{"disambiguationData":[TD([[makeQuery(id+"F2.imprint","IMPRINT",EDGE,{"derivedFrom":subQ4}),1.0]])]});}
            var Q131;
            {var subQ4=sQuery(id+"F2.wireOp",EDGE,"E26.0.5.340");Q131=makeQuery(id+"F2.imprint","IMPRINT",FACE,{"disambiguationData":[TD([[makeQuery(id+"F2.imprint","IMPRINT",EDGE,{"derivedFrom":subQ4}),-1.0]])]});}
            var Q132;
            {var subQ0=sQuery(id+"F2.wireOp",EDGE,"E26.0.5.338");Q132=makeQuery(id+"F2.imprint","IMPRINT",FACE,{"disambiguationData":[TD([[makeQuery(id+"F2.imprint","IMPRINT",EDGE,{"derivedFrom":subQ0}),1.0]])]});}
            var Q133;
            {var subQ0=sQuery(id+"F2.wireOp",EDGE,"E26.0.5.350");Q133=makeQuery(id+"F2.imprint","IMPRINT",FACE,{"disambiguationData":[TD([[makeQuery(id+"F2.imprint","IMPRINT",EDGE,{"derivedFrom":subQ0}),1.0]])]});}
            var Q134;
            {var subQ0=sQuery(id+"F2.wireOp",EDGE,"E26.0.5.333");Q134=makeQuery(id+"F2.imprint","IMPRINT",FACE,{"disambiguationData":[TD([[makeQuery(id+"F2.imprint","IMPRINT",EDGE,{"derivedFrom":subQ0}),-1.0]])]});}
            var Q135;
            {var subQ4=sQuery(id+"F2.wireOp",EDGE,"E26.0.5.329");Q135=makeQuery(id+"F2.imprint","IMPRINT",FACE,{"disambiguationData":[TD([[makeQuery(id+"F2.imprint","IMPRINT",EDGE,{"derivedFrom":subQ4}),1.0]])]});}
            var Q136;
            {var subQ0=sQuery(id+"F2.wireOp",EDGE,"E26.0.5.336");Q136=makeQuery(id+"F2.imprint","IMPRINT",FACE,{"disambiguationData":[TD([[makeQuery(id+"F2.imprint","IMPRINT",EDGE,{"derivedFrom":subQ0}),1.0]])]});}
            var Q137;
            {var subQ0=sQuery(id+"F2.wireOp",EDGE,"E26.0.5.341");Q137=makeQuery(id+"F2.imprint","IMPRINT",FACE,{"disambiguationData":[TD([[makeQuery(id+"F2.imprint","IMPRINT",EDGE,{"derivedFrom":subQ0}),-1.0]])]});}
            var Q138;
            Q138=makeQuery(id+"F2.imprint","IMPRINT",FACE,{"disambiguationData":[TD([[makeQuery(id+"F2.imprint","IMPRINT",EDGE,{"derivedFrom":sQuery(id+"F2.wireOp",EDGE,"E26.0.4.2")}),-1.0]])]});
            var Q139;
            Q139=makeQuery(id+"F2.imprint","IMPRINT",FACE,{"disambiguationData":[TD([[makeQuery(id+"F2.imprint","IMPRINT",EDGE,{"derivedFrom":sQuery(id+"F2.wireOp",EDGE,"E26.0.4.48")}),-1.0]])]});
            var Q140;
            Q140=makeQuery(id+"F2.imprint","IMPRINT",FACE,{"disambiguationData":[TD([[makeQuery(id+"F2.imprint","IMPRINT",EDGE,{"derivedFrom":sQuery(id+"F2.wireOp",EDGE,"E26.0.4.38")}),-1.0]])]});
            var Q141;
            Q141=makeQuery(id+"F2.imprint","IMPRINT",FACE,{"disambiguationData":[TD([[makeQuery(id+"F2.imprint","IMPRINT",EDGE,{"derivedFrom":sQuery(id+"F2.wireOp",EDGE,"E26.0.4.43")}),-1.0]])]});
            var Q142;
            Q142=makeQuery(id+"F2.imprint","IMPRINT",FACE,{"disambiguationData":[TD([[makeQuery(id+"F2.imprint","IMPRINT",EDGE,{"derivedFrom":sQuery(id+"F2.wireOp",EDGE,"E26.0.4.16")}),-1.0]])]});
            var Q143;
            Q143=makeQuery(id+"F2.imprint","IMPRINT",FACE,{"disambiguationData":[TD([[makeQuery(id+"F2.imprint","IMPRINT",EDGE,{"derivedFrom":sQuery(id+"F2.wireOp",EDGE,"E26.0.4.54")}),-1.0]])]});
            var Q144;
            Q144=makeQuery(id+"F2.imprint","IMPRINT",FACE,{"disambiguationData":[TD([[makeQuery(id+"F2.imprint","IMPRINT",EDGE,{"derivedFrom":sQuery(id+"F2.wireOp",EDGE,"E26.0.4.23")}),-1.0]])]});
            var Q145;
            Q145=makeQuery(id+"F2.imprint","IMPRINT",FACE,{"disambiguationData":[TD([[makeQuery(id+"F2.imprint","IMPRINT",EDGE,{"derivedFrom":sQuery(id+"F2.wireOp",EDGE,"E26.0.4.3")}),-1.0]])]});
            var Q146;
            Q146=makeQuery(id+"F2.imprint","IMPRINT",FACE,{"disambiguationData":[TD([[makeQuery(id+"F2.imprint","IMPRINT",EDGE,{"derivedFrom":sQuery(id+"F2.wireOp",EDGE,"E26.0.4.13")}),-1.0]])]});
            var Q147;
            Q147=makeQuery(id+"F2.imprint","IMPRINT",FACE,{"disambiguationData":[TD([[makeQuery(id+"F2.imprint","IMPRINT",EDGE,{"derivedFrom":sQuery(id+"F2.wireOp",EDGE,"E26.0.4.7")}),-1.0]])]});
            var Q148;
            Q148=makeQuery(id+"F2.imprint","IMPRINT",FACE,{"disambiguationData":[TD([[makeQuery(id+"F2.imprint","IMPRINT",EDGE,{"derivedFrom":sQuery(id+"F2.wireOp",EDGE,"E26.0.3.41")}),-1.0]])]});
            var Q149;
            Q149=makeQuery(id+"F2.imprint","IMPRINT",FACE,{"disambiguationData":[TD([[makeQuery(id+"F2.imprint","IMPRINT",EDGE,{"derivedFrom":sQuery(id+"F2.wireOp",EDGE,"E26.0.4.37")}),-1.0]])]});
            var Q150;
            Q150=makeQuery(id+"F2.imprint","IMPRINT",FACE,{"disambiguationData":[TD([[makeQuery(id+"F2.imprint","IMPRINT",EDGE,{"derivedFrom":sQuery(id+"F2.wireOp",EDGE,"E26.0.4.50")}),1.0]])]});
            var Q151;
            Q151=makeQuery(id+"F2.imprint","IMPRINT",FACE,{"disambiguationData":[TD([[makeQuery(id+"F2.imprint","IMPRINT",EDGE,{"derivedFrom":sQuery(id+"F2.wireOp",EDGE,"E26.0.3.2")}),-1.0]])]});
            var Q152;
            Q152=makeQuery(id+"F2.imprint","IMPRINT",FACE,{"disambiguationData":[TD([[makeQuery(id+"F2.imprint","IMPRINT",EDGE,{"derivedFrom":sQuery(id+"F2.wireOp",EDGE,"E26.0.4.80")}),1.0]])]});
            var Q153;
            Q153=makeQuery(id+"F2.imprint","IMPRINT",FACE,{"disambiguationData":[TD([[makeQuery(id+"F2.imprint","IMPRINT",EDGE,{"derivedFrom":sQuery(id+"F2.wireOp",EDGE,"E26.0.3.48")}),-1.0]])]});
            var Q154;
            Q154=makeQuery(id+"F2.imprint","IMPRINT",FACE,{"disambiguationData":[TD([[makeQuery(id+"F2.imprint","IMPRINT",EDGE,{"derivedFrom":sQuery(id+"F2.wireOp",EDGE,"E26.0.4.102")}),1.0]])]});
            var Q155;
            Q155=makeQuery(id+"F2.imprint","IMPRINT",FACE,{"disambiguationData":[TD([[makeQuery(id+"F2.imprint","IMPRINT",EDGE,{"derivedFrom":sQuery(id+"F2.wireOp",EDGE,"E26.0.3.38")}),-1.0]])]});
            var Q156;
            Q156=makeQuery(id+"F2.imprint","IMPRINT",FACE,{"disambiguationData":[TD([[makeQuery(id+"F2.imprint","IMPRINT",EDGE,{"derivedFrom":sQuery(id+"F2.wireOp",EDGE,"E26.0.4.130")}),-1.0]])]});
            var Q157;
            Q157=makeQuery(id+"F2.imprint","IMPRINT",FACE,{"disambiguationData":[TD([[makeQuery(id+"F2.imprint","IMPRINT",EDGE,{"derivedFrom":sQuery(id+"F2.wireOp",EDGE,"E26.0.3.43")}),-1.0]])]});
            var Q158;
            Q158=makeQuery(id+"F2.imprint","IMPRINT",FACE,{"disambiguationData":[TD([[makeQuery(id+"F2.imprint","IMPRINT",EDGE,{"derivedFrom":sQuery(id+"F2.wireOp",EDGE,"E26.0.4.191")}),1.0]])]});
            var Q159;
            Q159=makeQuery(id+"F2.imprint","IMPRINT",FACE,{"disambiguationData":[TD([[makeQuery(id+"F2.imprint","IMPRINT",EDGE,{"derivedFrom":sQuery(id+"F2.wireOp",EDGE,"E26.0.3.16")}),-1.0]])]});
            var Q160;
            Q160=makeQuery(id+"F2.imprint","IMPRINT",FACE,{"disambiguationData":[TD([[makeQuery(id+"F2.imprint","IMPRINT",EDGE,{"derivedFrom":sQuery(id+"F2.wireOp",EDGE,"E26.0.4.84")}),1.0]])]});
            var Q161;
            Q161=makeQuery(id+"F2.imprint","IMPRINT",FACE,{"disambiguationData":[TD([[makeQuery(id+"F2.imprint","IMPRINT",EDGE,{"derivedFrom":sQuery(id+"F2.wireOp",EDGE,"E26.0.3.54")}),-1.0]])]});
            var Q162;
            Q162=makeQuery(id+"F2.imprint","IMPRINT",FACE,{"disambiguationData":[TD([[makeQuery(id+"F2.imprint","IMPRINT",EDGE,{"derivedFrom":sQuery(id+"F2.wireOp",EDGE,"E26.0.4.88")}),-1.0]])]});
            var Q163;
            Q163=makeQuery(id+"F2.imprint","IMPRINT",FACE,{"disambiguationData":[TD([[makeQuery(id+"F2.imprint","IMPRINT",EDGE,{"derivedFrom":sQuery(id+"F2.wireOp",EDGE,"E26.0.3.23")}),-1.0]])]});
            var Q164;
            Q164=makeQuery(id+"F2.imprint","IMPRINT",FACE,{"disambiguationData":[TD([[makeQuery(id+"F2.imprint","IMPRINT",EDGE,{"derivedFrom":sQuery(id+"F2.wireOp",EDGE,"E26.0.4.60")}),1.0]])]});
            var Q165;
            Q165=makeQuery(id+"F2.imprint","IMPRINT",FACE,{"disambiguationData":[TD([[makeQuery(id+"F2.imprint","IMPRINT",EDGE,{"derivedFrom":sQuery(id+"F2.wireOp",EDGE,"E26.0.3.3")}),-1.0]])]});
            var Q166;
            Q166=makeQuery(id+"F2.imprint","IMPRINT",FACE,{"disambiguationData":[TD([[makeQuery(id+"F2.imprint","IMPRINT",EDGE,{"derivedFrom":sQuery(id+"F2.wireOp",EDGE,"E26.0.4.35")}),1.0]])]});
            var Q167;
            Q167=makeQuery(id+"F2.imprint","IMPRINT",FACE,{"disambiguationData":[TD([[makeQuery(id+"F2.imprint","IMPRINT",EDGE,{"derivedFrom":sQuery(id+"F2.wireOp",EDGE,"E26.0.3.13")}),-1.0]])]});
            var Q168;
            Q168=makeQuery(id+"F2.imprint","IMPRINT",FACE,{"disambiguationData":[TD([[makeQuery(id+"F2.imprint","IMPRINT",EDGE,{"derivedFrom":sQuery(id+"F2.wireOp",EDGE,"E26.0.4.91")}),-1.0]])]});
            var Q169;
            Q169=makeQuery(id+"F2.imprint","IMPRINT",FACE,{"disambiguationData":[TD([[makeQuery(id+"F2.imprint","IMPRINT",EDGE,{"derivedFrom":sQuery(id+"F2.wireOp",EDGE,"E26.0.3.7")}),-1.0]])]});
            var Q170;
            Q170=makeQuery(id+"F2.imprint","IMPRINT",FACE,{"disambiguationData":[TD([[makeQuery(id+"F2.imprint","IMPRINT",EDGE,{"derivedFrom":sQuery(id+"F2.wireOp",EDGE,"E26.0.4.143")}),1.0]])]});
            var Q171;
            Q171=makeQuery(id+"F2.imprint","IMPRINT",FACE,{"disambiguationData":[TD([[makeQuery(id+"F2.imprint","IMPRINT",EDGE,{"derivedFrom":sQuery(id+"F2.wireOp",EDGE,"E26.0.3.18")}),-1.0]])]});
            var Q172;
            Q172=makeQuery(id+"F2.imprint","IMPRINT",FACE,{"disambiguationData":[TD([[makeQuery(id+"F2.imprint","IMPRINT",EDGE,{"derivedFrom":sQuery(id+"F2.wireOp",EDGE,"E26.0.4.30")}),1.0]])]});
            var Q173;
            Q173=makeQuery(id+"F2.imprint","IMPRINT",FACE,{"disambiguationData":[TD([[makeQuery(id+"F2.imprint","IMPRINT",EDGE,{"derivedFrom":sQuery(id+"F2.wireOp",EDGE,"E26.0.3.8")}),-1.0]])]});
            var Q174;
            Q174=makeQuery(id+"F2.imprint","IMPRINT",FACE,{"disambiguationData":[TD([[makeQuery(id+"F2.imprint","IMPRINT",EDGE,{"derivedFrom":sQuery(id+"F2.wireOp",EDGE,"E26.0.4.63")}),-1.0]])]});
            var Q175;
            Q175=makeQuery(id+"F2.imprint","IMPRINT",FACE,{"disambiguationData":[TD([[makeQuery(id+"F2.imprint","IMPRINT",EDGE,{"derivedFrom":sQuery(id+"F2.wireOp",EDGE,"E26.0.3.12")}),-1.0]])]});
            var Q176;
            Q176=makeQuery(id+"F2.imprint","IMPRINT",FACE,{"disambiguationData":[TD([[makeQuery(id+"F2.imprint","IMPRINT",EDGE,{"derivedFrom":sQuery(id+"F2.wireOp",EDGE,"E26.0.3.99")}),-1.0]])]});
            var Q177;
            Q177=makeQuery(id+"F2.imprint","IMPRINT",FACE,{"disambiguationData":[TD([[makeQuery(id+"F2.imprint","IMPRINT",EDGE,{"derivedFrom":sQuery(id+"F2.wireOp",EDGE,"E26.0.4.111")}),1.0]])]});
            var Q178;
            {var subQ0=sQuery(id+"F2.wireOp",EDGE,"E26.0.5.330");Q178=makeQuery(id+"F2.imprint","IMPRINT",FACE,{"disambiguationData":[TD([[makeQuery(id+"F2.imprint","IMPRINT",EDGE,{"derivedFrom":subQ0}),1.0]])]});}
            var Q179;
            {var subQ0=sQuery(id+"F2.wireOp",EDGE,"E26.0.5.317");Q179=makeQuery(id+"F2.imprint","IMPRINT",FACE,{"disambiguationData":[TD([[makeQuery(id+"F2.imprint","IMPRINT",EDGE,{"derivedFrom":subQ0}),1.0]])]});}
            var Q180;
            {var subQ0=sQuery(id+"F2.wireOp",EDGE,"E26.0.5.320");Q180=makeQuery(id+"F2.imprint","IMPRINT",FACE,{"disambiguationData":[TD([[makeQuery(id+"F2.imprint","IMPRINT",EDGE,{"derivedFrom":subQ0}),-1.0]])]});}
            var Q181;
            {var subQ0=sQuery(id+"F2.wireOp",EDGE,"E26.0.5.306");Q181=makeQuery(id+"F2.imprint","IMPRINT",FACE,{"disambiguationData":[TD([[makeQuery(id+"F2.imprint","IMPRINT",EDGE,{"derivedFrom":subQ0}),1.0]])]});}
            var Q182;
            {var subQ0=sQuery(id+"F2.wireOp",EDGE,"E26.0.5.310");Q182=makeQuery(id+"F2.imprint","IMPRINT",FACE,{"disambiguationData":[TD([[makeQuery(id+"F2.imprint","IMPRINT",EDGE,{"derivedFrom":subQ0}),1.0]])]});}
            var Q183;
            {var subQ0=sQuery(id+"F2.wireOp",EDGE,"E26.0.5.305");Q183=makeQuery(id+"F2.imprint","IMPRINT",FACE,{"disambiguationData":[TD([[makeQuery(id+"F2.imprint","IMPRINT",EDGE,{"derivedFrom":subQ0}),-1.0]])]});}
            var Q184;
            {var subQ0=sQuery(id+"F2.wireOp",EDGE,"E26.0.5.315");Q184=makeQuery(id+"F2.imprint","IMPRINT",FACE,{"disambiguationData":[TD([[makeQuery(id+"F2.imprint","IMPRINT",EDGE,{"derivedFrom":subQ0}),1.0]])]});}
            var Q185;
            {var subQ0=sQuery(id+"F2.wireOp",EDGE,"E26.0.5.311");Q185=makeQuery(id+"F2.imprint","IMPRINT",FACE,{"disambiguationData":[TD([[makeQuery(id+"F2.imprint","IMPRINT",EDGE,{"derivedFrom":subQ0}),1.0]])]});}
            var Q186;
            {var subQ0=sQuery(id+"F2.wireOp",EDGE,"E26.0.5.308");Q186=makeQuery(id+"F2.imprint","IMPRINT",FACE,{"disambiguationData":[TD([[makeQuery(id+"F2.imprint","IMPRINT",EDGE,{"derivedFrom":subQ0}),-1.0]])]});}
            var Q187;
            {var subQ0=sQuery(id+"F2.wireOp",EDGE,"E26.0.5.304");Q187=makeQuery(id+"F2.imprint","IMPRINT",FACE,{"disambiguationData":[TD([[makeQuery(id+"F2.imprint","IMPRINT",EDGE,{"derivedFrom":subQ0}),1.0]])]});}
            var Q188;
            Q188=makeQuery(id+"F2.imprint","IMPRINT",FACE,{"disambiguationData":[TD([[makeQuery(id+"F2.imprint","IMPRINT",EDGE,{"derivedFrom":sQuery(id+"F2.wireOp",EDGE,"E26.0.4.18")}),-1.0]])]});
            var Q189;
            Q189=makeQuery(id+"F2.imprint","IMPRINT",FACE,{"disambiguationData":[TD([[makeQuery(id+"F2.imprint","IMPRINT",EDGE,{"derivedFrom":sQuery(id+"F2.wireOp",EDGE,"E26.0.4.8")}),-1.0]])]});
            var Q190;
            Q190=makeQuery(id+"F2.imprint","IMPRINT",FACE,{"disambiguationData":[TD([[makeQuery(id+"F2.imprint","IMPRINT",EDGE,{"derivedFrom":sQuery(id+"F2.wireOp",EDGE,"E26.0.4.12")}),-1.0]])]});
            var Q191;
            Q191=makeQuery(id+"F2.imprint","IMPRINT",FACE,{"disambiguationData":[TD([[makeQuery(id+"F2.imprint","IMPRINT",EDGE,{"derivedFrom":sQuery(id+"F2.wireOp",EDGE,"E26.0.4.99")}),-1.0]])]});
            var Q192;
            Q192=makeQuery(id+"F2.imprint","IMPRINT",FACE,{"disambiguationData":[TD([[makeQuery(id+"F2.imprint","IMPRINT",EDGE,{"derivedFrom":sQuery(id+"F2.wireOp",EDGE,"E26.0.4.34")}),-1.0]])]});
            var Q193;
            Q193=makeQuery(id+"F2.imprint","IMPRINT",FACE,{"disambiguationData":[TD([[makeQuery(id+"F2.imprint","IMPRINT",EDGE,{"derivedFrom":sQuery(id+"F2.wireOp",EDGE,"E26.0.4.6")}),-1.0]])]});
            var Q194;
            Q194=makeQuery(id+"F2.imprint","IMPRINT",FACE,{"disambiguationData":[TD([[makeQuery(id+"F2.imprint","IMPRINT",EDGE,{"derivedFrom":sQuery(id+"F2.wireOp",EDGE,"E26.0.4.117")}),-1.0]])]});
            var Q195;
            Q195=makeQuery(id+"F2.imprint","IMPRINT",FACE,{"disambiguationData":[TD([[makeQuery(id+"F2.imprint","IMPRINT",EDGE,{"derivedFrom":sQuery(id+"F2.wireOp",EDGE,"E26.0.4.164")}),-1.0]])]});
            var Q196;
            Q196=makeQuery(id+"F2.imprint","IMPRINT",FACE,{"disambiguationData":[TD([[makeQuery(id+"F2.imprint","IMPRINT",EDGE,{"derivedFrom":sQuery(id+"F2.wireOp",EDGE,"E26.0.4.62")}),-1.0]])]});
            var Q197;
            Q197=makeQuery(id+"F2.imprint","IMPRINT",FACE,{"disambiguationData":[TD([[makeQuery(id+"F2.imprint","IMPRINT",EDGE,{"derivedFrom":sQuery(id+"F2.wireOp",EDGE,"E26.0.4.106")}),1.0]])]});
            var Q198;
            Q198=makeQuery(id+"F2.imprint","IMPRINT",FACE,{"disambiguationData":[TD([[makeQuery(id+"F2.imprint","IMPRINT",EDGE,{"derivedFrom":sQuery(id+"F2.wireOp",EDGE,"E26.0.3.34")}),-1.0]])]});
            var Q199;
            Q199=makeQuery(id+"F2.imprint","IMPRINT",FACE,{"disambiguationData":[TD([[makeQuery(id+"F2.imprint","IMPRINT",EDGE,{"derivedFrom":sQuery(id+"F2.wireOp",EDGE,"E26.0.3.6")}),-1.0]])]});
            var Q200;
            Q200=makeQuery(id+"F2.imprint","IMPRINT",FACE,{"disambiguationData":[TD([[makeQuery(id+"F2.imprint","IMPRINT",EDGE,{"derivedFrom":sQuery(id+"F2.wireOp",EDGE,"E26.0.4.33")}),1.0]])]});
            var Q201;
            Q201=makeQuery(id+"F2.imprint","IMPRINT",FACE,{"disambiguationData":[TD([[makeQuery(id+"F2.imprint","IMPRINT",EDGE,{"derivedFrom":sQuery(id+"F2.wireOp",EDGE,"E26.0.3.117")}),-1.0]])]});
            var Q202;
            Q202=makeQuery(id+"F2.imprint","IMPRINT",FACE,{"disambiguationData":[TD([[makeQuery(id+"F2.imprint","IMPRINT",EDGE,{"derivedFrom":sQuery(id+"F2.wireOp",EDGE,"E26.0.4.112")}),1.0]])]});
            var Q203;
            Q203=makeQuery(id+"F2.imprint","IMPRINT",FACE,{"disambiguationData":[TD([[makeQuery(id+"F2.imprint","IMPRINT",EDGE,{"derivedFrom":sQuery(id+"F2.wireOp",EDGE,"E26.0.3.164")}),-1.0]])]});
            var Q204;
            Q204=makeQuery(id+"F2.imprint","IMPRINT",FACE,{"disambiguationData":[TD([[makeQuery(id+"F2.imprint","IMPRINT",EDGE,{"derivedFrom":sQuery(id+"F2.wireOp",EDGE,"E26.0.4.87")}),-1.0]])]});
            var Q205;
            Q205=makeQuery(id+"F2.imprint","IMPRINT",FACE,{"disambiguationData":[TD([[makeQuery(id+"F2.imprint","IMPRINT",EDGE,{"derivedFrom":sQuery(id+"F2.wireOp",EDGE,"E26.0.4.46")}),-1.0]])]});
            var Q206;
            {var subQ0=sQuery(id+"F2.wireOp",EDGE,"E26.0.5.314");Q206=makeQuery(id+"F2.imprint","IMPRINT",FACE,{"disambiguationData":[TD([[makeQuery(id+"F2.imprint","IMPRINT",EDGE,{"derivedFrom":subQ0}),1.0]])]});}
            var Q207;
            {var subQ4=sQuery(id+"F2.wireOp",EDGE,"E26.0.5.316");Q207=makeQuery(id+"F2.imprint","IMPRINT",FACE,{"disambiguationData":[TD([[makeQuery(id+"F2.imprint","IMPRINT",EDGE,{"derivedFrom":subQ4}),-1.0]])]});}
            var Q208;
            {var subQ0=sQuery(id+"F2.wireOp",EDGE,"E26.0.5.303");Q208=makeQuery(id+"F2.imprint","IMPRINT",FACE,{"disambiguationData":[TD([[makeQuery(id+"F2.imprint","IMPRINT",EDGE,{"derivedFrom":subQ0}),1.0]])]});}
            var Q209;
            {var subQ5=sQuery(id+"F2.wireOp",EDGE,"E26.0.4.151");Q209=makeQuery(id+"F2.imprint","IMPRINT",FACE,{"disambiguationData":[TD([[makeQuery(id+"F2.imprint","IMPRINT",EDGE,{"derivedFrom":subQ5}),-1.0]])]});}
            var Q210;
            Q210=makeQuery(id+"F2.imprint","IMPRINT",FACE,{"disambiguationData":[TD([[makeQuery(id+"F2.imprint","IMPRINT",EDGE,{"derivedFrom":sQuery(id+"F2.wireOp",EDGE,"E26.0.4.66")}),-1.0]])]});
            var Q211;
            Q211=makeQuery(id+"F2.imprint","IMPRINT",FACE,{"disambiguationData":[TD([[makeQuery(id+"F2.imprint","IMPRINT",EDGE,{"derivedFrom":sQuery(id+"F2.wireOp",EDGE,"E26.0.4.22")}),-1.0]])]});
            var Q212;
            Q212=makeQuery(id+"F2.imprint","IMPRINT",FACE,{"disambiguationData":[TD([[makeQuery(id+"F2.imprint","IMPRINT",EDGE,{"derivedFrom":sQuery(id+"F2.wireOp",EDGE,"E26.0.4.71")}),-1.0]])]});
            var Q213;
            Q213=makeQuery(id+"F2.imprint","IMPRINT",FACE,{"disambiguationData":[TD([[makeQuery(id+"F2.imprint","IMPRINT",EDGE,{"derivedFrom":sQuery(id+"F2.wireOp",EDGE,"E26.0.4.113")}),1.0]])]});
            var Q214;
            Q214=makeQuery(id+"F2.imprint","IMPRINT",FACE,{"disambiguationData":[TD([[makeQuery(id+"F2.imprint","IMPRINT",EDGE,{"derivedFrom":sQuery(id+"F2.wireOp",EDGE,"E26.0.4.136")}),1.0]])]});
            var Q215;
            Q215=makeQuery(id+"F2.imprint","IMPRINT",FACE,{"disambiguationData":[TD([[makeQuery(id+"F2.imprint","IMPRINT",EDGE,{"derivedFrom":sQuery(id+"F2.wireOp",EDGE,"E26.0.4.100")}),-1.0]])]});
            var Q216;
            Q216=makeQuery(id+"F2.imprint","IMPRINT",FACE,{"disambiguationData":[TD([[makeQuery(id+"F2.imprint","IMPRINT",EDGE,{"derivedFrom":sQuery(id+"F2.wireOp",EDGE,"E26.0.4.142")}),1.0]])]});
            var Q217;
            Q217=makeQuery(id+"F2.imprint","IMPRINT",FACE,{"disambiguationData":[TD([[makeQuery(id+"F2.imprint","IMPRINT",EDGE,{"derivedFrom":sQuery(id+"F2.wireOp",EDGE,"E26.0.3.62")}),-1.0]])]});
            var Q218;
            Q218=makeQuery(id+"F2.imprint","IMPRINT",FACE,{"disambiguationData":[TD([[makeQuery(id+"F2.imprint","IMPRINT",EDGE,{"derivedFrom":sQuery(id+"F2.wireOp",EDGE,"E26.0.3.71")}),-1.0]])]});
            var Q219;
            Q219=makeQuery(id+"F2.imprint","IMPRINT",FACE,{"disambiguationData":[TD([[makeQuery(id+"F2.imprint","IMPRINT",EDGE,{"derivedFrom":sQuery(id+"F2.wireOp",EDGE,"E26.0.3.22")}),-1.0]])]});
            var Q220;
            Q220=makeQuery(id+"F2.imprint","IMPRINT",FACE,{"disambiguationData":[TD([[makeQuery(id+"F2.imprint","IMPRINT",EDGE,{"derivedFrom":sQuery(id+"F2.wireOp",EDGE,"E26.0.3.66")}),-1.0]])]});
            var Q221;
            {var subQ5=sQuery(id+"F2.wireOp",EDGE,"E26.0.3.151");Q221=makeQuery(id+"F2.imprint","IMPRINT",FACE,{"disambiguationData":[TD([[makeQuery(id+"F2.imprint","IMPRINT",EDGE,{"derivedFrom":subQ5}),-1.0]])]});}
            var Q222;
            Q222=makeQuery(id+"F2.imprint","IMPRINT",FACE,{"disambiguationData":[TD([[makeQuery(id+"F2.imprint","IMPRINT",EDGE,{"derivedFrom":sQuery(id+"F2.wireOp",EDGE,"E26.0.3.142")}),1.0]])]});
            var Q223;
            Q223=makeQuery(id+"F2.imprint","IMPRINT",FACE,{"disambiguationData":[TD([[makeQuery(id+"F2.imprint","IMPRINT",EDGE,{"derivedFrom":sQuery(id+"F2.wireOp",EDGE,"E26.0.3.100")}),-1.0]])]});
            var Q224;
            Q224=makeQuery(id+"F2.imprint","IMPRINT",FACE,{"disambiguationData":[TD([[makeQuery(id+"F2.imprint","IMPRINT",EDGE,{"derivedFrom":sQuery(id+"F2.wireOp",EDGE,"E26.0.3.136")}),1.0]])]});
            var Q225;
            Q225=makeQuery(id+"F2.imprint","IMPRINT",FACE,{"disambiguationData":[TD([[makeQuery(id+"F2.imprint","IMPRINT",EDGE,{"derivedFrom":sQuery(id+"F2.wireOp",EDGE,"E26.0.3.113")}),1.0]])]});
            var Q226;
            Q226=makeQuery(id+"F2.imprint","IMPRINT",FACE,{"disambiguationData":[TD([[makeQuery(id+"F2.imprint","IMPRINT",EDGE,{"derivedFrom":sQuery(id+"F2.wireOp",EDGE,"E26.0.3.87")}),-1.0]])]});
            var Q227;
            Q227=makeQuery(id+"F2.imprint","IMPRINT",FACE,{"disambiguationData":[TD([[makeQuery(id+"F2.imprint","IMPRINT",EDGE,{"derivedFrom":sQuery(id+"F2.wireOp",EDGE,"E26.0.3.112")}),1.0]])]});
            var Q228;
            Q228=makeQuery(id+"F2.imprint","IMPRINT",FACE,{"disambiguationData":[TD([[makeQuery(id+"F2.imprint","IMPRINT",EDGE,{"derivedFrom":sQuery(id+"F2.wireOp",EDGE,"E26.0.3.33")}),1.0]])]});
            var Q229;
            Q229=makeQuery(id+"F2.imprint","IMPRINT",FACE,{"disambiguationData":[TD([[makeQuery(id+"F2.imprint","IMPRINT",EDGE,{"derivedFrom":sQuery(id+"F2.wireOp",EDGE,"E26.0.3.46")}),-1.0]])]});
            var Q230;
            Q230=makeQuery(id+"F2.imprint","IMPRINT",FACE,{"disambiguationData":[TD([[makeQuery(id+"F2.imprint","IMPRINT",EDGE,{"derivedFrom":sQuery(id+"F2.wireOp",EDGE,"E26.0.3.106")}),1.0]])]});
            var Q231;
            Q231=makeQuery(id+"F2.imprint","IMPRINT",FACE,{"disambiguationData":[TD([[makeQuery(id+"F2.imprint","IMPRINT",EDGE,{"derivedFrom":sQuery(id+"F2.wireOp",EDGE,"E26.0.3.111")}),1.0]])]});
            var Q232;
            Q232=makeQuery(id+"F2.imprint","IMPRINT",FACE,{"disambiguationData":[TD([[makeQuery(id+"F2.imprint","IMPRINT",EDGE,{"derivedFrom":sQuery(id+"F2.wireOp",EDGE,"E26.0.3.63")}),-1.0]])]});
            var Q233;
            Q233=makeQuery(id+"F2.imprint","IMPRINT",FACE,{"disambiguationData":[TD([[makeQuery(id+"F2.imprint","IMPRINT",EDGE,{"derivedFrom":sQuery(id+"F2.wireOp",EDGE,"E26.0.3.30")}),1.0]])]});
            var Q234;
            Q234=makeQuery(id+"F2.imprint","IMPRINT",FACE,{"disambiguationData":[TD([[makeQuery(id+"F2.imprint","IMPRINT",EDGE,{"derivedFrom":sQuery(id+"F2.wireOp",EDGE,"E26.0.3.143")}),1.0]])]});
            var Q235;
            Q235=makeQuery(id+"F2.imprint","IMPRINT",FACE,{"disambiguationData":[TD([[makeQuery(id+"F2.imprint","IMPRINT",EDGE,{"derivedFrom":sQuery(id+"F2.wireOp",EDGE,"E26.0.3.91")}),-1.0]])]});
            var Q236;
            Q236=makeQuery(id+"F2.imprint","IMPRINT",FACE,{"disambiguationData":[TD([[makeQuery(id+"F2.imprint","IMPRINT",EDGE,{"derivedFrom":sQuery(id+"F2.wireOp",EDGE,"E26.0.3.50")}),1.0]])]});
            var Q237;
            Q237=makeQuery(id+"F2.imprint","IMPRINT",FACE,{"disambiguationData":[TD([[makeQuery(id+"F2.imprint","IMPRINT",EDGE,{"derivedFrom":sQuery(id+"F2.wireOp",EDGE,"E26.0.3.37")}),-1.0]])]});
            var Q238;
            Q238=makeQuery(id+"F2.imprint","IMPRINT",FACE,{"disambiguationData":[TD([[makeQuery(id+"F2.imprint","IMPRINT",EDGE,{"derivedFrom":sQuery(id+"F2.wireOp",EDGE,"E26.0.3.80")}),1.0]])]});
            var Q239;
            Q239=makeQuery(id+"F2.imprint","IMPRINT",FACE,{"disambiguationData":[TD([[makeQuery(id+"F2.imprint","IMPRINT",EDGE,{"derivedFrom":sQuery(id+"F2.wireOp",EDGE,"E26.0.3.102")}),1.0]])]});
            var Q240;
            Q240=makeQuery(id+"F2.imprint","IMPRINT",FACE,{"disambiguationData":[TD([[makeQuery(id+"F2.imprint","IMPRINT",EDGE,{"derivedFrom":sQuery(id+"F2.wireOp",EDGE,"E26.0.3.130")}),-1.0]])]});
            var Q241;
            Q241=makeQuery(id+"F2.imprint","IMPRINT",FACE,{"disambiguationData":[TD([[makeQuery(id+"F2.imprint","IMPRINT",EDGE,{"derivedFrom":sQuery(id+"F2.wireOp",EDGE,"E26.0.3.191")}),1.0]])]});
            var Q242;
            Q242=makeQuery(id+"F2.imprint","IMPRINT",FACE,{"disambiguationData":[TD([[makeQuery(id+"F2.imprint","IMPRINT",EDGE,{"derivedFrom":sQuery(id+"F2.wireOp",EDGE,"E26.0.3.84")}),1.0]])]});
            var Q243;
            Q243=makeQuery(id+"F2.imprint","IMPRINT",FACE,{"disambiguationData":[TD([[makeQuery(id+"F2.imprint","IMPRINT",EDGE,{"derivedFrom":sQuery(id+"F2.wireOp",EDGE,"E26.0.3.88")}),-1.0]])]});
            var Q244;
            Q244=makeQuery(id+"F2.imprint","IMPRINT",FACE,{"disambiguationData":[TD([[makeQuery(id+"F2.imprint","IMPRINT",EDGE,{"derivedFrom":sQuery(id+"F2.wireOp",EDGE,"E26.0.3.60")}),1.0]])]});
            var Q245;
            Q245=makeQuery(id+"F2.imprint","IMPRINT",FACE,{"disambiguationData":[TD([[makeQuery(id+"F2.imprint","IMPRINT",EDGE,{"derivedFrom":sQuery(id+"F2.wireOp",EDGE,"E26.0.3.35")}),1.0]])]});
            var Q246;
            {var subQ0=sQuery(id+"F2.wireOp",EDGE,"E24.2.0.0");Q246=makeQuery(id+"F2.imprint","IMPRINT",FACE,{"disambiguationData":[TD([[makeQuery(id+"F2.imprint","IMPRINT",EDGE,{"derivedFrom":subQ0}),-1.0]])]});}
            var Q247;
            Q247=makeQuery(id+"F2.imprint","IMPRINT",FACE,{"disambiguationData":[TD([[makeQuery(id+"F2.imprint","IMPRINT",EDGE,{"derivedFrom":sQuery(id+"F2.wireOp",EDGE,"E24.1.0.5")}),-1.0]])]});
            var Q248;
            Q248=makeQuery(id+"F2.imprint","IMPRINT",FACE,{"disambiguationData":[TD([[makeQuery(id+"F2.imprint","IMPRINT",EDGE,{"derivedFrom":sQuery(id+"F2.wireOp",EDGE,"E25.0.1.22")}),1.0]])]});
            var Q249;
            Q249=makeQuery(id+"F2.imprint","IMPRINT",FACE,{"disambiguationData":[TD([[makeQuery(id+"F2.imprint","IMPRINT",EDGE,{"derivedFrom":sQuery(id+"F2.wireOp",EDGE,"E25.0.1.14")}),-1.0]])]});
            var Q250;
            Q250=makeQuery(id+"F2.imprint","IMPRINT",FACE,{"disambiguationData":[TD([[makeQuery(id+"F2.imprint","IMPRINT",EDGE,{"derivedFrom":sQuery(id+"F2.wireOp",EDGE,"E25.0.1.35")}),-1.0]])]});
            var Q251;
            Q251=makeQuery(id+"F2.imprint","IMPRINT",FACE,{"disambiguationData":[TD([[makeQuery(id+"F2.imprint","IMPRINT",EDGE,{"derivedFrom":sQuery(id+"F2.wireOp",EDGE,"E25.0.2.22")}),1.0]])]});
            var Q252;
            Q252=makeQuery(id+"F2.imprint","IMPRINT",FACE,{"disambiguationData":[TD([[makeQuery(id+"F2.imprint","IMPRINT",EDGE,{"derivedFrom":sQuery(id+"F2.wireOp",EDGE,"E25.0.2.11")}),-1.0]])]});
            var Q253;
            Q253=makeQuery(id+"F2.imprint","IMPRINT",FACE,{"disambiguationData":[TD([[makeQuery(id+"F2.imprint","IMPRINT",EDGE,{"derivedFrom":sQuery(id+"F2.wireOp",EDGE,"E25.0.1.3")}),-1.0]])]});
            var Q254;
            Q254=makeQuery(id+"F2.imprint","IMPRINT",FACE,{"disambiguationData":[TD([[makeQuery(id+"F2.imprint","IMPRINT",EDGE,{"derivedFrom":sQuery(id+"F2.wireOp",EDGE,"E25.0.2.15")}),1.0]])]});
            var Q255;
            Q255=makeQuery(id+"F2.imprint","IMPRINT",FACE,{"disambiguationData":[TD([[makeQuery(id+"F2.imprint","IMPRINT",EDGE,{"derivedFrom":sQuery(id+"F2.wireOp",EDGE,"E25.0.1.162")}),-1.0]])]});
            var Q256;
            Q256=makeQuery(id+"F2.imprint","IMPRINT",FACE,{"disambiguationData":[TD([[makeQuery(id+"F2.imprint","IMPRINT",EDGE,{"derivedFrom":sQuery(id+"F2.wireOp",EDGE,"E25.0.2.65")}),1.0]])]});
            var Q257;
            Q257=makeQuery(id+"F2.imprint","IMPRINT",FACE,{"disambiguationData":[TD([[makeQuery(id+"F2.imprint","IMPRINT",EDGE,{"derivedFrom":sQuery(id+"F2.wireOp",EDGE,"E25.0.1.69")}),-1.0]])]});
            var Q258;
            Q258=makeQuery(id+"F2.imprint","IMPRINT",FACE,{"disambiguationData":[TD([[makeQuery(id+"F2.imprint","IMPRINT",EDGE,{"derivedFrom":sQuery(id+"F2.wireOp",EDGE,"E25.0.2.221")}),-1.0]])]});
            var Q259;
            Q259=makeQuery(id+"F2.imprint","IMPRINT",FACE,{"disambiguationData":[TD([[makeQuery(id+"F2.imprint","IMPRINT",EDGE,{"derivedFrom":sQuery(id+"F2.wireOp",EDGE,"E25.0.1.62")}),-1.0]])]});
            var Q260;
            Q260=makeQuery(id+"F2.imprint","IMPRINT",FACE,{"disambiguationData":[TD([[makeQuery(id+"F2.imprint","IMPRINT",EDGE,{"derivedFrom":sQuery(id+"F2.wireOp",EDGE,"E25.0.2.55")}),1.0]])]});
            var Q261;
            Q261=makeQuery(id+"F2.imprint","IMPRINT",FACE,{"disambiguationData":[TD([[makeQuery(id+"F2.imprint","IMPRINT",EDGE,{"derivedFrom":sQuery(id+"F2.wireOp",EDGE,"E25.0.1.32")}),-1.0]])]});
            var Q262;
            Q262=makeQuery(id+"F2.imprint","IMPRINT",FACE,{"disambiguationData":[TD([[makeQuery(id+"F2.imprint","IMPRINT",EDGE,{"derivedFrom":sQuery(id+"F2.wireOp",EDGE,"E25.0.2.13")}),1.0]])]});
            var Q263;
            Q263=makeQuery(id+"F2.imprint","IMPRINT",FACE,{"disambiguationData":[TD([[makeQuery(id+"F2.imprint","IMPRINT",EDGE,{"derivedFrom":sQuery(id+"F2.wireOp",EDGE,"E25.0.1.12")}),-1.0]])]});
            var Q264;
            Q264=makeQuery(id+"F2.imprint","IMPRINT",FACE,{"disambiguationData":[TD([[makeQuery(id+"F2.imprint","IMPRINT",EDGE,{"derivedFrom":sQuery(id+"F2.wireOp",EDGE,"E25.0.2.149")}),-1.0]])]});
            var Q265;
            Q265=makeQuery(id+"F2.imprint","IMPRINT",FACE,{"disambiguationData":[TD([[makeQuery(id+"F2.imprint","IMPRINT",EDGE,{"derivedFrom":sQuery(id+"F2.wireOp",EDGE,"E25.0.1.63")}),-1.0]])]});
            var Q266;
            Q266=makeQuery(id+"F2.imprint","IMPRINT",FACE,{"disambiguationData":[TD([[makeQuery(id+"F2.imprint","IMPRINT",EDGE,{"derivedFrom":sQuery(id+"F2.wireOp",EDGE,"E25.0.1.149")}),-1.0]])]});
            var Q267;
            Q267=makeQuery(id+"F2.imprint","IMPRINT",FACE,{"disambiguationData":[TD([[makeQuery(id+"F2.imprint","IMPRINT",EDGE,{"derivedFrom":sQuery(id+"F2.wireOp",EDGE,"E24.3.0.5")}),-1.0]])]});
            var Q268;
            Q268=makeQuery(id+"F2.imprint","IMPRINT",FACE,{"disambiguationData":[TD([[makeQuery(id+"F2.imprint","IMPRINT",EDGE,{"derivedFrom":sQuery(id+"F2.wireOp",EDGE,"E25.0.1.13")}),1.0]])]});
            var Q269;
            Q269=makeQuery(id+"F2.imprint","IMPRINT",FACE,{"disambiguationData":[TD([[makeQuery(id+"F2.imprint","IMPRINT",EDGE,{"derivedFrom":sQuery(id+"F2.wireOp",EDGE,"E24.3.0.4")}),-1.0]])]});
            var Q270;
            Q270=makeQuery(id+"F2.imprint","IMPRINT",FACE,{"disambiguationData":[TD([[makeQuery(id+"F2.imprint","IMPRINT",EDGE,{"derivedFrom":sQuery(id+"F2.wireOp",EDGE,"E25.0.1.55")}),1.0]])]});
            var Q271;
            Q271=makeQuery(id+"F2.imprint","IMPRINT",FACE,{"disambiguationData":[TD([[makeQuery(id+"F2.imprint","IMPRINT",EDGE,{"derivedFrom":sQuery(id+"F2.wireOp",EDGE,"E24.3.0.14")}),-1.0]])]});
            var Q272;
            Q272=makeQuery(id+"F2.imprint","IMPRINT",FACE,{"disambiguationData":[TD([[makeQuery(id+"F2.imprint","IMPRINT",EDGE,{"derivedFrom":sQuery(id+"F2.wireOp",EDGE,"E25.0.1.221")}),-1.0]])]});
            var Q273;
            Q273=makeQuery(id+"F2.imprint","IMPRINT",FACE,{"disambiguationData":[TD([[makeQuery(id+"F2.imprint","IMPRINT",EDGE,{"derivedFrom":sQuery(id+"F2.wireOp",EDGE,"E24.2.0.5")}),-1.0]])]});
            var Q274;
            Q274=makeQuery(id+"F2.imprint","IMPRINT",FACE,{"disambiguationData":[TD([[makeQuery(id+"F2.imprint","IMPRINT",EDGE,{"derivedFrom":sQuery(id+"F2.wireOp",EDGE,"E25.0.1.65")}),1.0]])]});
            var Q275;
            Q275=makeQuery(id+"F2.imprint","IMPRINT",FACE,{"disambiguationData":[TD([[makeQuery(id+"F2.imprint","IMPRINT",EDGE,{"derivedFrom":sQuery(id+"F2.wireOp",EDGE,"E24.2.0.4")}),-1.0]])]});
            var Q276;
            Q276=makeQuery(id+"F2.imprint","IMPRINT",FACE,{"disambiguationData":[TD([[makeQuery(id+"F2.imprint","IMPRINT",EDGE,{"derivedFrom":sQuery(id+"F2.wireOp",EDGE,"E25.0.1.15")}),1.0]])]});
            var Q277;
            Q277=makeQuery(id+"F2.imprint","IMPRINT",FACE,{"disambiguationData":[TD([[makeQuery(id+"F2.imprint","IMPRINT",EDGE,{"derivedFrom":sQuery(id+"F2.wireOp",EDGE,"E24.2.0.14")}),-1.0]])]});
            var Q278;
            Q278=makeQuery(id+"F2.imprint","IMPRINT",FACE,{"disambiguationData":[TD([[makeQuery(id+"F2.imprint","IMPRINT",EDGE,{"derivedFrom":sQuery(id+"F2.wireOp",EDGE,"E25.0.1.11")}),-1.0]])]});
            var Q279;
            {var subQ0=sQuery(id+"F2.wireOp",EDGE,"E24.2.0.8");Q279=makeQuery(id+"F2.imprint","IMPRINT",FACE,{"disambiguationData":[TD([[makeQuery(id+"F2.imprint","IMPRINT",EDGE,{"derivedFrom":subQ0}),1.0]])]});}
            var Q280;
            {var subQ0=sQuery(id+"F2.wireOp",EDGE,"E24.2.0.2");Q280=makeQuery(id+"F2.imprint","IMPRINT",FACE,{"disambiguationData":[TD([[makeQuery(id+"F2.imprint","IMPRINT",EDGE,{"derivedFrom":subQ0}),1.0]])]});}
            var Q281;
            {var subQ0=sQuery(id+"F2.wireOp",EDGE,"E24.3.0.0");Q281=makeQuery(id+"F2.imprint","IMPRINT",FACE,{"disambiguationData":[TD([[makeQuery(id+"F2.imprint","IMPRINT",EDGE,{"derivedFrom":subQ0}),-1.0]])]});}
            var Q282;
            {var subQ0=sQuery(id+"F2.wireOp",EDGE,"E24.3.0.8");Q282=makeQuery(id+"F2.imprint","IMPRINT",FACE,{"disambiguationData":[TD([[makeQuery(id+"F2.imprint","IMPRINT",EDGE,{"derivedFrom":subQ0}),1.0]])]});}
            var Q283;
            {var subQ0=sQuery(id+"F2.wireOp",EDGE,"E24.3.0.2");Q283=makeQuery(id+"F2.imprint","IMPRINT",FACE,{"disambiguationData":[TD([[makeQuery(id+"F2.imprint","IMPRINT",EDGE,{"derivedFrom":subQ0}),1.0]])]});}
            var Q284;
            {var subQ0=sQuery(id+"F2.wireOp",EDGE,"E24.4.0.0");Q284=makeQuery(id+"F2.imprint","IMPRINT",FACE,{"disambiguationData":[TD([[makeQuery(id+"F2.imprint","IMPRINT",EDGE,{"derivedFrom":subQ0}),-1.0]])]});}
            var Q285;
            {var subQ0=sQuery(id+"F2.wireOp",EDGE,"E24.4.0.8");Q285=makeQuery(id+"F2.imprint","IMPRINT",FACE,{"disambiguationData":[TD([[makeQuery(id+"F2.imprint","IMPRINT",EDGE,{"derivedFrom":subQ0}),1.0]])]});}
            var Q286;
            {var subQ0=sQuery(id+"F2.wireOp",EDGE,"E24.4.0.2");Q286=makeQuery(id+"F2.imprint","IMPRINT",FACE,{"disambiguationData":[TD([[makeQuery(id+"F2.imprint","IMPRINT",EDGE,{"derivedFrom":subQ0}),1.0]])]});}
            var Q287;
            {var subQ0=sQuery(id+"F2.wireOp",EDGE,"E24.5.0.0");Q287=makeQuery(id+"F2.imprint","IMPRINT",FACE,{"disambiguationData":[TD([[makeQuery(id+"F2.imprint","IMPRINT",EDGE,{"derivedFrom":subQ0}),-1.0]])]});}
            var Q288;
            {var subQ0=sQuery(id+"F2.wireOp",EDGE,"E24.5.0.8");Q288=makeQuery(id+"F2.imprint","IMPRINT",FACE,{"disambiguationData":[TD([[makeQuery(id+"F2.imprint","IMPRINT",EDGE,{"derivedFrom":subQ0}),1.0]])]});}
            var Q289;
            {var subQ0=sQuery(id+"F2.wireOp",EDGE,"E24.5.0.2");Q289=makeQuery(id+"F2.imprint","IMPRINT",FACE,{"disambiguationData":[TD([[makeQuery(id+"F2.imprint","IMPRINT",EDGE,{"derivedFrom":subQ0}),1.0]])]});}
            var Q290;
            {var subQ0=sQuery(id+"F2.wireOp",EDGE,"E24.6.0.0");Q290=makeQuery(id+"F2.imprint","IMPRINT",FACE,{"disambiguationData":[TD([[makeQuery(id+"F2.imprint","IMPRINT",EDGE,{"derivedFrom":subQ0}),-1.0]])]});}
            var Q291;
            {var subQ0=sQuery(id+"F2.wireOp",EDGE,"E24.6.0.8");Q291=makeQuery(id+"F2.imprint","IMPRINT",FACE,{"disambiguationData":[TD([[makeQuery(id+"F2.imprint","IMPRINT",EDGE,{"derivedFrom":subQ0}),1.0]])]});}
            var Q292;
            Q292=makeQuery(id+"F2.imprint","IMPRINT",FACE,{"disambiguationData":[TD([[makeQuery(id+"F2.imprint","IMPRINT",EDGE,{"derivedFrom":sQuery(id+"F2.wireOp",EDGE,"E24.6.0.14")}),-1.0]])]});
            var Q293;
            Q293=makeQuery(id+"F2.imprint","IMPRINT",FACE,{"disambiguationData":[TD([[makeQuery(id+"F2.imprint","IMPRINT",EDGE,{"derivedFrom":sQuery(id+"F2.wireOp",EDGE,"E25.0.1.48")}),-1.0]])]});
            var Q294;
            Q294=makeQuery(id+"F2.imprint","IMPRINT",FACE,{"disambiguationData":[TD([[makeQuery(id+"F2.imprint","IMPRINT",EDGE,{"derivedFrom":sQuery(id+"F2.wireOp",EDGE,"E24.5.0.5")}),-1.0]])]});
            var Q295;
            Q295=makeQuery(id+"F2.imprint","IMPRINT",FACE,{"disambiguationData":[TD([[makeQuery(id+"F2.imprint","IMPRINT",EDGE,{"derivedFrom":sQuery(id+"F2.wireOp",EDGE,"E25.0.1.36")}),1.0]])]});
            var Q296;
            Q296=makeQuery(id+"F2.imprint","IMPRINT",FACE,{"disambiguationData":[TD([[makeQuery(id+"F2.imprint","IMPRINT",EDGE,{"derivedFrom":sQuery(id+"F2.wireOp",EDGE,"E24.5.0.4")}),-1.0]])]});
            var Q297;
            Q297=makeQuery(id+"F2.imprint","IMPRINT",FACE,{"disambiguationData":[TD([[makeQuery(id+"F2.imprint","IMPRINT",EDGE,{"derivedFrom":sQuery(id+"F2.wireOp",EDGE,"E25.0.1.18")}),1.0]])]});
            var Q298;
            Q298=makeQuery(id+"F2.imprint","IMPRINT",FACE,{"disambiguationData":[TD([[makeQuery(id+"F2.imprint","IMPRINT",EDGE,{"derivedFrom":sQuery(id+"F2.wireOp",EDGE,"E25.0.1.176")}),-1.0]])]});
            var Q299;
            Q299=makeQuery(id+"F2.imprint","IMPRINT",FACE,{"disambiguationData":[TD([[makeQuery(id+"F2.imprint","IMPRINT",EDGE,{"derivedFrom":sQuery(id+"F2.wireOp",EDGE,"E24.4.0.5")}),-1.0]])]});
            var Q300;
            Q300=makeQuery(id+"F2.imprint","IMPRINT",FACE,{"disambiguationData":[TD([[makeQuery(id+"F2.imprint","IMPRINT",EDGE,{"derivedFrom":sQuery(id+"F2.wireOp",EDGE,"E25.0.1.76")}),1.0]])]});
            var Q301;
            Q301=makeQuery(id+"F2.imprint","IMPRINT",FACE,{"disambiguationData":[TD([[makeQuery(id+"F2.imprint","IMPRINT",EDGE,{"derivedFrom":sQuery(id+"F2.wireOp",EDGE,"E24.4.0.4")}),-1.0]])]});
            var Q302;
            Q302=makeQuery(id+"F2.imprint","IMPRINT",FACE,{"disambiguationData":[TD([[makeQuery(id+"F2.imprint","IMPRINT",EDGE,{"derivedFrom":sQuery(id+"F2.wireOp",EDGE,"E25.0.1.146")}),1.0]])]});
            var Q303;
            Q303=makeQuery(id+"F2.imprint","IMPRINT",FACE,{"disambiguationData":[TD([[makeQuery(id+"F2.imprint","IMPRINT",EDGE,{"derivedFrom":sQuery(id+"F2.wireOp",EDGE,"E24.4.0.14")}),-1.0]])]});
            var Q304;
            Q304=makeQuery(id+"F2.imprint","IMPRINT",FACE,{"disambiguationData":[TD([[makeQuery(id+"F2.imprint","IMPRINT",EDGE,{"derivedFrom":sQuery(id+"F2.wireOp",EDGE,"E24.5.0.14")}),-1.0]])]});
            var Q305;
            Q305=makeQuery(id+"F2.imprint","IMPRINT",FACE,{"disambiguationData":[TD([[makeQuery(id+"F2.imprint","IMPRINT",EDGE,{"derivedFrom":sQuery(id+"F2.wireOp",EDGE,"E25.0.2.146")}),1.0]])]});
            var Q306;
            Q306=makeQuery(id+"F2.imprint","IMPRINT",FACE,{"disambiguationData":[TD([[makeQuery(id+"F2.imprint","IMPRINT",EDGE,{"derivedFrom":sQuery(id+"F2.wireOp",EDGE,"E25.0.1.56")}),-1.0]])]});
            var Q307;
            Q307=makeQuery(id+"F2.imprint","IMPRINT",FACE,{"disambiguationData":[TD([[makeQuery(id+"F2.imprint","IMPRINT",EDGE,{"derivedFrom":sQuery(id+"F2.wireOp",EDGE,"E25.0.2.76")}),1.0]])]});
            var Q308;
            Q308=makeQuery(id+"F2.imprint","IMPRINT",FACE,{"disambiguationData":[TD([[makeQuery(id+"F2.imprint","IMPRINT",EDGE,{"derivedFrom":sQuery(id+"F2.wireOp",EDGE,"E25.0.1.45")}),-1.0]])]});
            var Q309;
            Q309=makeQuery(id+"F2.imprint","IMPRINT",FACE,{"disambiguationData":[TD([[makeQuery(id+"F2.imprint","IMPRINT",EDGE,{"derivedFrom":sQuery(id+"F2.wireOp",EDGE,"E25.0.2.176")}),-1.0]])]});
            var Q310;
            Q310=makeQuery(id+"F2.imprint","IMPRINT",FACE,{"disambiguationData":[TD([[makeQuery(id+"F2.imprint","IMPRINT",EDGE,{"derivedFrom":sQuery(id+"F2.wireOp",EDGE,"E25.0.1.24")}),-1.0]])]});
            var Q311;
            Q311=makeQuery(id+"F2.imprint","IMPRINT",FACE,{"disambiguationData":[TD([[makeQuery(id+"F2.imprint","IMPRINT",EDGE,{"derivedFrom":sQuery(id+"F2.wireOp",EDGE,"E25.0.2.18")}),1.0]])]});
            var Q312;
            Q312=makeQuery(id+"F2.imprint","IMPRINT",FACE,{"disambiguationData":[TD([[makeQuery(id+"F2.imprint","IMPRINT",EDGE,{"derivedFrom":sQuery(id+"F2.wireOp",EDGE,"E25.0.1.16")}),-1.0]])]});
            var Q313;
            Q313=makeQuery(id+"F2.imprint","IMPRINT",FACE,{"disambiguationData":[TD([[makeQuery(id+"F2.imprint","IMPRINT",EDGE,{"derivedFrom":sQuery(id+"F2.wireOp",EDGE,"E25.0.2.36")}),1.0]])]});
            var Q314;
            Q314=makeQuery(id+"F2.imprint","IMPRINT",FACE,{"disambiguationData":[TD([[makeQuery(id+"F2.imprint","IMPRINT",EDGE,{"derivedFrom":sQuery(id+"F2.wireOp",EDGE,"E25.0.1.39")}),-1.0]])]});
            var Q315;
            Q315=makeQuery(id+"F2.imprint","IMPRINT",FACE,{"disambiguationData":[TD([[makeQuery(id+"F2.imprint","IMPRINT",EDGE,{"derivedFrom":sQuery(id+"F2.wireOp",EDGE,"E25.0.2.48")}),-1.0]])]});
            var Q316;
            Q316=makeQuery(id+"F2.imprint","IMPRINT",FACE,{"disambiguationData":[TD([[makeQuery(id+"F2.imprint","IMPRINT",EDGE,{"derivedFrom":sQuery(id+"F2.wireOp",EDGE,"E25.0.1.0")}),-1.0]])]});
            var Q317;
            Q317=makeQuery(id+"F2.imprint","IMPRINT",FACE,{"disambiguationData":[TD([[makeQuery(id+"F2.imprint","IMPRINT",EDGE,{"derivedFrom":sQuery(id+"F2.wireOp",EDGE,"E25.0.2.21")}),1.0]])]});
            var Q318;
            Q318=makeQuery(id+"F2.imprint","IMPRINT",FACE,{"disambiguationData":[TD([[makeQuery(id+"F2.imprint","IMPRINT",EDGE,{"derivedFrom":sQuery(id+"F2.wireOp",EDGE,"E25.0.1.94")}),-1.0]])]});
            var Q319;
            Q319=makeQuery(id+"F2.imprint","IMPRINT",FACE,{"disambiguationData":[TD([[makeQuery(id+"F2.imprint","IMPRINT",EDGE,{"derivedFrom":sQuery(id+"F2.wireOp",EDGE,"E25.0.1.21")}),1.0]])]});
            var Q320;
            Q320=makeQuery(id+"F2.imprint","IMPRINT",FACE,{"disambiguationData":[TD([[makeQuery(id+"F2.imprint","IMPRINT",EDGE,{"derivedFrom":sQuery(id+"F2.wireOp",EDGE,"E24.6.0.4")}),-1.0]])]});
            var Q321;
            Q321=makeQuery(id+"F2.imprint","IMPRINT",FACE,{"disambiguationData":[TD([[makeQuery(id+"F2.imprint","IMPRINT",EDGE,{"derivedFrom":sQuery(id+"F2.wireOp",EDGE,"E25.0.1.64")}),1.0]])]});
            var Q322;
            Q322=makeQuery(id+"F2.imprint","IMPRINT",FACE,{"disambiguationData":[TD([[makeQuery(id+"F2.imprint","IMPRINT",EDGE,{"derivedFrom":sQuery(id+"F2.wireOp",EDGE,"E25.0.1.74")}),-1.0]])]});
            var Q323;
            Q323=makeQuery(id+"F2.imprint","IMPRINT",FACE,{"disambiguationData":[TD([[makeQuery(id+"F2.imprint","IMPRINT",EDGE,{"derivedFrom":sQuery(id+"F2.wireOp",EDGE,"E25.0.2.64")}),1.0]])]});
            var Q324;
            {var subQ0=sQuery(id+"F2.wireOp",EDGE,"E24.6.0.2");Q324=makeQuery(id+"F2.imprint","IMPRINT",FACE,{"disambiguationData":[TD([[makeQuery(id+"F2.imprint","IMPRINT",EDGE,{"derivedFrom":subQ0}),1.0]])]});}
            var Q325;
            {var subQ0=sQuery(id+"F2.wireOp",EDGE,"E24.7.0.0");Q325=makeQuery(id+"F2.imprint","IMPRINT",FACE,{"disambiguationData":[TD([[makeQuery(id+"F2.imprint","IMPRINT",EDGE,{"derivedFrom":subQ0}),-1.0]])]});}
            var Q326;
            {var subQ0=sQuery(id+"F2.wireOp",EDGE,"E24.7.0.8");Q326=makeQuery(id+"F2.imprint","IMPRINT",FACE,{"disambiguationData":[TD([[makeQuery(id+"F2.imprint","IMPRINT",EDGE,{"derivedFrom":subQ0}),1.0]])]});}
            var Q327;
            {var subQ0=sQuery(id+"F2.wireOp",EDGE,"E24.7.0.2");Q327=makeQuery(id+"F2.imprint","IMPRINT",FACE,{"disambiguationData":[TD([[makeQuery(id+"F2.imprint","IMPRINT",EDGE,{"derivedFrom":subQ0}),1.0]])]});}
            var Q328;
            {var subQ0=sQuery(id+"F2.wireOp",EDGE,"E24.8.0.0");Q328=makeQuery(id+"F2.imprint","IMPRINT",FACE,{"disambiguationData":[TD([[makeQuery(id+"F2.imprint","IMPRINT",EDGE,{"derivedFrom":subQ0}),-1.0]])]});}
            var Q329;
            {var subQ0=sQuery(id+"F2.wireOp",EDGE,"E24.8.0.8");Q329=makeQuery(id+"F2.imprint","IMPRINT",FACE,{"disambiguationData":[TD([[makeQuery(id+"F2.imprint","IMPRINT",EDGE,{"derivedFrom":subQ0}),1.0]])]});}
            var Q330;
            {var subQ0=sQuery(id+"F2.wireOp",EDGE,"E24.8.0.2");Q330=makeQuery(id+"F2.imprint","IMPRINT",FACE,{"disambiguationData":[TD([[makeQuery(id+"F2.imprint","IMPRINT",EDGE,{"derivedFrom":subQ0}),1.0]])]});}
            var Q331;
            {var subQ0=sQuery(id+"F2.wireOp",EDGE,"E24.9.0.0");Q331=makeQuery(id+"F2.imprint","IMPRINT",FACE,{"disambiguationData":[TD([[makeQuery(id+"F2.imprint","IMPRINT",EDGE,{"derivedFrom":subQ0}),-1.0]])]});}
            var Q332;
            {var subQ5=sQuery(id+"F2.wireOp",EDGE,"E24.9.0.43");Q332=makeQuery(id+"F2.imprint","IMPRINT",FACE,{"disambiguationData":[TD([[makeQuery(id+"F2.imprint","IMPRINT",EDGE,{"derivedFrom":subQ5}),1.0]])]});}
            var Q333;
            {var subQ5=sQuery(id+"F2.wireOp",EDGE,"E24.9.0.4");Q333=makeQuery(id+"F2.imprint","IMPRINT",FACE,{"disambiguationData":[TD([[makeQuery(id+"F2.imprint","IMPRINT",EDGE,{"derivedFrom":subQ5}),-1.0]])]});}
            var Q334;
            Q334=makeQuery(id+"F2.imprint","IMPRINT",FACE,{"disambiguationData":[TD([[makeQuery(id+"F2.imprint","IMPRINT",EDGE,{"derivedFrom":sQuery(id+"F2.wireOp",EDGE,"E24.9.0.14")}),-1.0]])]});
            var Q335;
            {var subQ5=sQuery(id+"F2.wireOp",EDGE,"E25.0.1.282");Q335=makeQuery(id+"F2.imprint","IMPRINT",FACE,{"disambiguationData":[TD([[makeQuery(id+"F2.imprint","IMPRINT",EDGE,{"derivedFrom":subQ5}),1.0]])]});}
            var Q336;
            Q336=makeQuery(id+"F2.imprint","IMPRINT",FACE,{"disambiguationData":[TD([[makeQuery(id+"F2.imprint","IMPRINT",EDGE,{"derivedFrom":sQuery(id+"F2.wireOp",EDGE,"E25.0.1.226")}),-1.0]])]});
            var Q337;
            Q337=makeQuery(id+"F2.imprint","IMPRINT",FACE,{"disambiguationData":[TD([[makeQuery(id+"F2.imprint","IMPRINT",EDGE,{"derivedFrom":sQuery(id+"F2.wireOp",EDGE,"E24.8.0.5")}),-1.0]])]});
            var Q338;
            Q338=makeQuery(id+"F2.imprint","IMPRINT",FACE,{"disambiguationData":[TD([[makeQuery(id+"F2.imprint","IMPRINT",EDGE,{"derivedFrom":sQuery(id+"F2.wireOp",EDGE,"E25.0.1.72")}),1.0]])]});
            var Q339;
            Q339=makeQuery(id+"F2.imprint","IMPRINT",FACE,{"disambiguationData":[TD([[makeQuery(id+"F2.imprint","IMPRINT",EDGE,{"derivedFrom":sQuery(id+"F2.wireOp",EDGE,"E24.8.0.4")}),-1.0]])]});
            var Q340;
            Q340=makeQuery(id+"F2.imprint","IMPRINT",FACE,{"disambiguationData":[TD([[makeQuery(id+"F2.imprint","IMPRINT",EDGE,{"derivedFrom":sQuery(id+"F2.wireOp",EDGE,"E24.8.0.14")}),-1.0]])]});
            var Q341;
            Q341=makeQuery(id+"F2.imprint","IMPRINT",FACE,{"disambiguationData":[TD([[makeQuery(id+"F2.imprint","IMPRINT",EDGE,{"derivedFrom":sQuery(id+"F2.wireOp",EDGE,"E24.7.0.5")}),-1.0]])]});
            var Q342;
            Q342=makeQuery(id+"F2.imprint","IMPRINT",FACE,{"disambiguationData":[TD([[makeQuery(id+"F2.imprint","IMPRINT",EDGE,{"derivedFrom":sQuery(id+"F2.wireOp",EDGE,"E25.0.1.82")}),-1.0]])]});
            var Q343;
            Q343=makeQuery(id+"F2.imprint","IMPRINT",FACE,{"disambiguationData":[TD([[makeQuery(id+"F2.imprint","IMPRINT",EDGE,{"derivedFrom":sQuery(id+"F2.wireOp",EDGE,"E25.0.1.136")}),1.0]])]});
            var Q344;
            {var subQ5=sQuery(id+"F2.wireOp",EDGE,"E25.0.1.359");Q344=makeQuery(id+"F2.imprint","IMPRINT",FACE,{"disambiguationData":[TD([[makeQuery(id+"F2.imprint","IMPRINT",EDGE,{"derivedFrom":subQ5}),-1.0]])]});}
            var Q345;
            Q345=makeQuery(id+"F2.imprint","IMPRINT",FACE,{"disambiguationData":[TD([[makeQuery(id+"F2.imprint","IMPRINT",EDGE,{"derivedFrom":sQuery(id+"F2.wireOp",EDGE,"E25.0.1.23")}),-1.0]])]});
            var Q346;
            {var subQ0=sQuery(id+"F2.wireOp",EDGE,"E25.0.2.282");Q346=makeQuery(id+"F2.imprint","IMPRINT",FACE,{"disambiguationData":[TD([[makeQuery(id+"F2.imprint","IMPRINT",EDGE,{"derivedFrom":subQ0}),1.0]])]});}
            var Q347;
            Q347=makeQuery(id+"F2.imprint","IMPRINT",FACE,{"disambiguationData":[TD([[makeQuery(id+"F2.imprint","IMPRINT",EDGE,{"derivedFrom":sQuery(id+"F2.wireOp",EDGE,"E25.0.2.226")}),-1.0]])]});
            var Q348;
            Q348=makeQuery(id+"F2.imprint","IMPRINT",FACE,{"disambiguationData":[TD([[makeQuery(id+"F2.imprint","IMPRINT",EDGE,{"derivedFrom":sQuery(id+"F2.wireOp",EDGE,"E25.0.2.72")}),1.0]])]});
            var Q349;
            Q349=makeQuery(id+"F2.imprint","IMPRINT",FACE,{"disambiguationData":[TD([[makeQuery(id+"F2.imprint","IMPRINT",EDGE,{"derivedFrom":sQuery(id+"F2.wireOp",EDGE,"E25.0.2.136")}),1.0]])]});
            var Q350;
            Q350=makeQuery(id+"F2.imprint","IMPRINT",FACE,{"disambiguationData":[TD([[makeQuery(id+"F2.imprint","IMPRINT",EDGE,{"derivedFrom":sQuery(id+"F2.wireOp",EDGE,"E25.0.2.82")}),-1.0]])]});
            var Q351;
            Q351=makeQuery(id+"F2.imprint","IMPRINT",FACE,{"disambiguationData":[TD([[makeQuery(id+"F2.imprint","IMPRINT",EDGE,{"derivedFrom":sQuery(id+"F2.wireOp",EDGE,"E25.0.1.27")}),-1.0]])]});
            var Q352;
            Q352=makeQuery(id+"F2.imprint","IMPRINT",FACE,{"disambiguationData":[TD([[makeQuery(id+"F2.imprint","IMPRINT",EDGE,{"derivedFrom":sQuery(id+"F2.wireOp",EDGE,"E25.0.1.29")}),-1.0]])]});
            var Q353;
            Q353=makeQuery(id+"F2.imprint","IMPRINT",FACE,{"disambiguationData":[TD([[makeQuery(id+"F2.imprint","IMPRINT",EDGE,{"derivedFrom":sQuery(id+"F2.wireOp",EDGE,"E25.0.1.25")}),-1.0]])]});
            var Q354;
            Q354=makeQuery(id+"F2.imprint","IMPRINT",FACE,{"disambiguationData":[TD([[makeQuery(id+"F2.imprint","IMPRINT",EDGE,{"derivedFrom":sQuery(id+"F2.wireOp",EDGE,"E25.0.1.28")}),-1.0]])]});
            var Q355;
            {var subQ5=sQuery(id+"F2.wireOp",EDGE,"E25.0.2.359");Q355=makeQuery(id+"F2.imprint","IMPRINT",FACE,{"disambiguationData":[TD([[makeQuery(id+"F2.imprint","IMPRINT",EDGE,{"derivedFrom":subQ5}),-1.0]])]});}
            var Q356;
            {var subQ0=sQuery(id+"F2.wireOp",EDGE,"E25.0.3.282");Q356=makeQuery(id+"F2.imprint","IMPRINT",FACE,{"disambiguationData":[TD([[makeQuery(id+"F2.imprint","IMPRINT",EDGE,{"derivedFrom":subQ0}),1.0]])]});}
            var Q357;
            Q357=makeQuery(id+"F2.imprint","IMPRINT",FACE,{"disambiguationData":[TD([[makeQuery(id+"F2.imprint","IMPRINT",EDGE,{"derivedFrom":sQuery(id+"F2.wireOp",EDGE,"E25.0.2.23")}),-1.0]])]});
            var Q358;
            Q358=makeQuery(id+"F2.imprint","IMPRINT",FACE,{"disambiguationData":[TD([[makeQuery(id+"F2.imprint","IMPRINT",EDGE,{"derivedFrom":sQuery(id+"F2.wireOp",EDGE,"E25.0.3.226")}),-1.0]])]});
            var Q359;
            Q359=makeQuery(id+"F2.imprint","IMPRINT",FACE,{"disambiguationData":[TD([[makeQuery(id+"F2.imprint","IMPRINT",EDGE,{"derivedFrom":sQuery(id+"F2.wireOp",EDGE,"E25.0.3.23")}),-1.0]])]});
            var Q360;
            {var subQ5=sQuery(id+"F2.wireOp",EDGE,"E25.0.3.359");Q360=makeQuery(id+"F2.imprint","IMPRINT",FACE,{"disambiguationData":[TD([[makeQuery(id+"F2.imprint","IMPRINT",EDGE,{"derivedFrom":subQ5}),-1.0]])]});}
            var Q361;
            {var subQ0=sQuery(id+"F2.wireOp",EDGE,"E25.0.4.282");Q361=makeQuery(id+"F2.imprint","IMPRINT",FACE,{"disambiguationData":[TD([[makeQuery(id+"F2.imprint","IMPRINT",EDGE,{"derivedFrom":subQ0}),1.0]])]});}
            var Q362;
            Q362=makeQuery(id+"F2.imprint","IMPRINT",FACE,{"disambiguationData":[TD([[makeQuery(id+"F2.imprint","IMPRINT",EDGE,{"derivedFrom":sQuery(id+"F2.wireOp",EDGE,"E25.0.4.226")}),-1.0]])]});
            var Q363;
            Q363=makeQuery(id+"F2.imprint","IMPRINT",FACE,{"disambiguationData":[TD([[makeQuery(id+"F2.imprint","IMPRINT",EDGE,{"derivedFrom":sQuery(id+"F2.wireOp",EDGE,"E25.0.4.23")}),-1.0]])]});
            var Q364;
            Q364=makeQuery(id+"F2.imprint","IMPRINT",FACE,{"disambiguationData":[TD([[makeQuery(id+"F2.imprint","IMPRINT",EDGE,{"derivedFrom":sQuery(id+"F2.wireOp",EDGE,"E25.0.5.226")}),-1.0]])]});
            var Q365;
            Q365=makeQuery(id+"F2.imprint","IMPRINT",FACE,{"disambiguationData":[TD([[makeQuery(id+"F2.imprint","IMPRINT",EDGE,{"derivedFrom":sQuery(id+"F2.wireOp",EDGE,"E25.0.5.23")}),-1.0]])]});
            var Q366;
            {var subQ0=sQuery(id+"F2.wireOp",EDGE,"E25.0.5.282");Q366=makeQuery(id+"F2.imprint","IMPRINT",FACE,{"disambiguationData":[TD([[makeQuery(id+"F2.imprint","IMPRINT",EDGE,{"derivedFrom":subQ0}),1.0]])]});}
            var Q367;
            {var subQ5=sQuery(id+"F2.wireOp",EDGE,"E25.0.4.359");Q367=makeQuery(id+"F2.imprint","IMPRINT",FACE,{"disambiguationData":[TD([[makeQuery(id+"F2.imprint","IMPRINT",EDGE,{"derivedFrom":subQ5}),-1.0]])]});}
            var Q368;
            {var subQ5=sQuery(id+"F2.wireOp",EDGE,"E25.0.5.359");Q368=makeQuery(id+"F2.imprint","IMPRINT",FACE,{"disambiguationData":[TD([[makeQuery(id+"F2.imprint","IMPRINT",EDGE,{"derivedFrom":subQ5}),-1.0]])]});}
            var Q369;
            {var subQ0=sQuery(id+"F2.wireOp",EDGE,"E25.0.6.282");Q369=makeQuery(id+"F2.imprint","IMPRINT",FACE,{"disambiguationData":[TD([[makeQuery(id+"F2.imprint","IMPRINT",EDGE,{"derivedFrom":subQ0}),1.0]])]});}
            var Q370;
            {var subQ5=sQuery(id+"F2.wireOp",EDGE,"E25.0.6.359");Q370=makeQuery(id+"F2.imprint","IMPRINT",FACE,{"disambiguationData":[TD([[makeQuery(id+"F2.imprint","IMPRINT",EDGE,{"derivedFrom":subQ5}),-1.0]])]});}
            var Q371;
            Q371=makeQuery(id+"F2.imprint","IMPRINT",FACE,{"disambiguationData":[TD([[makeQuery(id+"F2.imprint","IMPRINT",EDGE,{"derivedFrom":sQuery(id+"F2.wireOp",EDGE,"E25.0.6.23")}),-1.0]])]});
            var Q372;
            Q372=makeQuery(id+"F2.imprint","IMPRINT",FACE,{"disambiguationData":[TD([[makeQuery(id+"F2.imprint","IMPRINT",EDGE,{"derivedFrom":sQuery(id+"F2.wireOp",EDGE,"E25.0.6.226")}),-1.0]])]});
            var Q373;
            {var subQ0=sQuery(id+"F2.wireOp",EDGE,"E25.0.7.282");Q373=makeQuery(id+"F2.imprint","IMPRINT",FACE,{"disambiguationData":[TD([[makeQuery(id+"F2.imprint","IMPRINT",EDGE,{"derivedFrom":subQ0}),1.0]])]});}
            var Q374;
            {var subQ5=sQuery(id+"F2.wireOp",EDGE,"E25.0.7.359");Q374=makeQuery(id+"F2.imprint","IMPRINT",FACE,{"disambiguationData":[TD([[makeQuery(id+"F2.imprint","IMPRINT",EDGE,{"derivedFrom":subQ5}),-1.0]])]});}
            var Q375;
            Q375=makeQuery(id+"F2.imprint","IMPRINT",FACE,{"disambiguationData":[TD([[makeQuery(id+"F2.imprint","IMPRINT",EDGE,{"derivedFrom":sQuery(id+"F2.wireOp",EDGE,"E25.0.7.23")}),-1.0]])]});
            var Q376;
            Q376=makeQuery(id+"F2.imprint","IMPRINT",FACE,{"disambiguationData":[TD([[makeQuery(id+"F2.imprint","IMPRINT",EDGE,{"derivedFrom":sQuery(id+"F2.wireOp",EDGE,"E25.0.7.226")}),-1.0]])]});
            var Q377;
            {var subQ0=sQuery(id+"F2.wireOp",EDGE,"E25.0.8.282");Q377=makeQuery(id+"F2.imprint","IMPRINT",FACE,{"disambiguationData":[TD([[makeQuery(id+"F2.imprint","IMPRINT",EDGE,{"derivedFrom":subQ0}),1.0]])]});}
            var Q378;
            {var subQ5=sQuery(id+"F2.wireOp",EDGE,"E25.0.8.359");Q378=makeQuery(id+"F2.imprint","IMPRINT",FACE,{"disambiguationData":[TD([[makeQuery(id+"F2.imprint","IMPRINT",EDGE,{"derivedFrom":subQ5}),-1.0]])]});}
            var Q379;
            Q379=makeQuery(id+"F2.imprint","IMPRINT",FACE,{"disambiguationData":[TD([[makeQuery(id+"F2.imprint","IMPRINT",EDGE,{"derivedFrom":sQuery(id+"F2.wireOp",EDGE,"E25.0.8.226")}),-1.0]])]});
            var Q380;
            Q380=makeQuery(id+"F2.imprint","IMPRINT",FACE,{"disambiguationData":[TD([[makeQuery(id+"F2.imprint","IMPRINT",EDGE,{"derivedFrom":sQuery(id+"F2.wireOp",EDGE,"E25.0.8.23")}),-1.0]])]});
            var Q381;
            Q381=makeQuery(id+"F2.imprint","IMPRINT",FACE,{"disambiguationData":[TD([[makeQuery(id+"F2.imprint","IMPRINT",EDGE,{"derivedFrom":sQuery(id+"F2.wireOp",EDGE,"E26.0.1.142")}),1.0]])]});
            var Q382;
            Q382=makeQuery(id+"F2.imprint","IMPRINT",FACE,{"disambiguationData":[TD([[makeQuery(id+"F2.imprint","IMPRINT",EDGE,{"derivedFrom":sQuery(id+"F2.wireOp",EDGE,"E26.0.1.100")}),-1.0]])]});
            var Q383;
            Q383=makeQuery(id+"F2.imprint","IMPRINT",FACE,{"disambiguationData":[TD([[makeQuery(id+"F2.imprint","IMPRINT",EDGE,{"derivedFrom":sQuery(id+"F2.wireOp",EDGE,"E26.0.1.66")}),-1.0]])]});
            var Q384;
            Q384=makeQuery(id+"F2.imprint","IMPRINT",FACE,{"disambiguationData":[TD([[makeQuery(id+"F2.imprint","IMPRINT",EDGE,{"derivedFrom":sQuery(id+"F2.wireOp",EDGE,"E26.0.1.22")}),-1.0]])]});
            var Q385;
            Q385=makeQuery(id+"F2.imprint","IMPRINT",FACE,{"disambiguationData":[TD([[makeQuery(id+"F2.imprint","IMPRINT",EDGE,{"derivedFrom":sQuery(id+"F2.wireOp",EDGE,"E25.0.8.28")}),-1.0]])]});
            var Q386;
            {var subQ5=sQuery(id+"F2.wireOp",EDGE,"E26.0.1.151");Q386=makeQuery(id+"F2.imprint","IMPRINT",FACE,{"disambiguationData":[TD([[makeQuery(id+"F2.imprint","IMPRINT",EDGE,{"derivedFrom":subQ5}),-1.0]])]});}
            var Q387;
            Q387=makeQuery(id+"F2.imprint","IMPRINT",FACE,{"disambiguationData":[TD([[makeQuery(id+"F2.imprint","IMPRINT",EDGE,{"derivedFrom":sQuery(id+"F2.wireOp",EDGE,"E26.0.2.142")}),1.0]])]});
            var Q388;
            {var subQ5=sQuery(id+"F2.wireOp",EDGE,"E26.0.2.151");Q388=makeQuery(id+"F2.imprint","IMPRINT",FACE,{"disambiguationData":[TD([[makeQuery(id+"F2.imprint","IMPRINT",EDGE,{"derivedFrom":subQ5}),-1.0]])]});}
            var Q389;
            Q389=makeQuery(id+"F2.imprint","IMPRINT",FACE,{"disambiguationData":[TD([[makeQuery(id+"F2.imprint","IMPRINT",EDGE,{"derivedFrom":sQuery(id+"F2.wireOp",EDGE,"E26.0.2.66")}),-1.0]])]});
            var Q390;
            Q390=makeQuery(id+"F2.imprint","IMPRINT",FACE,{"disambiguationData":[TD([[makeQuery(id+"F2.imprint","IMPRINT",EDGE,{"derivedFrom":sQuery(id+"F2.wireOp",EDGE,"E26.0.2.100")}),-1.0]])]});
            var Q391;
            Q391=makeQuery(id+"F2.imprint","IMPRINT",FACE,{"disambiguationData":[TD([[makeQuery(id+"F2.imprint","IMPRINT",EDGE,{"derivedFrom":sQuery(id+"F2.wireOp",EDGE,"E26.0.2.22")}),-1.0]])]});
            var Q392;
            Q392=makeQuery(id+"F2.imprint","IMPRINT",FACE,{"disambiguationData":[TD([[makeQuery(id+"F2.imprint","IMPRINT",EDGE,{"derivedFrom":sQuery(id+"F2.wireOp",EDGE,"E26.0.2.136")}),1.0]])]});
            var Q393;
            Q393=makeQuery(id+"F2.imprint","IMPRINT",FACE,{"disambiguationData":[TD([[makeQuery(id+"F2.imprint","IMPRINT",EDGE,{"derivedFrom":sQuery(id+"F2.wireOp",EDGE,"E26.0.2.71")}),-1.0]])]});
            var Q394;
            Q394=makeQuery(id+"F2.imprint","IMPRINT",FACE,{"disambiguationData":[TD([[makeQuery(id+"F2.imprint","IMPRINT",EDGE,{"derivedFrom":sQuery(id+"F2.wireOp",EDGE,"E26.0.2.113")}),1.0]])]});
            var Q395;
            Q395=makeQuery(id+"F2.imprint","IMPRINT",FACE,{"disambiguationData":[TD([[makeQuery(id+"F2.imprint","IMPRINT",EDGE,{"derivedFrom":sQuery(id+"F2.wireOp",EDGE,"E26.0.2.62")}),-1.0]])]});
            var Q396;
            Q396=makeQuery(id+"F2.imprint","IMPRINT",FACE,{"disambiguationData":[TD([[makeQuery(id+"F2.imprint","IMPRINT",EDGE,{"derivedFrom":sQuery(id+"F2.wireOp",EDGE,"E26.0.2.87")}),-1.0]])]});
            var Q397;
            Q397=makeQuery(id+"F2.imprint","IMPRINT",FACE,{"disambiguationData":[TD([[makeQuery(id+"F2.imprint","IMPRINT",EDGE,{"derivedFrom":sQuery(id+"F2.wireOp",EDGE,"E26.0.2.164")}),-1.0]])]});
            var Q398;
            Q398=makeQuery(id+"F2.imprint","IMPRINT",FACE,{"disambiguationData":[TD([[makeQuery(id+"F2.imprint","IMPRINT",EDGE,{"derivedFrom":sQuery(id+"F2.wireOp",EDGE,"E26.0.2.112")}),1.0]])]});
            var Q399;
            Q399=makeQuery(id+"F2.imprint","IMPRINT",FACE,{"disambiguationData":[TD([[makeQuery(id+"F2.imprint","IMPRINT",EDGE,{"derivedFrom":sQuery(id+"F2.wireOp",EDGE,"E26.0.2.117")}),-1.0]])]});
            var Q400;
            Q400=makeQuery(id+"F2.imprint","IMPRINT",FACE,{"disambiguationData":[TD([[makeQuery(id+"F2.imprint","IMPRINT",EDGE,{"derivedFrom":sQuery(id+"F2.wireOp",EDGE,"E26.0.2.33")}),1.0]])]});
            var Q401;
            Q401=makeQuery(id+"F2.imprint","IMPRINT",FACE,{"disambiguationData":[TD([[makeQuery(id+"F2.imprint","IMPRINT",EDGE,{"derivedFrom":sQuery(id+"F2.wireOp",EDGE,"E26.0.2.6")}),-1.0]])]});
            var Q402;
            Q402=makeQuery(id+"F2.imprint","IMPRINT",FACE,{"disambiguationData":[TD([[makeQuery(id+"F2.imprint","IMPRINT",EDGE,{"derivedFrom":sQuery(id+"F2.wireOp",EDGE,"E26.0.2.46")}),-1.0]])]});
            var Q403;
            Q403=makeQuery(id+"F2.imprint","IMPRINT",FACE,{"disambiguationData":[TD([[makeQuery(id+"F2.imprint","IMPRINT",EDGE,{"derivedFrom":sQuery(id+"F2.wireOp",EDGE,"E26.0.2.34")}),-1.0]])]});
            var Q404;
            Q404=makeQuery(id+"F2.imprint","IMPRINT",FACE,{"disambiguationData":[TD([[makeQuery(id+"F2.imprint","IMPRINT",EDGE,{"derivedFrom":sQuery(id+"F2.wireOp",EDGE,"E26.0.2.106")}),1.0]])]});
            var Q405;
            Q405=makeQuery(id+"F2.imprint","IMPRINT",FACE,{"disambiguationData":[TD([[makeQuery(id+"F2.imprint","IMPRINT",EDGE,{"derivedFrom":sQuery(id+"F2.wireOp",EDGE,"E26.0.2.99")}),-1.0]])]});
            var Q406;
            Q406=makeQuery(id+"F2.imprint","IMPRINT",FACE,{"disambiguationData":[TD([[makeQuery(id+"F2.imprint","IMPRINT",EDGE,{"derivedFrom":sQuery(id+"F2.wireOp",EDGE,"E26.0.2.111")}),1.0]])]});
            var Q407;
            Q407=makeQuery(id+"F2.imprint","IMPRINT",FACE,{"disambiguationData":[TD([[makeQuery(id+"F2.imprint","IMPRINT",EDGE,{"derivedFrom":sQuery(id+"F2.wireOp",EDGE,"E26.0.2.12")}),-1.0]])]});
            var Q408;
            Q408=makeQuery(id+"F2.imprint","IMPRINT",FACE,{"disambiguationData":[TD([[makeQuery(id+"F2.imprint","IMPRINT",EDGE,{"derivedFrom":sQuery(id+"F2.wireOp",EDGE,"E26.0.2.63")}),-1.0]])]});
            var Q409;
            Q409=makeQuery(id+"F2.imprint","IMPRINT",FACE,{"disambiguationData":[TD([[makeQuery(id+"F2.imprint","IMPRINT",EDGE,{"derivedFrom":sQuery(id+"F2.wireOp",EDGE,"E26.0.2.8")}),-1.0]])]});
            var Q410;
            Q410=makeQuery(id+"F2.imprint","IMPRINT",FACE,{"disambiguationData":[TD([[makeQuery(id+"F2.imprint","IMPRINT",EDGE,{"derivedFrom":sQuery(id+"F2.wireOp",EDGE,"E26.0.2.30")}),1.0]])]});
            var Q411;
            Q411=makeQuery(id+"F2.imprint","IMPRINT",FACE,{"disambiguationData":[TD([[makeQuery(id+"F2.imprint","IMPRINT",EDGE,{"derivedFrom":sQuery(id+"F2.wireOp",EDGE,"E26.0.2.18")}),-1.0]])]});
            var Q412;
            Q412=makeQuery(id+"F2.imprint","IMPRINT",FACE,{"disambiguationData":[TD([[makeQuery(id+"F2.imprint","IMPRINT",EDGE,{"derivedFrom":sQuery(id+"F2.wireOp",EDGE,"E26.0.2.143")}),1.0]])]});
            var Q413;
            Q413=makeQuery(id+"F2.imprint","IMPRINT",FACE,{"disambiguationData":[TD([[makeQuery(id+"F2.imprint","IMPRINT",EDGE,{"derivedFrom":sQuery(id+"F2.wireOp",EDGE,"E26.0.2.7")}),-1.0]])]});
            var Q414;
            Q414=makeQuery(id+"F2.imprint","IMPRINT",FACE,{"disambiguationData":[TD([[makeQuery(id+"F2.imprint","IMPRINT",EDGE,{"derivedFrom":sQuery(id+"F2.wireOp",EDGE,"E26.0.2.91")}),-1.0]])]});
            var Q415;
            Q415=makeQuery(id+"F2.imprint","IMPRINT",FACE,{"disambiguationData":[TD([[makeQuery(id+"F2.imprint","IMPRINT",EDGE,{"derivedFrom":sQuery(id+"F2.wireOp",EDGE,"E26.0.2.13")}),-1.0]])]});
            var Q416;
            Q416=makeQuery(id+"F2.imprint","IMPRINT",FACE,{"disambiguationData":[TD([[makeQuery(id+"F2.imprint","IMPRINT",EDGE,{"derivedFrom":sQuery(id+"F2.wireOp",EDGE,"E26.0.2.35")}),1.0]])]});
            var Q417;
            Q417=makeQuery(id+"F2.imprint","IMPRINT",FACE,{"disambiguationData":[TD([[makeQuery(id+"F2.imprint","IMPRINT",EDGE,{"derivedFrom":sQuery(id+"F2.wireOp",EDGE,"E26.0.2.3")}),-1.0]])]});
            var Q418;
            Q418=makeQuery(id+"F2.imprint","IMPRINT",FACE,{"disambiguationData":[TD([[makeQuery(id+"F2.imprint","IMPRINT",EDGE,{"derivedFrom":sQuery(id+"F2.wireOp",EDGE,"E26.0.2.60")}),1.0]])]});
            var Q419;
            Q419=makeQuery(id+"F2.imprint","IMPRINT",FACE,{"disambiguationData":[TD([[makeQuery(id+"F2.imprint","IMPRINT",EDGE,{"derivedFrom":sQuery(id+"F2.wireOp",EDGE,"E26.0.2.23")}),-1.0]])]});
            var Q420;
            Q420=makeQuery(id+"F2.imprint","IMPRINT",FACE,{"disambiguationData":[TD([[makeQuery(id+"F2.imprint","IMPRINT",EDGE,{"derivedFrom":sQuery(id+"F2.wireOp",EDGE,"E26.0.2.88")}),-1.0]])]});
            var Q421;
            Q421=makeQuery(id+"F2.imprint","IMPRINT",FACE,{"disambiguationData":[TD([[makeQuery(id+"F2.imprint","IMPRINT",EDGE,{"derivedFrom":sQuery(id+"F2.wireOp",EDGE,"E26.0.2.54")}),-1.0]])]});
            var Q422;
            Q422=makeQuery(id+"F2.imprint","IMPRINT",FACE,{"disambiguationData":[TD([[makeQuery(id+"F2.imprint","IMPRINT",EDGE,{"derivedFrom":sQuery(id+"F2.wireOp",EDGE,"E26.0.2.84")}),1.0]])]});
            var Q423;
            Q423=makeQuery(id+"F2.imprint","IMPRINT",FACE,{"disambiguationData":[TD([[makeQuery(id+"F2.imprint","IMPRINT",EDGE,{"derivedFrom":sQuery(id+"F2.wireOp",EDGE,"E26.0.2.16")}),-1.0]])]});
            var Q424;
            Q424=makeQuery(id+"F2.imprint","IMPRINT",FACE,{"disambiguationData":[TD([[makeQuery(id+"F2.imprint","IMPRINT",EDGE,{"derivedFrom":sQuery(id+"F2.wireOp",EDGE,"E26.0.2.191")}),1.0]])]});
            var Q425;
            Q425=makeQuery(id+"F2.imprint","IMPRINT",FACE,{"disambiguationData":[TD([[makeQuery(id+"F2.imprint","IMPRINT",EDGE,{"derivedFrom":sQuery(id+"F2.wireOp",EDGE,"E26.0.2.43")}),-1.0]])]});
            var Q426;
            Q426=makeQuery(id+"F2.imprint","IMPRINT",FACE,{"disambiguationData":[TD([[makeQuery(id+"F2.imprint","IMPRINT",EDGE,{"derivedFrom":sQuery(id+"F2.wireOp",EDGE,"E26.0.2.130")}),-1.0]])]});
            var Q427;
            Q427=makeQuery(id+"F2.imprint","IMPRINT",FACE,{"disambiguationData":[TD([[makeQuery(id+"F2.imprint","IMPRINT",EDGE,{"derivedFrom":sQuery(id+"F2.wireOp",EDGE,"E26.0.2.102")}),1.0]])]});
            var Q428;
            Q428=makeQuery(id+"F2.imprint","IMPRINT",FACE,{"disambiguationData":[TD([[makeQuery(id+"F2.imprint","IMPRINT",EDGE,{"derivedFrom":sQuery(id+"F2.wireOp",EDGE,"E26.0.2.38")}),-1.0]])]});
            var Q429;
            Q429=makeQuery(id+"F2.imprint","IMPRINT",FACE,{"disambiguationData":[TD([[makeQuery(id+"F2.imprint","IMPRINT",EDGE,{"derivedFrom":sQuery(id+"F2.wireOp",EDGE,"E26.0.2.48")}),-1.0]])]});
            var Q430;
            Q430=makeQuery(id+"F2.imprint","IMPRINT",FACE,{"disambiguationData":[TD([[makeQuery(id+"F2.imprint","IMPRINT",EDGE,{"derivedFrom":sQuery(id+"F2.wireOp",EDGE,"E26.0.2.80")}),1.0]])]});
            var Q431;
            Q431=makeQuery(id+"F2.imprint","IMPRINT",FACE,{"disambiguationData":[TD([[makeQuery(id+"F2.imprint","IMPRINT",EDGE,{"derivedFrom":sQuery(id+"F2.wireOp",EDGE,"E26.0.2.2")}),-1.0]])]});
            var Q432;
            Q432=makeQuery(id+"F2.imprint","IMPRINT",FACE,{"disambiguationData":[TD([[makeQuery(id+"F2.imprint","IMPRINT",EDGE,{"derivedFrom":sQuery(id+"F2.wireOp",EDGE,"E26.0.2.37")}),-1.0]])]});
            var Q433;
            Q433=makeQuery(id+"F2.imprint","IMPRINT",FACE,{"disambiguationData":[TD([[makeQuery(id+"F2.imprint","IMPRINT",EDGE,{"derivedFrom":sQuery(id+"F2.wireOp",EDGE,"E26.0.2.41")}),-1.0]])]});
            var Q434;
            Q434=makeQuery(id+"F2.imprint","IMPRINT",FACE,{"disambiguationData":[TD([[makeQuery(id+"F2.imprint","IMPRINT",EDGE,{"derivedFrom":sQuery(id+"F2.wireOp",EDGE,"E26.0.2.50")}),1.0]])]});
            var Q435;
            Q435=makeQuery(id+"F2.imprint","IMPRINT",FACE,{"disambiguationData":[TD([[makeQuery(id+"F2.imprint","IMPRINT",EDGE,{"derivedFrom":sQuery(id+"F2.wireOp",EDGE,"E26.0.2.9")}),-1.0]])]});
            var Q436;
            Q436=makeQuery(id+"F2.imprint","IMPRINT",FACE,{"disambiguationData":[TD([[makeQuery(id+"F2.imprint","IMPRINT",EDGE,{"derivedFrom":sQuery(id+"F2.wireOp",EDGE,"E26.0.1.9")}),-1.0]])]});
            var Q437;
            Q437=makeQuery(id+"F2.imprint","IMPRINT",FACE,{"disambiguationData":[TD([[makeQuery(id+"F2.imprint","IMPRINT",EDGE,{"derivedFrom":sQuery(id+"F2.wireOp",EDGE,"E26.0.1.50")}),1.0]])]});
            var Q438;
            Q438=makeQuery(id+"F2.imprint","IMPRINT",FACE,{"disambiguationData":[TD([[makeQuery(id+"F2.imprint","IMPRINT",EDGE,{"derivedFrom":sQuery(id+"F2.wireOp",EDGE,"E25.0.8.14")}),-1.0]])]});
            var Q439;
            Q439=makeQuery(id+"F2.imprint","IMPRINT",FACE,{"disambiguationData":[TD([[makeQuery(id+"F2.imprint","IMPRINT",EDGE,{"derivedFrom":sQuery(id+"F2.wireOp",EDGE,"E25.0.8.35")}),-1.0]])]});
            var Q440;
            Q440=makeQuery(id+"F2.imprint","IMPRINT",FACE,{"disambiguationData":[TD([[makeQuery(id+"F2.imprint","IMPRINT",EDGE,{"derivedFrom":sQuery(id+"F2.wireOp",EDGE,"E26.0.1.37")}),-1.0]])]});
            var Q441;
            Q441=makeQuery(id+"F2.imprint","IMPRINT",FACE,{"disambiguationData":[TD([[makeQuery(id+"F2.imprint","IMPRINT",EDGE,{"derivedFrom":sQuery(id+"F2.wireOp",EDGE,"E26.0.1.41")}),-1.0]])]});
            var Q442;
            Q442=makeQuery(id+"F2.imprint","IMPRINT",FACE,{"disambiguationData":[TD([[makeQuery(id+"F2.imprint","IMPRINT",EDGE,{"derivedFrom":sQuery(id+"F2.wireOp",EDGE,"E26.0.1.2")}),-1.0]])]});
            var Q443;
            Q443=makeQuery(id+"F2.imprint","IMPRINT",FACE,{"disambiguationData":[TD([[makeQuery(id+"F2.imprint","IMPRINT",EDGE,{"derivedFrom":sQuery(id+"F2.wireOp",EDGE,"E24.6.0.5")}),-1.0]])]});
            var Q444;
            Q444=makeQuery(id+"F2.imprint","IMPRINT",FACE,{"disambiguationData":[TD([[makeQuery(id+"F2.imprint","IMPRINT",EDGE,{"derivedFrom":sQuery(id+"F2.wireOp",EDGE,"E24.7.0.14")}),-1.0]])]});
            var Q445;
            Q445=makeQuery(id+"F2.imprint","IMPRINT",FACE,{"disambiguationData":[TD([[makeQuery(id+"F2.imprint","IMPRINT",EDGE,{"derivedFrom":sQuery(id+"F2.wireOp",EDGE,"E24.7.0.4")}),-1.0]])]});
            var Q446;
            Q446=makeQuery(id+"F2.imprint","IMPRINT",FACE,{"disambiguationData":[TD([[makeQuery(id+"F2.imprint","IMPRINT",EDGE,{"derivedFrom":sQuery(id+"F2.wireOp",EDGE,"E25.0.1.26")}),1.0]])]});
            var Q447;
            Q447=makeQuery(id+"F2.imprint","IMPRINT",FACE,{"disambiguationData":[TD([[makeQuery(id+"F2.imprint","IMPRINT",EDGE,{"derivedFrom":sQuery(id+"F2.wireOp",EDGE,"E25.0.1.54")}),1.0]])]});
            var Q448;
            Q448=makeQuery(id+"F2.imprint","IMPRINT",FACE,{"disambiguationData":[TD([[makeQuery(id+"F2.imprint","IMPRINT",EDGE,{"derivedFrom":sQuery(id+"F2.wireOp",EDGE,"E25.0.1.213")}),-1.0]])]});
            var Q449;
            Q449=makeQuery(id+"F2.imprint","IMPRINT",FACE,{"disambiguationData":[TD([[makeQuery(id+"F2.imprint","IMPRINT",EDGE,{"derivedFrom":sQuery(id+"F2.wireOp",EDGE,"E25.0.1.58")}),-1.0]])]});
            var Q450;
            Q450=makeQuery(id+"F2.imprint","IMPRINT",FACE,{"disambiguationData":[TD([[makeQuery(id+"F2.imprint","IMPRINT",EDGE,{"derivedFrom":sQuery(id+"F2.wireOp",EDGE,"E25.0.1.34")}),-1.0]])]});
            var Q451;
            Q451=makeQuery(id+"F2.imprint","IMPRINT",FACE,{"disambiguationData":[TD([[makeQuery(id+"F2.imprint","IMPRINT",EDGE,{"derivedFrom":sQuery(id+"F2.wireOp",EDGE,"E25.0.2.26")}),1.0]])]});
            var Q452;
            Q452=makeQuery(id+"F2.imprint","IMPRINT",FACE,{"disambiguationData":[TD([[makeQuery(id+"F2.imprint","IMPRINT",EDGE,{"derivedFrom":sQuery(id+"F2.wireOp",EDGE,"E25.0.2.54")}),1.0]])]});
            var Q453;
            Q453=makeQuery(id+"F2.imprint","IMPRINT",FACE,{"disambiguationData":[TD([[makeQuery(id+"F2.imprint","IMPRINT",EDGE,{"derivedFrom":sQuery(id+"F2.wireOp",EDGE,"E25.0.2.213")}),-1.0]])]});
            var Q454;
            Q454=makeQuery(id+"F2.imprint","IMPRINT",FACE,{"disambiguationData":[TD([[makeQuery(id+"F2.imprint","IMPRINT",EDGE,{"derivedFrom":sQuery(id+"F2.wireOp",EDGE,"E25.0.2.28")}),-1.0]])]});
            var Q455;
            Q455=makeQuery(id+"F2.imprint","IMPRINT",FACE,{"disambiguationData":[TD([[makeQuery(id+"F2.imprint","IMPRINT",EDGE,{"derivedFrom":sQuery(id+"F2.wireOp",EDGE,"E25.0.3.72")}),1.0]])]});
            var Q456;
            Q456=makeQuery(id+"F2.imprint","IMPRINT",FACE,{"disambiguationData":[TD([[makeQuery(id+"F2.imprint","IMPRINT",EDGE,{"derivedFrom":sQuery(id+"F2.wireOp",EDGE,"E25.0.2.25")}),-1.0]])]});
            var Q457;
            Q457=makeQuery(id+"F2.imprint","IMPRINT",FACE,{"disambiguationData":[TD([[makeQuery(id+"F2.imprint","IMPRINT",EDGE,{"derivedFrom":sQuery(id+"F2.wireOp",EDGE,"E25.0.3.28")}),-1.0]])]});
            var Q458;
            Q458=makeQuery(id+"F2.imprint","IMPRINT",FACE,{"disambiguationData":[TD([[makeQuery(id+"F2.imprint","IMPRINT",EDGE,{"derivedFrom":sQuery(id+"F2.wireOp",EDGE,"E25.0.4.72")}),1.0]])]});
            var Q459;
            Q459=makeQuery(id+"F2.imprint","IMPRINT",FACE,{"disambiguationData":[TD([[makeQuery(id+"F2.imprint","IMPRINT",EDGE,{"derivedFrom":sQuery(id+"F2.wireOp",EDGE,"E25.0.4.28")}),-1.0]])]});
            var Q460;
            Q460=makeQuery(id+"F2.imprint","IMPRINT",FACE,{"disambiguationData":[TD([[makeQuery(id+"F2.imprint","IMPRINT",EDGE,{"derivedFrom":sQuery(id+"F2.wireOp",EDGE,"E25.0.5.72")}),1.0]])]});
            var Q461;
            Q461=makeQuery(id+"F2.imprint","IMPRINT",FACE,{"disambiguationData":[TD([[makeQuery(id+"F2.imprint","IMPRINT",EDGE,{"derivedFrom":sQuery(id+"F2.wireOp",EDGE,"E25.0.5.28")}),-1.0]])]});
            var Q462;
            Q462=makeQuery(id+"F2.imprint","IMPRINT",FACE,{"disambiguationData":[TD([[makeQuery(id+"F2.imprint","IMPRINT",EDGE,{"derivedFrom":sQuery(id+"F2.wireOp",EDGE,"E25.0.6.72")}),1.0]])]});
            var Q463;
            Q463=makeQuery(id+"F2.imprint","IMPRINT",FACE,{"disambiguationData":[TD([[makeQuery(id+"F2.imprint","IMPRINT",EDGE,{"derivedFrom":sQuery(id+"F2.wireOp",EDGE,"E25.0.6.28")}),-1.0]])]});
            var Q464;
            Q464=makeQuery(id+"F2.imprint","IMPRINT",FACE,{"disambiguationData":[TD([[makeQuery(id+"F2.imprint","IMPRINT",EDGE,{"derivedFrom":sQuery(id+"F2.wireOp",EDGE,"E25.0.6.25")}),-1.0]])]});
            var Q465;
            Q465=makeQuery(id+"F2.imprint","IMPRINT",FACE,{"disambiguationData":[TD([[makeQuery(id+"F2.imprint","IMPRINT",EDGE,{"derivedFrom":sQuery(id+"F2.wireOp",EDGE,"E25.0.2.29")}),-1.0]])]});
            var Q466;
            Q466=makeQuery(id+"F2.imprint","IMPRINT",FACE,{"disambiguationData":[TD([[makeQuery(id+"F2.imprint","IMPRINT",EDGE,{"derivedFrom":sQuery(id+"F2.wireOp",EDGE,"E25.0.3.136")}),1.0]])]});
            var Q467;
            Q467=makeQuery(id+"F2.imprint","IMPRINT",FACE,{"disambiguationData":[TD([[makeQuery(id+"F2.imprint","IMPRINT",EDGE,{"derivedFrom":sQuery(id+"F2.wireOp",EDGE,"E25.0.3.25")}),-1.0]])]});
            var Q468;
            Q468=makeQuery(id+"F2.imprint","IMPRINT",FACE,{"disambiguationData":[TD([[makeQuery(id+"F2.imprint","IMPRINT",EDGE,{"derivedFrom":sQuery(id+"F2.wireOp",EDGE,"E25.0.3.29")}),-1.0]])]});
            var Q469;
            Q469=makeQuery(id+"F2.imprint","IMPRINT",FACE,{"disambiguationData":[TD([[makeQuery(id+"F2.imprint","IMPRINT",EDGE,{"derivedFrom":sQuery(id+"F2.wireOp",EDGE,"E25.0.3.82")}),-1.0]])]});
            var Q470;
            Q470=makeQuery(id+"F2.imprint","IMPRINT",FACE,{"disambiguationData":[TD([[makeQuery(id+"F2.imprint","IMPRINT",EDGE,{"derivedFrom":sQuery(id+"F2.wireOp",EDGE,"E25.0.4.136")}),1.0]])]});
            var Q471;
            Q471=makeQuery(id+"F2.imprint","IMPRINT",FACE,{"disambiguationData":[TD([[makeQuery(id+"F2.imprint","IMPRINT",EDGE,{"derivedFrom":sQuery(id+"F2.wireOp",EDGE,"E25.0.4.25")}),-1.0]])]});
            var Q472;
            Q472=makeQuery(id+"F2.imprint","IMPRINT",FACE,{"disambiguationData":[TD([[makeQuery(id+"F2.imprint","IMPRINT",EDGE,{"derivedFrom":sQuery(id+"F2.wireOp",EDGE,"E25.0.5.136")}),1.0]])]});
            var Q473;
            Q473=makeQuery(id+"F2.imprint","IMPRINT",FACE,{"disambiguationData":[TD([[makeQuery(id+"F2.imprint","IMPRINT",EDGE,{"derivedFrom":sQuery(id+"F2.wireOp",EDGE,"E25.0.5.25")}),-1.0]])]});
            var Q474;
            Q474=makeQuery(id+"F2.imprint","IMPRINT",FACE,{"disambiguationData":[TD([[makeQuery(id+"F2.imprint","IMPRINT",EDGE,{"derivedFrom":sQuery(id+"F2.wireOp",EDGE,"E25.0.6.136")}),1.0]])]});
            var Q475;
            Q475=makeQuery(id+"F2.imprint","IMPRINT",FACE,{"disambiguationData":[TD([[makeQuery(id+"F2.imprint","IMPRINT",EDGE,{"derivedFrom":sQuery(id+"F2.wireOp",EDGE,"E25.0.5.29")}),-1.0]])]});
            var Q476;
            Q476=makeQuery(id+"F2.imprint","IMPRINT",FACE,{"disambiguationData":[TD([[makeQuery(id+"F2.imprint","IMPRINT",EDGE,{"derivedFrom":sQuery(id+"F2.wireOp",EDGE,"E25.0.6.82")}),-1.0]])]});
            var Q477;
            Q477=makeQuery(id+"F2.imprint","IMPRINT",FACE,{"disambiguationData":[TD([[makeQuery(id+"F2.imprint","IMPRINT",EDGE,{"derivedFrom":sQuery(id+"F2.wireOp",EDGE,"E25.0.6.29")}),-1.0]])]});
            var Q478;
            Q478=makeQuery(id+"F2.imprint","IMPRINT",FACE,{"disambiguationData":[TD([[makeQuery(id+"F2.imprint","IMPRINT",EDGE,{"derivedFrom":sQuery(id+"F2.wireOp",EDGE,"E25.0.6.27")}),-1.0]])]});
            var Q479;
            Q479=makeQuery(id+"F2.imprint","IMPRINT",FACE,{"disambiguationData":[TD([[makeQuery(id+"F2.imprint","IMPRINT",EDGE,{"derivedFrom":sQuery(id+"F2.wireOp",EDGE,"E25.0.6.26")}),1.0]])]});
            var Q480;
            Q480=makeQuery(id+"F2.imprint","IMPRINT",FACE,{"disambiguationData":[TD([[makeQuery(id+"F2.imprint","IMPRINT",EDGE,{"derivedFrom":sQuery(id+"F2.wireOp",EDGE,"E25.0.5.27")}),-1.0]])]});
            var Q481;
            Q481=makeQuery(id+"F2.imprint","IMPRINT",FACE,{"disambiguationData":[TD([[makeQuery(id+"F2.imprint","IMPRINT",EDGE,{"derivedFrom":sQuery(id+"F2.wireOp",EDGE,"E25.0.5.82")}),-1.0]])]});
            var Q482;
            Q482=makeQuery(id+"F2.imprint","IMPRINT",FACE,{"disambiguationData":[TD([[makeQuery(id+"F2.imprint","IMPRINT",EDGE,{"derivedFrom":sQuery(id+"F2.wireOp",EDGE,"E25.0.4.29")}),-1.0]])]});
            var Q483;
            Q483=makeQuery(id+"F2.imprint","IMPRINT",FACE,{"disambiguationData":[TD([[makeQuery(id+"F2.imprint","IMPRINT",EDGE,{"derivedFrom":sQuery(id+"F2.wireOp",EDGE,"E25.0.4.82")}),-1.0]])]});
            var Q484;
            Q484=makeQuery(id+"F2.imprint","IMPRINT",FACE,{"disambiguationData":[TD([[makeQuery(id+"F2.imprint","IMPRINT",EDGE,{"derivedFrom":sQuery(id+"F2.wireOp",EDGE,"E25.0.3.27")}),-1.0]])]});
            var Q485;
            Q485=makeQuery(id+"F2.imprint","IMPRINT",FACE,{"disambiguationData":[TD([[makeQuery(id+"F2.imprint","IMPRINT",EDGE,{"derivedFrom":sQuery(id+"F2.wireOp",EDGE,"E25.0.3.26")}),1.0]])]});
            var Q486;
            Q486=makeQuery(id+"F2.imprint","IMPRINT",FACE,{"disambiguationData":[TD([[makeQuery(id+"F2.imprint","IMPRINT",EDGE,{"derivedFrom":sQuery(id+"F2.wireOp",EDGE,"E25.0.2.27")}),-1.0]])]});
            var Q487;
            Q487=makeQuery(id+"F2.imprint","IMPRINT",FACE,{"disambiguationData":[TD([[makeQuery(id+"F2.imprint","IMPRINT",EDGE,{"derivedFrom":sQuery(id+"F2.wireOp",EDGE,"E25.0.2.34")}),-1.0]])]});
            var Q488;
            Q488=makeQuery(id+"F2.imprint","IMPRINT",FACE,{"disambiguationData":[TD([[makeQuery(id+"F2.imprint","IMPRINT",EDGE,{"derivedFrom":sQuery(id+"F2.wireOp",EDGE,"E25.0.2.58")}),-1.0]])]});
            var Q489;
            Q489=makeQuery(id+"F2.imprint","IMPRINT",FACE,{"disambiguationData":[TD([[makeQuery(id+"F2.imprint","IMPRINT",EDGE,{"derivedFrom":sQuery(id+"F2.wireOp",EDGE,"E25.0.2.74")}),-1.0]])]});
            var Q490;
            Q490=makeQuery(id+"F2.imprint","IMPRINT",FACE,{"disambiguationData":[TD([[makeQuery(id+"F2.imprint","IMPRINT",EDGE,{"derivedFrom":sQuery(id+"F2.wireOp",EDGE,"E25.0.2.94")}),-1.0]])]});
            var Q491;
            Q491=makeQuery(id+"F2.imprint","IMPRINT",FACE,{"disambiguationData":[TD([[makeQuery(id+"F2.imprint","IMPRINT",EDGE,{"derivedFrom":sQuery(id+"F2.wireOp",EDGE,"E25.0.2.0")}),-1.0]])]});
            var Q492;
            Q492=makeQuery(id+"F2.imprint","IMPRINT",FACE,{"disambiguationData":[TD([[makeQuery(id+"F2.imprint","IMPRINT",EDGE,{"derivedFrom":sQuery(id+"F2.wireOp",EDGE,"E25.0.2.39")}),-1.0]])]});
            var Q493;
            Q493=makeQuery(id+"F2.imprint","IMPRINT",FACE,{"disambiguationData":[TD([[makeQuery(id+"F2.imprint","IMPRINT",EDGE,{"derivedFrom":sQuery(id+"F2.wireOp",EDGE,"E25.0.2.16")}),-1.0]])]});
            var Q494;
            Q494=makeQuery(id+"F2.imprint","IMPRINT",FACE,{"disambiguationData":[TD([[makeQuery(id+"F2.imprint","IMPRINT",EDGE,{"derivedFrom":sQuery(id+"F2.wireOp",EDGE,"E25.0.2.24")}),-1.0]])]});
            var Q495;
            Q495=makeQuery(id+"F2.imprint","IMPRINT",FACE,{"disambiguationData":[TD([[makeQuery(id+"F2.imprint","IMPRINT",EDGE,{"derivedFrom":sQuery(id+"F2.wireOp",EDGE,"E25.0.2.45")}),-1.0]])]});
            var Q496;
            Q496=makeQuery(id+"F2.imprint","IMPRINT",FACE,{"disambiguationData":[TD([[makeQuery(id+"F2.imprint","IMPRINT",EDGE,{"derivedFrom":sQuery(id+"F2.wireOp",EDGE,"E25.0.2.56")}),-1.0]])]});
            var Q497;
            Q497=makeQuery(id+"F2.imprint","IMPRINT",FACE,{"disambiguationData":[TD([[makeQuery(id+"F2.imprint","IMPRINT",EDGE,{"derivedFrom":sQuery(id+"F2.wireOp",EDGE,"E25.0.2.63")}),-1.0]])]});
            var Q498;
            Q498=makeQuery(id+"F2.imprint","IMPRINT",FACE,{"disambiguationData":[TD([[makeQuery(id+"F2.imprint","IMPRINT",EDGE,{"derivedFrom":sQuery(id+"F2.wireOp",EDGE,"E25.0.3.146")}),1.0]])]});
            var Q499;
            Q499=makeQuery(id+"F2.imprint","IMPRINT",FACE,{"disambiguationData":[TD([[makeQuery(id+"F2.imprint","IMPRINT",EDGE,{"derivedFrom":sQuery(id+"F2.wireOp",EDGE,"E25.0.3.56")}),-1.0]])]});
            var Q500;
            Q500=makeQuery(id+"F2.imprint","IMPRINT",FACE,{"disambiguationData":[TD([[makeQuery(id+"F2.imprint","IMPRINT",EDGE,{"derivedFrom":sQuery(id+"F2.wireOp",EDGE,"E25.0.3.76")}),1.0]])]});
            var Q501;
            Q501=makeQuery(id+"F2.imprint","IMPRINT",FACE,{"disambiguationData":[TD([[makeQuery(id+"F2.imprint","IMPRINT",EDGE,{"derivedFrom":sQuery(id+"F2.wireOp",EDGE,"E25.0.3.45")}),-1.0]])]});
            var Q502;
            Q502=makeQuery(id+"F2.imprint","IMPRINT",FACE,{"disambiguationData":[TD([[makeQuery(id+"F2.imprint","IMPRINT",EDGE,{"derivedFrom":sQuery(id+"F2.wireOp",EDGE,"E25.0.3.176")}),-1.0]])]});
            var Q503;
            Q503=makeQuery(id+"F2.imprint","IMPRINT",FACE,{"disambiguationData":[TD([[makeQuery(id+"F2.imprint","IMPRINT",EDGE,{"derivedFrom":sQuery(id+"F2.wireOp",EDGE,"E25.0.3.24")}),-1.0]])]});
            var Q504;
            Q504=makeQuery(id+"F2.imprint","IMPRINT",FACE,{"disambiguationData":[TD([[makeQuery(id+"F2.imprint","IMPRINT",EDGE,{"derivedFrom":sQuery(id+"F2.wireOp",EDGE,"E25.0.3.18")}),1.0]])]});
            var Q505;
            Q505=makeQuery(id+"F2.imprint","IMPRINT",FACE,{"disambiguationData":[TD([[makeQuery(id+"F2.imprint","IMPRINT",EDGE,{"derivedFrom":sQuery(id+"F2.wireOp",EDGE,"E25.0.3.16")}),-1.0]])]});
            var Q506;
            Q506=makeQuery(id+"F2.imprint","IMPRINT",FACE,{"disambiguationData":[TD([[makeQuery(id+"F2.imprint","IMPRINT",EDGE,{"derivedFrom":sQuery(id+"F2.wireOp",EDGE,"E25.0.3.36")}),1.0]])]});
            var Q507;
            Q507=makeQuery(id+"F2.imprint","IMPRINT",FACE,{"disambiguationData":[TD([[makeQuery(id+"F2.imprint","IMPRINT",EDGE,{"derivedFrom":sQuery(id+"F2.wireOp",EDGE,"E25.0.3.39")}),-1.0]])]});
            var Q508;
            Q508=makeQuery(id+"F2.imprint","IMPRINT",FACE,{"disambiguationData":[TD([[makeQuery(id+"F2.imprint","IMPRINT",EDGE,{"derivedFrom":sQuery(id+"F2.wireOp",EDGE,"E25.0.3.48")}),-1.0]])]});
            var Q509;
            Q509=makeQuery(id+"F2.imprint","IMPRINT",FACE,{"disambiguationData":[TD([[makeQuery(id+"F2.imprint","IMPRINT",EDGE,{"derivedFrom":sQuery(id+"F2.wireOp",EDGE,"E25.0.3.0")}),-1.0]])]});
            var Q510;
            Q510=makeQuery(id+"F2.imprint","IMPRINT",FACE,{"disambiguationData":[TD([[makeQuery(id+"F2.imprint","IMPRINT",EDGE,{"derivedFrom":sQuery(id+"F2.wireOp",EDGE,"E25.0.3.21")}),1.0]])]});
            var Q511;
            Q511=makeQuery(id+"F2.imprint","IMPRINT",FACE,{"disambiguationData":[TD([[makeQuery(id+"F2.imprint","IMPRINT",EDGE,{"derivedFrom":sQuery(id+"F2.wireOp",EDGE,"E25.0.3.94")}),-1.0]])]});
            var Q512;
            Q512=makeQuery(id+"F2.imprint","IMPRINT",FACE,{"disambiguationData":[TD([[makeQuery(id+"F2.imprint","IMPRINT",EDGE,{"derivedFrom":sQuery(id+"F2.wireOp",EDGE,"E25.0.3.64")}),1.0]])]});
            var Q513;
            Q513=makeQuery(id+"F2.imprint","IMPRINT",FACE,{"disambiguationData":[TD([[makeQuery(id+"F2.imprint","IMPRINT",EDGE,{"derivedFrom":sQuery(id+"F2.wireOp",EDGE,"E25.0.3.74")}),-1.0]])]});
            var Q514;
            Q514=makeQuery(id+"F2.imprint","IMPRINT",FACE,{"disambiguationData":[TD([[makeQuery(id+"F2.imprint","IMPRINT",EDGE,{"derivedFrom":sQuery(id+"F2.wireOp",EDGE,"E25.0.3.213")}),-1.0]])]});
            var Q515;
            Q515=makeQuery(id+"F2.imprint","IMPRINT",FACE,{"disambiguationData":[TD([[makeQuery(id+"F2.imprint","IMPRINT",EDGE,{"derivedFrom":sQuery(id+"F2.wireOp",EDGE,"E25.0.3.58")}),-1.0]])]});
            var Q516;
            Q516=makeQuery(id+"F2.imprint","IMPRINT",FACE,{"disambiguationData":[TD([[makeQuery(id+"F2.imprint","IMPRINT",EDGE,{"derivedFrom":sQuery(id+"F2.wireOp",EDGE,"E25.0.3.54")}),1.0]])]});
            var Q517;
            Q517=makeQuery(id+"F2.imprint","IMPRINT",FACE,{"disambiguationData":[TD([[makeQuery(id+"F2.imprint","IMPRINT",EDGE,{"derivedFrom":sQuery(id+"F2.wireOp",EDGE,"E25.0.3.34")}),-1.0]])]});
            var Q518;
            Q518=makeQuery(id+"F2.imprint","IMPRINT",FACE,{"disambiguationData":[TD([[makeQuery(id+"F2.imprint","IMPRINT",EDGE,{"derivedFrom":sQuery(id+"F2.wireOp",EDGE,"E25.0.4.26")}),1.0]])]});
            var Q519;
            Q519=makeQuery(id+"F2.imprint","IMPRINT",FACE,{"disambiguationData":[TD([[makeQuery(id+"F2.imprint","IMPRINT",EDGE,{"derivedFrom":sQuery(id+"F2.wireOp",EDGE,"E25.0.4.27")}),-1.0]])]});
            var Q520;
            Q520=makeQuery(id+"F2.imprint","IMPRINT",FACE,{"disambiguationData":[TD([[makeQuery(id+"F2.imprint","IMPRINT",EDGE,{"derivedFrom":sQuery(id+"F2.wireOp",EDGE,"E25.0.5.26")}),1.0]])]});
            var Q521;
            Q521=makeQuery(id+"F2.imprint","IMPRINT",FACE,{"disambiguationData":[TD([[makeQuery(id+"F2.imprint","IMPRINT",EDGE,{"derivedFrom":sQuery(id+"F2.wireOp",EDGE,"E25.0.4.34")}),-1.0]])]});
            var Q522;
            Q522=makeQuery(id+"F2.imprint","IMPRINT",FACE,{"disambiguationData":[TD([[makeQuery(id+"F2.imprint","IMPRINT",EDGE,{"derivedFrom":sQuery(id+"F2.wireOp",EDGE,"E25.0.4.54")}),1.0]])]});
            var Q523;
            Q523=makeQuery(id+"F2.imprint","IMPRINT",FACE,{"disambiguationData":[TD([[makeQuery(id+"F2.imprint","IMPRINT",EDGE,{"derivedFrom":sQuery(id+"F2.wireOp",EDGE,"E25.0.4.58")}),-1.0]])]});
            var Q524;
            Q524=makeQuery(id+"F2.imprint","IMPRINT",FACE,{"disambiguationData":[TD([[makeQuery(id+"F2.imprint","IMPRINT",EDGE,{"derivedFrom":sQuery(id+"F2.wireOp",EDGE,"E25.0.3.63")}),-1.0]])]});
            var Q525;
            Q525=makeQuery(id+"F2.imprint","IMPRINT",FACE,{"disambiguationData":[TD([[makeQuery(id+"F2.imprint","IMPRINT",EDGE,{"derivedFrom":sQuery(id+"F2.wireOp",EDGE,"E25.0.4.146")}),1.0]])]});
            var Q526;
            Q526=makeQuery(id+"F2.imprint","IMPRINT",FACE,{"disambiguationData":[TD([[makeQuery(id+"F2.imprint","IMPRINT",EDGE,{"derivedFrom":sQuery(id+"F2.wireOp",EDGE,"E25.0.4.63")}),-1.0]])]});
            var Q527;
            Q527=makeQuery(id+"F2.imprint","IMPRINT",FACE,{"disambiguationData":[TD([[makeQuery(id+"F2.imprint","IMPRINT",EDGE,{"derivedFrom":sQuery(id+"F2.wireOp",EDGE,"E25.0.4.56")}),-1.0]])]});
            var Q528;
            Q528=makeQuery(id+"F2.imprint","IMPRINT",FACE,{"disambiguationData":[TD([[makeQuery(id+"F2.imprint","IMPRINT",EDGE,{"derivedFrom":sQuery(id+"F2.wireOp",EDGE,"E25.0.4.76")}),1.0]])]});
            var Q529;
            Q529=makeQuery(id+"F2.imprint","IMPRINT",FACE,{"disambiguationData":[TD([[makeQuery(id+"F2.imprint","IMPRINT",EDGE,{"derivedFrom":sQuery(id+"F2.wireOp",EDGE,"E25.0.4.45")}),-1.0]])]});
            var Q530;
            Q530=makeQuery(id+"F2.imprint","IMPRINT",FACE,{"disambiguationData":[TD([[makeQuery(id+"F2.imprint","IMPRINT",EDGE,{"derivedFrom":sQuery(id+"F2.wireOp",EDGE,"E25.0.4.176")}),-1.0]])]});
            var Q531;
            Q531=makeQuery(id+"F2.imprint","IMPRINT",FACE,{"disambiguationData":[TD([[makeQuery(id+"F2.imprint","IMPRINT",EDGE,{"derivedFrom":sQuery(id+"F2.wireOp",EDGE,"E25.0.4.24")}),-1.0]])]});
            var Q532;
            Q532=makeQuery(id+"F2.imprint","IMPRINT",FACE,{"disambiguationData":[TD([[makeQuery(id+"F2.imprint","IMPRINT",EDGE,{"derivedFrom":sQuery(id+"F2.wireOp",EDGE,"E25.0.4.18")}),1.0]])]});
            var Q533;
            Q533=makeQuery(id+"F2.imprint","IMPRINT",FACE,{"disambiguationData":[TD([[makeQuery(id+"F2.imprint","IMPRINT",EDGE,{"derivedFrom":sQuery(id+"F2.wireOp",EDGE,"E25.0.4.16")}),-1.0]])]});
            var Q534;
            Q534=makeQuery(id+"F2.imprint","IMPRINT",FACE,{"disambiguationData":[TD([[makeQuery(id+"F2.imprint","IMPRINT",EDGE,{"derivedFrom":sQuery(id+"F2.wireOp",EDGE,"E25.0.4.36")}),1.0]])]});
            var Q535;
            Q535=makeQuery(id+"F2.imprint","IMPRINT",FACE,{"disambiguationData":[TD([[makeQuery(id+"F2.imprint","IMPRINT",EDGE,{"derivedFrom":sQuery(id+"F2.wireOp",EDGE,"E25.0.4.39")}),-1.0]])]});
            var Q536;
            Q536=makeQuery(id+"F2.imprint","IMPRINT",FACE,{"disambiguationData":[TD([[makeQuery(id+"F2.imprint","IMPRINT",EDGE,{"derivedFrom":sQuery(id+"F2.wireOp",EDGE,"E25.0.4.48")}),-1.0]])]});
            var Q537;
            Q537=makeQuery(id+"F2.imprint","IMPRINT",FACE,{"disambiguationData":[TD([[makeQuery(id+"F2.imprint","IMPRINT",EDGE,{"derivedFrom":sQuery(id+"F2.wireOp",EDGE,"E25.0.4.0")}),-1.0]])]});
            var Q538;
            Q538=makeQuery(id+"F2.imprint","IMPRINT",FACE,{"disambiguationData":[TD([[makeQuery(id+"F2.imprint","IMPRINT",EDGE,{"derivedFrom":sQuery(id+"F2.wireOp",EDGE,"E25.0.4.21")}),1.0]])]});
            var Q539;
            Q539=makeQuery(id+"F2.imprint","IMPRINT",FACE,{"disambiguationData":[TD([[makeQuery(id+"F2.imprint","IMPRINT",EDGE,{"derivedFrom":sQuery(id+"F2.wireOp",EDGE,"E25.0.4.94")}),-1.0]])]});
            var Q540;
            Q540=makeQuery(id+"F2.imprint","IMPRINT",FACE,{"disambiguationData":[TD([[makeQuery(id+"F2.imprint","IMPRINT",EDGE,{"derivedFrom":sQuery(id+"F2.wireOp",EDGE,"E25.0.4.64")}),1.0]])]});
            var Q541;
            Q541=makeQuery(id+"F2.imprint","IMPRINT",FACE,{"disambiguationData":[TD([[makeQuery(id+"F2.imprint","IMPRINT",EDGE,{"derivedFrom":sQuery(id+"F2.wireOp",EDGE,"E25.0.4.74")}),-1.0]])]});
            var Q542;
            Q542=makeQuery(id+"F2.imprint","IMPRINT",FACE,{"disambiguationData":[TD([[makeQuery(id+"F2.imprint","IMPRINT",EDGE,{"derivedFrom":sQuery(id+"F2.wireOp",EDGE,"E25.0.4.213")}),-1.0]])]});
            var Q543;
            Q543=makeQuery(id+"F2.imprint","IMPRINT",FACE,{"disambiguationData":[TD([[makeQuery(id+"F2.imprint","IMPRINT",EDGE,{"derivedFrom":sQuery(id+"F2.wireOp",EDGE,"E25.0.5.146")}),1.0]])]});
            var Q544;
            Q544=makeQuery(id+"F2.imprint","IMPRINT",FACE,{"disambiguationData":[TD([[makeQuery(id+"F2.imprint","IMPRINT",EDGE,{"derivedFrom":sQuery(id+"F2.wireOp",EDGE,"E25.0.5.63")}),-1.0]])]});
            var Q545;
            Q545=makeQuery(id+"F2.imprint","IMPRINT",FACE,{"disambiguationData":[TD([[makeQuery(id+"F2.imprint","IMPRINT",EDGE,{"derivedFrom":sQuery(id+"F2.wireOp",EDGE,"E25.0.5.56")}),-1.0]])]});
            var Q546;
            Q546=makeQuery(id+"F2.imprint","IMPRINT",FACE,{"disambiguationData":[TD([[makeQuery(id+"F2.imprint","IMPRINT",EDGE,{"derivedFrom":sQuery(id+"F2.wireOp",EDGE,"E25.0.5.76")}),1.0]])]});
            var Q547;
            Q547=makeQuery(id+"F2.imprint","IMPRINT",FACE,{"disambiguationData":[TD([[makeQuery(id+"F2.imprint","IMPRINT",EDGE,{"derivedFrom":sQuery(id+"F2.wireOp",EDGE,"E25.0.5.45")}),-1.0]])]});
            var Q548;
            Q548=makeQuery(id+"F2.imprint","IMPRINT",FACE,{"disambiguationData":[TD([[makeQuery(id+"F2.imprint","IMPRINT",EDGE,{"derivedFrom":sQuery(id+"F2.wireOp",EDGE,"E25.0.5.176")}),-1.0]])]});
            var Q549;
            Q549=makeQuery(id+"F2.imprint","IMPRINT",FACE,{"disambiguationData":[TD([[makeQuery(id+"F2.imprint","IMPRINT",EDGE,{"derivedFrom":sQuery(id+"F2.wireOp",EDGE,"E25.0.5.24")}),-1.0]])]});
            var Q550;
            Q550=makeQuery(id+"F2.imprint","IMPRINT",FACE,{"disambiguationData":[TD([[makeQuery(id+"F2.imprint","IMPRINT",EDGE,{"derivedFrom":sQuery(id+"F2.wireOp",EDGE,"E25.0.5.18")}),1.0]])]});
            var Q551;
            Q551=makeQuery(id+"F2.imprint","IMPRINT",FACE,{"disambiguationData":[TD([[makeQuery(id+"F2.imprint","IMPRINT",EDGE,{"derivedFrom":sQuery(id+"F2.wireOp",EDGE,"E25.0.5.16")}),-1.0]])]});
            var Q552;
            Q552=makeQuery(id+"F2.imprint","IMPRINT",FACE,{"disambiguationData":[TD([[makeQuery(id+"F2.imprint","IMPRINT",EDGE,{"derivedFrom":sQuery(id+"F2.wireOp",EDGE,"E25.0.5.36")}),1.0]])]});
            var Q553;
            Q553=makeQuery(id+"F2.imprint","IMPRINT",FACE,{"disambiguationData":[TD([[makeQuery(id+"F2.imprint","IMPRINT",EDGE,{"derivedFrom":sQuery(id+"F2.wireOp",EDGE,"E25.0.5.39")}),-1.0]])]});
            var Q554;
            Q554=makeQuery(id+"F2.imprint","IMPRINT",FACE,{"disambiguationData":[TD([[makeQuery(id+"F2.imprint","IMPRINT",EDGE,{"derivedFrom":sQuery(id+"F2.wireOp",EDGE,"E25.0.5.48")}),-1.0]])]});
            var Q555;
            Q555=makeQuery(id+"F2.imprint","IMPRINT",FACE,{"disambiguationData":[TD([[makeQuery(id+"F2.imprint","IMPRINT",EDGE,{"derivedFrom":sQuery(id+"F2.wireOp",EDGE,"E25.0.5.0")}),-1.0]])]});
            var Q556;
            Q556=makeQuery(id+"F2.imprint","IMPRINT",FACE,{"disambiguationData":[TD([[makeQuery(id+"F2.imprint","IMPRINT",EDGE,{"derivedFrom":sQuery(id+"F2.wireOp",EDGE,"E25.0.5.21")}),1.0]])]});
            var Q557;
            Q557=makeQuery(id+"F2.imprint","IMPRINT",FACE,{"disambiguationData":[TD([[makeQuery(id+"F2.imprint","IMPRINT",EDGE,{"derivedFrom":sQuery(id+"F2.wireOp",EDGE,"E25.0.5.94")}),-1.0]])]});
            var Q558;
            Q558=makeQuery(id+"F2.imprint","IMPRINT",FACE,{"disambiguationData":[TD([[makeQuery(id+"F2.imprint","IMPRINT",EDGE,{"derivedFrom":sQuery(id+"F2.wireOp",EDGE,"E25.0.5.64")}),1.0]])]});
            var Q559;
            Q559=makeQuery(id+"F2.imprint","IMPRINT",FACE,{"disambiguationData":[TD([[makeQuery(id+"F2.imprint","IMPRINT",EDGE,{"derivedFrom":sQuery(id+"F2.wireOp",EDGE,"E25.0.5.74")}),-1.0]])]});
            var Q560;
            Q560=makeQuery(id+"F2.imprint","IMPRINT",FACE,{"disambiguationData":[TD([[makeQuery(id+"F2.imprint","IMPRINT",EDGE,{"derivedFrom":sQuery(id+"F2.wireOp",EDGE,"E25.0.5.213")}),-1.0]])]});
            var Q561;
            Q561=makeQuery(id+"F2.imprint","IMPRINT",FACE,{"disambiguationData":[TD([[makeQuery(id+"F2.imprint","IMPRINT",EDGE,{"derivedFrom":sQuery(id+"F2.wireOp",EDGE,"E25.0.5.54")}),1.0]])]});
            var Q562;
            Q562=makeQuery(id+"F2.imprint","IMPRINT",FACE,{"disambiguationData":[TD([[makeQuery(id+"F2.imprint","IMPRINT",EDGE,{"derivedFrom":sQuery(id+"F2.wireOp",EDGE,"E25.0.5.58")}),-1.0]])]});
            var Q563;
            Q563=makeQuery(id+"F2.imprint","IMPRINT",FACE,{"disambiguationData":[TD([[makeQuery(id+"F2.imprint","IMPRINT",EDGE,{"derivedFrom":sQuery(id+"F2.wireOp",EDGE,"E25.0.5.34")}),-1.0]])]});
            var Q564;
            Q564=makeQuery(id+"F2.imprint","IMPRINT",FACE,{"disambiguationData":[TD([[makeQuery(id+"F2.imprint","IMPRINT",EDGE,{"derivedFrom":sQuery(id+"F2.wireOp",EDGE,"E25.0.6.54")}),1.0]])]});
            var Q565;
            Q565=makeQuery(id+"F2.imprint","IMPRINT",FACE,{"disambiguationData":[TD([[makeQuery(id+"F2.imprint","IMPRINT",EDGE,{"derivedFrom":sQuery(id+"F2.wireOp",EDGE,"E25.0.6.34")}),-1.0]])]});
            var Q566;
            Q566=makeQuery(id+"F2.imprint","IMPRINT",FACE,{"disambiguationData":[TD([[makeQuery(id+"F2.imprint","IMPRINT",EDGE,{"derivedFrom":sQuery(id+"F2.wireOp",EDGE,"E25.0.6.149")}),-1.0]])]});
            var Q567;
            Q567=makeQuery(id+"F2.imprint","IMPRINT",FACE,{"disambiguationData":[TD([[makeQuery(id+"F2.imprint","IMPRINT",EDGE,{"derivedFrom":sQuery(id+"F2.wireOp",EDGE,"E25.0.6.63")}),-1.0]])]});
            var Q568;
            Q568=makeQuery(id+"F2.imprint","IMPRINT",FACE,{"disambiguationData":[TD([[makeQuery(id+"F2.imprint","IMPRINT",EDGE,{"derivedFrom":sQuery(id+"F2.wireOp",EDGE,"E25.0.6.146")}),1.0]])]});
            var Q569;
            Q569=makeQuery(id+"F2.imprint","IMPRINT",FACE,{"disambiguationData":[TD([[makeQuery(id+"F2.imprint","IMPRINT",EDGE,{"derivedFrom":sQuery(id+"F2.wireOp",EDGE,"E25.0.6.56")}),-1.0]])]});
            var Q570;
            Q570=makeQuery(id+"F2.imprint","IMPRINT",FACE,{"disambiguationData":[TD([[makeQuery(id+"F2.imprint","IMPRINT",EDGE,{"derivedFrom":sQuery(id+"F2.wireOp",EDGE,"E25.0.6.76")}),1.0]])]});
            var Q571;
            Q571=makeQuery(id+"F2.imprint","IMPRINT",FACE,{"disambiguationData":[TD([[makeQuery(id+"F2.imprint","IMPRINT",EDGE,{"derivedFrom":sQuery(id+"F2.wireOp",EDGE,"E25.0.6.45")}),-1.0]])]});
            var Q572;
            Q572=makeQuery(id+"F2.imprint","IMPRINT",FACE,{"disambiguationData":[TD([[makeQuery(id+"F2.imprint","IMPRINT",EDGE,{"derivedFrom":sQuery(id+"F2.wireOp",EDGE,"E25.0.6.176")}),-1.0]])]});
            var Q573;
            Q573=makeQuery(id+"F2.imprint","IMPRINT",FACE,{"disambiguationData":[TD([[makeQuery(id+"F2.imprint","IMPRINT",EDGE,{"derivedFrom":sQuery(id+"F2.wireOp",EDGE,"E25.0.6.24")}),-1.0]])]});
            var Q574;
            Q574=makeQuery(id+"F2.imprint","IMPRINT",FACE,{"disambiguationData":[TD([[makeQuery(id+"F2.imprint","IMPRINT",EDGE,{"derivedFrom":sQuery(id+"F2.wireOp",EDGE,"E25.0.6.18")}),1.0]])]});
            var Q575;
            Q575=makeQuery(id+"F2.imprint","IMPRINT",FACE,{"disambiguationData":[TD([[makeQuery(id+"F2.imprint","IMPRINT",EDGE,{"derivedFrom":sQuery(id+"F2.wireOp",EDGE,"E25.0.6.16")}),-1.0]])]});
            var Q576;
            Q576=makeQuery(id+"F2.imprint","IMPRINT",FACE,{"disambiguationData":[TD([[makeQuery(id+"F2.imprint","IMPRINT",EDGE,{"derivedFrom":sQuery(id+"F2.wireOp",EDGE,"E25.0.6.36")}),1.0]])]});
            var Q577;
            Q577=makeQuery(id+"F2.imprint","IMPRINT",FACE,{"disambiguationData":[TD([[makeQuery(id+"F2.imprint","IMPRINT",EDGE,{"derivedFrom":sQuery(id+"F2.wireOp",EDGE,"E25.0.6.39")}),-1.0]])]});
            var Q578;
            Q578=makeQuery(id+"F2.imprint","IMPRINT",FACE,{"disambiguationData":[TD([[makeQuery(id+"F2.imprint","IMPRINT",EDGE,{"derivedFrom":sQuery(id+"F2.wireOp",EDGE,"E25.0.6.48")}),-1.0]])]});
            var Q579;
            Q579=makeQuery(id+"F2.imprint","IMPRINT",FACE,{"disambiguationData":[TD([[makeQuery(id+"F2.imprint","IMPRINT",EDGE,{"derivedFrom":sQuery(id+"F2.wireOp",EDGE,"E25.0.6.0")}),-1.0]])]});
            var Q580;
            Q580=makeQuery(id+"F2.imprint","IMPRINT",FACE,{"disambiguationData":[TD([[makeQuery(id+"F2.imprint","IMPRINT",EDGE,{"derivedFrom":sQuery(id+"F2.wireOp",EDGE,"E25.0.6.21")}),1.0]])]});
            var Q581;
            Q581=makeQuery(id+"F2.imprint","IMPRINT",FACE,{"disambiguationData":[TD([[makeQuery(id+"F2.imprint","IMPRINT",EDGE,{"derivedFrom":sQuery(id+"F2.wireOp",EDGE,"E25.0.6.94")}),-1.0]])]});
            var Q582;
            Q582=makeQuery(id+"F2.imprint","IMPRINT",FACE,{"disambiguationData":[TD([[makeQuery(id+"F2.imprint","IMPRINT",EDGE,{"derivedFrom":sQuery(id+"F2.wireOp",EDGE,"E25.0.6.64")}),1.0]])]});
            var Q583;
            Q583=makeQuery(id+"F2.imprint","IMPRINT",FACE,{"disambiguationData":[TD([[makeQuery(id+"F2.imprint","IMPRINT",EDGE,{"derivedFrom":sQuery(id+"F2.wireOp",EDGE,"E25.0.6.74")}),-1.0]])]});
            var Q584;
            Q584=makeQuery(id+"F2.imprint","IMPRINT",FACE,{"disambiguationData":[TD([[makeQuery(id+"F2.imprint","IMPRINT",EDGE,{"derivedFrom":sQuery(id+"F2.wireOp",EDGE,"E25.0.6.213")}),-1.0]])]});
            var Q585;
            Q585=makeQuery(id+"F2.imprint","IMPRINT",FACE,{"disambiguationData":[TD([[makeQuery(id+"F2.imprint","IMPRINT",EDGE,{"derivedFrom":sQuery(id+"F2.wireOp",EDGE,"E25.0.6.58")}),-1.0]])]});
            var Q586;
            Q586=makeQuery(id+"F2.imprint","IMPRINT",FACE,{"disambiguationData":[TD([[makeQuery(id+"F2.imprint","IMPRINT",EDGE,{"derivedFrom":sQuery(id+"F2.wireOp",EDGE,"E25.0.7.146")}),1.0]])]});
            var Q587;
            Q587=makeQuery(id+"F2.imprint","IMPRINT",FACE,{"disambiguationData":[TD([[makeQuery(id+"F2.imprint","IMPRINT",EDGE,{"derivedFrom":sQuery(id+"F2.wireOp",EDGE,"E25.0.7.63")}),-1.0]])]});
            var Q588;
            Q588=makeQuery(id+"F2.imprint","IMPRINT",FACE,{"disambiguationData":[TD([[makeQuery(id+"F2.imprint","IMPRINT",EDGE,{"derivedFrom":sQuery(id+"F2.wireOp",EDGE,"E25.0.8.146")}),1.0]])]});
            var Q589;
            Q589=makeQuery(id+"F2.imprint","IMPRINT",FACE,{"disambiguationData":[TD([[makeQuery(id+"F2.imprint","IMPRINT",EDGE,{"derivedFrom":sQuery(id+"F2.wireOp",EDGE,"E25.0.8.63")}),-1.0]])]});
            var Q590;
            Q590=makeQuery(id+"F2.imprint","IMPRINT",FACE,{"disambiguationData":[TD([[makeQuery(id+"F2.imprint","IMPRINT",EDGE,{"derivedFrom":sQuery(id+"F2.wireOp",EDGE,"E26.0.1.60")}),1.0]])]});
            var Q591;
            Q591=makeQuery(id+"F2.imprint","IMPRINT",FACE,{"disambiguationData":[TD([[makeQuery(id+"F2.imprint","IMPRINT",EDGE,{"derivedFrom":sQuery(id+"F2.wireOp",EDGE,"E26.0.1.3")}),-1.0]])]});
            var Q592;
            Q592=makeQuery(id+"F2.imprint","IMPRINT",FACE,{"disambiguationData":[TD([[makeQuery(id+"F2.imprint","IMPRINT",EDGE,{"derivedFrom":sQuery(id+"F2.wireOp",EDGE,"E26.0.1.23")}),-1.0]])]});
            var Q593;
            Q593=makeQuery(id+"F2.imprint","IMPRINT",FACE,{"disambiguationData":[TD([[makeQuery(id+"F2.imprint","IMPRINT",EDGE,{"derivedFrom":sQuery(id+"F2.wireOp",EDGE,"E25.0.7.76")}),1.0]])]});
            var Q594;
            Q594=makeQuery(id+"F2.imprint","IMPRINT",FACE,{"disambiguationData":[TD([[makeQuery(id+"F2.imprint","IMPRINT",EDGE,{"derivedFrom":sQuery(id+"F2.wireOp",EDGE,"E25.0.7.56")}),-1.0]])]});
            var Q595;
            Q595=makeQuery(id+"F2.imprint","IMPRINT",FACE,{"disambiguationData":[TD([[makeQuery(id+"F2.imprint","IMPRINT",EDGE,{"derivedFrom":sQuery(id+"F2.wireOp",EDGE,"E25.0.8.76")}),1.0]])]});
            var Q596;
            Q596=makeQuery(id+"F2.imprint","IMPRINT",FACE,{"disambiguationData":[TD([[makeQuery(id+"F2.imprint","IMPRINT",EDGE,{"derivedFrom":sQuery(id+"F2.wireOp",EDGE,"E25.0.8.56")}),-1.0]])]});
            var Q597;
            Q597=makeQuery(id+"F2.imprint","IMPRINT",FACE,{"disambiguationData":[TD([[makeQuery(id+"F2.imprint","IMPRINT",EDGE,{"derivedFrom":sQuery(id+"F2.wireOp",EDGE,"E26.0.1.35")}),1.0]])]});
            var Q598;
            Q598=makeQuery(id+"F2.imprint","IMPRINT",FACE,{"disambiguationData":[TD([[makeQuery(id+"F2.imprint","IMPRINT",EDGE,{"derivedFrom":sQuery(id+"F2.wireOp",EDGE,"E26.0.1.13")}),-1.0]])]});
            var Q599;
            Q599=makeQuery(id+"F2.imprint","IMPRINT",FACE,{"disambiguationData":[TD([[makeQuery(id+"F2.imprint","IMPRINT",EDGE,{"derivedFrom":sQuery(id+"F2.wireOp",EDGE,"E25.0.7.176")}),-1.0]])]});
            var Q600;
            Q600=makeQuery(id+"F2.imprint","IMPRINT",FACE,{"disambiguationData":[TD([[makeQuery(id+"F2.imprint","IMPRINT",EDGE,{"derivedFrom":sQuery(id+"F2.wireOp",EDGE,"E25.0.7.18")}),1.0]])]});
            var Q601;
            Q601=makeQuery(id+"F2.imprint","IMPRINT",FACE,{"disambiguationData":[TD([[makeQuery(id+"F2.imprint","IMPRINT",EDGE,{"derivedFrom":sQuery(id+"F2.wireOp",EDGE,"E25.0.7.24")}),-1.0]])]});
            var Q602;
            Q602=makeQuery(id+"F2.imprint","IMPRINT",FACE,{"disambiguationData":[TD([[makeQuery(id+"F2.imprint","IMPRINT",EDGE,{"derivedFrom":sQuery(id+"F2.wireOp",EDGE,"E25.0.7.45")}),-1.0]])]});
            var Q603;
            Q603=makeQuery(id+"F2.imprint","IMPRINT",FACE,{"disambiguationData":[TD([[makeQuery(id+"F2.imprint","IMPRINT",EDGE,{"derivedFrom":sQuery(id+"F2.wireOp",EDGE,"E25.0.8.176")}),-1.0]])]});
            var Q604;
            Q604=makeQuery(id+"F2.imprint","IMPRINT",FACE,{"disambiguationData":[TD([[makeQuery(id+"F2.imprint","IMPRINT",EDGE,{"derivedFrom":sQuery(id+"F2.wireOp",EDGE,"E25.0.8.18")}),1.0]])]});
            var Q605;
            Q605=makeQuery(id+"F2.imprint","IMPRINT",FACE,{"disambiguationData":[TD([[makeQuery(id+"F2.imprint","IMPRINT",EDGE,{"derivedFrom":sQuery(id+"F2.wireOp",EDGE,"E25.0.8.24")}),-1.0]])]});
            var Q606;
            Q606=makeQuery(id+"F2.imprint","IMPRINT",FACE,{"disambiguationData":[TD([[makeQuery(id+"F2.imprint","IMPRINT",EDGE,{"derivedFrom":sQuery(id+"F2.wireOp",EDGE,"E25.0.8.45")}),-1.0]])]});
            var Q607;
            Q607=makeQuery(id+"F2.imprint","IMPRINT",FACE,{"disambiguationData":[TD([[makeQuery(id+"F2.imprint","IMPRINT",EDGE,{"derivedFrom":sQuery(id+"F2.wireOp",EDGE,"E26.0.1.91")}),-1.0]])]});
            var Q608;
            Q608=makeQuery(id+"F2.imprint","IMPRINT",FACE,{"disambiguationData":[TD([[makeQuery(id+"F2.imprint","IMPRINT",EDGE,{"derivedFrom":sQuery(id+"F2.wireOp",EDGE,"E26.0.1.143")}),1.0]])]});
            var Q609;
            Q609=makeQuery(id+"F2.imprint","IMPRINT",FACE,{"disambiguationData":[TD([[makeQuery(id+"F2.imprint","IMPRINT",EDGE,{"derivedFrom":sQuery(id+"F2.wireOp",EDGE,"E26.0.1.7")}),-1.0]])]});
            var Q610;
            Q610=makeQuery(id+"F2.imprint","IMPRINT",FACE,{"disambiguationData":[TD([[makeQuery(id+"F2.imprint","IMPRINT",EDGE,{"derivedFrom":sQuery(id+"F2.wireOp",EDGE,"E26.0.1.18")}),-1.0]])]});
            var Q611;
            Q611=makeQuery(id+"F2.imprint","IMPRINT",FACE,{"disambiguationData":[TD([[makeQuery(id+"F2.imprint","IMPRINT",EDGE,{"derivedFrom":sQuery(id+"F2.wireOp",EDGE,"E25.0.7.16")}),-1.0]])]});
            var Q612;
            Q612=makeQuery(id+"F2.imprint","IMPRINT",FACE,{"disambiguationData":[TD([[makeQuery(id+"F2.imprint","IMPRINT",EDGE,{"derivedFrom":sQuery(id+"F2.wireOp",EDGE,"E25.0.7.36")}),1.0]])]});
            var Q613;
            Q613=makeQuery(id+"F2.imprint","IMPRINT",FACE,{"disambiguationData":[TD([[makeQuery(id+"F2.imprint","IMPRINT",EDGE,{"derivedFrom":sQuery(id+"F2.wireOp",EDGE,"E25.0.7.39")}),-1.0]])]});
            var Q614;
            Q614=makeQuery(id+"F2.imprint","IMPRINT",FACE,{"disambiguationData":[TD([[makeQuery(id+"F2.imprint","IMPRINT",EDGE,{"derivedFrom":sQuery(id+"F2.wireOp",EDGE,"E25.0.7.48")}),-1.0]])]});
            var Q615;
            Q615=makeQuery(id+"F2.imprint","IMPRINT",FACE,{"disambiguationData":[TD([[makeQuery(id+"F2.imprint","IMPRINT",EDGE,{"derivedFrom":sQuery(id+"F2.wireOp",EDGE,"E25.0.7.0")}),-1.0]])]});
            var Q616;
            Q616=makeQuery(id+"F2.imprint","IMPRINT",FACE,{"disambiguationData":[TD([[makeQuery(id+"F2.imprint","IMPRINT",EDGE,{"derivedFrom":sQuery(id+"F2.wireOp",EDGE,"E25.0.7.21")}),1.0]])]});
            var Q617;
            Q617=makeQuery(id+"F2.imprint","IMPRINT",FACE,{"disambiguationData":[TD([[makeQuery(id+"F2.imprint","IMPRINT",EDGE,{"derivedFrom":sQuery(id+"F2.wireOp",EDGE,"E25.0.7.94")}),-1.0]])]});
            var Q618;
            Q618=makeQuery(id+"F2.imprint","IMPRINT",FACE,{"disambiguationData":[TD([[makeQuery(id+"F2.imprint","IMPRINT",EDGE,{"derivedFrom":sQuery(id+"F2.wireOp",EDGE,"E25.0.7.64")}),1.0]])]});
            var Q619;
            Q619=makeQuery(id+"F2.imprint","IMPRINT",FACE,{"disambiguationData":[TD([[makeQuery(id+"F2.imprint","IMPRINT",EDGE,{"derivedFrom":sQuery(id+"F2.wireOp",EDGE,"E25.0.7.74")}),-1.0]])]});
            var Q620;
            Q620=makeQuery(id+"F2.imprint","IMPRINT",FACE,{"disambiguationData":[TD([[makeQuery(id+"F2.imprint","IMPRINT",EDGE,{"derivedFrom":sQuery(id+"F2.wireOp",EDGE,"E25.0.7.213")}),-1.0]])]});
            var Q621;
            Q621=makeQuery(id+"F2.imprint","IMPRINT",FACE,{"disambiguationData":[TD([[makeQuery(id+"F2.imprint","IMPRINT",EDGE,{"derivedFrom":sQuery(id+"F2.wireOp",EDGE,"E25.0.7.58")}),-1.0]])]});
            var Q622;
            Q622=makeQuery(id+"F2.imprint","IMPRINT",FACE,{"disambiguationData":[TD([[makeQuery(id+"F2.imprint","IMPRINT",EDGE,{"derivedFrom":sQuery(id+"F2.wireOp",EDGE,"E25.0.7.54")}),1.0]])]});
            var Q623;
            Q623=makeQuery(id+"F2.imprint","IMPRINT",FACE,{"disambiguationData":[TD([[makeQuery(id+"F2.imprint","IMPRINT",EDGE,{"derivedFrom":sQuery(id+"F2.wireOp",EDGE,"E25.0.7.34")}),-1.0]])]});
            var Q624;
            Q624=makeQuery(id+"F2.imprint","IMPRINT",FACE,{"disambiguationData":[TD([[makeQuery(id+"F2.imprint","IMPRINT",EDGE,{"derivedFrom":sQuery(id+"F2.wireOp",EDGE,"E25.0.7.26")}),1.0]])]});
            var Q625;
            Q625=makeQuery(id+"F2.imprint","IMPRINT",FACE,{"disambiguationData":[TD([[makeQuery(id+"F2.imprint","IMPRINT",EDGE,{"derivedFrom":sQuery(id+"F2.wireOp",EDGE,"E25.0.7.27")}),-1.0]])]});
            var Q626;
            Q626=makeQuery(id+"F2.imprint","IMPRINT",FACE,{"disambiguationData":[TD([[makeQuery(id+"F2.imprint","IMPRINT",EDGE,{"derivedFrom":sQuery(id+"F2.wireOp",EDGE,"E25.0.7.82")}),-1.0]])]});
            var Q627;
            Q627=makeQuery(id+"F2.imprint","IMPRINT",FACE,{"disambiguationData":[TD([[makeQuery(id+"F2.imprint","IMPRINT",EDGE,{"derivedFrom":sQuery(id+"F2.wireOp",EDGE,"E25.0.7.29")}),-1.0]])]});
            var Q628;
            Q628=makeQuery(id+"F2.imprint","IMPRINT",FACE,{"disambiguationData":[TD([[makeQuery(id+"F2.imprint","IMPRINT",EDGE,{"derivedFrom":sQuery(id+"F2.wireOp",EDGE,"E25.0.7.136")}),1.0]])]});
            var Q629;
            Q629=makeQuery(id+"F2.imprint","IMPRINT",FACE,{"disambiguationData":[TD([[makeQuery(id+"F2.imprint","IMPRINT",EDGE,{"derivedFrom":sQuery(id+"F2.wireOp",EDGE,"E25.0.7.25")}),-1.0]])]});
            var Q630;
            Q630=makeQuery(id+"F2.imprint","IMPRINT",FACE,{"disambiguationData":[TD([[makeQuery(id+"F2.imprint","IMPRINT",EDGE,{"derivedFrom":sQuery(id+"F2.wireOp",EDGE,"E25.0.7.72")}),1.0]])]});
            var Q631;
            Q631=makeQuery(id+"F2.imprint","IMPRINT",FACE,{"disambiguationData":[TD([[makeQuery(id+"F2.imprint","IMPRINT",EDGE,{"derivedFrom":sQuery(id+"F2.wireOp",EDGE,"E25.0.7.28")}),-1.0]])]});
            var Q632;
            Q632=makeQuery(id+"F2.imprint","IMPRINT",FACE,{"disambiguationData":[TD([[makeQuery(id+"F2.imprint","IMPRINT",EDGE,{"derivedFrom":sQuery(id+"F2.wireOp",EDGE,"E25.0.8.72")}),1.0]])]});
            var Q633;
            Q633=makeQuery(id+"F2.imprint","IMPRINT",FACE,{"disambiguationData":[TD([[makeQuery(id+"F2.imprint","IMPRINT",EDGE,{"derivedFrom":sQuery(id+"F2.wireOp",EDGE,"E25.0.8.25")}),-1.0]])]});
            var Q634;
            Q634=makeQuery(id+"F2.imprint","IMPRINT",FACE,{"disambiguationData":[TD([[makeQuery(id+"F2.imprint","IMPRINT",EDGE,{"derivedFrom":sQuery(id+"F2.wireOp",EDGE,"E26.0.1.136")}),1.0]])]});
            var Q635;
            Q635=makeQuery(id+"F2.imprint","IMPRINT",FACE,{"disambiguationData":[TD([[makeQuery(id+"F2.imprint","IMPRINT",EDGE,{"derivedFrom":sQuery(id+"F2.wireOp",EDGE,"E26.0.1.71")}),-1.0]])]});
            var Q636;
            Q636=makeQuery(id+"F2.imprint","IMPRINT",FACE,{"disambiguationData":[TD([[makeQuery(id+"F2.imprint","IMPRINT",EDGE,{"derivedFrom":sQuery(id+"F2.wireOp",EDGE,"E25.0.8.16")}),-1.0]])]});
            var Q637;
            Q637=makeQuery(id+"F2.imprint","IMPRINT",FACE,{"disambiguationData":[TD([[makeQuery(id+"F2.imprint","IMPRINT",EDGE,{"derivedFrom":sQuery(id+"F2.wireOp",EDGE,"E25.0.8.36")}),1.0]])]});
            var Q638;
            Q638=makeQuery(id+"F2.imprint","IMPRINT",FACE,{"disambiguationData":[TD([[makeQuery(id+"F2.imprint","IMPRINT",EDGE,{"derivedFrom":sQuery(id+"F2.wireOp",EDGE,"E25.0.8.39")}),-1.0]])]});
            var Q639;
            Q639=makeQuery(id+"F2.imprint","IMPRINT",FACE,{"disambiguationData":[TD([[makeQuery(id+"F2.imprint","IMPRINT",EDGE,{"derivedFrom":sQuery(id+"F2.wireOp",EDGE,"E25.0.8.48")}),-1.0]])]});
            var Q640;
            Q640=makeQuery(id+"F2.imprint","IMPRINT",FACE,{"disambiguationData":[TD([[makeQuery(id+"F2.imprint","IMPRINT",EDGE,{"derivedFrom":sQuery(id+"F2.wireOp",EDGE,"E25.0.8.0")}),-1.0]])]});
            var Q641;
            Q641=makeQuery(id+"F2.imprint","IMPRINT",FACE,{"disambiguationData":[TD([[makeQuery(id+"F2.imprint","IMPRINT",EDGE,{"derivedFrom":sQuery(id+"F2.wireOp",EDGE,"E25.0.8.21")}),1.0]])]});
            var Q642;
            Q642=makeQuery(id+"F2.imprint","IMPRINT",FACE,{"disambiguationData":[TD([[makeQuery(id+"F2.imprint","IMPRINT",EDGE,{"derivedFrom":sQuery(id+"F2.wireOp",EDGE,"E25.0.8.94")}),-1.0]])]});
            var Q643;
            Q643=makeQuery(id+"F2.imprint","IMPRINT",FACE,{"disambiguationData":[TD([[makeQuery(id+"F2.imprint","IMPRINT",EDGE,{"derivedFrom":sQuery(id+"F2.wireOp",EDGE,"E25.0.8.64")}),1.0]])]});
            var Q644;
            Q644=makeQuery(id+"F2.imprint","IMPRINT",FACE,{"disambiguationData":[TD([[makeQuery(id+"F2.imprint","IMPRINT",EDGE,{"derivedFrom":sQuery(id+"F2.wireOp",EDGE,"E25.0.8.74")}),-1.0]])]});
            var Q645;
            Q645=makeQuery(id+"F2.imprint","IMPRINT",FACE,{"disambiguationData":[TD([[makeQuery(id+"F2.imprint","IMPRINT",EDGE,{"derivedFrom":sQuery(id+"F2.wireOp",EDGE,"E25.0.8.213")}),-1.0]])]});
            var Q646;
            Q646=makeQuery(id+"F2.imprint","IMPRINT",FACE,{"disambiguationData":[TD([[makeQuery(id+"F2.imprint","IMPRINT",EDGE,{"derivedFrom":sQuery(id+"F2.wireOp",EDGE,"E25.0.8.58")}),-1.0]])]});
            var Q647;
            Q647=makeQuery(id+"F2.imprint","IMPRINT",FACE,{"disambiguationData":[TD([[makeQuery(id+"F2.imprint","IMPRINT",EDGE,{"derivedFrom":sQuery(id+"F2.wireOp",EDGE,"E25.0.8.54")}),1.0]])]});
            var Q648;
            Q648=makeQuery(id+"F2.imprint","IMPRINT",FACE,{"disambiguationData":[TD([[makeQuery(id+"F2.imprint","IMPRINT",EDGE,{"derivedFrom":sQuery(id+"F2.wireOp",EDGE,"E25.0.8.34")}),-1.0]])]});
            var Q649;
            Q649=makeQuery(id+"F2.imprint","IMPRINT",FACE,{"disambiguationData":[TD([[makeQuery(id+"F2.imprint","IMPRINT",EDGE,{"derivedFrom":sQuery(id+"F2.wireOp",EDGE,"E25.0.8.26")}),1.0]])]});
            var Q650;
            Q650=makeQuery(id+"F2.imprint","IMPRINT",FACE,{"disambiguationData":[TD([[makeQuery(id+"F2.imprint","IMPRINT",EDGE,{"derivedFrom":sQuery(id+"F2.wireOp",EDGE,"E25.0.8.27")}),-1.0]])]});
            var Q651;
            Q651=makeQuery(id+"F2.imprint","IMPRINT",FACE,{"disambiguationData":[TD([[makeQuery(id+"F2.imprint","IMPRINT",EDGE,{"derivedFrom":sQuery(id+"F2.wireOp",EDGE,"E25.0.8.82")}),-1.0]])]});
            var Q652;
            Q652=makeQuery(id+"F2.imprint","IMPRINT",FACE,{"disambiguationData":[TD([[makeQuery(id+"F2.imprint","IMPRINT",EDGE,{"derivedFrom":sQuery(id+"F2.wireOp",EDGE,"E25.0.8.29")}),-1.0]])]});
            var Q653;
            Q653=makeQuery(id+"F2.imprint","IMPRINT",FACE,{"disambiguationData":[TD([[makeQuery(id+"F2.imprint","IMPRINT",EDGE,{"derivedFrom":sQuery(id+"F2.wireOp",EDGE,"E25.0.8.136")}),1.0]])]});
            var Q654;
            Q654=makeQuery(id+"F2.imprint","IMPRINT",FACE,{"disambiguationData":[TD([[makeQuery(id+"F2.imprint","IMPRINT",EDGE,{"derivedFrom":sQuery(id+"F2.wireOp",EDGE,"E26.0.1.30")}),1.0]])]});
            var Q655;
            Q655=makeQuery(id+"F2.imprint","IMPRINT",FACE,{"disambiguationData":[TD([[makeQuery(id+"F2.imprint","IMPRINT",EDGE,{"derivedFrom":sQuery(id+"F2.wireOp",EDGE,"E26.0.1.63")}),-1.0]])]});
            var Q656;
            Q656=makeQuery(id+"F2.imprint","IMPRINT",FACE,{"disambiguationData":[TD([[makeQuery(id+"F2.imprint","IMPRINT",EDGE,{"derivedFrom":sQuery(id+"F2.wireOp",EDGE,"E26.0.1.12")}),-1.0]])]});
            var Q657;
            Q657=makeQuery(id+"F2.imprint","IMPRINT",FACE,{"disambiguationData":[TD([[makeQuery(id+"F2.imprint","IMPRINT",EDGE,{"derivedFrom":sQuery(id+"F2.wireOp",EDGE,"E26.0.1.111")}),1.0]])]});
            var Q658;
            Q658=makeQuery(id+"F2.imprint","IMPRINT",FACE,{"disambiguationData":[TD([[makeQuery(id+"F2.imprint","IMPRINT",EDGE,{"derivedFrom":sQuery(id+"F2.wireOp",EDGE,"E26.0.1.8")}),-1.0]])]});
            var Q659;
            Q659=makeQuery(id+"F2.imprint","IMPRINT",FACE,{"disambiguationData":[TD([[makeQuery(id+"F2.imprint","IMPRINT",EDGE,{"derivedFrom":sQuery(id+"F2.wireOp",EDGE,"E26.0.1.99")}),-1.0]])]});
            var Q660;
            Q660=makeQuery(id+"F2.imprint","IMPRINT",FACE,{"disambiguationData":[TD([[makeQuery(id+"F2.imprint","IMPRINT",EDGE,{"derivedFrom":sQuery(id+"F2.wireOp",EDGE,"E26.0.1.106")}),1.0]])]});
            var Q661;
            Q661=makeQuery(id+"F2.imprint","IMPRINT",FACE,{"disambiguationData":[TD([[makeQuery(id+"F2.imprint","IMPRINT",EDGE,{"derivedFrom":sQuery(id+"F2.wireOp",EDGE,"E26.0.1.34")}),-1.0]])]});
            var Q662;
            Q662=makeQuery(id+"F2.imprint","IMPRINT",FACE,{"disambiguationData":[TD([[makeQuery(id+"F2.imprint","IMPRINT",EDGE,{"derivedFrom":sQuery(id+"F2.wireOp",EDGE,"E26.0.1.46")}),-1.0]])]});
            var Q663;
            Q663=makeQuery(id+"F2.imprint","IMPRINT",FACE,{"disambiguationData":[TD([[makeQuery(id+"F2.imprint","IMPRINT",EDGE,{"derivedFrom":sQuery(id+"F2.wireOp",EDGE,"E26.0.1.6")}),-1.0]])]});
            var Q664;
            Q664=makeQuery(id+"F2.imprint","IMPRINT",FACE,{"disambiguationData":[TD([[makeQuery(id+"F2.imprint","IMPRINT",EDGE,{"derivedFrom":sQuery(id+"F2.wireOp",EDGE,"E26.0.1.33")}),1.0]])]});
            var Q665;
            Q665=makeQuery(id+"F2.imprint","IMPRINT",FACE,{"disambiguationData":[TD([[makeQuery(id+"F2.imprint","IMPRINT",EDGE,{"derivedFrom":sQuery(id+"F2.wireOp",EDGE,"E26.0.1.117")}),-1.0]])]});
            var Q666;
            Q666=makeQuery(id+"F2.imprint","IMPRINT",FACE,{"disambiguationData":[TD([[makeQuery(id+"F2.imprint","IMPRINT",EDGE,{"derivedFrom":sQuery(id+"F2.wireOp",EDGE,"E26.0.1.112")}),1.0]])]});
            var Q667;
            Q667=makeQuery(id+"F2.imprint","IMPRINT",FACE,{"disambiguationData":[TD([[makeQuery(id+"F2.imprint","IMPRINT",EDGE,{"derivedFrom":sQuery(id+"F2.wireOp",EDGE,"E26.0.1.164")}),-1.0]])]});
            var Q668;
            Q668=makeQuery(id+"F2.imprint","IMPRINT",FACE,{"disambiguationData":[TD([[makeQuery(id+"F2.imprint","IMPRINT",EDGE,{"derivedFrom":sQuery(id+"F2.wireOp",EDGE,"E26.0.1.87")}),-1.0]])]});
            var Q669;
            Q669=makeQuery(id+"F2.imprint","IMPRINT",FACE,{"disambiguationData":[TD([[makeQuery(id+"F2.imprint","IMPRINT",EDGE,{"derivedFrom":sQuery(id+"F2.wireOp",EDGE,"E26.0.1.62")}),-1.0]])]});
            var Q670;
            Q670=makeQuery(id+"F2.imprint","IMPRINT",FACE,{"disambiguationData":[TD([[makeQuery(id+"F2.imprint","IMPRINT",EDGE,{"derivedFrom":sQuery(id+"F2.wireOp",EDGE,"E26.0.1.113")}),1.0]])]});
            var Q671;
            Q671=makeQuery(id+"F2.imprint","IMPRINT",FACE,{"disambiguationData":[TD([[makeQuery(id+"F2.imprint","IMPRINT",EDGE,{"derivedFrom":sQuery(id+"F2.wireOp",EDGE,"E26.0.1.80")}),1.0]])]});
            var Q672;
            Q672=makeQuery(id+"F2.imprint","IMPRINT",FACE,{"disambiguationData":[TD([[makeQuery(id+"F2.imprint","IMPRINT",EDGE,{"derivedFrom":sQuery(id+"F2.wireOp",EDGE,"E26.0.1.48")}),-1.0]])]});
            var Q673;
            Q673=makeQuery(id+"F2.imprint","IMPRINT",FACE,{"disambiguationData":[TD([[makeQuery(id+"F2.imprint","IMPRINT",EDGE,{"derivedFrom":sQuery(id+"F2.wireOp",EDGE,"E26.0.1.102")}),1.0]])]});
            var Q674;
            Q674=makeQuery(id+"F2.imprint","IMPRINT",FACE,{"disambiguationData":[TD([[makeQuery(id+"F2.imprint","IMPRINT",EDGE,{"derivedFrom":sQuery(id+"F2.wireOp",EDGE,"E26.0.1.38")}),-1.0]])]});
            var Q675;
            Q675=makeQuery(id+"F2.imprint","IMPRINT",FACE,{"disambiguationData":[TD([[makeQuery(id+"F2.imprint","IMPRINT",EDGE,{"derivedFrom":sQuery(id+"F2.wireOp",EDGE,"E26.0.1.130")}),-1.0]])]});
            var Q676;
            Q676=makeQuery(id+"F2.imprint","IMPRINT",FACE,{"disambiguationData":[TD([[makeQuery(id+"F2.imprint","IMPRINT",EDGE,{"derivedFrom":sQuery(id+"F2.wireOp",EDGE,"E26.0.1.43")}),-1.0]])]});
            var Q677;
            Q677=makeQuery(id+"F2.imprint","IMPRINT",FACE,{"disambiguationData":[TD([[makeQuery(id+"F2.imprint","IMPRINT",EDGE,{"derivedFrom":sQuery(id+"F2.wireOp",EDGE,"E26.0.1.191")}),1.0]])]});
            var Q678;
            Q678=makeQuery(id+"F2.imprint","IMPRINT",FACE,{"disambiguationData":[TD([[makeQuery(id+"F2.imprint","IMPRINT",EDGE,{"derivedFrom":sQuery(id+"F2.wireOp",EDGE,"E26.0.1.16")}),-1.0]])]});
            var Q679;
            Q679=makeQuery(id+"F2.imprint","IMPRINT",FACE,{"disambiguationData":[TD([[makeQuery(id+"F2.imprint","IMPRINT",EDGE,{"derivedFrom":sQuery(id+"F2.wireOp",EDGE,"E26.0.1.84")}),1.0]])]});
            var Q680;
            Q680=makeQuery(id+"F2.imprint","IMPRINT",FACE,{"disambiguationData":[TD([[makeQuery(id+"F2.imprint","IMPRINT",EDGE,{"derivedFrom":sQuery(id+"F2.wireOp",EDGE,"E26.0.1.54")}),-1.0]])]});
            var Q681;
            Q681=makeQuery(id+"F2.imprint","IMPRINT",FACE,{"disambiguationData":[TD([[makeQuery(id+"F2.imprint","IMPRINT",EDGE,{"derivedFrom":sQuery(id+"F2.wireOp",EDGE,"E26.0.1.88")}),-1.0]])]});
            var Q682;
            Q682=makeQuery(id+"F2.imprint","IMPRINT",FACE,{"disambiguationData":[TD([[makeQuery(id+"F2.imprint","IMPRINT",EDGE,{"derivedFrom":sQuery(id+"F2.wireOp",EDGE,"E25.0.2.14")}),-1.0]])]});
            var Q683;
            Q683=makeQuery(id+"F2.imprint","IMPRINT",FACE,{"disambiguationData":[TD([[makeQuery(id+"F2.imprint","IMPRINT",EDGE,{"derivedFrom":sQuery(id+"F2.wireOp",EDGE,"E25.0.3.22")}),1.0]])]});
            var Q684;
            Q684=makeQuery(id+"F2.imprint","IMPRINT",FACE,{"disambiguationData":[TD([[makeQuery(id+"F2.imprint","IMPRINT",EDGE,{"derivedFrom":sQuery(id+"F2.wireOp",EDGE,"E25.0.2.35")}),-1.0]])]});
            var Q685;
            Q685=makeQuery(id+"F2.imprint","IMPRINT",FACE,{"disambiguationData":[TD([[makeQuery(id+"F2.imprint","IMPRINT",EDGE,{"derivedFrom":sQuery(id+"F2.wireOp",EDGE,"E25.0.3.11")}),-1.0]])]});
            var Q686;
            Q686=makeQuery(id+"F2.imprint","IMPRINT",FACE,{"disambiguationData":[TD([[makeQuery(id+"F2.imprint","IMPRINT",EDGE,{"derivedFrom":sQuery(id+"F2.wireOp",EDGE,"E25.0.2.3")}),-1.0]])]});
            var Q687;
            Q687=makeQuery(id+"F2.imprint","IMPRINT",FACE,{"disambiguationData":[TD([[makeQuery(id+"F2.imprint","IMPRINT",EDGE,{"derivedFrom":sQuery(id+"F2.wireOp",EDGE,"E25.0.3.15")}),1.0]])]});
            var Q688;
            Q688=makeQuery(id+"F2.imprint","IMPRINT",FACE,{"disambiguationData":[TD([[makeQuery(id+"F2.imprint","IMPRINT",EDGE,{"derivedFrom":sQuery(id+"F2.wireOp",EDGE,"E25.0.2.162")}),-1.0]])]});
            var Q689;
            Q689=makeQuery(id+"F2.imprint","IMPRINT",FACE,{"disambiguationData":[TD([[makeQuery(id+"F2.imprint","IMPRINT",EDGE,{"derivedFrom":sQuery(id+"F2.wireOp",EDGE,"E25.0.3.65")}),1.0]])]});
            var Q690;
            Q690=makeQuery(id+"F2.imprint","IMPRINT",FACE,{"disambiguationData":[TD([[makeQuery(id+"F2.imprint","IMPRINT",EDGE,{"derivedFrom":sQuery(id+"F2.wireOp",EDGE,"E25.0.2.69")}),-1.0]])]});
            var Q691;
            Q691=makeQuery(id+"F2.imprint","IMPRINT",FACE,{"disambiguationData":[TD([[makeQuery(id+"F2.imprint","IMPRINT",EDGE,{"derivedFrom":sQuery(id+"F2.wireOp",EDGE,"E25.0.3.221")}),-1.0]])]});
            var Q692;
            Q692=makeQuery(id+"F2.imprint","IMPRINT",FACE,{"disambiguationData":[TD([[makeQuery(id+"F2.imprint","IMPRINT",EDGE,{"derivedFrom":sQuery(id+"F2.wireOp",EDGE,"E25.0.2.62")}),-1.0]])]});
            var Q693;
            Q693=makeQuery(id+"F2.imprint","IMPRINT",FACE,{"disambiguationData":[TD([[makeQuery(id+"F2.imprint","IMPRINT",EDGE,{"derivedFrom":sQuery(id+"F2.wireOp",EDGE,"E25.0.3.55")}),1.0]])]});
            var Q694;
            Q694=makeQuery(id+"F2.imprint","IMPRINT",FACE,{"disambiguationData":[TD([[makeQuery(id+"F2.imprint","IMPRINT",EDGE,{"derivedFrom":sQuery(id+"F2.wireOp",EDGE,"E25.0.2.32")}),-1.0]])]});
            var Q695;
            Q695=makeQuery(id+"F2.imprint","IMPRINT",FACE,{"disambiguationData":[TD([[makeQuery(id+"F2.imprint","IMPRINT",EDGE,{"derivedFrom":sQuery(id+"F2.wireOp",EDGE,"E25.0.3.13")}),1.0]])]});
            var Q696;
            Q696=makeQuery(id+"F2.imprint","IMPRINT",FACE,{"disambiguationData":[TD([[makeQuery(id+"F2.imprint","IMPRINT",EDGE,{"derivedFrom":sQuery(id+"F2.wireOp",EDGE,"E25.0.2.12")}),-1.0]])]});
            var Q697;
            Q697=makeQuery(id+"F2.imprint","IMPRINT",FACE,{"disambiguationData":[TD([[makeQuery(id+"F2.imprint","IMPRINT",EDGE,{"derivedFrom":sQuery(id+"F2.wireOp",EDGE,"E25.0.3.149")}),-1.0]])]});
            var Q698;
            Q698=makeQuery(id+"F2.imprint","IMPRINT",FACE,{"disambiguationData":[TD([[makeQuery(id+"F2.imprint","IMPRINT",EDGE,{"derivedFrom":sQuery(id+"F2.wireOp",EDGE,"E25.0.3.14")}),-1.0]])]});
            var Q699;
            Q699=makeQuery(id+"F2.imprint","IMPRINT",FACE,{"disambiguationData":[TD([[makeQuery(id+"F2.imprint","IMPRINT",EDGE,{"derivedFrom":sQuery(id+"F2.wireOp",EDGE,"E25.0.4.22")}),1.0]])]});
            var Q700;
            Q700=makeQuery(id+"F2.imprint","IMPRINT",FACE,{"disambiguationData":[TD([[makeQuery(id+"F2.imprint","IMPRINT",EDGE,{"derivedFrom":sQuery(id+"F2.wireOp",EDGE,"E25.0.3.35")}),-1.0]])]});
            var Q701;
            Q701=makeQuery(id+"F2.imprint","IMPRINT",FACE,{"disambiguationData":[TD([[makeQuery(id+"F2.imprint","IMPRINT",EDGE,{"derivedFrom":sQuery(id+"F2.wireOp",EDGE,"E25.0.4.11")}),-1.0]])]});
            var Q702;
            Q702=makeQuery(id+"F2.imprint","IMPRINT",FACE,{"disambiguationData":[TD([[makeQuery(id+"F2.imprint","IMPRINT",EDGE,{"derivedFrom":sQuery(id+"F2.wireOp",EDGE,"E25.0.3.3")}),-1.0]])]});
            var Q703;
            Q703=makeQuery(id+"F2.imprint","IMPRINT",FACE,{"disambiguationData":[TD([[makeQuery(id+"F2.imprint","IMPRINT",EDGE,{"derivedFrom":sQuery(id+"F2.wireOp",EDGE,"E25.0.4.15")}),1.0]])]});
            var Q704;
            Q704=makeQuery(id+"F2.imprint","IMPRINT",FACE,{"disambiguationData":[TD([[makeQuery(id+"F2.imprint","IMPRINT",EDGE,{"derivedFrom":sQuery(id+"F2.wireOp",EDGE,"E25.0.3.162")}),-1.0]])]});
            var Q705;
            Q705=makeQuery(id+"F2.imprint","IMPRINT",FACE,{"disambiguationData":[TD([[makeQuery(id+"F2.imprint","IMPRINT",EDGE,{"derivedFrom":sQuery(id+"F2.wireOp",EDGE,"E25.0.4.65")}),1.0]])]});
            var Q706;
            Q706=makeQuery(id+"F2.imprint","IMPRINT",FACE,{"disambiguationData":[TD([[makeQuery(id+"F2.imprint","IMPRINT",EDGE,{"derivedFrom":sQuery(id+"F2.wireOp",EDGE,"E25.0.3.69")}),-1.0]])]});
            var Q707;
            Q707=makeQuery(id+"F2.imprint","IMPRINT",FACE,{"disambiguationData":[TD([[makeQuery(id+"F2.imprint","IMPRINT",EDGE,{"derivedFrom":sQuery(id+"F2.wireOp",EDGE,"E25.0.4.221")}),-1.0]])]});
            var Q708;
            Q708=makeQuery(id+"F2.imprint","IMPRINT",FACE,{"disambiguationData":[TD([[makeQuery(id+"F2.imprint","IMPRINT",EDGE,{"derivedFrom":sQuery(id+"F2.wireOp",EDGE,"E25.0.3.62")}),-1.0]])]});
            var Q709;
            Q709=makeQuery(id+"F2.imprint","IMPRINT",FACE,{"disambiguationData":[TD([[makeQuery(id+"F2.imprint","IMPRINT",EDGE,{"derivedFrom":sQuery(id+"F2.wireOp",EDGE,"E25.0.4.55")}),1.0]])]});
            var Q710;
            Q710=makeQuery(id+"F2.imprint","IMPRINT",FACE,{"disambiguationData":[TD([[makeQuery(id+"F2.imprint","IMPRINT",EDGE,{"derivedFrom":sQuery(id+"F2.wireOp",EDGE,"E25.0.3.32")}),-1.0]])]});
            var Q711;
            Q711=makeQuery(id+"F2.imprint","IMPRINT",FACE,{"disambiguationData":[TD([[makeQuery(id+"F2.imprint","IMPRINT",EDGE,{"derivedFrom":sQuery(id+"F2.wireOp",EDGE,"E25.0.4.13")}),1.0]])]});
            var Q712;
            Q712=makeQuery(id+"F2.imprint","IMPRINT",FACE,{"disambiguationData":[TD([[makeQuery(id+"F2.imprint","IMPRINT",EDGE,{"derivedFrom":sQuery(id+"F2.wireOp",EDGE,"E25.0.3.12")}),-1.0]])]});
            var Q713;
            Q713=makeQuery(id+"F2.imprint","IMPRINT",FACE,{"disambiguationData":[TD([[makeQuery(id+"F2.imprint","IMPRINT",EDGE,{"derivedFrom":sQuery(id+"F2.wireOp",EDGE,"E25.0.4.149")}),-1.0]])]});
            var Q714;
            Q714=makeQuery(id+"F2.imprint","IMPRINT",FACE,{"disambiguationData":[TD([[makeQuery(id+"F2.imprint","IMPRINT",EDGE,{"derivedFrom":sQuery(id+"F2.wireOp",EDGE,"E25.0.4.14")}),-1.0]])]});
            var Q715;
            Q715=makeQuery(id+"F2.imprint","IMPRINT",FACE,{"disambiguationData":[TD([[makeQuery(id+"F2.imprint","IMPRINT",EDGE,{"derivedFrom":sQuery(id+"F2.wireOp",EDGE,"E25.0.5.22")}),1.0]])]});
            var Q716;
            Q716=makeQuery(id+"F2.imprint","IMPRINT",FACE,{"disambiguationData":[TD([[makeQuery(id+"F2.imprint","IMPRINT",EDGE,{"derivedFrom":sQuery(id+"F2.wireOp",EDGE,"E25.0.4.35")}),-1.0]])]});
            var Q717;
            Q717=makeQuery(id+"F2.imprint","IMPRINT",FACE,{"disambiguationData":[TD([[makeQuery(id+"F2.imprint","IMPRINT",EDGE,{"derivedFrom":sQuery(id+"F2.wireOp",EDGE,"E25.0.5.11")}),-1.0]])]});
            var Q718;
            Q718=makeQuery(id+"F2.imprint","IMPRINT",FACE,{"disambiguationData":[TD([[makeQuery(id+"F2.imprint","IMPRINT",EDGE,{"derivedFrom":sQuery(id+"F2.wireOp",EDGE,"E25.0.4.3")}),-1.0]])]});
            var Q719;
            Q719=makeQuery(id+"F2.imprint","IMPRINT",FACE,{"disambiguationData":[TD([[makeQuery(id+"F2.imprint","IMPRINT",EDGE,{"derivedFrom":sQuery(id+"F2.wireOp",EDGE,"E25.0.5.15")}),1.0]])]});
            var Q720;
            Q720=makeQuery(id+"F2.imprint","IMPRINT",FACE,{"disambiguationData":[TD([[makeQuery(id+"F2.imprint","IMPRINT",EDGE,{"derivedFrom":sQuery(id+"F2.wireOp",EDGE,"E25.0.4.162")}),-1.0]])]});
            var Q721;
            Q721=makeQuery(id+"F2.imprint","IMPRINT",FACE,{"disambiguationData":[TD([[makeQuery(id+"F2.imprint","IMPRINT",EDGE,{"derivedFrom":sQuery(id+"F2.wireOp",EDGE,"E25.0.5.65")}),1.0]])]});
            var Q722;
            Q722=makeQuery(id+"F2.imprint","IMPRINT",FACE,{"disambiguationData":[TD([[makeQuery(id+"F2.imprint","IMPRINT",EDGE,{"derivedFrom":sQuery(id+"F2.wireOp",EDGE,"E25.0.4.69")}),-1.0]])]});
            var Q723;
            Q723=makeQuery(id+"F2.imprint","IMPRINT",FACE,{"disambiguationData":[TD([[makeQuery(id+"F2.imprint","IMPRINT",EDGE,{"derivedFrom":sQuery(id+"F2.wireOp",EDGE,"E25.0.5.221")}),-1.0]])]});
            var Q724;
            Q724=makeQuery(id+"F2.imprint","IMPRINT",FACE,{"disambiguationData":[TD([[makeQuery(id+"F2.imprint","IMPRINT",EDGE,{"derivedFrom":sQuery(id+"F2.wireOp",EDGE,"E25.0.4.62")}),-1.0]])]});
            var Q725;
            Q725=makeQuery(id+"F2.imprint","IMPRINT",FACE,{"disambiguationData":[TD([[makeQuery(id+"F2.imprint","IMPRINT",EDGE,{"derivedFrom":sQuery(id+"F2.wireOp",EDGE,"E25.0.5.55")}),1.0]])]});
            var Q726;
            Q726=makeQuery(id+"F2.imprint","IMPRINT",FACE,{"disambiguationData":[TD([[makeQuery(id+"F2.imprint","IMPRINT",EDGE,{"derivedFrom":sQuery(id+"F2.wireOp",EDGE,"E25.0.4.32")}),-1.0]])]});
            var Q727;
            Q727=makeQuery(id+"F2.imprint","IMPRINT",FACE,{"disambiguationData":[TD([[makeQuery(id+"F2.imprint","IMPRINT",EDGE,{"derivedFrom":sQuery(id+"F2.wireOp",EDGE,"E25.0.5.13")}),1.0]])]});
            var Q728;
            Q728=makeQuery(id+"F2.imprint","IMPRINT",FACE,{"disambiguationData":[TD([[makeQuery(id+"F2.imprint","IMPRINT",EDGE,{"derivedFrom":sQuery(id+"F2.wireOp",EDGE,"E25.0.4.12")}),-1.0]])]});
            var Q729;
            Q729=makeQuery(id+"F2.imprint","IMPRINT",FACE,{"disambiguationData":[TD([[makeQuery(id+"F2.imprint","IMPRINT",EDGE,{"derivedFrom":sQuery(id+"F2.wireOp",EDGE,"E25.0.5.149")}),-1.0]])]});
            var Q730;
            Q730=makeQuery(id+"F2.imprint","IMPRINT",FACE,{"disambiguationData":[TD([[makeQuery(id+"F2.imprint","IMPRINT",EDGE,{"derivedFrom":sQuery(id+"F2.wireOp",EDGE,"E25.0.5.14")}),-1.0]])]});
            var Q731;
            Q731=makeQuery(id+"F2.imprint","IMPRINT",FACE,{"disambiguationData":[TD([[makeQuery(id+"F2.imprint","IMPRINT",EDGE,{"derivedFrom":sQuery(id+"F2.wireOp",EDGE,"E25.0.6.22")}),1.0]])]});
            var Q732;
            Q732=makeQuery(id+"F2.imprint","IMPRINT",FACE,{"disambiguationData":[TD([[makeQuery(id+"F2.imprint","IMPRINT",EDGE,{"derivedFrom":sQuery(id+"F2.wireOp",EDGE,"E25.0.6.14")}),-1.0]])]});
            var Q733;
            Q733=makeQuery(id+"F2.imprint","IMPRINT",FACE,{"disambiguationData":[TD([[makeQuery(id+"F2.imprint","IMPRINT",EDGE,{"derivedFrom":sQuery(id+"F2.wireOp",EDGE,"E25.0.7.22")}),1.0]])]});
            var Q734;
            Q734=makeQuery(id+"F2.imprint","IMPRINT",FACE,{"disambiguationData":[TD([[makeQuery(id+"F2.imprint","IMPRINT",EDGE,{"derivedFrom":sQuery(id+"F2.wireOp",EDGE,"E25.0.7.14")}),-1.0]])]});
            var Q735;
            Q735=makeQuery(id+"F2.imprint","IMPRINT",FACE,{"disambiguationData":[TD([[makeQuery(id+"F2.imprint","IMPRINT",EDGE,{"derivedFrom":sQuery(id+"F2.wireOp",EDGE,"E25.0.8.22")}),1.0]])]});
            var Q736;
            Q736=makeQuery(id+"F2.imprint","IMPRINT",FACE,{"disambiguationData":[TD([[makeQuery(id+"F2.imprint","IMPRINT",EDGE,{"derivedFrom":sQuery(id+"F2.wireOp",EDGE,"E25.0.8.11")}),-1.0]])]});
            var Q737;
            Q737=makeQuery(id+"F2.imprint","IMPRINT",FACE,{"disambiguationData":[TD([[makeQuery(id+"F2.imprint","IMPRINT",EDGE,{"derivedFrom":sQuery(id+"F2.wireOp",EDGE,"E25.0.8.3")}),-1.0]])]});
            var Q738;
            Q738=makeQuery(id+"F2.imprint","IMPRINT",FACE,{"disambiguationData":[TD([[makeQuery(id+"F2.imprint","IMPRINT",EDGE,{"derivedFrom":sQuery(id+"F2.wireOp",EDGE,"E25.0.8.15")}),1.0]])]});
            var Q739;
            Q739=makeQuery(id+"F2.imprint","IMPRINT",FACE,{"disambiguationData":[TD([[makeQuery(id+"F2.imprint","IMPRINT",EDGE,{"derivedFrom":sQuery(id+"F2.wireOp",EDGE,"E25.0.8.162")}),-1.0]])]});
            var Q740;
            Q740=makeQuery(id+"F2.imprint","IMPRINT",FACE,{"disambiguationData":[TD([[makeQuery(id+"F2.imprint","IMPRINT",EDGE,{"derivedFrom":sQuery(id+"F2.wireOp",EDGE,"E25.0.8.65")}),1.0]])]});
            var Q741;
            Q741=makeQuery(id+"F2.imprint","IMPRINT",FACE,{"disambiguationData":[TD([[makeQuery(id+"F2.imprint","IMPRINT",EDGE,{"derivedFrom":sQuery(id+"F2.wireOp",EDGE,"E25.0.8.69")}),-1.0]])]});
            var Q742;
            Q742=makeQuery(id+"F2.imprint","IMPRINT",FACE,{"disambiguationData":[TD([[makeQuery(id+"F2.imprint","IMPRINT",EDGE,{"derivedFrom":sQuery(id+"F2.wireOp",EDGE,"E25.0.8.221")}),-1.0]])]});
            var Q743;
            Q743=makeQuery(id+"F2.imprint","IMPRINT",FACE,{"disambiguationData":[TD([[makeQuery(id+"F2.imprint","IMPRINT",EDGE,{"derivedFrom":sQuery(id+"F2.wireOp",EDGE,"E25.0.8.62")}),-1.0]])]});
            var Q744;
            Q744=makeQuery(id+"F2.imprint","IMPRINT",FACE,{"disambiguationData":[TD([[makeQuery(id+"F2.imprint","IMPRINT",EDGE,{"derivedFrom":sQuery(id+"F2.wireOp",EDGE,"E25.0.8.55")}),1.0]])]});
            var Q745;
            Q745=makeQuery(id+"F2.imprint","IMPRINT",FACE,{"disambiguationData":[TD([[makeQuery(id+"F2.imprint","IMPRINT",EDGE,{"derivedFrom":sQuery(id+"F2.wireOp",EDGE,"E25.0.8.32")}),-1.0]])]});
            var Q746;
            Q746=makeQuery(id+"F2.imprint","IMPRINT",FACE,{"disambiguationData":[TD([[makeQuery(id+"F2.imprint","IMPRINT",EDGE,{"derivedFrom":sQuery(id+"F2.wireOp",EDGE,"E25.0.8.13")}),1.0]])]});
            var Q747;
            Q747=makeQuery(id+"F2.imprint","IMPRINT",FACE,{"disambiguationData":[TD([[makeQuery(id+"F2.imprint","IMPRINT",EDGE,{"derivedFrom":sQuery(id+"F2.wireOp",EDGE,"E25.0.8.12")}),-1.0]])]});
            var Q748;
            Q748=makeQuery(id+"F2.imprint","IMPRINT",FACE,{"disambiguationData":[TD([[makeQuery(id+"F2.imprint","IMPRINT",EDGE,{"derivedFrom":sQuery(id+"F2.wireOp",EDGE,"E25.0.8.149")}),-1.0]])]});
            var Q749;
            Q749=makeQuery(id+"F2.imprint","IMPRINT",FACE,{"disambiguationData":[TD([[makeQuery(id+"F2.imprint","IMPRINT",EDGE,{"derivedFrom":sQuery(id+"F2.wireOp",EDGE,"E25.0.7.35")}),-1.0]])]});
            var Q750;
            Q750=makeQuery(id+"F2.imprint","IMPRINT",FACE,{"disambiguationData":[TD([[makeQuery(id+"F2.imprint","IMPRINT",EDGE,{"derivedFrom":sQuery(id+"F2.wireOp",EDGE,"E25.0.7.11")}),-1.0]])]});
            var Q751;
            Q751=makeQuery(id+"F2.imprint","IMPRINT",FACE,{"disambiguationData":[TD([[makeQuery(id+"F2.imprint","IMPRINT",EDGE,{"derivedFrom":sQuery(id+"F2.wireOp",EDGE,"E25.0.7.3")}),-1.0]])]});
            var Q752;
            Q752=makeQuery(id+"F2.imprint","IMPRINT",FACE,{"disambiguationData":[TD([[makeQuery(id+"F2.imprint","IMPRINT",EDGE,{"derivedFrom":sQuery(id+"F2.wireOp",EDGE,"E25.0.7.15")}),1.0]])]});
            var Q753;
            Q753=makeQuery(id+"F2.imprint","IMPRINT",FACE,{"disambiguationData":[TD([[makeQuery(id+"F2.imprint","IMPRINT",EDGE,{"derivedFrom":sQuery(id+"F2.wireOp",EDGE,"E25.0.7.162")}),-1.0]])]});
            var Q754;
            Q754=makeQuery(id+"F2.imprint","IMPRINT",FACE,{"disambiguationData":[TD([[makeQuery(id+"F2.imprint","IMPRINT",EDGE,{"derivedFrom":sQuery(id+"F2.wireOp",EDGE,"E25.0.7.65")}),1.0]])]});
            var Q755;
            Q755=makeQuery(id+"F2.imprint","IMPRINT",FACE,{"disambiguationData":[TD([[makeQuery(id+"F2.imprint","IMPRINT",EDGE,{"derivedFrom":sQuery(id+"F2.wireOp",EDGE,"E25.0.7.69")}),-1.0]])]});
            var Q756;
            Q756=makeQuery(id+"F2.imprint","IMPRINT",FACE,{"disambiguationData":[TD([[makeQuery(id+"F2.imprint","IMPRINT",EDGE,{"derivedFrom":sQuery(id+"F2.wireOp",EDGE,"E25.0.7.221")}),-1.0]])]});
            var Q757;
            Q757=makeQuery(id+"F2.imprint","IMPRINT",FACE,{"disambiguationData":[TD([[makeQuery(id+"F2.imprint","IMPRINT",EDGE,{"derivedFrom":sQuery(id+"F2.wireOp",EDGE,"E25.0.7.62")}),-1.0]])]});
            var Q758;
            Q758=makeQuery(id+"F2.imprint","IMPRINT",FACE,{"disambiguationData":[TD([[makeQuery(id+"F2.imprint","IMPRINT",EDGE,{"derivedFrom":sQuery(id+"F2.wireOp",EDGE,"E25.0.7.55")}),1.0]])]});
            var Q759;
            Q759=makeQuery(id+"F2.imprint","IMPRINT",FACE,{"disambiguationData":[TD([[makeQuery(id+"F2.imprint","IMPRINT",EDGE,{"derivedFrom":sQuery(id+"F2.wireOp",EDGE,"E25.0.7.32")}),-1.0]])]});
            var Q760;
            Q760=makeQuery(id+"F2.imprint","IMPRINT",FACE,{"disambiguationData":[TD([[makeQuery(id+"F2.imprint","IMPRINT",EDGE,{"derivedFrom":sQuery(id+"F2.wireOp",EDGE,"E25.0.7.13")}),1.0]])]});
            var Q761;
            Q761=makeQuery(id+"F2.imprint","IMPRINT",FACE,{"disambiguationData":[TD([[makeQuery(id+"F2.imprint","IMPRINT",EDGE,{"derivedFrom":sQuery(id+"F2.wireOp",EDGE,"E25.0.7.12")}),-1.0]])]});
            var Q762;
            Q762=makeQuery(id+"F2.imprint","IMPRINT",FACE,{"disambiguationData":[TD([[makeQuery(id+"F2.imprint","IMPRINT",EDGE,{"derivedFrom":sQuery(id+"F2.wireOp",EDGE,"E25.0.7.149")}),-1.0]])]});
            var Q763;
            Q763=makeQuery(id+"F2.imprint","IMPRINT",FACE,{"disambiguationData":[TD([[makeQuery(id+"F2.imprint","IMPRINT",EDGE,{"derivedFrom":sQuery(id+"F2.wireOp",EDGE,"E25.0.5.35")}),-1.0]])]});
            var Q764;
            Q764=makeQuery(id+"F2.imprint","IMPRINT",FACE,{"disambiguationData":[TD([[makeQuery(id+"F2.imprint","IMPRINT",EDGE,{"derivedFrom":sQuery(id+"F2.wireOp",EDGE,"E25.0.6.11")}),-1.0]])]});
            var Q765;
            Q765=makeQuery(id+"F2.imprint","IMPRINT",FACE,{"disambiguationData":[TD([[makeQuery(id+"F2.imprint","IMPRINT",EDGE,{"derivedFrom":sQuery(id+"F2.wireOp",EDGE,"E25.0.6.35")}),-1.0]])]});
            var Q766;
            Q766=makeQuery(id+"F2.imprint","IMPRINT",FACE,{"disambiguationData":[TD([[makeQuery(id+"F2.imprint","IMPRINT",EDGE,{"derivedFrom":sQuery(id+"F2.wireOp",EDGE,"E25.0.6.3")}),-1.0]])]});
            var Q767;
            Q767=makeQuery(id+"F2.imprint","IMPRINT",FACE,{"disambiguationData":[TD([[makeQuery(id+"F2.imprint","IMPRINT",EDGE,{"derivedFrom":sQuery(id+"F2.wireOp",EDGE,"E25.0.6.15")}),1.0]])]});
            var Q768;
            Q768=makeQuery(id+"F2.imprint","IMPRINT",FACE,{"disambiguationData":[TD([[makeQuery(id+"F2.imprint","IMPRINT",EDGE,{"derivedFrom":sQuery(id+"F2.wireOp",EDGE,"E25.0.5.3")}),-1.0]])]});
            var Q769;
            Q769=makeQuery(id+"F2.imprint","IMPRINT",FACE,{"disambiguationData":[TD([[makeQuery(id+"F2.imprint","IMPRINT",EDGE,{"derivedFrom":sQuery(id+"F2.wireOp",EDGE,"E25.0.5.162")}),-1.0]])]});
            var Q770;
            Q770=makeQuery(id+"F2.imprint","IMPRINT",FACE,{"disambiguationData":[TD([[makeQuery(id+"F2.imprint","IMPRINT",EDGE,{"derivedFrom":sQuery(id+"F2.wireOp",EDGE,"E25.0.6.65")}),1.0]])]});
            var Q771;
            Q771=makeQuery(id+"F2.imprint","IMPRINT",FACE,{"disambiguationData":[TD([[makeQuery(id+"F2.imprint","IMPRINT",EDGE,{"derivedFrom":sQuery(id+"F2.wireOp",EDGE,"E25.0.6.162")}),-1.0]])]});
            var Q772;
            Q772=makeQuery(id+"F2.imprint","IMPRINT",FACE,{"disambiguationData":[TD([[makeQuery(id+"F2.imprint","IMPRINT",EDGE,{"derivedFrom":sQuery(id+"F2.wireOp",EDGE,"E25.0.6.69")}),-1.0]])]});
            var Q773;
            Q773=makeQuery(id+"F2.imprint","IMPRINT",FACE,{"disambiguationData":[TD([[makeQuery(id+"F2.imprint","IMPRINT",EDGE,{"derivedFrom":sQuery(id+"F2.wireOp",EDGE,"E25.0.6.221")}),-1.0]])]});
            var Q774;
            Q774=makeQuery(id+"F2.imprint","IMPRINT",FACE,{"disambiguationData":[TD([[makeQuery(id+"F2.imprint","IMPRINT",EDGE,{"derivedFrom":sQuery(id+"F2.wireOp",EDGE,"E25.0.5.69")}),-1.0]])]});
            var Q775;
            Q775=makeQuery(id+"F2.imprint","IMPRINT",FACE,{"disambiguationData":[TD([[makeQuery(id+"F2.imprint","IMPRINT",EDGE,{"derivedFrom":sQuery(id+"F2.wireOp",EDGE,"E25.0.5.62")}),-1.0]])]});
            var Q776;
            Q776=makeQuery(id+"F2.imprint","IMPRINT",FACE,{"disambiguationData":[TD([[makeQuery(id+"F2.imprint","IMPRINT",EDGE,{"derivedFrom":sQuery(id+"F2.wireOp",EDGE,"E25.0.5.32")}),-1.0]])]});
            var Q777;
            Q777=makeQuery(id+"F2.imprint","IMPRINT",FACE,{"disambiguationData":[TD([[makeQuery(id+"F2.imprint","IMPRINT",EDGE,{"derivedFrom":sQuery(id+"F2.wireOp",EDGE,"E25.0.5.12")}),-1.0]])]});
            var Q778;
            Q778=makeQuery(id+"F2.imprint","IMPRINT",FACE,{"disambiguationData":[TD([[makeQuery(id+"F2.imprint","IMPRINT",EDGE,{"derivedFrom":sQuery(id+"F2.wireOp",EDGE,"E25.0.6.55")}),1.0]])]});
            var Q779;
            Q779=makeQuery(id+"F2.imprint","IMPRINT",FACE,{"disambiguationData":[TD([[makeQuery(id+"F2.imprint","IMPRINT",EDGE,{"derivedFrom":sQuery(id+"F2.wireOp",EDGE,"E25.0.6.62")}),-1.0]])]});
            var Q780;
            Q780=makeQuery(id+"F2.imprint","IMPRINT",FACE,{"disambiguationData":[TD([[makeQuery(id+"F2.imprint","IMPRINT",EDGE,{"derivedFrom":sQuery(id+"F2.wireOp",EDGE,"E25.0.6.32")}),-1.0]])]});
            var Q781;
            Q781=makeQuery(id+"F2.imprint","IMPRINT",FACE,{"disambiguationData":[TD([[makeQuery(id+"F2.imprint","IMPRINT",EDGE,{"derivedFrom":sQuery(id+"F2.wireOp",EDGE,"E25.0.6.13")}),1.0]])]});
            var Q782;
            Q782=makeQuery(id+"F2.imprint","IMPRINT",FACE,{"disambiguationData":[TD([[makeQuery(id+"F2.imprint","IMPRINT",EDGE,{"derivedFrom":sQuery(id+"F2.wireOp",EDGE,"E25.0.6.12")}),-1.0]])]});
            extrude(context, id + "F3", {"entities" : qUnion([Q0, Q1, Q2, Q3, Q4, Q5, Q6, Q7, Q8, Q9, Q10, Q11, Q12, Q13, Q14, Q15, Q16, Q17, Q18, Q19, Q20, Q21, Q22, Q23, Q24, Q25, Q26, Q27, Q28, Q29, Q30, Q31, Q32, Q33, Q34, Q35, Q36, Q37, Q38, Q39, Q40, Q41, Q42, Q43, Q44, Q45, Q46, Q47, Q48, Q49, Q50, Q51, Q52, Q53, Q54, Q55, Q56, Q57, Q58, Q59, Q60, Q61, Q62, Q63, Q64, Q65, Q66, Q67, Q68, Q69, Q70, Q71, Q72, Q73, Q74, Q75, Q76, Q77, Q78, Q79, Q80, Q81, Q82, Q83, Q84, Q85, Q86, Q87, Q88, Q89, Q90, Q91, Q92, Q93, Q94, Q95, Q96, Q97, Q98, Q99, Q100, Q101, Q102, Q103, Q104, Q105, Q106, Q107, Q108, Q109, Q110, Q111, Q112, Q113, Q114, Q115, Q116, Q117, Q118, Q119, Q120, Q121, Q122, Q123, Q124, Q125, Q126, Q127, Q128, Q129, Q130, Q131, Q132, Q133, Q134, Q135, Q136, Q137, Q138, Q139, Q140, Q141, Q142, Q143, Q144, Q145, Q146, Q147, Q148, Q149, Q150, Q151, Q152, Q153, Q154, Q155, Q156, Q157, Q158, Q159, Q160, Q161, Q162, Q163, Q164, Q165, Q166, Q167, Q168, Q169, Q170, Q171, Q172, Q173, Q174, Q175, Q176, Q177, Q178, Q179, Q180, Q181, Q182, Q183, Q184, Q185, Q186, Q187, Q188, Q189, Q190, Q191, Q192, Q193, Q194, Q195, Q196, Q197, Q198, Q199, Q200, Q201, Q202, Q203, Q204, Q205, Q206, Q207, Q208, Q209, Q210, Q211, Q212, Q213, Q214, Q215, Q216, Q217, Q218, Q219, Q220, Q221, Q222, Q223, Q224, Q225, Q226, Q227, Q228, Q229, Q230, Q231, Q232, Q233, Q234, Q235, Q236, Q237, Q238, Q239, Q240, Q241, Q242, Q243, Q244, Q245, Q246, Q247, Q248, Q249, Q250, Q251, Q252, Q253, Q254, Q255, Q256, Q257, Q258, Q259, Q260, Q261, Q262, Q263, Q264, Q265, Q266, Q267, Q268, Q269, Q270, Q271, Q272, Q273, Q274, Q275, Q276, Q277, Q278, Q279, Q280, Q281, Q282, Q283, Q284, Q285, Q286, Q287, Q288, Q289, Q290, Q291, Q292, Q293, Q294, Q295, Q296, Q297, Q298, Q299, Q300, Q301, Q302, Q303, Q304, Q305, Q306, Q307, Q308, Q309, Q310, Q311, Q312, Q313, Q314, Q315, Q316, Q317, Q318, Q319, Q320, Q321, Q322, Q323, Q324, Q325, Q326, Q327, Q328, Q329, Q330, Q331, Q332, Q333, Q334, Q335, Q336, Q337, Q338, Q339, Q340, Q341, Q342, Q343, Q344, Q345, Q346, Q347, Q348, Q349, Q350, Q351, Q352, Q353, Q354, Q355, Q356, Q357, Q358, Q359, Q360, Q361, Q362, Q363, Q364, Q365, Q366, Q367, Q368, Q369, Q370, Q371, Q372, Q373, Q374, Q375, Q376, Q377, Q378, Q379, Q380, Q381, Q382, Q383, Q384, Q385, Q386, Q387, Q388, Q389, Q390, Q391, Q392, Q393, Q394, Q395, Q396, Q397, Q398, Q399, Q400, Q401, Q402, Q403, Q404, Q405, Q406, Q407, Q408, Q409, Q410, Q411, Q412, Q413, Q414, Q415, Q416, Q417, Q418, Q419, Q420, Q421, Q422, Q423, Q424, Q425, Q426, Q427, Q428, Q429, Q430, Q431, Q432, Q433, Q434, Q435, Q436, Q437, Q438, Q439, Q440, Q441, Q442, Q443, Q444, Q445, Q446, Q447, Q448, Q449, Q450, Q451, Q452, Q453, Q454, Q455, Q456, Q457, Q458, Q459, Q460, Q461, Q462, Q463, Q464, Q465, Q466, Q467, Q468, Q469, Q470, Q471, Q472, Q473, Q474, Q475, Q476, Q477, Q478, Q479, Q480, Q481, Q482, Q483, Q484, Q485, Q486, Q487, Q488, Q489, Q490, Q491, Q492, Q493, Q494, Q495, Q496, Q497, Q498, Q499, Q500, Q501, Q502, Q503, Q504, Q505, Q506, Q507, Q508, Q509, Q510, Q511, Q512, Q513, Q514, Q515, Q516, Q517, Q518, Q519, Q520, Q521, Q522, Q523, Q524, Q525, Q526, Q527, Q528, Q529, Q530, Q531, Q532, Q533, Q534, Q535, Q536, Q537, Q538, Q539, Q540, Q541, Q542, Q543, Q544, Q545, Q546, Q547, Q548, Q549, Q550, Q551, Q552, Q553, Q554, Q555, Q556, Q557, Q558, Q559, Q560, Q561, Q562, Q563, Q564, Q565, Q566, Q567, Q568, Q569, Q570, Q571, Q572, Q573, Q574, Q575, Q576, Q577, Q578, Q579, Q580, Q581, Q582, Q583, Q584, Q585, Q586, Q587, Q588, Q589, Q590, Q591, Q592, Q593, Q594, Q595, Q596, Q597, Q598, Q599, Q600, Q601, Q602, Q603, Q604, Q605, Q606, Q607, Q608, Q609, Q610, Q611, Q612, Q613, Q614, Q615, Q616, Q617, Q618, Q619, Q620, Q621, Q622, Q623, Q624, Q625, Q626, Q627, Q628, Q629, Q630, Q631, Q632, Q633, Q634, Q635, Q636, Q637, Q638, Q639, Q640, Q641, Q642, Q643, Q644, Q645, Q646, Q647, Q648, Q649, Q650, Q651, Q652, Q653, Q654, Q655, Q656, Q657, Q658, Q659, Q660, Q661, Q662, Q663, Q664, Q665, Q666, Q667, Q668, Q669, Q670, Q671, Q672, Q673, Q674, Q675, Q676, Q677, Q678, Q679, Q680, Q681, Q682, Q683, Q684, Q685, Q686, Q687, Q688, Q689, Q690, Q691, Q692, Q693, Q694, Q695, Q696, Q697, Q698, Q699, Q700, Q701, Q702, Q703, Q704, Q705, Q706, Q707, Q708, Q709, Q710, Q711, Q712, Q713, Q714, Q715, Q716, Q717, Q718, Q719, Q720, Q721, Q722, Q723, Q724, Q725, Q726, Q727, Q728, Q729, Q730, Q731, Q732, Q733, Q734, Q735, Q736, Q737, Q738, Q739, Q740, Q741, Q742, Q743, Q744, Q745, Q746, Q747, Q748, Q749, Q750, Q751, Q752, Q753, Q754, Q755, Q756, Q757, Q758, Q759, Q760, Q761, Q762, Q763, Q764, Q765, Q766, Q767, Q768, Q769, Q770, Q771, Q772, Q773, Q774, Q775, Q776, Q777, Q778, Q779, Q780, Q781, Q782]), "operationType" : NewBodyOperationType.REMOVE, "oppositeDirection" : true, "depth" : 25 * mm, "offsetDistance" : 25 * mm});
        }
    });
